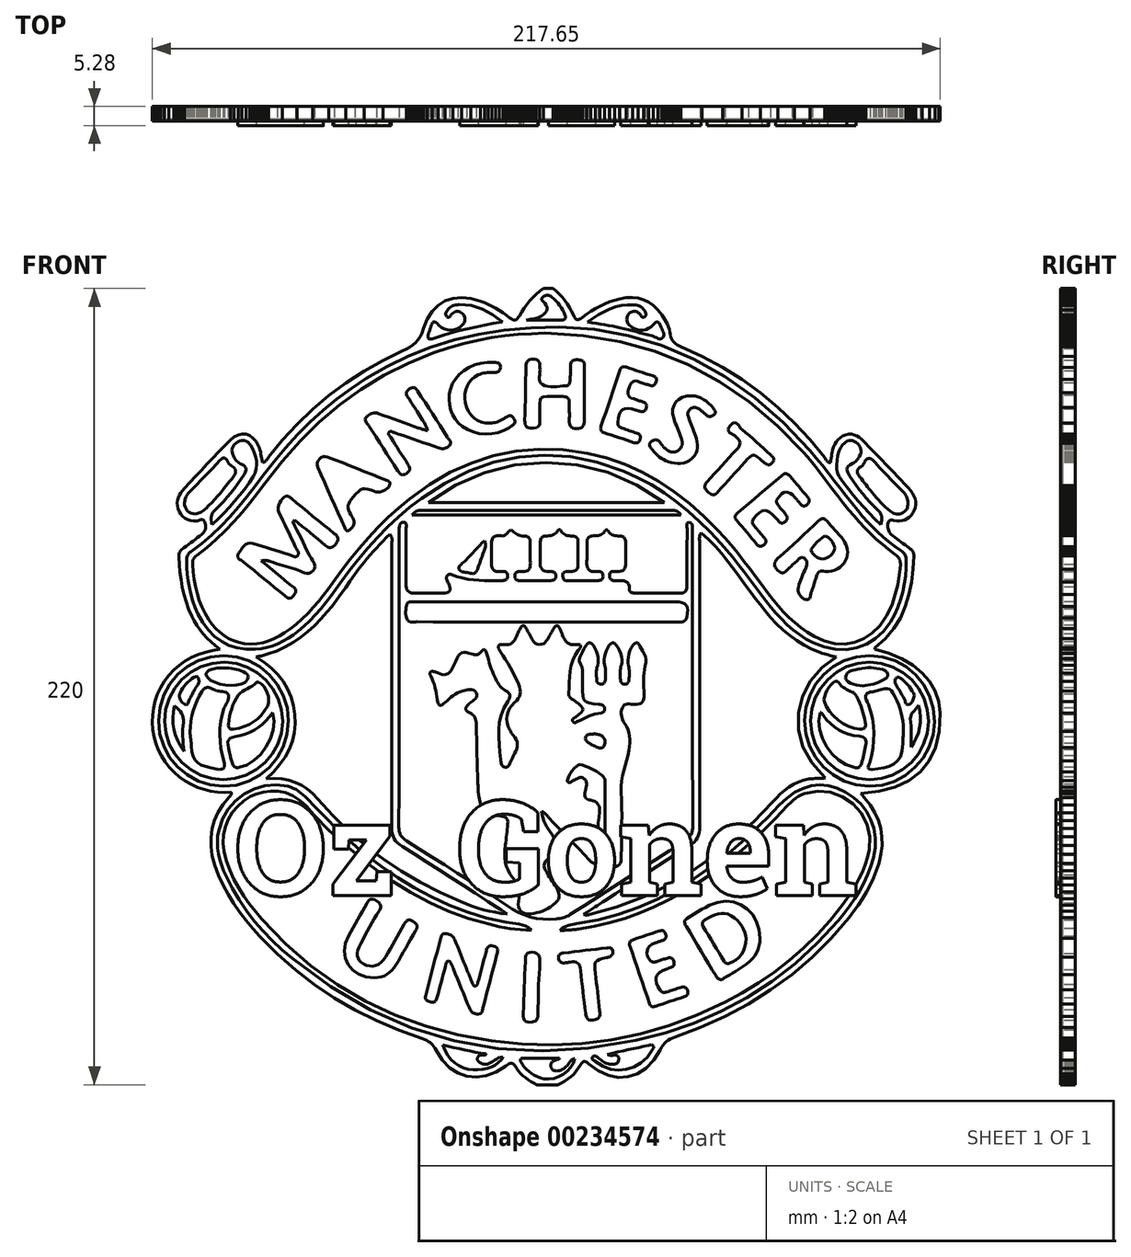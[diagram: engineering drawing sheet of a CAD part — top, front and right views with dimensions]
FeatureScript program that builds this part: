
annotation { "Feature Type Name" : "Feature", "Feature Type Description" : "" }
export const myFeature = defineFeature(function(context is Context, id is Id, definition is map)
    precondition{}
    {
        {
            var Q0;
            Q0=qCreatedBy(makeId("Front.planeOp"),FACE);
            var sketch = newSketch(context, id + "F0", { "sketchPlane" : qUnion([Q0])});
            skLineSegment(sketch, "E0", {"start": v(-1.82, 250) * mm, "end": v(-1.07, 250) * mm});
            skLineSegment(sketch, "E1", {"start": v(-1.07, 250) * mm, "end": v(-0.32, 250) * mm});
            skLineSegment(sketch, "E2", {"start": v(-0.32, 250) * mm, "end": v(0.43, 250) * mm});
            skLineSegment(sketch, "E3", {"start": v(0.43, 250) * mm, "end": v(1.18, 250) * mm});
            skLineSegment(sketch, "E4", {"start": v(1.18, 250) * mm, "end": v(1.93, 250) * mm});
            skLineSegment(sketch, "E5", {"start": v(1.93, 250) * mm, "end": v(2.68, 250) * mm});
            skLineSegment(sketch, "E6", {"start": v(2.68, 250) * mm, "end": v(3.43, 250) * mm});
            skLineSegment(sketch, "E7", {"start": v(3.43, 250) * mm, "end": v(4.18, 250) * mm});
            skLineSegment(sketch, "E8", {"start": v(4.18, 250) * mm, "end": v(6.35, 248.32) * mm});
            skLineSegment(sketch, "E9", {"start": v(6.35, 248.32) * mm, "end": v(8.32, 246.48) * mm});
            skLineSegment(sketch, "E10", {"start": v(8.32, 246.48) * mm, "end": v(10.12, 244.5) * mm});
            skLineSegment(sketch, "E11", {"start": v(10.12, 244.5) * mm, "end": v(11.75, 242.4) * mm});
            skLineSegment(sketch, "E12", {"start": v(11.75, 242.4) * mm, "end": v(13.25, 240.2) * mm});
            skLineSegment(sketch, "E13", {"start": v(13.25, 240.2) * mm, "end": v(14.63, 237.9) * mm});
            skLineSegment(sketch, "E14", {"start": v(14.63, 237.9) * mm, "end": v(15.91, 235.55) * mm});
            skLineSegment(sketch, "E15", {"start": v(15.91, 235.55) * mm, "end": v(17.11, 233.14) * mm});
            skLineSegment(sketch, "E16", {"start": v(17.11, 233.14) * mm, "end": v(17.67, 232.1) * mm});
            skLineSegment(sketch, "E17", {"start": v(17.67, 232.1) * mm, "end": v(18.22, 231.32) * mm});
            skLineSegment(sketch, "E18", {"start": v(18.22, 231.32) * mm, "end": v(18.8, 230.79) * mm});
            skLineSegment(sketch, "E19", {"start": v(18.8, 230.79) * mm, "end": v(19.4, 230.51) * mm});
            skLineSegment(sketch, "E20", {"start": v(19.4, 230.51) * mm, "end": v(20.07, 230.48) * mm});
            skLineSegment(sketch, "E21", {"start": v(20.07, 230.48) * mm, "end": v(20.82, 230.69) * mm});
            skLineSegment(sketch, "E22", {"start": v(20.82, 230.69) * mm, "end": v(21.66, 231.13) * mm});
            skLineSegment(sketch, "E23", {"start": v(21.66, 231.13) * mm, "end": v(22.63, 231.81) * mm});
            skLineSegment(sketch, "E24", {"start": v(22.63, 231.81) * mm, "end": v(25.3, 233.8) * mm});
            skLineSegment(sketch, "E25", {"start": v(25.3, 233.8) * mm, "end": v(28.03, 235.66) * mm});
            skLineSegment(sketch, "E26", {"start": v(28.03, 235.66) * mm, "end": v(30.83, 237.4) * mm});
            skLineSegment(sketch, "E27", {"start": v(30.83, 237.4) * mm, "end": v(33.7, 238.99) * mm});
            skLineSegment(sketch, "E28", {"start": v(33.7, 238.99) * mm, "end": v(36.67, 240.41) * mm});
            skLineSegment(sketch, "E29", {"start": v(36.67, 240.41) * mm, "end": v(39.72, 241.66) * mm});
            skLineSegment(sketch, "E30", {"start": v(39.72, 241.66) * mm, "end": v(42.86, 242.73) * mm});
            skLineSegment(sketch, "E31", {"start": v(42.86, 242.73) * mm, "end": v(46.1, 243.6) * mm});
            skLineSegment(sketch, "E32", {"start": v(46.1, 243.6) * mm, "end": v(50.2, 244.27) * mm});
            skLineSegment(sketch, "E33", {"start": v(50.2, 244.27) * mm, "end": v(54.05, 244.4) * mm});
            skLineSegment(sketch, "E34", {"start": v(54.05, 244.4) * mm, "end": v(57.69, 243.97) * mm});
            skLineSegment(sketch, "E35", {"start": v(57.69, 243.97) * mm, "end": v(61.1, 242.98) * mm});
            skLineSegment(sketch, "E36", {"start": v(61.1, 242.98) * mm, "end": v(64.3, 241.43) * mm});
            skLineSegment(sketch, "E37", {"start": v(64.3, 241.43) * mm, "end": v(67.3, 239.32) * mm});
            skLineSegment(sketch, "E38", {"start": v(67.3, 239.32) * mm, "end": v(70.08, 236.64) * mm});
            skLineSegment(sketch, "E39", {"start": v(70.08, 236.64) * mm, "end": v(72.65, 233.4) * mm});
            skLineSegment(sketch, "E40", {"start": v(72.65, 233.4) * mm, "end": v(73.61, 231.98) * mm});
            skLineSegment(sketch, "E41", {"start": v(73.61, 231.98) * mm, "end": v(74.51, 230.53) * mm});
            skLineSegment(sketch, "E42", {"start": v(74.51, 230.53) * mm, "end": v(75.34, 229.04) * mm});
            skLineSegment(sketch, "E43", {"start": v(75.34, 229.04) * mm, "end": v(76.07, 227.52) * mm});
            skLineSegment(sketch, "E44", {"start": v(76.07, 227.52) * mm, "end": v(76.71, 225.97) * mm});
            skLineSegment(sketch, "E45", {"start": v(76.71, 225.97) * mm, "end": v(77.24, 224.38) * mm});
            skLineSegment(sketch, "E46", {"start": v(77.24, 224.38) * mm, "end": v(77.65, 222.76) * mm});
            skLineSegment(sketch, "E47", {"start": v(77.65, 222.76) * mm, "end": v(77.92, 221.1) * mm});
            skLineSegment(sketch, "E48", {"start": v(77.92, 221.1) * mm, "end": v(78.2, 219.57) * mm});
            skLineSegment(sketch, "E49", {"start": v(78.2, 219.57) * mm, "end": v(78.67, 218.27) * mm});
            skLineSegment(sketch, "E50", {"start": v(78.67, 218.27) * mm, "end": v(79.3, 217.16) * mm});
            skLineSegment(sketch, "E51", {"start": v(79.3, 217.16) * mm, "end": v(80.08, 216.22) * mm});
            skLineSegment(sketch, "E52", {"start": v(80.08, 216.22) * mm, "end": v(81.01, 215.41) * mm});
            skLineSegment(sketch, "E53", {"start": v(81.01, 215.41) * mm, "end": v(82.08, 214.71) * mm});
            skLineSegment(sketch, "E54", {"start": v(82.08, 214.71) * mm, "end": v(83.27, 214.09) * mm});
            skLineSegment(sketch, "E55", {"start": v(83.27, 214.09) * mm, "end": v(84.58, 213.5) * mm});
            skLineSegment(sketch, "E56", {"start": v(84.58, 213.5) * mm, "end": v(97.9, 207.43) * mm});
            skLineSegment(sketch, "E57", {"start": v(97.9, 207.43) * mm, "end": v(110.63, 200.58) * mm});
            skLineSegment(sketch, "E58", {"start": v(110.63, 200.58) * mm, "end": v(122.77, 192.97) * mm});
            skLineSegment(sketch, "E59", {"start": v(122.77, 192.97) * mm, "end": v(134.34, 184.6) * mm});
            skLineSegment(sketch, "E60", {"start": v(134.34, 184.6) * mm, "end": v(145.32, 175.49) * mm});
            skLineSegment(sketch, "E61", {"start": v(145.32, 175.49) * mm, "end": v(155.74, 165.64) * mm});
            skLineSegment(sketch, "E62", {"start": v(155.74, 165.64) * mm, "end": v(165.59, 155.05) * mm});
            skLineSegment(sketch, "E63", {"start": v(165.59, 155.05) * mm, "end": v(174.88, 143.75) * mm});
            skLineSegment(sketch, "E64", {"start": v(174.88, 143.75) * mm, "end": v(175.21, 143.27) * mm});
            skLineSegment(sketch, "E65", {"start": v(175.21, 143.27) * mm, "end": v(175.52, 142.76) * mm});
            skLineSegment(sketch, "E66", {"start": v(175.52, 142.76) * mm, "end": v(175.85, 142.25) * mm});
            skLineSegment(sketch, "E67", {"start": v(175.85, 142.25) * mm, "end": v(176.2, 141.77) * mm});
            skLineSegment(sketch, "E68", {"start": v(176.2, 141.77) * mm, "end": v(176.63, 141.35) * mm});
            skLineSegment(sketch, "E69", {"start": v(176.63, 141.35) * mm, "end": v(177.14, 141.03) * mm});
            skLineSegment(sketch, "E70", {"start": v(177.14, 141.03) * mm, "end": v(177.77, 140.85) * mm});
            skLineSegment(sketch, "E71", {"start": v(177.77, 140.85) * mm, "end": v(178.54, 140.82) * mm});
            skLineSegment(sketch, "E72", {"start": v(178.54, 140.82) * mm, "end": v(178.65, 141.59) * mm});
            skLineSegment(sketch, "E73", {"start": v(178.65, 141.59) * mm, "end": v(178.74, 142.34) * mm});
            skLineSegment(sketch, "E74", {"start": v(178.74, 142.34) * mm, "end": v(178.84, 143.1) * mm});
            skLineSegment(sketch, "E75", {"start": v(178.84, 143.1) * mm, "end": v(178.94, 143.84) * mm});
            skLineSegment(sketch, "E76", {"start": v(178.94, 143.84) * mm, "end": v(179.04, 144.58) * mm});
            skLineSegment(sketch, "E77", {"start": v(179.04, 144.58) * mm, "end": v(179.16, 145.32) * mm});
            skLineSegment(sketch, "E78", {"start": v(179.16, 145.32) * mm, "end": v(179.28, 146.05) * mm});
            skLineSegment(sketch, "E79", {"start": v(179.28, 146.05) * mm, "end": v(179.43, 146.78) * mm});
            skLineSegment(sketch, "E80", {"start": v(179.43, 146.78) * mm, "end": v(179.89, 148.67) * mm});
            skLineSegment(sketch, "E81", {"start": v(179.89, 148.67) * mm, "end": v(180.47, 150.48) * mm});
            skLineSegment(sketch, "E82", {"start": v(180.47, 150.48) * mm, "end": v(181.2, 152.19) * mm});
            skLineSegment(sketch, "E83", {"start": v(181.2, 152.19) * mm, "end": v(182.1, 153.77) * mm});
            skLineSegment(sketch, "E84", {"start": v(182.1, 153.77) * mm, "end": v(183.2, 155.18) * mm});
            skLineSegment(sketch, "E85", {"start": v(183.2, 155.18) * mm, "end": v(184.54, 156.4) * mm});
            skLineSegment(sketch, "E86", {"start": v(184.54, 156.4) * mm, "end": v(186.12, 157.4) * mm});
            skLineSegment(sketch, "E87", {"start": v(186.12, 157.4) * mm, "end": v(187.99, 158.16) * mm});
            skLineSegment(sketch, "E88", {"start": v(187.99, 158.16) * mm, "end": v(189.94, 158.56) * mm});
            skLineSegment(sketch, "E89", {"start": v(189.94, 158.56) * mm, "end": v(191.75, 158.54) * mm});
            skLineSegment(sketch, "E90", {"start": v(191.75, 158.54) * mm, "end": v(193.43, 158.17) * mm});
            skLineSegment(sketch, "E91", {"start": v(193.43, 158.17) * mm, "end": v(195, 157.5) * mm});
            skLineSegment(sketch, "E92", {"start": v(195, 157.5) * mm, "end": v(196.48, 156.57) * mm});
            skLineSegment(sketch, "E93", {"start": v(196.48, 156.57) * mm, "end": v(197.88, 155.44) * mm});
            skLineSegment(sketch, "E94", {"start": v(197.88, 155.44) * mm, "end": v(199.23, 154.18) * mm});
            skLineSegment(sketch, "E95", {"start": v(199.23, 154.18) * mm, "end": v(200.53, 152.83) * mm});
            skLineSegment(sketch, "E96", {"start": v(200.53, 152.83) * mm, "end": v(202.6, 150.65) * mm});
            skLineSegment(sketch, "E97", {"start": v(202.6, 150.65) * mm, "end": v(204.66, 148.48) * mm});
            skLineSegment(sketch, "E98", {"start": v(204.66, 148.48) * mm, "end": v(206.74, 146.32) * mm});
            skLineSegment(sketch, "E99", {"start": v(206.74, 146.32) * mm, "end": v(208.83, 144.17) * mm});
            skLineSegment(sketch, "E100", {"start": v(208.83, 144.17) * mm, "end": v(210.92, 142.01) * mm});
            skLineSegment(sketch, "E101", {"start": v(210.92, 142.01) * mm, "end": v(213, 139.86) * mm});
            skLineSegment(sketch, "E102", {"start": v(213, 139.86) * mm, "end": v(215.09, 137.7) * mm});
            skLineSegment(sketch, "E103", {"start": v(215.09, 137.7) * mm, "end": v(217.16, 135.54) * mm});
            skLineSegment(sketch, "E104", {"start": v(217.16, 135.54) * mm, "end": v(218.63, 134) * mm});
            skLineSegment(sketch, "E105", {"start": v(218.63, 134) * mm, "end": v(220.1, 132.47) * mm});
            skLineSegment(sketch, "E106", {"start": v(220.1, 132.47) * mm, "end": v(221.57, 130.93) * mm});
            skLineSegment(sketch, "E107", {"start": v(221.57, 130.93) * mm, "end": v(223.03, 129.4) * mm});
            skLineSegment(sketch, "E108", {"start": v(223.03, 129.4) * mm, "end": v(224.48, 127.84) * mm});
            skLineSegment(sketch, "E109", {"start": v(224.48, 127.84) * mm, "end": v(225.92, 126.28) * mm});
            skLineSegment(sketch, "E110", {"start": v(225.92, 126.28) * mm, "end": v(227.33, 124.7) * mm});
            skLineSegment(sketch, "E111", {"start": v(227.33, 124.7) * mm, "end": v(228.73, 123.1) * mm});
            skLineSegment(sketch, "E112", {"start": v(228.73, 123.1) * mm, "end": v(229.98, 121.42) * mm});
            skLineSegment(sketch, "E113", {"start": v(229.98, 121.42) * mm, "end": v(230.93, 119.68) * mm});
            skLineSegment(sketch, "E114", {"start": v(230.93, 119.68) * mm, "end": v(231.58, 117.9) * mm});
            skLineSegment(sketch, "E115", {"start": v(231.58, 117.9) * mm, "end": v(231.93, 116.11) * mm});
            skLineSegment(sketch, "E116", {"start": v(231.93, 116.11) * mm, "end": v(231.98, 114.32) * mm});
            skLineSegment(sketch, "E117", {"start": v(231.98, 114.32) * mm, "end": v(231.73, 112.56) * mm});
            skLineSegment(sketch, "E118", {"start": v(231.73, 112.56) * mm, "end": v(231.19, 110.84) * mm});
            skLineSegment(sketch, "E119", {"start": v(231.19, 110.84) * mm, "end": v(230.34, 109.18) * mm});
            skLineSegment(sketch, "E120", {"start": v(230.34, 109.18) * mm, "end": v(229.23, 107.63) * mm});
            skLineSegment(sketch, "E121", {"start": v(229.23, 107.63) * mm, "end": v(228, 106.36) * mm});
            skLineSegment(sketch, "E122", {"start": v(228, 106.36) * mm, "end": v(226.63, 105.37) * mm});
            skLineSegment(sketch, "E123", {"start": v(226.63, 105.37) * mm, "end": v(225.16, 104.65) * mm});
            skLineSegment(sketch, "E124", {"start": v(225.16, 104.65) * mm, "end": v(223.58, 104.2) * mm});
            skLineSegment(sketch, "E125", {"start": v(223.58, 104.2) * mm, "end": v(221.9, 104.02) * mm});
            skLineSegment(sketch, "E126", {"start": v(221.9, 104.02) * mm, "end": v(220.13, 104.1) * mm});
            skLineSegment(sketch, "E127", {"start": v(220.13, 104.1) * mm, "end": v(218.28, 104.43) * mm});
            skLineSegment(sketch, "E128", {"start": v(218.28, 104.43) * mm, "end": v(217.24, 104.62) * mm});
            skLineSegment(sketch, "E129", {"start": v(217.24, 104.62) * mm, "end": v(216.4, 104.63) * mm});
            skLineSegment(sketch, "E130", {"start": v(216.4, 104.63) * mm, "end": v(215.74, 104.47) * mm});
            skLineSegment(sketch, "E131", {"start": v(215.74, 104.47) * mm, "end": v(215.24, 104.14) * mm});
            skLineSegment(sketch, "E132", {"start": v(215.24, 104.14) * mm, "end": v(214.87, 103.64) * mm});
            skLineSegment(sketch, "E133", {"start": v(214.87, 103.64) * mm, "end": v(214.63, 102.98) * mm});
            skLineSegment(sketch, "E134", {"start": v(214.63, 102.98) * mm, "end": v(214.5, 102.15) * mm});
            skLineSegment(sketch, "E135", {"start": v(214.5, 102.15) * mm, "end": v(214.46, 101.17) * mm});
            skLineSegment(sketch, "E136", {"start": v(214.46, 101.17) * mm, "end": v(214.5, 100.17) * mm});
            skLineSegment(sketch, "E137", {"start": v(214.5, 100.17) * mm, "end": v(214.63, 99.22) * mm});
            skLineSegment(sketch, "E138", {"start": v(214.63, 99.22) * mm, "end": v(214.86, 98.34) * mm});
            skLineSegment(sketch, "E139", {"start": v(214.86, 98.34) * mm, "end": v(215.19, 97.52) * mm});
            skLineSegment(sketch, "E140", {"start": v(215.19, 97.52) * mm, "end": v(215.62, 96.75) * mm});
            skLineSegment(sketch, "E141", {"start": v(215.62, 96.75) * mm, "end": v(216.16, 96.03) * mm});
            skLineSegment(sketch, "E142", {"start": v(216.16, 96.03) * mm, "end": v(216.8, 95.36) * mm});
            skLineSegment(sketch, "E143", {"start": v(216.8, 95.36) * mm, "end": v(217.56, 94.74) * mm});
            skLineSegment(sketch, "E144", {"start": v(217.56, 94.74) * mm, "end": v(218.86, 93.78) * mm});
            skLineSegment(sketch, "E145", {"start": v(218.86, 93.78) * mm, "end": v(220.16, 92.8) * mm});
            skLineSegment(sketch, "E146", {"start": v(220.16, 92.8) * mm, "end": v(221.46, 91.83) * mm});
            skLineSegment(sketch, "E147", {"start": v(221.46, 91.83) * mm, "end": v(222.76, 90.86) * mm});
            skLineSegment(sketch, "E148", {"start": v(222.76, 90.86) * mm, "end": v(224.07, 89.9) * mm});
            skLineSegment(sketch, "E149", {"start": v(224.07, 89.9) * mm, "end": v(225.38, 88.93) * mm});
            skLineSegment(sketch, "E150", {"start": v(225.38, 88.93) * mm, "end": v(226.7, 87.98) * mm});
            skLineSegment(sketch, "E151", {"start": v(226.7, 87.98) * mm, "end": v(228.02, 87.04) * mm});
            skLineSegment(sketch, "E152", {"start": v(228.02, 87.04) * mm, "end": v(228.65, 86.57) * mm});
            skLineSegment(sketch, "E153", {"start": v(228.65, 86.57) * mm, "end": v(229.21, 86.07) * mm});
            skLineSegment(sketch, "E154", {"start": v(229.21, 86.07) * mm, "end": v(229.7, 85.54) * mm});
            skLineSegment(sketch, "E155", {"start": v(229.7, 85.54) * mm, "end": v(230.1, 84.98) * mm});
            skLineSegment(sketch, "E156", {"start": v(230.1, 84.98) * mm, "end": v(230.42, 84.36) * mm});
            skLineSegment(sketch, "E157", {"start": v(230.42, 84.36) * mm, "end": v(230.65, 83.69) * mm});
            skLineSegment(sketch, "E158", {"start": v(230.65, 83.69) * mm, "end": v(230.77, 82.95) * mm});
            skLineSegment(sketch, "E159", {"start": v(230.77, 82.95) * mm, "end": v(230.8, 82.13) * mm});
            skLineSegment(sketch, "E160", {"start": v(230.8, 82.13) * mm, "end": v(230.27, 73.86) * mm});
            skLineSegment(sketch, "E161", {"start": v(230.27, 73.86) * mm, "end": v(229.3, 65.78) * mm});
            skLineSegment(sketch, "E162", {"start": v(229.3, 65.78) * mm, "end": v(227.74, 57.94) * mm});
            skLineSegment(sketch, "E163", {"start": v(227.74, 57.94) * mm, "end": v(225.46, 50.41) * mm});
            skLineSegment(sketch, "E164", {"start": v(225.46, 50.41) * mm, "end": v(222.33, 43.24) * mm});
            skLineSegment(sketch, "E165", {"start": v(222.33, 43.24) * mm, "end": v(218.2, 36.5) * mm});
            skLineSegment(sketch, "E166", {"start": v(218.2, 36.5) * mm, "end": v(212.95, 30.22) * mm});
            skLineSegment(sketch, "E167", {"start": v(212.95, 30.22) * mm, "end": v(206.43, 24.48) * mm});
            skLineSegment(sketch, "E168", {"start": v(206.43, 24.48) * mm, "end": v(206.4, 24.42) * mm});
            skLineSegment(sketch, "E169", {"start": v(206.4, 24.42) * mm, "end": v(206.37, 24.33) * mm});
            skLineSegment(sketch, "E170", {"start": v(206.37, 24.33) * mm, "end": v(206.36, 24.23) * mm});
            skLineSegment(sketch, "E171", {"start": v(206.36, 24.23) * mm, "end": v(206.37, 24.1) * mm});
            skLineSegment(sketch, "E172", {"start": v(206.37, 24.1) * mm, "end": v(206.38, 23.97) * mm});
            skLineSegment(sketch, "E173", {"start": v(206.38, 23.97) * mm, "end": v(206.4, 23.84) * mm});
            skLineSegment(sketch, "E174", {"start": v(206.4, 23.84) * mm, "end": v(206.41, 23.7) * mm});
            skLineSegment(sketch, "E175", {"start": v(206.41, 23.7) * mm, "end": v(206.42, 23.59) * mm});
            skLineSegment(sketch, "E176", {"start": v(206.42, 23.59) * mm, "end": v(215.37, 20.89) * mm});
            skLineSegment(sketch, "E177", {"start": v(215.37, 20.89) * mm, "end": v(223.34, 17.47) * mm});
            skLineSegment(sketch, "E178", {"start": v(223.34, 17.47) * mm, "end": v(230.25, 13.37) * mm});
            skLineSegment(sketch, "E179", {"start": v(230.25, 13.37) * mm, "end": v(236.07, 8.6) * mm});
            skLineSegment(sketch, "E180", {"start": v(236.07, 8.6) * mm, "end": v(240.74, 3.21) * mm});
            skLineSegment(sketch, "E181", {"start": v(240.74, 3.21) * mm, "end": v(244.21, -2.78) * mm});
            skLineSegment(sketch, "E182", {"start": v(244.21, -2.78) * mm, "end": v(246.42, -9.36) * mm});
            skLineSegment(sketch, "E183", {"start": v(246.42, -9.36) * mm, "end": v(247.33, -16.48) * mm});
            skLineSegment(sketch, "E184", {"start": v(247.33, -16.48) * mm, "end": v(246.81, -28.2) * mm});
            skLineSegment(sketch, "E185", {"start": v(246.81, -28.2) * mm, "end": v(244.5, -38.26) * mm});
            skLineSegment(sketch, "E186", {"start": v(244.5, -38.26) * mm, "end": v(240.48, -46.7) * mm});
            skLineSegment(sketch, "E187", {"start": v(240.48, -46.7) * mm, "end": v(234.83, -53.6) * mm});
            skLineSegment(sketch, "E188", {"start": v(234.83, -53.6) * mm, "end": v(227.62, -59.01) * mm});
            skLineSegment(sketch, "E189", {"start": v(227.62, -59.01) * mm, "end": v(218.93, -63) * mm});
            skLineSegment(sketch, "E190", {"start": v(218.93, -63) * mm, "end": v(208.85, -65.66) * mm});
            skLineSegment(sketch, "E191", {"start": v(208.85, -65.66) * mm, "end": v(197.45, -67.02) * mm});
            skLineSegment(sketch, "E192", {"start": v(197.45, -67.02) * mm, "end": v(197.8, -67.44) * mm});
            skLineSegment(sketch, "E193", {"start": v(197.8, -67.44) * mm, "end": v(198.13, -67.83) * mm});
            skLineSegment(sketch, "E194", {"start": v(198.13, -67.83) * mm, "end": v(198.43, -68.19) * mm});
            skLineSegment(sketch, "E195", {"start": v(198.43, -68.19) * mm, "end": v(198.72, -68.52) * mm});
            skLineSegment(sketch, "E196", {"start": v(198.72, -68.52) * mm, "end": v(198.98, -68.83) * mm});
            skLineSegment(sketch, "E197", {"start": v(198.98, -68.83) * mm, "end": v(199.23, -69.12) * mm});
            skLineSegment(sketch, "E198", {"start": v(199.23, -69.12) * mm, "end": v(199.48, -69.4) * mm});
            skLineSegment(sketch, "E199", {"start": v(199.48, -69.4) * mm, "end": v(199.72, -69.69) * mm});
            skLineSegment(sketch, "E200", {"start": v(199.72, -69.69) * mm, "end": v(203.35, -74.31) * mm});
            skLineSegment(sketch, "E201", {"start": v(203.35, -74.31) * mm, "end": v(206.27, -79.1) * mm});
            skLineSegment(sketch, "E202", {"start": v(206.27, -79.1) * mm, "end": v(208.5, -84.03) * mm});
            skLineSegment(sketch, "E203", {"start": v(208.5, -84.03) * mm, "end": v(210, -89.12) * mm});
            skLineSegment(sketch, "E204", {"start": v(210, -89.12) * mm, "end": v(210.79, -94.36) * mm});
            skLineSegment(sketch, "E205", {"start": v(210.79, -94.36) * mm, "end": v(210.85, -99.77) * mm});
            skLineSegment(sketch, "E206", {"start": v(210.85, -99.77) * mm, "end": v(210.17, -105.33) * mm});
            skLineSegment(sketch, "E207", {"start": v(210.17, -105.33) * mm, "end": v(208.76, -111.06) * mm});
            skLineSegment(sketch, "E208", {"start": v(208.76, -111.06) * mm, "end": v(207.18, -115.72) * mm});
            skLineSegment(sketch, "E209", {"start": v(207.18, -115.72) * mm, "end": v(205.34, -120.24) * mm});
            skLineSegment(sketch, "E210", {"start": v(205.34, -120.24) * mm, "end": v(203.28, -124.64) * mm});
            skLineSegment(sketch, "E211", {"start": v(203.28, -124.64) * mm, "end": v(201, -128.92) * mm});
            skLineSegment(sketch, "E212", {"start": v(201, -128.92) * mm, "end": v(198.52, -133.1) * mm});
            skLineSegment(sketch, "E213", {"start": v(198.52, -133.1) * mm, "end": v(195.86, -137.16) * mm});
            skLineSegment(sketch, "E214", {"start": v(195.86, -137.16) * mm, "end": v(193.03, -141.13) * mm});
            skLineSegment(sketch, "E215", {"start": v(193.03, -141.13) * mm, "end": v(190.05, -145) * mm});
            skLineSegment(sketch, "E216", {"start": v(190.05, -145) * mm, "end": v(178.88, -158) * mm});
            skLineSegment(sketch, "E217", {"start": v(178.88, -158) * mm, "end": v(166.95, -169.88) * mm});
            skLineSegment(sketch, "E218", {"start": v(166.95, -169.88) * mm, "end": v(154.27, -180.7) * mm});
            skLineSegment(sketch, "E219", {"start": v(154.27, -180.7) * mm, "end": v(140.89, -190.48) * mm});
            skLineSegment(sketch, "E220", {"start": v(140.89, -190.48) * mm, "end": v(126.82, -199.28) * mm});
            skLineSegment(sketch, "E221", {"start": v(126.82, -199.28) * mm, "end": v(112.1, -207.11) * mm});
            skLineSegment(sketch, "E222", {"start": v(112.1, -207.11) * mm, "end": v(96.75, -214.04) * mm});
            skLineSegment(sketch, "E223", {"start": v(96.75, -214.04) * mm, "end": v(80.8, -220.09) * mm});
            skLineSegment(sketch, "E224", {"start": v(80.8, -220.09) * mm, "end": v(79.23, -220.7) * mm});
            skLineSegment(sketch, "E225", {"start": v(79.23, -220.7) * mm, "end": v(77.8, -221.38) * mm});
            skLineSegment(sketch, "E226", {"start": v(77.8, -221.38) * mm, "end": v(76.48, -222.16) * mm});
            skLineSegment(sketch, "E227", {"start": v(76.48, -222.16) * mm, "end": v(75.29, -223.05) * mm});
            skLineSegment(sketch, "E228", {"start": v(75.29, -223.05) * mm, "end": v(74.2, -224.07) * mm});
            skLineSegment(sketch, "E229", {"start": v(74.2, -224.07) * mm, "end": v(73.2, -225.24) * mm});
            skLineSegment(sketch, "E230", {"start": v(73.2, -225.24) * mm, "end": v(72.3, -226.56) * mm});
            skLineSegment(sketch, "E231", {"start": v(72.3, -226.56) * mm, "end": v(71.45, -228.06) * mm});
            skLineSegment(sketch, "E232", {"start": v(71.45, -228.06) * mm, "end": v(67.36, -234.57) * mm});
            skLineSegment(sketch, "E233", {"start": v(67.36, -234.57) * mm, "end": v(62.56, -239.57) * mm});
            skLineSegment(sketch, "E234", {"start": v(62.56, -239.57) * mm, "end": v(57.18, -243.06) * mm});
            skLineSegment(sketch, "E235", {"start": v(57.18, -243.06) * mm, "end": v(51.36, -245) * mm});
            skLineSegment(sketch, "E236", {"start": v(51.36, -245) * mm, "end": v(45.24, -245.35) * mm});
            skLineSegment(sketch, "E237", {"start": v(45.24, -245.35) * mm, "end": v(38.96, -244.12) * mm});
            skLineSegment(sketch, "E238", {"start": v(38.96, -244.12) * mm, "end": v(32.65, -241.26) * mm});
            skLineSegment(sketch, "E239", {"start": v(32.65, -241.26) * mm, "end": v(26.46, -236.75) * mm});
            skLineSegment(sketch, "E240", {"start": v(26.46, -236.75) * mm, "end": v(25.64, -236.1) * mm});
            skLineSegment(sketch, "E241", {"start": v(25.64, -236.1) * mm, "end": v(24.92, -235.64) * mm});
            skLineSegment(sketch, "E242", {"start": v(24.92, -235.64) * mm, "end": v(24.27, -235.4) * mm});
            skLineSegment(sketch, "E243", {"start": v(24.27, -235.4) * mm, "end": v(23.68, -235.38) * mm});
            skLineSegment(sketch, "E244", {"start": v(23.68, -235.38) * mm, "end": v(23.13, -235.57) * mm});
            skLineSegment(sketch, "E245", {"start": v(23.13, -235.57) * mm, "end": v(22.6, -235.98) * mm});
            skLineSegment(sketch, "E246", {"start": v(22.6, -235.98) * mm, "end": v(22.1, -236.6) * mm});
            skLineSegment(sketch, "E247", {"start": v(22.1, -236.6) * mm, "end": v(21.57, -237.43) * mm});
            skLineSegment(sketch, "E248", {"start": v(21.57, -237.43) * mm, "end": v(20.25, -239.55) * mm});
            skLineSegment(sketch, "E249", {"start": v(20.25, -239.55) * mm, "end": v(18.8, -241.51) * mm});
            skLineSegment(sketch, "E250", {"start": v(18.8, -241.51) * mm, "end": v(17.21, -243.32) * mm});
            skLineSegment(sketch, "E251", {"start": v(17.21, -243.32) * mm, "end": v(15.48, -244.98) * mm});
            skLineSegment(sketch, "E252", {"start": v(15.48, -244.98) * mm, "end": v(13.62, -246.47) * mm});
            skLineSegment(sketch, "E253", {"start": v(13.62, -246.47) * mm, "end": v(11.61, -247.81) * mm});
            skLineSegment(sketch, "E254", {"start": v(11.61, -247.81) * mm, "end": v(9.47, -248.99) * mm});
            skLineSegment(sketch, "E255", {"start": v(9.47, -248.99) * mm, "end": v(7.18, -250) * mm});
            skLineSegment(sketch, "E256", {"start": v(7.18, -250) * mm, "end": v(5.55, -250) * mm});
            skLineSegment(sketch, "E257", {"start": v(5.55, -250) * mm, "end": v(3.93, -250) * mm});
            skLineSegment(sketch, "E258", {"start": v(3.93, -250) * mm, "end": v(2.3, -250) * mm});
            skLineSegment(sketch, "E259", {"start": v(2.3, -250) * mm, "end": v(0.68, -250) * mm});
            skLineSegment(sketch, "E260", {"start": v(0.68, -250) * mm, "end": v(-0.95, -250) * mm});
            skLineSegment(sketch, "E261", {"start": v(-0.95, -250) * mm, "end": v(-2.57, -250) * mm});
            skLineSegment(sketch, "E262", {"start": v(-2.57, -250) * mm, "end": v(-4.2, -250) * mm});
            skLineSegment(sketch, "E263", {"start": v(-4.2, -250) * mm, "end": v(-5.82, -250) * mm});
            skLineSegment(sketch, "E264", {"start": v(-5.82, -250) * mm, "end": v(-7.73, -249.02) * mm});
            skLineSegment(sketch, "E265", {"start": v(-7.73, -249.02) * mm, "end": v(-9.6, -247.98) * mm});
            skLineSegment(sketch, "E266", {"start": v(-9.6, -247.98) * mm, "end": v(-11.4, -246.85) * mm});
            skLineSegment(sketch, "E267", {"start": v(-11.4, -246.85) * mm, "end": v(-13.1, -245.62) * mm});
            skLineSegment(sketch, "E268", {"start": v(-13.1, -245.62) * mm, "end": v(-14.71, -244.27) * mm});
            skLineSegment(sketch, "E269", {"start": v(-14.71, -244.27) * mm, "end": v(-16.2, -242.79) * mm});
            skLineSegment(sketch, "E270", {"start": v(-16.2, -242.79) * mm, "end": v(-17.56, -241.15) * mm});
            skLineSegment(sketch, "E271", {"start": v(-17.56, -241.15) * mm, "end": v(-18.76, -239.35) * mm});
            skLineSegment(sketch, "E272", {"start": v(-18.76, -239.35) * mm, "end": v(-19.5, -238.22) * mm});
            skLineSegment(sketch, "E273", {"start": v(-19.5, -238.22) * mm, "end": v(-20.22, -237.38) * mm});
            skLineSegment(sketch, "E274", {"start": v(-20.22, -237.38) * mm, "end": v(-20.94, -236.83) * mm});
            skLineSegment(sketch, "E275", {"start": v(-20.94, -236.83) * mm, "end": v(-21.7, -236.56) * mm});
            skLineSegment(sketch, "E276", {"start": v(-21.7, -236.56) * mm, "end": v(-22.52, -236.58) * mm});
            skLineSegment(sketch, "E277", {"start": v(-22.52, -236.58) * mm, "end": v(-23.42, -236.86) * mm});
            skLineSegment(sketch, "E278", {"start": v(-23.42, -236.86) * mm, "end": v(-24.43, -237.43) * mm});
            skLineSegment(sketch, "E279", {"start": v(-24.43, -237.43) * mm, "end": v(-25.6, -238.25) * mm});
            skLineSegment(sketch, "E280", {"start": v(-25.6, -238.25) * mm, "end": v(-31.66, -242.1) * mm});
            skLineSegment(sketch, "E281", {"start": v(-31.66, -242.1) * mm, "end": v(-37.85, -244.44) * mm});
            skLineSegment(sketch, "E282", {"start": v(-37.85, -244.44) * mm, "end": v(-44, -245.3) * mm});
            skLineSegment(sketch, "E283", {"start": v(-44, -245.3) * mm, "end": v(-49.95, -244.7) * mm});
            skLineSegment(sketch, "E284", {"start": v(-49.95, -244.7) * mm, "end": v(-55.6, -242.7) * mm});
            skLineSegment(sketch, "E285", {"start": v(-55.6, -242.7) * mm, "end": v(-60.75, -239.3) * mm});
            skLineSegment(sketch, "E286", {"start": v(-60.75, -239.3) * mm, "end": v(-65.3, -234.55) * mm});
            skLineSegment(sketch, "E287", {"start": v(-65.3, -234.55) * mm, "end": v(-69.08, -228.5) * mm});
            skLineSegment(sketch, "E288", {"start": v(-69.08, -228.5) * mm, "end": v(-69.88, -227.04) * mm});
            skLineSegment(sketch, "E289", {"start": v(-69.88, -227.04) * mm, "end": v(-70.76, -225.77) * mm});
            skLineSegment(sketch, "E290", {"start": v(-70.76, -225.77) * mm, "end": v(-71.72, -224.66) * mm});
            skLineSegment(sketch, "E291", {"start": v(-71.72, -224.66) * mm, "end": v(-72.77, -223.7) * mm});
            skLineSegment(sketch, "E292", {"start": v(-72.77, -223.7) * mm, "end": v(-73.92, -222.85) * mm});
            skLineSegment(sketch, "E293", {"start": v(-73.92, -222.85) * mm, "end": v(-75.2, -222.12) * mm});
            skLineSegment(sketch, "E294", {"start": v(-75.2, -222.12) * mm, "end": v(-76.59, -221.48) * mm});
            skLineSegment(sketch, "E295", {"start": v(-76.59, -221.48) * mm, "end": v(-78.12, -220.92) * mm});
            skLineSegment(sketch, "E296", {"start": v(-78.12, -220.92) * mm, "end": v(-92.57, -215.7) * mm});
            skLineSegment(sketch, "E297", {"start": v(-92.57, -215.7) * mm, "end": v(-106.56, -209.72) * mm});
            skLineSegment(sketch, "E298", {"start": v(-106.56, -209.72) * mm, "end": v(-120.06, -202.97) * mm});
            skLineSegment(sketch, "E299", {"start": v(-120.06, -202.97) * mm, "end": v(-133.06, -195.41) * mm});
            skLineSegment(sketch, "E300", {"start": v(-133.06, -195.41) * mm, "end": v(-145.55, -187.05) * mm});
            skLineSegment(sketch, "E301", {"start": v(-145.55, -187.05) * mm, "end": v(-157.51, -177.85) * mm});
            skLineSegment(sketch, "E302", {"start": v(-157.51, -177.85) * mm, "end": v(-168.93, -167.8) * mm});
            skLineSegment(sketch, "E303", {"start": v(-168.93, -167.8) * mm, "end": v(-179.79, -156.87) * mm});
            skLineSegment(sketch, "E304", {"start": v(-179.79, -156.87) * mm, "end": v(-184.29, -151.88) * mm});
            skLineSegment(sketch, "E305", {"start": v(-184.29, -151.88) * mm, "end": v(-188.59, -146.76) * mm});
            skLineSegment(sketch, "E306", {"start": v(-188.59, -146.76) * mm, "end": v(-192.65, -141.48) * mm});
            skLineSegment(sketch, "E307", {"start": v(-192.65, -141.48) * mm, "end": v(-196.44, -136.03) * mm});
            skLineSegment(sketch, "E308", {"start": v(-196.44, -136.03) * mm, "end": v(-199.93, -130.38) * mm});
            skLineSegment(sketch, "E309", {"start": v(-199.93, -130.38) * mm, "end": v(-203.08, -124.5) * mm});
            skLineSegment(sketch, "E310", {"start": v(-203.08, -124.5) * mm, "end": v(-205.85, -118.4) * mm});
            skLineSegment(sketch, "E311", {"start": v(-205.85, -118.4) * mm, "end": v(-208.22, -112.05) * mm});
            skLineSegment(sketch, "E312", {"start": v(-208.22, -112.05) * mm, "end": v(-209.8, -106.13) * mm});
            skLineSegment(sketch, "E313", {"start": v(-209.8, -106.13) * mm, "end": v(-210.6, -100.4) * mm});
            skLineSegment(sketch, "E314", {"start": v(-210.6, -100.4) * mm, "end": v(-210.62, -94.81) * mm});
            skLineSegment(sketch, "E315", {"start": v(-210.62, -94.81) * mm, "end": v(-209.86, -89.4) * mm});
            skLineSegment(sketch, "E316", {"start": v(-209.86, -89.4) * mm, "end": v(-208.33, -84.15) * mm});
            skLineSegment(sketch, "E317", {"start": v(-208.33, -84.15) * mm, "end": v(-206.03, -79.07) * mm});
            skLineSegment(sketch, "E318", {"start": v(-206.03, -79.07) * mm, "end": v(-202.97, -74.14) * mm});
            skLineSegment(sketch, "E319", {"start": v(-202.97, -74.14) * mm, "end": v(-199.15, -69.38) * mm});
            skLineSegment(sketch, "E320", {"start": v(-199.15, -69.38) * mm, "end": v(-198.9, -69.12) * mm});
            skLineSegment(sketch, "E321", {"start": v(-198.9, -69.12) * mm, "end": v(-198.63, -68.86) * mm});
            skLineSegment(sketch, "E322", {"start": v(-198.63, -68.86) * mm, "end": v(-198.37, -68.58) * mm});
            skLineSegment(sketch, "E323", {"start": v(-198.37, -68.58) * mm, "end": v(-198.13, -68.28) * mm});
            skLineSegment(sketch, "E324", {"start": v(-198.13, -68.28) * mm, "end": v(-197.94, -67.92) * mm});
            skLineSegment(sketch, "E325", {"start": v(-197.94, -67.92) * mm, "end": v(-197.8, -67.5) * mm});
            skLineSegment(sketch, "E326", {"start": v(-197.8, -67.5) * mm, "end": v(-197.75, -66.98) * mm});
            skLineSegment(sketch, "E327", {"start": v(-197.75, -66.98) * mm, "end": v(-197.8, -66.37) * mm});
            skLineSegment(sketch, "E328", {"start": v(-197.8, -66.37) * mm, "end": v(-202.2, -66.42) * mm});
            skLineSegment(sketch, "E329", {"start": v(-202.2, -66.42) * mm, "end": v(-206.53, -66.15) * mm});
            skLineSegment(sketch, "E330", {"start": v(-206.53, -66.15) * mm, "end": v(-210.76, -65.54) * mm});
            skLineSegment(sketch, "E331", {"start": v(-210.76, -65.54) * mm, "end": v(-214.9, -64.57) * mm});
            skLineSegment(sketch, "E332", {"start": v(-214.9, -64.57) * mm, "end": v(-218.93, -63.22) * mm});
            skLineSegment(sketch, "E333", {"start": v(-218.93, -63.22) * mm, "end": v(-222.84, -61.46) * mm});
            skLineSegment(sketch, "E334", {"start": v(-222.84, -61.46) * mm, "end": v(-226.63, -59.29) * mm});
            skLineSegment(sketch, "E335", {"start": v(-226.63, -59.29) * mm, "end": v(-230.28, -56.67) * mm});
            skLineSegment(sketch, "E336", {"start": v(-230.28, -56.67) * mm, "end": v(-233.7, -53.7) * mm});
            skLineSegment(sketch, "E337", {"start": v(-233.7, -53.7) * mm, "end": v(-236.75, -50.53) * mm});
            skLineSegment(sketch, "E338", {"start": v(-236.75, -50.53) * mm, "end": v(-239.44, -47.14) * mm});
            skLineSegment(sketch, "E339", {"start": v(-239.44, -47.14) * mm, "end": v(-241.74, -43.54) * mm});
            skLineSegment(sketch, "E340", {"start": v(-241.74, -43.54) * mm, "end": v(-243.66, -39.73) * mm});
            skLineSegment(sketch, "E341", {"start": v(-243.66, -39.73) * mm, "end": v(-245.18, -35.7) * mm});
            skLineSegment(sketch, "E342", {"start": v(-245.18, -35.7) * mm, "end": v(-246.3, -31.46) * mm});
            skLineSegment(sketch, "E343", {"start": v(-246.3, -31.46) * mm, "end": v(-247.02, -27) * mm});
            skLineSegment(sketch, "E344", {"start": v(-247.02, -27) * mm, "end": v(-247.33, -22.33) * mm});
            skLineSegment(sketch, "E345", {"start": v(-247.33, -22.33) * mm, "end": v(-247.22, -17.76) * mm});
            skLineSegment(sketch, "E346", {"start": v(-247.22, -17.76) * mm, "end": v(-246.66, -13.3) * mm});
            skLineSegment(sketch, "E347", {"start": v(-246.66, -13.3) * mm, "end": v(-245.66, -8.97) * mm});
            skLineSegment(sketch, "E348", {"start": v(-245.66, -8.97) * mm, "end": v(-244.21, -4.77) * mm});
            skLineSegment(sketch, "E349", {"start": v(-244.21, -4.77) * mm, "end": v(-242.3, -0.7) * mm});
            skLineSegment(sketch, "E350", {"start": v(-242.3, -0.7) * mm, "end": v(-239.92, 3.25) * mm});
            skLineSegment(sketch, "E351", {"start": v(-239.92, 3.25) * mm, "end": v(-237.07, 7.04) * mm});
            skLineSegment(sketch, "E352", {"start": v(-237.07, 7.04) * mm, "end": v(-233.89, 10.49) * mm});
            skLineSegment(sketch, "E353", {"start": v(-233.89, 10.49) * mm, "end": v(-230.46, 13.5) * mm});
            skLineSegment(sketch, "E354", {"start": v(-230.46, 13.5) * mm, "end": v(-226.8, 16.08) * mm});
            skLineSegment(sketch, "E355", {"start": v(-226.8, 16.08) * mm, "end": v(-222.88, 18.29) * mm});
            skLineSegment(sketch, "E356", {"start": v(-222.88, 18.29) * mm, "end": v(-218.73, 20.12) * mm});
            skLineSegment(sketch, "E357", {"start": v(-218.73, 20.12) * mm, "end": v(-214.35, 21.6) * mm});
            skLineSegment(sketch, "E358", {"start": v(-214.35, 21.6) * mm, "end": v(-209.73, 22.78) * mm});
            skLineSegment(sketch, "E359", {"start": v(-209.73, 22.78) * mm, "end": v(-204.87, 23.65) * mm});
            skLineSegment(sketch, "E360", {"start": v(-204.87, 23.65) * mm, "end": v(-207.88, 25.84) * mm});
            skLineSegment(sketch, "E361", {"start": v(-207.88, 25.84) * mm, "end": v(-210.62, 28.14) * mm});
            skLineSegment(sketch, "E362", {"start": v(-210.62, 28.14) * mm, "end": v(-213.12, 30.54) * mm});
            skLineSegment(sketch, "E363", {"start": v(-213.12, 30.54) * mm, "end": v(-215.4, 33.06) * mm});
            skLineSegment(sketch, "E364", {"start": v(-215.4, 33.06) * mm, "end": v(-217.47, 35.69) * mm});
            skLineSegment(sketch, "E365", {"start": v(-217.47, 35.69) * mm, "end": v(-219.34, 38.43) * mm});
            skLineSegment(sketch, "E366", {"start": v(-219.34, 38.43) * mm, "end": v(-221.04, 41.3) * mm});
            skLineSegment(sketch, "E367", {"start": v(-221.04, 41.3) * mm, "end": v(-222.58, 44.27) * mm});
            skLineSegment(sketch, "E368", {"start": v(-222.58, 44.27) * mm, "end": v(-224.53, 48.73) * mm});
            skLineSegment(sketch, "E369", {"start": v(-224.53, 48.73) * mm, "end": v(-226.15, 53.27) * mm});
            skLineSegment(sketch, "E370", {"start": v(-226.15, 53.27) * mm, "end": v(-227.48, 57.86) * mm});
            skLineSegment(sketch, "E371", {"start": v(-227.48, 57.86) * mm, "end": v(-228.53, 62.52) * mm});
            skLineSegment(sketch, "E372", {"start": v(-228.53, 62.52) * mm, "end": v(-229.36, 67.23) * mm});
            skLineSegment(sketch, "E373", {"start": v(-229.36, 67.23) * mm, "end": v(-229.98, 71.99) * mm});
            skLineSegment(sketch, "E374", {"start": v(-229.98, 71.99) * mm, "end": v(-230.43, 76.78) * mm});
            skLineSegment(sketch, "E375", {"start": v(-230.43, 76.78) * mm, "end": v(-230.75, 81.6) * mm});
            skLineSegment(sketch, "E376", {"start": v(-230.75, 81.6) * mm, "end": v(-230.73, 82.55) * mm});
            skLineSegment(sketch, "E377", {"start": v(-230.73, 82.55) * mm, "end": v(-230.58, 83.41) * mm});
            skLineSegment(sketch, "E378", {"start": v(-230.58, 83.41) * mm, "end": v(-230.3, 84.2) * mm});
            skLineSegment(sketch, "E379", {"start": v(-230.3, 84.2) * mm, "end": v(-229.92, 84.9) * mm});
            skLineSegment(sketch, "E380", {"start": v(-229.92, 84.9) * mm, "end": v(-229.43, 85.56) * mm});
            skLineSegment(sketch, "E381", {"start": v(-229.43, 85.56) * mm, "end": v(-228.84, 86.17) * mm});
            skLineSegment(sketch, "E382", {"start": v(-228.84, 86.17) * mm, "end": v(-228.17, 86.74) * mm});
            skLineSegment(sketch, "E383", {"start": v(-228.17, 86.74) * mm, "end": v(-227.44, 87.3) * mm});
            skLineSegment(sketch, "E384", {"start": v(-227.44, 87.3) * mm, "end": v(-226.01, 88.3) * mm});
            skLineSegment(sketch, "E385", {"start": v(-226.01, 88.3) * mm, "end": v(-224.6, 89.33) * mm});
            skLineSegment(sketch, "E386", {"start": v(-224.6, 89.33) * mm, "end": v(-223.19, 90.37) * mm});
            skLineSegment(sketch, "E387", {"start": v(-223.19, 90.37) * mm, "end": v(-221.79, 91.42) * mm});
            skLineSegment(sketch, "E388", {"start": v(-221.79, 91.42) * mm, "end": v(-220.4, 92.47) * mm});
            skLineSegment(sketch, "E389", {"start": v(-220.4, 92.47) * mm, "end": v(-219.01, 93.54) * mm});
            skLineSegment(sketch, "E390", {"start": v(-219.01, 93.54) * mm, "end": v(-217.63, 94.62) * mm});
            skLineSegment(sketch, "E391", {"start": v(-217.63, 94.62) * mm, "end": v(-216.27, 95.7) * mm});
            skLineSegment(sketch, "E392", {"start": v(-216.27, 95.7) * mm, "end": v(-215.4, 96.53) * mm});
            skLineSegment(sketch, "E393", {"start": v(-215.4, 96.53) * mm, "end": v(-214.77, 97.43) * mm});
            skLineSegment(sketch, "E394", {"start": v(-214.77, 97.43) * mm, "end": v(-214.34, 98.4) * mm});
            skLineSegment(sketch, "E395", {"start": v(-214.34, 98.4) * mm, "end": v(-214.09, 99.41) * mm});
            skLineSegment(sketch, "E396", {"start": v(-214.09, 99.41) * mm, "end": v(-214, 100.45) * mm});
            skLineSegment(sketch, "E397", {"start": v(-214, 100.45) * mm, "end": v(-214.06, 101.5) * mm});
            skLineSegment(sketch, "E398", {"start": v(-214.06, 101.5) * mm, "end": v(-214.25, 102.52) * mm});
            skLineSegment(sketch, "E399", {"start": v(-214.25, 102.52) * mm, "end": v(-214.55, 103.52) * mm});
            skLineSegment(sketch, "E400", {"start": v(-214.55, 103.52) * mm, "end": v(-214.98, 104.32) * mm});
            skLineSegment(sketch, "E401", {"start": v(-214.98, 104.32) * mm, "end": v(-215.53, 104.75) * mm});
            skLineSegment(sketch, "E402", {"start": v(-215.53, 104.75) * mm, "end": v(-216.17, 104.9) * mm});
            skLineSegment(sketch, "E403", {"start": v(-216.17, 104.9) * mm, "end": v(-216.87, 104.82) * mm});
            skLineSegment(sketch, "E404", {"start": v(-216.87, 104.82) * mm, "end": v(-217.6, 104.62) * mm});
            skLineSegment(sketch, "E405", {"start": v(-217.6, 104.62) * mm, "end": v(-218.36, 104.36) * mm});
            skLineSegment(sketch, "E406", {"start": v(-218.36, 104.36) * mm, "end": v(-219.1, 104.13) * mm});
            skLineSegment(sketch, "E407", {"start": v(-219.1, 104.13) * mm, "end": v(-219.8, 104) * mm});
            skLineSegment(sketch, "E408", {"start": v(-219.8, 104) * mm, "end": v(-221.76, 104) * mm});
            skLineSegment(sketch, "E409", {"start": v(-221.76, 104) * mm, "end": v(-223.61, 104.3) * mm});
            skLineSegment(sketch, "E410", {"start": v(-223.61, 104.3) * mm, "end": v(-225.33, 104.89) * mm});
            skLineSegment(sketch, "E411", {"start": v(-225.33, 104.89) * mm, "end": v(-226.9, 105.75) * mm});
            skLineSegment(sketch, "E412", {"start": v(-226.9, 105.75) * mm, "end": v(-228.29, 106.88) * mm});
            skLineSegment(sketch, "E413", {"start": v(-228.29, 106.88) * mm, "end": v(-229.49, 108.26) * mm});
            skLineSegment(sketch, "E414", {"start": v(-229.49, 108.26) * mm, "end": v(-230.48, 109.87) * mm});
            skLineSegment(sketch, "E415", {"start": v(-230.48, 109.87) * mm, "end": v(-231.23, 111.71) * mm});
            skLineSegment(sketch, "E416", {"start": v(-231.23, 111.71) * mm, "end": v(-231.68, 113.6) * mm});
            skLineSegment(sketch, "E417", {"start": v(-231.68, 113.6) * mm, "end": v(-231.79, 115.4) * mm});
            skLineSegment(sketch, "E418", {"start": v(-231.79, 115.4) * mm, "end": v(-231.59, 117.1) * mm});
            skLineSegment(sketch, "E419", {"start": v(-231.59, 117.1) * mm, "end": v(-231.12, 118.7) * mm});
            skLineSegment(sketch, "E420", {"start": v(-231.12, 118.7) * mm, "end": v(-230.42, 120.23) * mm});
            skLineSegment(sketch, "E421", {"start": v(-230.42, 120.23) * mm, "end": v(-229.53, 121.68) * mm});
            skLineSegment(sketch, "E422", {"start": v(-229.53, 121.68) * mm, "end": v(-228.48, 123.07) * mm});
            skLineSegment(sketch, "E423", {"start": v(-228.48, 123.07) * mm, "end": v(-227.31, 124.4) * mm});
            skLineSegment(sketch, "E424", {"start": v(-227.31, 124.4) * mm, "end": v(-223.74, 128.26) * mm});
            skLineSegment(sketch, "E425", {"start": v(-223.74, 128.26) * mm, "end": v(-220.17, 132.1) * mm});
            skLineSegment(sketch, "E426", {"start": v(-220.17, 132.1) * mm, "end": v(-216.58, 135.93) * mm});
            skLineSegment(sketch, "E427", {"start": v(-216.58, 135.93) * mm, "end": v(-212.98, 139.75) * mm});
            skLineSegment(sketch, "E428", {"start": v(-212.98, 139.75) * mm, "end": v(-209.37, 143.56) * mm});
            skLineSegment(sketch, "E429", {"start": v(-209.37, 143.56) * mm, "end": v(-205.73, 147.34) * mm});
            skLineSegment(sketch, "E430", {"start": v(-205.73, 147.34) * mm, "end": v(-202.07, 151.1) * mm});
            skLineSegment(sketch, "E431", {"start": v(-202.07, 151.1) * mm, "end": v(-198.38, 154.84) * mm});
            skLineSegment(sketch, "E432", {"start": v(-198.38, 154.84) * mm, "end": v(-195.96, 156.85) * mm});
            skLineSegment(sketch, "E433", {"start": v(-195.96, 156.85) * mm, "end": v(-193.48, 158.12) * mm});
            skLineSegment(sketch, "E434", {"start": v(-193.48, 158.12) * mm, "end": v(-191, 158.66) * mm});
            skLineSegment(sketch, "E435", {"start": v(-191, 158.66) * mm, "end": v(-188.58, 158.5) * mm});
            skLineSegment(sketch, "E436", {"start": v(-188.58, 158.5) * mm, "end": v(-186.28, 157.65) * mm});
            skLineSegment(sketch, "E437", {"start": v(-186.28, 157.65) * mm, "end": v(-184.16, 156.15) * mm});
            skLineSegment(sketch, "E438", {"start": v(-184.16, 156.15) * mm, "end": v(-182.27, 154) * mm});
            skLineSegment(sketch, "E439", {"start": v(-182.27, 154) * mm, "end": v(-180.68, 151.23) * mm});
            skLineSegment(sketch, "E440", {"start": v(-180.68, 151.23) * mm, "end": v(-180.16, 149.97) * mm});
            skLineSegment(sketch, "E441", {"start": v(-180.16, 149.97) * mm, "end": v(-179.76, 148.67) * mm});
            skLineSegment(sketch, "E442", {"start": v(-179.76, 148.67) * mm, "end": v(-179.44, 147.36) * mm});
            skLineSegment(sketch, "E443", {"start": v(-179.44, 147.36) * mm, "end": v(-179.17, 146.03) * mm});
            skLineSegment(sketch, "E444", {"start": v(-179.17, 146.03) * mm, "end": v(-178.94, 144.69) * mm});
            skLineSegment(sketch, "E445", {"start": v(-178.94, 144.69) * mm, "end": v(-178.7, 143.35) * mm});
            skLineSegment(sketch, "E446", {"start": v(-178.7, 143.35) * mm, "end": v(-178.43, 142.01) * mm});
            skLineSegment(sketch, "E447", {"start": v(-178.43, 142.01) * mm, "end": v(-178.1, 140.7) * mm});
            skLineSegment(sketch, "E448", {"start": v(-178.1, 140.7) * mm, "end": v(-177.35, 140.9) * mm});
            skLineSegment(sketch, "E449", {"start": v(-177.35, 140.9) * mm, "end": v(-176.73, 141.2) * mm});
            skLineSegment(sketch, "E450", {"start": v(-176.73, 141.2) * mm, "end": v(-176.22, 141.6) * mm});
            skLineSegment(sketch, "E451", {"start": v(-176.22, 141.6) * mm, "end": v(-175.8, 142.07) * mm});
            skLineSegment(sketch, "E452", {"start": v(-175.8, 142.07) * mm, "end": v(-175.43, 142.57) * mm});
            skLineSegment(sketch, "E453", {"start": v(-175.43, 142.57) * mm, "end": v(-175.1, 143.1) * mm});
            skLineSegment(sketch, "E454", {"start": v(-175.1, 143.1) * mm, "end": v(-174.76, 143.61) * mm});
            skLineSegment(sketch, "E455", {"start": v(-174.76, 143.61) * mm, "end": v(-174.42, 144.1) * mm});
            skLineSegment(sketch, "E456", {"start": v(-174.42, 144.1) * mm, "end": v(-165.71, 154.72) * mm});
            skLineSegment(sketch, "E457", {"start": v(-165.71, 154.72) * mm, "end": v(-156.5, 164.71) * mm});
            skLineSegment(sketch, "E458", {"start": v(-156.5, 164.71) * mm, "end": v(-146.77, 174.06) * mm});
            skLineSegment(sketch, "E459", {"start": v(-146.77, 174.06) * mm, "end": v(-136.53, 182.75) * mm});
            skLineSegment(sketch, "E460", {"start": v(-136.53, 182.75) * mm, "end": v(-125.76, 190.78) * mm});
            skLineSegment(sketch, "E461", {"start": v(-125.76, 190.78) * mm, "end": v(-114.48, 198.15) * mm});
            skLineSegment(sketch, "E462", {"start": v(-114.48, 198.15) * mm, "end": v(-102.66, 204.84) * mm});
            skLineSegment(sketch, "E463", {"start": v(-102.66, 204.84) * mm, "end": v(-90.32, 210.85) * mm});
            skLineSegment(sketch, "E464", {"start": v(-90.32, 210.85) * mm, "end": v(-87.91, 212) * mm});
            skLineSegment(sketch, "E465", {"start": v(-87.91, 212) * mm, "end": v(-85.74, 213.22) * mm});
            skLineSegment(sketch, "E466", {"start": v(-85.74, 213.22) * mm, "end": v(-83.78, 214.57) * mm});
            skLineSegment(sketch, "E467", {"start": v(-83.78, 214.57) * mm, "end": v(-82.04, 216.09) * mm});
            skLineSegment(sketch, "E468", {"start": v(-82.04, 216.09) * mm, "end": v(-80.5, 217.83) * mm});
            skLineSegment(sketch, "E469", {"start": v(-80.5, 217.83) * mm, "end": v(-79.17, 219.85) * mm});
            skLineSegment(sketch, "E470", {"start": v(-79.17, 219.85) * mm, "end": v(-78.03, 222.2) * mm});
            skLineSegment(sketch, "E471", {"start": v(-78.03, 222.2) * mm, "end": v(-77.09, 224.93) * mm});
            skLineSegment(sketch, "E472", {"start": v(-77.09, 224.93) * mm, "end": v(-74.8, 230.87) * mm});
            skLineSegment(sketch, "E473", {"start": v(-74.8, 230.87) * mm, "end": v(-71.75, 235.74) * mm});
            skLineSegment(sketch, "E474", {"start": v(-71.75, 235.74) * mm, "end": v(-68, 239.54) * mm});
            skLineSegment(sketch, "E475", {"start": v(-68, 239.54) * mm, "end": v(-63.62, 242.26) * mm});
            skLineSegment(sketch, "E476", {"start": v(-63.62, 242.26) * mm, "end": v(-58.69, 243.88) * mm});
            skLineSegment(sketch, "E477", {"start": v(-58.69, 243.88) * mm, "end": v(-53.27, 244.39) * mm});
            skLineSegment(sketch, "E478", {"start": v(-53.27, 244.39) * mm, "end": v(-47.45, 243.78) * mm});
            skLineSegment(sketch, "E479", {"start": v(-47.45, 243.78) * mm, "end": v(-41.28, 242.03) * mm});
            skLineSegment(sketch, "E480", {"start": v(-41.28, 242.03) * mm, "end": v(-38.82, 241.08) * mm});
            skLineSegment(sketch, "E481", {"start": v(-38.82, 241.08) * mm, "end": v(-36.4, 240.03) * mm});
            skLineSegment(sketch, "E482", {"start": v(-36.4, 240.03) * mm, "end": v(-34.05, 238.88) * mm});
            skLineSegment(sketch, "E483", {"start": v(-34.05, 238.88) * mm, "end": v(-31.74, 237.65) * mm});
            skLineSegment(sketch, "E484", {"start": v(-31.74, 237.65) * mm, "end": v(-29.5, 236.31) * mm});
            skLineSegment(sketch, "E485", {"start": v(-29.5, 236.31) * mm, "end": v(-27.3, 234.89) * mm});
            skLineSegment(sketch, "E486", {"start": v(-27.3, 234.89) * mm, "end": v(-25.15, 233.37) * mm});
            skLineSegment(sketch, "E487", {"start": v(-25.15, 233.37) * mm, "end": v(-23.07, 231.76) * mm});
            skLineSegment(sketch, "E488", {"start": v(-23.07, 231.76) * mm, "end": v(-22.07, 231.02) * mm});
            skLineSegment(sketch, "E489", {"start": v(-22.07, 231.02) * mm, "end": v(-21.17, 230.54) * mm});
            skLineSegment(sketch, "E490", {"start": v(-21.17, 230.54) * mm, "end": v(-20.35, 230.3) * mm});
            skLineSegment(sketch, "E491", {"start": v(-20.35, 230.3) * mm, "end": v(-19.6, 230.32) * mm});
            skLineSegment(sketch, "E492", {"start": v(-19.6, 230.32) * mm, "end": v(-18.9, 230.59) * mm});
            skLineSegment(sketch, "E493", {"start": v(-18.9, 230.59) * mm, "end": v(-18.24, 231.11) * mm});
            skLineSegment(sketch, "E494", {"start": v(-18.24, 231.11) * mm, "end": v(-17.6, 231.9) * mm});
            skLineSegment(sketch, "E495", {"start": v(-17.6, 231.9) * mm, "end": v(-16.93, 232.93) * mm});
            skLineSegment(sketch, "E496", {"start": v(-16.93, 232.93) * mm, "end": v(-15.44, 235.4) * mm});
            skLineSegment(sketch, "E497", {"start": v(-15.44, 235.4) * mm, "end": v(-13.86, 237.8) * mm});
            skLineSegment(sketch, "E498", {"start": v(-13.86, 237.8) * mm, "end": v(-12.18, 240.12) * mm});
            skLineSegment(sketch, "E499", {"start": v(-12.18, 240.12) * mm, "end": v(-10.37, 242.33) * mm});
            skLineSegment(sketch, "E500", {"start": v(-10.37, 242.33) * mm, "end": v(-8.45, 244.44) * mm});
            skLineSegment(sketch, "E501", {"start": v(-8.45, 244.44) * mm, "end": v(-6.39, 246.42) * mm});
            skLineSegment(sketch, "E502", {"start": v(-6.39, 246.42) * mm, "end": v(-4.18, 248.28) * mm});
            skLineSegment(sketch, "E503", {"start": v(-4.18, 248.28) * mm, "end": v(-1.82, 250) * mm});
            skLineSegment(sketch, "E504", {"start": v(91.86, 4.35) * mm, "end": v(91.86, 16.1) * mm});
            skLineSegment(sketch, "E505", {"start": v(91.86, 16.1) * mm, "end": v(91.86, 27.84) * mm});
            skLineSegment(sketch, "E506", {"start": v(91.86, 27.84) * mm, "end": v(91.86, 39.59) * mm});
            skLineSegment(sketch, "E507", {"start": v(91.86, 39.59) * mm, "end": v(91.86, 51.33) * mm});
            skLineSegment(sketch, "E508", {"start": v(91.86, 51.33) * mm, "end": v(91.86, 63.08) * mm});
            skLineSegment(sketch, "E509", {"start": v(91.86, 63.08) * mm, "end": v(91.85, 74.83) * mm});
            skLineSegment(sketch, "E510", {"start": v(91.85, 74.83) * mm, "end": v(91.85, 86.57) * mm});
            skLineSegment(sketch, "E511", {"start": v(91.85, 86.57) * mm, "end": v(91.84, 98.32) * mm});
            skLineSegment(sketch, "E512", {"start": v(91.84, 98.32) * mm, "end": v(91.85, 99.08) * mm});
            skLineSegment(sketch, "E513", {"start": v(91.85, 99.08) * mm, "end": v(91.85, 99.9) * mm});
            skLineSegment(sketch, "E514", {"start": v(91.85, 99.9) * mm, "end": v(91.82, 100.7) * mm});
            skLineSegment(sketch, "E515", {"start": v(91.82, 100.7) * mm, "end": v(91.7, 101.48) * mm});
            skLineSegment(sketch, "E516", {"start": v(91.7, 101.48) * mm, "end": v(91.47, 102.15) * mm});
            skLineSegment(sketch, "E517", {"start": v(91.47, 102.15) * mm, "end": v(91.07, 102.68) * mm});
            skLineSegment(sketch, "E518", {"start": v(91.07, 102.68) * mm, "end": v(90.49, 103.02) * mm});
            skLineSegment(sketch, "E519", {"start": v(90.49, 103.02) * mm, "end": v(89.67, 103.12) * mm});
            skLineSegment(sketch, "E520", {"start": v(89.67, 103.12) * mm, "end": v(88.96, 102.97) * mm});
            skLineSegment(sketch, "E521", {"start": v(88.96, 102.97) * mm, "end": v(88.51, 102.6) * mm});
            skLineSegment(sketch, "E522", {"start": v(88.51, 102.6) * mm, "end": v(88.28, 102.05) * mm});
            skLineSegment(sketch, "E523", {"start": v(88.28, 102.05) * mm, "end": v(88.2, 101.39) * mm});
            skLineSegment(sketch, "E524", {"start": v(88.2, 101.39) * mm, "end": v(88.23, 100.65) * mm});
            skLineSegment(sketch, "E525", {"start": v(88.23, 100.65) * mm, "end": v(88.32, 99.9) * mm});
            skLineSegment(sketch, "E526", {"start": v(88.32, 99.9) * mm, "end": v(88.4, 99.16) * mm});
            skLineSegment(sketch, "E527", {"start": v(88.4, 99.16) * mm, "end": v(88.44, 98.5) * mm});
            skLineSegment(sketch, "E528", {"start": v(88.44, 98.5) * mm, "end": v(88.4, 94.2) * mm});
            skLineSegment(sketch, "E529", {"start": v(88.4, 94.2) * mm, "end": v(88.38, 89.88) * mm});
            skLineSegment(sketch, "E530", {"start": v(88.38, 89.88) * mm, "end": v(88.36, 85.57) * mm});
            skLineSegment(sketch, "E531", {"start": v(88.36, 85.57) * mm, "end": v(88.35, 81.26) * mm});
            skLineSegment(sketch, "E532", {"start": v(88.35, 81.26) * mm, "end": v(88.35, 76.95) * mm});
            skLineSegment(sketch, "E533", {"start": v(88.35, 76.95) * mm, "end": v(88.36, 72.64) * mm});
            skLineSegment(sketch, "E534", {"start": v(88.36, 72.64) * mm, "end": v(88.36, 68.33) * mm});
            skLineSegment(sketch, "E535", {"start": v(88.36, 68.33) * mm, "end": v(88.36, 64.01) * mm});
            skLineSegment(sketch, "E536", {"start": v(88.36, 64.01) * mm, "end": v(88.33, 62.94) * mm});
            skLineSegment(sketch, "E537", {"start": v(88.33, 62.94) * mm, "end": v(88.22, 61.94) * mm});
            skLineSegment(sketch, "E538", {"start": v(88.22, 61.94) * mm, "end": v(88, 61.04) * mm});
            skLineSegment(sketch, "E539", {"start": v(88, 61.04) * mm, "end": v(87.63, 60.26) * mm});
            skLineSegment(sketch, "E540", {"start": v(87.63, 60.26) * mm, "end": v(87.08, 59.62) * mm});
            skLineSegment(sketch, "E541", {"start": v(87.08, 59.62) * mm, "end": v(86.33, 59.14) * mm});
            skLineSegment(sketch, "E542", {"start": v(86.33, 59.14) * mm, "end": v(85.33, 58.84) * mm});
            skLineSegment(sketch, "E543", {"start": v(85.33, 58.84) * mm, "end": v(84.06, 58.74) * mm});
            skLineSegment(sketch, "E544", {"start": v(84.06, 58.74) * mm, "end": v(80.57, 58.76) * mm});
            skLineSegment(sketch, "E545", {"start": v(80.57, 58.76) * mm, "end": v(77.07, 58.77) * mm});
            skLineSegment(sketch, "E546", {"start": v(77.07, 58.77) * mm, "end": v(73.57, 58.77) * mm});
            skLineSegment(sketch, "E547", {"start": v(73.57, 58.77) * mm, "end": v(70.07, 58.77) * mm});
            skLineSegment(sketch, "E548", {"start": v(70.07, 58.77) * mm, "end": v(66.57, 58.77) * mm});
            skLineSegment(sketch, "E549", {"start": v(66.57, 58.77) * mm, "end": v(63.07, 58.77) * mm});
            skLineSegment(sketch, "E550", {"start": v(63.07, 58.77) * mm, "end": v(59.57, 58.77) * mm});
            skLineSegment(sketch, "E551", {"start": v(59.57, 58.77) * mm, "end": v(56.07, 58.78) * mm});
            skLineSegment(sketch, "E552", {"start": v(56.07, 58.78) * mm, "end": v(55.42, 58.79) * mm});
            skLineSegment(sketch, "E553", {"start": v(55.42, 58.79) * mm, "end": v(54.75, 58.84) * mm});
            skLineSegment(sketch, "E554", {"start": v(54.75, 58.84) * mm, "end": v(54.1, 58.94) * mm});
            skLineSegment(sketch, "E555", {"start": v(54.1, 58.94) * mm, "end": v(53.5, 59.12) * mm});
            skLineSegment(sketch, "E556", {"start": v(53.5, 59.12) * mm, "end": v(52.98, 59.4) * mm});
            skLineSegment(sketch, "E557", {"start": v(52.98, 59.4) * mm, "end": v(52.57, 59.8) * mm});
            skLineSegment(sketch, "E558", {"start": v(52.57, 59.8) * mm, "end": v(52.3, 60.34) * mm});
            skLineSegment(sketch, "E559", {"start": v(52.3, 60.34) * mm, "end": v(52.22, 61.03) * mm});
            skLineSegment(sketch, "E560", {"start": v(52.22, 61.03) * mm, "end": v(52.08, 62.95) * mm});
            skLineSegment(sketch, "E561", {"start": v(52.08, 62.95) * mm, "end": v(51.63, 64.39) * mm});
            skLineSegment(sketch, "E562", {"start": v(51.63, 64.39) * mm, "end": v(50.9, 65.4) * mm});
            skLineSegment(sketch, "E563", {"start": v(50.9, 65.4) * mm, "end": v(49.93, 66.07) * mm});
            skLineSegment(sketch, "E564", {"start": v(49.93, 66.07) * mm, "end": v(48.76, 66.45) * mm});
            skLineSegment(sketch, "E565", {"start": v(48.76, 66.45) * mm, "end": v(47.44, 66.63) * mm});
            skLineSegment(sketch, "E566", {"start": v(47.44, 66.63) * mm, "end": v(46, 66.67) * mm});
            skLineSegment(sketch, "E567", {"start": v(46, 66.67) * mm, "end": v(44.5, 66.65) * mm});
            skLineSegment(sketch, "E568", {"start": v(44.5, 66.65) * mm, "end": v(43.72, 66.61) * mm});
            skLineSegment(sketch, "E569", {"start": v(43.72, 66.61) * mm, "end": v(42.9, 66.59) * mm});
            skLineSegment(sketch, "E570", {"start": v(42.9, 66.59) * mm, "end": v(42.11, 66.62) * mm});
            skLineSegment(sketch, "E571", {"start": v(42.11, 66.62) * mm, "end": v(41.38, 66.76) * mm});
            skLineSegment(sketch, "E572", {"start": v(41.38, 66.76) * mm, "end": v(40.73, 67.06) * mm});
            skLineSegment(sketch, "E573", {"start": v(40.73, 67.06) * mm, "end": v(40.22, 67.57) * mm});
            skLineSegment(sketch, "E574", {"start": v(40.22, 67.57) * mm, "end": v(39.88, 68.35) * mm});
            skLineSegment(sketch, "E575", {"start": v(39.88, 68.35) * mm, "end": v(39.75, 69.44) * mm});
            skLineSegment(sketch, "E576", {"start": v(39.75, 69.44) * mm, "end": v(39.86, 70.54) * mm});
            skLineSegment(sketch, "E577", {"start": v(39.86, 70.54) * mm, "end": v(40.18, 71.34) * mm});
            skLineSegment(sketch, "E578", {"start": v(40.18, 71.34) * mm, "end": v(40.67, 71.87) * mm});
            skLineSegment(sketch, "E579", {"start": v(40.67, 71.87) * mm, "end": v(41.3, 72.2) * mm});
            skLineSegment(sketch, "E580", {"start": v(41.3, 72.2) * mm, "end": v(42.04, 72.35) * mm});
            skLineSegment(sketch, "E581", {"start": v(42.04, 72.35) * mm, "end": v(42.83, 72.4) * mm});
            skLineSegment(sketch, "E582", {"start": v(42.83, 72.4) * mm, "end": v(43.64, 72.36) * mm});
            skLineSegment(sketch, "E583", {"start": v(43.64, 72.36) * mm, "end": v(44.43, 72.3) * mm});
            skLineSegment(sketch, "E584", {"start": v(44.43, 72.3) * mm, "end": v(45.88, 72.3) * mm});
            skLineSegment(sketch, "E585", {"start": v(45.88, 72.3) * mm, "end": v(47.08, 72.49) * mm});
            skLineSegment(sketch, "E586", {"start": v(47.08, 72.49) * mm, "end": v(48.06, 72.88) * mm});
            skLineSegment(sketch, "E587", {"start": v(48.06, 72.88) * mm, "end": v(48.81, 73.48) * mm});
            skLineSegment(sketch, "E588", {"start": v(48.81, 73.48) * mm, "end": v(49.36, 74.29) * mm});
            skLineSegment(sketch, "E589", {"start": v(49.36, 74.29) * mm, "end": v(49.71, 75.3) * mm});
            skLineSegment(sketch, "E590", {"start": v(49.71, 75.3) * mm, "end": v(49.88, 76.5) * mm});
            skLineSegment(sketch, "E591", {"start": v(49.88, 76.5) * mm, "end": v(49.88, 77.92) * mm});
            skLineSegment(sketch, "E592", {"start": v(49.88, 77.92) * mm, "end": v(49.81, 79.48) * mm});
            skLineSegment(sketch, "E593", {"start": v(49.81, 79.48) * mm, "end": v(49.77, 81.04) * mm});
            skLineSegment(sketch, "E594", {"start": v(49.77, 81.04) * mm, "end": v(49.76, 82.6) * mm});
            skLineSegment(sketch, "E595", {"start": v(49.76, 82.6) * mm, "end": v(49.76, 84.16) * mm});
            skLineSegment(sketch, "E596", {"start": v(49.76, 84.16) * mm, "end": v(49.77, 85.72) * mm});
            skLineSegment(sketch, "E597", {"start": v(49.77, 85.72) * mm, "end": v(49.8, 87.29) * mm});
            skLineSegment(sketch, "E598", {"start": v(49.8, 87.29) * mm, "end": v(49.81, 88.85) * mm});
            skLineSegment(sketch, "E599", {"start": v(49.81, 88.85) * mm, "end": v(49.83, 90.41) * mm});
            skLineSegment(sketch, "E600", {"start": v(49.83, 90.41) * mm, "end": v(49.8, 91.32) * mm});
            skLineSegment(sketch, "E601", {"start": v(49.8, 91.32) * mm, "end": v(49.66, 92.14) * mm});
            skLineSegment(sketch, "E602", {"start": v(49.66, 92.14) * mm, "end": v(49.42, 92.87) * mm});
            skLineSegment(sketch, "E603", {"start": v(49.42, 92.87) * mm, "end": v(49.07, 93.49) * mm});
            skLineSegment(sketch, "E604", {"start": v(49.07, 93.49) * mm, "end": v(48.58, 93.99) * mm});
            skLineSegment(sketch, "E605", {"start": v(48.58, 93.99) * mm, "end": v(47.94, 94.36) * mm});
            skLineSegment(sketch, "E606", {"start": v(47.94, 94.36) * mm, "end": v(47.14, 94.59) * mm});
            skLineSegment(sketch, "E607", {"start": v(47.14, 94.59) * mm, "end": v(46.16, 94.66) * mm});
            skLineSegment(sketch, "E608", {"start": v(46.16, 94.66) * mm, "end": v(45.09, 94.67) * mm});
            skLineSegment(sketch, "E609", {"start": v(45.09, 94.67) * mm, "end": v(44.03, 94.71) * mm});
            skLineSegment(sketch, "E610", {"start": v(44.03, 94.71) * mm, "end": v(43.01, 94.83) * mm});
            skLineSegment(sketch, "E611", {"start": v(43.01, 94.83) * mm, "end": v(42.04, 95.05) * mm});
            skLineSegment(sketch, "E612", {"start": v(42.04, 95.05) * mm, "end": v(41.13, 95.43) * mm});
            skLineSegment(sketch, "E613", {"start": v(41.13, 95.43) * mm, "end": v(40.29, 95.98) * mm});
            skLineSegment(sketch, "E614", {"start": v(40.29, 95.98) * mm, "end": v(39.52, 96.75) * mm});
            skLineSegment(sketch, "E615", {"start": v(39.52, 96.75) * mm, "end": v(38.86, 97.77) * mm});
            skLineSegment(sketch, "E616", {"start": v(38.86, 97.77) * mm, "end": v(38.6, 98.15) * mm});
            skLineSegment(sketch, "E617", {"start": v(38.6, 98.15) * mm, "end": v(38.3, 98.39) * mm});
            skLineSegment(sketch, "E618", {"start": v(38.3, 98.39) * mm, "end": v(37.98, 98.5) * mm});
            skLineSegment(sketch, "E619", {"start": v(37.98, 98.5) * mm, "end": v(37.65, 98.5) * mm});
            skLineSegment(sketch, "E620", {"start": v(37.65, 98.5) * mm, "end": v(37.32, 98.38) * mm});
            skLineSegment(sketch, "E621", {"start": v(37.32, 98.38) * mm, "end": v(37.02, 98.18) * mm});
            skLineSegment(sketch, "E622", {"start": v(37.02, 98.18) * mm, "end": v(36.74, 97.9) * mm});
            skLineSegment(sketch, "E623", {"start": v(36.74, 97.9) * mm, "end": v(36.5, 97.54) * mm});
            skLineSegment(sketch, "E624", {"start": v(36.5, 97.54) * mm, "end": v(35.86, 96.59) * mm});
            skLineSegment(sketch, "E625", {"start": v(35.86, 96.59) * mm, "end": v(35.14, 95.87) * mm});
            skLineSegment(sketch, "E626", {"start": v(35.14, 95.87) * mm, "end": v(34.34, 95.36) * mm});
            skLineSegment(sketch, "E627", {"start": v(34.34, 95.36) * mm, "end": v(33.47, 95.01) * mm});
            skLineSegment(sketch, "E628", {"start": v(33.47, 95.01) * mm, "end": v(32.54, 94.8) * mm});
            skLineSegment(sketch, "E629", {"start": v(32.54, 94.8) * mm, "end": v(31.58, 94.7) * mm});
            skLineSegment(sketch, "E630", {"start": v(31.58, 94.7) * mm, "end": v(30.59, 94.68) * mm});
            skLineSegment(sketch, "E631", {"start": v(30.59, 94.68) * mm, "end": v(29.57, 94.7) * mm});
            skLineSegment(sketch, "E632", {"start": v(29.57, 94.7) * mm, "end": v(28.52, 94.64) * mm});
            skLineSegment(sketch, "E633", {"start": v(28.52, 94.64) * mm, "end": v(27.65, 94.43) * mm});
            skLineSegment(sketch, "E634", {"start": v(27.65, 94.43) * mm, "end": v(26.94, 94.07) * mm});
            skLineSegment(sketch, "E635", {"start": v(26.94, 94.07) * mm, "end": v(26.39, 93.58) * mm});
            skLineSegment(sketch, "E636", {"start": v(26.39, 93.58) * mm, "end": v(25.98, 92.94) * mm});
            skLineSegment(sketch, "E637", {"start": v(25.98, 92.94) * mm, "end": v(25.7, 92.18) * mm});
            skLineSegment(sketch, "E638", {"start": v(25.7, 92.18) * mm, "end": v(25.56, 91.3) * mm});
            skLineSegment(sketch, "E639", {"start": v(25.56, 91.3) * mm, "end": v(25.52, 90.3) * mm});
            skLineSegment(sketch, "E640", {"start": v(25.52, 90.3) * mm, "end": v(25.55, 88.85) * mm});
            skLineSegment(sketch, "E641", {"start": v(25.55, 88.85) * mm, "end": v(25.57, 87.42) * mm});
            skLineSegment(sketch, "E642", {"start": v(25.57, 87.42) * mm, "end": v(25.6, 85.98) * mm});
            skLineSegment(sketch, "E643", {"start": v(25.6, 85.98) * mm, "end": v(25.62, 84.54) * mm});
            skLineSegment(sketch, "E644", {"start": v(25.62, 84.54) * mm, "end": v(25.62, 83.1) * mm});
            skLineSegment(sketch, "E645", {"start": v(25.62, 83.1) * mm, "end": v(25.6, 81.66) * mm});
            skLineSegment(sketch, "E646", {"start": v(25.6, 81.66) * mm, "end": v(25.55, 80.23) * mm});
            skLineSegment(sketch, "E647", {"start": v(25.55, 80.23) * mm, "end": v(25.47, 78.8) * mm});
            skLineSegment(sketch, "E648", {"start": v(25.47, 78.8) * mm, "end": v(25.43, 77.19) * mm});
            skLineSegment(sketch, "E649", {"start": v(25.43, 77.19) * mm, "end": v(25.57, 75.78) * mm});
            skLineSegment(sketch, "E650", {"start": v(25.57, 75.78) * mm, "end": v(25.9, 74.59) * mm});
            skLineSegment(sketch, "E651", {"start": v(25.9, 74.59) * mm, "end": v(26.48, 73.63) * mm});
            skLineSegment(sketch, "E652", {"start": v(26.48, 73.63) * mm, "end": v(27.3, 72.9) * mm});
            skLineSegment(sketch, "E653", {"start": v(27.3, 72.9) * mm, "end": v(28.4, 72.43) * mm});
            skLineSegment(sketch, "E654", {"start": v(28.4, 72.43) * mm, "end": v(29.82, 72.23) * mm});
            skLineSegment(sketch, "E655", {"start": v(29.82, 72.23) * mm, "end": v(31.55, 72.3) * mm});
            skLineSegment(sketch, "E656", {"start": v(31.55, 72.3) * mm, "end": v(32.32, 72.36) * mm});
            skLineSegment(sketch, "E657", {"start": v(32.32, 72.36) * mm, "end": v(33.06, 72.36) * mm});
            skLineSegment(sketch, "E658", {"start": v(33.06, 72.36) * mm, "end": v(33.77, 72.25) * mm});
            skLineSegment(sketch, "E659", {"start": v(33.77, 72.25) * mm, "end": v(34.4, 72.02) * mm});
            skLineSegment(sketch, "E660", {"start": v(34.4, 72.02) * mm, "end": v(34.93, 71.64) * mm});
            skLineSegment(sketch, "E661", {"start": v(34.93, 71.64) * mm, "end": v(35.33, 71.09) * mm});
            skLineSegment(sketch, "E662", {"start": v(35.33, 71.09) * mm, "end": v(35.57, 70.33) * mm});
            skLineSegment(sketch, "E663", {"start": v(35.57, 70.33) * mm, "end": v(35.63, 69.34) * mm});
            skLineSegment(sketch, "E664", {"start": v(35.63, 69.34) * mm, "end": v(35.5, 68.35) * mm});
            skLineSegment(sketch, "E665", {"start": v(35.5, 68.35) * mm, "end": v(35.17, 67.64) * mm});
            skLineSegment(sketch, "E666", {"start": v(35.17, 67.64) * mm, "end": v(34.7, 67.15) * mm});
            skLineSegment(sketch, "E667", {"start": v(34.7, 67.15) * mm, "end": v(34.13, 66.85) * mm});
            skLineSegment(sketch, "E668", {"start": v(34.13, 66.85) * mm, "end": v(33.46, 66.7) * mm});
            skLineSegment(sketch, "E669", {"start": v(33.46, 66.7) * mm, "end": v(32.74, 66.64) * mm});
            skLineSegment(sketch, "E670", {"start": v(32.74, 66.64) * mm, "end": v(32, 66.63) * mm});
            skLineSegment(sketch, "E671", {"start": v(32, 66.63) * mm, "end": v(31.26, 66.63) * mm});
            skLineSegment(sketch, "E672", {"start": v(31.26, 66.63) * mm, "end": v(29.32, 66.6) * mm});
            skLineSegment(sketch, "E673", {"start": v(29.32, 66.6) * mm, "end": v(27.38, 66.59) * mm});
            skLineSegment(sketch, "E674", {"start": v(27.38, 66.59) * mm, "end": v(25.44, 66.57) * mm});
            skLineSegment(sketch, "E675", {"start": v(25.44, 66.57) * mm, "end": v(23.5, 66.57) * mm});
            skLineSegment(sketch, "E676", {"start": v(23.5, 66.57) * mm, "end": v(21.57, 66.57) * mm});
            skLineSegment(sketch, "E677", {"start": v(21.57, 66.57) * mm, "end": v(19.63, 66.58) * mm});
            skLineSegment(sketch, "E678", {"start": v(19.63, 66.58) * mm, "end": v(17.7, 66.6) * mm});
            skLineSegment(sketch, "E679", {"start": v(17.7, 66.6) * mm, "end": v(15.76, 66.65) * mm});
            skLineSegment(sketch, "E680", {"start": v(15.76, 66.65) * mm, "end": v(14.93, 66.63) * mm});
            skLineSegment(sketch, "E681", {"start": v(14.93, 66.63) * mm, "end": v(14.05, 66.58) * mm});
            skLineSegment(sketch, "E682", {"start": v(14.05, 66.58) * mm, "end": v(13.17, 66.57) * mm});
            skLineSegment(sketch, "E683", {"start": v(13.17, 66.57) * mm, "end": v(12.33, 66.65) * mm});
            skLineSegment(sketch, "E684", {"start": v(12.33, 66.65) * mm, "end": v(11.58, 66.9) * mm});
            skLineSegment(sketch, "E685", {"start": v(11.58, 66.9) * mm, "end": v(10.97, 67.38) * mm});
            skLineSegment(sketch, "E686", {"start": v(10.97, 67.38) * mm, "end": v(10.54, 68.16) * mm});
            skLineSegment(sketch, "E687", {"start": v(10.54, 68.16) * mm, "end": v(10.34, 69.3) * mm});
            skLineSegment(sketch, "E688", {"start": v(10.34, 69.3) * mm, "end": v(10.4, 70.5) * mm});
            skLineSegment(sketch, "E689", {"start": v(10.4, 70.5) * mm, "end": v(10.73, 71.33) * mm});
            skLineSegment(sketch, "E690", {"start": v(10.73, 71.33) * mm, "end": v(11.27, 71.87) * mm});
            skLineSegment(sketch, "E691", {"start": v(11.27, 71.87) * mm, "end": v(11.97, 72.18) * mm});
            skLineSegment(sketch, "E692", {"start": v(11.97, 72.18) * mm, "end": v(12.78, 72.32) * mm});
            skLineSegment(sketch, "E693", {"start": v(12.78, 72.32) * mm, "end": v(13.65, 72.35) * mm});
            skLineSegment(sketch, "E694", {"start": v(13.65, 72.35) * mm, "end": v(14.53, 72.33) * mm});
            skLineSegment(sketch, "E695", {"start": v(14.53, 72.33) * mm, "end": v(15.38, 72.33) * mm});
            skLineSegment(sketch, "E696", {"start": v(15.38, 72.33) * mm, "end": v(16.36, 72.38) * mm});
            skLineSegment(sketch, "E697", {"start": v(16.36, 72.38) * mm, "end": v(17.25, 72.53) * mm});
            skLineSegment(sketch, "E698", {"start": v(17.25, 72.53) * mm, "end": v(18.03, 72.79) * mm});
            skLineSegment(sketch, "E699", {"start": v(18.03, 72.79) * mm, "end": v(18.69, 73.16) * mm});
            skLineSegment(sketch, "E700", {"start": v(18.69, 73.16) * mm, "end": v(19.22, 73.68) * mm});
            skLineSegment(sketch, "E701", {"start": v(19.22, 73.68) * mm, "end": v(19.61, 74.36) * mm});
            skLineSegment(sketch, "E702", {"start": v(19.61, 74.36) * mm, "end": v(19.85, 75.22) * mm});
            skLineSegment(sketch, "E703", {"start": v(19.85, 75.22) * mm, "end": v(19.94, 76.28) * mm});
            skLineSegment(sketch, "E704", {"start": v(19.94, 76.28) * mm, "end": v(19.93, 78.09) * mm});
            skLineSegment(sketch, "E705", {"start": v(19.93, 78.09) * mm, "end": v(19.93, 79.9) * mm});
            skLineSegment(sketch, "E706", {"start": v(19.93, 79.9) * mm, "end": v(19.93, 81.71) * mm});
            skLineSegment(sketch, "E707", {"start": v(19.93, 81.71) * mm, "end": v(19.93, 83.52) * mm});
            skLineSegment(sketch, "E708", {"start": v(19.93, 83.52) * mm, "end": v(19.94, 85.34) * mm});
            skLineSegment(sketch, "E709", {"start": v(19.94, 85.34) * mm, "end": v(19.94, 87.15) * mm});
            skLineSegment(sketch, "E710", {"start": v(19.94, 87.15) * mm, "end": v(19.93, 88.96) * mm});
            skLineSegment(sketch, "E711", {"start": v(19.93, 88.96) * mm, "end": v(19.93, 90.77) * mm});
            skLineSegment(sketch, "E712", {"start": v(19.93, 90.77) * mm, "end": v(19.88, 91.61) * mm});
            skLineSegment(sketch, "E713", {"start": v(19.88, 91.61) * mm, "end": v(19.73, 92.37) * mm});
            skLineSegment(sketch, "E714", {"start": v(19.73, 92.37) * mm, "end": v(19.48, 93.03) * mm});
            skLineSegment(sketch, "E715", {"start": v(19.48, 93.03) * mm, "end": v(19.1, 93.6) * mm});
            skLineSegment(sketch, "E716", {"start": v(19.1, 93.6) * mm, "end": v(18.62, 94.05) * mm});
            skLineSegment(sketch, "E717", {"start": v(18.62, 94.05) * mm, "end": v(18.01, 94.38) * mm});
            skLineSegment(sketch, "E718", {"start": v(18.01, 94.38) * mm, "end": v(17.27, 94.58) * mm});
            skLineSegment(sketch, "E719", {"start": v(17.27, 94.58) * mm, "end": v(16.4, 94.65) * mm});
            skLineSegment(sketch, "E720", {"start": v(16.4, 94.65) * mm, "end": v(15.3, 94.66) * mm});
            skLineSegment(sketch, "E721", {"start": v(15.3, 94.66) * mm, "end": v(14.25, 94.73) * mm});
            skLineSegment(sketch, "E722", {"start": v(14.25, 94.73) * mm, "end": v(13.24, 94.88) * mm});
            skLineSegment(sketch, "E723", {"start": v(13.24, 94.88) * mm, "end": v(12.27, 95.15) * mm});
            skLineSegment(sketch, "E724", {"start": v(12.27, 95.15) * mm, "end": v(11.38, 95.56) * mm});
            skLineSegment(sketch, "E725", {"start": v(11.38, 95.56) * mm, "end": v(10.56, 96.14) * mm});
            skLineSegment(sketch, "E726", {"start": v(10.56, 96.14) * mm, "end": v(9.82, 96.92) * mm});
            skLineSegment(sketch, "E727", {"start": v(9.82, 96.92) * mm, "end": v(9.18, 97.94) * mm});
            skLineSegment(sketch, "E728", {"start": v(9.18, 97.94) * mm, "end": v(8.98, 98.24) * mm});
            skLineSegment(sketch, "E729", {"start": v(8.98, 98.24) * mm, "end": v(8.74, 98.46) * mm});
            skLineSegment(sketch, "E730", {"start": v(8.74, 98.46) * mm, "end": v(8.46, 98.6) * mm});
            skLineSegment(sketch, "E731", {"start": v(8.46, 98.6) * mm, "end": v(8.17, 98.65) * mm});
            skLineSegment(sketch, "E732", {"start": v(8.17, 98.65) * mm, "end": v(7.88, 98.63) * mm});
            skLineSegment(sketch, "E733", {"start": v(7.88, 98.63) * mm, "end": v(7.6, 98.52) * mm});
            skLineSegment(sketch, "E734", {"start": v(7.6, 98.52) * mm, "end": v(7.35, 98.32) * mm});
            skLineSegment(sketch, "E735", {"start": v(7.35, 98.32) * mm, "end": v(7.15, 98.03) * mm});
            skLineSegment(sketch, "E736", {"start": v(7.15, 98.03) * mm, "end": v(6.45, 96.98) * mm});
            skLineSegment(sketch, "E737", {"start": v(6.45, 96.98) * mm, "end": v(5.65, 96.17) * mm});
            skLineSegment(sketch, "E738", {"start": v(5.65, 96.17) * mm, "end": v(4.76, 95.58) * mm});
            skLineSegment(sketch, "E739", {"start": v(4.76, 95.58) * mm, "end": v(3.8, 95.16) * mm});
            skLineSegment(sketch, "E740", {"start": v(3.8, 95.16) * mm, "end": v(2.78, 94.89) * mm});
            skLineSegment(sketch, "E741", {"start": v(2.78, 94.89) * mm, "end": v(1.7, 94.72) * mm});
            skLineSegment(sketch, "E742", {"start": v(1.7, 94.72) * mm, "end": v(0.59, 94.63) * mm});
            skLineSegment(sketch, "E743", {"start": v(0.59, 94.63) * mm, "end": v(-0.56, 94.58) * mm});
            skLineSegment(sketch, "E744", {"start": v(-0.56, 94.58) * mm, "end": v(-1.45, 94.46) * mm});
            skLineSegment(sketch, "E745", {"start": v(-1.45, 94.46) * mm, "end": v(-2.16, 94.19) * mm});
            skLineSegment(sketch, "E746", {"start": v(-2.16, 94.19) * mm, "end": v(-2.7, 93.78) * mm});
            skLineSegment(sketch, "E747", {"start": v(-2.7, 93.78) * mm, "end": v(-3.12, 93.25) * mm});
            skLineSegment(sketch, "E748", {"start": v(-3.12, 93.25) * mm, "end": v(-3.42, 92.62) * mm});
            skLineSegment(sketch, "E749", {"start": v(-3.42, 92.62) * mm, "end": v(-3.6, 91.91) * mm});
            skLineSegment(sketch, "E750", {"start": v(-3.6, 91.91) * mm, "end": v(-3.71, 91.15) * mm});
            skLineSegment(sketch, "E751", {"start": v(-3.71, 91.15) * mm, "end": v(-3.75, 90.35) * mm});
            skLineSegment(sketch, "E752", {"start": v(-3.75, 90.35) * mm, "end": v(-3.76, 88.91) * mm});
            skLineSegment(sketch, "E753", {"start": v(-3.76, 88.91) * mm, "end": v(-3.75, 87.47) * mm});
            skLineSegment(sketch, "E754", {"start": v(-3.75, 87.47) * mm, "end": v(-3.74, 86.04) * mm});
            skLineSegment(sketch, "E755", {"start": v(-3.74, 86.04) * mm, "end": v(-3.73, 84.6) * mm});
            skLineSegment(sketch, "E756", {"start": v(-3.73, 84.6) * mm, "end": v(-3.73, 83.16) * mm});
            skLineSegment(sketch, "E757", {"start": v(-3.73, 83.16) * mm, "end": v(-3.74, 81.72) * mm});
            skLineSegment(sketch, "E758", {"start": v(-3.74, 81.72) * mm, "end": v(-3.78, 80.29) * mm});
            skLineSegment(sketch, "E759", {"start": v(-3.78, 80.29) * mm, "end": v(-3.84, 78.86) * mm});
            skLineSegment(sketch, "E760", {"start": v(-3.84, 78.86) * mm, "end": v(-3.86, 77.26) * mm});
            skLineSegment(sketch, "E761", {"start": v(-3.86, 77.26) * mm, "end": v(-3.7, 75.86) * mm});
            skLineSegment(sketch, "E762", {"start": v(-3.7, 75.86) * mm, "end": v(-3.35, 74.66) * mm});
            skLineSegment(sketch, "E763", {"start": v(-3.35, 74.66) * mm, "end": v(-2.77, 73.68) * mm});
            skLineSegment(sketch, "E764", {"start": v(-2.77, 73.68) * mm, "end": v(-1.94, 72.95) * mm});
            skLineSegment(sketch, "E765", {"start": v(-1.94, 72.95) * mm, "end": v(-0.83, 72.46) * mm});
            skLineSegment(sketch, "E766", {"start": v(-0.83, 72.46) * mm, "end": v(0.57, 72.24) * mm});
            skLineSegment(sketch, "E767", {"start": v(0.57, 72.24) * mm, "end": v(2.3, 72.3) * mm});
            skLineSegment(sketch, "E768", {"start": v(2.3, 72.3) * mm, "end": v(3.03, 72.33) * mm});
            skLineSegment(sketch, "E769", {"start": v(3.03, 72.33) * mm, "end": v(3.72, 72.29) * mm});
            skLineSegment(sketch, "E770", {"start": v(3.72, 72.29) * mm, "end": v(4.36, 72.14) * mm});
            skLineSegment(sketch, "E771", {"start": v(4.36, 72.14) * mm, "end": v(4.92, 71.88) * mm});
            skLineSegment(sketch, "E772", {"start": v(4.92, 71.88) * mm, "end": v(5.38, 71.49) * mm});
            skLineSegment(sketch, "E773", {"start": v(5.38, 71.49) * mm, "end": v(5.73, 70.96) * mm});
            skLineSegment(sketch, "E774", {"start": v(5.73, 70.96) * mm, "end": v(5.95, 70.27) * mm});
            skLineSegment(sketch, "E775", {"start": v(5.95, 70.27) * mm, "end": v(6.01, 69.4) * mm});
            skLineSegment(sketch, "E776", {"start": v(6.01, 69.4) * mm, "end": v(5.9, 68.55) * mm});
            skLineSegment(sketch, "E777", {"start": v(5.9, 68.55) * mm, "end": v(5.65, 67.89) * mm});
            skLineSegment(sketch, "E778", {"start": v(5.65, 67.89) * mm, "end": v(5.27, 67.4) * mm});
            skLineSegment(sketch, "E779", {"start": v(5.27, 67.4) * mm, "end": v(4.77, 67.06) * mm});
            skLineSegment(sketch, "E780", {"start": v(4.77, 67.06) * mm, "end": v(4.2, 66.84) * mm});
            skLineSegment(sketch, "E781", {"start": v(4.2, 66.84) * mm, "end": v(3.54, 66.7) * mm});
            skLineSegment(sketch, "E782", {"start": v(3.54, 66.7) * mm, "end": v(2.85, 66.65) * mm});
            skLineSegment(sketch, "E783", {"start": v(2.85, 66.65) * mm, "end": v(2.13, 66.63) * mm});
            skLineSegment(sketch, "E784", {"start": v(2.13, 66.63) * mm, "end": v(0, 66.62) * mm});
            skLineSegment(sketch, "E785", {"start": v(0, 66.62) * mm, "end": v(-2.12, 66.61) * mm});
            skLineSegment(sketch, "E786", {"start": v(-2.12, 66.61) * mm, "end": v(-4.24, 66.6) * mm});
            skLineSegment(sketch, "E787", {"start": v(-4.24, 66.6) * mm, "end": v(-6.37, 66.6) * mm});
            skLineSegment(sketch, "E788", {"start": v(-6.37, 66.6) * mm, "end": v(-8.5, 66.6) * mm});
            skLineSegment(sketch, "E789", {"start": v(-8.5, 66.6) * mm, "end": v(-10.62, 66.6) * mm});
            skLineSegment(sketch, "E790", {"start": v(-10.62, 66.6) * mm, "end": v(-12.74, 66.62) * mm});
            skLineSegment(sketch, "E791", {"start": v(-12.74, 66.62) * mm, "end": v(-14.86, 66.64) * mm});
            skLineSegment(sketch, "E792", {"start": v(-14.86, 66.64) * mm, "end": v(-15.65, 66.63) * mm});
            skLineSegment(sketch, "E793", {"start": v(-15.65, 66.63) * mm, "end": v(-16.47, 66.61) * mm});
            skLineSegment(sketch, "E794", {"start": v(-16.47, 66.61) * mm, "end": v(-17.27, 66.64) * mm});
            skLineSegment(sketch, "E795", {"start": v(-17.27, 66.64) * mm, "end": v(-18.02, 66.77) * mm});
            skLineSegment(sketch, "E796", {"start": v(-18.02, 66.77) * mm, "end": v(-18.69, 67.05) * mm});
            skLineSegment(sketch, "E797", {"start": v(-18.69, 67.05) * mm, "end": v(-19.23, 67.54) * mm});
            skLineSegment(sketch, "E798", {"start": v(-19.23, 67.54) * mm, "end": v(-19.6, 68.29) * mm});
            skLineSegment(sketch, "E799", {"start": v(-19.6, 68.29) * mm, "end": v(-19.77, 69.35) * mm});
            skLineSegment(sketch, "E800", {"start": v(-19.77, 69.35) * mm, "end": v(-19.7, 70.44) * mm});
            skLineSegment(sketch, "E801", {"start": v(-19.7, 70.44) * mm, "end": v(-19.4, 71.23) * mm});
            skLineSegment(sketch, "E802", {"start": v(-19.4, 71.23) * mm, "end": v(-18.91, 71.78) * mm});
            skLineSegment(sketch, "E803", {"start": v(-18.91, 71.78) * mm, "end": v(-18.29, 72.12) * mm});
            skLineSegment(sketch, "E804", {"start": v(-18.29, 72.12) * mm, "end": v(-17.56, 72.3) * mm});
            skLineSegment(sketch, "E805", {"start": v(-17.56, 72.3) * mm, "end": v(-16.76, 72.36) * mm});
            skLineSegment(sketch, "E806", {"start": v(-16.76, 72.36) * mm, "end": v(-15.95, 72.35) * mm});
            skLineSegment(sketch, "E807", {"start": v(-15.95, 72.35) * mm, "end": v(-15.14, 72.3) * mm});
            skLineSegment(sketch, "E808", {"start": v(-15.14, 72.3) * mm, "end": v(-13.76, 72.32) * mm});
            skLineSegment(sketch, "E809", {"start": v(-13.76, 72.32) * mm, "end": v(-12.62, 72.54) * mm});
            skLineSegment(sketch, "E810", {"start": v(-12.62, 72.54) * mm, "end": v(-11.7, 72.96) * mm});
            skLineSegment(sketch, "E811", {"start": v(-11.7, 72.96) * mm, "end": v(-11.01, 73.57) * mm});
            skLineSegment(sketch, "E812", {"start": v(-11.01, 73.57) * mm, "end": v(-10.51, 74.36) * mm});
            skLineSegment(sketch, "E813", {"start": v(-10.51, 74.36) * mm, "end": v(-10.2, 75.32) * mm});
            skLineSegment(sketch, "E814", {"start": v(-10.2, 75.32) * mm, "end": v(-10.03, 76.46) * mm});
            skLineSegment(sketch, "E815", {"start": v(-10.03, 76.46) * mm, "end": v(-10.02, 77.77) * mm});
            skLineSegment(sketch, "E816", {"start": v(-10.02, 77.77) * mm, "end": v(-10.07, 79.33) * mm});
            skLineSegment(sketch, "E817", {"start": v(-10.07, 79.33) * mm, "end": v(-10.1, 80.9) * mm});
            skLineSegment(sketch, "E818", {"start": v(-10.1, 80.9) * mm, "end": v(-10.12, 82.45) * mm});
            skLineSegment(sketch, "E819", {"start": v(-10.12, 82.45) * mm, "end": v(-10.12, 84.02) * mm});
            skLineSegment(sketch, "E820", {"start": v(-10.12, 84.02) * mm, "end": v(-10.11, 85.58) * mm});
            skLineSegment(sketch, "E821", {"start": v(-10.11, 85.58) * mm, "end": v(-10.1, 87.14) * mm});
            skLineSegment(sketch, "E822", {"start": v(-10.1, 87.14) * mm, "end": v(-10.08, 88.7) * mm});
            skLineSegment(sketch, "E823", {"start": v(-10.08, 88.7) * mm, "end": v(-10.06, 90.27) * mm});
            skLineSegment(sketch, "E824", {"start": v(-10.06, 90.27) * mm, "end": v(-10.1, 91.26) * mm});
            skLineSegment(sketch, "E825", {"start": v(-10.1, 91.26) * mm, "end": v(-10.26, 92.16) * mm});
            skLineSegment(sketch, "E826", {"start": v(-10.26, 92.16) * mm, "end": v(-10.53, 92.93) * mm});
            skLineSegment(sketch, "E827", {"start": v(-10.53, 92.93) * mm, "end": v(-10.94, 93.58) * mm});
            skLineSegment(sketch, "E828", {"start": v(-10.94, 93.58) * mm, "end": v(-11.5, 94.1) * mm});
            skLineSegment(sketch, "E829", {"start": v(-11.5, 94.1) * mm, "end": v(-12.2, 94.45) * mm});
            skLineSegment(sketch, "E830", {"start": v(-12.2, 94.45) * mm, "end": v(-13.07, 94.64) * mm});
            skLineSegment(sketch, "E831", {"start": v(-13.07, 94.64) * mm, "end": v(-14.12, 94.66) * mm});
            skLineSegment(sketch, "E832", {"start": v(-14.12, 94.66) * mm, "end": v(-15.22, 94.67) * mm});
            skLineSegment(sketch, "E833", {"start": v(-15.22, 94.67) * mm, "end": v(-16.23, 94.83) * mm});
            skLineSegment(sketch, "E834", {"start": v(-16.23, 94.83) * mm, "end": v(-17.16, 95.13) * mm});
            skLineSegment(sketch, "E835", {"start": v(-17.16, 95.13) * mm, "end": v(-18.04, 95.54) * mm});
            skLineSegment(sketch, "E836", {"start": v(-18.04, 95.54) * mm, "end": v(-18.9, 96.04) * mm});
            skLineSegment(sketch, "E837", {"start": v(-18.9, 96.04) * mm, "end": v(-19.73, 96.6) * mm});
            skLineSegment(sketch, "E838", {"start": v(-19.73, 96.6) * mm, "end": v(-20.57, 97.21) * mm});
            skLineSegment(sketch, "E839", {"start": v(-20.57, 97.21) * mm, "end": v(-21.44, 97.85) * mm});
            skLineSegment(sketch, "E840", {"start": v(-21.44, 97.85) * mm, "end": v(-22.23, 98.14) * mm});
            skLineSegment(sketch, "E841", {"start": v(-22.23, 98.14) * mm, "end": v(-22.96, 97.9) * mm});
            skLineSegment(sketch, "E842", {"start": v(-22.96, 97.9) * mm, "end": v(-23.67, 97.3) * mm});
            skLineSegment(sketch, "E843", {"start": v(-23.67, 97.3) * mm, "end": v(-24.4, 96.5) * mm});
            skLineSegment(sketch, "E844", {"start": v(-24.4, 96.5) * mm, "end": v(-25.18, 95.67) * mm});
            skLineSegment(sketch, "E845", {"start": v(-25.18, 95.67) * mm, "end": v(-26.06, 95) * mm});
            skLineSegment(sketch, "E846", {"start": v(-26.06, 95) * mm, "end": v(-27.07, 94.62) * mm});
            skLineSegment(sketch, "E847", {"start": v(-27.07, 94.62) * mm, "end": v(-28.25, 94.73) * mm});
            skLineSegment(sketch, "E848", {"start": v(-28.25, 94.73) * mm, "end": v(-28.42, 94.76) * mm});
            skLineSegment(sketch, "E849", {"start": v(-28.42, 94.76) * mm, "end": v(-28.6, 94.78) * mm});
            skLineSegment(sketch, "E850", {"start": v(-28.6, 94.78) * mm, "end": v(-28.79, 94.77) * mm});
            skLineSegment(sketch, "E851", {"start": v(-28.79, 94.77) * mm, "end": v(-28.98, 94.76) * mm});
            skLineSegment(sketch, "E852", {"start": v(-28.98, 94.76) * mm, "end": v(-29.17, 94.74) * mm});
            skLineSegment(sketch, "E853", {"start": v(-29.17, 94.74) * mm, "end": v(-29.36, 94.72) * mm});
            skLineSegment(sketch, "E854", {"start": v(-29.36, 94.72) * mm, "end": v(-29.55, 94.7) * mm});
            skLineSegment(sketch, "E855", {"start": v(-29.55, 94.7) * mm, "end": v(-29.74, 94.71) * mm});
            skLineSegment(sketch, "E856", {"start": v(-29.74, 94.71) * mm, "end": v(-30.95, 94.71) * mm});
            skLineSegment(sketch, "E857", {"start": v(-30.95, 94.71) * mm, "end": v(-31.96, 94.53) * mm});
            skLineSegment(sketch, "E858", {"start": v(-31.96, 94.53) * mm, "end": v(-32.78, 94.17) * mm});
            skLineSegment(sketch, "E859", {"start": v(-32.78, 94.17) * mm, "end": v(-33.42, 93.64) * mm});
            skLineSegment(sketch, "E860", {"start": v(-33.42, 93.64) * mm, "end": v(-33.9, 92.94) * mm});
            skLineSegment(sketch, "E861", {"start": v(-33.9, 92.94) * mm, "end": v(-34.22, 92.07) * mm});
            skLineSegment(sketch, "E862", {"start": v(-34.22, 92.07) * mm, "end": v(-34.39, 91.06) * mm});
            skLineSegment(sketch, "E863", {"start": v(-34.39, 91.06) * mm, "end": v(-34.41, 89.88) * mm});
            skLineSegment(sketch, "E864", {"start": v(-34.41, 89.88) * mm, "end": v(-34.37, 88.57) * mm});
            skLineSegment(sketch, "E865", {"start": v(-34.37, 88.57) * mm, "end": v(-34.33, 87.26) * mm});
            skLineSegment(sketch, "E866", {"start": v(-34.33, 87.26) * mm, "end": v(-34.3, 85.95) * mm});
            skLineSegment(sketch, "E867", {"start": v(-34.3, 85.95) * mm, "end": v(-34.28, 84.63) * mm});
            skLineSegment(sketch, "E868", {"start": v(-34.28, 84.63) * mm, "end": v(-34.29, 83.32) * mm});
            skLineSegment(sketch, "E869", {"start": v(-34.29, 83.32) * mm, "end": v(-34.31, 82) * mm});
            skLineSegment(sketch, "E870", {"start": v(-34.31, 82) * mm, "end": v(-34.37, 80.7) * mm});
            skLineSegment(sketch, "E871", {"start": v(-34.37, 80.7) * mm, "end": v(-34.45, 79.4) * mm});
            skLineSegment(sketch, "E872", {"start": v(-34.45, 79.4) * mm, "end": v(-34.52, 77.65) * mm});
            skLineSegment(sketch, "E873", {"start": v(-34.52, 77.65) * mm, "end": v(-34.4, 76.12) * mm});
            skLineSegment(sketch, "E874", {"start": v(-34.4, 76.12) * mm, "end": v(-34.06, 74.8) * mm});
            skLineSegment(sketch, "E875", {"start": v(-34.06, 74.8) * mm, "end": v(-33.47, 73.74) * mm});
            skLineSegment(sketch, "E876", {"start": v(-33.47, 73.74) * mm, "end": v(-32.6, 72.93) * mm});
            skLineSegment(sketch, "E877", {"start": v(-32.6, 72.93) * mm, "end": v(-31.4, 72.4) * mm});
            skLineSegment(sketch, "E878", {"start": v(-31.4, 72.4) * mm, "end": v(-29.87, 72.2) * mm});
            skLineSegment(sketch, "E879", {"start": v(-29.87, 72.2) * mm, "end": v(-27.95, 72.3) * mm});
            skLineSegment(sketch, "E880", {"start": v(-27.95, 72.3) * mm, "end": v(-27.23, 72.35) * mm});
            skLineSegment(sketch, "E881", {"start": v(-27.23, 72.35) * mm, "end": v(-26.54, 72.32) * mm});
            skLineSegment(sketch, "E882", {"start": v(-26.54, 72.32) * mm, "end": v(-25.9, 72.19) * mm});
            skLineSegment(sketch, "E883", {"start": v(-25.9, 72.19) * mm, "end": v(-25.35, 71.94) * mm});
            skLineSegment(sketch, "E884", {"start": v(-25.35, 71.94) * mm, "end": v(-24.88, 71.55) * mm});
            skLineSegment(sketch, "E885", {"start": v(-24.88, 71.55) * mm, "end": v(-24.52, 71.02) * mm});
            skLineSegment(sketch, "E886", {"start": v(-24.52, 71.02) * mm, "end": v(-24.3, 70.33) * mm});
            skLineSegment(sketch, "E887", {"start": v(-24.3, 70.33) * mm, "end": v(-24.22, 69.46) * mm});
            skLineSegment(sketch, "E888", {"start": v(-24.22, 69.46) * mm, "end": v(-24.3, 68.6) * mm});
            skLineSegment(sketch, "E889", {"start": v(-24.3, 68.6) * mm, "end": v(-24.54, 67.93) * mm});
            skLineSegment(sketch, "E890", {"start": v(-24.54, 67.93) * mm, "end": v(-24.9, 67.43) * mm});
            skLineSegment(sketch, "E891", {"start": v(-24.9, 67.43) * mm, "end": v(-25.38, 67.08) * mm});
            skLineSegment(sketch, "E892", {"start": v(-25.38, 67.08) * mm, "end": v(-25.95, 66.85) * mm});
            skLineSegment(sketch, "E893", {"start": v(-25.95, 66.85) * mm, "end": v(-26.59, 66.72) * mm});
            skLineSegment(sketch, "E894", {"start": v(-26.59, 66.72) * mm, "end": v(-27.28, 66.65) * mm});
            skLineSegment(sketch, "E895", {"start": v(-27.28, 66.65) * mm, "end": v(-28, 66.62) * mm});
            skLineSegment(sketch, "E896", {"start": v(-28, 66.62) * mm, "end": v(-31.56, 66.57) * mm});
            skLineSegment(sketch, "E897", {"start": v(-31.56, 66.57) * mm, "end": v(-35.12, 66.54) * mm});
            skLineSegment(sketch, "E898", {"start": v(-35.12, 66.54) * mm, "end": v(-38.67, 66.58) * mm});
            skLineSegment(sketch, "E899", {"start": v(-38.67, 66.58) * mm, "end": v(-42.2, 66.71) * mm});
            skLineSegment(sketch, "E900", {"start": v(-42.2, 66.71) * mm, "end": v(-45.74, 67) * mm});
            skLineSegment(sketch, "E901", {"start": v(-45.74, 67) * mm, "end": v(-49.25, 67.47) * mm});
            skLineSegment(sketch, "E902", {"start": v(-49.25, 67.47) * mm, "end": v(-52.75, 68.17) * mm});
            skLineSegment(sketch, "E903", {"start": v(-52.75, 68.17) * mm, "end": v(-56.22, 69.15) * mm});
            skLineSegment(sketch, "E904", {"start": v(-56.22, 69.15) * mm, "end": v(-56.96, 69.42) * mm});
            skLineSegment(sketch, "E905", {"start": v(-56.96, 69.42) * mm, "end": v(-57.74, 69.75) * mm});
            skLineSegment(sketch, "E906", {"start": v(-57.74, 69.75) * mm, "end": v(-58.54, 70.06) * mm});
            skLineSegment(sketch, "E907", {"start": v(-58.54, 70.06) * mm, "end": v(-59.34, 70.32) * mm});
            skLineSegment(sketch, "E908", {"start": v(-59.34, 70.32) * mm, "end": v(-60.13, 70.47) * mm});
            skLineSegment(sketch, "E909", {"start": v(-60.13, 70.47) * mm, "end": v(-60.88, 70.44) * mm});
            skLineSegment(sketch, "E910", {"start": v(-60.88, 70.44) * mm, "end": v(-61.58, 70.19) * mm});
            skLineSegment(sketch, "E911", {"start": v(-61.58, 70.19) * mm, "end": v(-62.21, 69.66) * mm});
            skLineSegment(sketch, "E912", {"start": v(-62.21, 69.66) * mm, "end": v(-62.57, 69.06) * mm});
            skLineSegment(sketch, "E913", {"start": v(-62.57, 69.06) * mm, "end": v(-62.68, 68.4) * mm});
            skLineSegment(sketch, "E914", {"start": v(-62.68, 68.4) * mm, "end": v(-62.61, 67.7) * mm});
            skLineSegment(sketch, "E915", {"start": v(-62.61, 67.7) * mm, "end": v(-62.4, 66.96) * mm});
            skLineSegment(sketch, "E916", {"start": v(-62.4, 66.96) * mm, "end": v(-62.1, 66.22) * mm});
            skLineSegment(sketch, "E917", {"start": v(-62.1, 66.22) * mm, "end": v(-61.74, 65.47) * mm});
            skLineSegment(sketch, "E918", {"start": v(-61.74, 65.47) * mm, "end": v(-61.4, 64.75) * mm});
            skLineSegment(sketch, "E919", {"start": v(-61.4, 64.75) * mm, "end": v(-61.1, 64.05) * mm});
            skLineSegment(sketch, "E920", {"start": v(-61.1, 64.05) * mm, "end": v(-60.64, 62.66) * mm});
            skLineSegment(sketch, "E921", {"start": v(-60.64, 62.66) * mm, "end": v(-60.45, 61.5) * mm});
            skLineSegment(sketch, "E922", {"start": v(-60.45, 61.5) * mm, "end": v(-60.52, 60.55) * mm});
            skLineSegment(sketch, "E923", {"start": v(-60.52, 60.55) * mm, "end": v(-60.86, 59.81) * mm});
            skLineSegment(sketch, "E924", {"start": v(-60.86, 59.81) * mm, "end": v(-61.48, 59.26) * mm});
            skLineSegment(sketch, "E925", {"start": v(-61.48, 59.26) * mm, "end": v(-62.36, 58.9) * mm});
            skLineSegment(sketch, "E926", {"start": v(-62.36, 58.9) * mm, "end": v(-63.53, 58.7) * mm});
            skLineSegment(sketch, "E927", {"start": v(-63.53, 58.7) * mm, "end": v(-64.97, 58.68) * mm});
            skLineSegment(sketch, "E928", {"start": v(-64.97, 58.68) * mm, "end": v(-67.03, 58.74) * mm});
            skLineSegment(sketch, "E929", {"start": v(-67.03, 58.74) * mm, "end": v(-69.1, 58.8) * mm});
            skLineSegment(sketch, "E930", {"start": v(-69.1, 58.8) * mm, "end": v(-71.16, 58.83) * mm});
            skLineSegment(sketch, "E931", {"start": v(-71.16, 58.83) * mm, "end": v(-73.22, 58.85) * mm});
            skLineSegment(sketch, "E932", {"start": v(-73.22, 58.85) * mm, "end": v(-75.29, 58.84) * mm});
            skLineSegment(sketch, "E933", {"start": v(-75.29, 58.84) * mm, "end": v(-77.35, 58.8) * mm});
            skLineSegment(sketch, "E934", {"start": v(-77.35, 58.8) * mm, "end": v(-79.4, 58.74) * mm});
            skLineSegment(sketch, "E935", {"start": v(-79.4, 58.74) * mm, "end": v(-81.46, 58.64) * mm});
            skLineSegment(sketch, "E936", {"start": v(-81.46, 58.64) * mm, "end": v(-83.18, 58.63) * mm});
            skLineSegment(sketch, "E937", {"start": v(-83.18, 58.63) * mm, "end": v(-84.62, 58.82) * mm});
            skLineSegment(sketch, "E938", {"start": v(-84.62, 58.82) * mm, "end": v(-85.8, 59.24) * mm});
            skLineSegment(sketch, "E939", {"start": v(-85.8, 59.24) * mm, "end": v(-86.73, 59.89) * mm});
            skLineSegment(sketch, "E940", {"start": v(-86.73, 59.89) * mm, "end": v(-87.41, 60.79) * mm});
            skLineSegment(sketch, "E941", {"start": v(-87.41, 60.79) * mm, "end": v(-87.88, 61.96) * mm});
            skLineSegment(sketch, "E942", {"start": v(-87.88, 61.96) * mm, "end": v(-88.13, 63.42) * mm});
            skLineSegment(sketch, "E943", {"start": v(-88.13, 63.42) * mm, "end": v(-88.17, 65.18) * mm});
            skLineSegment(sketch, "E944", {"start": v(-88.17, 65.18) * mm, "end": v(-88.08, 69.3) * mm});
            skLineSegment(sketch, "E945", {"start": v(-88.08, 69.3) * mm, "end": v(-88.03, 73.42) * mm});
            skLineSegment(sketch, "E946", {"start": v(-88.03, 73.42) * mm, "end": v(-88, 77.54) * mm});
            skLineSegment(sketch, "E947", {"start": v(-88, 77.54) * mm, "end": v(-88, 81.67) * mm});
            skLineSegment(sketch, "E948", {"start": v(-88, 81.67) * mm, "end": v(-88.03, 85.8) * mm});
            skLineSegment(sketch, "E949", {"start": v(-88.03, 85.8) * mm, "end": v(-88.06, 89.92) * mm});
            skLineSegment(sketch, "E950", {"start": v(-88.06, 89.92) * mm, "end": v(-88.1, 94.04) * mm});
            skLineSegment(sketch, "E951", {"start": v(-88.1, 94.04) * mm, "end": v(-88.15, 98.16) * mm});
            skLineSegment(sketch, "E952", {"start": v(-88.15, 98.16) * mm, "end": v(-88.11, 98.89) * mm});
            skLineSegment(sketch, "E953", {"start": v(-88.11, 98.89) * mm, "end": v(-88.02, 99.69) * mm});
            skLineSegment(sketch, "E954", {"start": v(-88.02, 99.69) * mm, "end": v(-87.93, 100.51) * mm});
            skLineSegment(sketch, "E955", {"start": v(-87.93, 100.51) * mm, "end": v(-87.9, 101.31) * mm});
            skLineSegment(sketch, "E956", {"start": v(-87.9, 101.31) * mm, "end": v(-87.97, 102.04) * mm});
            skLineSegment(sketch, "E957", {"start": v(-87.97, 102.04) * mm, "end": v(-88.22, 102.64) * mm});
            skLineSegment(sketch, "E958", {"start": v(-88.22, 102.64) * mm, "end": v(-88.69, 103.06) * mm});
            skLineSegment(sketch, "E959", {"start": v(-88.69, 103.06) * mm, "end": v(-89.43, 103.24) * mm});
            skLineSegment(sketch, "E960", {"start": v(-89.43, 103.24) * mm, "end": v(-90.37, 103.16) * mm});
            skLineSegment(sketch, "E961", {"start": v(-90.37, 103.16) * mm, "end": v(-91.1, 102.82) * mm});
            skLineSegment(sketch, "E962", {"start": v(-91.1, 102.82) * mm, "end": v(-91.63, 102.26) * mm});
            skLineSegment(sketch, "E963", {"start": v(-91.63, 102.26) * mm, "end": v(-92, 101.54) * mm});
            skLineSegment(sketch, "E964", {"start": v(-92, 101.54) * mm, "end": v(-92.25, 100.7) * mm});
            skLineSegment(sketch, "E965", {"start": v(-92.25, 100.7) * mm, "end": v(-92.4, 99.77) * mm});
            skLineSegment(sketch, "E966", {"start": v(-92.4, 99.77) * mm, "end": v(-92.47, 98.83) * mm});
            skLineSegment(sketch, "E967", {"start": v(-92.47, 98.83) * mm, "end": v(-92.5, 97.9) * mm});
            skLineSegment(sketch, "E968", {"start": v(-92.5, 97.9) * mm, "end": v(-92.5, 97.65) * mm});
            skLineSegment(sketch, "E969", {"start": v(-92.5, 97.65) * mm, "end": v(-92.5, 97.4) * mm});
            skLineSegment(sketch, "E970", {"start": v(-92.5, 97.4) * mm, "end": v(-92.5, 97.15) * mm});
            skLineSegment(sketch, "E971", {"start": v(-92.5, 97.15) * mm, "end": v(-92.5, 96.9) * mm});
            skLineSegment(sketch, "E972", {"start": v(-92.5, 96.9) * mm, "end": v(-92.5, 96.65) * mm});
            skLineSegment(sketch, "E973", {"start": v(-92.5, 96.65) * mm, "end": v(-92.5, 96.4) * mm});
            skLineSegment(sketch, "E974", {"start": v(-92.5, 96.4) * mm, "end": v(-92.5, 96.15) * mm});
            skLineSegment(sketch, "E975", {"start": v(-92.5, 96.15) * mm, "end": v(-92.5, 95.9) * mm});
            skLineSegment(sketch, "E976", {"start": v(-92.5, 95.9) * mm, "end": v(-92.5, 72.9) * mm});
            skLineSegment(sketch, "E977", {"start": v(-92.5, 72.9) * mm, "end": v(-92.5, 49.91) * mm});
            skLineSegment(sketch, "E978", {"start": v(-92.5, 49.91) * mm, "end": v(-92.5, 26.92) * mm});
            skLineSegment(sketch, "E979", {"start": v(-92.5, 26.92) * mm, "end": v(-92.5, 3.92) * mm});
            skLineSegment(sketch, "E980", {"start": v(-92.5, 3.92) * mm, "end": v(-92.5, -19.07) * mm});
            skLineSegment(sketch, "E981", {"start": v(-92.5, -19.07) * mm, "end": v(-92.52, -42.06) * mm});
            skLineSegment(sketch, "E982", {"start": v(-92.52, -42.06) * mm, "end": v(-92.55, -65.06) * mm});
            skLineSegment(sketch, "E983", {"start": v(-92.55, -65.06) * mm, "end": v(-92.58, -88.05) * mm});
            skLineSegment(sketch, "E984", {"start": v(-92.58, -88.05) * mm, "end": v(-92.52, -89.54) * mm});
            skLineSegment(sketch, "E985", {"start": v(-92.52, -89.54) * mm, "end": v(-92.31, -90.9) * mm});
            skLineSegment(sketch, "E986", {"start": v(-92.31, -90.9) * mm, "end": v(-91.96, -92.12) * mm});
            skLineSegment(sketch, "E987", {"start": v(-91.96, -92.12) * mm, "end": v(-91.44, -93.23) * mm});
            skLineSegment(sketch, "E988", {"start": v(-91.44, -93.23) * mm, "end": v(-90.77, -94.26) * mm});
            skLineSegment(sketch, "E989", {"start": v(-90.77, -94.26) * mm, "end": v(-89.92, -95.2) * mm});
            skLineSegment(sketch, "E990", {"start": v(-89.92, -95.2) * mm, "end": v(-88.9, -96.1) * mm});
            skLineSegment(sketch, "E991", {"start": v(-88.9, -96.1) * mm, "end": v(-87.68, -96.94) * mm});
            skLineSegment(sketch, "E992", {"start": v(-87.68, -96.94) * mm, "end": v(-79.75, -101.94) * mm});
            skLineSegment(sketch, "E993", {"start": v(-79.75, -101.94) * mm, "end": v(-71.81, -106.92) * mm});
            skLineSegment(sketch, "E994", {"start": v(-71.81, -106.92) * mm, "end": v(-63.88, -111.92) * mm});
            skLineSegment(sketch, "E995", {"start": v(-63.88, -111.92) * mm, "end": v(-55.97, -116.93) * mm});
            skLineSegment(sketch, "E996", {"start": v(-55.97, -116.93) * mm, "end": v(-48.07, -121.99) * mm});
            skLineSegment(sketch, "E997", {"start": v(-48.07, -121.99) * mm, "end": v(-40.22, -127.1) * mm});
            skLineSegment(sketch, "E998", {"start": v(-40.22, -127.1) * mm, "end": v(-32.4, -132.26) * mm});
            skLineSegment(sketch, "E999", {"start": v(-32.4, -132.26) * mm, "end": v(-24.65, -137.52) * mm});
            skLineSegment(sketch, "E1000", {"start": v(-24.65, -137.52) * mm, "end": v(-21.02, -139.83) * mm});
            skLineSegment(sketch, "E1001", {"start": v(-21.02, -139.83) * mm, "end": v(-17.36, -141.78) * mm});
            skLineSegment(sketch, "E1002", {"start": v(-17.36, -141.78) * mm, "end": v(-13.66, -143.38) * mm});
            skLineSegment(sketch, "E1003", {"start": v(-13.66, -143.38) * mm, "end": v(-9.9, -144.62) * mm});
            skLineSegment(sketch, "E1004", {"start": v(-9.9, -144.62) * mm, "end": v(-6.04, -145.49) * mm});
            skLineSegment(sketch, "E1005", {"start": v(-6.04, -145.49) * mm, "end": v(-2.1, -145.99) * mm});
            skLineSegment(sketch, "E1006", {"start": v(-2.1, -145.99) * mm, "end": v(1.97, -146.11) * mm});
            skLineSegment(sketch, "E1007", {"start": v(1.97, -146.11) * mm, "end": v(6.18, -145.86) * mm});
            skLineSegment(sketch, "E1008", {"start": v(6.18, -145.86) * mm, "end": v(7.37, -145.72) * mm});
            skLineSegment(sketch, "E1009", {"start": v(7.37, -145.72) * mm, "end": v(8.54, -145.55) * mm});
            skLineSegment(sketch, "E1010", {"start": v(8.54, -145.55) * mm, "end": v(9.68, -145.33) * mm});
            skLineSegment(sketch, "E1011", {"start": v(9.68, -145.33) * mm, "end": v(10.8, -145.06) * mm});
            skLineSegment(sketch, "E1012", {"start": v(10.8, -145.06) * mm, "end": v(11.89, -144.71) * mm});
            skLineSegment(sketch, "E1013", {"start": v(11.89, -144.71) * mm, "end": v(12.96, -144.3) * mm});
            skLineSegment(sketch, "E1014", {"start": v(12.96, -144.3) * mm, "end": v(14.02, -143.78) * mm});
            skLineSegment(sketch, "E1015", {"start": v(14.02, -143.78) * mm, "end": v(15.07, -143.16) * mm});
            skLineSegment(sketch, "E1016", {"start": v(15.07, -143.16) * mm, "end": v(24, -137.4) * mm});
            skLineSegment(sketch, "E1017", {"start": v(24, -137.4) * mm, "end": v(32.92, -131.64) * mm});
            skLineSegment(sketch, "E1018", {"start": v(32.92, -131.64) * mm, "end": v(41.84, -125.88) * mm});
            skLineSegment(sketch, "E1019", {"start": v(41.84, -125.88) * mm, "end": v(50.77, -120.14) * mm});
            skLineSegment(sketch, "E1020", {"start": v(50.77, -120.14) * mm, "end": v(59.71, -114.4) * mm});
            skLineSegment(sketch, "E1021", {"start": v(59.71, -114.4) * mm, "end": v(68.66, -108.68) * mm});
            skLineSegment(sketch, "E1022", {"start": v(68.66, -108.68) * mm, "end": v(77.62, -102.98) * mm});
            skLineSegment(sketch, "E1023", {"start": v(77.62, -102.98) * mm, "end": v(86.6, -97.3) * mm});
            skLineSegment(sketch, "E1024", {"start": v(86.6, -97.3) * mm, "end": v(88, -96.32) * mm});
            skLineSegment(sketch, "E1025", {"start": v(88, -96.32) * mm, "end": v(89.15, -95.28) * mm});
            skLineSegment(sketch, "E1026", {"start": v(89.15, -95.28) * mm, "end": v(90.08, -94.18) * mm});
            skLineSegment(sketch, "E1027", {"start": v(90.08, -94.18) * mm, "end": v(90.81, -93) * mm});
            skLineSegment(sketch, "E1028", {"start": v(90.81, -93) * mm, "end": v(91.34, -91.72) * mm});
            skLineSegment(sketch, "E1029", {"start": v(91.34, -91.72) * mm, "end": v(91.7, -90.33) * mm});
            skLineSegment(sketch, "E1030", {"start": v(91.7, -90.33) * mm, "end": v(91.9, -88.8) * mm});
            skLineSegment(sketch, "E1031", {"start": v(91.9, -88.8) * mm, "end": v(91.96, -87.13) * mm});
            skLineSegment(sketch, "E1032", {"start": v(91.96, -87.13) * mm, "end": v(91.9, -75.7) * mm});
            skLineSegment(sketch, "E1033", {"start": v(91.9, -75.7) * mm, "end": v(91.87, -64.26) * mm});
            skLineSegment(sketch, "E1034", {"start": v(91.87, -64.26) * mm, "end": v(91.85, -52.83) * mm});
            skLineSegment(sketch, "E1035", {"start": v(91.85, -52.83) * mm, "end": v(91.85, -41.4) * mm});
            skLineSegment(sketch, "E1036", {"start": v(91.85, -41.4) * mm, "end": v(91.85, -29.96) * mm});
            skLineSegment(sketch, "E1037", {"start": v(91.85, -29.96) * mm, "end": v(91.85, -18.52) * mm});
            skLineSegment(sketch, "E1038", {"start": v(91.85, -18.52) * mm, "end": v(91.86, -7.09) * mm});
            skLineSegment(sketch, "E1039", {"start": v(91.86, -7.09) * mm, "end": v(91.86, 4.35) * mm});
            skLineSegment(sketch, "E1040", {"start": v(23.45, -143) * mm, "end": v(23.83, -143.14) * mm});
            skLineSegment(sketch, "E1041", {"start": v(23.83, -143.14) * mm, "end": v(24.13, -143.26) * mm});
            skLineSegment(sketch, "E1042", {"start": v(24.13, -143.26) * mm, "end": v(24.36, -143.36) * mm});
            skLineSegment(sketch, "E1043", {"start": v(24.36, -143.36) * mm, "end": v(24.54, -143.43) * mm});
            skLineSegment(sketch, "E1044", {"start": v(24.54, -143.43) * mm, "end": v(24.67, -143.49) * mm});
            skLineSegment(sketch, "E1045", {"start": v(24.67, -143.49) * mm, "end": v(24.76, -143.52) * mm});
            skLineSegment(sketch, "E1046", {"start": v(24.76, -143.52) * mm, "end": v(24.83, -143.53) * mm});
            skLineSegment(sketch, "E1047", {"start": v(24.83, -143.53) * mm, "end": v(24.88, -143.53) * mm});
            skLineSegment(sketch, "E1048", {"start": v(24.88, -143.53) * mm, "end": v(25.2, -143.49) * mm});
            skLineSegment(sketch, "E1049", {"start": v(25.2, -143.49) * mm, "end": v(25.5, -143.45) * mm});
            skLineSegment(sketch, "E1050", {"start": v(25.5, -143.45) * mm, "end": v(25.8, -143.4) * mm});
            skLineSegment(sketch, "E1051", {"start": v(25.8, -143.4) * mm, "end": v(26.11, -143.35) * mm});
            skLineSegment(sketch, "E1052", {"start": v(26.11, -143.35) * mm, "end": v(26.42, -143.3) * mm});
            skLineSegment(sketch, "E1053", {"start": v(26.42, -143.3) * mm, "end": v(26.72, -143.25) * mm});
            skLineSegment(sketch, "E1054", {"start": v(26.72, -143.25) * mm, "end": v(27.03, -143.19) * mm});
            skLineSegment(sketch, "E1055", {"start": v(27.03, -143.19) * mm, "end": v(27.33, -143.12) * mm});
            skLineSegment(sketch, "E1056", {"start": v(27.33, -143.12) * mm, "end": v(44.2, -138.4) * mm});
            skLineSegment(sketch, "E1057", {"start": v(44.2, -138.4) * mm, "end": v(60.28, -132.4) * mm});
            skLineSegment(sketch, "E1058", {"start": v(60.28, -132.4) * mm, "end": v(75.6, -125.15) * mm});
            skLineSegment(sketch, "E1059", {"start": v(75.6, -125.15) * mm, "end": v(90.19, -116.73) * mm});
            skLineSegment(sketch, "E1060", {"start": v(90.19, -116.73) * mm, "end": v(104.1, -107.2) * mm});
            skLineSegment(sketch, "E1061", {"start": v(104.1, -107.2) * mm, "end": v(117.34, -96.6) * mm});
            skLineSegment(sketch, "E1062", {"start": v(117.34, -96.6) * mm, "end": v(129.97, -85.01) * mm});
            skLineSegment(sketch, "E1063", {"start": v(129.97, -85.01) * mm, "end": v(142.01, -72.5) * mm});
            skLineSegment(sketch, "E1064", {"start": v(142.01, -72.5) * mm, "end": v(144.47, -69.88) * mm});
            skLineSegment(sketch, "E1065", {"start": v(144.47, -69.88) * mm, "end": v(146.99, -67.42) * mm});
            skLineSegment(sketch, "E1066", {"start": v(146.99, -67.42) * mm, "end": v(149.6, -65.15) * mm});
            skLineSegment(sketch, "E1067", {"start": v(149.6, -65.15) * mm, "end": v(152.33, -63.1) * mm});
            skLineSegment(sketch, "E1068", {"start": v(152.33, -63.1) * mm, "end": v(155.22, -61.34) * mm});
            skLineSegment(sketch, "E1069", {"start": v(155.22, -61.34) * mm, "end": v(158.3, -59.87) * mm});
            skLineSegment(sketch, "E1070", {"start": v(158.3, -59.87) * mm, "end": v(161.6, -58.75) * mm});
            skLineSegment(sketch, "E1071", {"start": v(161.6, -58.75) * mm, "end": v(165.13, -58) * mm});
            skLineSegment(sketch, "E1072", {"start": v(165.13, -58) * mm, "end": v(166.34, -57.85) * mm});
            skLineSegment(sketch, "E1073", {"start": v(166.34, -57.85) * mm, "end": v(167.57, -57.74) * mm});
            skLineSegment(sketch, "E1074", {"start": v(167.57, -57.74) * mm, "end": v(168.8, -57.66) * mm});
            skLineSegment(sketch, "E1075", {"start": v(168.8, -57.66) * mm, "end": v(170.05, -57.6) * mm});
            skLineSegment(sketch, "E1076", {"start": v(170.05, -57.6) * mm, "end": v(171.3, -57.55) * mm});
            skLineSegment(sketch, "E1077", {"start": v(171.3, -57.55) * mm, "end": v(172.59, -57.5) * mm});
            skLineSegment(sketch, "E1078", {"start": v(172.59, -57.5) * mm, "end": v(173.89, -57.45) * mm});
            skLineSegment(sketch, "E1079", {"start": v(173.89, -57.45) * mm, "end": v(175.21, -57.39) * mm});
            skLineSegment(sketch, "E1080", {"start": v(175.21, -57.39) * mm, "end": v(166.62, -47.88) * mm});
            skLineSegment(sketch, "E1081", {"start": v(166.62, -47.88) * mm, "end": v(161.08, -37.57) * mm});
            skLineSegment(sketch, "E1082", {"start": v(161.08, -37.57) * mm, "end": v(158.4, -26.87) * mm});
            skLineSegment(sketch, "E1083", {"start": v(158.4, -26.87) * mm, "end": v(158.42, -16.18) * mm});
            skLineSegment(sketch, "E1084", {"start": v(158.42, -16.18) * mm, "end": v(160.98, -5.89) * mm});
            skLineSegment(sketch, "E1085", {"start": v(160.98, -5.89) * mm, "end": v(165.9, 3.6) * mm});
            skLineSegment(sketch, "E1086", {"start": v(165.9, 3.6) * mm, "end": v(173, 11.9) * mm});
            skLineSegment(sketch, "E1087", {"start": v(173, 11.9) * mm, "end": v(182.13, 18.58) * mm});
            skLineSegment(sketch, "E1088", {"start": v(182.13, 18.58) * mm, "end": v(180.8, 18.94) * mm});
            skLineSegment(sketch, "E1089", {"start": v(180.8, 18.94) * mm, "end": v(179.5, 19.28) * mm});
            skLineSegment(sketch, "E1090", {"start": v(179.5, 19.28) * mm, "end": v(178.2, 19.62) * mm});
            skLineSegment(sketch, "E1091", {"start": v(178.2, 19.62) * mm, "end": v(176.92, 19.95) * mm});
            skLineSegment(sketch, "E1092", {"start": v(176.92, 19.95) * mm, "end": v(175.66, 20.3) * mm});
            skLineSegment(sketch, "E1093", {"start": v(175.66, 20.3) * mm, "end": v(174.41, 20.65) * mm});
            skLineSegment(sketch, "E1094", {"start": v(174.41, 20.65) * mm, "end": v(173.18, 21.03) * mm});
            skLineSegment(sketch, "E1095", {"start": v(173.18, 21.03) * mm, "end": v(171.96, 21.44) * mm});
            skLineSegment(sketch, "E1096", {"start": v(171.96, 21.44) * mm, "end": v(166.76, 23.56) * mm});
            skLineSegment(sketch, "E1097", {"start": v(166.76, 23.56) * mm, "end": v(161.85, 26.07) * mm});
            skLineSegment(sketch, "E1098", {"start": v(161.85, 26.07) * mm, "end": v(157.2, 28.94) * mm});
            skLineSegment(sketch, "E1099", {"start": v(157.2, 28.94) * mm, "end": v(152.79, 32.14) * mm});
            skLineSegment(sketch, "E1100", {"start": v(152.79, 32.14) * mm, "end": v(148.62, 35.63) * mm});
            skLineSegment(sketch, "E1101", {"start": v(148.62, 35.63) * mm, "end": v(144.66, 39.4) * mm});
            skLineSegment(sketch, "E1102", {"start": v(144.66, 39.4) * mm, "end": v(140.9, 43.41) * mm});
            skLineSegment(sketch, "E1103", {"start": v(140.9, 43.41) * mm, "end": v(137.32, 47.64) * mm});
            skLineSegment(sketch, "E1104", {"start": v(137.32, 47.64) * mm, "end": v(134.3, 51.45) * mm});
            skLineSegment(sketch, "E1105", {"start": v(134.3, 51.45) * mm, "end": v(131.34, 55.32) * mm});
            skLineSegment(sketch, "E1106", {"start": v(131.34, 55.32) * mm, "end": v(128.44, 59.22) * mm});
            skLineSegment(sketch, "E1107", {"start": v(128.44, 59.22) * mm, "end": v(125.56, 63.15) * mm});
            skLineSegment(sketch, "E1108", {"start": v(125.56, 63.15) * mm, "end": v(122.69, 67.09) * mm});
            skLineSegment(sketch, "E1109", {"start": v(122.69, 67.09) * mm, "end": v(119.8, 71.01) * mm});
            skLineSegment(sketch, "E1110", {"start": v(119.8, 71.01) * mm, "end": v(116.9, 74.92) * mm});
            skLineSegment(sketch, "E1111", {"start": v(116.9, 74.92) * mm, "end": v(113.94, 78.79) * mm});
            skLineSegment(sketch, "E1112", {"start": v(113.94, 78.79) * mm, "end": v(112.07, 81.17) * mm});
            skLineSegment(sketch, "E1113", {"start": v(112.07, 81.17) * mm, "end": v(110.15, 83.52) * mm});
            skLineSegment(sketch, "E1114", {"start": v(110.15, 83.52) * mm, "end": v(108.2, 85.84) * mm});
            skLineSegment(sketch, "E1115", {"start": v(108.2, 85.84) * mm, "end": v(106.17, 88.11) * mm});
            skLineSegment(sketch, "E1116", {"start": v(106.17, 88.11) * mm, "end": v(104.08, 90.34) * mm});
            skLineSegment(sketch, "E1117", {"start": v(104.08, 90.34) * mm, "end": v(101.9, 92.5) * mm});
            skLineSegment(sketch, "E1118", {"start": v(101.9, 92.5) * mm, "end": v(99.65, 94.58) * mm});
            skLineSegment(sketch, "E1119", {"start": v(99.65, 94.58) * mm, "end": v(97.28, 96.6) * mm});
            skLineSegment(sketch, "E1120", {"start": v(97.28, 96.6) * mm, "end": v(96.77, 95.74) * mm});
            skLineSegment(sketch, "E1121", {"start": v(96.77, 95.74) * mm, "end": v(96.43, 94.9) * mm});
            skLineSegment(sketch, "E1122", {"start": v(96.43, 94.9) * mm, "end": v(96.24, 94.05) * mm});
            skLineSegment(sketch, "E1123", {"start": v(96.24, 94.05) * mm, "end": v(96.16, 93.22) * mm});
            skLineSegment(sketch, "E1124", {"start": v(96.16, 93.22) * mm, "end": v(96.16, 92.4) * mm});
            skLineSegment(sketch, "E1125", {"start": v(96.16, 92.4) * mm, "end": v(96.2, 91.6) * mm});
            skLineSegment(sketch, "E1126", {"start": v(96.2, 91.6) * mm, "end": v(96.25, 90.8) * mm});
            skLineSegment(sketch, "E1127", {"start": v(96.25, 90.8) * mm, "end": v(96.27, 90.02) * mm});
            skLineSegment(sketch, "E1128", {"start": v(96.27, 90.02) * mm, "end": v(96.26, 67.78) * mm});
            skLineSegment(sketch, "E1129", {"start": v(96.26, 67.78) * mm, "end": v(96.24, 45.54) * mm});
            skLineSegment(sketch, "E1130", {"start": v(96.24, 45.54) * mm, "end": v(96.23, 23.3) * mm});
            skLineSegment(sketch, "E1131", {"start": v(96.23, 23.3) * mm, "end": v(96.23, 1.07) * mm});
            skLineSegment(sketch, "E1132", {"start": v(96.23, 1.07) * mm, "end": v(96.24, -21.17) * mm});
            skLineSegment(sketch, "E1133", {"start": v(96.24, -21.17) * mm, "end": v(96.26, -43.4) * mm});
            skLineSegment(sketch, "E1134", {"start": v(96.26, -43.4) * mm, "end": v(96.3, -65.64) * mm});
            skLineSegment(sketch, "E1135", {"start": v(96.3, -65.64) * mm, "end": v(96.36, -87.88) * mm});
            skLineSegment(sketch, "E1136", {"start": v(96.36, -87.88) * mm, "end": v(96.27, -89.9) * mm});
            skLineSegment(sketch, "E1137", {"start": v(96.27, -89.9) * mm, "end": v(96, -91.74) * mm});
            skLineSegment(sketch, "E1138", {"start": v(96, -91.74) * mm, "end": v(95.54, -93.4) * mm});
            skLineSegment(sketch, "E1139", {"start": v(95.54, -93.4) * mm, "end": v(94.87, -94.92) * mm});
            skLineSegment(sketch, "E1140", {"start": v(94.87, -94.92) * mm, "end": v(93.96, -96.31) * mm});
            skLineSegment(sketch, "E1141", {"start": v(93.96, -96.31) * mm, "end": v(92.82, -97.6) * mm});
            skLineSegment(sketch, "E1142", {"start": v(92.82, -97.6) * mm, "end": v(91.42, -98.82) * mm});
            skLineSegment(sketch, "E1143", {"start": v(91.42, -98.82) * mm, "end": v(89.75, -99.98) * mm});
            skLineSegment(sketch, "E1144", {"start": v(89.75, -99.98) * mm, "end": v(83.1, -104.2) * mm});
            skLineSegment(sketch, "E1145", {"start": v(83.1, -104.2) * mm, "end": v(76.49, -108.44) * mm});
            skLineSegment(sketch, "E1146", {"start": v(76.49, -108.44) * mm, "end": v(69.88, -112.72) * mm});
            skLineSegment(sketch, "E1147", {"start": v(69.88, -112.72) * mm, "end": v(63.29, -117.01) * mm});
            skLineSegment(sketch, "E1148", {"start": v(63.29, -117.01) * mm, "end": v(56.7, -121.32) * mm});
            skLineSegment(sketch, "E1149", {"start": v(56.7, -121.32) * mm, "end": v(50.12, -125.63) * mm});
            skLineSegment(sketch, "E1150", {"start": v(50.12, -125.63) * mm, "end": v(43.53, -129.94) * mm});
            skLineSegment(sketch, "E1151", {"start": v(43.53, -129.94) * mm, "end": v(36.95, -134.25) * mm});
            skLineSegment(sketch, "E1152", {"start": v(36.95, -134.25) * mm, "end": v(35.33, -135.3) * mm});
            skLineSegment(sketch, "E1153", {"start": v(35.33, -135.3) * mm, "end": v(33.71, -136.35) * mm});
            skLineSegment(sketch, "E1154", {"start": v(33.71, -136.35) * mm, "end": v(32.08, -137.4) * mm});
            skLineSegment(sketch, "E1155", {"start": v(32.08, -137.4) * mm, "end": v(30.42, -138.48) * mm});
            skLineSegment(sketch, "E1156", {"start": v(30.42, -138.48) * mm, "end": v(28.73, -139.57) * mm});
            skLineSegment(sketch, "E1157", {"start": v(28.73, -139.57) * mm, "end": v(27.02, -140.68) * mm});
            skLineSegment(sketch, "E1158", {"start": v(27.02, -140.68) * mm, "end": v(25.26, -141.82) * mm});
            skLineSegment(sketch, "E1159", {"start": v(25.26, -141.82) * mm, "end": v(23.45, -143) * mm});
            skLineSegment(sketch, "E1160", {"start": v(-24.65, -142.81) * mm, "end": v(-25.2, -142.43) * mm});
            skLineSegment(sketch, "E1161", {"start": v(-25.2, -142.43) * mm, "end": v(-25.74, -142.04) * mm});
            skLineSegment(sketch, "E1162", {"start": v(-25.74, -142.04) * mm, "end": v(-26.29, -141.66) * mm});
            skLineSegment(sketch, "E1163", {"start": v(-26.29, -141.66) * mm, "end": v(-26.83, -141.27) * mm});
            skLineSegment(sketch, "E1164", {"start": v(-26.83, -141.27) * mm, "end": v(-27.38, -140.89) * mm});
            skLineSegment(sketch, "E1165", {"start": v(-27.38, -140.89) * mm, "end": v(-27.92, -140.5) * mm});
            skLineSegment(sketch, "E1166", {"start": v(-27.92, -140.5) * mm, "end": v(-28.48, -140.13) * mm});
            skLineSegment(sketch, "E1167", {"start": v(-28.48, -140.13) * mm, "end": v(-29.03, -139.77) * mm});
            skLineSegment(sketch, "E1168", {"start": v(-29.03, -139.77) * mm, "end": v(-36.7, -134.82) * mm});
            skLineSegment(sketch, "E1169", {"start": v(-36.7, -134.82) * mm, "end": v(-44.36, -129.87) * mm});
            skLineSegment(sketch, "E1170", {"start": v(-44.36, -129.87) * mm, "end": v(-52.02, -124.92) * mm});
            skLineSegment(sketch, "E1171", {"start": v(-52.02, -124.92) * mm, "end": v(-59.69, -119.97) * mm});
            skLineSegment(sketch, "E1172", {"start": v(-59.69, -119.97) * mm, "end": v(-67.36, -115.03) * mm});
            skLineSegment(sketch, "E1173", {"start": v(-67.36, -115.03) * mm, "end": v(-75.05, -110.12) * mm});
            skLineSegment(sketch, "E1174", {"start": v(-75.05, -110.12) * mm, "end": v(-82.75, -105.23) * mm});
            skLineSegment(sketch, "E1175", {"start": v(-82.75, -105.23) * mm, "end": v(-90.47, -100.37) * mm});
            skLineSegment(sketch, "E1176", {"start": v(-90.47, -100.37) * mm, "end": v(-92.14, -99.21) * mm});
            skLineSegment(sketch, "E1177", {"start": v(-92.14, -99.21) * mm, "end": v(-93.54, -98) * mm});
            skLineSegment(sketch, "E1178", {"start": v(-93.54, -98) * mm, "end": v(-94.68, -96.7) * mm});
            skLineSegment(sketch, "E1179", {"start": v(-94.68, -96.7) * mm, "end": v(-95.59, -95.31) * mm});
            skLineSegment(sketch, "E1180", {"start": v(-95.59, -95.31) * mm, "end": v(-96.26, -93.8) * mm});
            skLineSegment(sketch, "E1181", {"start": v(-96.26, -93.8) * mm, "end": v(-96.72, -92.13) * mm});
            skLineSegment(sketch, "E1182", {"start": v(-96.72, -92.13) * mm, "end": v(-96.99, -90.3) * mm});
            skLineSegment(sketch, "E1183", {"start": v(-96.99, -90.3) * mm, "end": v(-97.07, -88.28) * mm});
            skLineSegment(sketch, "E1184", {"start": v(-97.07, -88.28) * mm, "end": v(-97, -66.1) * mm});
            skLineSegment(sketch, "E1185", {"start": v(-97, -66.1) * mm, "end": v(-96.97, -43.9) * mm});
            skLineSegment(sketch, "E1186", {"start": v(-96.97, -43.9) * mm, "end": v(-96.95, -21.72) * mm});
            skLineSegment(sketch, "E1187", {"start": v(-96.95, -21.72) * mm, "end": v(-96.94, 0.46) * mm});
            skLineSegment(sketch, "E1188", {"start": v(-96.94, 0.46) * mm, "end": v(-96.95, 22.65) * mm});
            skLineSegment(sketch, "E1189", {"start": v(-96.95, 22.65) * mm, "end": v(-96.96, 44.84) * mm});
            skLineSegment(sketch, "E1190", {"start": v(-96.96, 44.84) * mm, "end": v(-96.97, 67.02) * mm});
            skLineSegment(sketch, "E1191", {"start": v(-96.97, 67.02) * mm, "end": v(-97, 89.2) * mm});
            skLineSegment(sketch, "E1192", {"start": v(-97, 89.2) * mm, "end": v(-96.96, 89.98) * mm});
            skLineSegment(sketch, "E1193", {"start": v(-96.96, 89.98) * mm, "end": v(-96.9, 90.77) * mm});
            skLineSegment(sketch, "E1194", {"start": v(-96.9, 90.77) * mm, "end": v(-96.86, 91.58) * mm});
            skLineSegment(sketch, "E1195", {"start": v(-96.86, 91.58) * mm, "end": v(-96.86, 92.4) * mm});
            skLineSegment(sketch, "E1196", {"start": v(-96.86, 92.4) * mm, "end": v(-96.95, 93.21) * mm});
            skLineSegment(sketch, "E1197", {"start": v(-96.95, 93.21) * mm, "end": v(-97.17, 94.04) * mm});
            skLineSegment(sketch, "E1198", {"start": v(-97.17, 94.04) * mm, "end": v(-97.56, 94.86) * mm});
            skLineSegment(sketch, "E1199", {"start": v(-97.56, 94.86) * mm, "end": v(-98.17, 95.68) * mm});
            skLineSegment(sketch, "E1200", {"start": v(-98.17, 95.68) * mm, "end": v(-100.4, 93.62) * mm});
            skLineSegment(sketch, "E1201", {"start": v(-100.4, 93.62) * mm, "end": v(-102.54, 91.5) * mm});
            skLineSegment(sketch, "E1202", {"start": v(-102.54, 91.5) * mm, "end": v(-104.62, 89.32) * mm});
            skLineSegment(sketch, "E1203", {"start": v(-104.62, 89.32) * mm, "end": v(-106.65, 87.11) * mm});
            skLineSegment(sketch, "E1204", {"start": v(-106.65, 87.11) * mm, "end": v(-108.63, 84.87) * mm});
            skLineSegment(sketch, "E1205", {"start": v(-108.63, 84.87) * mm, "end": v(-110.58, 82.6) * mm});
            skLineSegment(sketch, "E1206", {"start": v(-110.58, 82.6) * mm, "end": v(-112.5, 80.32) * mm});
            skLineSegment(sketch, "E1207", {"start": v(-112.5, 80.32) * mm, "end": v(-114.43, 78.04) * mm});
            skLineSegment(sketch, "E1208", {"start": v(-114.43, 78.04) * mm, "end": v(-117.47, 74.23) * mm});
            skLineSegment(sketch, "E1209", {"start": v(-117.47, 74.23) * mm, "end": v(-120.38, 70.32) * mm});
            skLineSegment(sketch, "E1210", {"start": v(-120.38, 70.32) * mm, "end": v(-123.2, 66.34) * mm});
            skLineSegment(sketch, "E1211", {"start": v(-123.2, 66.34) * mm, "end": v(-125.96, 62.33) * mm});
            skLineSegment(sketch, "E1212", {"start": v(-125.96, 62.33) * mm, "end": v(-128.75, 58.33) * mm});
            skLineSegment(sketch, "E1213", {"start": v(-128.75, 58.33) * mm, "end": v(-131.6, 54.38) * mm});
            skLineSegment(sketch, "E1214", {"start": v(-131.6, 54.38) * mm, "end": v(-134.55, 50.5) * mm});
            skLineSegment(sketch, "E1215", {"start": v(-134.55, 50.5) * mm, "end": v(-137.68, 46.76) * mm});
            skLineSegment(sketch, "E1216", {"start": v(-137.68, 46.76) * mm, "end": v(-141.59, 42.47) * mm});
            skLineSegment(sketch, "E1217", {"start": v(-141.59, 42.47) * mm, "end": v(-145.64, 38.38) * mm});
            skLineSegment(sketch, "E1218", {"start": v(-145.64, 38.38) * mm, "end": v(-149.86, 34.54) * mm});
            skLineSegment(sketch, "E1219", {"start": v(-149.86, 34.54) * mm, "end": v(-154.29, 30.98) * mm});
            skLineSegment(sketch, "E1220", {"start": v(-154.29, 30.98) * mm, "end": v(-158.95, 27.75) * mm});
            skLineSegment(sketch, "E1221", {"start": v(-158.95, 27.75) * mm, "end": v(-163.88, 24.9) * mm});
            skLineSegment(sketch, "E1222", {"start": v(-163.88, 24.9) * mm, "end": v(-169.1, 22.46) * mm});
            skLineSegment(sketch, "E1223", {"start": v(-169.1, 22.46) * mm, "end": v(-174.66, 20.5) * mm});
            skLineSegment(sketch, "E1224", {"start": v(-174.66, 20.5) * mm, "end": v(-175.52, 20.25) * mm});
            skLineSegment(sketch, "E1225", {"start": v(-175.52, 20.25) * mm, "end": v(-176.39, 20) * mm});
            skLineSegment(sketch, "E1226", {"start": v(-176.39, 20) * mm, "end": v(-177.28, 19.77) * mm});
            skLineSegment(sketch, "E1227", {"start": v(-177.28, 19.77) * mm, "end": v(-178.2, 19.54) * mm});
            skLineSegment(sketch, "E1228", {"start": v(-178.2, 19.54) * mm, "end": v(-179.14, 19.3) * mm});
            skLineSegment(sketch, "E1229", {"start": v(-179.14, 19.3) * mm, "end": v(-180.14, 19.06) * mm});
            skLineSegment(sketch, "E1230", {"start": v(-180.14, 19.06) * mm, "end": v(-181.18, 18.8) * mm});
            skLineSegment(sketch, "E1231", {"start": v(-181.18, 18.8) * mm, "end": v(-182.28, 18.51) * mm});
            skLineSegment(sketch, "E1232", {"start": v(-182.28, 18.51) * mm, "end": v(-177.14, 15.2) * mm});
            skLineSegment(sketch, "E1233", {"start": v(-177.14, 15.2) * mm, "end": v(-172.57, 11.57) * mm});
            skLineSegment(sketch, "E1234", {"start": v(-172.57, 11.57) * mm, "end": v(-168.6, 7.61) * mm});
            skLineSegment(sketch, "E1235", {"start": v(-168.6, 7.61) * mm, "end": v(-165.22, 3.31) * mm});
            skLineSegment(sketch, "E1236", {"start": v(-165.22, 3.31) * mm, "end": v(-162.45, -1.34) * mm});
            skLineSegment(sketch, "E1237", {"start": v(-162.45, -1.34) * mm, "end": v(-160.3, -6.36) * mm});
            skLineSegment(sketch, "E1238", {"start": v(-160.3, -6.36) * mm, "end": v(-158.8, -11.74) * mm});
            skLineSegment(sketch, "E1239", {"start": v(-158.8, -11.74) * mm, "end": v(-157.92, -17.5) * mm});
            skLineSegment(sketch, "E1240", {"start": v(-157.92, -17.5) * mm, "end": v(-157.73, -23.37) * mm});
            skLineSegment(sketch, "E1241", {"start": v(-157.73, -23.37) * mm, "end": v(-158.25, -28.97) * mm});
            skLineSegment(sketch, "E1242", {"start": v(-158.25, -28.97) * mm, "end": v(-159.49, -34.33) * mm});
            skLineSegment(sketch, "E1243", {"start": v(-159.49, -34.33) * mm, "end": v(-161.42, -39.45) * mm});
            skLineSegment(sketch, "E1244", {"start": v(-161.42, -39.45) * mm, "end": v(-164.04, -44.35) * mm});
            skLineSegment(sketch, "E1245", {"start": v(-164.04, -44.35) * mm, "end": v(-167.35, -49.02) * mm});
            skLineSegment(sketch, "E1246", {"start": v(-167.35, -49.02) * mm, "end": v(-171.32, -53.49) * mm});
            skLineSegment(sketch, "E1247", {"start": v(-171.32, -53.49) * mm, "end": v(-175.96, -57.75) * mm});
            skLineSegment(sketch, "E1248", {"start": v(-175.96, -57.75) * mm, "end": v(-170.9, -57.63) * mm});
            skLineSegment(sketch, "E1249", {"start": v(-170.9, -57.63) * mm, "end": v(-166.17, -58) * mm});
            skLineSegment(sketch, "E1250", {"start": v(-166.17, -58) * mm, "end": v(-161.73, -58.84) * mm});
            skLineSegment(sketch, "E1251", {"start": v(-161.73, -58.84) * mm, "end": v(-157.59, -60.18) * mm});
            skLineSegment(sketch, "E1252", {"start": v(-157.59, -60.18) * mm, "end": v(-153.7, -62) * mm});
            skLineSegment(sketch, "E1253", {"start": v(-153.7, -62) * mm, "end": v(-150.07, -64.34) * mm});
            skLineSegment(sketch, "E1254", {"start": v(-150.07, -64.34) * mm, "end": v(-146.67, -67.17) * mm});
            skLineSegment(sketch, "E1255", {"start": v(-146.67, -67.17) * mm, "end": v(-143.5, -70.52) * mm});
            skLineSegment(sketch, "E1256", {"start": v(-143.5, -70.52) * mm, "end": v(-134.01, -80.97) * mm});
            skLineSegment(sketch, "E1257", {"start": v(-134.01, -80.97) * mm, "end": v(-124.03, -90.71) * mm});
            skLineSegment(sketch, "E1258", {"start": v(-124.03, -90.71) * mm, "end": v(-113.54, -99.77) * mm});
            skLineSegment(sketch, "E1259", {"start": v(-113.54, -99.77) * mm, "end": v(-102.56, -108.15) * mm});
            skLineSegment(sketch, "E1260", {"start": v(-102.56, -108.15) * mm, "end": v(-91.1, -115.85) * mm});
            skLineSegment(sketch, "E1261", {"start": v(-91.1, -115.85) * mm, "end": v(-79.16, -122.9) * mm});
            skLineSegment(sketch, "E1262", {"start": v(-79.16, -122.9) * mm, "end": v(-66.75, -129.29) * mm});
            skLineSegment(sketch, "E1263", {"start": v(-66.75, -129.29) * mm, "end": v(-53.89, -135.04) * mm});
            skLineSegment(sketch, "E1264", {"start": v(-53.89, -135.04) * mm, "end": v(-50.38, -136.44) * mm});
            skLineSegment(sketch, "E1265", {"start": v(-50.38, -136.44) * mm, "end": v(-46.84, -137.74) * mm});
            skLineSegment(sketch, "E1266", {"start": v(-46.84, -137.74) * mm, "end": v(-43.26, -138.93) * mm});
            skLineSegment(sketch, "E1267", {"start": v(-43.26, -138.93) * mm, "end": v(-39.63, -140) * mm});
            skLineSegment(sketch, "E1268", {"start": v(-39.63, -140) * mm, "end": v(-35.96, -140.93) * mm});
            skLineSegment(sketch, "E1269", {"start": v(-35.96, -140.93) * mm, "end": v(-32.25, -141.71) * mm});
            skLineSegment(sketch, "E1270", {"start": v(-32.25, -141.71) * mm, "end": v(-28.48, -142.35) * mm});
            skLineSegment(sketch, "E1271", {"start": v(-28.48, -142.35) * mm, "end": v(-24.65, -142.81) * mm});
            skLineSegment(sketch, "E1272", {"start": v(8.24, 225.8) * mm, "end": v(-9.61, 225.29) * mm});
            skLineSegment(sketch, "E1273", {"start": v(-9.61, 225.29) * mm, "end": v(-26.52, 223.78) * mm});
            skLineSegment(sketch, "E1274", {"start": v(-26.52, 223.78) * mm, "end": v(-42.57, 221.28) * mm});
            skLineSegment(sketch, "E1275", {"start": v(-42.57, 221.28) * mm, "end": v(-57.85, 217.78) * mm});
            skLineSegment(sketch, "E1276", {"start": v(-57.85, 217.78) * mm, "end": v(-72.46, 213.26) * mm});
            skLineSegment(sketch, "E1277", {"start": v(-72.46, 213.26) * mm, "end": v(-86.49, 207.7) * mm});
            skLineSegment(sketch, "E1278", {"start": v(-86.49, 207.7) * mm, "end": v(-100.03, 201.11) * mm});
            skLineSegment(sketch, "E1279", {"start": v(-100.03, 201.11) * mm, "end": v(-113.17, 193.47) * mm});
            skLineSegment(sketch, "E1280", {"start": v(-113.17, 193.47) * mm, "end": v(-122.55, 187.22) * mm});
            skLineSegment(sketch, "E1281", {"start": v(-122.55, 187.22) * mm, "end": v(-131.55, 180.56) * mm});
            skLineSegment(sketch, "E1282", {"start": v(-131.55, 180.56) * mm, "end": v(-140.17, 173.5) * mm});
            skLineSegment(sketch, "E1283", {"start": v(-140.17, 173.5) * mm, "end": v(-148.42, 166.03) * mm});
            skLineSegment(sketch, "E1284", {"start": v(-148.42, 166.03) * mm, "end": v(-156.32, 158.2) * mm});
            skLineSegment(sketch, "E1285", {"start": v(-156.32, 158.2) * mm, "end": v(-163.86, 149.99) * mm});
            skLineSegment(sketch, "E1286", {"start": v(-163.86, 149.99) * mm, "end": v(-171.07, 141.42) * mm});
            skLineSegment(sketch, "E1287", {"start": v(-171.07, 141.42) * mm, "end": v(-177.95, 132.51) * mm});
            skLineSegment(sketch, "E1288", {"start": v(-177.95, 132.51) * mm, "end": v(-182.9, 125.9) * mm});
            skLineSegment(sketch, "E1289", {"start": v(-182.9, 125.9) * mm, "end": v(-187.95, 119.37) * mm});
            skLineSegment(sketch, "E1290", {"start": v(-187.95, 119.37) * mm, "end": v(-193.14, 112.98) * mm});
            skLineSegment(sketch, "E1291", {"start": v(-193.14, 112.98) * mm, "end": v(-198.53, 106.78) * mm});
            skLineSegment(sketch, "E1292", {"start": v(-198.53, 106.78) * mm, "end": v(-204.17, 100.82) * mm});
            skLineSegment(sketch, "E1293", {"start": v(-204.17, 100.82) * mm, "end": v(-210.1, 95.15) * mm});
            skLineSegment(sketch, "E1294", {"start": v(-210.1, 95.15) * mm, "end": v(-216.4, 89.8) * mm});
            skLineSegment(sketch, "E1295", {"start": v(-216.4, 89.8) * mm, "end": v(-223.1, 84.85) * mm});
            skLineSegment(sketch, "E1296", {"start": v(-223.1, 84.85) * mm, "end": v(-223.8, 84.32) * mm});
            skLineSegment(sketch, "E1297", {"start": v(-223.8, 84.32) * mm, "end": v(-224.37, 83.74) * mm});
            skLineSegment(sketch, "E1298", {"start": v(-224.37, 83.74) * mm, "end": v(-224.84, 83.12) * mm});
            skLineSegment(sketch, "E1299", {"start": v(-224.84, 83.12) * mm, "end": v(-225.2, 82.45) * mm});
            skLineSegment(sketch, "E1300", {"start": v(-225.2, 82.45) * mm, "end": v(-225.48, 81.74) * mm});
            skLineSegment(sketch, "E1301", {"start": v(-225.48, 81.74) * mm, "end": v(-225.67, 80.98) * mm});
            skLineSegment(sketch, "E1302", {"start": v(-225.67, 80.98) * mm, "end": v(-225.77, 80.17) * mm});
            skLineSegment(sketch, "E1303", {"start": v(-225.77, 80.17) * mm, "end": v(-225.8, 79.32) * mm});
            skLineSegment(sketch, "E1304", {"start": v(-225.8, 79.32) * mm, "end": v(-225.7, 74.97) * mm});
            skLineSegment(sketch, "E1305", {"start": v(-225.7, 74.97) * mm, "end": v(-225.4, 70.66) * mm});
            skLineSegment(sketch, "E1306", {"start": v(-225.4, 70.66) * mm, "end": v(-224.9, 66.4) * mm});
            skLineSegment(sketch, "E1307", {"start": v(-224.9, 66.4) * mm, "end": v(-224.16, 62.18) * mm});
            skLineSegment(sketch, "E1308", {"start": v(-224.16, 62.18) * mm, "end": v(-223.2, 58.02) * mm});
            skLineSegment(sketch, "E1309", {"start": v(-223.2, 58.02) * mm, "end": v(-222, 53.9) * mm});
            skLineSegment(sketch, "E1310", {"start": v(-222, 53.9) * mm, "end": v(-220.53, 49.85) * mm});
            skLineSegment(sketch, "E1311", {"start": v(-220.53, 49.85) * mm, "end": v(-218.79, 45.86) * mm});
            skLineSegment(sketch, "E1312", {"start": v(-218.79, 45.86) * mm, "end": v(-215.76, 40.36) * mm});
            skLineSegment(sketch, "E1313", {"start": v(-215.76, 40.36) * mm, "end": v(-212.28, 35.61) * mm});
            skLineSegment(sketch, "E1314", {"start": v(-212.28, 35.61) * mm, "end": v(-208.35, 31.62) * mm});
            skLineSegment(sketch, "E1315", {"start": v(-208.35, 31.62) * mm, "end": v(-204, 28.39) * mm});
            skLineSegment(sketch, "E1316", {"start": v(-204, 28.39) * mm, "end": v(-199.22, 25.94) * mm});
            skLineSegment(sketch, "E1317", {"start": v(-199.22, 25.94) * mm, "end": v(-194.06, 24.28) * mm});
            skLineSegment(sketch, "E1318", {"start": v(-194.06, 24.28) * mm, "end": v(-188.53, 23.43) * mm});
            skLineSegment(sketch, "E1319", {"start": v(-188.53, 23.43) * mm, "end": v(-182.64, 23.4) * mm});
            skLineSegment(sketch, "E1320", {"start": v(-182.64, 23.4) * mm, "end": v(-178.9, 23.81) * mm});
            skLineSegment(sketch, "E1321", {"start": v(-178.9, 23.81) * mm, "end": v(-175.29, 24.57) * mm});
            skLineSegment(sketch, "E1322", {"start": v(-175.29, 24.57) * mm, "end": v(-171.8, 25.64) * mm});
            skLineSegment(sketch, "E1323", {"start": v(-171.8, 25.64) * mm, "end": v(-168.43, 27) * mm});
            skLineSegment(sketch, "E1324", {"start": v(-168.43, 27) * mm, "end": v(-165.17, 28.62) * mm});
            skLineSegment(sketch, "E1325", {"start": v(-165.17, 28.62) * mm, "end": v(-162.01, 30.48) * mm});
            skLineSegment(sketch, "E1326", {"start": v(-162.01, 30.48) * mm, "end": v(-158.94, 32.54) * mm});
            skLineSegment(sketch, "E1327", {"start": v(-158.94, 32.54) * mm, "end": v(-155.95, 34.8) * mm});
            skLineSegment(sketch, "E1328", {"start": v(-155.95, 34.8) * mm, "end": v(-152.05, 38.08) * mm});
            skLineSegment(sketch, "E1329", {"start": v(-152.05, 38.08) * mm, "end": v(-148.37, 41.56) * mm});
            skLineSegment(sketch, "E1330", {"start": v(-148.37, 41.56) * mm, "end": v(-144.88, 45.21) * mm});
            skLineSegment(sketch, "E1331", {"start": v(-144.88, 45.21) * mm, "end": v(-141.55, 49) * mm});
            skLineSegment(sketch, "E1332", {"start": v(-141.55, 49) * mm, "end": v(-138.35, 52.9) * mm});
            skLineSegment(sketch, "E1333", {"start": v(-138.35, 52.9) * mm, "end": v(-135.25, 56.9) * mm});
            skLineSegment(sketch, "E1334", {"start": v(-135.25, 56.9) * mm, "end": v(-132.23, 60.96) * mm});
            skLineSegment(sketch, "E1335", {"start": v(-132.23, 60.96) * mm, "end": v(-129.26, 65.06) * mm});
            skLineSegment(sketch, "E1336", {"start": v(-129.26, 65.06) * mm, "end": v(-123.74, 72.52) * mm});
            skLineSegment(sketch, "E1337", {"start": v(-123.74, 72.52) * mm, "end": v(-118.04, 79.82) * mm});
            skLineSegment(sketch, "E1338", {"start": v(-118.04, 79.82) * mm, "end": v(-112.13, 86.91) * mm});
            skLineSegment(sketch, "E1339", {"start": v(-112.13, 86.91) * mm, "end": v(-105.98, 93.77) * mm});
            skLineSegment(sketch, "E1340", {"start": v(-105.98, 93.77) * mm, "end": v(-99.56, 100.37) * mm});
            skLineSegment(sketch, "E1341", {"start": v(-99.56, 100.37) * mm, "end": v(-92.83, 106.68) * mm});
            skLineSegment(sketch, "E1342", {"start": v(-92.83, 106.68) * mm, "end": v(-85.77, 112.66) * mm});
            skLineSegment(sketch, "E1343", {"start": v(-85.77, 112.66) * mm, "end": v(-78.35, 118.28) * mm});
            skLineSegment(sketch, "E1344", {"start": v(-78.35, 118.28) * mm, "end": v(-63.48, 127.84) * mm});
            skLineSegment(sketch, "E1345", {"start": v(-63.48, 127.84) * mm, "end": v(-48.32, 135.4) * mm});
            skLineSegment(sketch, "E1346", {"start": v(-48.32, 135.4) * mm, "end": v(-32.88, 140.9) * mm});
            skLineSegment(sketch, "E1347", {"start": v(-32.88, 140.9) * mm, "end": v(-17.15, 144.28) * mm});
            skLineSegment(sketch, "E1348", {"start": v(-17.15, 144.28) * mm, "end": v(-1.13, 145.47) * mm});
            skLineSegment(sketch, "E1349", {"start": v(-1.13, 145.47) * mm, "end": v(15.18, 144.4) * mm});
            skLineSegment(sketch, "E1350", {"start": v(15.18, 144.4) * mm, "end": v(31.8, 141.03) * mm});
            skLineSegment(sketch, "E1351", {"start": v(31.8, 141.03) * mm, "end": v(48.7, 135.26) * mm});
            skLineSegment(sketch, "E1352", {"start": v(48.7, 135.26) * mm, "end": v(57.51, 131.28) * mm});
            skLineSegment(sketch, "E1353", {"start": v(57.51, 131.28) * mm, "end": v(65.93, 126.74) * mm});
            skLineSegment(sketch, "E1354", {"start": v(65.93, 126.74) * mm, "end": v(73.98, 121.68) * mm});
            skLineSegment(sketch, "E1355", {"start": v(73.98, 121.68) * mm, "end": v(81.68, 116.14) * mm});
            skLineSegment(sketch, "E1356", {"start": v(81.68, 116.14) * mm, "end": v(89.06, 110.17) * mm});
            skLineSegment(sketch, "E1357", {"start": v(89.06, 110.17) * mm, "end": v(96.16, 103.8) * mm});
            skLineSegment(sketch, "E1358", {"start": v(96.16, 103.8) * mm, "end": v(102.99, 97.08) * mm});
            skLineSegment(sketch, "E1359", {"start": v(102.99, 97.08) * mm, "end": v(109.58, 90.05) * mm});
            skLineSegment(sketch, "E1360", {"start": v(109.58, 90.05) * mm, "end": v(113.37, 85.71) * mm});
            skLineSegment(sketch, "E1361", {"start": v(113.37, 85.71) * mm, "end": v(117.03, 81.28) * mm});
            skLineSegment(sketch, "E1362", {"start": v(117.03, 81.28) * mm, "end": v(120.58, 76.76) * mm});
            skLineSegment(sketch, "E1363", {"start": v(120.58, 76.76) * mm, "end": v(124.06, 72.2) * mm});
            skLineSegment(sketch, "E1364", {"start": v(124.06, 72.2) * mm, "end": v(127.5, 67.6) * mm});
            skLineSegment(sketch, "E1365", {"start": v(127.5, 67.6) * mm, "end": v(130.93, 62.98) * mm});
            skLineSegment(sketch, "E1366", {"start": v(130.93, 62.98) * mm, "end": v(134.38, 58.39) * mm});
            skLineSegment(sketch, "E1367", {"start": v(134.38, 58.39) * mm, "end": v(137.88, 53.83) * mm});
            skLineSegment(sketch, "E1368", {"start": v(137.88, 53.83) * mm, "end": v(141.02, 49.9) * mm});
            skLineSegment(sketch, "E1369", {"start": v(141.02, 49.9) * mm, "end": v(144.26, 46.1) * mm});
            skLineSegment(sketch, "E1370", {"start": v(144.26, 46.1) * mm, "end": v(147.65, 42.44) * mm});
            skLineSegment(sketch, "E1371", {"start": v(147.65, 42.44) * mm, "end": v(151.2, 38.96) * mm});
            skLineSegment(sketch, "E1372", {"start": v(151.2, 38.96) * mm, "end": v(154.93, 35.7) * mm});
            skLineSegment(sketch, "E1373", {"start": v(154.93, 35.7) * mm, "end": v(158.89, 32.7) * mm});
            skLineSegment(sketch, "E1374", {"start": v(158.89, 32.7) * mm, "end": v(163.09, 29.97) * mm});
            skLineSegment(sketch, "E1375", {"start": v(163.09, 29.97) * mm, "end": v(167.57, 27.57) * mm});
            skLineSegment(sketch, "E1376", {"start": v(167.57, 27.57) * mm, "end": v(174.57, 24.85) * mm});
            skLineSegment(sketch, "E1377", {"start": v(174.57, 24.85) * mm, "end": v(181.53, 23.43) * mm});
            skLineSegment(sketch, "E1378", {"start": v(181.53, 23.43) * mm, "end": v(188.33, 23.3) * mm});
            skLineSegment(sketch, "E1379", {"start": v(188.33, 23.3) * mm, "end": v(194.87, 24.4) * mm});
            skLineSegment(sketch, "E1380", {"start": v(194.87, 24.4) * mm, "end": v(201.02, 26.7) * mm});
            skLineSegment(sketch, "E1381", {"start": v(201.02, 26.7) * mm, "end": v(206.68, 30.21) * mm});
            skLineSegment(sketch, "E1382", {"start": v(206.68, 30.21) * mm, "end": v(211.73, 34.88) * mm});
            skLineSegment(sketch, "E1383", {"start": v(211.73, 34.88) * mm, "end": v(216.08, 40.67) * mm});
            skLineSegment(sketch, "E1384", {"start": v(216.08, 40.67) * mm, "end": v(218.64, 45.22) * mm});
            skLineSegment(sketch, "E1385", {"start": v(218.64, 45.22) * mm, "end": v(220.77, 49.88) * mm});
            skLineSegment(sketch, "E1386", {"start": v(220.77, 49.88) * mm, "end": v(222.49, 54.66) * mm});
            skLineSegment(sketch, "E1387", {"start": v(222.49, 54.66) * mm, "end": v(223.83, 59.53) * mm});
            skLineSegment(sketch, "E1388", {"start": v(223.83, 59.53) * mm, "end": v(224.83, 64.5) * mm});
            skLineSegment(sketch, "E1389", {"start": v(224.83, 64.5) * mm, "end": v(225.51, 69.55) * mm});
            skLineSegment(sketch, "E1390", {"start": v(225.51, 69.55) * mm, "end": v(225.9, 74.67) * mm});
            skLineSegment(sketch, "E1391", {"start": v(225.9, 74.67) * mm, "end": v(226.04, 79.86) * mm});
            skLineSegment(sketch, "E1392", {"start": v(226.04, 79.86) * mm, "end": v(225.98, 80.83) * mm});
            skLineSegment(sketch, "E1393", {"start": v(225.98, 80.83) * mm, "end": v(225.78, 81.7) * mm});
            skLineSegment(sketch, "E1394", {"start": v(225.78, 81.7) * mm, "end": v(225.46, 82.47) * mm});
            skLineSegment(sketch, "E1395", {"start": v(225.46, 82.47) * mm, "end": v(225.03, 83.17) * mm});
            skLineSegment(sketch, "E1396", {"start": v(225.03, 83.17) * mm, "end": v(224.5, 83.8) * mm});
            skLineSegment(sketch, "E1397", {"start": v(224.5, 83.8) * mm, "end": v(223.9, 84.39) * mm});
            skLineSegment(sketch, "E1398", {"start": v(223.9, 84.39) * mm, "end": v(223.24, 84.93) * mm});
            skLineSegment(sketch, "E1399", {"start": v(223.24, 84.93) * mm, "end": v(222.5, 85.46) * mm});
            skLineSegment(sketch, "E1400", {"start": v(222.5, 85.46) * mm, "end": v(218.73, 88.16) * mm});
            skLineSegment(sketch, "E1401", {"start": v(218.73, 88.16) * mm, "end": v(215.07, 91) * mm});
            skLineSegment(sketch, "E1402", {"start": v(215.07, 91) * mm, "end": v(211.53, 93.97) * mm});
            skLineSegment(sketch, "E1403", {"start": v(211.53, 93.97) * mm, "end": v(208.1, 97.06) * mm});
            skLineSegment(sketch, "E1404", {"start": v(208.1, 97.06) * mm, "end": v(204.8, 100.28) * mm});
            skLineSegment(sketch, "E1405", {"start": v(204.8, 100.28) * mm, "end": v(201.6, 103.6) * mm});
            skLineSegment(sketch, "E1406", {"start": v(201.6, 103.6) * mm, "end": v(198.5, 107.04) * mm});
            skLineSegment(sketch, "E1407", {"start": v(198.5, 107.04) * mm, "end": v(195.52, 110.58) * mm});
            skLineSegment(sketch, "E1408", {"start": v(195.52, 110.58) * mm, "end": v(191.76, 115.25) * mm});
            skLineSegment(sketch, "E1409", {"start": v(191.76, 115.25) * mm, "end": v(188.06, 119.97) * mm});
            skLineSegment(sketch, "E1410", {"start": v(188.06, 119.97) * mm, "end": v(184.38, 124.7) * mm});
            skLineSegment(sketch, "E1411", {"start": v(184.38, 124.7) * mm, "end": v(180.7, 129.45) * mm});
            skLineSegment(sketch, "E1412", {"start": v(180.7, 129.45) * mm, "end": v(177.02, 134.18) * mm});
            skLineSegment(sketch, "E1413", {"start": v(177.02, 134.18) * mm, "end": v(173.29, 138.87) * mm});
            skLineSegment(sketch, "E1414", {"start": v(173.29, 138.87) * mm, "end": v(169.5, 143.51) * mm});
            skLineSegment(sketch, "E1415", {"start": v(169.5, 143.51) * mm, "end": v(165.6, 148.07) * mm});
            skLineSegment(sketch, "E1416", {"start": v(165.6, 148.07) * mm, "end": v(148.72, 165.8) * mm});
            skLineSegment(sketch, "E1417", {"start": v(148.72, 165.8) * mm, "end": v(130.88, 181.31) * mm});
            skLineSegment(sketch, "E1418", {"start": v(130.88, 181.31) * mm, "end": v(112.16, 194.58) * mm});
            skLineSegment(sketch, "E1419", {"start": v(112.16, 194.58) * mm, "end": v(92.65, 205.55) * mm});
            skLineSegment(sketch, "E1420", {"start": v(92.65, 205.55) * mm, "end": v(72.42, 214.2) * mm});
            skLineSegment(sketch, "E1421", {"start": v(72.42, 214.2) * mm, "end": v(51.56, 220.5) * mm});
            skLineSegment(sketch, "E1422", {"start": v(51.56, 220.5) * mm, "end": v(30.14, 224.37) * mm});
            skLineSegment(sketch, "E1423", {"start": v(30.14, 224.37) * mm, "end": v(8.24, 225.8) * mm});
            skLineSegment(sketch, "E1424", {"start": v(8.61, -153.2) * mm, "end": v(9.88, -153.11) * mm});
            skLineSegment(sketch, "E1425", {"start": v(9.88, -153.11) * mm, "end": v(11.1, -153.03) * mm});
            skLineSegment(sketch, "E1426", {"start": v(11.1, -153.03) * mm, "end": v(12.27, -152.96) * mm});
            skLineSegment(sketch, "E1427", {"start": v(12.27, -152.96) * mm, "end": v(13.4, -152.88) * mm});
            skLineSegment(sketch, "E1428", {"start": v(13.4, -152.88) * mm, "end": v(14.5, -152.81) * mm});
            skLineSegment(sketch, "E1429", {"start": v(14.5, -152.81) * mm, "end": v(15.59, -152.74) * mm});
            skLineSegment(sketch, "E1430", {"start": v(15.59, -152.74) * mm, "end": v(16.65, -152.66) * mm});
            skLineSegment(sketch, "E1431", {"start": v(16.65, -152.66) * mm, "end": v(17.7, -152.59) * mm});
            skLineSegment(sketch, "E1432", {"start": v(17.7, -152.59) * mm, "end": v(18.01, -152.56) * mm});
            skLineSegment(sketch, "E1433", {"start": v(18.01, -152.56) * mm, "end": v(18.32, -152.52) * mm});
            skLineSegment(sketch, "E1434", {"start": v(18.32, -152.52) * mm, "end": v(18.63, -152.47) * mm});
            skLineSegment(sketch, "E1435", {"start": v(18.63, -152.47) * mm, "end": v(18.94, -152.42) * mm});
            skLineSegment(sketch, "E1436", {"start": v(18.94, -152.42) * mm, "end": v(19.25, -152.36) * mm});
            skLineSegment(sketch, "E1437", {"start": v(19.25, -152.36) * mm, "end": v(19.55, -152.3) * mm});
            skLineSegment(sketch, "E1438", {"start": v(19.55, -152.3) * mm, "end": v(19.86, -152.25) * mm});
            skLineSegment(sketch, "E1439", {"start": v(19.86, -152.25) * mm, "end": v(20.17, -152.2) * mm});
            skLineSegment(sketch, "E1440", {"start": v(20.17, -152.2) * mm, "end": v(30.08, -150.54) * mm});
            skLineSegment(sketch, "E1441", {"start": v(30.08, -150.54) * mm, "end": v(39.77, -148.3) * mm});
            skLineSegment(sketch, "E1442", {"start": v(39.77, -148.3) * mm, "end": v(49.25, -145.5) * mm});
            skLineSegment(sketch, "E1443", {"start": v(49.25, -145.5) * mm, "end": v(58.52, -142.17) * mm});
            skLineSegment(sketch, "E1444", {"start": v(58.52, -142.17) * mm, "end": v(67.6, -138.33) * mm});
            skLineSegment(sketch, "E1445", {"start": v(67.6, -138.33) * mm, "end": v(76.5, -134.03) * mm});
            skLineSegment(sketch, "E1446", {"start": v(76.5, -134.03) * mm, "end": v(85.24, -129.28) * mm});
            skLineSegment(sketch, "E1447", {"start": v(85.24, -129.28) * mm, "end": v(93.81, -124.1) * mm});
            skLineSegment(sketch, "E1448", {"start": v(93.81, -124.1) * mm, "end": v(101.41, -119.1) * mm});
            skLineSegment(sketch, "E1449", {"start": v(101.41, -119.1) * mm, "end": v(108.79, -113.83) * mm});
            skLineSegment(sketch, "E1450", {"start": v(108.79, -113.83) * mm, "end": v(115.95, -108.31) * mm});
            skLineSegment(sketch, "E1451", {"start": v(115.95, -108.31) * mm, "end": v(122.92, -102.56) * mm});
            skLineSegment(sketch, "E1452", {"start": v(122.92, -102.56) * mm, "end": v(129.7, -96.58) * mm});
            skLineSegment(sketch, "E1453", {"start": v(129.7, -96.58) * mm, "end": v(136.28, -90.38) * mm});
            skLineSegment(sketch, "E1454", {"start": v(136.28, -90.38) * mm, "end": v(142.7, -83.98) * mm});
            skLineSegment(sketch, "E1455", {"start": v(142.7, -83.98) * mm, "end": v(148.96, -77.39) * mm});
            skLineSegment(sketch, "E1456", {"start": v(148.96, -77.39) * mm, "end": v(150.4, -75.83) * mm});
            skLineSegment(sketch, "E1457", {"start": v(150.4, -75.83) * mm, "end": v(151.86, -74.3) * mm});
            skLineSegment(sketch, "E1458", {"start": v(151.86, -74.3) * mm, "end": v(153.37, -72.8) * mm});
            skLineSegment(sketch, "E1459", {"start": v(153.37, -72.8) * mm, "end": v(154.93, -71.4) * mm});
            skLineSegment(sketch, "E1460", {"start": v(154.93, -71.4) * mm, "end": v(156.58, -70.1) * mm});
            skLineSegment(sketch, "E1461", {"start": v(156.58, -70.1) * mm, "end": v(158.33, -68.92) * mm});
            skLineSegment(sketch, "E1462", {"start": v(158.33, -68.92) * mm, "end": v(160.2, -67.9) * mm});
            skLineSegment(sketch, "E1463", {"start": v(160.2, -67.9) * mm, "end": v(162.23, -67.08) * mm});
            skLineSegment(sketch, "E1464", {"start": v(162.23, -67.08) * mm, "end": v(170.4, -65.52) * mm});
            skLineSegment(sketch, "E1465", {"start": v(170.4, -65.52) * mm, "end": v(178.36, -66.26) * mm});
            skLineSegment(sketch, "E1466", {"start": v(178.36, -66.26) * mm, "end": v(185.78, -69.01) * mm});
            skLineSegment(sketch, "E1467", {"start": v(185.78, -69.01) * mm, "end": v(192.32, -73.47) * mm});
            skLineSegment(sketch, "E1468", {"start": v(192.32, -73.47) * mm, "end": v(197.65, -79.34) * mm});
            skLineSegment(sketch, "E1469", {"start": v(197.65, -79.34) * mm, "end": v(201.4, -86.33) * mm});
            skLineSegment(sketch, "E1470", {"start": v(201.4, -86.33) * mm, "end": v(203.25, -94.13) * mm});
            skLineSegment(sketch, "E1471", {"start": v(203.25, -94.13) * mm, "end": v(202.86, -102.46) * mm});
            skLineSegment(sketch, "E1472", {"start": v(202.86, -102.46) * mm, "end": v(201.72, -107.28) * mm});
            skLineSegment(sketch, "E1473", {"start": v(201.72, -107.28) * mm, "end": v(200.23, -111.93) * mm});
            skLineSegment(sketch, "E1474", {"start": v(200.23, -111.93) * mm, "end": v(198.4, -116.43) * mm});
            skLineSegment(sketch, "E1475", {"start": v(198.4, -116.43) * mm, "end": v(196.3, -120.79) * mm});
            skLineSegment(sketch, "E1476", {"start": v(196.3, -120.79) * mm, "end": v(193.96, -125.02) * mm});
            skLineSegment(sketch, "E1477", {"start": v(193.96, -125.02) * mm, "end": v(191.4, -129.15) * mm});
            skLineSegment(sketch, "E1478", {"start": v(191.4, -129.15) * mm, "end": v(188.68, -133.2) * mm});
            skLineSegment(sketch, "E1479", {"start": v(188.68, -133.2) * mm, "end": v(185.82, -137.16) * mm});
            skLineSegment(sketch, "E1480", {"start": v(185.82, -137.16) * mm, "end": v(178.24, -146.74) * mm});
            skLineSegment(sketch, "E1481", {"start": v(178.24, -146.74) * mm, "end": v(170.15, -155.72) * mm});
            skLineSegment(sketch, "E1482", {"start": v(170.15, -155.72) * mm, "end": v(161.58, -164.13) * mm});
            skLineSegment(sketch, "E1483", {"start": v(161.58, -164.13) * mm, "end": v(152.55, -171.97) * mm});
            skLineSegment(sketch, "E1484", {"start": v(152.55, -171.97) * mm, "end": v(143.07, -179.27) * mm});
            skLineSegment(sketch, "E1485", {"start": v(143.07, -179.27) * mm, "end": v(133.16, -186.06) * mm});
            skLineSegment(sketch, "E1486", {"start": v(133.16, -186.06) * mm, "end": v(122.85, -192.34) * mm});
            skLineSegment(sketch, "E1487", {"start": v(122.85, -192.34) * mm, "end": v(112.16, -198.14) * mm});
            skLineSegment(sketch, "E1488", {"start": v(112.16, -198.14) * mm, "end": v(94.7, -206.25) * mm});
            skLineSegment(sketch, "E1489", {"start": v(94.7, -206.25) * mm, "end": v(76.98, -212.88) * mm});
            skLineSegment(sketch, "E1490", {"start": v(76.98, -212.88) * mm, "end": v(59.01, -218.04) * mm});
            skLineSegment(sketch, "E1491", {"start": v(59.01, -218.04) * mm, "end": v(40.8, -221.75) * mm});
            skLineSegment(sketch, "E1492", {"start": v(40.8, -221.75) * mm, "end": v(22.34, -224.02) * mm});
            skLineSegment(sketch, "E1493", {"start": v(22.34, -224.02) * mm, "end": v(3.67, -224.86) * mm});
            skLineSegment(sketch, "E1494", {"start": v(3.67, -224.86) * mm, "end": v(-15.23, -224.3) * mm});
            skLineSegment(sketch, "E1495", {"start": v(-15.23, -224.3) * mm, "end": v(-34.34, -222.33) * mm});
            skLineSegment(sketch, "E1496", {"start": v(-34.34, -222.33) * mm, "end": v(-55.4, -218.57) * mm});
            skLineSegment(sketch, "E1497", {"start": v(-55.4, -218.57) * mm, "end": v(-75.65, -213.22) * mm});
            skLineSegment(sketch, "E1498", {"start": v(-75.65, -213.22) * mm, "end": v(-95.04, -206.24) * mm});
            skLineSegment(sketch, "E1499", {"start": v(-95.04, -206.24) * mm, "end": v(-113.57, -197.62) * mm});
            skLineSegment(sketch, "E1500", {"start": v(-113.57, -197.62) * mm, "end": v(-131.22, -187.3) * mm});
            skLineSegment(sketch, "E1501", {"start": v(-131.22, -187.3) * mm, "end": v(-147.95, -175.28) * mm});
            skLineSegment(sketch, "E1502", {"start": v(-147.95, -175.28) * mm, "end": v(-163.75, -161.52) * mm});
            skLineSegment(sketch, "E1503", {"start": v(-163.75, -161.52) * mm, "end": v(-178.6, -145.98) * mm});
            skLineSegment(sketch, "E1504", {"start": v(-178.6, -145.98) * mm, "end": v(-182.6, -141.24) * mm});
            skLineSegment(sketch, "E1505", {"start": v(-182.6, -141.24) * mm, "end": v(-186.42, -136.38) * mm});
            skLineSegment(sketch, "E1506", {"start": v(-186.42, -136.38) * mm, "end": v(-190, -131.36) * mm});
            skLineSegment(sketch, "E1507", {"start": v(-190, -131.36) * mm, "end": v(-193.28, -126.17) * mm});
            skLineSegment(sketch, "E1508", {"start": v(-193.28, -126.17) * mm, "end": v(-196.21, -120.79) * mm});
            skLineSegment(sketch, "E1509", {"start": v(-196.21, -120.79) * mm, "end": v(-198.76, -115.18) * mm});
            skLineSegment(sketch, "E1510", {"start": v(-198.76, -115.18) * mm, "end": v(-200.85, -109.34) * mm});
            skLineSegment(sketch, "E1511", {"start": v(-200.85, -109.34) * mm, "end": v(-202.46, -103.23) * mm});
            skLineSegment(sketch, "E1512", {"start": v(-202.46, -103.23) * mm, "end": v(-203.06, -98.22) * mm});
            skLineSegment(sketch, "E1513", {"start": v(-203.06, -98.22) * mm, "end": v(-202.76, -93.18) * mm});
            skLineSegment(sketch, "E1514", {"start": v(-202.76, -93.18) * mm, "end": v(-201.64, -88.23) * mm});
            skLineSegment(sketch, "E1515", {"start": v(-201.64, -88.23) * mm, "end": v(-199.74, -83.48) * mm});
            skLineSegment(sketch, "E1516", {"start": v(-199.74, -83.48) * mm, "end": v(-197.12, -79.06) * mm});
            skLineSegment(sketch, "E1517", {"start": v(-197.12, -79.06) * mm, "end": v(-193.86, -75.07) * mm});
            skLineSegment(sketch, "E1518", {"start": v(-193.86, -75.07) * mm, "end": v(-190, -71.64) * mm});
            skLineSegment(sketch, "E1519", {"start": v(-190, -71.64) * mm, "end": v(-185.6, -68.87) * mm});
            skLineSegment(sketch, "E1520", {"start": v(-185.6, -68.87) * mm, "end": v(-181.85, -67.28) * mm});
            skLineSegment(sketch, "E1521", {"start": v(-181.85, -67.28) * mm, "end": v(-177.66, -66.15) * mm});
            skLineSegment(sketch, "E1522", {"start": v(-177.66, -66.15) * mm, "end": v(-173.16, -65.6) * mm});
            skLineSegment(sketch, "E1523", {"start": v(-173.16, -65.6) * mm, "end": v(-168.48, -65.74) * mm});
            skLineSegment(sketch, "E1524", {"start": v(-168.48, -65.74) * mm, "end": v(-163.75, -66.67) * mm});
            skLineSegment(sketch, "E1525", {"start": v(-163.75, -66.67) * mm, "end": v(-159.1, -68.5) * mm});
            skLineSegment(sketch, "E1526", {"start": v(-159.1, -68.5) * mm, "end": v(-154.66, -71.34) * mm});
            skLineSegment(sketch, "E1527", {"start": v(-154.66, -71.34) * mm, "end": v(-150.56, -75.3) * mm});
            skLineSegment(sketch, "E1528", {"start": v(-150.56, -75.3) * mm, "end": v(-147.93, -78.31) * mm});
            skLineSegment(sketch, "E1529", {"start": v(-147.93, -78.31) * mm, "end": v(-145.23, -81.26) * mm});
            skLineSegment(sketch, "E1530", {"start": v(-145.23, -81.26) * mm, "end": v(-142.48, -84.16) * mm});
            skLineSegment(sketch, "E1531", {"start": v(-142.48, -84.16) * mm, "end": v(-139.67, -87) * mm});
            skLineSegment(sketch, "E1532", {"start": v(-139.67, -87) * mm, "end": v(-136.8, -89.8) * mm});
            skLineSegment(sketch, "E1533", {"start": v(-136.8, -89.8) * mm, "end": v(-133.9, -92.56) * mm});
            skLineSegment(sketch, "E1534", {"start": v(-133.9, -92.56) * mm, "end": v(-130.96, -95.27) * mm});
            skLineSegment(sketch, "E1535", {"start": v(-130.96, -95.27) * mm, "end": v(-127.98, -97.95) * mm});
            skLineSegment(sketch, "E1536", {"start": v(-127.98, -97.95) * mm, "end": v(-117.75, -106.65) * mm});
            skLineSegment(sketch, "E1537", {"start": v(-117.75, -106.65) * mm, "end": v(-107.22, -114.81) * mm});
            skLineSegment(sketch, "E1538", {"start": v(-107.22, -114.81) * mm, "end": v(-96.35, -122.37) * mm});
            skLineSegment(sketch, "E1539", {"start": v(-96.35, -122.37) * mm, "end": v(-85.11, -129.27) * mm});
            skLineSegment(sketch, "E1540", {"start": v(-85.11, -129.27) * mm, "end": v(-73.48, -135.46) * mm});
            skLineSegment(sketch, "E1541", {"start": v(-73.48, -135.46) * mm, "end": v(-61.42, -140.88) * mm});
            skLineSegment(sketch, "E1542", {"start": v(-61.42, -140.88) * mm, "end": v(-48.9, -145.48) * mm});
            skLineSegment(sketch, "E1543", {"start": v(-48.9, -145.48) * mm, "end": v(-35.9, -149.2) * mm});
            skLineSegment(sketch, "E1544", {"start": v(-35.9, -149.2) * mm, "end": v(-32.69, -149.96) * mm});
            skLineSegment(sketch, "E1545", {"start": v(-32.69, -149.96) * mm, "end": v(-29.45, -150.68) * mm});
            skLineSegment(sketch, "E1546", {"start": v(-29.45, -150.68) * mm, "end": v(-26.2, -151.33) * mm});
            skLineSegment(sketch, "E1547", {"start": v(-26.2, -151.33) * mm, "end": v(-22.9, -151.9) * mm});
            skLineSegment(sketch, "E1548", {"start": v(-22.9, -151.9) * mm, "end": v(-19.56, -152.35) * mm});
            skLineSegment(sketch, "E1549", {"start": v(-19.56, -152.35) * mm, "end": v(-16.17, -152.68) * mm});
            skLineSegment(sketch, "E1550", {"start": v(-16.17, -152.68) * mm, "end": v(-12.73, -152.87) * mm});
            skLineSegment(sketch, "E1551", {"start": v(-12.73, -152.87) * mm, "end": v(-9.22, -152.9) * mm});
            skLineSegment(sketch, "E1552", {"start": v(-9.22, -152.9) * mm, "end": v(-11.1, -151.4) * mm});
            skLineSegment(sketch, "E1553", {"start": v(-11.1, -151.4) * mm, "end": v(-13.04, -150.3) * mm});
            skLineSegment(sketch, "E1554", {"start": v(-13.04, -150.3) * mm, "end": v(-15.04, -149.54) * mm});
            skLineSegment(sketch, "E1555", {"start": v(-15.04, -149.54) * mm, "end": v(-17.07, -149.03) * mm});
            skLineSegment(sketch, "E1556", {"start": v(-17.07, -149.03) * mm, "end": v(-19.13, -148.69) * mm});
            skLineSegment(sketch, "E1557", {"start": v(-19.13, -148.69) * mm, "end": v(-21.19, -148.44) * mm});
            skLineSegment(sketch, "E1558", {"start": v(-21.19, -148.44) * mm, "end": v(-23.23, -148.2) * mm});
            skLineSegment(sketch, "E1559", {"start": v(-23.23, -148.2) * mm, "end": v(-25.24, -147.9) * mm});
            skLineSegment(sketch, "E1560", {"start": v(-25.24, -147.9) * mm, "end": v(-37.52, -145.2) * mm});
            skLineSegment(sketch, "E1561", {"start": v(-37.52, -145.2) * mm, "end": v(-49.4, -141.64) * mm});
            skLineSegment(sketch, "E1562", {"start": v(-49.4, -141.64) * mm, "end": v(-60.88, -137.29) * mm});
            skLineSegment(sketch, "E1563", {"start": v(-60.88, -137.29) * mm, "end": v(-72, -132.2) * mm});
            skLineSegment(sketch, "E1564", {"start": v(-72, -132.2) * mm, "end": v(-82.8, -126.4) * mm});
            skLineSegment(sketch, "E1565", {"start": v(-82.8, -126.4) * mm, "end": v(-93.28, -119.96) * mm});
            skLineSegment(sketch, "E1566", {"start": v(-93.28, -119.96) * mm, "end": v(-103.47, -112.93) * mm});
            skLineSegment(sketch, "E1567", {"start": v(-103.47, -112.93) * mm, "end": v(-113.4, -105.34) * mm});
            skLineSegment(sketch, "E1568", {"start": v(-113.4, -105.34) * mm, "end": v(-118.28, -101.32) * mm});
            skLineSegment(sketch, "E1569", {"start": v(-118.28, -101.32) * mm, "end": v(-123.03, -97.16) * mm});
            skLineSegment(sketch, "E1570", {"start": v(-123.03, -97.16) * mm, "end": v(-127.68, -92.9) * mm});
            skLineSegment(sketch, "E1571", {"start": v(-127.68, -92.9) * mm, "end": v(-132.23, -88.53) * mm});
            skLineSegment(sketch, "E1572", {"start": v(-132.23, -88.53) * mm, "end": v(-136.72, -84.1) * mm});
            skLineSegment(sketch, "E1573", {"start": v(-136.72, -84.1) * mm, "end": v(-141.15, -79.6) * mm});
            skLineSegment(sketch, "E1574", {"start": v(-141.15, -79.6) * mm, "end": v(-145.54, -75.08) * mm});
            skLineSegment(sketch, "E1575", {"start": v(-145.54, -75.08) * mm, "end": v(-149.92, -70.53) * mm});
            skLineSegment(sketch, "E1576", {"start": v(-149.92, -70.53) * mm, "end": v(-151.25, -69.19) * mm});
            skLineSegment(sketch, "E1577", {"start": v(-151.25, -69.19) * mm, "end": v(-152.63, -67.91) * mm});
            skLineSegment(sketch, "E1578", {"start": v(-152.63, -67.91) * mm, "end": v(-154.06, -66.72) * mm});
            skLineSegment(sketch, "E1579", {"start": v(-154.06, -66.72) * mm, "end": v(-155.55, -65.62) * mm});
            skLineSegment(sketch, "E1580", {"start": v(-155.55, -65.62) * mm, "end": v(-157.12, -64.64) * mm});
            skLineSegment(sketch, "E1581", {"start": v(-157.12, -64.64) * mm, "end": v(-158.77, -63.8) * mm});
            skLineSegment(sketch, "E1582", {"start": v(-158.77, -63.8) * mm, "end": v(-160.52, -63.1) * mm});
            skLineSegment(sketch, "E1583", {"start": v(-160.52, -63.1) * mm, "end": v(-162.38, -62.58) * mm});
            skLineSegment(sketch, "E1584", {"start": v(-162.38, -62.58) * mm, "end": v(-169.64, -61.7) * mm});
            skLineSegment(sketch, "E1585", {"start": v(-169.64, -61.7) * mm, "end": v(-176.73, -62.27) * mm});
            skLineSegment(sketch, "E1586", {"start": v(-176.73, -62.27) * mm, "end": v(-183.47, -64.2) * mm});
            skLineSegment(sketch, "E1587", {"start": v(-183.47, -64.2) * mm, "end": v(-189.67, -67.35) * mm});
            skLineSegment(sketch, "E1588", {"start": v(-189.67, -67.35) * mm, "end": v(-195.17, -71.64) * mm});
            skLineSegment(sketch, "E1589", {"start": v(-195.17, -71.64) * mm, "end": v(-199.79, -76.93) * mm});
            skLineSegment(sketch, "E1590", {"start": v(-199.79, -76.93) * mm, "end": v(-203.35, -83.12) * mm});
            skLineSegment(sketch, "E1591", {"start": v(-203.35, -83.12) * mm, "end": v(-205.68, -90.09) * mm});
            skLineSegment(sketch, "E1592", {"start": v(-205.68, -90.09) * mm, "end": v(-206.32, -93.93) * mm});
            skLineSegment(sketch, "E1593", {"start": v(-206.32, -93.93) * mm, "end": v(-206.53, -97.7) * mm});
            skLineSegment(sketch, "E1594", {"start": v(-206.53, -97.7) * mm, "end": v(-206.35, -101.4) * mm});
            skLineSegment(sketch, "E1595", {"start": v(-206.35, -101.4) * mm, "end": v(-205.82, -105.04) * mm});
            skLineSegment(sketch, "E1596", {"start": v(-205.82, -105.04) * mm, "end": v(-204.98, -108.63) * mm});
            skLineSegment(sketch, "E1597", {"start": v(-204.98, -108.63) * mm, "end": v(-203.87, -112.17) * mm});
            skLineSegment(sketch, "E1598", {"start": v(-203.87, -112.17) * mm, "end": v(-202.54, -115.67) * mm});
            skLineSegment(sketch, "E1599", {"start": v(-202.54, -115.67) * mm, "end": v(-201.03, -119.13) * mm});
            skLineSegment(sketch, "E1600", {"start": v(-201.03, -119.13) * mm, "end": v(-197.24, -126.66) * mm});
            skLineSegment(sketch, "E1601", {"start": v(-197.24, -126.66) * mm, "end": v(-193, -133.84) * mm});
            skLineSegment(sketch, "E1602", {"start": v(-193, -133.84) * mm, "end": v(-188.34, -140.7) * mm});
            skLineSegment(sketch, "E1603", {"start": v(-188.34, -140.7) * mm, "end": v(-183.28, -147.23) * mm});
            skLineSegment(sketch, "E1604", {"start": v(-183.28, -147.23) * mm, "end": v(-177.86, -153.47) * mm});
            skLineSegment(sketch, "E1605", {"start": v(-177.86, -153.47) * mm, "end": v(-172.1, -159.42) * mm});
            skLineSegment(sketch, "E1606", {"start": v(-172.1, -159.42) * mm, "end": v(-166.04, -165.1) * mm});
            skLineSegment(sketch, "E1607", {"start": v(-166.04, -165.1) * mm, "end": v(-159.7, -170.54) * mm});
            skLineSegment(sketch, "E1608", {"start": v(-159.7, -170.54) * mm, "end": v(-135.47, -188.47) * mm});
            skLineSegment(sketch, "E1609", {"start": v(-135.47, -188.47) * mm, "end": v(-110.4, -203.07) * mm});
            skLineSegment(sketch, "E1610", {"start": v(-110.4, -203.07) * mm, "end": v(-84.54, -214.37) * mm});
            skLineSegment(sketch, "E1611", {"start": v(-84.54, -214.37) * mm, "end": v(-57.88, -222.4) * mm});
            skLineSegment(sketch, "E1612", {"start": v(-57.88, -222.4) * mm, "end": v(-30.46, -227.17) * mm});
            skLineSegment(sketch, "E1613", {"start": v(-30.46, -227.17) * mm, "end": v(-2.28, -228.7) * mm});
            skLineSegment(sketch, "E1614", {"start": v(-2.28, -228.7) * mm, "end": v(26.62, -227.02) * mm});
            skLineSegment(sketch, "E1615", {"start": v(26.62, -227.02) * mm, "end": v(56.24, -222.15) * mm});
            skLineSegment(sketch, "E1616", {"start": v(56.24, -222.15) * mm, "end": v(74.8, -217.42) * mm});
            skLineSegment(sketch, "E1617", {"start": v(74.8, -217.42) * mm, "end": v(92.63, -211.36) * mm});
            skLineSegment(sketch, "E1618", {"start": v(92.63, -211.36) * mm, "end": v(109.73, -203.98) * mm});
            skLineSegment(sketch, "E1619", {"start": v(109.73, -203.98) * mm, "end": v(126.06, -195.26) * mm});
            skLineSegment(sketch, "E1620", {"start": v(126.06, -195.26) * mm, "end": v(141.62, -185.2) * mm});
            skLineSegment(sketch, "E1621", {"start": v(141.62, -185.2) * mm, "end": v(156.37, -173.78) * mm});
            skLineSegment(sketch, "E1622", {"start": v(156.37, -173.78) * mm, "end": v(170.3, -160.99) * mm});
            skLineSegment(sketch, "E1623", {"start": v(170.3, -160.99) * mm, "end": v(183.37, -146.82) * mm});
            skLineSegment(sketch, "E1624", {"start": v(183.37, -146.82) * mm, "end": v(187, -142.42) * mm});
            skLineSegment(sketch, "E1625", {"start": v(187, -142.42) * mm, "end": v(190.45, -137.89) * mm});
            skLineSegment(sketch, "E1626", {"start": v(190.45, -137.89) * mm, "end": v(193.68, -133.23) * mm});
            skLineSegment(sketch, "E1627", {"start": v(193.68, -133.23) * mm, "end": v(196.66, -128.43) * mm});
            skLineSegment(sketch, "E1628", {"start": v(196.66, -128.43) * mm, "end": v(199.36, -123.46) * mm});
            skLineSegment(sketch, "E1629", {"start": v(199.36, -123.46) * mm, "end": v(201.73, -118.32) * mm});
            skLineSegment(sketch, "E1630", {"start": v(201.73, -118.32) * mm, "end": v(203.76, -113) * mm});
            skLineSegment(sketch, "E1631", {"start": v(203.76, -113) * mm, "end": v(205.4, -107.46) * mm});
            skLineSegment(sketch, "E1632", {"start": v(205.4, -107.46) * mm, "end": v(206.5, -101.15) * mm});
            skLineSegment(sketch, "E1633", {"start": v(206.5, -101.15) * mm, "end": v(206.58, -95) * mm});
            skLineSegment(sketch, "E1634", {"start": v(206.58, -95) * mm, "end": v(205.68, -89.1) * mm});
            skLineSegment(sketch, "E1635", {"start": v(205.68, -89.1) * mm, "end": v(203.84, -83.52) * mm});
            skLineSegment(sketch, "E1636", {"start": v(203.84, -83.52) * mm, "end": v(201.1, -78.35) * mm});
            skLineSegment(sketch, "E1637", {"start": v(201.1, -78.35) * mm, "end": v(197.5, -73.68) * mm});
            skLineSegment(sketch, "E1638", {"start": v(197.5, -73.68) * mm, "end": v(193.08, -69.6) * mm});
            skLineSegment(sketch, "E1639", {"start": v(193.08, -69.6) * mm, "end": v(187.87, -66.17) * mm});
            skLineSegment(sketch, "E1640", {"start": v(187.87, -66.17) * mm, "end": v(182.43, -63.68) * mm});
            skLineSegment(sketch, "E1641", {"start": v(182.43, -63.68) * mm, "end": v(177.02, -62.2) * mm});
            skLineSegment(sketch, "E1642", {"start": v(177.02, -62.2) * mm, "end": v(171.66, -61.74) * mm});
            skLineSegment(sketch, "E1643", {"start": v(171.66, -61.74) * mm, "end": v(166.38, -62.28) * mm});
            skLineSegment(sketch, "E1644", {"start": v(166.38, -62.28) * mm, "end": v(161.2, -63.82) * mm});
            skLineSegment(sketch, "E1645", {"start": v(161.2, -63.82) * mm, "end": v(156.11, -66.37) * mm});
            skLineSegment(sketch, "E1646", {"start": v(156.11, -66.37) * mm, "end": v(151.16, -69.9) * mm});
            skLineSegment(sketch, "E1647", {"start": v(151.16, -69.9) * mm, "end": v(146.35, -74.44) * mm});
            skLineSegment(sketch, "E1648", {"start": v(146.35, -74.44) * mm, "end": v(142.56, -78.43) * mm});
            skLineSegment(sketch, "E1649", {"start": v(142.56, -78.43) * mm, "end": v(138.72, -82.38) * mm});
            skLineSegment(sketch, "E1650", {"start": v(138.72, -82.38) * mm, "end": v(134.84, -86.27) * mm});
            skLineSegment(sketch, "E1651", {"start": v(134.84, -86.27) * mm, "end": v(130.9, -90.1) * mm});
            skLineSegment(sketch, "E1652", {"start": v(130.9, -90.1) * mm, "end": v(126.9, -93.86) * mm});
            skLineSegment(sketch, "E1653", {"start": v(126.9, -93.86) * mm, "end": v(122.82, -97.54) * mm});
            skLineSegment(sketch, "E1654", {"start": v(122.82, -97.54) * mm, "end": v(118.67, -101.15) * mm});
            skLineSegment(sketch, "E1655", {"start": v(118.67, -101.15) * mm, "end": v(114.42, -104.66) * mm});
            skLineSegment(sketch, "E1656", {"start": v(114.42, -104.66) * mm, "end": v(103.75, -112.87) * mm});
            skLineSegment(sketch, "E1657", {"start": v(103.75, -112.87) * mm, "end": v(92.78, -120.44) * mm});
            skLineSegment(sketch, "E1658", {"start": v(92.78, -120.44) * mm, "end": v(81.48, -127.3) * mm});
            skLineSegment(sketch, "E1659", {"start": v(81.48, -127.3) * mm, "end": v(69.83, -133.4) * mm});
            skLineSegment(sketch, "E1660", {"start": v(69.83, -133.4) * mm, "end": v(57.79, -138.65) * mm});
            skLineSegment(sketch, "E1661", {"start": v(57.79, -138.65) * mm, "end": v(45.34, -143.03) * mm});
            skLineSegment(sketch, "E1662", {"start": v(45.34, -143.03) * mm, "end": v(32.44, -146.44) * mm});
            skLineSegment(sketch, "E1663", {"start": v(32.44, -146.44) * mm, "end": v(19.08, -148.84) * mm});
            skLineSegment(sketch, "E1664", {"start": v(19.08, -148.84) * mm, "end": v(17.71, -149.03) * mm});
            skLineSegment(sketch, "E1665", {"start": v(17.71, -149.03) * mm, "end": v(16.35, -149.24) * mm});
            skLineSegment(sketch, "E1666", {"start": v(16.35, -149.24) * mm, "end": v(15, -149.51) * mm});
            skLineSegment(sketch, "E1667", {"start": v(15, -149.51) * mm, "end": v(13.67, -149.89) * mm});
            skLineSegment(sketch, "E1668", {"start": v(13.67, -149.89) * mm, "end": v(12.35, -150.4) * mm});
            skLineSegment(sketch, "E1669", {"start": v(12.35, -150.4) * mm, "end": v(11.07, -151.1) * mm});
            skLineSegment(sketch, "E1670", {"start": v(11.07, -151.1) * mm, "end": v(9.82, -152.02) * mm});
            skLineSegment(sketch, "E1671", {"start": v(9.82, -152.02) * mm, "end": v(8.61, -153.2) * mm});
            skLineSegment(sketch, "E1672", {"start": v(74.04, 115.6) * mm, "end": v(56.88, 126.64) * mm});
            skLineSegment(sketch, "E1673", {"start": v(56.88, 126.64) * mm, "end": v(38.53, 134.51) * mm});
            skLineSegment(sketch, "E1674", {"start": v(38.53, 134.51) * mm, "end": v(19.39, 139.22) * mm});
            skLineSegment(sketch, "E1675", {"start": v(19.39, 139.22) * mm, "end": v(-0.14, 140.77) * mm});
            skLineSegment(sketch, "E1676", {"start": v(-0.14, 140.77) * mm, "end": v(-19.63, 139.17) * mm});
            skLineSegment(sketch, "E1677", {"start": v(-19.63, 139.17) * mm, "end": v(-38.69, 134.44) * mm});
            skLineSegment(sketch, "E1678", {"start": v(-38.69, 134.44) * mm, "end": v(-56.9, 126.58) * mm});
            skLineSegment(sketch, "E1679", {"start": v(-56.9, 126.58) * mm, "end": v(-73.85, 115.6) * mm});
            skLineSegment(sketch, "E1680", {"start": v(-73.85, 115.6) * mm, "end": v(-55.41, 115.6) * mm});
            skLineSegment(sketch, "E1681", {"start": v(-55.41, 115.6) * mm, "end": v(-36.99, 115.6) * mm});
            skLineSegment(sketch, "E1682", {"start": v(-36.99, 115.6) * mm, "end": v(-18.57, 115.6) * mm});
            skLineSegment(sketch, "E1683", {"start": v(-18.57, 115.6) * mm, "end": v(-0.13, 115.6) * mm});
            skLineSegment(sketch, "E1684", {"start": v(-0.13, 115.6) * mm, "end": v(18.33, 115.6) * mm});
            skLineSegment(sketch, "E1685", {"start": v(18.33, 115.6) * mm, "end": v(36.84, 115.6) * mm});
            skLineSegment(sketch, "E1686", {"start": v(36.84, 115.6) * mm, "end": v(55.4, 115.6) * mm});
            skLineSegment(sketch, "E1687", {"start": v(55.4, 115.6) * mm, "end": v(74.04, 115.6) * mm});
            skLineSegment(sketch, "E1688", {"start": v(-161.89, -21.6) * mm, "end": v(-162.7, -13.3) * mm});
            skLineSegment(sketch, "E1689", {"start": v(-162.7, -13.3) * mm, "end": v(-165.06, -5.58) * mm});
            skLineSegment(sketch, "E1690", {"start": v(-165.06, -5.58) * mm, "end": v(-168.8, 1.4) * mm});
            skLineSegment(sketch, "E1691", {"start": v(-168.8, 1.4) * mm, "end": v(-173.76, 7.47) * mm});
            skLineSegment(sketch, "E1692", {"start": v(-173.76, 7.47) * mm, "end": v(-179.8, 12.48) * mm});
            skLineSegment(sketch, "E1693", {"start": v(-179.8, 12.48) * mm, "end": v(-186.72, 16.25) * mm});
            skLineSegment(sketch, "E1694", {"start": v(-186.72, 16.25) * mm, "end": v(-194.4, 18.64) * mm});
            skLineSegment(sketch, "E1695", {"start": v(-194.4, 18.64) * mm, "end": v(-202.66, 19.48) * mm});
            skLineSegment(sketch, "E1696", {"start": v(-202.66, 19.48) * mm, "end": v(-210.81, 18.66) * mm});
            skLineSegment(sketch, "E1697", {"start": v(-210.81, 18.66) * mm, "end": v(-218.44, 16.28) * mm});
            skLineSegment(sketch, "E1698", {"start": v(-218.44, 16.28) * mm, "end": v(-225.36, 12.5) * mm});
            skLineSegment(sketch, "E1699", {"start": v(-225.36, 12.5) * mm, "end": v(-231.4, 7.52) * mm});
            skLineSegment(sketch, "E1700", {"start": v(-231.4, 7.52) * mm, "end": v(-236.42, 1.49) * mm});
            skLineSegment(sketch, "E1701", {"start": v(-236.42, 1.49) * mm, "end": v(-240.22, -5.43) * mm});
            skLineSegment(sketch, "E1702", {"start": v(-240.22, -5.43) * mm, "end": v(-242.64, -13.05) * mm});
            skLineSegment(sketch, "E1703", {"start": v(-242.64, -13.05) * mm, "end": v(-243.5, -21.21) * mm});
            skLineSegment(sketch, "E1704", {"start": v(-243.5, -21.21) * mm, "end": v(-242.7, -29.5) * mm});
            skLineSegment(sketch, "E1705", {"start": v(-242.7, -29.5) * mm, "end": v(-240.36, -37.22) * mm});
            skLineSegment(sketch, "E1706", {"start": v(-240.36, -37.22) * mm, "end": v(-236.61, -44.23) * mm});
            skLineSegment(sketch, "E1707", {"start": v(-236.61, -44.23) * mm, "end": v(-231.64, -50.34) * mm});
            skLineSegment(sketch, "E1708", {"start": v(-231.64, -50.34) * mm, "end": v(-225.61, -55.4) * mm});
            skLineSegment(sketch, "E1709", {"start": v(-225.61, -55.4) * mm, "end": v(-218.69, -59.24) * mm});
            skLineSegment(sketch, "E1710", {"start": v(-218.69, -59.24) * mm, "end": v(-211.03, -61.68) * mm});
            skLineSegment(sketch, "E1711", {"start": v(-211.03, -61.68) * mm, "end": v(-202.8, -62.57) * mm});
            skLineSegment(sketch, "E1712", {"start": v(-202.8, -62.57) * mm, "end": v(-194.57, -61.78) * mm});
            skLineSegment(sketch, "E1713", {"start": v(-194.57, -61.78) * mm, "end": v(-186.9, -59.42) * mm});
            skLineSegment(sketch, "E1714", {"start": v(-186.9, -59.42) * mm, "end": v(-179.95, -55.66) * mm});
            skLineSegment(sketch, "E1715", {"start": v(-179.95, -55.66) * mm, "end": v(-173.9, -50.67) * mm});
            skLineSegment(sketch, "E1716", {"start": v(-173.9, -50.67) * mm, "end": v(-168.9, -44.6) * mm});
            skLineSegment(sketch, "E1717", {"start": v(-168.9, -44.6) * mm, "end": v(-165.12, -37.62) * mm});
            skLineSegment(sketch, "E1718", {"start": v(-165.12, -37.62) * mm, "end": v(-162.73, -29.9) * mm});
            skLineSegment(sketch, "E1719", {"start": v(-162.73, -29.9) * mm, "end": v(-161.89, -21.6) * mm});
            skLineSegment(sketch, "E1720", {"start": v(162.25, -21.22) * mm, "end": v(163.02, -29.54) * mm});
            skLineSegment(sketch, "E1721", {"start": v(163.02, -29.54) * mm, "end": v(165.33, -37.28) * mm});
            skLineSegment(sketch, "E1722", {"start": v(165.33, -37.28) * mm, "end": v(169.02, -44.27) * mm});
            skLineSegment(sketch, "E1723", {"start": v(169.02, -44.27) * mm, "end": v(173.93, -50.36) * mm});
            skLineSegment(sketch, "E1724", {"start": v(173.93, -50.36) * mm, "end": v(179.92, -55.39) * mm});
            skLineSegment(sketch, "E1725", {"start": v(179.92, -55.39) * mm, "end": v(186.82, -59.2) * mm});
            skLineSegment(sketch, "E1726", {"start": v(186.82, -59.2) * mm, "end": v(194.5, -61.65) * mm});
            skLineSegment(sketch, "E1727", {"start": v(194.5, -61.65) * mm, "end": v(202.78, -62.57) * mm});
            skLineSegment(sketch, "E1728", {"start": v(202.78, -62.57) * mm, "end": v(210.89, -61.82) * mm});
            skLineSegment(sketch, "E1729", {"start": v(210.89, -61.82) * mm, "end": v(218.5, -59.48) * mm});
            skLineSegment(sketch, "E1730", {"start": v(218.5, -59.48) * mm, "end": v(225.46, -55.74) * mm});
            skLineSegment(sketch, "E1731", {"start": v(225.46, -55.74) * mm, "end": v(231.55, -50.77) * mm});
            skLineSegment(sketch, "E1732", {"start": v(231.55, -50.77) * mm, "end": v(236.62, -44.74) * mm});
            skLineSegment(sketch, "E1733", {"start": v(236.62, -44.74) * mm, "end": v(240.48, -37.84) * mm});
            skLineSegment(sketch, "E1734", {"start": v(240.48, -37.84) * mm, "end": v(242.95, -30.23) * mm});
            skLineSegment(sketch, "E1735", {"start": v(242.95, -30.23) * mm, "end": v(243.86, -22.1) * mm});
            skLineSegment(sketch, "E1736", {"start": v(243.86, -22.1) * mm, "end": v(243.08, -13.71) * mm});
            skLineSegment(sketch, "E1737", {"start": v(243.08, -13.71) * mm, "end": v(240.71, -5.9) * mm});
            skLineSegment(sketch, "E1738", {"start": v(240.71, -5.9) * mm, "end": v(236.94, 1.2) * mm});
            skLineSegment(sketch, "E1739", {"start": v(236.94, 1.2) * mm, "end": v(231.92, 7.37) * mm});
            skLineSegment(sketch, "E1740", {"start": v(231.92, 7.37) * mm, "end": v(225.84, 12.46) * mm});
            skLineSegment(sketch, "E1741", {"start": v(225.84, 12.46) * mm, "end": v(218.86, 16.3) * mm});
            skLineSegment(sketch, "E1742", {"start": v(218.86, 16.3) * mm, "end": v(211.16, 18.69) * mm});
            skLineSegment(sketch, "E1743", {"start": v(211.16, 18.69) * mm, "end": v(202.9, 19.48) * mm});
            skLineSegment(sketch, "E1744", {"start": v(202.9, 19.48) * mm, "end": v(194.68, 18.6) * mm});
            skLineSegment(sketch, "E1745", {"start": v(194.68, 18.6) * mm, "end": v(187.04, 16.22) * mm});
            skLineSegment(sketch, "E1746", {"start": v(187.04, 16.22) * mm, "end": v(180.15, 12.47) * mm});
            skLineSegment(sketch, "E1747", {"start": v(180.15, 12.47) * mm, "end": v(174.15, 7.51) * mm});
            skLineSegment(sketch, "E1748", {"start": v(174.15, 7.51) * mm, "end": v(169.2, 1.51) * mm});
            skLineSegment(sketch, "E1749", {"start": v(169.2, 1.51) * mm, "end": v(165.47, -5.38) * mm});
            skLineSegment(sketch, "E1750", {"start": v(165.47, -5.38) * mm, "end": v(163.1, -13) * mm});
            skLineSegment(sketch, "E1751", {"start": v(163.1, -13) * mm, "end": v(162.25, -21.22) * mm});
            skLineSegment(sketch, "E1752", {"start": v(134.16, -158.1) * mm, "end": v(133.59, -152.46) * mm});
            skLineSegment(sketch, "E1753", {"start": v(133.59, -152.46) * mm, "end": v(131.95, -147.4) * mm});
            skLineSegment(sketch, "E1754", {"start": v(131.95, -147.4) * mm, "end": v(129.39, -143.05) * mm});
            skLineSegment(sketch, "E1755", {"start": v(129.39, -143.05) * mm, "end": v(126.05, -139.5) * mm});
            skLineSegment(sketch, "E1756", {"start": v(126.05, -139.5) * mm, "end": v(122.06, -136.86) * mm});
            skLineSegment(sketch, "E1757", {"start": v(122.06, -136.86) * mm, "end": v(117.57, -135.24) * mm});
            skLineSegment(sketch, "E1758", {"start": v(117.57, -135.24) * mm, "end": v(112.72, -134.74) * mm});
            skLineSegment(sketch, "E1759", {"start": v(112.72, -134.74) * mm, "end": v(107.63, -135.48) * mm});
            skLineSegment(sketch, "E1760", {"start": v(107.63, -135.48) * mm, "end": v(105, -136.33) * mm});
            skLineSegment(sketch, "E1761", {"start": v(105, -136.33) * mm, "end": v(102.46, -137.38) * mm});
            skLineSegment(sketch, "E1762", {"start": v(102.46, -137.38) * mm, "end": v(100, -138.59) * mm});
            skLineSegment(sketch, "E1763", {"start": v(100, -138.59) * mm, "end": v(97.6, -139.93) * mm});
            skLineSegment(sketch, "E1764", {"start": v(97.6, -139.93) * mm, "end": v(95.26, -141.35) * mm});
            skLineSegment(sketch, "E1765", {"start": v(95.26, -141.35) * mm, "end": v(92.93, -142.82) * mm});
            skLineSegment(sketch, "E1766", {"start": v(92.93, -142.82) * mm, "end": v(90.6, -144.3) * mm});
            skLineSegment(sketch, "E1767", {"start": v(90.6, -144.3) * mm, "end": v(88.27, -145.75) * mm});
            skLineSegment(sketch, "E1768", {"start": v(88.27, -145.75) * mm, "end": v(87.58, -146.26) * mm});
            skLineSegment(sketch, "E1769", {"start": v(87.58, -146.26) * mm, "end": v(87.14, -146.81) * mm});
            skLineSegment(sketch, "E1770", {"start": v(87.14, -146.81) * mm, "end": v(86.9, -147.39) * mm});
            skLineSegment(sketch, "E1771", {"start": v(86.9, -147.39) * mm, "end": v(86.86, -147.99) * mm});
            skLineSegment(sketch, "E1772", {"start": v(86.86, -147.99) * mm, "end": v(86.96, -148.6) * mm});
            skLineSegment(sketch, "E1773", {"start": v(86.96, -148.6) * mm, "end": v(87.18, -149.23) * mm});
            skLineSegment(sketch, "E1774", {"start": v(87.18, -149.23) * mm, "end": v(87.5, -149.86) * mm});
            skLineSegment(sketch, "E1775", {"start": v(87.5, -149.86) * mm, "end": v(87.85, -150.49) * mm});
            skLineSegment(sketch, "E1776", {"start": v(87.85, -150.49) * mm, "end": v(90.2, -154.4) * mm});
            skLineSegment(sketch, "E1777", {"start": v(90.2, -154.4) * mm, "end": v(92.54, -158.31) * mm});
            skLineSegment(sketch, "E1778", {"start": v(92.54, -158.31) * mm, "end": v(94.89, -162.22) * mm});
            skLineSegment(sketch, "E1779", {"start": v(94.89, -162.22) * mm, "end": v(97.23, -166.14) * mm});
            skLineSegment(sketch, "E1780", {"start": v(97.23, -166.14) * mm, "end": v(99.58, -170.05) * mm});
            skLineSegment(sketch, "E1781", {"start": v(99.58, -170.05) * mm, "end": v(101.92, -173.96) * mm});
            skLineSegment(sketch, "E1782", {"start": v(101.92, -173.96) * mm, "end": v(104.26, -177.88) * mm});
            skLineSegment(sketch, "E1783", {"start": v(104.26, -177.88) * mm, "end": v(106.6, -181.8) * mm});
            skLineSegment(sketch, "E1784", {"start": v(106.6, -181.8) * mm, "end": v(107.07, -182.51) * mm});
            skLineSegment(sketch, "E1785", {"start": v(107.07, -182.51) * mm, "end": v(107.56, -183.1) * mm});
            skLineSegment(sketch, "E1786", {"start": v(107.56, -183.1) * mm, "end": v(108.09, -183.54) * mm});
            skLineSegment(sketch, "E1787", {"start": v(108.09, -183.54) * mm, "end": v(108.66, -183.83) * mm});
            skLineSegment(sketch, "E1788", {"start": v(108.66, -183.83) * mm, "end": v(109.27, -183.96) * mm});
            skLineSegment(sketch, "E1789", {"start": v(109.27, -183.96) * mm, "end": v(109.94, -183.92) * mm});
            skLineSegment(sketch, "E1790", {"start": v(109.94, -183.92) * mm, "end": v(110.67, -183.68) * mm});
            skLineSegment(sketch, "E1791", {"start": v(110.67, -183.68) * mm, "end": v(111.47, -183.25) * mm});
            skLineSegment(sketch, "E1792", {"start": v(111.47, -183.25) * mm, "end": v(113.27, -182.13) * mm});
            skLineSegment(sketch, "E1793", {"start": v(113.27, -182.13) * mm, "end": v(115.09, -181.02) * mm});
            skLineSegment(sketch, "E1794", {"start": v(115.09, -181.02) * mm, "end": v(116.9, -179.92) * mm});
            skLineSegment(sketch, "E1795", {"start": v(116.9, -179.92) * mm, "end": v(118.73, -178.82) * mm});
            skLineSegment(sketch, "E1796", {"start": v(118.73, -178.82) * mm, "end": v(120.53, -177.7) * mm});
            skLineSegment(sketch, "E1797", {"start": v(120.53, -177.7) * mm, "end": v(122.32, -176.55) * mm});
            skLineSegment(sketch, "E1798", {"start": v(122.32, -176.55) * mm, "end": v(124.07, -175.37) * mm});
            skLineSegment(sketch, "E1799", {"start": v(124.07, -175.37) * mm, "end": v(125.78, -174.13) * mm});
            skLineSegment(sketch, "E1800", {"start": v(125.78, -174.13) * mm, "end": v(127.71, -172.52) * mm});
            skLineSegment(sketch, "E1801", {"start": v(127.71, -172.52) * mm, "end": v(129.41, -170.78) * mm});
            skLineSegment(sketch, "E1802", {"start": v(129.41, -170.78) * mm, "end": v(130.86, -168.91) * mm});
            skLineSegment(sketch, "E1803", {"start": v(130.86, -168.91) * mm, "end": v(132.07, -166.94) * mm});
            skLineSegment(sketch, "E1804", {"start": v(132.07, -166.94) * mm, "end": v(133, -164.86) * mm});
            skLineSegment(sketch, "E1805", {"start": v(133, -164.86) * mm, "end": v(133.68, -162.68) * mm});
            skLineSegment(sketch, "E1806", {"start": v(133.68, -162.68) * mm, "end": v(134.07, -160.43) * mm});
            skLineSegment(sketch, "E1807", {"start": v(134.07, -160.43) * mm, "end": v(134.16, -158.1) * mm});
            skLineSegment(sketch, "E1808", {"start": v(-75.8, -194.06) * mm, "end": v(-75.97, -194.9) * mm});
            skLineSegment(sketch, "E1809", {"start": v(-75.97, -194.9) * mm, "end": v(-75.97, -195.6) * mm});
            skLineSegment(sketch, "E1810", {"start": v(-75.97, -195.6) * mm, "end": v(-75.8, -196.18) * mm});
            skLineSegment(sketch, "E1811", {"start": v(-75.8, -196.18) * mm, "end": v(-75.5, -196.67) * mm});
            skLineSegment(sketch, "E1812", {"start": v(-75.5, -196.67) * mm, "end": v(-75.07, -197.08) * mm});
            skLineSegment(sketch, "E1813", {"start": v(-75.07, -197.08) * mm, "end": v(-74.53, -197.42) * mm});
            skLineSegment(sketch, "E1814", {"start": v(-74.53, -197.42) * mm, "end": v(-73.88, -197.7) * mm});
            skLineSegment(sketch, "E1815", {"start": v(-73.88, -197.7) * mm, "end": v(-73.14, -197.96) * mm});
            skLineSegment(sketch, "E1816", {"start": v(-73.14, -197.96) * mm, "end": v(-72.27, -198.17) * mm});
            skLineSegment(sketch, "E1817", {"start": v(-72.27, -198.17) * mm, "end": v(-71.5, -198.25) * mm});
            skLineSegment(sketch, "E1818", {"start": v(-71.5, -198.25) * mm, "end": v(-70.82, -198.18) * mm});
            skLineSegment(sketch, "E1819", {"start": v(-70.82, -198.18) * mm, "end": v(-70.22, -197.97) * mm});
            skLineSegment(sketch, "E1820", {"start": v(-70.22, -197.97) * mm, "end": v(-69.71, -197.6) * mm});
            skLineSegment(sketch, "E1821", {"start": v(-69.71, -197.6) * mm, "end": v(-69.29, -197.1) * mm});
            skLineSegment(sketch, "E1822", {"start": v(-69.29, -197.1) * mm, "end": v(-68.94, -196.42) * mm});
            skLineSegment(sketch, "E1823", {"start": v(-68.94, -196.42) * mm, "end": v(-68.66, -195.6) * mm});
            skLineSegment(sketch, "E1824", {"start": v(-68.66, -195.6) * mm, "end": v(-67.99, -193.06) * mm});
            skLineSegment(sketch, "E1825", {"start": v(-67.99, -193.06) * mm, "end": v(-67.31, -190.53) * mm});
            skLineSegment(sketch, "E1826", {"start": v(-67.31, -190.53) * mm, "end": v(-66.64, -188) * mm});
            skLineSegment(sketch, "E1827", {"start": v(-66.64, -188) * mm, "end": v(-65.96, -185.47) * mm});
            skLineSegment(sketch, "E1828", {"start": v(-65.96, -185.47) * mm, "end": v(-65.29, -182.94) * mm});
            skLineSegment(sketch, "E1829", {"start": v(-65.29, -182.94) * mm, "end": v(-64.61, -180.41) * mm});
            skLineSegment(sketch, "E1830", {"start": v(-64.61, -180.41) * mm, "end": v(-63.93, -177.89) * mm});
            skLineSegment(sketch, "E1831", {"start": v(-63.93, -177.89) * mm, "end": v(-63.25, -175.36) * mm});
            skLineSegment(sketch, "E1832", {"start": v(-63.25, -175.36) * mm, "end": v(-63.14, -174.88) * mm});
            skLineSegment(sketch, "E1833", {"start": v(-63.14, -174.88) * mm, "end": v(-63.05, -174.37) * mm});
            skLineSegment(sketch, "E1834", {"start": v(-63.05, -174.37) * mm, "end": v(-62.95, -173.86) * mm});
            skLineSegment(sketch, "E1835", {"start": v(-62.95, -173.86) * mm, "end": v(-62.8, -173.38) * mm});
            skLineSegment(sketch, "E1836", {"start": v(-62.8, -173.38) * mm, "end": v(-62.6, -172.96) * mm});
            skLineSegment(sketch, "E1837", {"start": v(-62.6, -172.96) * mm, "end": v(-62.3, -172.62) * mm});
            skLineSegment(sketch, "E1838", {"start": v(-62.3, -172.62) * mm, "end": v(-61.9, -172.38) * mm});
            skLineSegment(sketch, "E1839", {"start": v(-61.9, -172.38) * mm, "end": v(-61.34, -172.29) * mm});
            skLineSegment(sketch, "E1840", {"start": v(-61.34, -172.29) * mm, "end": v(-60.92, -172.35) * mm});
            skLineSegment(sketch, "E1841", {"start": v(-60.92, -172.35) * mm, "end": v(-60.56, -172.53) * mm});
            skLineSegment(sketch, "E1842", {"start": v(-60.56, -172.53) * mm, "end": v(-60.28, -172.82) * mm});
            skLineSegment(sketch, "E1843", {"start": v(-60.28, -172.82) * mm, "end": v(-60.05, -173.19) * mm});
            skLineSegment(sketch, "E1844", {"start": v(-60.05, -173.19) * mm, "end": v(-59.85, -173.6) * mm});
            skLineSegment(sketch, "E1845", {"start": v(-59.85, -173.6) * mm, "end": v(-59.68, -174.04) * mm});
            skLineSegment(sketch, "E1846", {"start": v(-59.68, -174.04) * mm, "end": v(-59.51, -174.48) * mm});
            skLineSegment(sketch, "E1847", {"start": v(-59.51, -174.48) * mm, "end": v(-59.34, -174.89) * mm});
            skLineSegment(sketch, "E1848", {"start": v(-59.34, -174.89) * mm, "end": v(-59.22, -175.17) * mm});
            skLineSegment(sketch, "E1849", {"start": v(-59.22, -175.17) * mm, "end": v(-59.1, -175.46) * mm});
            skLineSegment(sketch, "E1850", {"start": v(-59.1, -175.46) * mm, "end": v(-58.98, -175.75) * mm});
            skLineSegment(sketch, "E1851", {"start": v(-58.98, -175.75) * mm, "end": v(-58.86, -176.04) * mm});
            skLineSegment(sketch, "E1852", {"start": v(-58.86, -176.04) * mm, "end": v(-58.75, -176.33) * mm});
            skLineSegment(sketch, "E1853", {"start": v(-58.75, -176.33) * mm, "end": v(-58.63, -176.62) * mm});
            skLineSegment(sketch, "E1854", {"start": v(-58.63, -176.62) * mm, "end": v(-58.52, -176.9) * mm});
            skLineSegment(sketch, "E1855", {"start": v(-58.52, -176.9) * mm, "end": v(-58.4, -177.2) * mm});
            skLineSegment(sketch, "E1856", {"start": v(-58.4, -177.2) * mm, "end": v(-57.14, -180.25) * mm});
            skLineSegment(sketch, "E1857", {"start": v(-57.14, -180.25) * mm, "end": v(-55.88, -183.3) * mm});
            skLineSegment(sketch, "E1858", {"start": v(-55.88, -183.3) * mm, "end": v(-54.62, -186.36) * mm});
            skLineSegment(sketch, "E1859", {"start": v(-54.62, -186.36) * mm, "end": v(-53.36, -189.42) * mm});
            skLineSegment(sketch, "E1860", {"start": v(-53.36, -189.42) * mm, "end": v(-52.1, -192.47) * mm});
            skLineSegment(sketch, "E1861", {"start": v(-52.1, -192.47) * mm, "end": v(-50.84, -195.53) * mm});
            skLineSegment(sketch, "E1862", {"start": v(-50.84, -195.53) * mm, "end": v(-49.59, -198.58) * mm});
            skLineSegment(sketch, "E1863", {"start": v(-49.59, -198.58) * mm, "end": v(-48.33, -201.64) * mm});
            skLineSegment(sketch, "E1864", {"start": v(-48.33, -201.64) * mm, "end": v(-47.9, -202.56) * mm});
            skLineSegment(sketch, "E1865", {"start": v(-47.9, -202.56) * mm, "end": v(-47.4, -203.38) * mm});
            skLineSegment(sketch, "E1866", {"start": v(-47.4, -203.38) * mm, "end": v(-46.83, -204.1) * mm});
            skLineSegment(sketch, "E1867", {"start": v(-46.83, -204.1) * mm, "end": v(-46.17, -204.69) * mm});
            skLineSegment(sketch, "E1868", {"start": v(-46.17, -204.69) * mm, "end": v(-45.43, -205.15) * mm});
            skLineSegment(sketch, "E1869", {"start": v(-45.43, -205.15) * mm, "end": v(-44.6, -205.47) * mm});
            skLineSegment(sketch, "E1870", {"start": v(-44.6, -205.47) * mm, "end": v(-43.7, -205.65) * mm});
            skLineSegment(sketch, "E1871", {"start": v(-43.7, -205.65) * mm, "end": v(-42.68, -205.67) * mm});
            skLineSegment(sketch, "E1872", {"start": v(-42.68, -205.67) * mm, "end": v(-41.76, -205.5) * mm});
            skLineSegment(sketch, "E1873", {"start": v(-41.76, -205.5) * mm, "end": v(-41.1, -205.15) * mm});
            skLineSegment(sketch, "E1874", {"start": v(-41.1, -205.15) * mm, "end": v(-40.62, -204.63) * mm});
            skLineSegment(sketch, "E1875", {"start": v(-40.62, -204.63) * mm, "end": v(-40.3, -204) * mm});
            skLineSegment(sketch, "E1876", {"start": v(-40.3, -204) * mm, "end": v(-40.1, -203.3) * mm});
            skLineSegment(sketch, "E1877", {"start": v(-40.1, -203.3) * mm, "end": v(-39.95, -202.56) * mm});
            skLineSegment(sketch, "E1878", {"start": v(-39.95, -202.56) * mm, "end": v(-39.83, -201.83) * mm});
            skLineSegment(sketch, "E1879", {"start": v(-39.83, -201.83) * mm, "end": v(-39.68, -201.13) * mm});
            skLineSegment(sketch, "E1880", {"start": v(-39.68, -201.13) * mm, "end": v(-38.6, -197.1) * mm});
            skLineSegment(sketch, "E1881", {"start": v(-38.6, -197.1) * mm, "end": v(-37.51, -193.07) * mm});
            skLineSegment(sketch, "E1882", {"start": v(-37.51, -193.07) * mm, "end": v(-36.44, -189.03) * mm});
            skLineSegment(sketch, "E1883", {"start": v(-36.44, -189.03) * mm, "end": v(-35.38, -184.99) * mm});
            skLineSegment(sketch, "E1884", {"start": v(-35.38, -184.99) * mm, "end": v(-34.32, -180.95) * mm});
            skLineSegment(sketch, "E1885", {"start": v(-34.32, -180.95) * mm, "end": v(-33.27, -176.9) * mm});
            skLineSegment(sketch, "E1886", {"start": v(-33.27, -176.9) * mm, "end": v(-32.22, -172.86) * mm});
            skLineSegment(sketch, "E1887", {"start": v(-32.22, -172.86) * mm, "end": v(-31.17, -168.82) * mm});
            skLineSegment(sketch, "E1888", {"start": v(-31.17, -168.82) * mm, "end": v(-30.92, -167.93) * mm});
            skLineSegment(sketch, "E1889", {"start": v(-30.92, -167.93) * mm, "end": v(-30.69, -167.04) * mm});
            skLineSegment(sketch, "E1890", {"start": v(-30.69, -167.04) * mm, "end": v(-30.53, -166.17) * mm});
            skLineSegment(sketch, "E1891", {"start": v(-30.53, -166.17) * mm, "end": v(-30.51, -165.35) * mm});
            skLineSegment(sketch, "E1892", {"start": v(-30.51, -165.35) * mm, "end": v(-30.7, -164.58) * mm});
            skLineSegment(sketch, "E1893", {"start": v(-30.7, -164.58) * mm, "end": v(-31.17, -163.9) * mm});
            skLineSegment(sketch, "E1894", {"start": v(-31.17, -163.9) * mm, "end": v(-31.97, -163.33) * mm});
            skLineSegment(sketch, "E1895", {"start": v(-31.97, -163.33) * mm, "end": v(-33.18, -162.88) * mm});
            skLineSegment(sketch, "E1896", {"start": v(-33.18, -162.88) * mm, "end": v(-34.45, -162.67) * mm});
            skLineSegment(sketch, "E1897", {"start": v(-34.45, -162.67) * mm, "end": v(-35.43, -162.76) * mm});
            skLineSegment(sketch, "E1898", {"start": v(-35.43, -162.76) * mm, "end": v(-36.18, -163.11) * mm});
            skLineSegment(sketch, "E1899", {"start": v(-36.18, -163.11) * mm, "end": v(-36.74, -163.67) * mm});
            skLineSegment(sketch, "E1900", {"start": v(-36.74, -163.67) * mm, "end": v(-37.16, -164.38) * mm});
            skLineSegment(sketch, "E1901", {"start": v(-37.16, -164.38) * mm, "end": v(-37.47, -165.2) * mm});
            skLineSegment(sketch, "E1902", {"start": v(-37.47, -165.2) * mm, "end": v(-37.72, -166.1) * mm});
            skLineSegment(sketch, "E1903", {"start": v(-37.72, -166.1) * mm, "end": v(-37.96, -167) * mm});
            skLineSegment(sketch, "E1904", {"start": v(-37.96, -167) * mm, "end": v(-38.59, -169.35) * mm});
            skLineSegment(sketch, "E1905", {"start": v(-38.59, -169.35) * mm, "end": v(-39.21, -171.7) * mm});
            skLineSegment(sketch, "E1906", {"start": v(-39.21, -171.7) * mm, "end": v(-39.83, -174.05) * mm});
            skLineSegment(sketch, "E1907", {"start": v(-39.83, -174.05) * mm, "end": v(-40.45, -176.4) * mm});
            skLineSegment(sketch, "E1908", {"start": v(-40.45, -176.4) * mm, "end": v(-41.07, -178.75) * mm});
            skLineSegment(sketch, "E1909", {"start": v(-41.07, -178.75) * mm, "end": v(-41.7, -181.1) * mm});
            skLineSegment(sketch, "E1910", {"start": v(-41.7, -181.1) * mm, "end": v(-42.32, -183.45) * mm});
            skLineSegment(sketch, "E1911", {"start": v(-42.32, -183.45) * mm, "end": v(-42.95, -185.8) * mm});
            skLineSegment(sketch, "E1912", {"start": v(-42.95, -185.8) * mm, "end": v(-43.04, -186.15) * mm});
            skLineSegment(sketch, "E1913", {"start": v(-43.04, -186.15) * mm, "end": v(-43.14, -186.52) * mm});
            skLineSegment(sketch, "E1914", {"start": v(-43.14, -186.52) * mm, "end": v(-43.26, -186.89) * mm});
            skLineSegment(sketch, "E1915", {"start": v(-43.26, -186.89) * mm, "end": v(-43.4, -187.23) * mm});
            skLineSegment(sketch, "E1916", {"start": v(-43.4, -187.23) * mm, "end": v(-43.6, -187.54) * mm});
            skLineSegment(sketch, "E1917", {"start": v(-43.6, -187.54) * mm, "end": v(-43.84, -187.8) * mm});
            skLineSegment(sketch, "E1918", {"start": v(-43.84, -187.8) * mm, "end": v(-44.15, -188) * mm});
            skLineSegment(sketch, "E1919", {"start": v(-44.15, -188) * mm, "end": v(-44.54, -188.1) * mm});
            skLineSegment(sketch, "E1920", {"start": v(-44.54, -188.1) * mm, "end": v(-44.97, -188.1) * mm});
            skLineSegment(sketch, "E1921", {"start": v(-44.97, -188.1) * mm, "end": v(-45.32, -187.98) * mm});
            skLineSegment(sketch, "E1922", {"start": v(-45.32, -187.98) * mm, "end": v(-45.6, -187.77) * mm});
            skLineSegment(sketch, "E1923", {"start": v(-45.6, -187.77) * mm, "end": v(-45.82, -187.5) * mm});
            skLineSegment(sketch, "E1924", {"start": v(-45.82, -187.5) * mm, "end": v(-46, -187.18) * mm});
            skLineSegment(sketch, "E1925", {"start": v(-46, -187.18) * mm, "end": v(-46.16, -186.82) * mm});
            skLineSegment(sketch, "E1926", {"start": v(-46.16, -186.82) * mm, "end": v(-46.3, -186.47) * mm});
            skLineSegment(sketch, "E1927", {"start": v(-46.3, -186.47) * mm, "end": v(-46.43, -186.12) * mm});
            skLineSegment(sketch, "E1928", {"start": v(-46.43, -186.12) * mm, "end": v(-46.89, -185.03) * mm});
            skLineSegment(sketch, "E1929", {"start": v(-46.89, -185.03) * mm, "end": v(-47.34, -183.94) * mm});
            skLineSegment(sketch, "E1930", {"start": v(-47.34, -183.94) * mm, "end": v(-47.8, -182.84) * mm});
            skLineSegment(sketch, "E1931", {"start": v(-47.8, -182.84) * mm, "end": v(-48.24, -181.74) * mm});
            skLineSegment(sketch, "E1932", {"start": v(-48.24, -181.74) * mm, "end": v(-48.68, -180.65) * mm});
            skLineSegment(sketch, "E1933", {"start": v(-48.68, -180.65) * mm, "end": v(-49.13, -179.55) * mm});
            skLineSegment(sketch, "E1934", {"start": v(-49.13, -179.55) * mm, "end": v(-49.57, -178.45) * mm});
            skLineSegment(sketch, "E1935", {"start": v(-49.57, -178.45) * mm, "end": v(-50.02, -177.35) * mm});
            skLineSegment(sketch, "E1936", {"start": v(-50.02, -177.35) * mm, "end": v(-50.95, -175.04) * mm});
            skLineSegment(sketch, "E1937", {"start": v(-50.95, -175.04) * mm, "end": v(-51.89, -172.73) * mm});
            skLineSegment(sketch, "E1938", {"start": v(-51.89, -172.73) * mm, "end": v(-52.83, -170.42) * mm});
            skLineSegment(sketch, "E1939", {"start": v(-52.83, -170.42) * mm, "end": v(-53.76, -168.1) * mm});
            skLineSegment(sketch, "E1940", {"start": v(-53.76, -168.1) * mm, "end": v(-54.7, -165.8) * mm});
            skLineSegment(sketch, "E1941", {"start": v(-54.7, -165.8) * mm, "end": v(-55.63, -163.48) * mm});
            skLineSegment(sketch, "E1942", {"start": v(-55.63, -163.48) * mm, "end": v(-56.56, -161.16) * mm});
            skLineSegment(sketch, "E1943", {"start": v(-56.56, -161.16) * mm, "end": v(-57.48, -158.85) * mm});
            skLineSegment(sketch, "E1944", {"start": v(-57.48, -158.85) * mm, "end": v(-57.94, -157.91) * mm});
            skLineSegment(sketch, "E1945", {"start": v(-57.94, -157.91) * mm, "end": v(-58.5, -157.15) * mm});
            skLineSegment(sketch, "E1946", {"start": v(-58.5, -157.15) * mm, "end": v(-59.16, -156.54) * mm});
            skLineSegment(sketch, "E1947", {"start": v(-59.16, -156.54) * mm, "end": v(-59.9, -156.05) * mm});
            skLineSegment(sketch, "E1948", {"start": v(-59.9, -156.05) * mm, "end": v(-60.7, -155.68) * mm});
            skLineSegment(sketch, "E1949", {"start": v(-60.7, -155.68) * mm, "end": v(-61.57, -155.4) * mm});
            skLineSegment(sketch, "E1950", {"start": v(-61.57, -155.4) * mm, "end": v(-62.49, -155.21) * mm});
            skLineSegment(sketch, "E1951", {"start": v(-62.49, -155.21) * mm, "end": v(-63.44, -155.07) * mm});
            skLineSegment(sketch, "E1952", {"start": v(-63.44, -155.07) * mm, "end": v(-64.05, -155.06) * mm});
            skLineSegment(sketch, "E1953", {"start": v(-64.05, -155.06) * mm, "end": v(-64.55, -155.16) * mm});
            skLineSegment(sketch, "E1954", {"start": v(-64.55, -155.16) * mm, "end": v(-64.98, -155.37) * mm});
            skLineSegment(sketch, "E1955", {"start": v(-64.98, -155.37) * mm, "end": v(-65.33, -155.67) * mm});
            skLineSegment(sketch, "E1956", {"start": v(-65.33, -155.67) * mm, "end": v(-65.61, -156.03) * mm});
            skLineSegment(sketch, "E1957", {"start": v(-65.61, -156.03) * mm, "end": v(-65.84, -156.46) * mm});
            skLineSegment(sketch, "E1958", {"start": v(-65.84, -156.46) * mm, "end": v(-66.02, -156.92) * mm});
            skLineSegment(sketch, "E1959", {"start": v(-66.02, -156.92) * mm, "end": v(-66.17, -157.4) * mm});
            skLineSegment(sketch, "E1960", {"start": v(-66.17, -157.4) * mm, "end": v(-67.38, -161.99) * mm});
            skLineSegment(sketch, "E1961", {"start": v(-67.38, -161.99) * mm, "end": v(-68.59, -166.57) * mm});
            skLineSegment(sketch, "E1962", {"start": v(-68.59, -166.57) * mm, "end": v(-69.8, -171.15) * mm});
            skLineSegment(sketch, "E1963", {"start": v(-69.8, -171.15) * mm, "end": v(-71, -175.73) * mm});
            skLineSegment(sketch, "E1964", {"start": v(-71, -175.73) * mm, "end": v(-72.2, -180.32) * mm});
            skLineSegment(sketch, "E1965", {"start": v(-72.2, -180.32) * mm, "end": v(-73.4, -184.9) * mm});
            skLineSegment(sketch, "E1966", {"start": v(-73.4, -184.9) * mm, "end": v(-74.6, -189.48) * mm});
            skLineSegment(sketch, "E1967", {"start": v(-74.6, -189.48) * mm, "end": v(-75.8, -194.06) * mm});
            skLineSegment(sketch, "E1968", {"start": v(-107.93, -182.8) * mm, "end": v(-105.71, -182.68) * mm});
            skLineSegment(sketch, "E1969", {"start": v(-105.71, -182.68) * mm, "end": v(-103.66, -182.26) * mm});
            skLineSegment(sketch, "E1970", {"start": v(-103.66, -182.26) * mm, "end": v(-101.76, -181.58) * mm});
            skLineSegment(sketch, "E1971", {"start": v(-101.76, -181.58) * mm, "end": v(-100, -180.65) * mm});
            skLineSegment(sketch, "E1972", {"start": v(-100, -180.65) * mm, "end": v(-98.4, -179.49) * mm});
            skLineSegment(sketch, "E1973", {"start": v(-98.4, -179.49) * mm, "end": v(-96.94, -178.1) * mm});
            skLineSegment(sketch, "E1974", {"start": v(-96.94, -178.1) * mm, "end": v(-95.62, -176.53) * mm});
            skLineSegment(sketch, "E1975", {"start": v(-95.62, -176.53) * mm, "end": v(-94.42, -174.76) * mm});
            skLineSegment(sketch, "E1976", {"start": v(-94.42, -174.76) * mm, "end": v(-92.81, -172.1) * mm});
            skLineSegment(sketch, "E1977", {"start": v(-92.81, -172.1) * mm, "end": v(-91.24, -169.4) * mm});
            skLineSegment(sketch, "E1978", {"start": v(-91.24, -169.4) * mm, "end": v(-89.69, -166.7) * mm});
            skLineSegment(sketch, "E1979", {"start": v(-89.69, -166.7) * mm, "end": v(-88.15, -163.98) * mm});
            skLineSegment(sketch, "E1980", {"start": v(-88.15, -163.98) * mm, "end": v(-86.61, -161.26) * mm});
            skLineSegment(sketch, "E1981", {"start": v(-86.61, -161.26) * mm, "end": v(-85.07, -158.55) * mm});
            skLineSegment(sketch, "E1982", {"start": v(-85.07, -158.55) * mm, "end": v(-83.51, -155.85) * mm});
            skLineSegment(sketch, "E1983", {"start": v(-83.51, -155.85) * mm, "end": v(-81.92, -153.16) * mm});
            skLineSegment(sketch, "E1984", {"start": v(-81.92, -153.16) * mm, "end": v(-81.38, -152.11) * mm});
            skLineSegment(sketch, "E1985", {"start": v(-81.38, -152.11) * mm, "end": v(-81.1, -151.2) * mm});
            skLineSegment(sketch, "E1986", {"start": v(-81.1, -151.2) * mm, "end": v(-81.06, -150.39) * mm});
            skLineSegment(sketch, "E1987", {"start": v(-81.06, -150.39) * mm, "end": v(-81.23, -149.67) * mm});
            skLineSegment(sketch, "E1988", {"start": v(-81.23, -149.67) * mm, "end": v(-81.62, -149.02) * mm});
            skLineSegment(sketch, "E1989", {"start": v(-81.62, -149.02) * mm, "end": v(-82.19, -148.42) * mm});
            skLineSegment(sketch, "E1990", {"start": v(-82.19, -148.42) * mm, "end": v(-82.93, -147.84) * mm});
            skLineSegment(sketch, "E1991", {"start": v(-82.93, -147.84) * mm, "end": v(-83.82, -147.27) * mm});
            skLineSegment(sketch, "E1992", {"start": v(-83.82, -147.27) * mm, "end": v(-84.81, -146.76) * mm});
            skLineSegment(sketch, "E1993", {"start": v(-84.81, -146.76) * mm, "end": v(-85.68, -146.5) * mm});
            skLineSegment(sketch, "E1994", {"start": v(-85.68, -146.5) * mm, "end": v(-86.43, -146.47) * mm});
            skLineSegment(sketch, "E1995", {"start": v(-86.43, -146.47) * mm, "end": v(-87.1, -146.65) * mm});
            skLineSegment(sketch, "E1996", {"start": v(-87.1, -146.65) * mm, "end": v(-87.68, -147.02) * mm});
            skLineSegment(sketch, "E1997", {"start": v(-87.68, -147.02) * mm, "end": v(-88.23, -147.58) * mm});
            skLineSegment(sketch, "E1998", {"start": v(-88.23, -147.58) * mm, "end": v(-88.74, -148.29) * mm});
            skLineSegment(sketch, "E1999", {"start": v(-88.74, -148.29) * mm, "end": v(-89.24, -149.15) * mm});
            skLineSegment(sketch, "E2000", {"start": v(-89.24, -149.15) * mm, "end": v(-90.64, -151.72) * mm});
            skLineSegment(sketch, "E2001", {"start": v(-90.64, -151.72) * mm, "end": v(-92.05, -154.3) * mm});
            skLineSegment(sketch, "E2002", {"start": v(-92.05, -154.3) * mm, "end": v(-93.47, -156.86) * mm});
            skLineSegment(sketch, "E2003", {"start": v(-93.47, -156.86) * mm, "end": v(-94.9, -159.43) * mm});
            skLineSegment(sketch, "E2004", {"start": v(-94.9, -159.43) * mm, "end": v(-96.35, -161.98) * mm});
            skLineSegment(sketch, "E2005", {"start": v(-96.35, -161.98) * mm, "end": v(-97.8, -164.52) * mm});
            skLineSegment(sketch, "E2006", {"start": v(-97.8, -164.52) * mm, "end": v(-99.28, -167.06) * mm});
            skLineSegment(sketch, "E2007", {"start": v(-99.28, -167.06) * mm, "end": v(-100.78, -169.58) * mm});
            skLineSegment(sketch, "E2008", {"start": v(-100.78, -169.58) * mm, "end": v(-102.19, -171.58) * mm});
            skLineSegment(sketch, "E2009", {"start": v(-102.19, -171.58) * mm, "end": v(-103.75, -173.18) * mm});
            skLineSegment(sketch, "E2010", {"start": v(-103.75, -173.18) * mm, "end": v(-105.45, -174.37) * mm});
            skLineSegment(sketch, "E2011", {"start": v(-105.45, -174.37) * mm, "end": v(-107.23, -175.16) * mm});
            skLineSegment(sketch, "E2012", {"start": v(-107.23, -175.16) * mm, "end": v(-109.08, -175.53) * mm});
            skLineSegment(sketch, "E2013", {"start": v(-109.08, -175.53) * mm, "end": v(-110.97, -175.48) * mm});
            skLineSegment(sketch, "E2014", {"start": v(-110.97, -175.48) * mm, "end": v(-112.85, -175.01) * mm});
            skLineSegment(sketch, "E2015", {"start": v(-112.85, -175.01) * mm, "end": v(-114.7, -174.11) * mm});
            skLineSegment(sketch, "E2016", {"start": v(-114.7, -174.11) * mm, "end": v(-116.25, -173.01) * mm});
            skLineSegment(sketch, "E2017", {"start": v(-116.25, -173.01) * mm, "end": v(-117.41, -171.8) * mm});
            skLineSegment(sketch, "E2018", {"start": v(-117.41, -171.8) * mm, "end": v(-118.2, -170.46) * mm});
            skLineSegment(sketch, "E2019", {"start": v(-118.2, -170.46) * mm, "end": v(-118.6, -168.96) * mm});
            skLineSegment(sketch, "E2020", {"start": v(-118.6, -168.96) * mm, "end": v(-118.64, -167.3) * mm});
            skLineSegment(sketch, "E2021", {"start": v(-118.64, -167.3) * mm, "end": v(-118.3, -165.45) * mm});
            skLineSegment(sketch, "E2022", {"start": v(-118.3, -165.45) * mm, "end": v(-117.56, -163.38) * mm});
            skLineSegment(sketch, "E2023", {"start": v(-117.56, -163.38) * mm, "end": v(-116.45, -161.1) * mm});
            skLineSegment(sketch, "E2024", {"start": v(-116.45, -161.1) * mm, "end": v(-115.06, -158.51) * mm});
            skLineSegment(sketch, "E2025", {"start": v(-115.06, -158.51) * mm, "end": v(-113.65, -155.93) * mm});
            skLineSegment(sketch, "E2026", {"start": v(-113.65, -155.93) * mm, "end": v(-112.24, -153.37) * mm});
            skLineSegment(sketch, "E2027", {"start": v(-112.24, -153.37) * mm, "end": v(-110.8, -150.8) * mm});
            skLineSegment(sketch, "E2028", {"start": v(-110.8, -150.8) * mm, "end": v(-109.36, -148.25) * mm});
            skLineSegment(sketch, "E2029", {"start": v(-109.36, -148.25) * mm, "end": v(-107.9, -145.7) * mm});
            skLineSegment(sketch, "E2030", {"start": v(-107.9, -145.7) * mm, "end": v(-106.43, -143.17) * mm});
            skLineSegment(sketch, "E2031", {"start": v(-106.43, -143.17) * mm, "end": v(-104.93, -140.65) * mm});
            skLineSegment(sketch, "E2032", {"start": v(-104.93, -140.65) * mm, "end": v(-104.36, -139.54) * mm});
            skLineSegment(sketch, "E2033", {"start": v(-104.36, -139.54) * mm, "end": v(-104.04, -138.57) * mm});
            skLineSegment(sketch, "E2034", {"start": v(-104.04, -138.57) * mm, "end": v(-103.97, -137.7) * mm});
            skLineSegment(sketch, "E2035", {"start": v(-103.97, -137.7) * mm, "end": v(-104.14, -136.94) * mm});
            skLineSegment(sketch, "E2036", {"start": v(-104.14, -136.94) * mm, "end": v(-104.52, -136.24) * mm});
            skLineSegment(sketch, "E2037", {"start": v(-104.52, -136.24) * mm, "end": v(-105.11, -135.59) * mm});
            skLineSegment(sketch, "E2038", {"start": v(-105.11, -135.59) * mm, "end": v(-105.9, -134.96) * mm});
            skLineSegment(sketch, "E2039", {"start": v(-105.9, -134.96) * mm, "end": v(-106.87, -134.35) * mm});
            skLineSegment(sketch, "E2040", {"start": v(-106.87, -134.35) * mm, "end": v(-107.87, -133.83) * mm});
            skLineSegment(sketch, "E2041", {"start": v(-107.87, -133.83) * mm, "end": v(-108.76, -133.5) * mm});
            skLineSegment(sketch, "E2042", {"start": v(-108.76, -133.5) * mm, "end": v(-109.57, -133.39) * mm});
            skLineSegment(sketch, "E2043", {"start": v(-109.57, -133.39) * mm, "end": v(-110.3, -133.48) * mm});
            skLineSegment(sketch, "E2044", {"start": v(-110.3, -133.48) * mm, "end": v(-110.97, -133.78) * mm});
            skLineSegment(sketch, "E2045", {"start": v(-110.97, -133.78) * mm, "end": v(-111.6, -134.3) * mm});
            skLineSegment(sketch, "E2046", {"start": v(-111.6, -134.3) * mm, "end": v(-112.2, -135.04) * mm});
            skLineSegment(sketch, "E2047", {"start": v(-112.2, -135.04) * mm, "end": v(-112.78, -136) * mm});
            skLineSegment(sketch, "E2048", {"start": v(-112.78, -136) * mm, "end": v(-114.18, -138.58) * mm});
            skLineSegment(sketch, "E2049", {"start": v(-114.18, -138.58) * mm, "end": v(-115.6, -141.15) * mm});
            skLineSegment(sketch, "E2050", {"start": v(-115.6, -141.15) * mm, "end": v(-117.05, -143.7) * mm});
            skLineSegment(sketch, "E2051", {"start": v(-117.05, -143.7) * mm, "end": v(-118.5, -146.25) * mm});
            skLineSegment(sketch, "E2052", {"start": v(-118.5, -146.25) * mm, "end": v(-119.95, -148.8) * mm});
            skLineSegment(sketch, "E2053", {"start": v(-119.95, -148.8) * mm, "end": v(-121.4, -151.35) * mm});
            skLineSegment(sketch, "E2054", {"start": v(-121.4, -151.35) * mm, "end": v(-122.84, -153.9) * mm});
            skLineSegment(sketch, "E2055", {"start": v(-122.84, -153.9) * mm, "end": v(-124.26, -156.47) * mm});
            skLineSegment(sketch, "E2056", {"start": v(-124.26, -156.47) * mm, "end": v(-126.2, -161.3) * mm});
            skLineSegment(sketch, "E2057", {"start": v(-126.2, -161.3) * mm, "end": v(-126.8, -166.04) * mm});
            skLineSegment(sketch, "E2058", {"start": v(-126.8, -166.04) * mm, "end": v(-126.14, -170.5) * mm});
            skLineSegment(sketch, "E2059", {"start": v(-126.14, -170.5) * mm, "end": v(-124.35, -174.52) * mm});
            skLineSegment(sketch, "E2060", {"start": v(-124.35, -174.52) * mm, "end": v(-121.53, -177.93) * mm});
            skLineSegment(sketch, "E2061", {"start": v(-121.53, -177.93) * mm, "end": v(-117.78, -180.56) * mm});
            skLineSegment(sketch, "E2062", {"start": v(-117.78, -180.56) * mm, "end": v(-113.21, -182.24) * mm});
            skLineSegment(sketch, "E2063", {"start": v(-113.21, -182.24) * mm, "end": v(-107.93, -182.8) * mm});
            skLineSegment(sketch, "E2064", {"start": v(52.3, -162.08) * mm, "end": v(53.88, -166.75) * mm});
            skLineSegment(sketch, "E2065", {"start": v(53.88, -166.75) * mm, "end": v(55.44, -171.41) * mm});
            skLineSegment(sketch, "E2066", {"start": v(55.44, -171.41) * mm, "end": v(57.01, -176.08) * mm});
            skLineSegment(sketch, "E2067", {"start": v(57.01, -176.08) * mm, "end": v(58.58, -180.74) * mm});
            skLineSegment(sketch, "E2068", {"start": v(58.58, -180.74) * mm, "end": v(60.16, -185.4) * mm});
            skLineSegment(sketch, "E2069", {"start": v(60.16, -185.4) * mm, "end": v(61.73, -190.07) * mm});
            skLineSegment(sketch, "E2070", {"start": v(61.73, -190.07) * mm, "end": v(63.3, -194.73) * mm});
            skLineSegment(sketch, "E2071", {"start": v(63.3, -194.73) * mm, "end": v(64.9, -199.4) * mm});
            skLineSegment(sketch, "E2072", {"start": v(64.9, -199.4) * mm, "end": v(65.17, -200) * mm});
            skLineSegment(sketch, "E2073", {"start": v(65.17, -200) * mm, "end": v(65.52, -200.45) * mm});
            skLineSegment(sketch, "E2074", {"start": v(65.52, -200.45) * mm, "end": v(65.94, -200.75) * mm});
            skLineSegment(sketch, "E2075", {"start": v(65.94, -200.75) * mm, "end": v(66.41, -200.93) * mm});
            skLineSegment(sketch, "E2076", {"start": v(66.41, -200.93) * mm, "end": v(66.93, -201) * mm});
            skLineSegment(sketch, "E2077", {"start": v(66.93, -201) * mm, "end": v(67.47, -200.97) * mm});
            skLineSegment(sketch, "E2078", {"start": v(67.47, -200.97) * mm, "end": v(68.04, -200.87) * mm});
            skLineSegment(sketch, "E2079", {"start": v(68.04, -200.87) * mm, "end": v(68.63, -200.7) * mm});
            skLineSegment(sketch, "E2080", {"start": v(68.63, -200.7) * mm, "end": v(70.87, -199.96) * mm});
            skLineSegment(sketch, "E2081", {"start": v(70.87, -199.96) * mm, "end": v(73.12, -199.21) * mm});
            skLineSegment(sketch, "E2082", {"start": v(73.12, -199.21) * mm, "end": v(75.37, -198.46) * mm});
            skLineSegment(sketch, "E2083", {"start": v(75.37, -198.46) * mm, "end": v(77.61, -197.71) * mm});
            skLineSegment(sketch, "E2084", {"start": v(77.61, -197.71) * mm, "end": v(79.86, -196.97) * mm});
            skLineSegment(sketch, "E2085", {"start": v(79.86, -196.97) * mm, "end": v(82.1, -196.22) * mm});
            skLineSegment(sketch, "E2086", {"start": v(82.1, -196.22) * mm, "end": v(84.36, -195.48) * mm});
            skLineSegment(sketch, "E2087", {"start": v(84.36, -195.48) * mm, "end": v(86.6, -194.75) * mm});
            skLineSegment(sketch, "E2088", {"start": v(86.6, -194.75) * mm, "end": v(87.27, -194.5) * mm});
            skLineSegment(sketch, "E2089", {"start": v(87.27, -194.5) * mm, "end": v(87.84, -194.19) * mm});
            skLineSegment(sketch, "E2090", {"start": v(87.84, -194.19) * mm, "end": v(88.3, -193.83) * mm});
            skLineSegment(sketch, "E2091", {"start": v(88.3, -193.83) * mm, "end": v(88.64, -193.4) * mm});
            skLineSegment(sketch, "E2092", {"start": v(88.64, -193.4) * mm, "end": v(88.86, -192.92) * mm});
            skLineSegment(sketch, "E2093", {"start": v(88.86, -192.92) * mm, "end": v(88.96, -192.36) * mm});
            skLineSegment(sketch, "E2094", {"start": v(88.96, -192.36) * mm, "end": v(88.93, -191.73) * mm});
            skLineSegment(sketch, "E2095", {"start": v(88.93, -191.73) * mm, "end": v(88.76, -191.02) * mm});
            skLineSegment(sketch, "E2096", {"start": v(88.76, -191.02) * mm, "end": v(88.47, -190.29) * mm});
            skLineSegment(sketch, "E2097", {"start": v(88.47, -190.29) * mm, "end": v(88.11, -189.68) * mm});
            skLineSegment(sketch, "E2098", {"start": v(88.11, -189.68) * mm, "end": v(87.7, -189.21) * mm});
            skLineSegment(sketch, "E2099", {"start": v(87.7, -189.21) * mm, "end": v(87.2, -188.87) * mm});
            skLineSegment(sketch, "E2100", {"start": v(87.2, -188.87) * mm, "end": v(86.64, -188.67) * mm});
            skLineSegment(sketch, "E2101", {"start": v(86.64, -188.67) * mm, "end": v(86, -188.6) * mm});
            skLineSegment(sketch, "E2102", {"start": v(86, -188.6) * mm, "end": v(85.3, -188.66) * mm});
            skLineSegment(sketch, "E2103", {"start": v(85.3, -188.66) * mm, "end": v(84.52, -188.86) * mm});
            skLineSegment(sketch, "E2104", {"start": v(84.52, -188.86) * mm, "end": v(83.4, -189.23) * mm});
            skLineSegment(sketch, "E2105", {"start": v(83.4, -189.23) * mm, "end": v(82.27, -189.6) * mm});
            skLineSegment(sketch, "E2106", {"start": v(82.27, -189.6) * mm, "end": v(81.14, -189.96) * mm});
            skLineSegment(sketch, "E2107", {"start": v(81.14, -189.96) * mm, "end": v(80.02, -190.32) * mm});
            skLineSegment(sketch, "E2108", {"start": v(80.02, -190.32) * mm, "end": v(78.89, -190.68) * mm});
            skLineSegment(sketch, "E2109", {"start": v(78.89, -190.68) * mm, "end": v(77.76, -191.03) * mm});
            skLineSegment(sketch, "E2110", {"start": v(77.76, -191.03) * mm, "end": v(76.63, -191.39) * mm});
            skLineSegment(sketch, "E2111", {"start": v(76.63, -191.39) * mm, "end": v(75.5, -191.75) * mm});
            skLineSegment(sketch, "E2112", {"start": v(75.5, -191.75) * mm, "end": v(74.94, -191.9) * mm});
            skLineSegment(sketch, "E2113", {"start": v(74.94, -191.9) * mm, "end": v(74.4, -192) * mm});
            skLineSegment(sketch, "E2114", {"start": v(74.4, -192) * mm, "end": v(73.89, -192.03) * mm});
            skLineSegment(sketch, "E2115", {"start": v(73.89, -192.03) * mm, "end": v(73.4, -191.98) * mm});
            skLineSegment(sketch, "E2116", {"start": v(73.4, -191.98) * mm, "end": v(72.92, -191.83) * mm});
            skLineSegment(sketch, "E2117", {"start": v(72.92, -191.83) * mm, "end": v(72.46, -191.57) * mm});
            skLineSegment(sketch, "E2118", {"start": v(72.46, -191.57) * mm, "end": v(72.02, -191.2) * mm});
            skLineSegment(sketch, "E2119", {"start": v(72.02, -191.2) * mm, "end": v(71.6, -190.68) * mm});
            skLineSegment(sketch, "E2120", {"start": v(71.6, -190.68) * mm, "end": v(70.12, -188.34) * mm});
            skLineSegment(sketch, "E2121", {"start": v(70.12, -188.34) * mm, "end": v(69.2, -186.2) * mm});
            skLineSegment(sketch, "E2122", {"start": v(69.2, -186.2) * mm, "end": v(68.84, -184.24) * mm});
            skLineSegment(sketch, "E2123", {"start": v(68.84, -184.24) * mm, "end": v(69.06, -182.47) * mm});
            skLineSegment(sketch, "E2124", {"start": v(69.06, -182.47) * mm, "end": v(69.84, -180.9) * mm});
            skLineSegment(sketch, "E2125", {"start": v(69.84, -180.9) * mm, "end": v(71.19, -179.5) * mm});
            skLineSegment(sketch, "E2126", {"start": v(71.19, -179.5) * mm, "end": v(73.11, -178.27) * mm});
            skLineSegment(sketch, "E2127", {"start": v(73.11, -178.27) * mm, "end": v(75.61, -177.22) * mm});
            skLineSegment(sketch, "E2128", {"start": v(75.61, -177.22) * mm, "end": v(75.97, -177.1) * mm});
            skLineSegment(sketch, "E2129", {"start": v(75.97, -177.1) * mm, "end": v(76.32, -176.98) * mm});
            skLineSegment(sketch, "E2130", {"start": v(76.32, -176.98) * mm, "end": v(76.67, -176.86) * mm});
            skLineSegment(sketch, "E2131", {"start": v(76.67, -176.86) * mm, "end": v(77.03, -176.74) * mm});
            skLineSegment(sketch, "E2132", {"start": v(77.03, -176.74) * mm, "end": v(77.38, -176.61) * mm});
            skLineSegment(sketch, "E2133", {"start": v(77.38, -176.61) * mm, "end": v(77.73, -176.49) * mm});
            skLineSegment(sketch, "E2134", {"start": v(77.73, -176.49) * mm, "end": v(78.08, -176.36) * mm});
            skLineSegment(sketch, "E2135", {"start": v(78.08, -176.36) * mm, "end": v(78.43, -176.22) * mm});
            skLineSegment(sketch, "E2136", {"start": v(78.43, -176.22) * mm, "end": v(79, -175.95) * mm});
            skLineSegment(sketch, "E2137", {"start": v(79, -175.95) * mm, "end": v(79.47, -175.63) * mm});
            skLineSegment(sketch, "E2138", {"start": v(79.47, -175.63) * mm, "end": v(79.82, -175.26) * mm});
            skLineSegment(sketch, "E2139", {"start": v(79.82, -175.26) * mm, "end": v(80.06, -174.84) * mm});
            skLineSegment(sketch, "E2140", {"start": v(80.06, -174.84) * mm, "end": v(80.2, -174.36) * mm});
            skLineSegment(sketch, "E2141", {"start": v(80.2, -174.36) * mm, "end": v(80.25, -173.84) * mm});
            skLineSegment(sketch, "E2142", {"start": v(80.25, -173.84) * mm, "end": v(80.2, -173.26) * mm});
            skLineSegment(sketch, "E2143", {"start": v(80.2, -173.26) * mm, "end": v(80.06, -172.63) * mm});
            skLineSegment(sketch, "E2144", {"start": v(80.06, -172.63) * mm, "end": v(79.82, -171.94) * mm});
            skLineSegment(sketch, "E2145", {"start": v(79.82, -171.94) * mm, "end": v(79.53, -171.36) * mm});
            skLineSegment(sketch, "E2146", {"start": v(79.53, -171.36) * mm, "end": v(79.17, -170.9) * mm});
            skLineSegment(sketch, "E2147", {"start": v(79.17, -170.9) * mm, "end": v(78.76, -170.55) * mm});
            skLineSegment(sketch, "E2148", {"start": v(78.76, -170.55) * mm, "end": v(78.27, -170.32) * mm});
            skLineSegment(sketch, "E2149", {"start": v(78.27, -170.32) * mm, "end": v(77.72, -170.2) * mm});
            skLineSegment(sketch, "E2150", {"start": v(77.72, -170.2) * mm, "end": v(77.1, -170.23) * mm});
            skLineSegment(sketch, "E2151", {"start": v(77.1, -170.23) * mm, "end": v(76.39, -170.38) * mm});
            skLineSegment(sketch, "E2152", {"start": v(76.39, -170.38) * mm, "end": v(75.55, -170.62) * mm});
            skLineSegment(sketch, "E2153", {"start": v(75.55, -170.62) * mm, "end": v(74.72, -170.88) * mm});
            skLineSegment(sketch, "E2154", {"start": v(74.72, -170.88) * mm, "end": v(73.89, -171.14) * mm});
            skLineSegment(sketch, "E2155", {"start": v(73.89, -171.14) * mm, "end": v(73.06, -171.4) * mm});
            skLineSegment(sketch, "E2156", {"start": v(73.06, -171.4) * mm, "end": v(72.23, -171.67) * mm});
            skLineSegment(sketch, "E2157", {"start": v(72.23, -171.67) * mm, "end": v(71.4, -171.94) * mm});
            skLineSegment(sketch, "E2158", {"start": v(71.4, -171.94) * mm, "end": v(70.57, -172.2) * mm});
            skLineSegment(sketch, "E2159", {"start": v(70.57, -172.2) * mm, "end": v(69.73, -172.46) * mm});
            skLineSegment(sketch, "E2160", {"start": v(69.73, -172.46) * mm, "end": v(69.2, -172.63) * mm});
            skLineSegment(sketch, "E2161", {"start": v(69.2, -172.63) * mm, "end": v(68.68, -172.8) * mm});
            skLineSegment(sketch, "E2162", {"start": v(68.68, -172.8) * mm, "end": v(68.16, -172.93) * mm});
            skLineSegment(sketch, "E2163", {"start": v(68.16, -172.93) * mm, "end": v(67.64, -173) * mm});
            skLineSegment(sketch, "E2164", {"start": v(67.64, -173) * mm, "end": v(67.12, -173) * mm});
            skLineSegment(sketch, "E2165", {"start": v(67.12, -173) * mm, "end": v(66.6, -172.87) * mm});
            skLineSegment(sketch, "E2166", {"start": v(66.6, -172.87) * mm, "end": v(66.09, -172.61) * mm});
            skLineSegment(sketch, "E2167", {"start": v(66.09, -172.61) * mm, "end": v(65.58, -172.19) * mm});
            skLineSegment(sketch, "E2168", {"start": v(65.58, -172.19) * mm, "end": v(64.3, -170.6) * mm});
            skLineSegment(sketch, "E2169", {"start": v(64.3, -170.6) * mm, "end": v(63.5, -168.96) * mm});
            skLineSegment(sketch, "E2170", {"start": v(63.5, -168.96) * mm, "end": v(63.16, -167.33) * mm});
            skLineSegment(sketch, "E2171", {"start": v(63.16, -167.33) * mm, "end": v(63.3, -165.74) * mm});
            skLineSegment(sketch, "E2172", {"start": v(63.3, -165.74) * mm, "end": v(63.87, -164.26) * mm});
            skLineSegment(sketch, "E2173", {"start": v(63.87, -164.26) * mm, "end": v(64.9, -162.93) * mm});
            skLineSegment(sketch, "E2174", {"start": v(64.9, -162.93) * mm, "end": v(66.33, -161.82) * mm});
            skLineSegment(sketch, "E2175", {"start": v(66.33, -161.82) * mm, "end": v(68.2, -160.97) * mm});
            skLineSegment(sketch, "E2176", {"start": v(68.2, -160.97) * mm, "end": v(68.78, -160.77) * mm});
            skLineSegment(sketch, "E2177", {"start": v(68.78, -160.77) * mm, "end": v(69.37, -160.58) * mm});
            skLineSegment(sketch, "E2178", {"start": v(69.37, -160.58) * mm, "end": v(69.97, -160.38) * mm});
            skLineSegment(sketch, "E2179", {"start": v(69.97, -160.38) * mm, "end": v(70.56, -160.2) * mm});
            skLineSegment(sketch, "E2180", {"start": v(70.56, -160.2) * mm, "end": v(71.15, -160) * mm});
            skLineSegment(sketch, "E2181", {"start": v(71.15, -160) * mm, "end": v(71.74, -159.8) * mm});
            skLineSegment(sketch, "E2182", {"start": v(71.74, -159.8) * mm, "end": v(72.34, -159.6) * mm});
            skLineSegment(sketch, "E2183", {"start": v(72.34, -159.6) * mm, "end": v(72.92, -159.4) * mm});
            skLineSegment(sketch, "E2184", {"start": v(72.92, -159.4) * mm, "end": v(73.56, -159.15) * mm});
            skLineSegment(sketch, "E2185", {"start": v(73.56, -159.15) * mm, "end": v(74.1, -158.85) * mm});
            skLineSegment(sketch, "E2186", {"start": v(74.1, -158.85) * mm, "end": v(74.54, -158.5) * mm});
            skLineSegment(sketch, "E2187", {"start": v(74.54, -158.5) * mm, "end": v(74.87, -158.07) * mm});
            skLineSegment(sketch, "E2188", {"start": v(74.87, -158.07) * mm, "end": v(75.1, -157.58) * mm});
            skLineSegment(sketch, "E2189", {"start": v(75.1, -157.58) * mm, "end": v(75.2, -157.02) * mm});
            skLineSegment(sketch, "E2190", {"start": v(75.2, -157.02) * mm, "end": v(75.17, -156.37) * mm});
            skLineSegment(sketch, "E2191", {"start": v(75.17, -156.37) * mm, "end": v(75.01, -155.62) * mm});
            skLineSegment(sketch, "E2192", {"start": v(75.01, -155.62) * mm, "end": v(74.73, -154.83) * mm});
            skLineSegment(sketch, "E2193", {"start": v(74.73, -154.83) * mm, "end": v(74.37, -154.2) * mm});
            skLineSegment(sketch, "E2194", {"start": v(74.37, -154.2) * mm, "end": v(73.94, -153.73) * mm});
            skLineSegment(sketch, "E2195", {"start": v(73.94, -153.73) * mm, "end": v(73.45, -153.41) * mm});
            skLineSegment(sketch, "E2196", {"start": v(73.45, -153.41) * mm, "end": v(72.9, -153.23) * mm});
            skLineSegment(sketch, "E2197", {"start": v(72.9, -153.23) * mm, "end": v(72.27, -153.2) * mm});
            skLineSegment(sketch, "E2198", {"start": v(72.27, -153.2) * mm, "end": v(71.6, -153.27) * mm});
            skLineSegment(sketch, "E2199", {"start": v(71.6, -153.27) * mm, "end": v(70.85, -153.47) * mm});
            skLineSegment(sketch, "E2200", {"start": v(70.85, -153.47) * mm, "end": v(68.84, -154.13) * mm});
            skLineSegment(sketch, "E2201", {"start": v(68.84, -154.13) * mm, "end": v(66.83, -154.8) * mm});
            skLineSegment(sketch, "E2202", {"start": v(66.83, -154.8) * mm, "end": v(64.82, -155.46) * mm});
            skLineSegment(sketch, "E2203", {"start": v(64.82, -155.46) * mm, "end": v(62.81, -156.13) * mm});
            skLineSegment(sketch, "E2204", {"start": v(62.81, -156.13) * mm, "end": v(60.8, -156.8) * mm});
            skLineSegment(sketch, "E2205", {"start": v(60.8, -156.8) * mm, "end": v(58.8, -157.48) * mm});
            skLineSegment(sketch, "E2206", {"start": v(58.8, -157.48) * mm, "end": v(56.79, -158.16) * mm});
            skLineSegment(sketch, "E2207", {"start": v(56.79, -158.16) * mm, "end": v(54.78, -158.84) * mm});
            skLineSegment(sketch, "E2208", {"start": v(54.78, -158.84) * mm, "end": v(54.23, -159.04) * mm});
            skLineSegment(sketch, "E2209", {"start": v(54.23, -159.04) * mm, "end": v(53.7, -159.28) * mm});
            skLineSegment(sketch, "E2210", {"start": v(53.7, -159.28) * mm, "end": v(53.24, -159.55) * mm});
            skLineSegment(sketch, "E2211", {"start": v(53.24, -159.55) * mm, "end": v(52.85, -159.9) * mm});
            skLineSegment(sketch, "E2212", {"start": v(52.85, -159.9) * mm, "end": v(52.54, -160.3) * mm});
            skLineSegment(sketch, "E2213", {"start": v(52.54, -160.3) * mm, "end": v(52.34, -160.8) * mm});
            skLineSegment(sketch, "E2214", {"start": v(52.34, -160.8) * mm, "end": v(52.25, -161.38) * mm});
            skLineSegment(sketch, "E2215", {"start": v(52.25, -161.38) * mm, "end": v(52.3, -162.08) * mm});
            skLineSegment(sketch, "E2216", {"start": v(-84.26, 107.75) * mm, "end": v(-63.1, 107.75) * mm});
            skLineSegment(sketch, "E2217", {"start": v(-63.1, 107.75) * mm, "end": v(-41.96, 107.75) * mm});
            skLineSegment(sketch, "E2218", {"start": v(-41.96, 107.75) * mm, "end": v(-20.86, 107.75) * mm});
            skLineSegment(sketch, "E2219", {"start": v(-20.86, 107.75) * mm, "end": v(0.22, 107.75) * mm});
            skLineSegment(sketch, "E2220", {"start": v(0.22, 107.75) * mm, "end": v(21.3, 107.75) * mm});
            skLineSegment(sketch, "E2221", {"start": v(21.3, 107.75) * mm, "end": v(42.37, 107.75) * mm});
            skLineSegment(sketch, "E2222", {"start": v(42.37, 107.75) * mm, "end": v(63.45, 107.75) * mm});
            skLineSegment(sketch, "E2223", {"start": v(63.45, 107.75) * mm, "end": v(84.57, 107.75) * mm});
            skLineSegment(sketch, "E2224", {"start": v(84.57, 107.75) * mm, "end": v(83.81, 108.7) * mm});
            skLineSegment(sketch, "E2225", {"start": v(83.81, 108.7) * mm, "end": v(83.01, 109.44) * mm});
            skLineSegment(sketch, "E2226", {"start": v(83.01, 109.44) * mm, "end": v(82.18, 109.98) * mm});
            skLineSegment(sketch, "E2227", {"start": v(82.18, 109.98) * mm, "end": v(81.31, 110.36) * mm});
            skLineSegment(sketch, "E2228", {"start": v(81.31, 110.36) * mm, "end": v(80.41, 110.6) * mm});
            skLineSegment(sketch, "E2229", {"start": v(80.41, 110.6) * mm, "end": v(79.5, 110.74) * mm});
            skLineSegment(sketch, "E2230", {"start": v(79.5, 110.74) * mm, "end": v(78.56, 110.8) * mm});
            skLineSegment(sketch, "E2231", {"start": v(78.56, 110.8) * mm, "end": v(77.6, 110.81) * mm});
            skLineSegment(sketch, "E2232", {"start": v(77.6, 110.81) * mm, "end": v(58.24, 110.81) * mm});
            skLineSegment(sketch, "E2233", {"start": v(58.24, 110.81) * mm, "end": v(38.87, 110.81) * mm});
            skLineSegment(sketch, "E2234", {"start": v(38.87, 110.81) * mm, "end": v(19.5, 110.81) * mm});
            skLineSegment(sketch, "E2235", {"start": v(19.5, 110.81) * mm, "end": v(0.14, 110.81) * mm});
            skLineSegment(sketch, "E2236", {"start": v(0.14, 110.81) * mm, "end": v(-19.22, 110.81) * mm});
            skLineSegment(sketch, "E2237", {"start": v(-19.22, 110.81) * mm, "end": v(-38.6, 110.81) * mm});
            skLineSegment(sketch, "E2238", {"start": v(-38.6, 110.81) * mm, "end": v(-57.96, 110.81) * mm});
            skLineSegment(sketch, "E2239", {"start": v(-57.96, 110.81) * mm, "end": v(-77.32, 110.8) * mm});
            skLineSegment(sketch, "E2240", {"start": v(-77.32, 110.8) * mm, "end": v(-78.27, 110.8) * mm});
            skLineSegment(sketch, "E2241", {"start": v(-78.27, 110.8) * mm, "end": v(-79.2, 110.75) * mm});
            skLineSegment(sketch, "E2242", {"start": v(-79.2, 110.75) * mm, "end": v(-80.12, 110.62) * mm});
            skLineSegment(sketch, "E2243", {"start": v(-80.12, 110.62) * mm, "end": v(-81.02, 110.38) * mm});
            skLineSegment(sketch, "E2244", {"start": v(-81.02, 110.38) * mm, "end": v(-81.9, 110.01) * mm});
            skLineSegment(sketch, "E2245", {"start": v(-81.9, 110.01) * mm, "end": v(-82.73, 109.47) * mm});
            skLineSegment(sketch, "E2246", {"start": v(-82.73, 109.47) * mm, "end": v(-83.52, 108.73) * mm});
            skLineSegment(sketch, "E2247", {"start": v(-83.52, 108.73) * mm, "end": v(-84.26, 107.75) * mm});
            skLineSegment(sketch, "E2248", {"start": v(33.54, -203.44) * mm, "end": v(33.2, -200.65) * mm});
            skLineSegment(sketch, "E2249", {"start": v(33.2, -200.65) * mm, "end": v(32.87, -197.8) * mm});
            skLineSegment(sketch, "E2250", {"start": v(32.87, -197.8) * mm, "end": v(32.53, -194.89) * mm});
            skLineSegment(sketch, "E2251", {"start": v(32.53, -194.89) * mm, "end": v(32.18, -191.94) * mm});
            skLineSegment(sketch, "E2252", {"start": v(32.18, -191.94) * mm, "end": v(31.83, -188.95) * mm});
            skLineSegment(sketch, "E2253", {"start": v(31.83, -188.95) * mm, "end": v(31.49, -185.94) * mm});
            skLineSegment(sketch, "E2254", {"start": v(31.49, -185.94) * mm, "end": v(31.14, -182.91) * mm});
            skLineSegment(sketch, "E2255", {"start": v(31.14, -182.91) * mm, "end": v(30.8, -179.87) * mm});
            skLineSegment(sketch, "E2256", {"start": v(30.8, -179.87) * mm, "end": v(30.53, -177.3) * mm});
            skLineSegment(sketch, "E2257", {"start": v(30.53, -177.3) * mm, "end": v(30.43, -175.35) * mm});
            skLineSegment(sketch, "E2258", {"start": v(30.43, -175.35) * mm, "end": v(30.57, -173.9) * mm});
            skLineSegment(sketch, "E2259", {"start": v(30.57, -173.9) * mm, "end": v(31.04, -172.84) * mm});
            skLineSegment(sketch, "E2260", {"start": v(31.04, -172.84) * mm, "end": v(31.91, -172.05) * mm});
            skLineSegment(sketch, "E2261", {"start": v(31.91, -172.05) * mm, "end": v(33.27, -171.43) * mm});
            skLineSegment(sketch, "E2262", {"start": v(33.27, -171.43) * mm, "end": v(35.2, -170.86) * mm});
            skLineSegment(sketch, "E2263", {"start": v(35.2, -170.86) * mm, "end": v(37.78, -170.23) * mm});
            skLineSegment(sketch, "E2264", {"start": v(37.78, -170.23) * mm, "end": v(37.96, -170.18) * mm});
            skLineSegment(sketch, "E2265", {"start": v(37.96, -170.18) * mm, "end": v(38.15, -170.14) * mm});
            skLineSegment(sketch, "E2266", {"start": v(38.15, -170.14) * mm, "end": v(38.33, -170.1) * mm});
            skLineSegment(sketch, "E2267", {"start": v(38.33, -170.1) * mm, "end": v(38.5, -170.04) * mm});
            skLineSegment(sketch, "E2268", {"start": v(38.5, -170.04) * mm, "end": v(38.7, -170) * mm});
            skLineSegment(sketch, "E2269", {"start": v(38.7, -170) * mm, "end": v(38.87, -169.95) * mm});
            skLineSegment(sketch, "E2270", {"start": v(38.87, -169.95) * mm, "end": v(39.05, -169.9) * mm});
            skLineSegment(sketch, "E2271", {"start": v(39.05, -169.9) * mm, "end": v(39.23, -169.86) * mm});
            skLineSegment(sketch, "E2272", {"start": v(39.23, -169.86) * mm, "end": v(39.9, -169.64) * mm});
            skLineSegment(sketch, "E2273", {"start": v(39.9, -169.64) * mm, "end": v(40.48, -169.35) * mm});
            skLineSegment(sketch, "E2274", {"start": v(40.48, -169.35) * mm, "end": v(40.94, -168.98) * mm});
            skLineSegment(sketch, "E2275", {"start": v(40.94, -168.98) * mm, "end": v(41.3, -168.55) * mm});
            skLineSegment(sketch, "E2276", {"start": v(41.3, -168.55) * mm, "end": v(41.56, -168.05) * mm});
            skLineSegment(sketch, "E2277", {"start": v(41.56, -168.05) * mm, "end": v(41.72, -167.48) * mm});
            skLineSegment(sketch, "E2278", {"start": v(41.72, -167.48) * mm, "end": v(41.8, -166.85) * mm});
            skLineSegment(sketch, "E2279", {"start": v(41.8, -166.85) * mm, "end": v(41.77, -166.15) * mm});
            skLineSegment(sketch, "E2280", {"start": v(41.77, -166.15) * mm, "end": v(41.61, -165.36) * mm});
            skLineSegment(sketch, "E2281", {"start": v(41.61, -165.36) * mm, "end": v(41.34, -164.78) * mm});
            skLineSegment(sketch, "E2282", {"start": v(41.34, -164.78) * mm, "end": v(40.96, -164.37) * mm});
            skLineSegment(sketch, "E2283", {"start": v(40.96, -164.37) * mm, "end": v(40.5, -164.1) * mm});
            skLineSegment(sketch, "E2284", {"start": v(40.5, -164.1) * mm, "end": v(39.97, -163.97) * mm});
            skLineSegment(sketch, "E2285", {"start": v(39.97, -163.97) * mm, "end": v(39.38, -163.93) * mm});
            skLineSegment(sketch, "E2286", {"start": v(39.38, -163.93) * mm, "end": v(38.75, -163.96) * mm});
            skLineSegment(sketch, "E2287", {"start": v(38.75, -163.96) * mm, "end": v(38.09, -164.03) * mm});
            skLineSegment(sketch, "E2288", {"start": v(38.09, -164.03) * mm, "end": v(34.68, -164.44) * mm});
            skLineSegment(sketch, "E2289", {"start": v(34.68, -164.44) * mm, "end": v(31.27, -164.85) * mm});
            skLineSegment(sketch, "E2290", {"start": v(31.27, -164.85) * mm, "end": v(27.86, -165.26) * mm});
            skLineSegment(sketch, "E2291", {"start": v(27.86, -165.26) * mm, "end": v(24.46, -165.67) * mm});
            skLineSegment(sketch, "E2292", {"start": v(24.46, -165.67) * mm, "end": v(21.05, -166.07) * mm});
            skLineSegment(sketch, "E2293", {"start": v(21.05, -166.07) * mm, "end": v(17.64, -166.48) * mm});
            skLineSegment(sketch, "E2294", {"start": v(17.64, -166.48) * mm, "end": v(14.23, -166.88) * mm});
            skLineSegment(sketch, "E2295", {"start": v(14.23, -166.88) * mm, "end": v(10.82, -167.29) * mm});
            skLineSegment(sketch, "E2296", {"start": v(10.82, -167.29) * mm, "end": v(10.14, -167.4) * mm});
            skLineSegment(sketch, "E2297", {"start": v(10.14, -167.4) * mm, "end": v(9.52, -167.56) * mm});
            skLineSegment(sketch, "E2298", {"start": v(9.52, -167.56) * mm, "end": v(8.96, -167.79) * mm});
            skLineSegment(sketch, "E2299", {"start": v(8.96, -167.79) * mm, "end": v(8.5, -168.1) * mm});
            skLineSegment(sketch, "E2300", {"start": v(8.5, -168.1) * mm, "end": v(8.12, -168.5) * mm});
            skLineSegment(sketch, "E2301", {"start": v(8.12, -168.5) * mm, "end": v(7.85, -169) * mm});
            skLineSegment(sketch, "E2302", {"start": v(7.85, -169) * mm, "end": v(7.7, -169.62) * mm});
            skLineSegment(sketch, "E2303", {"start": v(7.7, -169.62) * mm, "end": v(7.7, -170.36) * mm});
            skLineSegment(sketch, "E2304", {"start": v(7.7, -170.36) * mm, "end": v(7.81, -171.12) * mm});
            skLineSegment(sketch, "E2305", {"start": v(7.81, -171.12) * mm, "end": v(8.03, -171.79) * mm});
            skLineSegment(sketch, "E2306", {"start": v(8.03, -171.79) * mm, "end": v(8.35, -172.35) * mm});
            skLineSegment(sketch, "E2307", {"start": v(8.35, -172.35) * mm, "end": v(8.77, -172.8) * mm});
            skLineSegment(sketch, "E2308", {"start": v(8.77, -172.8) * mm, "end": v(9.28, -173.15) * mm});
            skLineSegment(sketch, "E2309", {"start": v(9.28, -173.15) * mm, "end": v(9.89, -173.38) * mm});
            skLineSegment(sketch, "E2310", {"start": v(9.89, -173.38) * mm, "end": v(10.59, -173.49) * mm});
            skLineSegment(sketch, "E2311", {"start": v(10.59, -173.49) * mm, "end": v(11.38, -173.48) * mm});
            skLineSegment(sketch, "E2312", {"start": v(11.38, -173.48) * mm, "end": v(11.81, -173.44) * mm});
            skLineSegment(sketch, "E2313", {"start": v(11.81, -173.44) * mm, "end": v(12.25, -173.39) * mm});
            skLineSegment(sketch, "E2314", {"start": v(12.25, -173.39) * mm, "end": v(12.68, -173.32) * mm});
            skLineSegment(sketch, "E2315", {"start": v(12.68, -173.32) * mm, "end": v(13.11, -173.26) * mm});
            skLineSegment(sketch, "E2316", {"start": v(13.11, -173.26) * mm, "end": v(13.54, -173.18) * mm});
            skLineSegment(sketch, "E2317", {"start": v(13.54, -173.18) * mm, "end": v(13.97, -173.1) * mm});
            skLineSegment(sketch, "E2318", {"start": v(13.97, -173.1) * mm, "end": v(14.4, -173.02) * mm});
            skLineSegment(sketch, "E2319", {"start": v(14.4, -173.02) * mm, "end": v(14.83, -172.93) * mm});
            skLineSegment(sketch, "E2320", {"start": v(14.83, -172.93) * mm, "end": v(16.36, -172.7) * mm});
            skLineSegment(sketch, "E2321", {"start": v(16.36, -172.7) * mm, "end": v(17.67, -172.72) * mm});
            skLineSegment(sketch, "E2322", {"start": v(17.67, -172.72) * mm, "end": v(18.78, -172.98) * mm});
            skLineSegment(sketch, "E2323", {"start": v(18.78, -172.98) * mm, "end": v(19.7, -173.5) * mm});
            skLineSegment(sketch, "E2324", {"start": v(19.7, -173.5) * mm, "end": v(20.42, -174.27) * mm});
            skLineSegment(sketch, "E2325", {"start": v(20.42, -174.27) * mm, "end": v(20.97, -175.31) * mm});
            skLineSegment(sketch, "E2326", {"start": v(20.97, -175.31) * mm, "end": v(21.35, -176.63) * mm});
            skLineSegment(sketch, "E2327", {"start": v(21.35, -176.63) * mm, "end": v(21.58, -178.23) * mm});
            skLineSegment(sketch, "E2328", {"start": v(21.58, -178.23) * mm, "end": v(21.89, -181.58) * mm});
            skLineSegment(sketch, "E2329", {"start": v(21.89, -181.58) * mm, "end": v(22.23, -184.94) * mm});
            skLineSegment(sketch, "E2330", {"start": v(22.23, -184.94) * mm, "end": v(22.6, -188.29) * mm});
            skLineSegment(sketch, "E2331", {"start": v(22.6, -188.29) * mm, "end": v(23, -191.63) * mm});
            skLineSegment(sketch, "E2332", {"start": v(23, -191.63) * mm, "end": v(23.43, -194.98) * mm});
            skLineSegment(sketch, "E2333", {"start": v(23.43, -194.98) * mm, "end": v(23.85, -198.32) * mm});
            skLineSegment(sketch, "E2334", {"start": v(23.85, -198.32) * mm, "end": v(24.28, -201.67) * mm});
            skLineSegment(sketch, "E2335", {"start": v(24.28, -201.67) * mm, "end": v(24.7, -205.01) * mm});
            skLineSegment(sketch, "E2336", {"start": v(24.7, -205.01) * mm, "end": v(24.86, -205.98) * mm});
            skLineSegment(sketch, "E2337", {"start": v(24.86, -205.98) * mm, "end": v(25.08, -206.9) * mm});
            skLineSegment(sketch, "E2338", {"start": v(25.08, -206.9) * mm, "end": v(25.4, -207.73) * mm});
            skLineSegment(sketch, "E2339", {"start": v(25.4, -207.73) * mm, "end": v(25.84, -208.44) * mm});
            skLineSegment(sketch, "E2340", {"start": v(25.84, -208.44) * mm, "end": v(26.43, -209) * mm});
            skLineSegment(sketch, "E2341", {"start": v(26.43, -209) * mm, "end": v(27.2, -209.38) * mm});
            skLineSegment(sketch, "E2342", {"start": v(27.2, -209.38) * mm, "end": v(28.16, -209.55) * mm});
            skLineSegment(sketch, "E2343", {"start": v(28.16, -209.55) * mm, "end": v(29.36, -209.47) * mm});
            skLineSegment(sketch, "E2344", {"start": v(29.36, -209.47) * mm, "end": v(30.45, -209.25) * mm});
            skLineSegment(sketch, "E2345", {"start": v(30.45, -209.25) * mm, "end": v(31.43, -208.93) * mm});
            skLineSegment(sketch, "E2346", {"start": v(31.43, -208.93) * mm, "end": v(32.26, -208.48) * mm});
            skLineSegment(sketch, "E2347", {"start": v(32.26, -208.48) * mm, "end": v(32.92, -207.87) * mm});
            skLineSegment(sketch, "E2348", {"start": v(32.92, -207.87) * mm, "end": v(33.4, -207.1) * mm});
            skLineSegment(sketch, "E2349", {"start": v(33.4, -207.1) * mm, "end": v(33.68, -206.11) * mm});
            skLineSegment(sketch, "E2350", {"start": v(33.68, -206.11) * mm, "end": v(33.73, -204.9) * mm});
            skLineSegment(sketch, "E2351", {"start": v(33.73, -204.9) * mm, "end": v(33.54, -203.44) * mm});
            skLineSegment(sketch, "E2352", {"start": v(-220.32, 108.45) * mm, "end": v(-219.4, 108.59) * mm});
            skLineSegment(sketch, "E2353", {"start": v(-219.4, 108.59) * mm, "end": v(-218.51, 108.83) * mm});
            skLineSegment(sketch, "E2354", {"start": v(-218.51, 108.83) * mm, "end": v(-217.65, 109.18) * mm});
            skLineSegment(sketch, "E2355", {"start": v(-217.65, 109.18) * mm, "end": v(-216.81, 109.6) * mm});
            skLineSegment(sketch, "E2356", {"start": v(-216.81, 109.6) * mm, "end": v(-216, 110.11) * mm});
            skLineSegment(sketch, "E2357", {"start": v(-216, 110.11) * mm, "end": v(-215.2, 110.69) * mm});
            skLineSegment(sketch, "E2358", {"start": v(-215.2, 110.69) * mm, "end": v(-214.44, 111.32) * mm});
            skLineSegment(sketch, "E2359", {"start": v(-214.44, 111.32) * mm, "end": v(-213.68, 111.99) * mm});
            skLineSegment(sketch, "E2360", {"start": v(-213.68, 111.99) * mm, "end": v(-211.8, 113.8) * mm});
            skLineSegment(sketch, "E2361", {"start": v(-211.8, 113.8) * mm, "end": v(-209.95, 115.67) * mm});
            skLineSegment(sketch, "E2362", {"start": v(-209.95, 115.67) * mm, "end": v(-208.16, 117.58) * mm});
            skLineSegment(sketch, "E2363", {"start": v(-208.16, 117.58) * mm, "end": v(-206.42, 119.53) * mm});
            skLineSegment(sketch, "E2364", {"start": v(-206.42, 119.53) * mm, "end": v(-204.72, 121.52) * mm});
            skLineSegment(sketch, "E2365", {"start": v(-204.72, 121.52) * mm, "end": v(-203.06, 123.54) * mm});
            skLineSegment(sketch, "E2366", {"start": v(-203.06, 123.54) * mm, "end": v(-201.44, 125.6) * mm});
            skLineSegment(sketch, "E2367", {"start": v(-201.44, 125.6) * mm, "end": v(-199.85, 127.68) * mm});
            skLineSegment(sketch, "E2368", {"start": v(-199.85, 127.68) * mm, "end": v(-199.14, 128.56) * mm});
            skLineSegment(sketch, "E2369", {"start": v(-199.14, 128.56) * mm, "end": v(-198.39, 129.42) * mm});
            skLineSegment(sketch, "E2370", {"start": v(-198.39, 129.42) * mm, "end": v(-197.63, 130.28) * mm});
            skLineSegment(sketch, "E2371", {"start": v(-197.63, 130.28) * mm, "end": v(-196.9, 131.16) * mm});
            skLineSegment(sketch, "E2372", {"start": v(-196.9, 131.16) * mm, "end": v(-196.23, 132.06) * mm});
            skLineSegment(sketch, "E2373", {"start": v(-196.23, 132.06) * mm, "end": v(-195.69, 133.02) * mm});
            skLineSegment(sketch, "E2374", {"start": v(-195.69, 133.02) * mm, "end": v(-195.3, 134.03) * mm});
            skLineSegment(sketch, "E2375", {"start": v(-195.3, 134.03) * mm, "end": v(-195.1, 135.11) * mm});
            skLineSegment(sketch, "E2376", {"start": v(-195.1, 135.11) * mm, "end": v(-195.19, 136.03) * mm});
            skLineSegment(sketch, "E2377", {"start": v(-195.19, 136.03) * mm, "end": v(-195.57, 136.8) * mm});
            skLineSegment(sketch, "E2378", {"start": v(-195.57, 136.8) * mm, "end": v(-196.17, 137.44) * mm});
            skLineSegment(sketch, "E2379", {"start": v(-196.17, 137.44) * mm, "end": v(-196.9, 138.03) * mm});
            skLineSegment(sketch, "E2380", {"start": v(-196.9, 138.03) * mm, "end": v(-197.7, 138.6) * mm});
            skLineSegment(sketch, "E2381", {"start": v(-197.7, 138.6) * mm, "end": v(-198.48, 139.19) * mm});
            skLineSegment(sketch, "E2382", {"start": v(-198.48, 139.19) * mm, "end": v(-199.16, 139.85) * mm});
            skLineSegment(sketch, "E2383", {"start": v(-199.16, 139.85) * mm, "end": v(-199.67, 140.64) * mm});
            skLineSegment(sketch, "E2384", {"start": v(-199.67, 140.64) * mm, "end": v(-199.72, 140.75) * mm});
            skLineSegment(sketch, "E2385", {"start": v(-199.72, 140.75) * mm, "end": v(-199.79, 140.85) * mm});
            skLineSegment(sketch, "E2386", {"start": v(-199.79, 140.85) * mm, "end": v(-199.85, 140.96) * mm});
            skLineSegment(sketch, "E2387", {"start": v(-199.85, 140.96) * mm, "end": v(-199.92, 141.06) * mm});
            skLineSegment(sketch, "E2388", {"start": v(-199.92, 141.06) * mm, "end": v(-200, 141.17) * mm});
            skLineSegment(sketch, "E2389", {"start": v(-200, 141.17) * mm, "end": v(-200.06, 141.27) * mm});
            skLineSegment(sketch, "E2390", {"start": v(-200.06, 141.27) * mm, "end": v(-200.12, 141.38) * mm});
            skLineSegment(sketch, "E2391", {"start": v(-200.12, 141.38) * mm, "end": v(-200.18, 141.5) * mm});
            skLineSegment(sketch, "E2392", {"start": v(-200.18, 141.5) * mm, "end": v(-200.66, 142.44) * mm});
            skLineSegment(sketch, "E2393", {"start": v(-200.66, 142.44) * mm, "end": v(-201.16, 143.11) * mm});
            skLineSegment(sketch, "E2394", {"start": v(-201.16, 143.11) * mm, "end": v(-201.69, 143.51) * mm});
            skLineSegment(sketch, "E2395", {"start": v(-201.69, 143.51) * mm, "end": v(-202.25, 143.66) * mm});
            skLineSegment(sketch, "E2396", {"start": v(-202.25, 143.66) * mm, "end": v(-202.84, 143.57) * mm});
            skLineSegment(sketch, "E2397", {"start": v(-202.84, 143.57) * mm, "end": v(-203.48, 143.26) * mm});
            skLineSegment(sketch, "E2398", {"start": v(-203.48, 143.26) * mm, "end": v(-204.16, 142.75) * mm});
            skLineSegment(sketch, "E2399", {"start": v(-204.16, 142.75) * mm, "end": v(-204.89, 142.04) * mm});
            skLineSegment(sketch, "E2400", {"start": v(-204.89, 142.04) * mm, "end": v(-207.3, 139.5) * mm});
            skLineSegment(sketch, "E2401", {"start": v(-207.3, 139.5) * mm, "end": v(-209.7, 136.99) * mm});
            skLineSegment(sketch, "E2402", {"start": v(-209.7, 136.99) * mm, "end": v(-212.13, 134.47) * mm});
            skLineSegment(sketch, "E2403", {"start": v(-212.13, 134.47) * mm, "end": v(-214.56, 131.96) * mm});
            skLineSegment(sketch, "E2404", {"start": v(-214.56, 131.96) * mm, "end": v(-216.99, 129.46) * mm});
            skLineSegment(sketch, "E2405", {"start": v(-216.99, 129.46) * mm, "end": v(-219.42, 126.95) * mm});
            skLineSegment(sketch, "E2406", {"start": v(-219.42, 126.95) * mm, "end": v(-221.85, 124.45) * mm});
            skLineSegment(sketch, "E2407", {"start": v(-221.85, 124.45) * mm, "end": v(-224.28, 121.94) * mm});
            skLineSegment(sketch, "E2408", {"start": v(-224.28, 121.94) * mm, "end": v(-224.88, 121.27) * mm});
            skLineSegment(sketch, "E2409", {"start": v(-224.88, 121.27) * mm, "end": v(-225.4, 120.57) * mm});
            skLineSegment(sketch, "E2410", {"start": v(-225.4, 120.57) * mm, "end": v(-225.87, 119.83) * mm});
            skLineSegment(sketch, "E2411", {"start": v(-225.87, 119.83) * mm, "end": v(-226.25, 119.06) * mm});
            skLineSegment(sketch, "E2412", {"start": v(-226.25, 119.06) * mm, "end": v(-226.57, 118.27) * mm});
            skLineSegment(sketch, "E2413", {"start": v(-226.57, 118.27) * mm, "end": v(-226.82, 117.44) * mm});
            skLineSegment(sketch, "E2414", {"start": v(-226.82, 117.44) * mm, "end": v(-227, 116.58) * mm});
            skLineSegment(sketch, "E2415", {"start": v(-227, 116.58) * mm, "end": v(-227.1, 115.7) * mm});
            skLineSegment(sketch, "E2416", {"start": v(-227.1, 115.7) * mm, "end": v(-227.07, 114.23) * mm});
            skLineSegment(sketch, "E2417", {"start": v(-227.07, 114.23) * mm, "end": v(-226.76, 112.86) * mm});
            skLineSegment(sketch, "E2418", {"start": v(-226.76, 112.86) * mm, "end": v(-226.18, 111.61) * mm});
            skLineSegment(sketch, "E2419", {"start": v(-226.18, 111.61) * mm, "end": v(-225.37, 110.53) * mm});
            skLineSegment(sketch, "E2420", {"start": v(-225.37, 110.53) * mm, "end": v(-224.36, 109.64) * mm});
            skLineSegment(sketch, "E2421", {"start": v(-224.36, 109.64) * mm, "end": v(-223.16, 108.98) * mm});
            skLineSegment(sketch, "E2422", {"start": v(-223.16, 108.98) * mm, "end": v(-221.8, 108.57) * mm});
            skLineSegment(sketch, "E2423", {"start": v(-221.8, 108.57) * mm, "end": v(-220.32, 108.45) * mm});
            skLineSegment(sketch, "E2424", {"start": v(227, 115.24) * mm, "end": v(227.01, 116.36) * mm});
            skLineSegment(sketch, "E2425", {"start": v(227.01, 116.36) * mm, "end": v(226.86, 117.43) * mm});
            skLineSegment(sketch, "E2426", {"start": v(226.86, 117.43) * mm, "end": v(226.57, 118.45) * mm});
            skLineSegment(sketch, "E2427", {"start": v(226.57, 118.45) * mm, "end": v(226.15, 119.42) * mm});
            skLineSegment(sketch, "E2428", {"start": v(226.15, 119.42) * mm, "end": v(225.62, 120.35) * mm});
            skLineSegment(sketch, "E2429", {"start": v(225.62, 120.35) * mm, "end": v(225, 121.25) * mm});
            skLineSegment(sketch, "E2430", {"start": v(225, 121.25) * mm, "end": v(224.27, 122.12) * mm});
            skLineSegment(sketch, "E2431", {"start": v(224.27, 122.12) * mm, "end": v(223.49, 122.96) * mm});
            skLineSegment(sketch, "E2432", {"start": v(223.49, 122.96) * mm, "end": v(221.65, 124.82) * mm});
            skLineSegment(sketch, "E2433", {"start": v(221.65, 124.82) * mm, "end": v(219.82, 126.68) * mm});
            skLineSegment(sketch, "E2434", {"start": v(219.82, 126.68) * mm, "end": v(218, 128.55) * mm});
            skLineSegment(sketch, "E2435", {"start": v(218, 128.55) * mm, "end": v(216.17, 130.42) * mm});
            skLineSegment(sketch, "E2436", {"start": v(216.17, 130.42) * mm, "end": v(214.35, 132.29) * mm});
            skLineSegment(sketch, "E2437", {"start": v(214.35, 132.29) * mm, "end": v(212.53, 134.16) * mm});
            skLineSegment(sketch, "E2438", {"start": v(212.53, 134.16) * mm, "end": v(210.7, 136.03) * mm});
            skLineSegment(sketch, "E2439", {"start": v(210.7, 136.03) * mm, "end": v(208.88, 137.9) * mm});
            skLineSegment(sketch, "E2440", {"start": v(208.88, 137.9) * mm, "end": v(208.2, 138.65) * mm});
            skLineSegment(sketch, "E2441", {"start": v(208.2, 138.65) * mm, "end": v(207.53, 139.46) * mm});
            skLineSegment(sketch, "E2442", {"start": v(207.53, 139.46) * mm, "end": v(206.87, 140.3) * mm});
            skLineSegment(sketch, "E2443", {"start": v(206.87, 140.3) * mm, "end": v(206.2, 141.1) * mm});
            skLineSegment(sketch, "E2444", {"start": v(206.2, 141.1) * mm, "end": v(205.53, 141.85) * mm});
            skLineSegment(sketch, "E2445", {"start": v(205.53, 141.85) * mm, "end": v(204.82, 142.5) * mm});
            skLineSegment(sketch, "E2446", {"start": v(204.82, 142.5) * mm, "end": v(204.07, 143) * mm});
            skLineSegment(sketch, "E2447", {"start": v(204.07, 143) * mm, "end": v(203.27, 143.35) * mm});
            skLineSegment(sketch, "E2448", {"start": v(203.27, 143.35) * mm, "end": v(202.16, 143.45) * mm});
            skLineSegment(sketch, "E2449", {"start": v(202.16, 143.45) * mm, "end": v(201.31, 143.13) * mm});
            skLineSegment(sketch, "E2450", {"start": v(201.31, 143.13) * mm, "end": v(200.65, 142.48) * mm});
            skLineSegment(sketch, "E2451", {"start": v(200.65, 142.48) * mm, "end": v(200.1, 141.61) * mm});
            skLineSegment(sketch, "E2452", {"start": v(200.1, 141.61) * mm, "end": v(199.6, 140.64) * mm});
            skLineSegment(sketch, "E2453", {"start": v(199.6, 140.64) * mm, "end": v(199.06, 139.67) * mm});
            skLineSegment(sketch, "E2454", {"start": v(199.06, 139.67) * mm, "end": v(198.43, 138.82) * mm});
            skLineSegment(sketch, "E2455", {"start": v(198.43, 138.82) * mm, "end": v(197.62, 138.18) * mm});
            skLineSegment(sketch, "E2456", {"start": v(197.62, 138.18) * mm, "end": v(196.58, 137.52) * mm});
            skLineSegment(sketch, "E2457", {"start": v(196.58, 137.52) * mm, "end": v(195.87, 136.8) * mm});
            skLineSegment(sketch, "E2458", {"start": v(195.87, 136.8) * mm, "end": v(195.45, 136.04) * mm});
            skLineSegment(sketch, "E2459", {"start": v(195.45, 136.04) * mm, "end": v(195.3, 135.24) * mm});
            skLineSegment(sketch, "E2460", {"start": v(195.3, 135.24) * mm, "end": v(195.4, 134.4) * mm});
            skLineSegment(sketch, "E2461", {"start": v(195.4, 134.4) * mm, "end": v(195.71, 133.52) * mm});
            skLineSegment(sketch, "E2462", {"start": v(195.71, 133.52) * mm, "end": v(196.23, 132.62) * mm});
            skLineSegment(sketch, "E2463", {"start": v(196.23, 132.62) * mm, "end": v(196.92, 131.7) * mm});
            skLineSegment(sketch, "E2464", {"start": v(196.92, 131.7) * mm, "end": v(197.9, 130.49) * mm});
            skLineSegment(sketch, "E2465", {"start": v(197.9, 130.49) * mm, "end": v(198.85, 129.26) * mm});
            skLineSegment(sketch, "E2466", {"start": v(198.85, 129.26) * mm, "end": v(199.8, 128.03) * mm});
            skLineSegment(sketch, "E2467", {"start": v(199.8, 128.03) * mm, "end": v(200.74, 126.8) * mm});
            skLineSegment(sketch, "E2468", {"start": v(200.74, 126.8) * mm, "end": v(201.68, 125.55) * mm});
            skLineSegment(sketch, "E2469", {"start": v(201.68, 125.55) * mm, "end": v(202.63, 124.32) * mm});
            skLineSegment(sketch, "E2470", {"start": v(202.63, 124.32) * mm, "end": v(203.6, 123.1) * mm});
            skLineSegment(sketch, "E2471", {"start": v(203.6, 123.1) * mm, "end": v(204.58, 121.9) * mm});
            skLineSegment(sketch, "E2472", {"start": v(204.58, 121.9) * mm, "end": v(205.9, 120.33) * mm});
            skLineSegment(sketch, "E2473", {"start": v(205.9, 120.33) * mm, "end": v(207.23, 118.77) * mm});
            skLineSegment(sketch, "E2474", {"start": v(207.23, 118.77) * mm, "end": v(208.59, 117.23) * mm});
            skLineSegment(sketch, "E2475", {"start": v(208.59, 117.23) * mm, "end": v(209.98, 115.72) * mm});
            skLineSegment(sketch, "E2476", {"start": v(209.98, 115.72) * mm, "end": v(211.42, 114.26) * mm});
            skLineSegment(sketch, "E2477", {"start": v(211.42, 114.26) * mm, "end": v(212.9, 112.85) * mm});
            skLineSegment(sketch, "E2478", {"start": v(212.9, 112.85) * mm, "end": v(214.45, 111.5) * mm});
            skLineSegment(sketch, "E2479", {"start": v(214.45, 111.5) * mm, "end": v(216.06, 110.22) * mm});
            skLineSegment(sketch, "E2480", {"start": v(216.06, 110.22) * mm, "end": v(216.96, 109.6) * mm});
            skLineSegment(sketch, "E2481", {"start": v(216.96, 109.6) * mm, "end": v(217.88, 109.1) * mm});
            skLineSegment(sketch, "E2482", {"start": v(217.88, 109.1) * mm, "end": v(218.84, 108.71) * mm});
            skLineSegment(sketch, "E2483", {"start": v(218.84, 108.71) * mm, "end": v(219.82, 108.47) * mm});
            skLineSegment(sketch, "E2484", {"start": v(219.82, 108.47) * mm, "end": v(220.82, 108.38) * mm});
            skLineSegment(sketch, "E2485", {"start": v(220.82, 108.38) * mm, "end": v(221.85, 108.47) * mm});
            skLineSegment(sketch, "E2486", {"start": v(221.85, 108.47) * mm, "end": v(222.9, 108.75) * mm});
            skLineSegment(sketch, "E2487", {"start": v(222.9, 108.75) * mm, "end": v(223.96, 109.23) * mm});
            skLineSegment(sketch, "E2488", {"start": v(223.96, 109.23) * mm, "end": v(224.76, 109.74) * mm});
            skLineSegment(sketch, "E2489", {"start": v(224.76, 109.74) * mm, "end": v(225.42, 110.33) * mm});
            skLineSegment(sketch, "E2490", {"start": v(225.42, 110.33) * mm, "end": v(225.95, 110.98) * mm});
            skLineSegment(sketch, "E2491", {"start": v(225.95, 110.98) * mm, "end": v(226.37, 111.7) * mm});
            skLineSegment(sketch, "E2492", {"start": v(226.37, 111.7) * mm, "end": v(226.68, 112.5) * mm});
            skLineSegment(sketch, "E2493", {"start": v(226.68, 112.5) * mm, "end": v(226.88, 113.34) * mm});
            skLineSegment(sketch, "E2494", {"start": v(226.88, 113.34) * mm, "end": v(226.99, 114.26) * mm});
            skLineSegment(sketch, "E2495", {"start": v(226.99, 114.26) * mm, "end": v(227, 115.24) * mm});
            skLineSegment(sketch, "E2496", {"start": v(210.02, 101.7) * mm, "end": v(210.47, 103.24) * mm});
            skLineSegment(sketch, "E2497", {"start": v(210.47, 103.24) * mm, "end": v(210.7, 104.64) * mm});
            skLineSegment(sketch, "E2498", {"start": v(210.7, 104.64) * mm, "end": v(210.73, 105.91) * mm});
            skLineSegment(sketch, "E2499", {"start": v(210.73, 105.91) * mm, "end": v(210.56, 107.08) * mm});
            skLineSegment(sketch, "E2500", {"start": v(210.56, 107.08) * mm, "end": v(210.2, 108.16) * mm});
            skLineSegment(sketch, "E2501", {"start": v(210.2, 108.16) * mm, "end": v(209.64, 109.17) * mm});
            skLineSegment(sketch, "E2502", {"start": v(209.64, 109.17) * mm, "end": v(208.91, 110.13) * mm});
            skLineSegment(sketch, "E2503", {"start": v(208.91, 110.13) * mm, "end": v(208, 111.06) * mm});
            skLineSegment(sketch, "E2504", {"start": v(208, 111.06) * mm, "end": v(205.52, 113.45) * mm});
            skLineSegment(sketch, "E2505", {"start": v(205.52, 113.45) * mm, "end": v(203.15, 115.93) * mm});
            skLineSegment(sketch, "E2506", {"start": v(203.15, 115.93) * mm, "end": v(200.87, 118.49) * mm});
            skLineSegment(sketch, "E2507", {"start": v(200.87, 118.49) * mm, "end": v(198.67, 121.12) * mm});
            skLineSegment(sketch, "E2508", {"start": v(198.67, 121.12) * mm, "end": v(196.56, 123.82) * mm});
            skLineSegment(sketch, "E2509", {"start": v(196.56, 123.82) * mm, "end": v(194.5, 126.58) * mm});
            skLineSegment(sketch, "E2510", {"start": v(194.5, 126.58) * mm, "end": v(192.5, 129.38) * mm});
            skLineSegment(sketch, "E2511", {"start": v(192.5, 129.38) * mm, "end": v(190.56, 132.22) * mm});
            skLineSegment(sketch, "E2512", {"start": v(190.56, 132.22) * mm, "end": v(189.8, 133.43) * mm});
            skLineSegment(sketch, "E2513", {"start": v(189.8, 133.43) * mm, "end": v(189.23, 134.56) * mm});
            skLineSegment(sketch, "E2514", {"start": v(189.23, 134.56) * mm, "end": v(188.89, 135.62) * mm});
            skLineSegment(sketch, "E2515", {"start": v(188.89, 135.62) * mm, "end": v(188.82, 136.62) * mm});
            skLineSegment(sketch, "E2516", {"start": v(188.82, 136.62) * mm, "end": v(189.06, 137.55) * mm});
            skLineSegment(sketch, "E2517", {"start": v(189.06, 137.55) * mm, "end": v(189.65, 138.43) * mm});
            skLineSegment(sketch, "E2518", {"start": v(189.65, 138.43) * mm, "end": v(190.63, 139.25) * mm});
            skLineSegment(sketch, "E2519", {"start": v(190.63, 139.25) * mm, "end": v(192.04, 140.02) * mm});
            skLineSegment(sketch, "E2520", {"start": v(192.04, 140.02) * mm, "end": v(192.76, 140.4) * mm});
            skLineSegment(sketch, "E2521", {"start": v(192.76, 140.4) * mm, "end": v(193.43, 140.83) * mm});
            skLineSegment(sketch, "E2522", {"start": v(193.43, 140.83) * mm, "end": v(194.05, 141.34) * mm});
            skLineSegment(sketch, "E2523", {"start": v(194.05, 141.34) * mm, "end": v(194.64, 141.9) * mm});
            skLineSegment(sketch, "E2524", {"start": v(194.64, 141.9) * mm, "end": v(195.19, 142.5) * mm});
            skLineSegment(sketch, "E2525", {"start": v(195.19, 142.5) * mm, "end": v(195.7, 143.15) * mm});
            skLineSegment(sketch, "E2526", {"start": v(195.7, 143.15) * mm, "end": v(196.16, 143.83) * mm});
            skLineSegment(sketch, "E2527", {"start": v(196.16, 143.83) * mm, "end": v(196.6, 144.55) * mm});
            skLineSegment(sketch, "E2528", {"start": v(196.6, 144.55) * mm, "end": v(197.22, 145.85) * mm});
            skLineSegment(sketch, "E2529", {"start": v(197.22, 145.85) * mm, "end": v(197.56, 147.1) * mm});
            skLineSegment(sketch, "E2530", {"start": v(197.56, 147.1) * mm, "end": v(197.64, 148.27) * mm});
            skLineSegment(sketch, "E2531", {"start": v(197.64, 148.27) * mm, "end": v(197.48, 149.4) * mm});
            skLineSegment(sketch, "E2532", {"start": v(197.48, 149.4) * mm, "end": v(197.07, 150.47) * mm});
            skLineSegment(sketch, "E2533", {"start": v(197.07, 150.47) * mm, "end": v(196.45, 151.47) * mm});
            skLineSegment(sketch, "E2534", {"start": v(196.45, 151.47) * mm, "end": v(195.6, 152.41) * mm});
            skLineSegment(sketch, "E2535", {"start": v(195.6, 152.41) * mm, "end": v(194.57, 153.3) * mm});
            skLineSegment(sketch, "E2536", {"start": v(194.57, 153.3) * mm, "end": v(193.42, 154.02) * mm});
            skLineSegment(sketch, "E2537", {"start": v(193.42, 154.02) * mm, "end": v(192.3, 154.46) * mm});
            skLineSegment(sketch, "E2538", {"start": v(192.3, 154.46) * mm, "end": v(191.2, 154.63) * mm});
            skLineSegment(sketch, "E2539", {"start": v(191.2, 154.63) * mm, "end": v(190.13, 154.55) * mm});
            skLineSegment(sketch, "E2540", {"start": v(190.13, 154.55) * mm, "end": v(189.1, 154.22) * mm});
            skLineSegment(sketch, "E2541", {"start": v(189.1, 154.22) * mm, "end": v(188.09, 153.68) * mm});
            skLineSegment(sketch, "E2542", {"start": v(188.09, 153.68) * mm, "end": v(187.12, 152.94) * mm});
            skLineSegment(sketch, "E2543", {"start": v(187.12, 152.94) * mm, "end": v(186.2, 152.01) * mm});
            skLineSegment(sketch, "E2544", {"start": v(186.2, 152.01) * mm, "end": v(184.9, 150.16) * mm});
            skLineSegment(sketch, "E2545", {"start": v(184.9, 150.16) * mm, "end": v(183.84, 147.8) * mm});
            skLineSegment(sketch, "E2546", {"start": v(183.84, 147.8) * mm, "end": v(183.03, 145.09) * mm});
            skLineSegment(sketch, "E2547", {"start": v(183.03, 145.09) * mm, "end": v(182.5, 142.2) * mm});
            skLineSegment(sketch, "E2548", {"start": v(182.5, 142.2) * mm, "end": v(182.3, 139.28) * mm});
            skLineSegment(sketch, "E2549", {"start": v(182.3, 139.28) * mm, "end": v(182.43, 136.52) * mm});
            skLineSegment(sketch, "E2550", {"start": v(182.43, 136.52) * mm, "end": v(182.96, 134.06) * mm});
            skLineSegment(sketch, "E2551", {"start": v(182.96, 134.06) * mm, "end": v(183.9, 132.08) * mm});
            skLineSegment(sketch, "E2552", {"start": v(183.9, 132.08) * mm, "end": v(186.76, 128.06) * mm});
            skLineSegment(sketch, "E2553", {"start": v(186.76, 128.06) * mm, "end": v(189.72, 124.11) * mm});
            skLineSegment(sketch, "E2554", {"start": v(189.72, 124.11) * mm, "end": v(192.8, 120.24) * mm});
            skLineSegment(sketch, "E2555", {"start": v(192.8, 120.24) * mm, "end": v(196, 116.44) * mm});
            skLineSegment(sketch, "E2556", {"start": v(196, 116.44) * mm, "end": v(199.31, 112.7) * mm});
            skLineSegment(sketch, "E2557", {"start": v(199.31, 112.7) * mm, "end": v(202.75, 109) * mm});
            skLineSegment(sketch, "E2558", {"start": v(202.75, 109) * mm, "end": v(206.32, 105.33) * mm});
            skLineSegment(sketch, "E2559", {"start": v(206.32, 105.33) * mm, "end": v(210.02, 101.7) * mm});
            skLineSegment(sketch, "E2560", {"start": v(-209.77, 101.73) * mm, "end": v(-206.07, 105.34) * mm});
            skLineSegment(sketch, "E2561", {"start": v(-206.07, 105.34) * mm, "end": v(-202.48, 108.96) * mm});
            skLineSegment(sketch, "E2562", {"start": v(-202.48, 108.96) * mm, "end": v(-199, 112.62) * mm});
            skLineSegment(sketch, "E2563", {"start": v(-199, 112.62) * mm, "end": v(-195.67, 116.33) * mm});
            skLineSegment(sketch, "E2564", {"start": v(-195.67, 116.33) * mm, "end": v(-192.48, 120.1) * mm});
            skLineSegment(sketch, "E2565", {"start": v(-192.48, 120.1) * mm, "end": v(-189.46, 123.98) * mm});
            skLineSegment(sketch, "E2566", {"start": v(-189.46, 123.98) * mm, "end": v(-186.62, 127.97) * mm});
            skLineSegment(sketch, "E2567", {"start": v(-186.62, 127.97) * mm, "end": v(-183.99, 132.1) * mm});
            skLineSegment(sketch, "E2568", {"start": v(-183.99, 132.1) * mm, "end": v(-182.86, 134.41) * mm});
            skLineSegment(sketch, "E2569", {"start": v(-182.86, 134.41) * mm, "end": v(-182.18, 136.82) * mm});
            skLineSegment(sketch, "E2570", {"start": v(-182.18, 136.82) * mm, "end": v(-181.92, 139.3) * mm});
            skLineSegment(sketch, "E2571", {"start": v(-181.92, 139.3) * mm, "end": v(-182.04, 141.8) * mm});
            skLineSegment(sketch, "E2572", {"start": v(-182.04, 141.8) * mm, "end": v(-182.5, 144.3) * mm});
            skLineSegment(sketch, "E2573", {"start": v(-182.5, 144.3) * mm, "end": v(-183.29, 146.78) * mm});
            skLineSegment(sketch, "E2574", {"start": v(-183.29, 146.78) * mm, "end": v(-184.35, 149.2) * mm});
            skLineSegment(sketch, "E2575", {"start": v(-184.35, 149.2) * mm, "end": v(-185.66, 151.55) * mm});
            skLineSegment(sketch, "E2576", {"start": v(-185.66, 151.55) * mm, "end": v(-186.4, 152.57) * mm});
            skLineSegment(sketch, "E2577", {"start": v(-186.4, 152.57) * mm, "end": v(-187.24, 153.41) * mm});
            skLineSegment(sketch, "E2578", {"start": v(-187.24, 153.41) * mm, "end": v(-188.18, 154.06) * mm});
            skLineSegment(sketch, "E2579", {"start": v(-188.18, 154.06) * mm, "end": v(-189.2, 154.49) * mm});
            skLineSegment(sketch, "E2580", {"start": v(-189.2, 154.49) * mm, "end": v(-190.28, 154.68) * mm});
            skLineSegment(sketch, "E2581", {"start": v(-190.28, 154.68) * mm, "end": v(-191.43, 154.6) * mm});
            skLineSegment(sketch, "E2582", {"start": v(-191.43, 154.6) * mm, "end": v(-192.62, 154.26) * mm});
            skLineSegment(sketch, "E2583", {"start": v(-192.62, 154.26) * mm, "end": v(-193.84, 153.61) * mm});
            skLineSegment(sketch, "E2584", {"start": v(-193.84, 153.61) * mm, "end": v(-195, 152.77) * mm});
            skLineSegment(sketch, "E2585", {"start": v(-195, 152.77) * mm, "end": v(-195.93, 151.84) * mm});
            skLineSegment(sketch, "E2586", {"start": v(-195.93, 151.84) * mm, "end": v(-196.65, 150.84) * mm});
            skLineSegment(sketch, "E2587", {"start": v(-196.65, 150.84) * mm, "end": v(-197.14, 149.76) * mm});
            skLineSegment(sketch, "E2588", {"start": v(-197.14, 149.76) * mm, "end": v(-197.38, 148.6) * mm});
            skLineSegment(sketch, "E2589", {"start": v(-197.38, 148.6) * mm, "end": v(-197.35, 147.35) * mm});
            skLineSegment(sketch, "E2590", {"start": v(-197.35, 147.35) * mm, "end": v(-197.06, 146.03) * mm});
            skLineSegment(sketch, "E2591", {"start": v(-197.06, 146.03) * mm, "end": v(-196.47, 144.63) * mm});
            skLineSegment(sketch, "E2592", {"start": v(-196.47, 144.63) * mm, "end": v(-196, 143.8) * mm});
            skLineSegment(sketch, "E2593", {"start": v(-196, 143.8) * mm, "end": v(-195.46, 143) * mm});
            skLineSegment(sketch, "E2594", {"start": v(-195.46, 143) * mm, "end": v(-194.87, 142.28) * mm});
            skLineSegment(sketch, "E2595", {"start": v(-194.87, 142.28) * mm, "end": v(-194.23, 141.62) * mm});
            skLineSegment(sketch, "E2596", {"start": v(-194.23, 141.62) * mm, "end": v(-193.53, 141.01) * mm});
            skLineSegment(sketch, "E2597", {"start": v(-193.53, 141.01) * mm, "end": v(-192.79, 140.47) * mm});
            skLineSegment(sketch, "E2598", {"start": v(-192.79, 140.47) * mm, "end": v(-192, 139.98) * mm});
            skLineSegment(sketch, "E2599", {"start": v(-192, 139.98) * mm, "end": v(-191.17, 139.54) * mm});
            skLineSegment(sketch, "E2600", {"start": v(-191.17, 139.54) * mm, "end": v(-190.08, 138.93) * mm});
            skLineSegment(sketch, "E2601", {"start": v(-190.08, 138.93) * mm, "end": v(-189.29, 138.28) * mm});
            skLineSegment(sketch, "E2602", {"start": v(-189.29, 138.28) * mm, "end": v(-188.78, 137.59) * mm});
            skLineSegment(sketch, "E2603", {"start": v(-188.78, 137.59) * mm, "end": v(-188.53, 136.84) * mm});
            skLineSegment(sketch, "E2604", {"start": v(-188.53, 136.84) * mm, "end": v(-188.52, 136.04) * mm});
            skLineSegment(sketch, "E2605", {"start": v(-188.52, 136.04) * mm, "end": v(-188.74, 135.18) * mm});
            skLineSegment(sketch, "E2606", {"start": v(-188.74, 135.18) * mm, "end": v(-189.16, 134.25) * mm});
            skLineSegment(sketch, "E2607", {"start": v(-189.16, 134.25) * mm, "end": v(-189.76, 133.25) * mm});
            skLineSegment(sketch, "E2608", {"start": v(-189.76, 133.25) * mm, "end": v(-191.74, 130.3) * mm});
            skLineSegment(sketch, "E2609", {"start": v(-191.74, 130.3) * mm, "end": v(-193.78, 127.38) * mm});
            skLineSegment(sketch, "E2610", {"start": v(-193.78, 127.38) * mm, "end": v(-195.87, 124.52) * mm});
            skLineSegment(sketch, "E2611", {"start": v(-195.87, 124.52) * mm, "end": v(-198.03, 121.72) * mm});
            skLineSegment(sketch, "E2612", {"start": v(-198.03, 121.72) * mm, "end": v(-200.28, 118.98) * mm});
            skLineSegment(sketch, "E2613", {"start": v(-200.28, 118.98) * mm, "end": v(-202.62, 116.32) * mm});
            skLineSegment(sketch, "E2614", {"start": v(-202.62, 116.32) * mm, "end": v(-205.06, 113.75) * mm});
            skLineSegment(sketch, "E2615", {"start": v(-205.06, 113.75) * mm, "end": v(-207.62, 111.27) * mm});
            skLineSegment(sketch, "E2616", {"start": v(-207.62, 111.27) * mm, "end": v(-208.52, 110.35) * mm});
            skLineSegment(sketch, "E2617", {"start": v(-208.52, 110.35) * mm, "end": v(-209.25, 109.4) * mm});
            skLineSegment(sketch, "E2618", {"start": v(-209.25, 109.4) * mm, "end": v(-209.82, 108.38) * mm});
            skLineSegment(sketch, "E2619", {"start": v(-209.82, 108.38) * mm, "end": v(-210.2, 107.29) * mm});
            skLineSegment(sketch, "E2620", {"start": v(-210.2, 107.29) * mm, "end": v(-210.4, 106.1) * mm});
            skLineSegment(sketch, "E2621", {"start": v(-210.4, 106.1) * mm, "end": v(-210.4, 104.78) * mm});
            skLineSegment(sketch, "E2622", {"start": v(-210.4, 104.78) * mm, "end": v(-210.2, 103.33) * mm});
            skLineSegment(sketch, "E2623", {"start": v(-210.2, 103.33) * mm, "end": v(-209.77, 101.73) * mm});
            skLineSegment(sketch, "E2624", {"start": v(-27.6, 229.17) * mm, "end": v(-30.67, 231.42) * mm});
            skLineSegment(sketch, "E2625", {"start": v(-30.67, 231.42) * mm, "end": v(-33.8, 233.52) * mm});
            skLineSegment(sketch, "E2626", {"start": v(-33.8, 233.52) * mm, "end": v(-36.99, 235.4) * mm});
            skLineSegment(sketch, "E2627", {"start": v(-36.99, 235.4) * mm, "end": v(-40.27, 237.03) * mm});
            skLineSegment(sketch, "E2628", {"start": v(-40.27, 237.03) * mm, "end": v(-43.68, 238.34) * mm});
            skLineSegment(sketch, "E2629", {"start": v(-43.68, 238.34) * mm, "end": v(-47.22, 239.28) * mm});
            skLineSegment(sketch, "E2630", {"start": v(-47.22, 239.28) * mm, "end": v(-50.92, 239.8) * mm});
            skLineSegment(sketch, "E2631", {"start": v(-50.92, 239.8) * mm, "end": v(-54.8, 239.86) * mm});
            skLineSegment(sketch, "E2632", {"start": v(-54.8, 239.86) * mm, "end": v(-55.9, 239.77) * mm});
            skLineSegment(sketch, "E2633", {"start": v(-55.9, 239.77) * mm, "end": v(-56.96, 239.6) * mm});
            skLineSegment(sketch, "E2634", {"start": v(-56.96, 239.6) * mm, "end": v(-57.97, 239.35) * mm});
            skLineSegment(sketch, "E2635", {"start": v(-57.97, 239.35) * mm, "end": v(-58.94, 239) * mm});
            skLineSegment(sketch, "E2636", {"start": v(-58.94, 239) * mm, "end": v(-59.84, 238.54) * mm});
            skLineSegment(sketch, "E2637", {"start": v(-59.84, 238.54) * mm, "end": v(-60.7, 237.95) * mm});
            skLineSegment(sketch, "E2638", {"start": v(-60.7, 237.95) * mm, "end": v(-61.47, 237.23) * mm});
            skLineSegment(sketch, "E2639", {"start": v(-61.47, 237.23) * mm, "end": v(-62.17, 236.37) * mm});
            skLineSegment(sketch, "E2640", {"start": v(-62.17, 236.37) * mm, "end": v(-62.5, 235.89) * mm});
            skLineSegment(sketch, "E2641", {"start": v(-62.5, 235.89) * mm, "end": v(-62.78, 235.38) * mm});
            skLineSegment(sketch, "E2642", {"start": v(-62.78, 235.38) * mm, "end": v(-63.01, 234.86) * mm});
            skLineSegment(sketch, "E2643", {"start": v(-63.01, 234.86) * mm, "end": v(-63.16, 234.33) * mm});
            skLineSegment(sketch, "E2644", {"start": v(-63.16, 234.33) * mm, "end": v(-63.2, 233.8) * mm});
            skLineSegment(sketch, "E2645", {"start": v(-63.2, 233.8) * mm, "end": v(-63.09, 233.29) * mm});
            skLineSegment(sketch, "E2646", {"start": v(-63.09, 233.29) * mm, "end": v(-62.83, 232.8) * mm});
            skLineSegment(sketch, "E2647", {"start": v(-62.83, 232.8) * mm, "end": v(-62.38, 232.33) * mm});
            skLineSegment(sketch, "E2648", {"start": v(-62.38, 232.33) * mm, "end": v(-61.8, 231.97) * mm});
            skLineSegment(sketch, "E2649", {"start": v(-61.8, 231.97) * mm, "end": v(-61.33, 231.87) * mm});
            skLineSegment(sketch, "E2650", {"start": v(-61.33, 231.87) * mm, "end": v(-60.93, 231.98) * mm});
            skLineSegment(sketch, "E2651", {"start": v(-60.93, 231.98) * mm, "end": v(-60.6, 232.24) * mm});
            skLineSegment(sketch, "E2652", {"start": v(-60.6, 232.24) * mm, "end": v(-60.3, 232.62) * mm});
            skLineSegment(sketch, "E2653", {"start": v(-60.3, 232.62) * mm, "end": v(-60.02, 233.04) * mm});
            skLineSegment(sketch, "E2654", {"start": v(-60.02, 233.04) * mm, "end": v(-59.74, 233.46) * mm});
            skLineSegment(sketch, "E2655", {"start": v(-59.74, 233.46) * mm, "end": v(-59.45, 233.83) * mm});
            skLineSegment(sketch, "E2656", {"start": v(-59.45, 233.83) * mm, "end": v(-58.61, 234.6) * mm});
            skLineSegment(sketch, "E2657", {"start": v(-58.61, 234.6) * mm, "end": v(-57.76, 235.18) * mm});
            skLineSegment(sketch, "E2658", {"start": v(-57.76, 235.18) * mm, "end": v(-56.9, 235.57) * mm});
            skLineSegment(sketch, "E2659", {"start": v(-56.9, 235.57) * mm, "end": v(-56.02, 235.75) * mm});
            skLineSegment(sketch, "E2660", {"start": v(-56.02, 235.75) * mm, "end": v(-55.13, 235.7) * mm});
            skLineSegment(sketch, "E2661", {"start": v(-55.13, 235.7) * mm, "end": v(-54.25, 235.44) * mm});
            skLineSegment(sketch, "E2662", {"start": v(-54.25, 235.44) * mm, "end": v(-53.38, 234.93) * mm});
            skLineSegment(sketch, "E2663", {"start": v(-53.38, 234.93) * mm, "end": v(-52.51, 234.17) * mm});
            skLineSegment(sketch, "E2664", {"start": v(-52.51, 234.17) * mm, "end": v(-51.8, 233.3) * mm});
            skLineSegment(sketch, "E2665", {"start": v(-51.8, 233.3) * mm, "end": v(-51.32, 232.41) * mm});
            skLineSegment(sketch, "E2666", {"start": v(-51.32, 232.41) * mm, "end": v(-51.07, 231.52) * mm});
            skLineSegment(sketch, "E2667", {"start": v(-51.07, 231.52) * mm, "end": v(-51.02, 230.62) * mm});
            skLineSegment(sketch, "E2668", {"start": v(-51.02, 230.62) * mm, "end": v(-51.18, 229.72) * mm});
            skLineSegment(sketch, "E2669", {"start": v(-51.18, 229.72) * mm, "end": v(-51.53, 228.83) * mm});
            skLineSegment(sketch, "E2670", {"start": v(-51.53, 228.83) * mm, "end": v(-52.06, 227.94) * mm});
            skLineSegment(sketch, "E2671", {"start": v(-52.06, 227.94) * mm, "end": v(-52.77, 227.07) * mm});
            skLineSegment(sketch, "E2672", {"start": v(-52.77, 227.07) * mm, "end": v(-54.32, 225.7) * mm});
            skLineSegment(sketch, "E2673", {"start": v(-54.32, 225.7) * mm, "end": v(-56.1, 224.7) * mm});
            skLineSegment(sketch, "E2674", {"start": v(-56.1, 224.7) * mm, "end": v(-58.05, 224.08) * mm});
            skLineSegment(sketch, "E2675", {"start": v(-58.05, 224.08) * mm, "end": v(-60.07, 223.84) * mm});
            skLineSegment(sketch, "E2676", {"start": v(-60.07, 223.84) * mm, "end": v(-62.1, 224) * mm});
            skLineSegment(sketch, "E2677", {"start": v(-62.1, 224) * mm, "end": v(-64.06, 224.58) * mm});
            skLineSegment(sketch, "E2678", {"start": v(-64.06, 224.58) * mm, "end": v(-65.87, 225.58) * mm});
            skLineSegment(sketch, "E2679", {"start": v(-65.87, 225.58) * mm, "end": v(-67.47, 227.02) * mm});
            skLineSegment(sketch, "E2680", {"start": v(-67.47, 227.02) * mm, "end": v(-68.51, 228.1) * mm});
            skLineSegment(sketch, "E2681", {"start": v(-68.51, 228.1) * mm, "end": v(-69.39, 228.77) * mm});
            skLineSegment(sketch, "E2682", {"start": v(-69.39, 228.77) * mm, "end": v(-70.12, 229.06) * mm});
            skLineSegment(sketch, "E2683", {"start": v(-70.12, 229.06) * mm, "end": v(-70.73, 229) * mm});
            skLineSegment(sketch, "E2684", {"start": v(-70.73, 229) * mm, "end": v(-71.25, 228.62) * mm});
            skLineSegment(sketch, "E2685", {"start": v(-71.25, 228.62) * mm, "end": v(-71.7, 227.97) * mm});
            skLineSegment(sketch, "E2686", {"start": v(-71.7, 227.97) * mm, "end": v(-72.12, 227.07) * mm});
            skLineSegment(sketch, "E2687", {"start": v(-72.12, 227.07) * mm, "end": v(-72.52, 225.96) * mm});
            skLineSegment(sketch, "E2688", {"start": v(-72.52, 225.96) * mm, "end": v(-72.7, 225.43) * mm});
            skLineSegment(sketch, "E2689", {"start": v(-72.7, 225.43) * mm, "end": v(-72.88, 224.9) * mm});
            skLineSegment(sketch, "E2690", {"start": v(-72.88, 224.9) * mm, "end": v(-73.05, 224.36) * mm});
            skLineSegment(sketch, "E2691", {"start": v(-73.05, 224.36) * mm, "end": v(-73.23, 223.83) * mm});
            skLineSegment(sketch, "E2692", {"start": v(-73.23, 223.83) * mm, "end": v(-73.4, 223.3) * mm});
            skLineSegment(sketch, "E2693", {"start": v(-73.4, 223.3) * mm, "end": v(-73.57, 222.76) * mm});
            skLineSegment(sketch, "E2694", {"start": v(-73.57, 222.76) * mm, "end": v(-73.75, 222.23) * mm});
            skLineSegment(sketch, "E2695", {"start": v(-73.75, 222.23) * mm, "end": v(-73.93, 221.7) * mm});
            skLineSegment(sketch, "E2696", {"start": v(-73.93, 221.7) * mm, "end": v(-74.23, 220.6) * mm});
            skLineSegment(sketch, "E2697", {"start": v(-74.23, 220.6) * mm, "end": v(-74.31, 219.7) * mm});
            skLineSegment(sketch, "E2698", {"start": v(-74.31, 219.7) * mm, "end": v(-74.19, 219.05) * mm});
            skLineSegment(sketch, "E2699", {"start": v(-74.19, 219.05) * mm, "end": v(-73.86, 218.6) * mm});
            skLineSegment(sketch, "E2700", {"start": v(-73.86, 218.6) * mm, "end": v(-73.35, 218.35) * mm});
            skLineSegment(sketch, "E2701", {"start": v(-73.35, 218.35) * mm, "end": v(-72.65, 218.3) * mm});
            skLineSegment(sketch, "E2702", {"start": v(-72.65, 218.3) * mm, "end": v(-71.8, 218.42) * mm});
            skLineSegment(sketch, "E2703", {"start": v(-71.8, 218.42) * mm, "end": v(-70.77, 218.71) * mm});
            skLineSegment(sketch, "E2704", {"start": v(-70.77, 218.71) * mm, "end": v(-65.5, 220.44) * mm});
            skLineSegment(sketch, "E2705", {"start": v(-65.5, 220.44) * mm, "end": v(-60.2, 222.01) * mm});
            skLineSegment(sketch, "E2706", {"start": v(-60.2, 222.01) * mm, "end": v(-54.85, 223.45) * mm});
            skLineSegment(sketch, "E2707", {"start": v(-54.85, 223.45) * mm, "end": v(-49.47, 224.77) * mm});
            skLineSegment(sketch, "E2708", {"start": v(-49.47, 224.77) * mm, "end": v(-44.06, 225.99) * mm});
            skLineSegment(sketch, "E2709", {"start": v(-44.06, 225.99) * mm, "end": v(-38.6, 227.11) * mm});
            skLineSegment(sketch, "E2710", {"start": v(-38.6, 227.11) * mm, "end": v(-33.12, 228.17) * mm});
            skLineSegment(sketch, "E2711", {"start": v(-33.12, 228.17) * mm, "end": v(-27.6, 229.17) * mm});
            skLineSegment(sketch, "E2712", {"start": v(-4.16, -176.73) * mm, "end": v(-4.16, -176.18) * mm});
            skLineSegment(sketch, "E2713", {"start": v(-4.16, -176.18) * mm, "end": v(-4.17, -175.68) * mm});
            skLineSegment(sketch, "E2714", {"start": v(-4.17, -175.68) * mm, "end": v(-4.17, -175.22) * mm});
            skLineSegment(sketch, "E2715", {"start": v(-4.17, -175.22) * mm, "end": v(-4.18, -174.78) * mm});
            skLineSegment(sketch, "E2716", {"start": v(-4.18, -174.78) * mm, "end": v(-4.18, -174.37) * mm});
            skLineSegment(sketch, "E2717", {"start": v(-4.18, -174.37) * mm, "end": v(-4.18, -173.97) * mm});
            skLineSegment(sketch, "E2718", {"start": v(-4.18, -173.97) * mm, "end": v(-4.17, -173.6) * mm});
            skLineSegment(sketch, "E2719", {"start": v(-4.17, -173.6) * mm, "end": v(-4.15, -173.22) * mm});
            skLineSegment(sketch, "E2720", {"start": v(-4.15, -173.22) * mm, "end": v(-4.1, -171.94) * mm});
            skLineSegment(sketch, "E2721", {"start": v(-4.1, -171.94) * mm, "end": v(-4.15, -170.76) * mm});
            skLineSegment(sketch, "E2722", {"start": v(-4.15, -170.76) * mm, "end": v(-4.36, -169.7) * mm});
            skLineSegment(sketch, "E2723", {"start": v(-4.36, -169.7) * mm, "end": v(-4.75, -168.77) * mm});
            skLineSegment(sketch, "E2724", {"start": v(-4.75, -168.77) * mm, "end": v(-5.37, -168) * mm});
            skLineSegment(sketch, "E2725", {"start": v(-5.37, -168) * mm, "end": v(-6.25, -167.41) * mm});
            skLineSegment(sketch, "E2726", {"start": v(-6.25, -167.41) * mm, "end": v(-7.42, -167.01) * mm});
            skLineSegment(sketch, "E2727", {"start": v(-7.42, -167.01) * mm, "end": v(-8.94, -166.83) * mm});
            skLineSegment(sketch, "E2728", {"start": v(-8.94, -166.83) * mm, "end": v(-10.45, -166.91) * mm});
            skLineSegment(sketch, "E2729", {"start": v(-10.45, -166.91) * mm, "end": v(-11.53, -167.28) * mm});
            skLineSegment(sketch, "E2730", {"start": v(-11.53, -167.28) * mm, "end": v(-12.27, -167.89) * mm});
            skLineSegment(sketch, "E2731", {"start": v(-12.27, -167.89) * mm, "end": v(-12.73, -168.68) * mm});
            skLineSegment(sketch, "E2732", {"start": v(-12.73, -168.68) * mm, "end": v(-12.97, -169.6) * mm});
            skLineSegment(sketch, "E2733", {"start": v(-12.97, -169.6) * mm, "end": v(-13.07, -170.59) * mm});
            skLineSegment(sketch, "E2734", {"start": v(-13.07, -170.59) * mm, "end": v(-13.1, -171.6) * mm});
            skLineSegment(sketch, "E2735", {"start": v(-13.1, -171.6) * mm, "end": v(-13.13, -172.6) * mm});
            skLineSegment(sketch, "E2736", {"start": v(-13.13, -172.6) * mm, "end": v(-13.33, -176.65) * mm});
            skLineSegment(sketch, "E2737", {"start": v(-13.33, -176.65) * mm, "end": v(-13.52, -180.7) * mm});
            skLineSegment(sketch, "E2738", {"start": v(-13.52, -180.7) * mm, "end": v(-13.69, -184.74) * mm});
            skLineSegment(sketch, "E2739", {"start": v(-13.69, -184.74) * mm, "end": v(-13.84, -188.8) * mm});
            skLineSegment(sketch, "E2740", {"start": v(-13.84, -188.8) * mm, "end": v(-14, -192.84) * mm});
            skLineSegment(sketch, "E2741", {"start": v(-14, -192.84) * mm, "end": v(-14.14, -196.9) * mm});
            skLineSegment(sketch, "E2742", {"start": v(-14.14, -196.9) * mm, "end": v(-14.3, -200.94) * mm});
            skLineSegment(sketch, "E2743", {"start": v(-14.3, -200.94) * mm, "end": v(-14.45, -204.99) * mm});
            skLineSegment(sketch, "E2744", {"start": v(-14.45, -204.99) * mm, "end": v(-14.48, -206.1) * mm});
            skLineSegment(sketch, "E2745", {"start": v(-14.48, -206.1) * mm, "end": v(-14.45, -207.15) * mm});
            skLineSegment(sketch, "E2746", {"start": v(-14.45, -207.15) * mm, "end": v(-14.3, -208.12) * mm});
            skLineSegment(sketch, "E2747", {"start": v(-14.3, -208.12) * mm, "end": v(-14, -208.97) * mm});
            skLineSegment(sketch, "E2748", {"start": v(-14, -208.97) * mm, "end": v(-13.5, -209.69) * mm});
            skLineSegment(sketch, "E2749", {"start": v(-13.5, -209.69) * mm, "end": v(-12.74, -210.24) * mm});
            skLineSegment(sketch, "E2750", {"start": v(-12.74, -210.24) * mm, "end": v(-11.68, -210.61) * mm});
            skLineSegment(sketch, "E2751", {"start": v(-11.68, -210.61) * mm, "end": v(-10.28, -210.76) * mm});
            skLineSegment(sketch, "E2752", {"start": v(-10.28, -210.76) * mm, "end": v(-8.87, -210.7) * mm});
            skLineSegment(sketch, "E2753", {"start": v(-8.87, -210.7) * mm, "end": v(-7.74, -210.41) * mm});
            skLineSegment(sketch, "E2754", {"start": v(-7.74, -210.41) * mm, "end": v(-6.85, -209.93) * mm});
            skLineSegment(sketch, "E2755", {"start": v(-6.85, -209.93) * mm, "end": v(-6.19, -209.28) * mm});
            skLineSegment(sketch, "E2756", {"start": v(-6.19, -209.28) * mm, "end": v(-5.72, -208.45) * mm});
            skLineSegment(sketch, "E2757", {"start": v(-5.72, -208.45) * mm, "end": v(-5.4, -207.48) * mm});
            skLineSegment(sketch, "E2758", {"start": v(-5.4, -207.48) * mm, "end": v(-5.24, -206.36) * mm});
            skLineSegment(sketch, "E2759", {"start": v(-5.24, -206.36) * mm, "end": v(-5.18, -205.12) * mm});
            skLineSegment(sketch, "E2760", {"start": v(-5.18, -205.12) * mm, "end": v(-5.15, -201.5) * mm});
            skLineSegment(sketch, "E2761", {"start": v(-5.15, -201.5) * mm, "end": v(-5.12, -197.9) * mm});
            skLineSegment(sketch, "E2762", {"start": v(-5.12, -197.9) * mm, "end": v(-5.08, -194.3) * mm});
            skLineSegment(sketch, "E2763", {"start": v(-5.08, -194.3) * mm, "end": v(-5.01, -190.72) * mm});
            skLineSegment(sketch, "E2764", {"start": v(-5.01, -190.72) * mm, "end": v(-4.9, -187.17) * mm});
            skLineSegment(sketch, "E2765", {"start": v(-4.9, -187.17) * mm, "end": v(-4.74, -183.65) * mm});
            skLineSegment(sketch, "E2766", {"start": v(-4.74, -183.65) * mm, "end": v(-4.5, -180.17) * mm});
            skLineSegment(sketch, "E2767", {"start": v(-4.5, -180.17) * mm, "end": v(-4.16, -176.73) * mm});
            skLineSegment(sketch, "E2768", {"start": v(26.05, 229.05) * mm, "end": v(28.82, 228.56) * mm});
            skLineSegment(sketch, "E2769", {"start": v(28.82, 228.56) * mm, "end": v(31.52, 228.1) * mm});
            skLineSegment(sketch, "E2770", {"start": v(31.52, 228.1) * mm, "end": v(34.14, 227.65) * mm});
            skLineSegment(sketch, "E2771", {"start": v(34.14, 227.65) * mm, "end": v(36.7, 227.22) * mm});
            skLineSegment(sketch, "E2772", {"start": v(36.7, 227.22) * mm, "end": v(39.2, 226.77) * mm});
            skLineSegment(sketch, "E2773", {"start": v(39.2, 226.77) * mm, "end": v(41.67, 226.32) * mm});
            skLineSegment(sketch, "E2774", {"start": v(41.67, 226.32) * mm, "end": v(44.1, 225.84) * mm});
            skLineSegment(sketch, "E2775", {"start": v(44.1, 225.84) * mm, "end": v(46.53, 225.33) * mm});
            skLineSegment(sketch, "E2776", {"start": v(46.53, 225.33) * mm, "end": v(49.02, 224.76) * mm});
            skLineSegment(sketch, "E2777", {"start": v(49.02, 224.76) * mm, "end": v(51.5, 224.16) * mm});
            skLineSegment(sketch, "E2778", {"start": v(51.5, 224.16) * mm, "end": v(53.97, 223.52) * mm});
            skLineSegment(sketch, "E2779", {"start": v(53.97, 223.52) * mm, "end": v(56.45, 222.87) * mm});
            skLineSegment(sketch, "E2780", {"start": v(56.45, 222.87) * mm, "end": v(58.92, 222.21) * mm});
            skLineSegment(sketch, "E2781", {"start": v(58.92, 222.21) * mm, "end": v(61.39, 221.56) * mm});
            skLineSegment(sketch, "E2782", {"start": v(61.39, 221.56) * mm, "end": v(63.86, 220.92) * mm});
            skLineSegment(sketch, "E2783", {"start": v(63.86, 220.92) * mm, "end": v(66.34, 220.3) * mm});
            skLineSegment(sketch, "E2784", {"start": v(66.34, 220.3) * mm, "end": v(67.24, 220) * mm});
            skLineSegment(sketch, "E2785", {"start": v(67.24, 220) * mm, "end": v(68.16, 219.6) * mm});
            skLineSegment(sketch, "E2786", {"start": v(68.16, 219.6) * mm, "end": v(69.09, 219.15) * mm});
            skLineSegment(sketch, "E2787", {"start": v(69.09, 219.15) * mm, "end": v(70, 218.75) * mm});
            skLineSegment(sketch, "E2788", {"start": v(70, 218.75) * mm, "end": v(70.9, 218.47) * mm});
            skLineSegment(sketch, "E2789", {"start": v(70.9, 218.47) * mm, "end": v(71.73, 218.38) * mm});
            skLineSegment(sketch, "E2790", {"start": v(71.73, 218.38) * mm, "end": v(72.5, 218.55) * mm});
            skLineSegment(sketch, "E2791", {"start": v(72.5, 218.55) * mm, "end": v(73.19, 219.08) * mm});
            skLineSegment(sketch, "E2792", {"start": v(73.19, 219.08) * mm, "end": v(73.65, 219.87) * mm});
            skLineSegment(sketch, "E2793", {"start": v(73.65, 219.87) * mm, "end": v(73.8, 220.73) * mm});
            skLineSegment(sketch, "E2794", {"start": v(73.8, 220.73) * mm, "end": v(73.7, 221.65) * mm});
            skLineSegment(sketch, "E2795", {"start": v(73.7, 221.65) * mm, "end": v(73.42, 222.6) * mm});
            skLineSegment(sketch, "E2796", {"start": v(73.42, 222.6) * mm, "end": v(73.02, 223.6) * mm});
            skLineSegment(sketch, "E2797", {"start": v(73.02, 223.6) * mm, "end": v(72.56, 224.58) * mm});
            skLineSegment(sketch, "E2798", {"start": v(72.56, 224.58) * mm, "end": v(72.12, 225.55) * mm});
            skLineSegment(sketch, "E2799", {"start": v(72.12, 225.55) * mm, "end": v(71.77, 226.5) * mm});
            skLineSegment(sketch, "E2800", {"start": v(71.77, 226.5) * mm, "end": v(71.37, 227.58) * mm});
            skLineSegment(sketch, "E2801", {"start": v(71.37, 227.58) * mm, "end": v(70.94, 228.35) * mm});
            skLineSegment(sketch, "E2802", {"start": v(70.94, 228.35) * mm, "end": v(70.47, 228.83) * mm});
            skLineSegment(sketch, "E2803", {"start": v(70.47, 228.83) * mm, "end": v(69.95, 229.02) * mm});
            skLineSegment(sketch, "E2804", {"start": v(69.95, 229.02) * mm, "end": v(69.36, 228.95) * mm});
            skLineSegment(sketch, "E2805", {"start": v(69.36, 228.95) * mm, "end": v(68.7, 228.61) * mm});
            skLineSegment(sketch, "E2806", {"start": v(68.7, 228.61) * mm, "end": v(67.97, 228.03) * mm});
            skLineSegment(sketch, "E2807", {"start": v(67.97, 228.03) * mm, "end": v(67.14, 227.2) * mm});
            skLineSegment(sketch, "E2808", {"start": v(67.14, 227.2) * mm, "end": v(65.67, 225.88) * mm});
            skLineSegment(sketch, "E2809", {"start": v(65.67, 225.88) * mm, "end": v(64.1, 224.89) * mm});
            skLineSegment(sketch, "E2810", {"start": v(64.1, 224.89) * mm, "end": v(62.46, 224.22) * mm});
            skLineSegment(sketch, "E2811", {"start": v(62.46, 224.22) * mm, "end": v(60.76, 223.88) * mm});
            skLineSegment(sketch, "E2812", {"start": v(60.76, 223.88) * mm, "end": v(59.04, 223.86) * mm});
            skLineSegment(sketch, "E2813", {"start": v(59.04, 223.86) * mm, "end": v(57.31, 224.15) * mm});
            skLineSegment(sketch, "E2814", {"start": v(57.31, 224.15) * mm, "end": v(55.6, 224.75) * mm});
            skLineSegment(sketch, "E2815", {"start": v(55.6, 224.75) * mm, "end": v(53.95, 225.66) * mm});
            skLineSegment(sketch, "E2816", {"start": v(53.95, 225.66) * mm, "end": v(53.2, 226.17) * mm});
            skLineSegment(sketch, "E2817", {"start": v(53.2, 226.17) * mm, "end": v(52.52, 226.72) * mm});
            skLineSegment(sketch, "E2818", {"start": v(52.52, 226.72) * mm, "end": v(51.91, 227.33) * mm});
            skLineSegment(sketch, "E2819", {"start": v(51.91, 227.33) * mm, "end": v(51.4, 228) * mm});
            skLineSegment(sketch, "E2820", {"start": v(51.4, 228) * mm, "end": v(50.98, 228.72) * mm});
            skLineSegment(sketch, "E2821", {"start": v(50.98, 228.72) * mm, "end": v(50.7, 229.51) * mm});
            skLineSegment(sketch, "E2822", {"start": v(50.7, 229.51) * mm, "end": v(50.57, 230.38) * mm});
            skLineSegment(sketch, "E2823", {"start": v(50.57, 230.38) * mm, "end": v(50.6, 231.34) * mm});
            skLineSegment(sketch, "E2824", {"start": v(50.6, 231.34) * mm, "end": v(50.73, 232.05) * mm});
            skLineSegment(sketch, "E2825", {"start": v(50.73, 232.05) * mm, "end": v(50.94, 232.71) * mm});
            skLineSegment(sketch, "E2826", {"start": v(50.94, 232.71) * mm, "end": v(51.21, 233.32) * mm});
            skLineSegment(sketch, "E2827", {"start": v(51.21, 233.32) * mm, "end": v(51.57, 233.88) * mm});
            skLineSegment(sketch, "E2828", {"start": v(51.57, 233.88) * mm, "end": v(52.01, 234.37) * mm});
            skLineSegment(sketch, "E2829", {"start": v(52.01, 234.37) * mm, "end": v(52.54, 234.79) * mm});
            skLineSegment(sketch, "E2830", {"start": v(52.54, 234.79) * mm, "end": v(53.15, 235.13) * mm});
            skLineSegment(sketch, "E2831", {"start": v(53.15, 235.13) * mm, "end": v(53.84, 235.39) * mm});
            skLineSegment(sketch, "E2832", {"start": v(53.84, 235.39) * mm, "end": v(54.71, 235.58) * mm});
            skLineSegment(sketch, "E2833", {"start": v(54.71, 235.58) * mm, "end": v(55.53, 235.62) * mm});
            skLineSegment(sketch, "E2834", {"start": v(55.53, 235.62) * mm, "end": v(56.3, 235.53) * mm});
            skLineSegment(sketch, "E2835", {"start": v(56.3, 235.53) * mm, "end": v(57.01, 235.3) * mm});
            skLineSegment(sketch, "E2836", {"start": v(57.01, 235.3) * mm, "end": v(57.68, 234.95) * mm});
            skLineSegment(sketch, "E2837", {"start": v(57.68, 234.95) * mm, "end": v(58.29, 234.47) * mm});
            skLineSegment(sketch, "E2838", {"start": v(58.29, 234.47) * mm, "end": v(58.85, 233.85) * mm});
            skLineSegment(sketch, "E2839", {"start": v(58.85, 233.85) * mm, "end": v(59.35, 233.12) * mm});
            skLineSegment(sketch, "E2840", {"start": v(59.35, 233.12) * mm, "end": v(59.56, 232.78) * mm});
            skLineSegment(sketch, "E2841", {"start": v(59.56, 232.78) * mm, "end": v(59.79, 232.47) * mm});
            skLineSegment(sketch, "E2842", {"start": v(59.79, 232.47) * mm, "end": v(60.04, 232.2) * mm});
            skLineSegment(sketch, "E2843", {"start": v(60.04, 232.2) * mm, "end": v(60.3, 231.98) * mm});
            skLineSegment(sketch, "E2844", {"start": v(60.3, 231.98) * mm, "end": v(60.6, 231.85) * mm});
            skLineSegment(sketch, "E2845", {"start": v(60.6, 231.85) * mm, "end": v(60.93, 231.82) * mm});
            skLineSegment(sketch, "E2846", {"start": v(60.93, 231.82) * mm, "end": v(61.3, 231.9) * mm});
            skLineSegment(sketch, "E2847", {"start": v(61.3, 231.9) * mm, "end": v(61.7, 232.11) * mm});
            skLineSegment(sketch, "E2848", {"start": v(61.7, 232.11) * mm, "end": v(62.07, 232.42) * mm});
            skLineSegment(sketch, "E2849", {"start": v(62.07, 232.42) * mm, "end": v(62.35, 232.76) * mm});
            skLineSegment(sketch, "E2850", {"start": v(62.35, 232.76) * mm, "end": v(62.52, 233.14) * mm});
            skLineSegment(sketch, "E2851", {"start": v(62.52, 233.14) * mm, "end": v(62.6, 233.53) * mm});
            skLineSegment(sketch, "E2852", {"start": v(62.6, 233.53) * mm, "end": v(62.61, 233.95) * mm});
            skLineSegment(sketch, "E2853", {"start": v(62.61, 233.95) * mm, "end": v(62.55, 234.37) * mm});
            skLineSegment(sketch, "E2854", {"start": v(62.55, 234.37) * mm, "end": v(62.42, 234.8) * mm});
            skLineSegment(sketch, "E2855", {"start": v(62.42, 234.8) * mm, "end": v(62.23, 235.23) * mm});
            skLineSegment(sketch, "E2856", {"start": v(62.23, 235.23) * mm, "end": v(61.63, 236.28) * mm});
            skLineSegment(sketch, "E2857", {"start": v(61.63, 236.28) * mm, "end": v(60.94, 237.18) * mm});
            skLineSegment(sketch, "E2858", {"start": v(60.94, 237.18) * mm, "end": v(60.15, 237.93) * mm});
            skLineSegment(sketch, "E2859", {"start": v(60.15, 237.93) * mm, "end": v(59.28, 238.55) * mm});
            skLineSegment(sketch, "E2860", {"start": v(59.28, 238.55) * mm, "end": v(58.32, 239.03) * mm});
            skLineSegment(sketch, "E2861", {"start": v(58.32, 239.03) * mm, "end": v(57.3, 239.4) * mm});
            skLineSegment(sketch, "E2862", {"start": v(57.3, 239.4) * mm, "end": v(56.19, 239.65) * mm});
            skLineSegment(sketch, "E2863", {"start": v(56.19, 239.65) * mm, "end": v(55.01, 239.79) * mm});
            skLineSegment(sketch, "E2864", {"start": v(55.01, 239.79) * mm, "end": v(51, 239.83) * mm});
            skLineSegment(sketch, "E2865", {"start": v(51, 239.83) * mm, "end": v(47.15, 239.37) * mm});
            skLineSegment(sketch, "E2866", {"start": v(47.15, 239.37) * mm, "end": v(43.46, 238.46) * mm});
            skLineSegment(sketch, "E2867", {"start": v(43.46, 238.46) * mm, "end": v(39.88, 237.15) * mm});
            skLineSegment(sketch, "E2868", {"start": v(39.88, 237.15) * mm, "end": v(36.38, 235.5) * mm});
            skLineSegment(sketch, "E2869", {"start": v(36.38, 235.5) * mm, "end": v(32.93, 233.57) * mm});
            skLineSegment(sketch, "E2870", {"start": v(32.93, 233.57) * mm, "end": v(29.5, 231.4) * mm});
            skLineSegment(sketch, "E2871", {"start": v(29.5, 231.4) * mm, "end": v(26.05, 229.05) * mm});
            skLineSegment(sketch, "E2872", {"start": v(38.21, -230.97) * mm, "end": v(38.74, -231.1) * mm});
            skLineSegment(sketch, "E2873", {"start": v(38.74, -231.1) * mm, "end": v(39.19, -231.23) * mm});
            skLineSegment(sketch, "E2874", {"start": v(39.19, -231.23) * mm, "end": v(39.55, -231.33) * mm});
            skLineSegment(sketch, "E2875", {"start": v(39.55, -231.33) * mm, "end": v(39.85, -231.42) * mm});
            skLineSegment(sketch, "E2876", {"start": v(39.85, -231.42) * mm, "end": v(40.1, -231.49) * mm});
            skLineSegment(sketch, "E2877", {"start": v(40.1, -231.49) * mm, "end": v(40.32, -231.54) * mm});
            skLineSegment(sketch, "E2878", {"start": v(40.32, -231.54) * mm, "end": v(40.5, -231.57) * mm});
            skLineSegment(sketch, "E2879", {"start": v(40.5, -231.57) * mm, "end": v(40.68, -231.58) * mm});
            skLineSegment(sketch, "E2880", {"start": v(40.68, -231.58) * mm, "end": v(41.47, -231.53) * mm});
            skLineSegment(sketch, "E2881", {"start": v(41.47, -231.53) * mm, "end": v(42.3, -231.45) * mm});
            skLineSegment(sketch, "E2882", {"start": v(42.3, -231.45) * mm, "end": v(43.13, -231.39) * mm});
            skLineSegment(sketch, "E2883", {"start": v(43.13, -231.39) * mm, "end": v(43.9, -231.43) * mm});
            skLineSegment(sketch, "E2884", {"start": v(43.9, -231.43) * mm, "end": v(44.56, -231.63) * mm});
            skLineSegment(sketch, "E2885", {"start": v(44.56, -231.63) * mm, "end": v(45.08, -232.07) * mm});
            skLineSegment(sketch, "E2886", {"start": v(45.08, -232.07) * mm, "end": v(45.4, -232.8) * mm});
            skLineSegment(sketch, "E2887", {"start": v(45.4, -232.8) * mm, "end": v(45.48, -233.9) * mm});
            skLineSegment(sketch, "E2888", {"start": v(45.48, -233.9) * mm, "end": v(45.3, -235.02) * mm});
            skLineSegment(sketch, "E2889", {"start": v(45.3, -235.02) * mm, "end": v(44.9, -235.86) * mm});
            skLineSegment(sketch, "E2890", {"start": v(44.9, -235.86) * mm, "end": v(44.3, -236.48) * mm});
            skLineSegment(sketch, "E2891", {"start": v(44.3, -236.48) * mm, "end": v(43.56, -236.89) * mm});
            skLineSegment(sketch, "E2892", {"start": v(43.56, -236.89) * mm, "end": v(42.7, -237.13) * mm});
            skLineSegment(sketch, "E2893", {"start": v(42.7, -237.13) * mm, "end": v(41.77, -237.22) * mm});
            skLineSegment(sketch, "E2894", {"start": v(41.77, -237.22) * mm, "end": v(40.8, -237.2) * mm});
            skLineSegment(sketch, "E2895", {"start": v(40.8, -237.2) * mm, "end": v(39.82, -237.1) * mm});
            skLineSegment(sketch, "E2896", {"start": v(39.82, -237.1) * mm, "end": v(38.82, -236.9) * mm});
            skLineSegment(sketch, "E2897", {"start": v(38.82, -236.9) * mm, "end": v(37.88, -236.6) * mm});
            skLineSegment(sketch, "E2898", {"start": v(37.88, -236.6) * mm, "end": v(36.98, -236.2) * mm});
            skLineSegment(sketch, "E2899", {"start": v(36.98, -236.2) * mm, "end": v(36.11, -235.72) * mm});
            skLineSegment(sketch, "E2900", {"start": v(36.11, -235.72) * mm, "end": v(35.28, -235.18) * mm});
            skLineSegment(sketch, "E2901", {"start": v(35.28, -235.18) * mm, "end": v(34.46, -234.6) * mm});
            skLineSegment(sketch, "E2902", {"start": v(34.46, -234.6) * mm, "end": v(33.67, -233.98) * mm});
            skLineSegment(sketch, "E2903", {"start": v(33.67, -233.98) * mm, "end": v(32.88, -233.35) * mm});
            skLineSegment(sketch, "E2904", {"start": v(32.88, -233.35) * mm, "end": v(32.44, -232.99) * mm});
            skLineSegment(sketch, "E2905", {"start": v(32.44, -232.99) * mm, "end": v(31.98, -232.6) * mm});
            skLineSegment(sketch, "E2906", {"start": v(31.98, -232.6) * mm, "end": v(31.51, -232.25) * mm});
            skLineSegment(sketch, "E2907", {"start": v(31.51, -232.25) * mm, "end": v(31.02, -231.96) * mm});
            skLineSegment(sketch, "E2908", {"start": v(31.02, -231.96) * mm, "end": v(30.53, -231.8) * mm});
            skLineSegment(sketch, "E2909", {"start": v(30.53, -231.8) * mm, "end": v(30.04, -231.8) * mm});
            skLineSegment(sketch, "E2910", {"start": v(30.04, -231.8) * mm, "end": v(29.55, -232) * mm});
            skLineSegment(sketch, "E2911", {"start": v(29.55, -232) * mm, "end": v(29.08, -232.47) * mm});
            skLineSegment(sketch, "E2912", {"start": v(29.08, -232.47) * mm, "end": v(28.8, -232.98) * mm});
            skLineSegment(sketch, "E2913", {"start": v(28.8, -232.98) * mm, "end": v(28.77, -233.44) * mm});
            skLineSegment(sketch, "E2914", {"start": v(28.77, -233.44) * mm, "end": v(28.92, -233.85) * mm});
            skLineSegment(sketch, "E2915", {"start": v(28.92, -233.85) * mm, "end": v(29.22, -234.22) * mm});
            skLineSegment(sketch, "E2916", {"start": v(29.22, -234.22) * mm, "end": v(29.62, -234.56) * mm});
            skLineSegment(sketch, "E2917", {"start": v(29.62, -234.56) * mm, "end": v(30.06, -234.88) * mm});
            skLineSegment(sketch, "E2918", {"start": v(30.06, -234.88) * mm, "end": v(30.5, -235.18) * mm});
            skLineSegment(sketch, "E2919", {"start": v(30.5, -235.18) * mm, "end": v(30.88, -235.47) * mm});
            skLineSegment(sketch, "E2920", {"start": v(30.88, -235.47) * mm, "end": v(35.37, -238.4) * mm});
            skLineSegment(sketch, "E2921", {"start": v(35.37, -238.4) * mm, "end": v(40.23, -240.15) * mm});
            skLineSegment(sketch, "E2922", {"start": v(40.23, -240.15) * mm, "end": v(45.27, -240.79) * mm});
            skLineSegment(sketch, "E2923", {"start": v(45.27, -240.79) * mm, "end": v(50.3, -240.34) * mm});
            skLineSegment(sketch, "E2924", {"start": v(50.3, -240.34) * mm, "end": v(55.11, -238.84) * mm});
            skLineSegment(sketch, "E2925", {"start": v(55.11, -238.84) * mm, "end": v(59.53, -236.33) * mm});
            skLineSegment(sketch, "E2926", {"start": v(59.53, -236.33) * mm, "end": v(63.35, -232.86) * mm});
            skLineSegment(sketch, "E2927", {"start": v(63.35, -232.86) * mm, "end": v(66.38, -228.45) * mm});
            skLineSegment(sketch, "E2928", {"start": v(66.38, -228.45) * mm, "end": v(66.6, -228.08) * mm});
            skLineSegment(sketch, "E2929", {"start": v(66.6, -228.08) * mm, "end": v(66.83, -227.7) * mm});
            skLineSegment(sketch, "E2930", {"start": v(66.83, -227.7) * mm, "end": v(67.05, -227.33) * mm});
            skLineSegment(sketch, "E2931", {"start": v(67.05, -227.33) * mm, "end": v(67.24, -226.94) * mm});
            skLineSegment(sketch, "E2932", {"start": v(67.24, -226.94) * mm, "end": v(67.36, -226.54) * mm});
            skLineSegment(sketch, "E2933", {"start": v(67.36, -226.54) * mm, "end": v(67.37, -226.14) * mm});
            skLineSegment(sketch, "E2934", {"start": v(67.37, -226.14) * mm, "end": v(67.26, -225.73) * mm});
            skLineSegment(sketch, "E2935", {"start": v(67.26, -225.73) * mm, "end": v(66.98, -225.3) * mm});
            skLineSegment(sketch, "E2936", {"start": v(66.98, -225.3) * mm, "end": v(66.68, -225.03) * mm});
            skLineSegment(sketch, "E2937", {"start": v(66.68, -225.03) * mm, "end": v(66.35, -224.89) * mm});
            skLineSegment(sketch, "E2938", {"start": v(66.35, -224.89) * mm, "end": v(66, -224.84) * mm});
            skLineSegment(sketch, "E2939", {"start": v(66, -224.84) * mm, "end": v(65.63, -224.86) * mm});
            skLineSegment(sketch, "E2940", {"start": v(65.63, -224.86) * mm, "end": v(65.26, -224.94) * mm});
            skLineSegment(sketch, "E2941", {"start": v(65.26, -224.94) * mm, "end": v(64.88, -225.05) * mm});
            skLineSegment(sketch, "E2942", {"start": v(64.88, -225.05) * mm, "end": v(64.52, -225.16) * mm});
            skLineSegment(sketch, "E2943", {"start": v(64.52, -225.16) * mm, "end": v(64.16, -225.25) * mm});
            skLineSegment(sketch, "E2944", {"start": v(64.16, -225.25) * mm, "end": v(61.06, -225.93) * mm});
            skLineSegment(sketch, "E2945", {"start": v(61.06, -225.93) * mm, "end": v(57.94, -226.61) * mm});
            skLineSegment(sketch, "E2946", {"start": v(57.94, -226.61) * mm, "end": v(54.8, -227.3) * mm});
            skLineSegment(sketch, "E2947", {"start": v(54.8, -227.3) * mm, "end": v(51.61, -228) * mm});
            skLineSegment(sketch, "E2948", {"start": v(51.61, -228) * mm, "end": v(48.38, -228.72) * mm});
            skLineSegment(sketch, "E2949", {"start": v(48.38, -228.72) * mm, "end": v(45.07, -229.45) * mm});
            skLineSegment(sketch, "E2950", {"start": v(45.07, -229.45) * mm, "end": v(41.69, -230.2) * mm});
            skLineSegment(sketch, "E2951", {"start": v(41.69, -230.2) * mm, "end": v(38.21, -230.97) * mm});
            skLineSegment(sketch, "E2952", {"start": v(-65.1, -225.08) * mm, "end": v(-63.63, -228.5) * mm});
            skLineSegment(sketch, "E2953", {"start": v(-63.63, -228.5) * mm, "end": v(-61.85, -231.51) * mm});
            skLineSegment(sketch, "E2954", {"start": v(-61.85, -231.51) * mm, "end": v(-59.79, -234.13) * mm});
            skLineSegment(sketch, "E2955", {"start": v(-59.79, -234.13) * mm, "end": v(-57.46, -236.34) * mm});
            skLineSegment(sketch, "E2956", {"start": v(-57.46, -236.34) * mm, "end": v(-54.9, -238.1) * mm});
            skLineSegment(sketch, "E2957", {"start": v(-54.9, -238.1) * mm, "end": v(-52.14, -239.44) * mm});
            skLineSegment(sketch, "E2958", {"start": v(-52.14, -239.44) * mm, "end": v(-49.2, -240.31) * mm});
            skLineSegment(sketch, "E2959", {"start": v(-49.2, -240.31) * mm, "end": v(-46.1, -240.71) * mm});
            skLineSegment(sketch, "E2960", {"start": v(-46.1, -240.71) * mm, "end": v(-42.94, -240.7) * mm});
            skLineSegment(sketch, "E2961", {"start": v(-42.94, -240.7) * mm, "end": v(-39.9, -240.37) * mm});
            skLineSegment(sketch, "E2962", {"start": v(-39.9, -240.37) * mm, "end": v(-37.04, -239.72) * mm});
            skLineSegment(sketch, "E2963", {"start": v(-37.04, -239.72) * mm, "end": v(-34.42, -238.77) * mm});
            skLineSegment(sketch, "E2964", {"start": v(-34.42, -238.77) * mm, "end": v(-32.08, -237.56) * mm});
            skLineSegment(sketch, "E2965", {"start": v(-32.08, -237.56) * mm, "end": v(-30.08, -236.1) * mm});
            skLineSegment(sketch, "E2966", {"start": v(-30.08, -236.1) * mm, "end": v(-28.47, -234.4) * mm});
            skLineSegment(sketch, "E2967", {"start": v(-28.47, -234.4) * mm, "end": v(-27.3, -232.5) * mm});
            skLineSegment(sketch, "E2968", {"start": v(-27.3, -232.5) * mm, "end": v(-28.73, -232.7) * mm});
            skLineSegment(sketch, "E2969", {"start": v(-28.73, -232.7) * mm, "end": v(-30.02, -233.18) * mm});
            skLineSegment(sketch, "E2970", {"start": v(-30.02, -233.18) * mm, "end": v(-31.21, -233.83) * mm});
            skLineSegment(sketch, "E2971", {"start": v(-31.21, -233.83) * mm, "end": v(-32.35, -234.58) * mm});
            skLineSegment(sketch, "E2972", {"start": v(-32.35, -234.58) * mm, "end": v(-33.47, -235.36) * mm});
            skLineSegment(sketch, "E2973", {"start": v(-33.47, -235.36) * mm, "end": v(-34.6, -236.07) * mm});
            skLineSegment(sketch, "E2974", {"start": v(-34.6, -236.07) * mm, "end": v(-35.8, -236.63) * mm});
            skLineSegment(sketch, "E2975", {"start": v(-35.8, -236.63) * mm, "end": v(-37.1, -236.97) * mm});
            skLineSegment(sketch, "E2976", {"start": v(-37.1, -236.97) * mm, "end": v(-37.87, -237.06) * mm});
            skLineSegment(sketch, "E2977", {"start": v(-37.87, -237.06) * mm, "end": v(-38.63, -237.08) * mm});
            skLineSegment(sketch, "E2978", {"start": v(-38.63, -237.08) * mm, "end": v(-39.36, -237.02) * mm});
            skLineSegment(sketch, "E2979", {"start": v(-39.36, -237.02) * mm, "end": v(-40.06, -236.89) * mm});
            skLineSegment(sketch, "E2980", {"start": v(-40.06, -236.89) * mm, "end": v(-40.74, -236.67) * mm});
            skLineSegment(sketch, "E2981", {"start": v(-40.74, -236.67) * mm, "end": v(-41.39, -236.35) * mm});
            skLineSegment(sketch, "E2982", {"start": v(-41.39, -236.35) * mm, "end": v(-42, -235.94) * mm});
            skLineSegment(sketch, "E2983", {"start": v(-42, -235.94) * mm, "end": v(-42.6, -235.43) * mm});
            skLineSegment(sketch, "E2984", {"start": v(-42.6, -235.43) * mm, "end": v(-42.85, -235.13) * mm});
            skLineSegment(sketch, "E2985", {"start": v(-42.85, -235.13) * mm, "end": v(-43.06, -234.81) * mm});
            skLineSegment(sketch, "E2986", {"start": v(-43.06, -234.81) * mm, "end": v(-43.2, -234.48) * mm});
            skLineSegment(sketch, "E2987", {"start": v(-43.2, -234.48) * mm, "end": v(-43.3, -234.14) * mm});
            skLineSegment(sketch, "E2988", {"start": v(-43.3, -234.14) * mm, "end": v(-43.32, -233.78) * mm});
            skLineSegment(sketch, "E2989", {"start": v(-43.32, -233.78) * mm, "end": v(-43.3, -233.42) * mm});
            skLineSegment(sketch, "E2990", {"start": v(-43.3, -233.42) * mm, "end": v(-43.2, -233.05) * mm});
            skLineSegment(sketch, "E2991", {"start": v(-43.2, -233.05) * mm, "end": v(-43.06, -232.67) * mm});
            skLineSegment(sketch, "E2992", {"start": v(-43.06, -232.67) * mm, "end": v(-42.6, -231.96) * mm});
            skLineSegment(sketch, "E2993", {"start": v(-42.6, -231.96) * mm, "end": v(-42.07, -231.52) * mm});
            skLineSegment(sketch, "E2994", {"start": v(-42.07, -231.52) * mm, "end": v(-41.48, -231.3) * mm});
            skLineSegment(sketch, "E2995", {"start": v(-41.48, -231.3) * mm, "end": v(-40.85, -231.25) * mm});
            skLineSegment(sketch, "E2996", {"start": v(-40.85, -231.25) * mm, "end": v(-40.2, -231.3) * mm});
            skLineSegment(sketch, "E2997", {"start": v(-40.2, -231.3) * mm, "end": v(-39.53, -231.39) * mm});
            skLineSegment(sketch, "E2998", {"start": v(-39.53, -231.39) * mm, "end": v(-38.87, -231.45) * mm});
            skLineSegment(sketch, "E2999", {"start": v(-38.87, -231.45) * mm, "end": v(-38.22, -231.45) * mm});
            skLineSegment(sketch, "E3000", {"start": v(-38.22, -231.45) * mm, "end": v(-38.17, -231.42) * mm});
            skLineSegment(sketch, "E3001", {"start": v(-38.17, -231.42) * mm, "end": v(-38.12, -231.36) * mm});
            skLineSegment(sketch, "E3002", {"start": v(-38.12, -231.36) * mm, "end": v(-38.07, -231.28) * mm});
            skLineSegment(sketch, "E3003", {"start": v(-38.07, -231.28) * mm, "end": v(-38.01, -231.17) * mm});
            skLineSegment(sketch, "E3004", {"start": v(-38.01, -231.17) * mm, "end": v(-37.96, -231.04) * mm});
            skLineSegment(sketch, "E3005", {"start": v(-37.96, -231.04) * mm, "end": v(-37.9, -230.9) * mm});
            skLineSegment(sketch, "E3006", {"start": v(-37.9, -230.9) * mm, "end": v(-37.83, -230.75) * mm});
            skLineSegment(sketch, "E3007", {"start": v(-37.83, -230.75) * mm, "end": v(-37.75, -230.6) * mm});
            skLineSegment(sketch, "E3008", {"start": v(-37.75, -230.6) * mm, "end": v(-41.13, -230.1) * mm});
            skLineSegment(sketch, "E3009", {"start": v(-41.13, -230.1) * mm, "end": v(-44.5, -229.52) * mm});
            skLineSegment(sketch, "E3010", {"start": v(-44.5, -229.52) * mm, "end": v(-47.87, -228.87) * mm});
            skLineSegment(sketch, "E3011", {"start": v(-47.87, -228.87) * mm, "end": v(-51.25, -228.16) * mm});
            skLineSegment(sketch, "E3012", {"start": v(-51.25, -228.16) * mm, "end": v(-54.65, -227.42) * mm});
            skLineSegment(sketch, "E3013", {"start": v(-54.65, -227.42) * mm, "end": v(-58.08, -226.64) * mm});
            skLineSegment(sketch, "E3014", {"start": v(-58.08, -226.64) * mm, "end": v(-61.56, -225.86) * mm});
            skLineSegment(sketch, "E3015", {"start": v(-61.56, -225.86) * mm, "end": v(-65.1, -225.08) * mm});
            skLineSegment(sketch, "E3016", {"start": v(8.27, -233.73) * mm, "end": v(8.26, -233.67) * mm});
            skLineSegment(sketch, "E3017", {"start": v(8.26, -233.67) * mm, "end": v(8.25, -233.6) * mm});
            skLineSegment(sketch, "E3018", {"start": v(8.25, -233.6) * mm, "end": v(8.24, -233.55) * mm});
            skLineSegment(sketch, "E3019", {"start": v(8.24, -233.55) * mm, "end": v(8.23, -233.49) * mm});
            skLineSegment(sketch, "E3020", {"start": v(8.23, -233.49) * mm, "end": v(8.21, -233.42) * mm});
            skLineSegment(sketch, "E3021", {"start": v(8.21, -233.42) * mm, "end": v(8.2, -233.36) * mm});
            skLineSegment(sketch, "E3022", {"start": v(8.2, -233.36) * mm, "end": v(8.2, -233.3) * mm});
            skLineSegment(sketch, "E3023", {"start": v(8.2, -233.3) * mm, "end": v(8.18, -233.24) * mm});
            skLineSegment(sketch, "E3024", {"start": v(8.18, -233.24) * mm, "end": v(5.5, -233.24) * mm});
            skLineSegment(sketch, "E3025", {"start": v(5.5, -233.24) * mm, "end": v(2.83, -233.25) * mm});
            skLineSegment(sketch, "E3026", {"start": v(2.83, -233.25) * mm, "end": v(0.15, -233.25) * mm});
            skLineSegment(sketch, "E3027", {"start": v(0.15, -233.25) * mm, "end": v(-2.53, -233.26) * mm});
            skLineSegment(sketch, "E3028", {"start": v(-2.53, -233.26) * mm, "end": v(-5.2, -233.26) * mm});
            skLineSegment(sketch, "E3029", {"start": v(-5.2, -233.26) * mm, "end": v(-7.88, -233.25) * mm});
            skLineSegment(sketch, "E3030", {"start": v(-7.88, -233.25) * mm, "end": v(-10.56, -233.24) * mm});
            skLineSegment(sketch, "E3031", {"start": v(-10.56, -233.24) * mm, "end": v(-13.24, -233.22) * mm});
            skLineSegment(sketch, "E3032", {"start": v(-13.24, -233.22) * mm, "end": v(-14.37, -233.27) * mm});
            skLineSegment(sketch, "E3033", {"start": v(-14.37, -233.27) * mm, "end": v(-15.23, -233.42) * mm});
            skLineSegment(sketch, "E3034", {"start": v(-15.23, -233.42) * mm, "end": v(-15.83, -233.7) * mm});
            skLineSegment(sketch, "E3035", {"start": v(-15.83, -233.7) * mm, "end": v(-16.17, -234.1) * mm});
            skLineSegment(sketch, "E3036", {"start": v(-16.17, -234.1) * mm, "end": v(-16.27, -234.62) * mm});
            skLineSegment(sketch, "E3037", {"start": v(-16.27, -234.62) * mm, "end": v(-16.12, -235.27) * mm});
            skLineSegment(sketch, "E3038", {"start": v(-16.12, -235.27) * mm, "end": v(-15.75, -236.06) * mm});
            skLineSegment(sketch, "E3039", {"start": v(-15.75, -236.06) * mm, "end": v(-15.15, -237) * mm});
            skLineSegment(sketch, "E3040", {"start": v(-15.15, -237) * mm, "end": v(-13.83, -238.73) * mm});
            skLineSegment(sketch, "E3041", {"start": v(-13.83, -238.73) * mm, "end": v(-12.4, -240.31) * mm});
            skLineSegment(sketch, "E3042", {"start": v(-12.4, -240.31) * mm, "end": v(-10.89, -241.74) * mm});
            skLineSegment(sketch, "E3043", {"start": v(-10.89, -241.74) * mm, "end": v(-9.26, -243) * mm});
            skLineSegment(sketch, "E3044", {"start": v(-9.26, -243) * mm, "end": v(-7.5, -244.08) * mm});
            skLineSegment(sketch, "E3045", {"start": v(-7.5, -244.08) * mm, "end": v(-5.64, -244.98) * mm});
            skLineSegment(sketch, "E3046", {"start": v(-5.64, -244.98) * mm, "end": v(-3.63, -245.7) * mm});
            skLineSegment(sketch, "E3047", {"start": v(-3.63, -245.7) * mm, "end": v(-1.5, -246.22) * mm});
            skLineSegment(sketch, "E3048", {"start": v(-1.5, -246.22) * mm, "end": v(1.58, -246.44) * mm});
            skLineSegment(sketch, "E3049", {"start": v(1.58, -246.44) * mm, "end": v(4.7, -246) * mm});
            skLineSegment(sketch, "E3050", {"start": v(4.7, -246) * mm, "end": v(7.75, -244.98) * mm});
            skLineSegment(sketch, "E3051", {"start": v(7.75, -244.98) * mm, "end": v(10.6, -243.45) * mm});
            skLineSegment(sketch, "E3052", {"start": v(10.6, -243.45) * mm, "end": v(13.15, -241.48) * mm});
            skLineSegment(sketch, "E3053", {"start": v(13.15, -241.48) * mm, "end": v(15.27, -239.14) * mm});
            skLineSegment(sketch, "E3054", {"start": v(15.27, -239.14) * mm, "end": v(16.83, -236.52) * mm});
            skLineSegment(sketch, "E3055", {"start": v(16.83, -236.52) * mm, "end": v(17.72, -233.67) * mm});
            skLineSegment(sketch, "E3056", {"start": v(17.72, -233.67) * mm, "end": v(17.08, -233.73) * mm});
            skLineSegment(sketch, "E3057", {"start": v(17.08, -233.73) * mm, "end": v(16.53, -233.91) * mm});
            skLineSegment(sketch, "E3058", {"start": v(16.53, -233.91) * mm, "end": v(16.07, -234.2) * mm});
            skLineSegment(sketch, "E3059", {"start": v(16.07, -234.2) * mm, "end": v(15.68, -234.55) * mm});
            skLineSegment(sketch, "E3060", {"start": v(15.68, -234.55) * mm, "end": v(15.33, -234.96) * mm});
            skLineSegment(sketch, "E3061", {"start": v(15.33, -234.96) * mm, "end": v(15, -235.4) * mm});
            skLineSegment(sketch, "E3062", {"start": v(15, -235.4) * mm, "end": v(14.7, -235.85) * mm});
            skLineSegment(sketch, "E3063", {"start": v(14.7, -235.85) * mm, "end": v(14.39, -236.28) * mm});
            skLineSegment(sketch, "E3064", {"start": v(14.39, -236.28) * mm, "end": v(13.76, -237.07) * mm});
            skLineSegment(sketch, "E3065", {"start": v(13.76, -237.07) * mm, "end": v(13.12, -237.84) * mm});
            skLineSegment(sketch, "E3066", {"start": v(13.12, -237.84) * mm, "end": v(12.44, -238.57) * mm});
            skLineSegment(sketch, "E3067", {"start": v(12.44, -238.57) * mm, "end": v(11.73, -239.25) * mm});
            skLineSegment(sketch, "E3068", {"start": v(11.73, -239.25) * mm, "end": v(10.97, -239.86) * mm});
            skLineSegment(sketch, "E3069", {"start": v(10.97, -239.86) * mm, "end": v(10.14, -240.4) * mm});
            skLineSegment(sketch, "E3070", {"start": v(10.14, -240.4) * mm, "end": v(9.24, -240.82) * mm});
            skLineSegment(sketch, "E3071", {"start": v(9.24, -240.82) * mm, "end": v(8.26, -241.12) * mm});
            skLineSegment(sketch, "E3072", {"start": v(8.26, -241.12) * mm, "end": v(7.42, -241.28) * mm});
            skLineSegment(sketch, "E3073", {"start": v(7.42, -241.28) * mm, "end": v(6.59, -241.34) * mm});
            skLineSegment(sketch, "E3074", {"start": v(6.59, -241.34) * mm, "end": v(5.8, -241.28) * mm});
            skLineSegment(sketch, "E3075", {"start": v(5.8, -241.28) * mm, "end": v(5.05, -241.1) * mm});
            skLineSegment(sketch, "E3076", {"start": v(5.05, -241.1) * mm, "end": v(4.38, -240.77) * mm});
            skLineSegment(sketch, "E3077", {"start": v(4.38, -240.77) * mm, "end": v(3.79, -240.29) * mm});
            skLineSegment(sketch, "E3078", {"start": v(3.79, -240.29) * mm, "end": v(3.3, -239.62) * mm});
            skLineSegment(sketch, "E3079", {"start": v(3.3, -239.62) * mm, "end": v(2.93, -238.77) * mm});
            skLineSegment(sketch, "E3080", {"start": v(2.93, -238.77) * mm, "end": v(2.75, -237.92) * mm});
            skLineSegment(sketch, "E3081", {"start": v(2.75, -237.92) * mm, "end": v(2.77, -237.17) * mm});
            skLineSegment(sketch, "E3082", {"start": v(2.77, -237.17) * mm, "end": v(2.97, -236.52) * mm});
            skLineSegment(sketch, "E3083", {"start": v(2.97, -236.52) * mm, "end": v(3.33, -235.95) * mm});
            skLineSegment(sketch, "E3084", {"start": v(3.33, -235.95) * mm, "end": v(3.82, -235.46) * mm});
            skLineSegment(sketch, "E3085", {"start": v(3.82, -235.46) * mm, "end": v(4.43, -235.04) * mm});
            skLineSegment(sketch, "E3086", {"start": v(4.43, -235.04) * mm, "end": v(5.12, -234.69) * mm});
            skLineSegment(sketch, "E3087", {"start": v(5.12, -234.69) * mm, "end": v(5.88, -234.4) * mm});
            skLineSegment(sketch, "E3088", {"start": v(5.88, -234.4) * mm, "end": v(6.17, -234.3) * mm});
            skLineSegment(sketch, "E3089", {"start": v(6.17, -234.3) * mm, "end": v(6.47, -234.2) * mm});
            skLineSegment(sketch, "E3090", {"start": v(6.47, -234.2) * mm, "end": v(6.77, -234.12) * mm});
            skLineSegment(sketch, "E3091", {"start": v(6.77, -234.12) * mm, "end": v(7.07, -234.04) * mm});
            skLineSegment(sketch, "E3092", {"start": v(7.07, -234.04) * mm, "end": v(7.37, -233.97) * mm});
            skLineSegment(sketch, "E3093", {"start": v(7.37, -233.97) * mm, "end": v(7.67, -233.89) * mm});
            skLineSegment(sketch, "E3094", {"start": v(7.67, -233.89) * mm, "end": v(7.97, -233.81) * mm});
            skLineSegment(sketch, "E3095", {"start": v(7.97, -233.81) * mm, "end": v(8.27, -233.73) * mm});
            skLineSegment(sketch, "E3096", {"start": v(-12.38, 230.23) * mm, "end": v(-9.61, 230.23) * mm});
            skLineSegment(sketch, "E3097", {"start": v(-9.61, 230.23) * mm, "end": v(-6.84, 230.23) * mm});
            skLineSegment(sketch, "E3098", {"start": v(-6.84, 230.23) * mm, "end": v(-4.06, 230.23) * mm});
            skLineSegment(sketch, "E3099", {"start": v(-4.06, 230.23) * mm, "end": v(-1.3, 230.22) * mm});
            skLineSegment(sketch, "E3100", {"start": v(-1.3, 230.22) * mm, "end": v(1.48, 230.22) * mm});
            skLineSegment(sketch, "E3101", {"start": v(1.48, 230.22) * mm, "end": v(4.25, 230.23) * mm});
            skLineSegment(sketch, "E3102", {"start": v(4.25, 230.23) * mm, "end": v(7.03, 230.24) * mm});
            skLineSegment(sketch, "E3103", {"start": v(7.03, 230.24) * mm, "end": v(9.8, 230.25) * mm});
            skLineSegment(sketch, "E3104", {"start": v(9.8, 230.25) * mm, "end": v(10.46, 230.3) * mm});
            skLineSegment(sketch, "E3105", {"start": v(10.46, 230.3) * mm, "end": v(11.03, 230.44) * mm});
            skLineSegment(sketch, "E3106", {"start": v(11.03, 230.44) * mm, "end": v(11.5, 230.68) * mm});
            skLineSegment(sketch, "E3107", {"start": v(11.5, 230.68) * mm, "end": v(11.87, 231) * mm});
            skLineSegment(sketch, "E3108", {"start": v(11.87, 231) * mm, "end": v(12.1, 231.4) * mm});
            skLineSegment(sketch, "E3109", {"start": v(12.1, 231.4) * mm, "end": v(12.19, 231.9) * mm});
            skLineSegment(sketch, "E3110", {"start": v(12.19, 231.9) * mm, "end": v(12.12, 232.49) * mm});
            skLineSegment(sketch, "E3111", {"start": v(12.12, 232.49) * mm, "end": v(11.89, 233.16) * mm});
            skLineSegment(sketch, "E3112", {"start": v(11.89, 233.16) * mm, "end": v(11.1, 234.8) * mm});
            skLineSegment(sketch, "E3113", {"start": v(11.1, 234.8) * mm, "end": v(10.27, 236.4) * mm});
            skLineSegment(sketch, "E3114", {"start": v(10.27, 236.4) * mm, "end": v(9.37, 237.96) * mm});
            skLineSegment(sketch, "E3115", {"start": v(9.37, 237.96) * mm, "end": v(8.39, 239.46) * mm});
            skLineSegment(sketch, "E3116", {"start": v(8.39, 239.46) * mm, "end": v(7.32, 240.9) * mm});
            skLineSegment(sketch, "E3117", {"start": v(7.32, 240.9) * mm, "end": v(6.14, 242.26) * mm});
            skLineSegment(sketch, "E3118", {"start": v(6.14, 242.26) * mm, "end": v(4.86, 243.54) * mm});
            skLineSegment(sketch, "E3119", {"start": v(4.86, 243.54) * mm, "end": v(3.45, 244.73) * mm});
            skLineSegment(sketch, "E3120", {"start": v(3.45, 244.73) * mm, "end": v(2.77, 245.17) * mm});
            skLineSegment(sketch, "E3121", {"start": v(2.77, 245.17) * mm, "end": v(2.09, 245.48) * mm});
            skLineSegment(sketch, "E3122", {"start": v(2.09, 245.48) * mm, "end": v(1.39, 245.66) * mm});
            skLineSegment(sketch, "E3123", {"start": v(1.39, 245.66) * mm, "end": v(0.69, 245.71) * mm});
            skLineSegment(sketch, "E3124", {"start": v(0.69, 245.71) * mm, "end": v(-0.02, 245.63) * mm});
            skLineSegment(sketch, "E3125", {"start": v(-0.02, 245.63) * mm, "end": v(-0.71, 245.43) * mm});
            skLineSegment(sketch, "E3126", {"start": v(-0.71, 245.43) * mm, "end": v(-1.4, 245.1) * mm});
            skLineSegment(sketch, "E3127", {"start": v(-1.4, 245.1) * mm, "end": v(-2.08, 244.65) * mm});
            skLineSegment(sketch, "E3128", {"start": v(-2.08, 244.65) * mm, "end": v(-2.44, 244.38) * mm});
            skLineSegment(sketch, "E3129", {"start": v(-2.44, 244.38) * mm, "end": v(-2.73, 244.1) * mm});
            skLineSegment(sketch, "E3130", {"start": v(-2.73, 244.1) * mm, "end": v(-2.93, 243.83) * mm});
            skLineSegment(sketch, "E3131", {"start": v(-2.93, 243.83) * mm, "end": v(-3.04, 243.55) * mm});
            skLineSegment(sketch, "E3132", {"start": v(-3.04, 243.55) * mm, "end": v(-3.04, 243.24) * mm});
            skLineSegment(sketch, "E3133", {"start": v(-3.04, 243.24) * mm, "end": v(-2.9, 242.89) * mm});
            skLineSegment(sketch, "E3134", {"start": v(-2.9, 242.89) * mm, "end": v(-2.61, 242.5) * mm});
            skLineSegment(sketch, "E3135", {"start": v(-2.61, 242.5) * mm, "end": v(-2.16, 242.05) * mm});
            skLineSegment(sketch, "E3136", {"start": v(-2.16, 242.05) * mm, "end": v(-0.9, 240.77) * mm});
            skLineSegment(sketch, "E3137", {"start": v(-0.9, 240.77) * mm, "end": v(-0.03, 239.53) * mm});
            skLineSegment(sketch, "E3138", {"start": v(-0.03, 239.53) * mm, "end": v(0.43, 238.34) * mm});
            skLineSegment(sketch, "E3139", {"start": v(0.43, 238.34) * mm, "end": v(0.5, 237.18) * mm});
            skLineSegment(sketch, "E3140", {"start": v(0.5, 237.18) * mm, "end": v(0.19, 236.05) * mm});
            skLineSegment(sketch, "E3141", {"start": v(0.19, 236.05) * mm, "end": v(-0.51, 234.94) * mm});
            skLineSegment(sketch, "E3142", {"start": v(-0.51, 234.94) * mm, "end": v(-1.59, 233.85) * mm});
            skLineSegment(sketch, "E3143", {"start": v(-1.59, 233.85) * mm, "end": v(-3.03, 232.77) * mm});
            skLineSegment(sketch, "E3144", {"start": v(-3.03, 232.77) * mm, "end": v(-4.13, 232.15) * mm});
            skLineSegment(sketch, "E3145", {"start": v(-4.13, 232.15) * mm, "end": v(-5.26, 231.69) * mm});
            skLineSegment(sketch, "E3146", {"start": v(-5.26, 231.69) * mm, "end": v(-6.41, 231.35) * mm});
            skLineSegment(sketch, "E3147", {"start": v(-6.41, 231.35) * mm, "end": v(-7.59, 231.1) * mm});
            skLineSegment(sketch, "E3148", {"start": v(-7.59, 231.1) * mm, "end": v(-8.78, 230.89) * mm});
            skLineSegment(sketch, "E3149", {"start": v(-8.78, 230.89) * mm, "end": v(-9.98, 230.7) * mm});
            skLineSegment(sketch, "E3150", {"start": v(-9.98, 230.7) * mm, "end": v(-11.18, 230.5) * mm});
            skLineSegment(sketch, "E3151", {"start": v(-11.18, 230.5) * mm, "end": v(-12.38, 230.23) * mm});
            skLineSegment(sketch, "E3152", {"start": v(-38.86, 91.72) * mm, "end": v(-40.36, 90.14) * mm});
            skLineSegment(sketch, "E3153", {"start": v(-40.36, 90.14) * mm, "end": v(-41.85, 88.58) * mm});
            skLineSegment(sketch, "E3154", {"start": v(-41.85, 88.58) * mm, "end": v(-43.33, 87.04) * mm});
            skLineSegment(sketch, "E3155", {"start": v(-43.33, 87.04) * mm, "end": v(-44.8, 85.5) * mm});
            skLineSegment(sketch, "E3156", {"start": v(-44.8, 85.5) * mm, "end": v(-46.26, 83.97) * mm});
            skLineSegment(sketch, "E3157", {"start": v(-46.26, 83.97) * mm, "end": v(-47.7, 82.44) * mm});
            skLineSegment(sketch, "E3158", {"start": v(-47.7, 82.44) * mm, "end": v(-49.12, 80.9) * mm});
            skLineSegment(sketch, "E3159", {"start": v(-49.12, 80.9) * mm, "end": v(-50.53, 79.35) * mm});
            skLineSegment(sketch, "E3160", {"start": v(-50.53, 79.35) * mm, "end": v(-51.21, 78.7) * mm});
            skLineSegment(sketch, "E3161", {"start": v(-51.21, 78.7) * mm, "end": v(-52, 78.04) * mm});
            skLineSegment(sketch, "E3162", {"start": v(-52, 78.04) * mm, "end": v(-52.8, 77.4) * mm});
            skLineSegment(sketch, "E3163", {"start": v(-52.8, 77.4) * mm, "end": v(-53.58, 76.74) * mm});
            skLineSegment(sketch, "E3164", {"start": v(-53.58, 76.74) * mm, "end": v(-54.24, 76.06) * mm});
            skLineSegment(sketch, "E3165", {"start": v(-54.24, 76.06) * mm, "end": v(-54.71, 75.35) * mm});
            skLineSegment(sketch, "E3166", {"start": v(-54.71, 75.35) * mm, "end": v(-54.92, 74.6) * mm});
            skLineSegment(sketch, "E3167", {"start": v(-54.92, 74.6) * mm, "end": v(-54.8, 73.79) * mm});
            skLineSegment(sketch, "E3168", {"start": v(-54.8, 73.79) * mm, "end": v(-54.34, 73.03) * mm});
            skLineSegment(sketch, "E3169", {"start": v(-54.34, 73.03) * mm, "end": v(-53.66, 72.5) * mm});
            skLineSegment(sketch, "E3170", {"start": v(-53.66, 72.5) * mm, "end": v(-52.8, 72.15) * mm});
            skLineSegment(sketch, "E3171", {"start": v(-52.8, 72.15) * mm, "end": v(-51.82, 71.93) * mm});
            skLineSegment(sketch, "E3172", {"start": v(-51.82, 71.93) * mm, "end": v(-50.77, 71.78) * mm});
            skLineSegment(sketch, "E3173", {"start": v(-50.77, 71.78) * mm, "end": v(-49.68, 71.65) * mm});
            skLineSegment(sketch, "E3174", {"start": v(-49.68, 71.65) * mm, "end": v(-48.63, 71.49) * mm});
            skLineSegment(sketch, "E3175", {"start": v(-48.63, 71.49) * mm, "end": v(-47.64, 71.24) * mm});
            skLineSegment(sketch, "E3176", {"start": v(-47.64, 71.24) * mm, "end": v(-46.78, 71.03) * mm});
            skLineSegment(sketch, "E3177", {"start": v(-46.78, 71.03) * mm, "end": v(-46.02, 71) * mm});
            skLineSegment(sketch, "E3178", {"start": v(-46.02, 71) * mm, "end": v(-45.35, 71.13) * mm});
            skLineSegment(sketch, "E3179", {"start": v(-45.35, 71.13) * mm, "end": v(-44.78, 71.4) * mm});
            skLineSegment(sketch, "E3180", {"start": v(-44.78, 71.4) * mm, "end": v(-44.29, 71.83) * mm});
            skLineSegment(sketch, "E3181", {"start": v(-44.29, 71.83) * mm, "end": v(-43.86, 72.39) * mm});
            skLineSegment(sketch, "E3182", {"start": v(-43.86, 72.39) * mm, "end": v(-43.5, 73.06) * mm});
            skLineSegment(sketch, "E3183", {"start": v(-43.5, 73.06) * mm, "end": v(-43.2, 73.85) * mm});
            skLineSegment(sketch, "E3184", {"start": v(-43.2, 73.85) * mm, "end": v(-42.72, 75.2) * mm});
            skLineSegment(sketch, "E3185", {"start": v(-42.72, 75.2) * mm, "end": v(-42.23, 76.56) * mm});
            skLineSegment(sketch, "E3186", {"start": v(-42.23, 76.56) * mm, "end": v(-41.73, 77.9) * mm});
            skLineSegment(sketch, "E3187", {"start": v(-41.73, 77.9) * mm, "end": v(-41.23, 79.25) * mm});
            skLineSegment(sketch, "E3188", {"start": v(-41.23, 79.25) * mm, "end": v(-40.74, 80.6) * mm});
            skLineSegment(sketch, "E3189", {"start": v(-40.74, 80.6) * mm, "end": v(-40.25, 81.94) * mm});
            skLineSegment(sketch, "E3190", {"start": v(-40.25, 81.94) * mm, "end": v(-39.78, 83.3) * mm});
            skLineSegment(sketch, "E3191", {"start": v(-39.78, 83.3) * mm, "end": v(-39.33, 84.65) * mm});
            skLineSegment(sketch, "E3192", {"start": v(-39.33, 84.65) * mm, "end": v(-39.05, 85.44) * mm});
            skLineSegment(sketch, "E3193", {"start": v(-39.05, 85.44) * mm, "end": v(-38.74, 86.23) * mm});
            skLineSegment(sketch, "E3194", {"start": v(-38.74, 86.23) * mm, "end": v(-38.44, 87.04) * mm});
            skLineSegment(sketch, "E3195", {"start": v(-38.44, 87.04) * mm, "end": v(-38.21, 87.89) * mm});
            skLineSegment(sketch, "E3196", {"start": v(-38.21, 87.89) * mm, "end": v(-38.1, 88.76) * mm});
            skLineSegment(sketch, "E3197", {"start": v(-38.1, 88.76) * mm, "end": v(-38.13, 89.69) * mm});
            skLineSegment(sketch, "E3198", {"start": v(-38.13, 89.69) * mm, "end": v(-38.37, 90.67) * mm});
            skLineSegment(sketch, "E3199", {"start": v(-38.37, 90.67) * mm, "end": v(-38.86, 91.72) * mm});
            skLineSegment(sketch, "E3200", {"start": v(-3.04, -78.42) * mm, "end": v(-2.69, -80.53) * mm});
            skLineSegment(sketch, "E3201", {"start": v(-2.69, -80.53) * mm, "end": v(-2.15, -82.51) * mm});
            skLineSegment(sketch, "E3202", {"start": v(-2.15, -82.51) * mm, "end": v(-1.44, -84.4) * mm});
            skLineSegment(sketch, "E3203", {"start": v(-1.44, -84.4) * mm, "end": v(-0.6, -86.2) * mm});
            skLineSegment(sketch, "E3204", {"start": v(-0.6, -86.2) * mm, "end": v(0.34, -87.95) * mm});
            skLineSegment(sketch, "E3205", {"start": v(0.34, -87.95) * mm, "end": v(1.37, -89.64) * mm});
            skLineSegment(sketch, "E3206", {"start": v(1.37, -89.64) * mm, "end": v(2.45, -91.3) * mm});
            skLineSegment(sketch, "E3207", {"start": v(2.45, -91.3) * mm, "end": v(3.56, -92.94) * mm});
            skLineSegment(sketch, "E3208", {"start": v(3.56, -92.94) * mm, "end": v(5.4, -95.73) * mm});
            skLineSegment(sketch, "E3209", {"start": v(5.4, -95.73) * mm, "end": v(6.67, -97.96) * mm});
            skLineSegment(sketch, "E3210", {"start": v(6.67, -97.96) * mm, "end": v(7.37, -99.78) * mm});
            skLineSegment(sketch, "E3211", {"start": v(7.37, -99.78) * mm, "end": v(7.45, -101.35) * mm});
            skLineSegment(sketch, "E3212", {"start": v(7.45, -101.35) * mm, "end": v(6.9, -102.82) * mm});
            skLineSegment(sketch, "E3213", {"start": v(6.9, -102.82) * mm, "end": v(5.68, -104.34) * mm});
            skLineSegment(sketch, "E3214", {"start": v(5.68, -104.34) * mm, "end": v(3.77, -106.06) * mm});
            skLineSegment(sketch, "E3215", {"start": v(3.77, -106.06) * mm, "end": v(1.15, -108.14) * mm});
            skLineSegment(sketch, "E3216", {"start": v(1.15, -108.14) * mm, "end": v(0.2, -108.96) * mm});
            skLineSegment(sketch, "E3217", {"start": v(0.2, -108.96) * mm, "end": v(-0.51, -109.8) * mm});
            skLineSegment(sketch, "E3218", {"start": v(-0.51, -109.8) * mm, "end": v(-1.02, -110.67) * mm});
            skLineSegment(sketch, "E3219", {"start": v(-1.02, -110.67) * mm, "end": v(-1.31, -111.57) * mm});
            skLineSegment(sketch, "E3220", {"start": v(-1.31, -111.57) * mm, "end": v(-1.4, -112.5) * mm});
            skLineSegment(sketch, "E3221", {"start": v(-1.4, -112.5) * mm, "end": v(-1.28, -113.47) * mm});
            skLineSegment(sketch, "E3222", {"start": v(-1.28, -113.47) * mm, "end": v(-0.96, -114.47) * mm});
            skLineSegment(sketch, "E3223", {"start": v(-0.96, -114.47) * mm, "end": v(-0.43, -115.51) * mm});
            skLineSegment(sketch, "E3224", {"start": v(-0.43, -115.51) * mm, "end": v(0.37, -116.85) * mm});
            skLineSegment(sketch, "E3225", {"start": v(0.37, -116.85) * mm, "end": v(1.18, -118.18) * mm});
            skLineSegment(sketch, "E3226", {"start": v(1.18, -118.18) * mm, "end": v(2.01, -119.5) * mm});
            skLineSegment(sketch, "E3227", {"start": v(2.01, -119.5) * mm, "end": v(2.85, -120.82) * mm});
            skLineSegment(sketch, "E3228", {"start": v(2.85, -120.82) * mm, "end": v(3.69, -122.14) * mm});
            skLineSegment(sketch, "E3229", {"start": v(3.69, -122.14) * mm, "end": v(4.53, -123.45) * mm});
            skLineSegment(sketch, "E3230", {"start": v(4.53, -123.45) * mm, "end": v(5.36, -124.77) * mm});
            skLineSegment(sketch, "E3231", {"start": v(5.36, -124.77) * mm, "end": v(6.18, -126.1) * mm});
            skLineSegment(sketch, "E3232", {"start": v(6.18, -126.1) * mm, "end": v(7.15, -127.85) * mm});
            skLineSegment(sketch, "E3233", {"start": v(7.15, -127.85) * mm, "end": v(7.78, -129.41) * mm});
            skLineSegment(sketch, "E3234", {"start": v(7.78, -129.41) * mm, "end": v(8.07, -130.84) * mm});
            skLineSegment(sketch, "E3235", {"start": v(8.07, -130.84) * mm, "end": v(8, -132.16) * mm});
            skLineSegment(sketch, "E3236", {"start": v(8, -132.16) * mm, "end": v(7.58, -133.42) * mm});
            skLineSegment(sketch, "E3237", {"start": v(7.58, -133.42) * mm, "end": v(6.8, -134.65) * mm});
            skLineSegment(sketch, "E3238", {"start": v(6.8, -134.65) * mm, "end": v(5.64, -135.9) * mm});
            skLineSegment(sketch, "E3239", {"start": v(5.64, -135.9) * mm, "end": v(4.1, -137.19) * mm});
            skLineSegment(sketch, "E3240", {"start": v(4.1, -137.19) * mm, "end": v(2.54, -138.3) * mm});
            skLineSegment(sketch, "E3241", {"start": v(2.54, -138.3) * mm, "end": v(0.94, -139.28) * mm});
            skLineSegment(sketch, "E3242", {"start": v(0.94, -139.28) * mm, "end": v(-0.7, -140.14) * mm});
            skLineSegment(sketch, "E3243", {"start": v(-0.7, -140.14) * mm, "end": v(-2.41, -140.88) * mm});
            skLineSegment(sketch, "E3244", {"start": v(-2.41, -140.88) * mm, "end": v(-4.16, -141.5) * mm});
            skLineSegment(sketch, "E3245", {"start": v(-4.16, -141.5) * mm, "end": v(-5.95, -142) * mm});
            skLineSegment(sketch, "E3246", {"start": v(-5.95, -142) * mm, "end": v(-7.8, -142.4) * mm});
            skLineSegment(sketch, "E3247", {"start": v(-7.8, -142.4) * mm, "end": v(-9.67, -142.66) * mm});
            skLineSegment(sketch, "E3248", {"start": v(-9.67, -142.66) * mm, "end": v(-11.7, -142.74) * mm});
            skLineSegment(sketch, "E3249", {"start": v(-11.7, -142.74) * mm, "end": v(-13.45, -142.5) * mm});
            skLineSegment(sketch, "E3250", {"start": v(-13.45, -142.5) * mm, "end": v(-14.91, -141.96) * mm});
            skLineSegment(sketch, "E3251", {"start": v(-14.91, -141.96) * mm, "end": v(-16.07, -141.1) * mm});
            skLineSegment(sketch, "E3252", {"start": v(-16.07, -141.1) * mm, "end": v(-16.92, -139.96) * mm});
            skLineSegment(sketch, "E3253", {"start": v(-16.92, -139.96) * mm, "end": v(-17.44, -138.52) * mm});
            skLineSegment(sketch, "E3254", {"start": v(-17.44, -138.52) * mm, "end": v(-17.62, -136.8) * mm});
            skLineSegment(sketch, "E3255", {"start": v(-17.62, -136.8) * mm, "end": v(-17.45, -134.82) * mm});
            skLineSegment(sketch, "E3256", {"start": v(-17.45, -134.82) * mm, "end": v(-17.19, -132.73) * mm});
            skLineSegment(sketch, "E3257", {"start": v(-17.19, -132.73) * mm, "end": v(-17.12, -130.71) * mm});
            skLineSegment(sketch, "E3258", {"start": v(-17.12, -130.71) * mm, "end": v(-17.24, -128.75) * mm});
            skLineSegment(sketch, "E3259", {"start": v(-17.24, -128.75) * mm, "end": v(-17.57, -126.84) * mm});
            skLineSegment(sketch, "E3260", {"start": v(-17.57, -126.84) * mm, "end": v(-18.12, -125) * mm});
            skLineSegment(sketch, "E3261", {"start": v(-18.12, -125) * mm, "end": v(-18.88, -123.21) * mm});
            skLineSegment(sketch, "E3262", {"start": v(-18.88, -123.21) * mm, "end": v(-19.88, -121.48) * mm});
            skLineSegment(sketch, "E3263", {"start": v(-19.88, -121.48) * mm, "end": v(-21.11, -119.82) * mm});
            skLineSegment(sketch, "E3264", {"start": v(-21.11, -119.82) * mm, "end": v(-22.78, -117.52) * mm});
            skLineSegment(sketch, "E3265", {"start": v(-22.78, -117.52) * mm, "end": v(-24.09, -115.16) * mm});
            skLineSegment(sketch, "E3266", {"start": v(-24.09, -115.16) * mm, "end": v(-25.05, -112.72) * mm});
            skLineSegment(sketch, "E3267", {"start": v(-25.05, -112.72) * mm, "end": v(-25.7, -110.21) * mm});
            skLineSegment(sketch, "E3268", {"start": v(-25.7, -110.21) * mm, "end": v(-26.07, -107.64) * mm});
            skLineSegment(sketch, "E3269", {"start": v(-26.07, -107.64) * mm, "end": v(-26.18, -105) * mm});
            skLineSegment(sketch, "E3270", {"start": v(-26.18, -105) * mm, "end": v(-26.05, -102.3) * mm});
            skLineSegment(sketch, "E3271", {"start": v(-26.05, -102.3) * mm, "end": v(-25.7, -99.56) * mm});
            skLineSegment(sketch, "E3272", {"start": v(-25.7, -99.56) * mm, "end": v(-25.46, -97.9) * mm});
            skLineSegment(sketch, "E3273", {"start": v(-25.46, -97.9) * mm, "end": v(-25.24, -96.22) * mm});
            skLineSegment(sketch, "E3274", {"start": v(-25.24, -96.22) * mm, "end": v(-25.05, -94.55) * mm});
            skLineSegment(sketch, "E3275", {"start": v(-25.05, -94.55) * mm, "end": v(-24.87, -92.87) * mm});
            skLineSegment(sketch, "E3276", {"start": v(-24.87, -92.87) * mm, "end": v(-24.7, -91.2) * mm});
            skLineSegment(sketch, "E3277", {"start": v(-24.7, -91.2) * mm, "end": v(-24.54, -89.52) * mm});
            skLineSegment(sketch, "E3278", {"start": v(-24.54, -89.52) * mm, "end": v(-24.37, -87.84) * mm});
            skLineSegment(sketch, "E3279", {"start": v(-24.37, -87.84) * mm, "end": v(-24.2, -86.16) * mm});
            skLineSegment(sketch, "E3280", {"start": v(-24.2, -86.16) * mm, "end": v(-24.15, -84.98) * mm});
            skLineSegment(sketch, "E3281", {"start": v(-24.15, -84.98) * mm, "end": v(-24.28, -84) * mm});
            skLineSegment(sketch, "E3282", {"start": v(-24.28, -84) * mm, "end": v(-24.58, -83.17) * mm});
            skLineSegment(sketch, "E3283", {"start": v(-24.58, -83.17) * mm, "end": v(-25.06, -82.5) * mm});
            skLineSegment(sketch, "E3284", {"start": v(-25.06, -82.5) * mm, "end": v(-25.72, -82) * mm});
            skLineSegment(sketch, "E3285", {"start": v(-25.72, -82) * mm, "end": v(-26.56, -81.64) * mm});
            skLineSegment(sketch, "E3286", {"start": v(-26.56, -81.64) * mm, "end": v(-27.58, -81.41) * mm});
            skLineSegment(sketch, "E3287", {"start": v(-27.58, -81.41) * mm, "end": v(-28.79, -81.3) * mm});
            skLineSegment(sketch, "E3288", {"start": v(-28.79, -81.3) * mm, "end": v(-31.9, -81.07) * mm});
            skLineSegment(sketch, "E3289", {"start": v(-31.9, -81.07) * mm, "end": v(-34.5, -80.56) * mm});
            skLineSegment(sketch, "E3290", {"start": v(-34.5, -80.56) * mm, "end": v(-36.64, -79.73) * mm});
            skLineSegment(sketch, "E3291", {"start": v(-36.64, -79.73) * mm, "end": v(-38.36, -78.55) * mm});
            skLineSegment(sketch, "E3292", {"start": v(-38.36, -78.55) * mm, "end": v(-39.74, -76.96) * mm});
            skLineSegment(sketch, "E3293", {"start": v(-39.74, -76.96) * mm, "end": v(-40.8, -74.93) * mm});
            skLineSegment(sketch, "E3294", {"start": v(-40.8, -74.93) * mm, "end": v(-41.62, -72.4) * mm});
            skLineSegment(sketch, "E3295", {"start": v(-41.62, -72.4) * mm, "end": v(-42.25, -69.35) * mm});
            skLineSegment(sketch, "E3296", {"start": v(-42.25, -69.35) * mm, "end": v(-42.4, -68.3) * mm});
            skLineSegment(sketch, "E3297", {"start": v(-42.4, -68.3) * mm, "end": v(-42.53, -67.25) * mm});
            skLineSegment(sketch, "E3298", {"start": v(-42.53, -67.25) * mm, "end": v(-42.65, -66.2) * mm});
            skLineSegment(sketch, "E3299", {"start": v(-42.65, -66.2) * mm, "end": v(-42.74, -65.14) * mm});
            skLineSegment(sketch, "E3300", {"start": v(-42.74, -65.14) * mm, "end": v(-42.82, -64.08) * mm});
            skLineSegment(sketch, "E3301", {"start": v(-42.82, -64.08) * mm, "end": v(-42.88, -63.02) * mm});
            skLineSegment(sketch, "E3302", {"start": v(-42.88, -63.02) * mm, "end": v(-42.93, -61.96) * mm});
            skLineSegment(sketch, "E3303", {"start": v(-42.93, -61.96) * mm, "end": v(-42.96, -60.9) * mm});
            skLineSegment(sketch, "E3304", {"start": v(-42.96, -60.9) * mm, "end": v(-43.11, -56.28) * mm});
            skLineSegment(sketch, "E3305", {"start": v(-43.11, -56.28) * mm, "end": v(-43.26, -51.66) * mm});
            skLineSegment(sketch, "E3306", {"start": v(-43.26, -51.66) * mm, "end": v(-43.4, -47.04) * mm});
            skLineSegment(sketch, "E3307", {"start": v(-43.4, -47.04) * mm, "end": v(-43.53, -42.42) * mm});
            skLineSegment(sketch, "E3308", {"start": v(-43.53, -42.42) * mm, "end": v(-43.66, -37.8) * mm});
            skLineSegment(sketch, "E3309", {"start": v(-43.66, -37.8) * mm, "end": v(-43.78, -33.18) * mm});
            skLineSegment(sketch, "E3310", {"start": v(-43.78, -33.18) * mm, "end": v(-43.89, -28.56) * mm});
            skLineSegment(sketch, "E3311", {"start": v(-43.89, -28.56) * mm, "end": v(-43.98, -23.94) * mm});
            skLineSegment(sketch, "E3312", {"start": v(-43.98, -23.94) * mm, "end": v(-44.05, -22.67) * mm});
            skLineSegment(sketch, "E3313", {"start": v(-44.05, -22.67) * mm, "end": v(-44.2, -21.49) * mm});
            skLineSegment(sketch, "E3314", {"start": v(-44.2, -21.49) * mm, "end": v(-44.48, -20.39) * mm});
            skLineSegment(sketch, "E3315", {"start": v(-44.48, -20.39) * mm, "end": v(-44.9, -19.38) * mm});
            skLineSegment(sketch, "E3316", {"start": v(-44.9, -19.38) * mm, "end": v(-45.47, -18.46) * mm});
            skLineSegment(sketch, "E3317", {"start": v(-45.47, -18.46) * mm, "end": v(-46.22, -17.63) * mm});
            skLineSegment(sketch, "E3318", {"start": v(-46.22, -17.63) * mm, "end": v(-47.16, -16.9) * mm});
            skLineSegment(sketch, "E3319", {"start": v(-47.16, -16.9) * mm, "end": v(-48.34, -16.29) * mm});
            skLineSegment(sketch, "E3320", {"start": v(-48.34, -16.29) * mm, "end": v(-49.36, -15.74) * mm});
            skLineSegment(sketch, "E3321", {"start": v(-49.36, -15.74) * mm, "end": v(-50.06, -15.14) * mm});
            skLineSegment(sketch, "E3322", {"start": v(-50.06, -15.14) * mm, "end": v(-50.47, -14.51) * mm});
            skLineSegment(sketch, "E3323", {"start": v(-50.47, -14.51) * mm, "end": v(-50.6, -13.85) * mm});
            skLineSegment(sketch, "E3324", {"start": v(-50.6, -13.85) * mm, "end": v(-50.46, -13.17) * mm});
            skLineSegment(sketch, "E3325", {"start": v(-50.46, -13.17) * mm, "end": v(-50.09, -12.46) * mm});
            skLineSegment(sketch, "E3326", {"start": v(-50.09, -12.46) * mm, "end": v(-49.5, -11.74) * mm});
            skLineSegment(sketch, "E3327", {"start": v(-49.5, -11.74) * mm, "end": v(-48.73, -11.01) * mm});
            skLineSegment(sketch, "E3328", {"start": v(-48.73, -11.01) * mm, "end": v(-48.63, -10.93) * mm});
            skLineSegment(sketch, "E3329", {"start": v(-48.63, -10.93) * mm, "end": v(-48.53, -10.86) * mm});
            skLineSegment(sketch, "E3330", {"start": v(-48.53, -10.86) * mm, "end": v(-48.44, -10.78) * mm});
            skLineSegment(sketch, "E3331", {"start": v(-48.44, -10.78) * mm, "end": v(-48.34, -10.7) * mm});
            skLineSegment(sketch, "E3332", {"start": v(-48.34, -10.7) * mm, "end": v(-48.24, -10.62) * mm});
            skLineSegment(sketch, "E3333", {"start": v(-48.24, -10.62) * mm, "end": v(-48.15, -10.54) * mm});
            skLineSegment(sketch, "E3334", {"start": v(-48.15, -10.54) * mm, "end": v(-48.06, -10.45) * mm});
            skLineSegment(sketch, "E3335", {"start": v(-48.06, -10.45) * mm, "end": v(-47.96, -10.37) * mm});
            skLineSegment(sketch, "E3336", {"start": v(-47.96, -10.37) * mm, "end": v(-47.16, -9.68) * mm});
            skLineSegment(sketch, "E3337", {"start": v(-47.16, -9.68) * mm, "end": v(-46.28, -8.98) * mm});
            skLineSegment(sketch, "E3338", {"start": v(-46.28, -8.98) * mm, "end": v(-45.4, -8.27) * mm});
            skLineSegment(sketch, "E3339", {"start": v(-45.4, -8.27) * mm, "end": v(-44.61, -7.53) * mm});
            skLineSegment(sketch, "E3340", {"start": v(-44.61, -7.53) * mm, "end": v(-44, -6.72) * mm});
            skLineSegment(sketch, "E3341", {"start": v(-44, -6.72) * mm, "end": v(-43.64, -5.84) * mm});
            skLineSegment(sketch, "E3342", {"start": v(-43.64, -5.84) * mm, "end": v(-43.61, -4.87) * mm});
            skLineSegment(sketch, "E3343", {"start": v(-43.61, -4.87) * mm, "end": v(-44.02, -3.78) * mm});
            skLineSegment(sketch, "E3344", {"start": v(-44.02, -3.78) * mm, "end": v(-44.8, -2.76) * mm});
            skLineSegment(sketch, "E3345", {"start": v(-44.8, -2.76) * mm, "end": v(-45.73, -2.12) * mm});
            skLineSegment(sketch, "E3346", {"start": v(-45.73, -2.12) * mm, "end": v(-46.79, -1.8) * mm});
            skLineSegment(sketch, "E3347", {"start": v(-46.79, -1.8) * mm, "end": v(-47.94, -1.74) * mm});
            skLineSegment(sketch, "E3348", {"start": v(-47.94, -1.74) * mm, "end": v(-49.14, -1.86) * mm});
            skLineSegment(sketch, "E3349", {"start": v(-49.14, -1.86) * mm, "end": v(-50.36, -2.12) * mm});
            skLineSegment(sketch, "E3350", {"start": v(-50.36, -2.12) * mm, "end": v(-51.56, -2.43) * mm});
            skLineSegment(sketch, "E3351", {"start": v(-51.56, -2.43) * mm, "end": v(-52.71, -2.74) * mm});
            skLineSegment(sketch, "E3352", {"start": v(-52.71, -2.74) * mm, "end": v(-54.28, -3.24) * mm});
            skLineSegment(sketch, "E3353", {"start": v(-54.28, -3.24) * mm, "end": v(-55.76, -3.9) * mm});
            skLineSegment(sketch, "E3354", {"start": v(-55.76, -3.9) * mm, "end": v(-57.17, -4.7) * mm});
            skLineSegment(sketch, "E3355", {"start": v(-57.17, -4.7) * mm, "end": v(-58.5, -5.6) * mm});
            skLineSegment(sketch, "E3356", {"start": v(-58.5, -5.6) * mm, "end": v(-59.8, -6.58) * mm});
            skLineSegment(sketch, "E3357", {"start": v(-59.8, -6.58) * mm, "end": v(-61.04, -7.63) * mm});
            skLineSegment(sketch, "E3358", {"start": v(-61.04, -7.63) * mm, "end": v(-62.26, -8.72) * mm});
            skLineSegment(sketch, "E3359", {"start": v(-62.26, -8.72) * mm, "end": v(-63.46, -9.83) * mm});
            skLineSegment(sketch, "E3360", {"start": v(-63.46, -9.83) * mm, "end": v(-64.44, -10.67) * mm});
            skLineSegment(sketch, "E3361", {"start": v(-64.44, -10.67) * mm, "end": v(-65.31, -11.26) * mm});
            skLineSegment(sketch, "E3362", {"start": v(-65.31, -11.26) * mm, "end": v(-66.08, -11.58) * mm});
            skLineSegment(sketch, "E3363", {"start": v(-66.08, -11.58) * mm, "end": v(-66.75, -11.6) * mm});
            skLineSegment(sketch, "E3364", {"start": v(-66.75, -11.6) * mm, "end": v(-67.32, -11.3) * mm});
            skLineSegment(sketch, "E3365", {"start": v(-67.32, -11.3) * mm, "end": v(-67.78, -10.65) * mm});
            skLineSegment(sketch, "E3366", {"start": v(-67.78, -10.65) * mm, "end": v(-68.15, -9.63) * mm});
            skLineSegment(sketch, "E3367", {"start": v(-68.15, -9.63) * mm, "end": v(-68.41, -8.2) * mm});
            skLineSegment(sketch, "E3368", {"start": v(-68.41, -8.2) * mm, "end": v(-68.69, -6.28) * mm});
            skLineSegment(sketch, "E3369", {"start": v(-68.69, -6.28) * mm, "end": v(-69, -4.38) * mm});
            skLineSegment(sketch, "E3370", {"start": v(-69, -4.38) * mm, "end": v(-69.37, -2.48) * mm});
            skLineSegment(sketch, "E3371", {"start": v(-69.37, -2.48) * mm, "end": v(-69.81, -0.6) * mm});
            skLineSegment(sketch, "E3372", {"start": v(-69.81, -0.6) * mm, "end": v(-70.34, 1.26) * mm});
            skLineSegment(sketch, "E3373", {"start": v(-70.34, 1.26) * mm, "end": v(-70.96, 3.08) * mm});
            skLineSegment(sketch, "E3374", {"start": v(-70.96, 3.08) * mm, "end": v(-71.7, 4.88) * mm});
            skLineSegment(sketch, "E3375", {"start": v(-71.7, 4.88) * mm, "end": v(-72.55, 6.64) * mm});
            skLineSegment(sketch, "E3376", {"start": v(-72.55, 6.64) * mm, "end": v(-72.73, 6.98) * mm});
            skLineSegment(sketch, "E3377", {"start": v(-72.73, 6.98) * mm, "end": v(-72.9, 7.32) * mm});
            skLineSegment(sketch, "E3378", {"start": v(-72.9, 7.32) * mm, "end": v(-73.06, 7.67) * mm});
            skLineSegment(sketch, "E3379", {"start": v(-73.06, 7.67) * mm, "end": v(-73.16, 8.03) * mm});
            skLineSegment(sketch, "E3380", {"start": v(-73.16, 8.03) * mm, "end": v(-73.19, 8.38) * mm});
            skLineSegment(sketch, "E3381", {"start": v(-73.19, 8.38) * mm, "end": v(-73.13, 8.71) * mm});
            skLineSegment(sketch, "E3382", {"start": v(-73.13, 8.71) * mm, "end": v(-72.95, 9.03) * mm});
            skLineSegment(sketch, "E3383", {"start": v(-72.95, 9.03) * mm, "end": v(-72.63, 9.32) * mm});
            skLineSegment(sketch, "E3384", {"start": v(-72.63, 9.32) * mm, "end": v(-72.41, 9.44) * mm});
            skLineSegment(sketch, "E3385", {"start": v(-72.41, 9.44) * mm, "end": v(-72.15, 9.5) * mm});
            skLineSegment(sketch, "E3386", {"start": v(-72.15, 9.5) * mm, "end": v(-71.86, 9.55) * mm});
            skLineSegment(sketch, "E3387", {"start": v(-71.86, 9.55) * mm, "end": v(-71.55, 9.55) * mm});
            skLineSegment(sketch, "E3388", {"start": v(-71.55, 9.55) * mm, "end": v(-71.23, 9.53) * mm});
            skLineSegment(sketch, "E3389", {"start": v(-71.23, 9.53) * mm, "end": v(-70.91, 9.49) * mm});
            skLineSegment(sketch, "E3390", {"start": v(-70.91, 9.49) * mm, "end": v(-70.6, 9.43) * mm});
            skLineSegment(sketch, "E3391", {"start": v(-70.6, 9.43) * mm, "end": v(-70.3, 9.37) * mm});
            skLineSegment(sketch, "E3392", {"start": v(-70.3, 9.37) * mm, "end": v(-69.88, 9.27) * mm});
            skLineSegment(sketch, "E3393", {"start": v(-69.88, 9.27) * mm, "end": v(-69.46, 9.15) * mm});
            skLineSegment(sketch, "E3394", {"start": v(-69.46, 9.15) * mm, "end": v(-69.04, 9.03) * mm});
            skLineSegment(sketch, "E3395", {"start": v(-69.04, 9.03) * mm, "end": v(-68.63, 8.89) * mm});
            skLineSegment(sketch, "E3396", {"start": v(-68.63, 8.89) * mm, "end": v(-68.21, 8.74) * mm});
            skLineSegment(sketch, "E3397", {"start": v(-68.21, 8.74) * mm, "end": v(-67.8, 8.58) * mm});
            skLineSegment(sketch, "E3398", {"start": v(-67.8, 8.58) * mm, "end": v(-67.4, 8.4) * mm});
            skLineSegment(sketch, "E3399", {"start": v(-67.4, 8.4) * mm, "end": v(-67, 8.23) * mm});
            skLineSegment(sketch, "E3400", {"start": v(-67, 8.23) * mm, "end": v(-65.7, 7.72) * mm});
            skLineSegment(sketch, "E3401", {"start": v(-65.7, 7.72) * mm, "end": v(-64.5, 7.5) * mm});
            skLineSegment(sketch, "E3402", {"start": v(-64.5, 7.5) * mm, "end": v(-63.39, 7.55) * mm});
            skLineSegment(sketch, "E3403", {"start": v(-63.39, 7.55) * mm, "end": v(-62.38, 7.84) * mm});
            skLineSegment(sketch, "E3404", {"start": v(-62.38, 7.84) * mm, "end": v(-61.46, 8.36) * mm});
            skLineSegment(sketch, "E3405", {"start": v(-61.46, 8.36) * mm, "end": v(-60.62, 9.1) * mm});
            skLineSegment(sketch, "E3406", {"start": v(-60.62, 9.1) * mm, "end": v(-59.86, 10.03) * mm});
            skLineSegment(sketch, "E3407", {"start": v(-59.86, 10.03) * mm, "end": v(-59.17, 11.15) * mm});
            skLineSegment(sketch, "E3408", {"start": v(-59.17, 11.15) * mm, "end": v(-58.88, 11.7) * mm});
            skLineSegment(sketch, "E3409", {"start": v(-58.88, 11.7) * mm, "end": v(-58.6, 12.26) * mm});
            skLineSegment(sketch, "E3410", {"start": v(-58.6, 12.26) * mm, "end": v(-58.33, 12.82) * mm});
            skLineSegment(sketch, "E3411", {"start": v(-58.33, 12.82) * mm, "end": v(-58.07, 13.4) * mm});
            skLineSegment(sketch, "E3412", {"start": v(-58.07, 13.4) * mm, "end": v(-57.82, 13.96) * mm});
            skLineSegment(sketch, "E3413", {"start": v(-57.82, 13.96) * mm, "end": v(-57.56, 14.53) * mm});
            skLineSegment(sketch, "E3414", {"start": v(-57.56, 14.53) * mm, "end": v(-57.31, 15.1) * mm});
            skLineSegment(sketch, "E3415", {"start": v(-57.31, 15.1) * mm, "end": v(-57.05, 15.67) * mm});
            skLineSegment(sketch, "E3416", {"start": v(-57.05, 15.67) * mm, "end": v(-56, 17.86) * mm});
            skLineSegment(sketch, "E3417", {"start": v(-56, 17.86) * mm, "end": v(-55.06, 19.5) * mm});
            skLineSegment(sketch, "E3418", {"start": v(-55.06, 19.5) * mm, "end": v(-54.11, 20.65) * mm});
            skLineSegment(sketch, "E3419", {"start": v(-54.11, 20.65) * mm, "end": v(-53.07, 21.35) * mm});
            skLineSegment(sketch, "E3420", {"start": v(-53.07, 21.35) * mm, "end": v(-51.85, 21.62) * mm});
            skLineSegment(sketch, "E3421", {"start": v(-51.85, 21.62) * mm, "end": v(-50.34, 21.5) * mm});
            skLineSegment(sketch, "E3422", {"start": v(-50.34, 21.5) * mm, "end": v(-48.46, 21.04) * mm});
            skLineSegment(sketch, "E3423", {"start": v(-48.46, 21.04) * mm, "end": v(-46.1, 20.26) * mm});
            skLineSegment(sketch, "E3424", {"start": v(-46.1, 20.26) * mm, "end": v(-45.35, 20.04) * mm});
            skLineSegment(sketch, "E3425", {"start": v(-45.35, 20.04) * mm, "end": v(-44.65, 19.93) * mm});
            skLineSegment(sketch, "E3426", {"start": v(-44.65, 19.93) * mm, "end": v(-44.01, 19.93) * mm});
            skLineSegment(sketch, "E3427", {"start": v(-44.01, 19.93) * mm, "end": v(-43.42, 20.05) * mm});
            skLineSegment(sketch, "E3428", {"start": v(-43.42, 20.05) * mm, "end": v(-42.86, 20.27) * mm});
            skLineSegment(sketch, "E3429", {"start": v(-42.86, 20.27) * mm, "end": v(-42.33, 20.6) * mm});
            skLineSegment(sketch, "E3430", {"start": v(-42.33, 20.6) * mm, "end": v(-41.82, 21.05) * mm});
            skLineSegment(sketch, "E3431", {"start": v(-41.82, 21.05) * mm, "end": v(-41.33, 21.6) * mm});
            skLineSegment(sketch, "E3432", {"start": v(-41.33, 21.6) * mm, "end": v(-40.5, 22.51) * mm});
            skLineSegment(sketch, "E3433", {"start": v(-40.5, 22.51) * mm, "end": v(-39.78, 23.04) * mm});
            skLineSegment(sketch, "E3434", {"start": v(-39.78, 23.04) * mm, "end": v(-39.16, 23.22) * mm});
            skLineSegment(sketch, "E3435", {"start": v(-39.16, 23.22) * mm, "end": v(-38.64, 23.1) * mm});
            skLineSegment(sketch, "E3436", {"start": v(-38.64, 23.1) * mm, "end": v(-38.2, 22.72) * mm});
            skLineSegment(sketch, "E3437", {"start": v(-38.2, 22.72) * mm, "end": v(-37.82, 22.1) * mm});
            skLineSegment(sketch, "E3438", {"start": v(-37.82, 22.1) * mm, "end": v(-37.5, 21.29) * mm});
            skLineSegment(sketch, "E3439", {"start": v(-37.5, 21.29) * mm, "end": v(-37.23, 20.31) * mm});
            skLineSegment(sketch, "E3440", {"start": v(-37.23, 20.31) * mm, "end": v(-36.77, 18.5) * mm});
            skLineSegment(sketch, "E3441", {"start": v(-36.77, 18.5) * mm, "end": v(-36.29, 16.68) * mm});
            skLineSegment(sketch, "E3442", {"start": v(-36.29, 16.68) * mm, "end": v(-35.77, 14.88) * mm});
            skLineSegment(sketch, "E3443", {"start": v(-35.77, 14.88) * mm, "end": v(-35.21, 13.1) * mm});
            skLineSegment(sketch, "E3444", {"start": v(-35.21, 13.1) * mm, "end": v(-34.6, 11.33) * mm});
            skLineSegment(sketch, "E3445", {"start": v(-34.6, 11.33) * mm, "end": v(-33.94, 9.58) * mm});
            skLineSegment(sketch, "E3446", {"start": v(-33.94, 9.58) * mm, "end": v(-33.2, 7.85) * mm});
            skLineSegment(sketch, "E3447", {"start": v(-33.2, 7.85) * mm, "end": v(-32.4, 6.15) * mm});
            skLineSegment(sketch, "E3448", {"start": v(-32.4, 6.15) * mm, "end": v(-31.8, 4.9) * mm});
            skLineSegment(sketch, "E3449", {"start": v(-31.8, 4.9) * mm, "end": v(-31.15, 3.68) * mm});
            skLineSegment(sketch, "E3450", {"start": v(-31.15, 3.68) * mm, "end": v(-30.46, 2.48) * mm});
            skLineSegment(sketch, "E3451", {"start": v(-30.46, 2.48) * mm, "end": v(-29.7, 1.33) * mm});
            skLineSegment(sketch, "E3452", {"start": v(-29.7, 1.33) * mm, "end": v(-28.87, 0.25) * mm});
            skLineSegment(sketch, "E3453", {"start": v(-28.87, 0.25) * mm, "end": v(-27.94, -0.74) * mm});
            skLineSegment(sketch, "E3454", {"start": v(-27.94, -0.74) * mm, "end": v(-26.89, -1.61) * mm});
            skLineSegment(sketch, "E3455", {"start": v(-26.89, -1.61) * mm, "end": v(-25.7, -2.35) * mm});
            skLineSegment(sketch, "E3456", {"start": v(-25.7, -2.35) * mm, "end": v(-24.55, -3.05) * mm});
            skLineSegment(sketch, "E3457", {"start": v(-24.55, -3.05) * mm, "end": v(-23.7, -3.8) * mm});
            skLineSegment(sketch, "E3458", {"start": v(-23.7, -3.8) * mm, "end": v(-23.14, -4.59) * mm});
            skLineSegment(sketch, "E3459", {"start": v(-23.14, -4.59) * mm, "end": v(-22.85, -5.42) * mm});
            skLineSegment(sketch, "E3460", {"start": v(-22.85, -5.42) * mm, "end": v(-22.82, -6.3) * mm});
            skLineSegment(sketch, "E3461", {"start": v(-22.82, -6.3) * mm, "end": v(-23.02, -7.21) * mm});
            skLineSegment(sketch, "E3462", {"start": v(-23.02, -7.21) * mm, "end": v(-23.45, -8.17) * mm});
            skLineSegment(sketch, "E3463", {"start": v(-23.45, -8.17) * mm, "end": v(-24.1, -9.18) * mm});
            skLineSegment(sketch, "E3464", {"start": v(-24.1, -9.18) * mm, "end": v(-26.7, -13.52) * mm});
            skLineSegment(sketch, "E3465", {"start": v(-26.7, -13.52) * mm, "end": v(-28.44, -17.95) * mm});
            skLineSegment(sketch, "E3466", {"start": v(-28.44, -17.95) * mm, "end": v(-29.47, -22.48) * mm});
            skLineSegment(sketch, "E3467", {"start": v(-29.47, -22.48) * mm, "end": v(-29.91, -27.08) * mm});
            skLineSegment(sketch, "E3468", {"start": v(-29.91, -27.08) * mm, "end": v(-29.9, -31.72) * mm});
            skLineSegment(sketch, "E3469", {"start": v(-29.9, -31.72) * mm, "end": v(-29.6, -36.41) * mm});
            skLineSegment(sketch, "E3470", {"start": v(-29.6, -36.41) * mm, "end": v(-29.1, -41.12) * mm});
            skLineSegment(sketch, "E3471", {"start": v(-29.1, -41.12) * mm, "end": v(-28.59, -45.82) * mm});
            skLineSegment(sketch, "E3472", {"start": v(-28.59, -45.82) * mm, "end": v(-28.51, -46.56) * mm});
            skLineSegment(sketch, "E3473", {"start": v(-28.51, -46.56) * mm, "end": v(-28.42, -47.32) * mm});
            skLineSegment(sketch, "E3474", {"start": v(-28.42, -47.32) * mm, "end": v(-28.29, -48.08) * mm});
            skLineSegment(sketch, "E3475", {"start": v(-28.29, -48.08) * mm, "end": v(-28.08, -48.8) * mm});
            skLineSegment(sketch, "E3476", {"start": v(-28.08, -48.8) * mm, "end": v(-27.76, -49.45) * mm});
            skLineSegment(sketch, "E3477", {"start": v(-27.76, -49.45) * mm, "end": v(-27.3, -49.99) * mm});
            skLineSegment(sketch, "E3478", {"start": v(-27.3, -49.99) * mm, "end": v(-26.68, -50.39) * mm});
            skLineSegment(sketch, "E3479", {"start": v(-26.68, -50.39) * mm, "end": v(-25.87, -50.6) * mm});
            skLineSegment(sketch, "E3480", {"start": v(-25.87, -50.6) * mm, "end": v(-25.1, -50.6) * mm});
            skLineSegment(sketch, "E3481", {"start": v(-25.1, -50.6) * mm, "end": v(-24.49, -50.38) * mm});
            skLineSegment(sketch, "E3482", {"start": v(-24.49, -50.38) * mm, "end": v(-24, -49.98) * mm});
            skLineSegment(sketch, "E3483", {"start": v(-24, -49.98) * mm, "end": v(-23.59, -49.45) * mm});
            skLineSegment(sketch, "E3484", {"start": v(-23.59, -49.45) * mm, "end": v(-23.24, -48.84) * mm});
            skLineSegment(sketch, "E3485", {"start": v(-23.24, -48.84) * mm, "end": v(-22.94, -48.2) * mm});
            skLineSegment(sketch, "E3486", {"start": v(-22.94, -48.2) * mm, "end": v(-22.64, -47.54) * mm});
            skLineSegment(sketch, "E3487", {"start": v(-22.64, -47.54) * mm, "end": v(-22.33, -46.94) * mm});
            skLineSegment(sketch, "E3488", {"start": v(-22.33, -46.94) * mm, "end": v(-22, -46.34) * mm});
            skLineSegment(sketch, "E3489", {"start": v(-22, -46.34) * mm, "end": v(-21.69, -45.73) * mm});
            skLineSegment(sketch, "E3490", {"start": v(-21.69, -45.73) * mm, "end": v(-21.39, -45.1) * mm});
            skLineSegment(sketch, "E3491", {"start": v(-21.39, -45.1) * mm, "end": v(-21.1, -44.49) * mm});
            skLineSegment(sketch, "E3492", {"start": v(-21.1, -44.49) * mm, "end": v(-20.8, -43.86) * mm});
            skLineSegment(sketch, "E3493", {"start": v(-20.8, -43.86) * mm, "end": v(-20.5, -43.24) * mm});
            skLineSegment(sketch, "E3494", {"start": v(-20.5, -43.24) * mm, "end": v(-20.18, -42.63) * mm});
            skLineSegment(sketch, "E3495", {"start": v(-20.18, -42.63) * mm, "end": v(-19.85, -42.04) * mm});
            skLineSegment(sketch, "E3496", {"start": v(-19.85, -42.04) * mm, "end": v(-19.06, -40.53) * mm});
            skLineSegment(sketch, "E3497", {"start": v(-19.06, -40.53) * mm, "end": v(-18.52, -39.04) * mm});
            skLineSegment(sketch, "E3498", {"start": v(-18.52, -39.04) * mm, "end": v(-18.22, -37.58) * mm});
            skLineSegment(sketch, "E3499", {"start": v(-18.22, -37.58) * mm, "end": v(-18.17, -36.14) * mm});
            skLineSegment(sketch, "E3500", {"start": v(-18.17, -36.14) * mm, "end": v(-18.4, -34.72) * mm});
            skLineSegment(sketch, "E3501", {"start": v(-18.4, -34.72) * mm, "end": v(-18.89, -33.32) * mm});
            skLineSegment(sketch, "E3502", {"start": v(-18.89, -33.32) * mm, "end": v(-19.67, -31.94) * mm});
            skLineSegment(sketch, "E3503", {"start": v(-19.67, -31.94) * mm, "end": v(-20.74, -30.57) * mm});
            skLineSegment(sketch, "E3504", {"start": v(-20.74, -30.57) * mm, "end": v(-21.06, -30.2) * mm});
            skLineSegment(sketch, "E3505", {"start": v(-21.06, -30.2) * mm, "end": v(-21.37, -29.8) * mm});
            skLineSegment(sketch, "E3506", {"start": v(-21.37, -29.8) * mm, "end": v(-21.65, -29.4) * mm});
            skLineSegment(sketch, "E3507", {"start": v(-21.65, -29.4) * mm, "end": v(-21.92, -28.97) * mm});
            skLineSegment(sketch, "E3508", {"start": v(-21.92, -28.97) * mm, "end": v(-22.18, -28.54) * mm});
            skLineSegment(sketch, "E3509", {"start": v(-22.18, -28.54) * mm, "end": v(-22.43, -28.1) * mm});
            skLineSegment(sketch, "E3510", {"start": v(-22.43, -28.1) * mm, "end": v(-22.66, -27.65) * mm});
            skLineSegment(sketch, "E3511", {"start": v(-22.66, -27.65) * mm, "end": v(-22.9, -27.21) * mm});
            skLineSegment(sketch, "E3512", {"start": v(-22.9, -27.21) * mm, "end": v(-23.94, -24.82) * mm});
            skLineSegment(sketch, "E3513", {"start": v(-23.94, -24.82) * mm, "end": v(-24.6, -22.49) * mm});
            skLineSegment(sketch, "E3514", {"start": v(-24.6, -22.49) * mm, "end": v(-24.86, -20.21) * mm});
            skLineSegment(sketch, "E3515", {"start": v(-24.86, -20.21) * mm, "end": v(-24.71, -18) * mm});
            skLineSegment(sketch, "E3516", {"start": v(-24.71, -18) * mm, "end": v(-24.16, -15.88) * mm});
            skLineSegment(sketch, "E3517", {"start": v(-24.16, -15.88) * mm, "end": v(-23.18, -13.83) * mm});
            skLineSegment(sketch, "E3518", {"start": v(-23.18, -13.83) * mm, "end": v(-21.78, -11.89) * mm});
            skLineSegment(sketch, "E3519", {"start": v(-21.78, -11.89) * mm, "end": v(-19.95, -10.05) * mm});
            skLineSegment(sketch, "E3520", {"start": v(-19.95, -10.05) * mm, "end": v(-18.63, -8.75) * mm});
            skLineSegment(sketch, "E3521", {"start": v(-18.63, -8.75) * mm, "end": v(-17.62, -7.44) * mm});
            skLineSegment(sketch, "E3522", {"start": v(-17.62, -7.44) * mm, "end": v(-16.9, -6.09) * mm});
            skLineSegment(sketch, "E3523", {"start": v(-16.9, -6.09) * mm, "end": v(-16.47, -4.7) * mm});
            skLineSegment(sketch, "E3524", {"start": v(-16.47, -4.7) * mm, "end": v(-16.32, -3.25) * mm});
            skLineSegment(sketch, "E3525", {"start": v(-16.32, -3.25) * mm, "end": v(-16.42, -1.74) * mm});
            skLineSegment(sketch, "E3526", {"start": v(-16.42, -1.74) * mm, "end": v(-16.79, -0.16) * mm});
            skLineSegment(sketch, "E3527", {"start": v(-16.79, -0.16) * mm, "end": v(-17.4, 1.5) * mm});
            skLineSegment(sketch, "E3528", {"start": v(-17.4, 1.5) * mm, "end": v(-18.6, 4.19) * mm});
            skLineSegment(sketch, "E3529", {"start": v(-18.6, 4.19) * mm, "end": v(-19.87, 6.83) * mm});
            skLineSegment(sketch, "E3530", {"start": v(-19.87, 6.83) * mm, "end": v(-21.22, 9.44) * mm});
            skLineSegment(sketch, "E3531", {"start": v(-21.22, 9.44) * mm, "end": v(-22.64, 12) * mm});
            skLineSegment(sketch, "E3532", {"start": v(-22.64, 12) * mm, "end": v(-24.12, 14.54) * mm});
            skLineSegment(sketch, "E3533", {"start": v(-24.12, 14.54) * mm, "end": v(-25.64, 17.05) * mm});
            skLineSegment(sketch, "E3534", {"start": v(-25.64, 17.05) * mm, "end": v(-27.22, 19.52) * mm});
            skLineSegment(sketch, "E3535", {"start": v(-27.22, 19.52) * mm, "end": v(-28.82, 21.98) * mm});
            skLineSegment(sketch, "E3536", {"start": v(-28.82, 21.98) * mm, "end": v(-29.52, 23.13) * mm});
            skLineSegment(sketch, "E3537", {"start": v(-29.52, 23.13) * mm, "end": v(-29.96, 24.12) * mm});
            skLineSegment(sketch, "E3538", {"start": v(-29.96, 24.12) * mm, "end": v(-30.15, 24.95) * mm});
            skLineSegment(sketch, "E3539", {"start": v(-30.15, 24.95) * mm, "end": v(-30.05, 25.6) * mm});
            skLineSegment(sketch, "E3540", {"start": v(-30.05, 25.6) * mm, "end": v(-29.65, 26.09) * mm});
            skLineSegment(sketch, "E3541", {"start": v(-29.65, 26.09) * mm, "end": v(-28.93, 26.39) * mm});
            skLineSegment(sketch, "E3542", {"start": v(-28.93, 26.39) * mm, "end": v(-27.87, 26.5) * mm});
            skLineSegment(sketch, "E3543", {"start": v(-27.87, 26.5) * mm, "end": v(-26.46, 26.42) * mm});
            skLineSegment(sketch, "E3544", {"start": v(-26.46, 26.42) * mm, "end": v(-25.05, 26.35) * mm});
            skLineSegment(sketch, "E3545", {"start": v(-25.05, 26.35) * mm, "end": v(-23.79, 26.48) * mm});
            skLineSegment(sketch, "E3546", {"start": v(-23.79, 26.48) * mm, "end": v(-22.67, 26.8) * mm});
            skLineSegment(sketch, "E3547", {"start": v(-22.67, 26.8) * mm, "end": v(-21.67, 27.33) * mm});
            skLineSegment(sketch, "E3548", {"start": v(-21.67, 27.33) * mm, "end": v(-20.8, 28.04) * mm});
            skLineSegment(sketch, "E3549", {"start": v(-20.8, 28.04) * mm, "end": v(-20.06, 28.95) * mm});
            skLineSegment(sketch, "E3550", {"start": v(-20.06, 28.95) * mm, "end": v(-19.42, 30.04) * mm});
            skLineSegment(sketch, "E3551", {"start": v(-19.42, 30.04) * mm, "end": v(-18.89, 31.31) * mm});
            skLineSegment(sketch, "E3552", {"start": v(-18.89, 31.31) * mm, "end": v(-18.62, 32.01) * mm});
            skLineSegment(sketch, "E3553", {"start": v(-18.62, 32.01) * mm, "end": v(-18.33, 32.7) * mm});
            skLineSegment(sketch, "E3554", {"start": v(-18.33, 32.7) * mm, "end": v(-18, 33.37) * mm});
            skLineSegment(sketch, "E3555", {"start": v(-18, 33.37) * mm, "end": v(-17.68, 34.05) * mm});
            skLineSegment(sketch, "E3556", {"start": v(-17.68, 34.05) * mm, "end": v(-17.33, 34.71) * mm});
            skLineSegment(sketch, "E3557", {"start": v(-17.33, 34.71) * mm, "end": v(-16.98, 35.38) * mm});
            skLineSegment(sketch, "E3558", {"start": v(-16.98, 35.38) * mm, "end": v(-16.64, 36.05) * mm});
            skLineSegment(sketch, "E3559", {"start": v(-16.64, 36.05) * mm, "end": v(-16.3, 36.72) * mm});
            skLineSegment(sketch, "E3560", {"start": v(-16.3, 36.72) * mm, "end": v(-15.86, 37.47) * mm});
            skLineSegment(sketch, "E3561", {"start": v(-15.86, 37.47) * mm, "end": v(-15.42, 37.98) * mm});
            skLineSegment(sketch, "E3562", {"start": v(-15.42, 37.98) * mm, "end": v(-14.98, 38.26) * mm});
            skLineSegment(sketch, "E3563", {"start": v(-14.98, 38.26) * mm, "end": v(-14.53, 38.33) * mm});
            skLineSegment(sketch, "E3564", {"start": v(-14.53, 38.33) * mm, "end": v(-14.08, 38.2) * mm});
            skLineSegment(sketch, "E3565", {"start": v(-14.08, 38.2) * mm, "end": v(-13.63, 37.89) * mm});
            skLineSegment(sketch, "E3566", {"start": v(-13.63, 37.89) * mm, "end": v(-13.19, 37.4) * mm});
            skLineSegment(sketch, "E3567", {"start": v(-13.19, 37.4) * mm, "end": v(-12.74, 36.76) * mm});
            skLineSegment(sketch, "E3568", {"start": v(-12.74, 36.76) * mm, "end": v(-12.49, 36.33) * mm});
            skLineSegment(sketch, "E3569", {"start": v(-12.49, 36.33) * mm, "end": v(-12.25, 35.9) * mm});
            skLineSegment(sketch, "E3570", {"start": v(-12.25, 35.9) * mm, "end": v(-12.01, 35.45) * mm});
            skLineSegment(sketch, "E3571", {"start": v(-12.01, 35.45) * mm, "end": v(-11.78, 35) * mm});
            skLineSegment(sketch, "E3572", {"start": v(-11.78, 35) * mm, "end": v(-11.55, 34.57) * mm});
            skLineSegment(sketch, "E3573", {"start": v(-11.55, 34.57) * mm, "end": v(-11.3, 34.13) * mm});
            skLineSegment(sketch, "E3574", {"start": v(-11.3, 34.13) * mm, "end": v(-11.06, 33.7) * mm});
            skLineSegment(sketch, "E3575", {"start": v(-11.06, 33.7) * mm, "end": v(-10.79, 33.28) * mm});
            skLineSegment(sketch, "E3576", {"start": v(-10.79, 33.28) * mm, "end": v(-10.19, 32.23) * mm});
            skLineSegment(sketch, "E3577", {"start": v(-10.19, 32.23) * mm, "end": v(-9.65, 31.13) * mm});
            skLineSegment(sketch, "E3578", {"start": v(-9.65, 31.13) * mm, "end": v(-9.12, 30.02) * mm});
            skLineSegment(sketch, "E3579", {"start": v(-9.12, 30.02) * mm, "end": v(-8.53, 28.96) * mm});
            skLineSegment(sketch, "E3580", {"start": v(-8.53, 28.96) * mm, "end": v(-7.82, 28.02) * mm});
            skLineSegment(sketch, "E3581", {"start": v(-7.82, 28.02) * mm, "end": v(-6.93, 27.25) * mm});
            skLineSegment(sketch, "E3582", {"start": v(-6.93, 27.25) * mm, "end": v(-5.78, 26.73) * mm});
            skLineSegment(sketch, "E3583", {"start": v(-5.78, 26.73) * mm, "end": v(-4.32, 26.5) * mm});
            skLineSegment(sketch, "E3584", {"start": v(-4.32, 26.5) * mm, "end": v(-2.82, 26.61) * mm});
            skLineSegment(sketch, "E3585", {"start": v(-2.82, 26.61) * mm, "end": v(-1.63, 27.06) * mm});
            skLineSegment(sketch, "E3586", {"start": v(-1.63, 27.06) * mm, "end": v(-0.7, 27.76) * mm});
            skLineSegment(sketch, "E3587", {"start": v(-0.7, 27.76) * mm, "end": v(0.06, 28.66) * mm});
            skLineSegment(sketch, "E3588", {"start": v(0.06, 28.66) * mm, "end": v(0.69, 29.68) * mm});
            skLineSegment(sketch, "E3589", {"start": v(0.69, 29.68) * mm, "end": v(1.25, 30.78) * mm});
            skLineSegment(sketch, "E3590", {"start": v(1.25, 30.78) * mm, "end": v(1.8, 31.87) * mm});
            skLineSegment(sketch, "E3591", {"start": v(1.8, 31.87) * mm, "end": v(2.43, 32.9) * mm});
            skLineSegment(sketch, "E3592", {"start": v(2.43, 32.9) * mm, "end": v(2.74, 33.36) * mm});
            skLineSegment(sketch, "E3593", {"start": v(2.74, 33.36) * mm, "end": v(3.04, 33.84) * mm});
            skLineSegment(sketch, "E3594", {"start": v(3.04, 33.84) * mm, "end": v(3.32, 34.32) * mm});
            skLineSegment(sketch, "E3595", {"start": v(3.32, 34.32) * mm, "end": v(3.6, 34.81) * mm});
            skLineSegment(sketch, "E3596", {"start": v(3.6, 34.81) * mm, "end": v(3.88, 35.3) * mm});
            skLineSegment(sketch, "E3597", {"start": v(3.88, 35.3) * mm, "end": v(4.15, 35.8) * mm});
            skLineSegment(sketch, "E3598", {"start": v(4.15, 35.8) * mm, "end": v(4.43, 36.29) * mm});
            skLineSegment(sketch, "E3599", {"start": v(4.43, 36.29) * mm, "end": v(4.7, 36.77) * mm});
            skLineSegment(sketch, "E3600", {"start": v(4.7, 36.77) * mm, "end": v(5.17, 37.47) * mm});
            skLineSegment(sketch, "E3601", {"start": v(5.17, 37.47) * mm, "end": v(5.64, 37.96) * mm});
            skLineSegment(sketch, "E3602", {"start": v(5.64, 37.96) * mm, "end": v(6.1, 38.23) * mm});
            skLineSegment(sketch, "E3603", {"start": v(6.1, 38.23) * mm, "end": v(6.55, 38.3) * mm});
            skLineSegment(sketch, "E3604", {"start": v(6.55, 38.3) * mm, "end": v(7, 38.19) * mm});
            skLineSegment(sketch, "E3605", {"start": v(7, 38.19) * mm, "end": v(7.44, 37.87) * mm});
            skLineSegment(sketch, "E3606", {"start": v(7.44, 37.87) * mm, "end": v(7.87, 37.37) * mm});
            skLineSegment(sketch, "E3607", {"start": v(7.87, 37.37) * mm, "end": v(8.28, 36.69) * mm});
            skLineSegment(sketch, "E3608", {"start": v(8.28, 36.69) * mm, "end": v(8.55, 36.2) * mm});
            skLineSegment(sketch, "E3609", {"start": v(8.55, 36.2) * mm, "end": v(8.8, 35.7) * mm});
            skLineSegment(sketch, "E3610", {"start": v(8.8, 35.7) * mm, "end": v(9.06, 35.19) * mm});
            skLineSegment(sketch, "E3611", {"start": v(9.06, 35.19) * mm, "end": v(9.3, 34.68) * mm});
            skLineSegment(sketch, "E3612", {"start": v(9.3, 34.68) * mm, "end": v(9.54, 34.17) * mm});
            skLineSegment(sketch, "E3613", {"start": v(9.54, 34.17) * mm, "end": v(9.76, 33.65) * mm});
            skLineSegment(sketch, "E3614", {"start": v(9.76, 33.65) * mm, "end": v(9.97, 33.13) * mm});
            skLineSegment(sketch, "E3615", {"start": v(9.97, 33.13) * mm, "end": v(10.15, 32.6) * mm});
            skLineSegment(sketch, "E3616", {"start": v(10.15, 32.6) * mm, "end": v(10.72, 31.1) * mm});
            skLineSegment(sketch, "E3617", {"start": v(10.72, 31.1) * mm, "end": v(11.4, 29.75) * mm});
            skLineSegment(sketch, "E3618", {"start": v(11.4, 29.75) * mm, "end": v(12.19, 28.6) * mm});
            skLineSegment(sketch, "E3619", {"start": v(12.19, 28.6) * mm, "end": v(13.14, 27.66) * mm});
            skLineSegment(sketch, "E3620", {"start": v(13.14, 27.66) * mm, "end": v(14.25, 26.95) * mm});
            skLineSegment(sketch, "E3621", {"start": v(14.25, 26.95) * mm, "end": v(15.56, 26.48) * mm});
            skLineSegment(sketch, "E3622", {"start": v(15.56, 26.48) * mm, "end": v(17.1, 26.29) * mm});
            skLineSegment(sketch, "E3623", {"start": v(17.1, 26.29) * mm, "end": v(18.86, 26.38) * mm});
            skLineSegment(sketch, "E3624", {"start": v(18.86, 26.38) * mm, "end": v(20.03, 26.44) * mm});
            skLineSegment(sketch, "E3625", {"start": v(20.03, 26.44) * mm, "end": v(20.83, 26.3) * mm});
            skLineSegment(sketch, "E3626", {"start": v(20.83, 26.3) * mm, "end": v(21.32, 25.98) * mm});
            skLineSegment(sketch, "E3627", {"start": v(21.32, 25.98) * mm, "end": v(21.52, 25.52) * mm});
            skLineSegment(sketch, "E3628", {"start": v(21.52, 25.52) * mm, "end": v(21.48, 24.95) * mm});
            skLineSegment(sketch, "E3629", {"start": v(21.48, 24.95) * mm, "end": v(21.23, 24.3) * mm});
            skLineSegment(sketch, "E3630", {"start": v(21.23, 24.3) * mm, "end": v(20.8, 23.6) * mm});
            skLineSegment(sketch, "E3631", {"start": v(20.8, 23.6) * mm, "end": v(20.26, 22.9) * mm});
            skLineSegment(sketch, "E3632", {"start": v(20.26, 22.9) * mm, "end": v(18.07, 19.82) * mm});
            skLineSegment(sketch, "E3633", {"start": v(18.07, 19.82) * mm, "end": v(16.53, 16.6) * mm});
            skLineSegment(sketch, "E3634", {"start": v(16.53, 16.6) * mm, "end": v(15.52, 13.24) * mm});
            skLineSegment(sketch, "E3635", {"start": v(15.52, 13.24) * mm, "end": v(14.9, 9.8) * mm});
            skLineSegment(sketch, "E3636", {"start": v(14.9, 9.8) * mm, "end": v(14.57, 6.3) * mm});
            skLineSegment(sketch, "E3637", {"start": v(14.57, 6.3) * mm, "end": v(14.4, 2.77) * mm});
            skLineSegment(sketch, "E3638", {"start": v(14.4, 2.77) * mm, "end": v(14.25, -0.77) * mm});
            skLineSegment(sketch, "E3639", {"start": v(14.25, -0.77) * mm, "end": v(14.02, -4.3) * mm});
            skLineSegment(sketch, "E3640", {"start": v(14.02, -4.3) * mm, "end": v(14.07, -5.24) * mm});
            skLineSegment(sketch, "E3641", {"start": v(14.07, -5.24) * mm, "end": v(14.36, -6.04) * mm});
            skLineSegment(sketch, "E3642", {"start": v(14.36, -6.04) * mm, "end": v(14.84, -6.72) * mm});
            skLineSegment(sketch, "E3643", {"start": v(14.84, -6.72) * mm, "end": v(15.46, -7.32) * mm});
            skLineSegment(sketch, "E3644", {"start": v(15.46, -7.32) * mm, "end": v(16.18, -7.84) * mm});
            skLineSegment(sketch, "E3645", {"start": v(16.18, -7.84) * mm, "end": v(16.94, -8.33) * mm});
            skLineSegment(sketch, "E3646", {"start": v(16.94, -8.33) * mm, "end": v(17.7, -8.81) * mm});
            skLineSegment(sketch, "E3647", {"start": v(17.7, -8.81) * mm, "end": v(18.4, -9.32) * mm});
            skLineSegment(sketch, "E3648", {"start": v(18.4, -9.32) * mm, "end": v(20.44, -10.94) * mm});
            skLineSegment(sketch, "E3649", {"start": v(20.44, -10.94) * mm, "end": v(21.9, -12.23) * mm});
            skLineSegment(sketch, "E3650", {"start": v(21.9, -12.23) * mm, "end": v(22.76, -13.3) * mm});
            skLineSegment(sketch, "E3651", {"start": v(22.76, -13.3) * mm, "end": v(23.06, -14.26) * mm});
            skLineSegment(sketch, "E3652", {"start": v(23.06, -14.26) * mm, "end": v(22.76, -15.21) * mm});
            skLineSegment(sketch, "E3653", {"start": v(22.76, -15.21) * mm, "end": v(21.89, -16.26) * mm});
            skLineSegment(sketch, "E3654", {"start": v(21.89, -16.26) * mm, "end": v(20.43, -17.53) * mm});
            skLineSegment(sketch, "E3655", {"start": v(20.43, -17.53) * mm, "end": v(18.38, -19.11) * mm});
            skLineSegment(sketch, "E3656", {"start": v(18.38, -19.11) * mm, "end": v(18.02, -19.36) * mm});
            skLineSegment(sketch, "E3657", {"start": v(18.02, -19.36) * mm, "end": v(17.63, -19.61) * mm});
            skLineSegment(sketch, "E3658", {"start": v(17.63, -19.61) * mm, "end": v(17.24, -19.88) * mm});
            skLineSegment(sketch, "E3659", {"start": v(17.24, -19.88) * mm, "end": v(16.89, -20.16) * mm});
            skLineSegment(sketch, "E3660", {"start": v(16.89, -20.16) * mm, "end": v(16.6, -20.47) * mm});
            skLineSegment(sketch, "E3661", {"start": v(16.6, -20.47) * mm, "end": v(16.43, -20.82) * mm});
            skLineSegment(sketch, "E3662", {"start": v(16.43, -20.82) * mm, "end": v(16.4, -21.22) * mm});
            skLineSegment(sketch, "E3663", {"start": v(16.4, -21.22) * mm, "end": v(16.53, -21.67) * mm});
            skLineSegment(sketch, "E3664", {"start": v(16.53, -21.67) * mm, "end": v(16.87, -22.2) * mm});
            skLineSegment(sketch, "E3665", {"start": v(16.87, -22.2) * mm, "end": v(17.27, -22.49) * mm});
            skLineSegment(sketch, "E3666", {"start": v(17.27, -22.49) * mm, "end": v(17.7, -22.59) * mm});
            skLineSegment(sketch, "E3667", {"start": v(17.7, -22.59) * mm, "end": v(18.16, -22.54) * mm});
            skLineSegment(sketch, "E3668", {"start": v(18.16, -22.54) * mm, "end": v(18.63, -22.38) * mm});
            skLineSegment(sketch, "E3669", {"start": v(18.63, -22.38) * mm, "end": v(19.1, -22.17) * mm});
            skLineSegment(sketch, "E3670", {"start": v(19.1, -22.17) * mm, "end": v(19.55, -21.93) * mm});
            skLineSegment(sketch, "E3671", {"start": v(19.55, -21.93) * mm, "end": v(19.98, -21.71) * mm});
            skLineSegment(sketch, "E3672", {"start": v(19.98, -21.71) * mm, "end": v(21.72, -20.88) * mm});
            skLineSegment(sketch, "E3673", {"start": v(21.72, -20.88) * mm, "end": v(23.47, -20.04) * mm});
            skLineSegment(sketch, "E3674", {"start": v(23.47, -20.04) * mm, "end": v(25.22, -19.23) * mm});
            skLineSegment(sketch, "E3675", {"start": v(25.22, -19.23) * mm, "end": v(26.98, -18.46) * mm});
            skLineSegment(sketch, "E3676", {"start": v(26.98, -18.46) * mm, "end": v(28.78, -17.77) * mm});
            skLineSegment(sketch, "E3677", {"start": v(28.78, -17.77) * mm, "end": v(30.62, -17.2) * mm});
            skLineSegment(sketch, "E3678", {"start": v(30.62, -17.2) * mm, "end": v(32.5, -16.76) * mm});
            skLineSegment(sketch, "E3679", {"start": v(32.5, -16.76) * mm, "end": v(34.46, -16.49) * mm});
            skLineSegment(sketch, "E3680", {"start": v(34.46, -16.49) * mm, "end": v(34.92, -16.4) * mm});
            skLineSegment(sketch, "E3681", {"start": v(34.92, -16.4) * mm, "end": v(35.33, -16.26) * mm});
            skLineSegment(sketch, "E3682", {"start": v(35.33, -16.26) * mm, "end": v(35.69, -16.04) * mm});
            skLineSegment(sketch, "E3683", {"start": v(35.69, -16.04) * mm, "end": v(36, -15.76) * mm});
            skLineSegment(sketch, "E3684", {"start": v(36, -15.76) * mm, "end": v(36.25, -15.43) * mm});
            skLineSegment(sketch, "E3685", {"start": v(36.25, -15.43) * mm, "end": v(36.44, -15.04) * mm});
            skLineSegment(sketch, "E3686", {"start": v(36.44, -15.04) * mm, "end": v(36.57, -14.6) * mm});
            skLineSegment(sketch, "E3687", {"start": v(36.57, -14.6) * mm, "end": v(36.63, -14.13) * mm});
            skLineSegment(sketch, "E3688", {"start": v(36.63, -14.13) * mm, "end": v(36.62, -13.57) * mm});
            skLineSegment(sketch, "E3689", {"start": v(36.62, -13.57) * mm, "end": v(36.52, -13.08) * mm});
            skLineSegment(sketch, "E3690", {"start": v(36.52, -13.08) * mm, "end": v(36.34, -12.64) * mm});
            skLineSegment(sketch, "E3691", {"start": v(36.34, -12.64) * mm, "end": v(36.09, -12.26) * mm});
            skLineSegment(sketch, "E3692", {"start": v(36.09, -12.26) * mm, "end": v(35.75, -11.94) * mm});
            skLineSegment(sketch, "E3693", {"start": v(35.75, -11.94) * mm, "end": v(35.35, -11.68) * mm});
            skLineSegment(sketch, "E3694", {"start": v(35.35, -11.68) * mm, "end": v(34.89, -11.47) * mm});
            skLineSegment(sketch, "E3695", {"start": v(34.89, -11.47) * mm, "end": v(34.36, -11.32) * mm});
            skLineSegment(sketch, "E3696", {"start": v(34.36, -11.32) * mm, "end": v(34.18, -11.28) * mm});
            skLineSegment(sketch, "E3697", {"start": v(34.18, -11.28) * mm, "end": v(34, -11.25) * mm});
            skLineSegment(sketch, "E3698", {"start": v(34, -11.25) * mm, "end": v(33.8, -11.22) * mm});
            skLineSegment(sketch, "E3699", {"start": v(33.8, -11.22) * mm, "end": v(33.62, -11.2) * mm});
            skLineSegment(sketch, "E3700", {"start": v(33.62, -11.2) * mm, "end": v(33.43, -11.18) * mm});
            skLineSegment(sketch, "E3701", {"start": v(33.43, -11.18) * mm, "end": v(33.25, -11.17) * mm});
            skLineSegment(sketch, "E3702", {"start": v(33.25, -11.17) * mm, "end": v(33.06, -11.15) * mm});
            skLineSegment(sketch, "E3703", {"start": v(33.06, -11.15) * mm, "end": v(32.87, -11.13) * mm});
            skLineSegment(sketch, "E3704", {"start": v(32.87, -11.13) * mm, "end": v(29.53, -10.73) * mm});
            skLineSegment(sketch, "E3705", {"start": v(29.53, -10.73) * mm, "end": v(27.03, -10.3) * mm});
            skLineSegment(sketch, "E3706", {"start": v(27.03, -10.3) * mm, "end": v(25.24, -9.71) * mm});
            skLineSegment(sketch, "E3707", {"start": v(25.24, -9.71) * mm, "end": v(24.04, -8.83) * mm});
            skLineSegment(sketch, "E3708", {"start": v(24.04, -8.83) * mm, "end": v(23.31, -7.5) * mm});
            skLineSegment(sketch, "E3709", {"start": v(23.31, -7.5) * mm, "end": v(22.93, -5.62) * mm});
            skLineSegment(sketch, "E3710", {"start": v(22.93, -5.62) * mm, "end": v(22.76, -3.03) * mm});
            skLineSegment(sketch, "E3711", {"start": v(22.76, -3.03) * mm, "end": v(22.7, 0.4) * mm});
            skLineSegment(sketch, "E3712", {"start": v(22.7, 0.4) * mm, "end": v(22.72, 2.37) * mm});
            skLineSegment(sketch, "E3713", {"start": v(22.72, 2.37) * mm, "end": v(22.79, 4.35) * mm});
            skLineSegment(sketch, "E3714", {"start": v(22.79, 4.35) * mm, "end": v(22.85, 6.34) * mm});
            skLineSegment(sketch, "E3715", {"start": v(22.85, 6.34) * mm, "end": v(22.83, 8.31) * mm});
            skLineSegment(sketch, "E3716", {"start": v(22.83, 8.31) * mm, "end": v(22.67, 10.28) * mm});
            skLineSegment(sketch, "E3717", {"start": v(22.67, 10.28) * mm, "end": v(22.3, 12.22) * mm});
            skLineSegment(sketch, "E3718", {"start": v(22.3, 12.22) * mm, "end": v(21.68, 14.14) * mm});
            skLineSegment(sketch, "E3719", {"start": v(21.68, 14.14) * mm, "end": v(20.73, 16.02) * mm});
            skLineSegment(sketch, "E3720", {"start": v(20.73, 16.02) * mm, "end": v(20.69, 16.84) * mm});
            skLineSegment(sketch, "E3721", {"start": v(20.69, 16.84) * mm, "end": v(21.06, 18.21) * mm});
            skLineSegment(sketch, "E3722", {"start": v(21.06, 18.21) * mm, "end": v(21.75, 19.96) * mm});
            skLineSegment(sketch, "E3723", {"start": v(21.75, 19.96) * mm, "end": v(22.65, 21.87) * mm});
            skLineSegment(sketch, "E3724", {"start": v(22.65, 21.87) * mm, "end": v(23.65, 23.77) * mm});
            skLineSegment(sketch, "E3725", {"start": v(23.65, 23.77) * mm, "end": v(24.64, 25.45) * mm});
            skLineSegment(sketch, "E3726", {"start": v(24.64, 25.45) * mm, "end": v(25.53, 26.71) * mm});
            skLineSegment(sketch, "E3727", {"start": v(25.53, 26.71) * mm, "end": v(26.21, 27.37) * mm});
            skLineSegment(sketch, "E3728", {"start": v(26.21, 27.37) * mm, "end": v(26.53, 27.52) * mm});
            skLineSegment(sketch, "E3729", {"start": v(26.53, 27.52) * mm, "end": v(26.82, 27.6) * mm});
            skLineSegment(sketch, "E3730", {"start": v(26.82, 27.6) * mm, "end": v(27.1, 27.6) * mm});
            skLineSegment(sketch, "E3731", {"start": v(27.1, 27.6) * mm, "end": v(27.36, 27.57) * mm});
            skLineSegment(sketch, "E3732", {"start": v(27.36, 27.57) * mm, "end": v(27.62, 27.47) * mm});
            skLineSegment(sketch, "E3733", {"start": v(27.62, 27.47) * mm, "end": v(27.88, 27.34) * mm});
            skLineSegment(sketch, "E3734", {"start": v(27.88, 27.34) * mm, "end": v(28.13, 27.16) * mm});
            skLineSegment(sketch, "E3735", {"start": v(28.13, 27.16) * mm, "end": v(28.4, 26.95) * mm});
            skLineSegment(sketch, "E3736", {"start": v(28.4, 26.95) * mm, "end": v(29.54, 25.72) * mm});
            skLineSegment(sketch, "E3737", {"start": v(29.54, 25.72) * mm, "end": v(30.55, 24.18) * mm});
            skLineSegment(sketch, "E3738", {"start": v(30.55, 24.18) * mm, "end": v(31.38, 22.41) * mm});
            skLineSegment(sketch, "E3739", {"start": v(31.38, 22.41) * mm, "end": v(32.02, 20.5) * mm});
            skLineSegment(sketch, "E3740", {"start": v(32.02, 20.5) * mm, "end": v(32.44, 18.54) * mm});
            skLineSegment(sketch, "E3741", {"start": v(32.44, 18.54) * mm, "end": v(32.62, 16.6) * mm});
            skLineSegment(sketch, "E3742", {"start": v(32.62, 16.6) * mm, "end": v(32.52, 14.78) * mm});
            skLineSegment(sketch, "E3743", {"start": v(32.52, 14.78) * mm, "end": v(32.14, 13.16) * mm});
            skLineSegment(sketch, "E3744", {"start": v(32.14, 13.16) * mm, "end": v(31.8, 12.06) * mm});
            skLineSegment(sketch, "E3745", {"start": v(31.8, 12.06) * mm, "end": v(31.6, 10.96) * mm});
            skLineSegment(sketch, "E3746", {"start": v(31.6, 10.96) * mm, "end": v(31.5, 9.84) * mm});
            skLineSegment(sketch, "E3747", {"start": v(31.5, 9.84) * mm, "end": v(31.46, 8.73) * mm});
            skLineSegment(sketch, "E3748", {"start": v(31.46, 8.73) * mm, "end": v(31.48, 7.6) * mm});
            skLineSegment(sketch, "E3749", {"start": v(31.48, 7.6) * mm, "end": v(31.53, 6.49) * mm});
            skLineSegment(sketch, "E3750", {"start": v(31.53, 6.49) * mm, "end": v(31.59, 5.37) * mm});
            skLineSegment(sketch, "E3751", {"start": v(31.59, 5.37) * mm, "end": v(31.63, 4.25) * mm});
            skLineSegment(sketch, "E3752", {"start": v(31.63, 4.25) * mm, "end": v(31.67, 3.71) * mm});
            skLineSegment(sketch, "E3753", {"start": v(31.67, 3.71) * mm, "end": v(31.8, 3.22) * mm});
            skLineSegment(sketch, "E3754", {"start": v(31.8, 3.22) * mm, "end": v(31.98, 2.78) * mm});
            skLineSegment(sketch, "E3755", {"start": v(31.98, 2.78) * mm, "end": v(32.25, 2.4) * mm});
            skLineSegment(sketch, "E3756", {"start": v(32.25, 2.4) * mm, "end": v(32.59, 2.07) * mm});
            skLineSegment(sketch, "E3757", {"start": v(32.59, 2.07) * mm, "end": v(33, 1.82) * mm});
            skLineSegment(sketch, "E3758", {"start": v(33, 1.82) * mm, "end": v(33.49, 1.65) * mm});
            skLineSegment(sketch, "E3759", {"start": v(33.49, 1.65) * mm, "end": v(34.04, 1.57) * mm});
            skLineSegment(sketch, "E3760", {"start": v(34.04, 1.57) * mm, "end": v(34.69, 1.58) * mm});
            skLineSegment(sketch, "E3761", {"start": v(34.69, 1.58) * mm, "end": v(35.25, 1.7) * mm});
            skLineSegment(sketch, "E3762", {"start": v(35.25, 1.7) * mm, "end": v(35.74, 1.92) * mm});
            skLineSegment(sketch, "E3763", {"start": v(35.74, 1.92) * mm, "end": v(36.15, 2.24) * mm});
            skLineSegment(sketch, "E3764", {"start": v(36.15, 2.24) * mm, "end": v(36.49, 2.63) * mm});
            skLineSegment(sketch, "E3765", {"start": v(36.49, 2.63) * mm, "end": v(36.74, 3.1) * mm});
            skLineSegment(sketch, "E3766", {"start": v(36.74, 3.1) * mm, "end": v(36.92, 3.65) * mm});
            skLineSegment(sketch, "E3767", {"start": v(36.92, 3.65) * mm, "end": v(37.02, 4.26) * mm});
            skLineSegment(sketch, "E3768", {"start": v(37.02, 4.26) * mm, "end": v(37.13, 5.44) * mm});
            skLineSegment(sketch, "E3769", {"start": v(37.13, 5.44) * mm, "end": v(37.2, 6.62) * mm});
            skLineSegment(sketch, "E3770", {"start": v(37.2, 6.62) * mm, "end": v(37.26, 7.8) * mm});
            skLineSegment(sketch, "E3771", {"start": v(37.26, 7.8) * mm, "end": v(37.26, 8.98) * mm});
            skLineSegment(sketch, "E3772", {"start": v(37.26, 8.98) * mm, "end": v(37.2, 10.16) * mm});
            skLineSegment(sketch, "E3773", {"start": v(37.2, 10.16) * mm, "end": v(37.07, 11.34) * mm});
            skLineSegment(sketch, "E3774", {"start": v(37.07, 11.34) * mm, "end": v(36.85, 12.5) * mm});
            skLineSegment(sketch, "E3775", {"start": v(36.85, 12.5) * mm, "end": v(36.53, 13.67) * mm});
            skLineSegment(sketch, "E3776", {"start": v(36.53, 13.67) * mm, "end": v(36.26, 15.17) * mm});
            skLineSegment(sketch, "E3777", {"start": v(36.26, 15.17) * mm, "end": v(36.28, 16.94) * mm});
            skLineSegment(sketch, "E3778", {"start": v(36.28, 16.94) * mm, "end": v(36.56, 18.87) * mm});
            skLineSegment(sketch, "E3779", {"start": v(36.56, 18.87) * mm, "end": v(37.07, 20.85) * mm});
            skLineSegment(sketch, "E3780", {"start": v(37.07, 20.85) * mm, "end": v(37.76, 22.77) * mm});
            skLineSegment(sketch, "E3781", {"start": v(37.76, 22.77) * mm, "end": v(38.61, 24.52) * mm});
            skLineSegment(sketch, "E3782", {"start": v(38.61, 24.52) * mm, "end": v(39.58, 25.98) * mm});
            skLineSegment(sketch, "E3783", {"start": v(39.58, 25.98) * mm, "end": v(40.63, 27.05) * mm});
            skLineSegment(sketch, "E3784", {"start": v(40.63, 27.05) * mm, "end": v(40.9, 27.25) * mm});
            skLineSegment(sketch, "E3785", {"start": v(40.9, 27.25) * mm, "end": v(41.17, 27.4) * mm});
            skLineSegment(sketch, "E3786", {"start": v(41.17, 27.4) * mm, "end": v(41.43, 27.51) * mm});
            skLineSegment(sketch, "E3787", {"start": v(41.43, 27.51) * mm, "end": v(41.69, 27.57) * mm});
            skLineSegment(sketch, "E3788", {"start": v(41.69, 27.57) * mm, "end": v(41.95, 27.57) * mm});
            skLineSegment(sketch, "E3789", {"start": v(41.95, 27.57) * mm, "end": v(42.23, 27.52) * mm});
            skLineSegment(sketch, "E3790", {"start": v(42.23, 27.52) * mm, "end": v(42.52, 27.41) * mm});
            skLineSegment(sketch, "E3791", {"start": v(42.52, 27.41) * mm, "end": v(42.83, 27.24) * mm});
            skLineSegment(sketch, "E3792", {"start": v(42.83, 27.24) * mm, "end": v(43.92, 26.27) * mm});
            skLineSegment(sketch, "E3793", {"start": v(43.92, 26.27) * mm, "end": v(44.95, 24.81) * mm});
            skLineSegment(sketch, "E3794", {"start": v(44.95, 24.81) * mm, "end": v(45.86, 23.02) * mm});
            skLineSegment(sketch, "E3795", {"start": v(45.86, 23.02) * mm, "end": v(46.62, 21.02) * mm});
            skLineSegment(sketch, "E3796", {"start": v(46.62, 21.02) * mm, "end": v(47.18, 18.94) * mm});
            skLineSegment(sketch, "E3797", {"start": v(47.18, 18.94) * mm, "end": v(47.5, 16.92) * mm});
            skLineSegment(sketch, "E3798", {"start": v(47.5, 16.92) * mm, "end": v(47.5, 15.1) * mm});
            skLineSegment(sketch, "E3799", {"start": v(47.5, 15.1) * mm, "end": v(47.19, 13.61) * mm});
            skLineSegment(sketch, "E3800", {"start": v(47.19, 13.61) * mm, "end": v(46.81, 12.45) * mm});
            skLineSegment(sketch, "E3801", {"start": v(46.81, 12.45) * mm, "end": v(46.57, 11.3) * mm});
            skLineSegment(sketch, "E3802", {"start": v(46.57, 11.3) * mm, "end": v(46.44, 10.12) * mm});
            skLineSegment(sketch, "E3803", {"start": v(46.44, 10.12) * mm, "end": v(46.4, 8.94) * mm});
            skLineSegment(sketch, "E3804", {"start": v(46.4, 8.94) * mm, "end": v(46.41, 7.76) * mm});
            skLineSegment(sketch, "E3805", {"start": v(46.41, 7.76) * mm, "end": v(46.46, 6.58) * mm});
            skLineSegment(sketch, "E3806", {"start": v(46.46, 6.58) * mm, "end": v(46.52, 5.4) * mm});
            skLineSegment(sketch, "E3807", {"start": v(46.52, 5.4) * mm, "end": v(46.57, 4.22) * mm});
            skLineSegment(sketch, "E3808", {"start": v(46.57, 4.22) * mm, "end": v(46.62, 3.69) * mm});
            skLineSegment(sketch, "E3809", {"start": v(46.62, 3.69) * mm, "end": v(46.74, 3.2) * mm});
            skLineSegment(sketch, "E3810", {"start": v(46.74, 3.2) * mm, "end": v(46.94, 2.76) * mm});
            skLineSegment(sketch, "E3811", {"start": v(46.94, 2.76) * mm, "end": v(47.21, 2.37) * mm});
            skLineSegment(sketch, "E3812", {"start": v(47.21, 2.37) * mm, "end": v(47.55, 2.05) * mm});
            skLineSegment(sketch, "E3813", {"start": v(47.55, 2.05) * mm, "end": v(47.97, 1.81) * mm});
            skLineSegment(sketch, "E3814", {"start": v(47.97, 1.81) * mm, "end": v(48.46, 1.64) * mm});
            skLineSegment(sketch, "E3815", {"start": v(48.46, 1.64) * mm, "end": v(49.01, 1.57) * mm});
            skLineSegment(sketch, "E3816", {"start": v(49.01, 1.57) * mm, "end": v(49.66, 1.59) * mm});
            skLineSegment(sketch, "E3817", {"start": v(49.66, 1.59) * mm, "end": v(50.23, 1.72) * mm});
            skLineSegment(sketch, "E3818", {"start": v(50.23, 1.72) * mm, "end": v(50.7, 1.94) * mm});
            skLineSegment(sketch, "E3819", {"start": v(50.7, 1.94) * mm, "end": v(51.1, 2.27) * mm});
            skLineSegment(sketch, "E3820", {"start": v(51.1, 2.27) * mm, "end": v(51.42, 2.67) * mm});
            skLineSegment(sketch, "E3821", {"start": v(51.42, 2.67) * mm, "end": v(51.66, 3.16) * mm});
            skLineSegment(sketch, "E3822", {"start": v(51.66, 3.16) * mm, "end": v(51.82, 3.7) * mm});
            skLineSegment(sketch, "E3823", {"start": v(51.82, 3.7) * mm, "end": v(51.9, 4.32) * mm});
            skLineSegment(sketch, "E3824", {"start": v(51.9, 4.32) * mm, "end": v(51.98, 5.44) * mm});
            skLineSegment(sketch, "E3825", {"start": v(51.98, 5.44) * mm, "end": v(52.05, 6.56) * mm});
            skLineSegment(sketch, "E3826", {"start": v(52.05, 6.56) * mm, "end": v(52.1, 7.68) * mm});
            skLineSegment(sketch, "E3827", {"start": v(52.1, 7.68) * mm, "end": v(52.11, 8.8) * mm});
            skLineSegment(sketch, "E3828", {"start": v(52.11, 8.8) * mm, "end": v(52.07, 9.93) * mm});
            skLineSegment(sketch, "E3829", {"start": v(52.07, 9.93) * mm, "end": v(51.97, 11.04) * mm});
            skLineSegment(sketch, "E3830", {"start": v(51.97, 11.04) * mm, "end": v(51.8, 12.15) * mm});
            skLineSegment(sketch, "E3831", {"start": v(51.8, 12.15) * mm, "end": v(51.51, 13.25) * mm});
            skLineSegment(sketch, "E3832", {"start": v(51.51, 13.25) * mm, "end": v(51.23, 14.87) * mm});
            skLineSegment(sketch, "E3833", {"start": v(51.23, 14.87) * mm, "end": v(51.22, 16.73) * mm});
            skLineSegment(sketch, "E3834", {"start": v(51.22, 16.73) * mm, "end": v(51.47, 18.73) * mm});
            skLineSegment(sketch, "E3835", {"start": v(51.47, 18.73) * mm, "end": v(51.94, 20.76) * mm});
            skLineSegment(sketch, "E3836", {"start": v(51.94, 20.76) * mm, "end": v(52.6, 22.72) * mm});
            skLineSegment(sketch, "E3837", {"start": v(52.6, 22.72) * mm, "end": v(53.41, 24.5) * mm});
            skLineSegment(sketch, "E3838", {"start": v(53.41, 24.5) * mm, "end": v(54.37, 26) * mm});
            skLineSegment(sketch, "E3839", {"start": v(54.37, 26) * mm, "end": v(55.42, 27.1) * mm});
            skLineSegment(sketch, "E3840", {"start": v(55.42, 27.1) * mm, "end": v(55.79, 27.36) * mm});
            skLineSegment(sketch, "E3841", {"start": v(55.79, 27.36) * mm, "end": v(56.15, 27.55) * mm});
            skLineSegment(sketch, "E3842", {"start": v(56.15, 27.55) * mm, "end": v(56.51, 27.67) * mm});
            skLineSegment(sketch, "E3843", {"start": v(56.51, 27.67) * mm, "end": v(56.85, 27.7) * mm});
            skLineSegment(sketch, "E3844", {"start": v(56.85, 27.7) * mm, "end": v(57.17, 27.66) * mm});
            skLineSegment(sketch, "E3845", {"start": v(57.17, 27.66) * mm, "end": v(57.46, 27.52) * mm});
            skLineSegment(sketch, "E3846", {"start": v(57.46, 27.52) * mm, "end": v(57.7, 27.28) * mm});
            skLineSegment(sketch, "E3847", {"start": v(57.7, 27.28) * mm, "end": v(57.92, 26.93) * mm});
            skLineSegment(sketch, "E3848", {"start": v(57.92, 26.93) * mm, "end": v(58.78, 25.32) * mm});
            skLineSegment(sketch, "E3849", {"start": v(58.78, 25.32) * mm, "end": v(59.72, 23.78) * mm});
            skLineSegment(sketch, "E3850", {"start": v(59.72, 23.78) * mm, "end": v(60.67, 22.23) * mm});
            skLineSegment(sketch, "E3851", {"start": v(60.67, 22.23) * mm, "end": v(61.52, 20.65) * mm});
            skLineSegment(sketch, "E3852", {"start": v(61.52, 20.65) * mm, "end": v(62.18, 18.98) * mm});
            skLineSegment(sketch, "E3853", {"start": v(62.18, 18.98) * mm, "end": v(62.56, 17.17) * mm});
            skLineSegment(sketch, "E3854", {"start": v(62.56, 17.17) * mm, "end": v(62.57, 15.16) * mm});
            skLineSegment(sketch, "E3855", {"start": v(62.57, 15.16) * mm, "end": v(62.1, 12.92) * mm});
            skLineSegment(sketch, "E3856", {"start": v(62.1, 12.92) * mm, "end": v(61.59, 10.82) * mm});
            skLineSegment(sketch, "E3857", {"start": v(61.59, 10.82) * mm, "end": v(61.27, 8.65) * mm});
            skLineSegment(sketch, "E3858", {"start": v(61.27, 8.65) * mm, "end": v(61.12, 6.43) * mm});
            skLineSegment(sketch, "E3859", {"start": v(61.12, 6.43) * mm, "end": v(61.09, 4.17) * mm});
            skLineSegment(sketch, "E3860", {"start": v(61.09, 4.17) * mm, "end": v(61.15, 1.89) * mm});
            skLineSegment(sketch, "E3861", {"start": v(61.15, 1.89) * mm, "end": v(61.26, -0.4) * mm});
            skLineSegment(sketch, "E3862", {"start": v(61.26, -0.4) * mm, "end": v(61.38, -2.68) * mm});
            skLineSegment(sketch, "E3863", {"start": v(61.38, -2.68) * mm, "end": v(61.47, -4.94) * mm});
            skLineSegment(sketch, "E3864", {"start": v(61.47, -4.94) * mm, "end": v(61.43, -6.52) * mm});
            skLineSegment(sketch, "E3865", {"start": v(61.43, -6.52) * mm, "end": v(61.2, -7.85) * mm});
            skLineSegment(sketch, "E3866", {"start": v(61.2, -7.85) * mm, "end": v(60.78, -8.93) * mm});
            skLineSegment(sketch, "E3867", {"start": v(60.78, -8.93) * mm, "end": v(60.15, -9.8) * mm});
            skLineSegment(sketch, "E3868", {"start": v(60.15, -9.8) * mm, "end": v(59.3, -10.43) * mm});
            skLineSegment(sketch, "E3869", {"start": v(59.3, -10.43) * mm, "end": v(58.22, -10.86) * mm});
            skLineSegment(sketch, "E3870", {"start": v(58.22, -10.86) * mm, "end": v(56.9, -11.1) * mm});
            skLineSegment(sketch, "E3871", {"start": v(56.9, -11.1) * mm, "end": v(55.35, -11.15) * mm});
            skLineSegment(sketch, "E3872", {"start": v(55.35, -11.15) * mm, "end": v(54.31, -11.08) * mm});
            skLineSegment(sketch, "E3873", {"start": v(54.31, -11.08) * mm, "end": v(53.23, -10.97) * mm});
            skLineSegment(sketch, "E3874", {"start": v(53.23, -10.97) * mm, "end": v(52.13, -10.89) * mm});
            skLineSegment(sketch, "E3875", {"start": v(52.13, -10.89) * mm, "end": v(51.06, -10.9) * mm});
            skLineSegment(sketch, "E3876", {"start": v(51.06, -10.9) * mm, "end": v(50.05, -11.07) * mm});
            skLineSegment(sketch, "E3877", {"start": v(50.05, -11.07) * mm, "end": v(49.13, -11.46) * mm});
            skLineSegment(sketch, "E3878", {"start": v(49.13, -11.46) * mm, "end": v(48.35, -12.15) * mm});
            skLineSegment(sketch, "E3879", {"start": v(48.35, -12.15) * mm, "end": v(47.74, -13.2) * mm});
            skLineSegment(sketch, "E3880", {"start": v(47.74, -13.2) * mm, "end": v(47.32, -14.44) * mm});
            skLineSegment(sketch, "E3881", {"start": v(47.32, -14.44) * mm, "end": v(47.09, -15.7) * mm});
            skLineSegment(sketch, "E3882", {"start": v(47.09, -15.7) * mm, "end": v(47.03, -16.96) * mm});
            skLineSegment(sketch, "E3883", {"start": v(47.03, -16.96) * mm, "end": v(47.15, -18.21) * mm});
            skLineSegment(sketch, "E3884", {"start": v(47.15, -18.21) * mm, "end": v(47.43, -19.46) * mm});
            skLineSegment(sketch, "E3885", {"start": v(47.43, -19.46) * mm, "end": v(47.87, -20.7) * mm});
            skLineSegment(sketch, "E3886", {"start": v(47.87, -20.7) * mm, "end": v(48.46, -21.94) * mm});
            skLineSegment(sketch, "E3887", {"start": v(48.46, -21.94) * mm, "end": v(49.2, -23.15) * mm});
            skLineSegment(sketch, "E3888", {"start": v(49.2, -23.15) * mm, "end": v(50.34, -25.08) * mm});
            skLineSegment(sketch, "E3889", {"start": v(50.34, -25.08) * mm, "end": v(51.2, -27.03) * mm});
            skLineSegment(sketch, "E3890", {"start": v(51.2, -27.03) * mm, "end": v(51.82, -29.01) * mm});
            skLineSegment(sketch, "E3891", {"start": v(51.82, -29.01) * mm, "end": v(52.2, -31.04) * mm});
            skLineSegment(sketch, "E3892", {"start": v(52.2, -31.04) * mm, "end": v(52.37, -33.14) * mm});
            skLineSegment(sketch, "E3893", {"start": v(52.37, -33.14) * mm, "end": v(52.36, -35.32) * mm});
            skLineSegment(sketch, "E3894", {"start": v(52.36, -35.32) * mm, "end": v(52.2, -37.6) * mm});
            skLineSegment(sketch, "E3895", {"start": v(52.2, -37.6) * mm, "end": v(51.9, -39.98) * mm});
            skLineSegment(sketch, "E3896", {"start": v(51.9, -39.98) * mm, "end": v(51.29, -43.23) * mm});
            skLineSegment(sketch, "E3897", {"start": v(51.29, -43.23) * mm, "end": v(50.47, -46.43) * mm});
            skLineSegment(sketch, "E3898", {"start": v(50.47, -46.43) * mm, "end": v(49.56, -49.6) * mm});
            skLineSegment(sketch, "E3899", {"start": v(49.56, -49.6) * mm, "end": v(48.64, -52.79) * mm});
            skLineSegment(sketch, "E3900", {"start": v(48.64, -52.79) * mm, "end": v(47.81, -56) * mm});
            skLineSegment(sketch, "E3901", {"start": v(47.81, -56) * mm, "end": v(47.18, -59.25) * mm});
            skLineSegment(sketch, "E3902", {"start": v(47.18, -59.25) * mm, "end": v(46.83, -62.6) * mm});
            skLineSegment(sketch, "E3903", {"start": v(46.83, -62.6) * mm, "end": v(46.88, -66.05) * mm});
            skLineSegment(sketch, "E3904", {"start": v(46.88, -66.05) * mm, "end": v(47.18, -71.03) * mm});
            skLineSegment(sketch, "E3905", {"start": v(47.18, -71.03) * mm, "end": v(47.35, -76.01) * mm});
            skLineSegment(sketch, "E3906", {"start": v(47.35, -76.01) * mm, "end": v(47.41, -81) * mm});
            skLineSegment(sketch, "E3907", {"start": v(47.41, -81) * mm, "end": v(47.4, -86) * mm});
            skLineSegment(sketch, "E3908", {"start": v(47.4, -86) * mm, "end": v(47.32, -91.01) * mm});
            skLineSegment(sketch, "E3909", {"start": v(47.32, -91.01) * mm, "end": v(47.23, -96.02) * mm});
            skLineSegment(sketch, "E3910", {"start": v(47.23, -96.02) * mm, "end": v(47.14, -101.02) * mm});
            skLineSegment(sketch, "E3911", {"start": v(47.14, -101.02) * mm, "end": v(47.1, -106.02) * mm});
            skLineSegment(sketch, "E3912", {"start": v(47.1, -106.02) * mm, "end": v(47.1, -106.9) * mm});
            skLineSegment(sketch, "E3913", {"start": v(47.1, -106.9) * mm, "end": v(47.1, -107.77) * mm});
            skLineSegment(sketch, "E3914", {"start": v(47.1, -107.77) * mm, "end": v(47.05, -108.63) * mm});
            skLineSegment(sketch, "E3915", {"start": v(47.05, -108.63) * mm, "end": v(46.93, -109.48) * mm});
            skLineSegment(sketch, "E3916", {"start": v(46.93, -109.48) * mm, "end": v(46.7, -110.3) * mm});
            skLineSegment(sketch, "E3917", {"start": v(46.7, -110.3) * mm, "end": v(46.35, -111.07) * mm});
            skLineSegment(sketch, "E3918", {"start": v(46.35, -111.07) * mm, "end": v(45.81, -111.77) * mm});
            skLineSegment(sketch, "E3919", {"start": v(45.81, -111.77) * mm, "end": v(45.07, -112.4) * mm});
            skLineSegment(sketch, "E3920", {"start": v(45.07, -112.4) * mm, "end": v(44.4, -112.8) * mm});
            skLineSegment(sketch, "E3921", {"start": v(44.4, -112.8) * mm, "end": v(43.7, -113.09) * mm});
            skLineSegment(sketch, "E3922", {"start": v(43.7, -113.09) * mm, "end": v(42.98, -113.27) * mm});
            skLineSegment(sketch, "E3923", {"start": v(42.98, -113.27) * mm, "end": v(42.26, -113.35) * mm});
            skLineSegment(sketch, "E3924", {"start": v(42.26, -113.35) * mm, "end": v(41.53, -113.34) * mm});
            skLineSegment(sketch, "E3925", {"start": v(41.53, -113.34) * mm, "end": v(40.8, -113.24) * mm});
            skLineSegment(sketch, "E3926", {"start": v(40.8, -113.24) * mm, "end": v(40.06, -113.05) * mm});
            skLineSegment(sketch, "E3927", {"start": v(40.06, -113.05) * mm, "end": v(39.33, -112.8) * mm});
            skLineSegment(sketch, "E3928", {"start": v(39.33, -112.8) * mm, "end": v(38.51, -112.36) * mm});
            skLineSegment(sketch, "E3929", {"start": v(38.51, -112.36) * mm, "end": v(37.9, -111.82) * mm});
            skLineSegment(sketch, "E3930", {"start": v(37.9, -111.82) * mm, "end": v(37.45, -111.19) * mm});
            skLineSegment(sketch, "E3931", {"start": v(37.45, -111.19) * mm, "end": v(37.16, -110.49) * mm});
            skLineSegment(sketch, "E3932", {"start": v(37.16, -110.49) * mm, "end": v(36.98, -109.73) * mm});
            skLineSegment(sketch, "E3933", {"start": v(36.98, -109.73) * mm, "end": v(36.88, -108.94) * mm});
            skLineSegment(sketch, "E3934", {"start": v(36.88, -108.94) * mm, "end": v(36.85, -108.12) * mm});
            skLineSegment(sketch, "E3935", {"start": v(36.85, -108.12) * mm, "end": v(36.85, -107.3) * mm});
            skLineSegment(sketch, "E3936", {"start": v(36.85, -107.3) * mm, "end": v(36.84, -101.92) * mm});
            skLineSegment(sketch, "E3937", {"start": v(36.84, -101.92) * mm, "end": v(36.85, -96.55) * mm});
            skLineSegment(sketch, "E3938", {"start": v(36.85, -96.55) * mm, "end": v(36.85, -91.17) * mm});
            skLineSegment(sketch, "E3939", {"start": v(36.85, -91.17) * mm, "end": v(36.85, -85.8) * mm});
            skLineSegment(sketch, "E3940", {"start": v(36.85, -85.8) * mm, "end": v(36.85, -80.42) * mm});
            skLineSegment(sketch, "E3941", {"start": v(36.85, -80.42) * mm, "end": v(36.84, -75.05) * mm});
            skLineSegment(sketch, "E3942", {"start": v(36.84, -75.05) * mm, "end": v(36.82, -69.67) * mm});
            skLineSegment(sketch, "E3943", {"start": v(36.82, -69.67) * mm, "end": v(36.79, -64.3) * mm});
            skLineSegment(sketch, "E3944", {"start": v(36.79, -64.3) * mm, "end": v(36.82, -63.14) * mm});
            skLineSegment(sketch, "E3945", {"start": v(36.82, -63.14) * mm, "end": v(36.9, -61.95) * mm});
            skLineSegment(sketch, "E3946", {"start": v(36.9, -61.95) * mm, "end": v(36.97, -60.75) * mm});
            skLineSegment(sketch, "E3947", {"start": v(36.97, -60.75) * mm, "end": v(36.95, -59.58) * mm});
            skLineSegment(sketch, "E3948", {"start": v(36.95, -59.58) * mm, "end": v(36.79, -58.44) * mm});
            skLineSegment(sketch, "E3949", {"start": v(36.79, -58.44) * mm, "end": v(36.41, -57.36) * mm});
            skLineSegment(sketch, "E3950", {"start": v(36.41, -57.36) * mm, "end": v(35.77, -56.36) * mm});
            skLineSegment(sketch, "E3951", {"start": v(35.77, -56.36) * mm, "end": v(34.8, -55.46) * mm});
            skLineSegment(sketch, "E3952", {"start": v(34.8, -55.46) * mm, "end": v(33.2, -54.36) * mm});
            skLineSegment(sketch, "E3953", {"start": v(33.2, -54.36) * mm, "end": v(31.55, -53.32) * mm});
            skLineSegment(sketch, "E3954", {"start": v(31.55, -53.32) * mm, "end": v(29.88, -52.36) * mm});
            skLineSegment(sketch, "E3955", {"start": v(29.88, -52.36) * mm, "end": v(28.16, -51.47) * mm});
            skLineSegment(sketch, "E3956", {"start": v(28.16, -51.47) * mm, "end": v(26.4, -50.67) * mm});
            skLineSegment(sketch, "E3957", {"start": v(26.4, -50.67) * mm, "end": v(24.6, -49.97) * mm});
            skLineSegment(sketch, "E3958", {"start": v(24.6, -49.97) * mm, "end": v(22.77, -49.35) * mm});
            skLineSegment(sketch, "E3959", {"start": v(22.77, -49.35) * mm, "end": v(20.9, -48.85) * mm});
            skLineSegment(sketch, "E3960", {"start": v(20.9, -48.85) * mm, "end": v(20, -49.07) * mm});
            skLineSegment(sketch, "E3961", {"start": v(20, -49.07) * mm, "end": v(18.85, -49.97) * mm});
            skLineSegment(sketch, "E3962", {"start": v(18.85, -49.97) * mm, "end": v(17.54, -51.34) * mm});
            skLineSegment(sketch, "E3963", {"start": v(17.54, -51.34) * mm, "end": v(16.21, -53.02) * mm});
            skLineSegment(sketch, "E3964", {"start": v(16.21, -53.02) * mm, "end": v(15, -54.82) * mm});
            skLineSegment(sketch, "E3965", {"start": v(15, -54.82) * mm, "end": v(14, -56.56) * mm});
            skLineSegment(sketch, "E3966", {"start": v(14, -56.56) * mm, "end": v(13.37, -58.05) * mm});
            skLineSegment(sketch, "E3967", {"start": v(13.37, -58.05) * mm, "end": v(13.23, -59.11) * mm});
            skLineSegment(sketch, "E3968", {"start": v(13.23, -59.11) * mm, "end": v(13.34, -59.5) * mm});
            skLineSegment(sketch, "E3969", {"start": v(13.34, -59.5) * mm, "end": v(13.49, -59.79) * mm});
            skLineSegment(sketch, "E3970", {"start": v(13.49, -59.79) * mm, "end": v(13.68, -60) * mm});
            skLineSegment(sketch, "E3971", {"start": v(13.68, -60) * mm, "end": v(13.9, -60.16) * mm});
            skLineSegment(sketch, "E3972", {"start": v(13.9, -60.16) * mm, "end": v(14.16, -60.23) * mm});
            skLineSegment(sketch, "E3973", {"start": v(14.16, -60.23) * mm, "end": v(14.44, -60.24) * mm});
            skLineSegment(sketch, "E3974", {"start": v(14.44, -60.24) * mm, "end": v(14.74, -60.19) * mm});
            skLineSegment(sketch, "E3975", {"start": v(14.74, -60.19) * mm, "end": v(15.06, -60.07) * mm});
            skLineSegment(sketch, "E3976", {"start": v(15.06, -60.07) * mm, "end": v(15.5, -59.86) * mm});
            skLineSegment(sketch, "E3977", {"start": v(15.5, -59.86) * mm, "end": v(15.94, -59.62) * mm});
            skLineSegment(sketch, "E3978", {"start": v(15.94, -59.62) * mm, "end": v(16.37, -59.38) * mm});
            skLineSegment(sketch, "E3979", {"start": v(16.37, -59.38) * mm, "end": v(16.8, -59.13) * mm});
            skLineSegment(sketch, "E3980", {"start": v(16.8, -59.13) * mm, "end": v(17.23, -58.87) * mm});
            skLineSegment(sketch, "E3981", {"start": v(17.23, -58.87) * mm, "end": v(17.66, -58.61) * mm});
            skLineSegment(sketch, "E3982", {"start": v(17.66, -58.61) * mm, "end": v(18.08, -58.35) * mm});
            skLineSegment(sketch, "E3983", {"start": v(18.08, -58.35) * mm, "end": v(18.5, -58.1) * mm});
            skLineSegment(sketch, "E3984", {"start": v(18.5, -58.1) * mm, "end": v(19.13, -57.75) * mm});
            skLineSegment(sketch, "E3985", {"start": v(19.13, -57.75) * mm, "end": v(19.76, -57.45) * mm});
            skLineSegment(sketch, "E3986", {"start": v(19.76, -57.45) * mm, "end": v(20.39, -57.22) * mm});
            skLineSegment(sketch, "E3987", {"start": v(20.39, -57.22) * mm, "end": v(21.03, -57.09) * mm});
            skLineSegment(sketch, "E3988", {"start": v(21.03, -57.09) * mm, "end": v(21.67, -57.05) * mm});
            skLineSegment(sketch, "E3989", {"start": v(21.67, -57.05) * mm, "end": v(22.32, -57.14) * mm});
            skLineSegment(sketch, "E3990", {"start": v(22.32, -57.14) * mm, "end": v(22.97, -57.37) * mm});
            skLineSegment(sketch, "E3991", {"start": v(22.97, -57.37) * mm, "end": v(23.64, -57.76) * mm});
            skLineSegment(sketch, "E3992", {"start": v(23.64, -57.76) * mm, "end": v(24.22, -58.25) * mm});
            skLineSegment(sketch, "E3993", {"start": v(24.22, -58.25) * mm, "end": v(24.66, -58.79) * mm});
            skLineSegment(sketch, "E3994", {"start": v(24.66, -58.79) * mm, "end": v(24.97, -59.37) * mm});
            skLineSegment(sketch, "E3995", {"start": v(24.97, -59.37) * mm, "end": v(25.17, -59.98) * mm});
            skLineSegment(sketch, "E3996", {"start": v(25.17, -59.98) * mm, "end": v(25.26, -60.63) * mm});
            skLineSegment(sketch, "E3997", {"start": v(25.26, -60.63) * mm, "end": v(25.27, -61.3) * mm});
            skLineSegment(sketch, "E3998", {"start": v(25.27, -61.3) * mm, "end": v(25.21, -61.99) * mm});
            skLineSegment(sketch, "E3999", {"start": v(25.21, -61.99) * mm, "end": v(25.1, -62.7) * mm});
            skLineSegment(sketch, "E4000", {"start": v(25.1, -62.7) * mm, "end": v(25.02, -63.06) * mm});
            skLineSegment(sketch, "E4001", {"start": v(25.02, -63.06) * mm, "end": v(24.95, -63.43) * mm});
            skLineSegment(sketch, "E4002", {"start": v(24.95, -63.43) * mm, "end": v(24.87, -63.8) * mm});
            skLineSegment(sketch, "E4003", {"start": v(24.87, -63.8) * mm, "end": v(24.8, -64.16) * mm});
            skLineSegment(sketch, "E4004", {"start": v(24.8, -64.16) * mm, "end": v(24.72, -64.53) * mm});
            skLineSegment(sketch, "E4005", {"start": v(24.72, -64.53) * mm, "end": v(24.63, -64.9) * mm});
            skLineSegment(sketch, "E4006", {"start": v(24.63, -64.9) * mm, "end": v(24.53, -65.26) * mm});
            skLineSegment(sketch, "E4007", {"start": v(24.53, -65.26) * mm, "end": v(24.43, -65.61) * mm});
            skLineSegment(sketch, "E4008", {"start": v(24.43, -65.61) * mm, "end": v(24.15, -66.74) * mm});
            skLineSegment(sketch, "E4009", {"start": v(24.15, -66.74) * mm, "end": v(24.03, -67.76) * mm});
            skLineSegment(sketch, "E4010", {"start": v(24.03, -67.76) * mm, "end": v(24.1, -68.66) * mm});
            skLineSegment(sketch, "E4011", {"start": v(24.1, -68.66) * mm, "end": v(24.38, -69.45) * mm});
            skLineSegment(sketch, "E4012", {"start": v(24.38, -69.45) * mm, "end": v(24.86, -70.11) * mm});
            skLineSegment(sketch, "E4013", {"start": v(24.86, -70.11) * mm, "end": v(25.58, -70.65) * mm});
            skLineSegment(sketch, "E4014", {"start": v(25.58, -70.65) * mm, "end": v(26.54, -71.04) * mm});
            skLineSegment(sketch, "E4015", {"start": v(26.54, -71.04) * mm, "end": v(27.77, -71.29) * mm});
            skLineSegment(sketch, "E4016", {"start": v(27.77, -71.29) * mm, "end": v(29.27, -71.6) * mm});
            skLineSegment(sketch, "E4017", {"start": v(29.27, -71.6) * mm, "end": v(30.54, -72.13) * mm});
            skLineSegment(sketch, "E4018", {"start": v(30.54, -72.13) * mm, "end": v(31.58, -72.83) * mm});
            skLineSegment(sketch, "E4019", {"start": v(31.58, -72.83) * mm, "end": v(32.4, -73.72) * mm});
            skLineSegment(sketch, "E4020", {"start": v(32.4, -73.72) * mm, "end": v(32.98, -74.76) * mm});
            skLineSegment(sketch, "E4021", {"start": v(32.98, -74.76) * mm, "end": v(33.34, -75.95) * mm});
            skLineSegment(sketch, "E4022", {"start": v(33.34, -75.95) * mm, "end": v(33.48, -77.26) * mm});
            skLineSegment(sketch, "E4023", {"start": v(33.48, -77.26) * mm, "end": v(33.4, -78.7) * mm});
            skLineSegment(sketch, "E4024", {"start": v(33.4, -78.7) * mm, "end": v(33, -82.12) * mm});
            skLineSegment(sketch, "E4025", {"start": v(33, -82.12) * mm, "end": v(32.66, -85.53) * mm});
            skLineSegment(sketch, "E4026", {"start": v(32.66, -85.53) * mm, "end": v(32.42, -88.95) * mm});
            skLineSegment(sketch, "E4027", {"start": v(32.42, -88.95) * mm, "end": v(32.3, -92.36) * mm});
            skLineSegment(sketch, "E4028", {"start": v(32.3, -92.36) * mm, "end": v(32.31, -95.78) * mm});
            skLineSegment(sketch, "E4029", {"start": v(32.31, -95.78) * mm, "end": v(32.48, -99.2) * mm});
            skLineSegment(sketch, "E4030", {"start": v(32.48, -99.2) * mm, "end": v(32.83, -102.6) * mm});
            skLineSegment(sketch, "E4031", {"start": v(32.83, -102.6) * mm, "end": v(33.38, -106.03) * mm});
            skLineSegment(sketch, "E4032", {"start": v(33.38, -106.03) * mm, "end": v(33.47, -106.72) * mm});
            skLineSegment(sketch, "E4033", {"start": v(33.47, -106.72) * mm, "end": v(33.47, -107.4) * mm});
            skLineSegment(sketch, "E4034", {"start": v(33.47, -107.4) * mm, "end": v(33.39, -108.08) * mm});
            skLineSegment(sketch, "E4035", {"start": v(33.39, -108.08) * mm, "end": v(33.2, -108.73) * mm});
            skLineSegment(sketch, "E4036", {"start": v(33.2, -108.73) * mm, "end": v(32.9, -109.33) * mm});
            skLineSegment(sketch, "E4037", {"start": v(32.9, -109.33) * mm, "end": v(32.5, -109.87) * mm});
            skLineSegment(sketch, "E4038", {"start": v(32.5, -109.87) * mm, "end": v(31.95, -110.33) * mm});
            skLineSegment(sketch, "E4039", {"start": v(31.95, -110.33) * mm, "end": v(31.28, -110.7) * mm});
            skLineSegment(sketch, "E4040", {"start": v(31.28, -110.7) * mm, "end": v(30.6, -110.9) * mm});
            skLineSegment(sketch, "E4041", {"start": v(30.6, -110.9) * mm, "end": v(29.96, -110.92) * mm});
            skLineSegment(sketch, "E4042", {"start": v(29.96, -110.92) * mm, "end": v(29.38, -110.78) * mm});
            skLineSegment(sketch, "E4043", {"start": v(29.38, -110.78) * mm, "end": v(28.84, -110.51) * mm});
            skLineSegment(sketch, "E4044", {"start": v(28.84, -110.51) * mm, "end": v(28.33, -110.15) * mm});
            skLineSegment(sketch, "E4045", {"start": v(28.33, -110.15) * mm, "end": v(27.86, -109.73) * mm});
            skLineSegment(sketch, "E4046", {"start": v(27.86, -109.73) * mm, "end": v(27.42, -109.29) * mm});
            skLineSegment(sketch, "E4047", {"start": v(27.42, -109.29) * mm, "end": v(27, -108.85) * mm});
            skLineSegment(sketch, "E4048", {"start": v(27, -108.85) * mm, "end": v(23.8, -105.51) * mm});
            skLineSegment(sketch, "E4049", {"start": v(23.8, -105.51) * mm, "end": v(20.6, -102.17) * mm});
            skLineSegment(sketch, "E4050", {"start": v(20.6, -102.17) * mm, "end": v(17.4, -98.82) * mm});
            skLineSegment(sketch, "E4051", {"start": v(17.4, -98.82) * mm, "end": v(14.22, -95.48) * mm});
            skLineSegment(sketch, "E4052", {"start": v(14.22, -95.48) * mm, "end": v(11.03, -92.13) * mm});
            skLineSegment(sketch, "E4053", {"start": v(11.03, -92.13) * mm, "end": v(7.84, -88.78) * mm});
            skLineSegment(sketch, "E4054", {"start": v(7.84, -88.78) * mm, "end": v(4.65, -85.44) * mm});
            skLineSegment(sketch, "E4055", {"start": v(4.65, -85.44) * mm, "end": v(1.45, -82.1) * mm});
            skLineSegment(sketch, "E4056", {"start": v(1.45, -82.1) * mm, "end": v(1, -81.6) * mm});
            skLineSegment(sketch, "E4057", {"start": v(1, -81.6) * mm, "end": v(0.56, -81.08) * mm});
            skLineSegment(sketch, "E4058", {"start": v(0.56, -81.08) * mm, "end": v(0.11, -80.56) * mm});
            skLineSegment(sketch, "E4059", {"start": v(0.11, -80.56) * mm, "end": v(-0.37, -80.04) * mm});
            skLineSegment(sketch, "E4060", {"start": v(-0.37, -80.04) * mm, "end": v(-0.9, -79.56) * mm});
            skLineSegment(sketch, "E4061", {"start": v(-0.9, -79.56) * mm, "end": v(-1.52, -79.11) * mm});
            skLineSegment(sketch, "E4062", {"start": v(-1.52, -79.11) * mm, "end": v(-2.22, -78.73) * mm});
            skLineSegment(sketch, "E4063", {"start": v(-2.22, -78.73) * mm, "end": v(-3.04, -78.42) * mm});
            skLineSegment(sketch, "E4064", {"start": v(29.92, -29.62) * mm, "end": v(29.23, -29.76) * mm});
            skLineSegment(sketch, "E4065", {"start": v(29.23, -29.76) * mm, "end": v(28.48, -29.84) * mm});
            skLineSegment(sketch, "E4066", {"start": v(28.48, -29.84) * mm, "end": v(27.71, -29.9) * mm});
            skLineSegment(sketch, "E4067", {"start": v(27.71, -29.9) * mm, "end": v(26.96, -29.98) * mm});
            skLineSegment(sketch, "E4068", {"start": v(26.96, -29.98) * mm, "end": v(26.26, -30.15) * mm});
            skLineSegment(sketch, "E4069", {"start": v(26.26, -30.15) * mm, "end": v(25.63, -30.43) * mm});
            skLineSegment(sketch, "E4070", {"start": v(25.63, -30.43) * mm, "end": v(25.13, -30.88) * mm});
            skLineSegment(sketch, "E4071", {"start": v(25.13, -30.88) * mm, "end": v(24.77, -31.55) * mm});
            skLineSegment(sketch, "E4072", {"start": v(24.77, -31.55) * mm, "end": v(24.6, -32.43) * mm});
            skLineSegment(sketch, "E4073", {"start": v(24.6, -32.43) * mm, "end": v(24.7, -33.2) * mm});
            skLineSegment(sketch, "E4074", {"start": v(24.7, -33.2) * mm, "end": v(25.03, -33.86) * mm});
            skLineSegment(sketch, "E4075", {"start": v(25.03, -33.86) * mm, "end": v(25.52, -34.44) * mm});
            skLineSegment(sketch, "E4076", {"start": v(25.52, -34.44) * mm, "end": v(26.14, -34.96) * mm});
            skLineSegment(sketch, "E4077", {"start": v(26.14, -34.96) * mm, "end": v(26.82, -35.43) * mm});
            skLineSegment(sketch, "E4078", {"start": v(26.82, -35.43) * mm, "end": v(27.53, -35.87) * mm});
            skLineSegment(sketch, "E4079", {"start": v(27.53, -35.87) * mm, "end": v(28.2, -36.3) * mm});
            skLineSegment(sketch, "E4080", {"start": v(28.2, -36.3) * mm, "end": v(28.61, -36.57) * mm});
            skLineSegment(sketch, "E4081", {"start": v(28.61, -36.57) * mm, "end": v(29.04, -36.8) * mm});
            skLineSegment(sketch, "E4082", {"start": v(29.04, -36.8) * mm, "end": v(29.48, -37.03) * mm});
            skLineSegment(sketch, "E4083", {"start": v(29.48, -37.03) * mm, "end": v(29.93, -37.23) * mm});
            skLineSegment(sketch, "E4084", {"start": v(29.93, -37.23) * mm, "end": v(30.38, -37.42) * mm});
            skLineSegment(sketch, "E4085", {"start": v(30.38, -37.42) * mm, "end": v(30.85, -37.6) * mm});
            skLineSegment(sketch, "E4086", {"start": v(30.85, -37.6) * mm, "end": v(31.3, -37.78) * mm});
            skLineSegment(sketch, "E4087", {"start": v(31.3, -37.78) * mm, "end": v(31.77, -37.95) * mm});
            skLineSegment(sketch, "E4088", {"start": v(31.77, -37.95) * mm, "end": v(32.43, -38.18) * mm});
            skLineSegment(sketch, "E4089", {"start": v(32.43, -38.18) * mm, "end": v(33.1, -38.39) * mm});
            skLineSegment(sketch, "E4090", {"start": v(33.1, -38.39) * mm, "end": v(33.77, -38.53) * mm});
            skLineSegment(sketch, "E4091", {"start": v(33.77, -38.53) * mm, "end": v(34.41, -38.56) * mm});
            skLineSegment(sketch, "E4092", {"start": v(34.41, -38.56) * mm, "end": v(35.02, -38.46) * mm});
            skLineSegment(sketch, "E4093", {"start": v(35.02, -38.46) * mm, "end": v(35.57, -38.19) * mm});
            skLineSegment(sketch, "E4094", {"start": v(35.57, -38.19) * mm, "end": v(36.05, -37.7) * mm});
            skLineSegment(sketch, "E4095", {"start": v(36.05, -37.7) * mm, "end": v(36.43, -36.98) * mm});
            skLineSegment(sketch, "E4096", {"start": v(36.43, -36.98) * mm, "end": v(36.7, -36.2) * mm});
            skLineSegment(sketch, "E4097", {"start": v(36.7, -36.2) * mm, "end": v(36.86, -35.43) * mm});
            skLineSegment(sketch, "E4098", {"start": v(36.86, -35.43) * mm, "end": v(36.92, -34.65) * mm});
            skLineSegment(sketch, "E4099", {"start": v(36.92, -34.65) * mm, "end": v(36.86, -33.89) * mm});
            skLineSegment(sketch, "E4100", {"start": v(36.86, -33.89) * mm, "end": v(36.66, -33.14) * mm});
            skLineSegment(sketch, "E4101", {"start": v(36.66, -33.14) * mm, "end": v(36.33, -32.44) * mm});
            skLineSegment(sketch, "E4102", {"start": v(36.33, -32.44) * mm, "end": v(35.83, -31.77) * mm});
            skLineSegment(sketch, "E4103", {"start": v(35.83, -31.77) * mm, "end": v(35.16, -31.16) * mm});
            skLineSegment(sketch, "E4104", {"start": v(35.16, -31.16) * mm, "end": v(34.58, -30.78) * mm});
            skLineSegment(sketch, "E4105", {"start": v(34.58, -30.78) * mm, "end": v(33.97, -30.47) * mm});
            skLineSegment(sketch, "E4106", {"start": v(33.97, -30.47) * mm, "end": v(33.34, -30.23) * mm});
            skLineSegment(sketch, "E4107", {"start": v(33.34, -30.23) * mm, "end": v(32.7, -30.04) * mm});
            skLineSegment(sketch, "E4108", {"start": v(32.7, -30.04) * mm, "end": v(32.02, -29.9) * mm});
            skLineSegment(sketch, "E4109", {"start": v(32.02, -29.9) * mm, "end": v(31.33, -29.79) * mm});
            skLineSegment(sketch, "E4110", {"start": v(31.33, -29.79) * mm, "end": v(30.63, -29.7) * mm});
            skLineSegment(sketch, "E4111", {"start": v(30.63, -29.7) * mm, "end": v(29.92, -29.62) * mm});
            skLineSegment(sketch, "E4112", {"start": v(0.18, 40.65) * mm, "end": v(-10, 40.65) * mm});
            skLineSegment(sketch, "E4113", {"start": v(-10, 40.65) * mm, "end": v(-20.18, 40.65) * mm});
            skLineSegment(sketch, "E4114", {"start": v(-20.18, 40.65) * mm, "end": v(-30.36, 40.65) * mm});
            skLineSegment(sketch, "E4115", {"start": v(-30.36, 40.65) * mm, "end": v(-40.54, 40.65) * mm});
            skLineSegment(sketch, "E4116", {"start": v(-40.54, 40.65) * mm, "end": v(-50.72, 40.65) * mm});
            skLineSegment(sketch, "E4117", {"start": v(-50.72, 40.65) * mm, "end": v(-60.9, 40.66) * mm});
            skLineSegment(sketch, "E4118", {"start": v(-60.9, 40.66) * mm, "end": v(-71.09, 40.68) * mm});
            skLineSegment(sketch, "E4119", {"start": v(-71.09, 40.68) * mm, "end": v(-81.27, 40.7) * mm});
            skLineSegment(sketch, "E4120", {"start": v(-81.27, 40.7) * mm, "end": v(-82.11, 40.66) * mm});
            skLineSegment(sketch, "E4121", {"start": v(-82.11, 40.66) * mm, "end": v(-83, 40.58) * mm});
            skLineSegment(sketch, "E4122", {"start": v(-83, 40.58) * mm, "end": v(-83.9, 40.52) * mm});
            skLineSegment(sketch, "E4123", {"start": v(-83.9, 40.52) * mm, "end": v(-84.78, 40.52) * mm});
            skLineSegment(sketch, "E4124", {"start": v(-84.78, 40.52) * mm, "end": v(-85.61, 40.66) * mm});
            skLineSegment(sketch, "E4125", {"start": v(-85.61, 40.66) * mm, "end": v(-86.36, 40.99) * mm});
            skLineSegment(sketch, "E4126", {"start": v(-86.36, 40.99) * mm, "end": v(-87, 41.56) * mm});
            skLineSegment(sketch, "E4127", {"start": v(-87, 41.56) * mm, "end": v(-87.49, 42.44) * mm});
            skLineSegment(sketch, "E4128", {"start": v(-87.49, 42.44) * mm, "end": v(-87.86, 43.56) * mm});
            skLineSegment(sketch, "E4129", {"start": v(-87.86, 43.56) * mm, "end": v(-88.11, 44.71) * mm});
            skLineSegment(sketch, "E4130", {"start": v(-88.11, 44.71) * mm, "end": v(-88.26, 45.88) * mm});
            skLineSegment(sketch, "E4131", {"start": v(-88.26, 45.88) * mm, "end": v(-88.3, 47.06) * mm});
            skLineSegment(sketch, "E4132", {"start": v(-88.3, 47.06) * mm, "end": v(-88.23, 48.24) * mm});
            skLineSegment(sketch, "E4133", {"start": v(-88.23, 48.24) * mm, "end": v(-88.07, 49.42) * mm});
            skLineSegment(sketch, "E4134", {"start": v(-88.07, 49.42) * mm, "end": v(-87.81, 50.6) * mm});
            skLineSegment(sketch, "E4135", {"start": v(-87.81, 50.6) * mm, "end": v(-87.48, 51.75) * mm});
            skLineSegment(sketch, "E4136", {"start": v(-87.48, 51.75) * mm, "end": v(-87.2, 52.32) * mm});
            skLineSegment(sketch, "E4137", {"start": v(-87.2, 52.32) * mm, "end": v(-86.84, 52.73) * mm});
            skLineSegment(sketch, "E4138", {"start": v(-86.84, 52.73) * mm, "end": v(-86.39, 53.01) * mm});
            skLineSegment(sketch, "E4139", {"start": v(-86.39, 53.01) * mm, "end": v(-85.88, 53.18) * mm});
            skLineSegment(sketch, "E4140", {"start": v(-85.88, 53.18) * mm, "end": v(-85.33, 53.27) * mm});
            skLineSegment(sketch, "E4141", {"start": v(-85.33, 53.27) * mm, "end": v(-84.75, 53.3) * mm});
            skLineSegment(sketch, "E4142", {"start": v(-84.75, 53.3) * mm, "end": v(-84.18, 53.31) * mm});
            skLineSegment(sketch, "E4143", {"start": v(-84.18, 53.31) * mm, "end": v(-83.61, 53.32) * mm});
            skLineSegment(sketch, "E4144", {"start": v(-83.61, 53.32) * mm, "end": v(-82.24, 53.34) * mm});
            skLineSegment(sketch, "E4145", {"start": v(-82.24, 53.34) * mm, "end": v(-80.86, 53.35) * mm});
            skLineSegment(sketch, "E4146", {"start": v(-80.86, 53.35) * mm, "end": v(-79.5, 53.36) * mm});
            skLineSegment(sketch, "E4147", {"start": v(-79.5, 53.36) * mm, "end": v(-78.12, 53.36) * mm});
            skLineSegment(sketch, "E4148", {"start": v(-78.12, 53.36) * mm, "end": v(-76.74, 53.36) * mm});
            skLineSegment(sketch, "E4149", {"start": v(-76.74, 53.36) * mm, "end": v(-75.37, 53.36) * mm});
            skLineSegment(sketch, "E4150", {"start": v(-75.37, 53.36) * mm, "end": v(-74, 53.36) * mm});
            skLineSegment(sketch, "E4151", {"start": v(-74, 53.36) * mm, "end": v(-72.62, 53.36) * mm});
            skLineSegment(sketch, "E4152", {"start": v(-72.62, 53.36) * mm, "end": v(-53.45, 53.36) * mm});
            skLineSegment(sketch, "E4153", {"start": v(-53.45, 53.36) * mm, "end": v(-34.27, 53.36) * mm});
            skLineSegment(sketch, "E4154", {"start": v(-34.27, 53.36) * mm, "end": v(-15.1, 53.36) * mm});
            skLineSegment(sketch, "E4155", {"start": v(-15.1, 53.36) * mm, "end": v(4.08, 53.36) * mm});
            skLineSegment(sketch, "E4156", {"start": v(4.08, 53.36) * mm, "end": v(23.25, 53.36) * mm});
            skLineSegment(sketch, "E4157", {"start": v(23.25, 53.36) * mm, "end": v(42.43, 53.36) * mm});
            skLineSegment(sketch, "E4158", {"start": v(42.43, 53.36) * mm, "end": v(61.6, 53.36) * mm});
            skLineSegment(sketch, "E4159", {"start": v(61.6, 53.36) * mm, "end": v(80.78, 53.36) * mm});
            skLineSegment(sketch, "E4160", {"start": v(80.78, 53.36) * mm, "end": v(83.23, 53.22) * mm});
            skLineSegment(sketch, "E4161", {"start": v(83.23, 53.22) * mm, "end": v(85.22, 52.8) * mm});
            skLineSegment(sketch, "E4162", {"start": v(85.22, 52.8) * mm, "end": v(86.76, 52.09) * mm});
            skLineSegment(sketch, "E4163", {"start": v(86.76, 52.09) * mm, "end": v(87.86, 51.06) * mm});
            skLineSegment(sketch, "E4164", {"start": v(87.86, 51.06) * mm, "end": v(88.53, 49.7) * mm});
            skLineSegment(sketch, "E4165", {"start": v(88.53, 49.7) * mm, "end": v(88.8, 47.98) * mm});
            skLineSegment(sketch, "E4166", {"start": v(88.8, 47.98) * mm, "end": v(88.68, 45.9) * mm});
            skLineSegment(sketch, "E4167", {"start": v(88.68, 45.9) * mm, "end": v(88.19, 43.44) * mm});
            skLineSegment(sketch, "E4168", {"start": v(88.19, 43.44) * mm, "end": v(87.8, 42.38) * mm});
            skLineSegment(sketch, "E4169", {"start": v(87.8, 42.38) * mm, "end": v(87.27, 41.62) * mm});
            skLineSegment(sketch, "E4170", {"start": v(87.27, 41.62) * mm, "end": v(86.64, 41.12) * mm});
            skLineSegment(sketch, "E4171", {"start": v(86.64, 41.12) * mm, "end": v(85.92, 40.83) * mm});
            skLineSegment(sketch, "E4172", {"start": v(85.92, 40.83) * mm, "end": v(85.13, 40.69) * mm});
            skLineSegment(sketch, "E4173", {"start": v(85.13, 40.69) * mm, "end": v(84.3, 40.65) * mm});
            skLineSegment(sketch, "E4174", {"start": v(84.3, 40.65) * mm, "end": v(83.46, 40.67) * mm});
            skLineSegment(sketch, "E4175", {"start": v(83.46, 40.67) * mm, "end": v(82.62, 40.69) * mm});
            skLineSegment(sketch, "E4176", {"start": v(82.62, 40.69) * mm, "end": v(75.63, 40.67) * mm});
            skLineSegment(sketch, "E4177", {"start": v(75.63, 40.67) * mm, "end": v(68.63, 40.66) * mm});
            skLineSegment(sketch, "E4178", {"start": v(68.63, 40.66) * mm, "end": v(61.64, 40.65) * mm});
            skLineSegment(sketch, "E4179", {"start": v(61.64, 40.65) * mm, "end": v(54.64, 40.65) * mm});
            skLineSegment(sketch, "E4180", {"start": v(54.64, 40.65) * mm, "end": v(47.65, 40.65) * mm});
            skLineSegment(sketch, "E4181", {"start": v(47.65, 40.65) * mm, "end": v(40.65, 40.65) * mm});
            skLineSegment(sketch, "E4182", {"start": v(40.65, 40.65) * mm, "end": v(33.66, 40.65) * mm});
            skLineSegment(sketch, "E4183", {"start": v(33.66, 40.65) * mm, "end": v(26.66, 40.65) * mm});
            skLineSegment(sketch, "E4184", {"start": v(26.66, 40.65) * mm, "end": v(23.35, 40.65) * mm});
            skLineSegment(sketch, "E4185", {"start": v(23.35, 40.65) * mm, "end": v(20.04, 40.65) * mm});
            skLineSegment(sketch, "E4186", {"start": v(20.04, 40.65) * mm, "end": v(16.73, 40.65) * mm});
            skLineSegment(sketch, "E4187", {"start": v(16.73, 40.65) * mm, "end": v(13.42, 40.65) * mm});
            skLineSegment(sketch, "E4188", {"start": v(13.42, 40.65) * mm, "end": v(10.1, 40.65) * mm});
            skLineSegment(sketch, "E4189", {"start": v(10.1, 40.65) * mm, "end": v(6.8, 40.65) * mm});
            skLineSegment(sketch, "E4190", {"start": v(6.8, 40.65) * mm, "end": v(3.49, 40.65) * mm});
            skLineSegment(sketch, "E4191", {"start": v(3.49, 40.65) * mm, "end": v(0.18, 40.65) * mm});
            skLineSegment(sketch, "E4192", {"start": v(-0.98, 221.99) * mm, "end": v(23.31, 220.5) * mm});
            skLineSegment(sketch, "E4193", {"start": v(23.31, 220.5) * mm, "end": v(46.41, 216.68) * mm});
            skLineSegment(sketch, "E4194", {"start": v(46.41, 216.68) * mm, "end": v(68.35, 210.54) * mm});
            skLineSegment(sketch, "E4195", {"start": v(68.35, 210.54) * mm, "end": v(89.16, 202.14) * mm});
            skLineSegment(sketch, "E4196", {"start": v(89.16, 202.14) * mm, "end": v(108.88, 191.51) * mm});
            skLineSegment(sketch, "E4197", {"start": v(108.88, 191.51) * mm, "end": v(127.55, 178.7) * mm});
            skLineSegment(sketch, "E4198", {"start": v(127.55, 178.7) * mm, "end": v(145.19, 163.76) * mm});
            skLineSegment(sketch, "E4199", {"start": v(145.19, 163.76) * mm, "end": v(161.84, 146.72) * mm});
            skLineSegment(sketch, "E4200", {"start": v(161.84, 146.72) * mm, "end": v(165.55, 142.4) * mm});
            skLineSegment(sketch, "E4201", {"start": v(165.55, 142.4) * mm, "end": v(169.12, 137.97) * mm});
            skLineSegment(sketch, "E4202", {"start": v(169.12, 137.97) * mm, "end": v(172.58, 133.47) * mm});
            skLineSegment(sketch, "E4203", {"start": v(172.58, 133.47) * mm, "end": v(176, 128.92) * mm});
            skLineSegment(sketch, "E4204", {"start": v(176, 128.92) * mm, "end": v(179.38, 124.36) * mm});
            skLineSegment(sketch, "E4205", {"start": v(179.38, 124.36) * mm, "end": v(182.8, 119.82) * mm});
            skLineSegment(sketch, "E4206", {"start": v(182.8, 119.82) * mm, "end": v(186.3, 115.34) * mm});
            skLineSegment(sketch, "E4207", {"start": v(186.3, 115.34) * mm, "end": v(189.9, 110.95) * mm});
            skLineSegment(sketch, "E4208", {"start": v(189.9, 110.95) * mm, "end": v(193.22, 107.1) * mm});
            skLineSegment(sketch, "E4209", {"start": v(193.22, 107.1) * mm, "end": v(196.6, 103.34) * mm});
            skLineSegment(sketch, "E4210", {"start": v(196.6, 103.34) * mm, "end": v(200.07, 99.66) * mm});
            skLineSegment(sketch, "E4211", {"start": v(200.07, 99.66) * mm, "end": v(203.63, 96.08) * mm});
            skLineSegment(sketch, "E4212", {"start": v(203.63, 96.08) * mm, "end": v(207.3, 92.61) * mm});
            skLineSegment(sketch, "E4213", {"start": v(207.3, 92.61) * mm, "end": v(211.09, 89.27) * mm});
            skLineSegment(sketch, "E4214", {"start": v(211.09, 89.27) * mm, "end": v(215, 86.06) * mm});
            skLineSegment(sketch, "E4215", {"start": v(215, 86.06) * mm, "end": v(219.07, 83.01) * mm});
            skLineSegment(sketch, "E4216", {"start": v(219.07, 83.01) * mm, "end": v(219.92, 82.35) * mm});
            skLineSegment(sketch, "E4217", {"start": v(219.92, 82.35) * mm, "end": v(220.64, 81.65) * mm});
            skLineSegment(sketch, "E4218", {"start": v(220.64, 81.65) * mm, "end": v(221.25, 80.9) * mm});
            skLineSegment(sketch, "E4219", {"start": v(221.25, 80.9) * mm, "end": v(221.73, 80.11) * mm});
            skLineSegment(sketch, "E4220", {"start": v(221.73, 80.11) * mm, "end": v(222.08, 79.26) * mm});
            skLineSegment(sketch, "E4221", {"start": v(222.08, 79.26) * mm, "end": v(222.31, 78.35) * mm});
            skLineSegment(sketch, "E4222", {"start": v(222.31, 78.35) * mm, "end": v(222.41, 77.35) * mm});
            skLineSegment(sketch, "E4223", {"start": v(222.41, 77.35) * mm, "end": v(222.38, 76.28) * mm});
            skLineSegment(sketch, "E4224", {"start": v(222.38, 76.28) * mm, "end": v(221.95, 72.1) * mm});
            skLineSegment(sketch, "E4225", {"start": v(221.95, 72.1) * mm, "end": v(221.38, 67.94) * mm});
            skLineSegment(sketch, "E4226", {"start": v(221.38, 67.94) * mm, "end": v(220.64, 63.84) * mm});
            skLineSegment(sketch, "E4227", {"start": v(220.64, 63.84) * mm, "end": v(219.7, 59.8) * mm});
            skLineSegment(sketch, "E4228", {"start": v(219.7, 59.8) * mm, "end": v(218.55, 55.81) * mm});
            skLineSegment(sketch, "E4229", {"start": v(218.55, 55.81) * mm, "end": v(217.14, 51.9) * mm});
            skLineSegment(sketch, "E4230", {"start": v(217.14, 51.9) * mm, "end": v(215.47, 48.06) * mm});
            skLineSegment(sketch, "E4231", {"start": v(215.47, 48.06) * mm, "end": v(213.5, 44.3) * mm});
            skLineSegment(sketch, "E4232", {"start": v(213.5, 44.3) * mm, "end": v(209.4, 38.38) * mm});
            skLineSegment(sketch, "E4233", {"start": v(209.4, 38.38) * mm, "end": v(204.66, 33.64) * mm});
            skLineSegment(sketch, "E4234", {"start": v(204.66, 33.64) * mm, "end": v(199.37, 30.11) * mm});
            skLineSegment(sketch, "E4235", {"start": v(199.37, 30.11) * mm, "end": v(193.62, 27.82) * mm});
            skLineSegment(sketch, "E4236", {"start": v(193.62, 27.82) * mm, "end": v(187.52, 26.8) * mm});
            skLineSegment(sketch, "E4237", {"start": v(187.52, 26.8) * mm, "end": v(181.17, 27.06) * mm});
            skLineSegment(sketch, "E4238", {"start": v(181.17, 27.06) * mm, "end": v(174.66, 28.66) * mm});
            skLineSegment(sketch, "E4239", {"start": v(174.66, 28.66) * mm, "end": v(168.1, 31.61) * mm});
            skLineSegment(sketch, "E4240", {"start": v(168.1, 31.61) * mm, "end": v(163.81, 34.2) * mm});
            skLineSegment(sketch, "E4241", {"start": v(163.81, 34.2) * mm, "end": v(159.78, 37.07) * mm});
            skLineSegment(sketch, "E4242", {"start": v(159.78, 37.07) * mm, "end": v(155.98, 40.19) * mm});
            skLineSegment(sketch, "E4243", {"start": v(155.98, 40.19) * mm, "end": v(152.37, 43.52) * mm});
            skLineSegment(sketch, "E4244", {"start": v(152.37, 43.52) * mm, "end": v(148.94, 47.03) * mm});
            skLineSegment(sketch, "E4245", {"start": v(148.94, 47.03) * mm, "end": v(145.67, 50.7) * mm});
            skLineSegment(sketch, "E4246", {"start": v(145.67, 50.7) * mm, "end": v(142.52, 54.51) * mm});
            skLineSegment(sketch, "E4247", {"start": v(142.52, 54.51) * mm, "end": v(139.48, 58.42) * mm});
            skLineSegment(sketch, "E4248", {"start": v(139.48, 58.42) * mm, "end": v(135.65, 63.51) * mm});
            skLineSegment(sketch, "E4249", {"start": v(135.65, 63.51) * mm, "end": v(131.85, 68.62) * mm});
            skLineSegment(sketch, "E4250", {"start": v(131.85, 68.62) * mm, "end": v(128.03, 73.72) * mm});
            skLineSegment(sketch, "E4251", {"start": v(128.03, 73.72) * mm, "end": v(124.17, 78.8) * mm});
            skLineSegment(sketch, "E4252", {"start": v(124.17, 78.8) * mm, "end": v(120.24, 83.8) * mm});
            skLineSegment(sketch, "E4253", {"start": v(120.24, 83.8) * mm, "end": v(116.21, 88.73) * mm});
            skLineSegment(sketch, "E4254", {"start": v(116.21, 88.73) * mm, "end": v(112.05, 93.55) * mm});
            skLineSegment(sketch, "E4255", {"start": v(112.05, 93.55) * mm, "end": v(107.71, 98.24) * mm});
            skLineSegment(sketch, "E4256", {"start": v(107.71, 98.24) * mm, "end": v(99.02, 106.87) * mm});
            skLineSegment(sketch, "E4257", {"start": v(99.02, 106.87) * mm, "end": v(89.98, 114.9) * mm});
            skLineSegment(sketch, "E4258", {"start": v(89.98, 114.9) * mm, "end": v(80.54, 122.28) * mm});
            skLineSegment(sketch, "E4259", {"start": v(80.54, 122.28) * mm, "end": v(70.67, 128.92) * mm});
            skLineSegment(sketch, "E4260", {"start": v(70.67, 128.92) * mm, "end": v(60.32, 134.75) * mm});
            skLineSegment(sketch, "E4261", {"start": v(60.32, 134.75) * mm, "end": v(49.46, 139.68) * mm});
            skLineSegment(sketch, "E4262", {"start": v(49.46, 139.68) * mm, "end": v(38.05, 143.66) * mm});
            skLineSegment(sketch, "E4263", {"start": v(38.05, 143.66) * mm, "end": v(26.05, 146.6) * mm});
            skLineSegment(sketch, "E4264", {"start": v(26.05, 146.6) * mm, "end": v(10.63, 148.75) * mm});
            skLineSegment(sketch, "E4265", {"start": v(10.63, 148.75) * mm, "end": v(-4.37, 149.18) * mm});
            skLineSegment(sketch, "E4266", {"start": v(-4.37, 149.18) * mm, "end": v(-18.95, 147.93) * mm});
            skLineSegment(sketch, "E4267", {"start": v(-18.95, 147.93) * mm, "end": v(-33.13, 145.04) * mm});
            skLineSegment(sketch, "E4268", {"start": v(-33.13, 145.04) * mm, "end": v(-46.9, 140.56) * mm});
            skLineSegment(sketch, "E4269", {"start": v(-46.9, 140.56) * mm, "end": v(-60.29, 134.52) * mm});
            skLineSegment(sketch, "E4270", {"start": v(-60.29, 134.52) * mm, "end": v(-73.29, 126.98) * mm});
            skLineSegment(sketch, "E4271", {"start": v(-73.29, 126.98) * mm, "end": v(-85.9, 117.97) * mm});
            skLineSegment(sketch, "E4272", {"start": v(-85.9, 117.97) * mm, "end": v(-92.85, 112.25) * mm});
            skLineSegment(sketch, "E4273", {"start": v(-92.85, 112.25) * mm, "end": v(-99.47, 106.24) * mm});
            skLineSegment(sketch, "E4274", {"start": v(-99.47, 106.24) * mm, "end": v(-105.8, 99.96) * mm});
            skLineSegment(sketch, "E4275", {"start": v(-105.8, 99.96) * mm, "end": v(-111.85, 93.44) * mm});
            skLineSegment(sketch, "E4276", {"start": v(-111.85, 93.44) * mm, "end": v(-117.68, 86.7) * mm});
            skLineSegment(sketch, "E4277", {"start": v(-117.68, 86.7) * mm, "end": v(-123.29, 79.78) * mm});
            skLineSegment(sketch, "E4278", {"start": v(-123.29, 79.78) * mm, "end": v(-128.72, 72.68) * mm});
            skLineSegment(sketch, "E4279", {"start": v(-128.72, 72.68) * mm, "end": v(-134, 65.44) * mm});
            skLineSegment(sketch, "E4280", {"start": v(-134, 65.44) * mm, "end": v(-136.94, 61.39) * mm});
            skLineSegment(sketch, "E4281", {"start": v(-136.94, 61.39) * mm, "end": v(-139.96, 57.4) * mm});
            skLineSegment(sketch, "E4282", {"start": v(-139.96, 57.4) * mm, "end": v(-143.08, 53.5) * mm});
            skLineSegment(sketch, "E4283", {"start": v(-143.08, 53.5) * mm, "end": v(-146.31, 49.71) * mm});
            skLineSegment(sketch, "E4284", {"start": v(-146.31, 49.71) * mm, "end": v(-149.7, 46.06) * mm});
            skLineSegment(sketch, "E4285", {"start": v(-149.7, 46.06) * mm, "end": v(-153.25, 42.55) * mm});
            skLineSegment(sketch, "E4286", {"start": v(-153.25, 42.55) * mm, "end": v(-156.98, 39.23) * mm});
            skLineSegment(sketch, "E4287", {"start": v(-156.98, 39.23) * mm, "end": v(-160.93, 36.1) * mm});
            skLineSegment(sketch, "E4288", {"start": v(-160.93, 36.1) * mm, "end": v(-164.16, 33.84) * mm});
            skLineSegment(sketch, "E4289", {"start": v(-164.16, 33.84) * mm, "end": v(-167.47, 31.8) * mm});
            skLineSegment(sketch, "E4290", {"start": v(-167.47, 31.8) * mm, "end": v(-170.87, 30.05) * mm});
            skLineSegment(sketch, "E4291", {"start": v(-170.87, 30.05) * mm, "end": v(-174.38, 28.63) * mm});
            skLineSegment(sketch, "E4292", {"start": v(-174.38, 28.63) * mm, "end": v(-178, 27.57) * mm});
            skLineSegment(sketch, "E4293", {"start": v(-178, 27.57) * mm, "end": v(-181.76, 26.93) * mm});
            skLineSegment(sketch, "E4294", {"start": v(-181.76, 26.93) * mm, "end": v(-185.66, 26.75) * mm});
            skLineSegment(sketch, "E4295", {"start": v(-185.66, 26.75) * mm, "end": v(-189.7, 27.09) * mm});
            skLineSegment(sketch, "E4296", {"start": v(-189.7, 27.09) * mm, "end": v(-193.22, 27.8) * mm});
            skLineSegment(sketch, "E4297", {"start": v(-193.22, 27.8) * mm, "end": v(-196.51, 28.88) * mm});
            skLineSegment(sketch, "E4298", {"start": v(-196.51, 28.88) * mm, "end": v(-199.58, 30.3) * mm});
            skLineSegment(sketch, "E4299", {"start": v(-199.58, 30.3) * mm, "end": v(-202.43, 32.05) * mm});
            skLineSegment(sketch, "E4300", {"start": v(-202.43, 32.05) * mm, "end": v(-205.08, 34.1) * mm});
            skLineSegment(sketch, "E4301", {"start": v(-205.08, 34.1) * mm, "end": v(-207.52, 36.45) * mm});
            skLineSegment(sketch, "E4302", {"start": v(-207.52, 36.45) * mm, "end": v(-209.76, 39.08) * mm});
            skLineSegment(sketch, "E4303", {"start": v(-209.76, 39.08) * mm, "end": v(-211.82, 41.96) * mm});
            skLineSegment(sketch, "E4304", {"start": v(-211.82, 41.96) * mm, "end": v(-214.2, 45.94) * mm});
            skLineSegment(sketch, "E4305", {"start": v(-214.2, 45.94) * mm, "end": v(-216.2, 50.04) * mm});
            skLineSegment(sketch, "E4306", {"start": v(-216.2, 50.04) * mm, "end": v(-217.86, 54.25) * mm});
            skLineSegment(sketch, "E4307", {"start": v(-217.86, 54.25) * mm, "end": v(-219.22, 58.55) * mm});
            skLineSegment(sketch, "E4308", {"start": v(-219.22, 58.55) * mm, "end": v(-220.29, 62.94) * mm});
            skLineSegment(sketch, "E4309", {"start": v(-220.29, 62.94) * mm, "end": v(-221.1, 67.4) * mm});
            skLineSegment(sketch, "E4310", {"start": v(-221.1, 67.4) * mm, "end": v(-221.7, 71.93) * mm});
            skLineSegment(sketch, "E4311", {"start": v(-221.7, 71.93) * mm, "end": v(-222.09, 76.52) * mm});
            skLineSegment(sketch, "E4312", {"start": v(-222.09, 76.52) * mm, "end": v(-222.1, 77.43) * mm});
            skLineSegment(sketch, "E4313", {"start": v(-222.1, 77.43) * mm, "end": v(-222.05, 78.29) * mm});
            skLineSegment(sketch, "E4314", {"start": v(-222.05, 78.29) * mm, "end": v(-221.89, 79.1) * mm});
            skLineSegment(sketch, "E4315", {"start": v(-221.89, 79.1) * mm, "end": v(-221.63, 79.87) * mm});
            skLineSegment(sketch, "E4316", {"start": v(-221.63, 79.87) * mm, "end": v(-221.27, 80.6) * mm});
            skLineSegment(sketch, "E4317", {"start": v(-221.27, 80.6) * mm, "end": v(-220.78, 81.28) * mm});
            skLineSegment(sketch, "E4318", {"start": v(-220.78, 81.28) * mm, "end": v(-220.17, 81.93) * mm});
            skLineSegment(sketch, "E4319", {"start": v(-220.17, 81.93) * mm, "end": v(-219.43, 82.55) * mm});
            skLineSegment(sketch, "E4320", {"start": v(-219.43, 82.55) * mm, "end": v(-213.16, 87.4) * mm});
            skLineSegment(sketch, "E4321", {"start": v(-213.16, 87.4) * mm, "end": v(-207.21, 92.56) * mm});
            skLineSegment(sketch, "E4322", {"start": v(-207.21, 92.56) * mm, "end": v(-201.55, 98) * mm});
            skLineSegment(sketch, "E4323", {"start": v(-201.55, 98) * mm, "end": v(-196.15, 103.67) * mm});
            skLineSegment(sketch, "E4324", {"start": v(-196.15, 103.67) * mm, "end": v(-190.96, 109.55) * mm});
            skLineSegment(sketch, "E4325", {"start": v(-190.96, 109.55) * mm, "end": v(-185.96, 115.61) * mm});
            skLineSegment(sketch, "E4326", {"start": v(-185.96, 115.61) * mm, "end": v(-181.12, 121.82) * mm});
            skLineSegment(sketch, "E4327", {"start": v(-181.12, 121.82) * mm, "end": v(-176.4, 128.15) * mm});
            skLineSegment(sketch, "E4328", {"start": v(-176.4, 128.15) * mm, "end": v(-165.8, 141.72) * mm});
            skLineSegment(sketch, "E4329", {"start": v(-165.8, 141.72) * mm, "end": v(-154.53, 154.4) * mm});
            skLineSegment(sketch, "E4330", {"start": v(-154.53, 154.4) * mm, "end": v(-142.53, 166.16) * mm});
            skLineSegment(sketch, "E4331", {"start": v(-142.53, 166.16) * mm, "end": v(-129.79, 176.95) * mm});
            skLineSegment(sketch, "E4332", {"start": v(-129.79, 176.95) * mm, "end": v(-116.27, 186.74) * mm});
            skLineSegment(sketch, "E4333", {"start": v(-116.27, 186.74) * mm, "end": v(-101.94, 195.48) * mm});
            skLineSegment(sketch, "E4334", {"start": v(-101.94, 195.48) * mm, "end": v(-86.79, 203.14) * mm});
            skLineSegment(sketch, "E4335", {"start": v(-86.79, 203.14) * mm, "end": v(-70.77, 209.66) * mm});
            skLineSegment(sketch, "E4336", {"start": v(-70.77, 209.66) * mm, "end": v(-61.02, 212.94) * mm});
            skLineSegment(sketch, "E4337", {"start": v(-61.02, 212.94) * mm, "end": v(-51.78, 215.57) * mm});
            skLineSegment(sketch, "E4338", {"start": v(-51.78, 215.57) * mm, "end": v(-42.93, 217.63) * mm});
            skLineSegment(sketch, "E4339", {"start": v(-42.93, 217.63) * mm, "end": v(-34.37, 219.2) * mm});
            skLineSegment(sketch, "E4340", {"start": v(-34.37, 219.2) * mm, "end": v(-26, 220.33) * mm});
            skLineSegment(sketch, "E4341", {"start": v(-26, 220.33) * mm, "end": v(-17.72, 221.13) * mm});
            skLineSegment(sketch, "E4342", {"start": v(-17.72, 221.13) * mm, "end": v(-9.41, 221.65) * mm});
            skLineSegment(sketch, "E4343", {"start": v(-9.41, 221.65) * mm, "end": v(-0.98, 221.99) * mm});
            skLineSegment(sketch, "E4344", {"start": v(-159.22, 103.53) * mm, "end": v(-159.07, 103.66) * mm});
            skLineSegment(sketch, "E4345", {"start": v(-159.07, 103.66) * mm, "end": v(-158.92, 103.8) * mm});
            skLineSegment(sketch, "E4346", {"start": v(-158.92, 103.8) * mm, "end": v(-158.77, 103.93) * mm});
            skLineSegment(sketch, "E4347", {"start": v(-158.77, 103.93) * mm, "end": v(-158.62, 104.06) * mm});
            skLineSegment(sketch, "E4348", {"start": v(-158.62, 104.06) * mm, "end": v(-158.47, 104.2) * mm});
            skLineSegment(sketch, "E4349", {"start": v(-158.47, 104.2) * mm, "end": v(-158.33, 104.32) * mm});
            skLineSegment(sketch, "E4350", {"start": v(-158.33, 104.32) * mm, "end": v(-158.18, 104.46) * mm});
            skLineSegment(sketch, "E4351", {"start": v(-158.18, 104.46) * mm, "end": v(-158.03, 104.59) * mm});
            skLineSegment(sketch, "E4352", {"start": v(-158.03, 104.59) * mm, "end": v(-155.62, 102.64) * mm});
            skLineSegment(sketch, "E4353", {"start": v(-155.62, 102.64) * mm, "end": v(-153.22, 100.7) * mm});
            skLineSegment(sketch, "E4354", {"start": v(-153.22, 100.7) * mm, "end": v(-150.8, 98.75) * mm});
            skLineSegment(sketch, "E4355", {"start": v(-150.8, 98.75) * mm, "end": v(-148.4, 96.8) * mm});
            skLineSegment(sketch, "E4356", {"start": v(-148.4, 96.8) * mm, "end": v(-146, 94.85) * mm});
            skLineSegment(sketch, "E4357", {"start": v(-146, 94.85) * mm, "end": v(-143.6, 92.88) * mm});
            skLineSegment(sketch, "E4358", {"start": v(-143.6, 92.88) * mm, "end": v(-141.23, 90.9) * mm});
            skLineSegment(sketch, "E4359", {"start": v(-141.23, 90.9) * mm, "end": v(-138.87, 88.9) * mm});
            skLineSegment(sketch, "E4360", {"start": v(-138.87, 88.9) * mm, "end": v(-137.92, 88.17) * mm});
            skLineSegment(sketch, "E4361", {"start": v(-137.92, 88.17) * mm, "end": v(-137.04, 87.66) * mm});
            skLineSegment(sketch, "E4362", {"start": v(-137.04, 87.66) * mm, "end": v(-136.2, 87.37) * mm});
            skLineSegment(sketch, "E4363", {"start": v(-136.2, 87.37) * mm, "end": v(-135.41, 87.32) * mm});
            skLineSegment(sketch, "E4364", {"start": v(-135.41, 87.32) * mm, "end": v(-134.64, 87.5) * mm});
            skLineSegment(sketch, "E4365", {"start": v(-134.64, 87.5) * mm, "end": v(-133.87, 87.9) * mm});
            skLineSegment(sketch, "E4366", {"start": v(-133.87, 87.9) * mm, "end": v(-133.09, 88.55) * mm});
            skLineSegment(sketch, "E4367", {"start": v(-133.09, 88.55) * mm, "end": v(-132.28, 89.43) * mm});
            skLineSegment(sketch, "E4368", {"start": v(-132.28, 89.43) * mm, "end": v(-131.57, 90.4) * mm});
            skLineSegment(sketch, "E4369", {"start": v(-131.57, 90.4) * mm, "end": v(-131.08, 91.3) * mm});
            skLineSegment(sketch, "E4370", {"start": v(-131.08, 91.3) * mm, "end": v(-130.83, 92.15) * mm});
            skLineSegment(sketch, "E4371", {"start": v(-130.83, 92.15) * mm, "end": v(-130.81, 92.95) * mm});
            skLineSegment(sketch, "E4372", {"start": v(-130.81, 92.95) * mm, "end": v(-131.02, 93.74) * mm});
            skLineSegment(sketch, "E4373", {"start": v(-131.02, 93.74) * mm, "end": v(-131.45, 94.5) * mm});
            skLineSegment(sketch, "E4374", {"start": v(-131.45, 94.5) * mm, "end": v(-132.1, 95.28) * mm});
            skLineSegment(sketch, "E4375", {"start": v(-132.1, 95.28) * mm, "end": v(-132.99, 96.06) * mm});
            skLineSegment(sketch, "E4376", {"start": v(-132.99, 96.06) * mm, "end": v(-136.4, 98.8) * mm});
            skLineSegment(sketch, "E4377", {"start": v(-136.4, 98.8) * mm, "end": v(-139.79, 101.55) * mm});
            skLineSegment(sketch, "E4378", {"start": v(-139.79, 101.55) * mm, "end": v(-143.18, 104.3) * mm});
            skLineSegment(sketch, "E4379", {"start": v(-143.18, 104.3) * mm, "end": v(-146.56, 107.07) * mm});
            skLineSegment(sketch, "E4380", {"start": v(-146.56, 107.07) * mm, "end": v(-149.95, 109.84) * mm});
            skLineSegment(sketch, "E4381", {"start": v(-149.95, 109.84) * mm, "end": v(-153.33, 112.6) * mm});
            skLineSegment(sketch, "E4382", {"start": v(-153.33, 112.6) * mm, "end": v(-156.71, 115.37) * mm});
            skLineSegment(sketch, "E4383", {"start": v(-156.71, 115.37) * mm, "end": v(-160.1, 118.13) * mm});
            skLineSegment(sketch, "E4384", {"start": v(-160.1, 118.13) * mm, "end": v(-160.47, 118.45) * mm});
            skLineSegment(sketch, "E4385", {"start": v(-160.47, 118.45) * mm, "end": v(-160.85, 118.77) * mm});
            skLineSegment(sketch, "E4386", {"start": v(-160.85, 118.77) * mm, "end": v(-161.24, 119.07) * mm});
            skLineSegment(sketch, "E4387", {"start": v(-161.24, 119.07) * mm, "end": v(-161.64, 119.34) * mm});
            skLineSegment(sketch, "E4388", {"start": v(-161.64, 119.34) * mm, "end": v(-162.08, 119.54) * mm});
            skLineSegment(sketch, "E4389", {"start": v(-162.08, 119.54) * mm, "end": v(-162.54, 119.66) * mm});
            skLineSegment(sketch, "E4390", {"start": v(-162.54, 119.66) * mm, "end": v(-163.05, 119.68) * mm});
            skLineSegment(sketch, "E4391", {"start": v(-163.05, 119.68) * mm, "end": v(-163.6, 119.56) * mm});
            skLineSegment(sketch, "E4392", {"start": v(-163.6, 119.56) * mm, "end": v(-164.69, 119) * mm});
            skLineSegment(sketch, "E4393", {"start": v(-164.69, 119) * mm, "end": v(-165.7, 118.03) * mm});
            skLineSegment(sketch, "E4394", {"start": v(-165.7, 118.03) * mm, "end": v(-166.61, 116.79) * mm});
            skLineSegment(sketch, "E4395", {"start": v(-166.61, 116.79) * mm, "end": v(-167.36, 115.36) * mm});
            skLineSegment(sketch, "E4396", {"start": v(-167.36, 115.36) * mm, "end": v(-167.91, 113.83) * mm});
            skLineSegment(sketch, "E4397", {"start": v(-167.91, 113.83) * mm, "end": v(-168.22, 112.31) * mm});
            skLineSegment(sketch, "E4398", {"start": v(-168.22, 112.31) * mm, "end": v(-168.24, 110.9) * mm});
            skLineSegment(sketch, "E4399", {"start": v(-168.24, 110.9) * mm, "end": v(-167.92, 109.68) * mm});
            skLineSegment(sketch, "E4400", {"start": v(-167.92, 109.68) * mm, "end": v(-166.65, 106.97) * mm});
            skLineSegment(sketch, "E4401", {"start": v(-166.65, 106.97) * mm, "end": v(-165.37, 104.26) * mm});
            skLineSegment(sketch, "E4402", {"start": v(-165.37, 104.26) * mm, "end": v(-164.08, 101.56) * mm});
            skLineSegment(sketch, "E4403", {"start": v(-164.08, 101.56) * mm, "end": v(-162.79, 98.85) * mm});
            skLineSegment(sketch, "E4404", {"start": v(-162.79, 98.85) * mm, "end": v(-161.5, 96.15) * mm});
            skLineSegment(sketch, "E4405", {"start": v(-161.5, 96.15) * mm, "end": v(-160.22, 93.44) * mm});
            skLineSegment(sketch, "E4406", {"start": v(-160.22, 93.44) * mm, "end": v(-158.96, 90.72) * mm});
            skLineSegment(sketch, "E4407", {"start": v(-158.96, 90.72) * mm, "end": v(-157.7, 88) * mm});
            skLineSegment(sketch, "E4408", {"start": v(-157.7, 88) * mm, "end": v(-157.33, 87.3) * mm});
            skLineSegment(sketch, "E4409", {"start": v(-157.33, 87.3) * mm, "end": v(-156.87, 86.58) * mm});
            skLineSegment(sketch, "E4410", {"start": v(-156.87, 86.58) * mm, "end": v(-156.4, 85.85) * mm});
            skLineSegment(sketch, "E4411", {"start": v(-156.4, 85.85) * mm, "end": v(-155.98, 85.12) * mm});
            skLineSegment(sketch, "E4412", {"start": v(-155.98, 85.12) * mm, "end": v(-155.67, 84.38) * mm});
            skLineSegment(sketch, "E4413", {"start": v(-155.67, 84.38) * mm, "end": v(-155.54, 83.65) * mm});
            skLineSegment(sketch, "E4414", {"start": v(-155.54, 83.65) * mm, "end": v(-155.66, 82.93) * mm});
            skLineSegment(sketch, "E4415", {"start": v(-155.66, 82.93) * mm, "end": v(-156.09, 82.22) * mm});
            skLineSegment(sketch, "E4416", {"start": v(-156.09, 82.22) * mm, "end": v(-156.65, 81.78) * mm});
            skLineSegment(sketch, "E4417", {"start": v(-156.65, 81.78) * mm, "end": v(-157.28, 81.6) * mm});
            skLineSegment(sketch, "E4418", {"start": v(-157.28, 81.6) * mm, "end": v(-157.97, 81.65) * mm});
            skLineSegment(sketch, "E4419", {"start": v(-157.97, 81.65) * mm, "end": v(-158.7, 81.84) * mm});
            skLineSegment(sketch, "E4420", {"start": v(-158.7, 81.84) * mm, "end": v(-159.44, 82.14) * mm});
            skLineSegment(sketch, "E4421", {"start": v(-159.44, 82.14) * mm, "end": v(-160.2, 82.48) * mm});
            skLineSegment(sketch, "E4422", {"start": v(-160.2, 82.48) * mm, "end": v(-160.93, 82.8) * mm});
            skLineSegment(sketch, "E4423", {"start": v(-160.93, 82.8) * mm, "end": v(-161.64, 83.05) * mm});
            skLineSegment(sketch, "E4424", {"start": v(-161.64, 83.05) * mm, "end": v(-164.46, 83.86) * mm});
            skLineSegment(sketch, "E4425", {"start": v(-164.46, 83.86) * mm, "end": v(-167.27, 84.69) * mm});
            skLineSegment(sketch, "E4426", {"start": v(-167.27, 84.69) * mm, "end": v(-170.08, 85.53) * mm});
            skLineSegment(sketch, "E4427", {"start": v(-170.08, 85.53) * mm, "end": v(-172.89, 86.37) * mm});
            skLineSegment(sketch, "E4428", {"start": v(-172.89, 86.37) * mm, "end": v(-175.7, 87.23) * mm});
            skLineSegment(sketch, "E4429", {"start": v(-175.7, 87.23) * mm, "end": v(-178.5, 88.09) * mm});
            skLineSegment(sketch, "E4430", {"start": v(-178.5, 88.09) * mm, "end": v(-181.3, 88.95) * mm});
            skLineSegment(sketch, "E4431", {"start": v(-181.3, 88.95) * mm, "end": v(-184.1, 89.81) * mm});
            skLineSegment(sketch, "E4432", {"start": v(-184.1, 89.81) * mm, "end": v(-185.98, 90.16) * mm});
            skLineSegment(sketch, "E4433", {"start": v(-185.98, 90.16) * mm, "end": v(-187.52, 89.98) * mm});
            skLineSegment(sketch, "E4434", {"start": v(-187.52, 89.98) * mm, "end": v(-188.78, 89.4) * mm});
            skLineSegment(sketch, "E4435", {"start": v(-188.78, 89.4) * mm, "end": v(-189.82, 88.49) * mm});
            skLineSegment(sketch, "E4436", {"start": v(-189.82, 88.49) * mm, "end": v(-190.72, 87.37) * mm});
            skLineSegment(sketch, "E4437", {"start": v(-190.72, 87.37) * mm, "end": v(-191.52, 86.14) * mm});
            skLineSegment(sketch, "E4438", {"start": v(-191.52, 86.14) * mm, "end": v(-192.3, 84.9) * mm});
            skLineSegment(sketch, "E4439", {"start": v(-192.3, 84.9) * mm, "end": v(-193.1, 83.74) * mm});
            skLineSegment(sketch, "E4440", {"start": v(-193.1, 83.74) * mm, "end": v(-193.7, 82.73) * mm});
            skLineSegment(sketch, "E4441", {"start": v(-193.7, 82.73) * mm, "end": v(-193.84, 81.86) * mm});
            skLineSegment(sketch, "E4442", {"start": v(-193.84, 81.86) * mm, "end": v(-193.62, 81.13) * mm});
            skLineSegment(sketch, "E4443", {"start": v(-193.62, 81.13) * mm, "end": v(-193.13, 80.49) * mm});
            skLineSegment(sketch, "E4444", {"start": v(-193.13, 80.49) * mm, "end": v(-192.46, 79.93) * mm});
            skLineSegment(sketch, "E4445", {"start": v(-192.46, 79.93) * mm, "end": v(-191.7, 79.42) * mm});
            skLineSegment(sketch, "E4446", {"start": v(-191.7, 79.42) * mm, "end": v(-190.96, 78.94) * mm});
            skLineSegment(sketch, "E4447", {"start": v(-190.96, 78.94) * mm, "end": v(-190.3, 78.46) * mm});
            skLineSegment(sketch, "E4448", {"start": v(-190.3, 78.46) * mm, "end": v(-187.04, 75.75) * mm});
            skLineSegment(sketch, "E4449", {"start": v(-187.04, 75.75) * mm, "end": v(-183.77, 73.05) * mm});
            skLineSegment(sketch, "E4450", {"start": v(-183.77, 73.05) * mm, "end": v(-180.48, 70.36) * mm});
            skLineSegment(sketch, "E4451", {"start": v(-180.48, 70.36) * mm, "end": v(-177.2, 67.68) * mm});
            skLineSegment(sketch, "E4452", {"start": v(-177.2, 67.68) * mm, "end": v(-173.9, 65) * mm});
            skLineSegment(sketch, "E4453", {"start": v(-173.9, 65) * mm, "end": v(-170.61, 62.31) * mm});
            skLineSegment(sketch, "E4454", {"start": v(-170.61, 62.31) * mm, "end": v(-167.33, 59.62) * mm});
            skLineSegment(sketch, "E4455", {"start": v(-167.33, 59.62) * mm, "end": v(-164.06, 56.91) * mm});
            skLineSegment(sketch, "E4456", {"start": v(-164.06, 56.91) * mm, "end": v(-163.33, 56.34) * mm});
            skLineSegment(sketch, "E4457", {"start": v(-163.33, 56.34) * mm, "end": v(-162.64, 55.9) * mm});
            skLineSegment(sketch, "E4458", {"start": v(-162.64, 55.9) * mm, "end": v(-161.98, 55.6) * mm});
            skLineSegment(sketch, "E4459", {"start": v(-161.98, 55.6) * mm, "end": v(-161.35, 55.49) * mm});
            skLineSegment(sketch, "E4460", {"start": v(-161.35, 55.49) * mm, "end": v(-160.72, 55.56) * mm});
            skLineSegment(sketch, "E4461", {"start": v(-160.72, 55.56) * mm, "end": v(-160.08, 55.84) * mm});
            skLineSegment(sketch, "E4462", {"start": v(-160.08, 55.84) * mm, "end": v(-159.43, 56.35) * mm});
            skLineSegment(sketch, "E4463", {"start": v(-159.43, 56.35) * mm, "end": v(-158.74, 57.11) * mm});
            skLineSegment(sketch, "E4464", {"start": v(-158.74, 57.11) * mm, "end": v(-158.15, 57.93) * mm});
            skLineSegment(sketch, "E4465", {"start": v(-158.15, 57.93) * mm, "end": v(-157.7, 58.7) * mm});
            skLineSegment(sketch, "E4466", {"start": v(-157.7, 58.7) * mm, "end": v(-157.4, 59.42) * mm});
            skLineSegment(sketch, "E4467", {"start": v(-157.4, 59.42) * mm, "end": v(-157.3, 60.12) * mm});
            skLineSegment(sketch, "E4468", {"start": v(-157.3, 60.12) * mm, "end": v(-157.4, 60.8) * mm});
            skLineSegment(sketch, "E4469", {"start": v(-157.4, 60.8) * mm, "end": v(-157.74, 61.48) * mm});
            skLineSegment(sketch, "E4470", {"start": v(-157.74, 61.48) * mm, "end": v(-158.33, 62.15) * mm});
            skLineSegment(sketch, "E4471", {"start": v(-158.33, 62.15) * mm, "end": v(-159.2, 62.83) * mm});
            skLineSegment(sketch, "E4472", {"start": v(-159.2, 62.83) * mm, "end": v(-159.96, 63.36) * mm});
            skLineSegment(sketch, "E4473", {"start": v(-159.96, 63.36) * mm, "end": v(-160.7, 63.93) * mm});
            skLineSegment(sketch, "E4474", {"start": v(-160.7, 63.93) * mm, "end": v(-161.44, 64.5) * mm});
            skLineSegment(sketch, "E4475", {"start": v(-161.44, 64.5) * mm, "end": v(-162.16, 65.1) * mm});
            skLineSegment(sketch, "E4476", {"start": v(-162.16, 65.1) * mm, "end": v(-162.87, 65.71) * mm});
            skLineSegment(sketch, "E4477", {"start": v(-162.87, 65.71) * mm, "end": v(-163.59, 66.32) * mm});
            skLineSegment(sketch, "E4478", {"start": v(-163.59, 66.32) * mm, "end": v(-164.3, 66.93) * mm});
            skLineSegment(sketch, "E4479", {"start": v(-164.3, 66.93) * mm, "end": v(-165.02, 67.53) * mm});
            skLineSegment(sketch, "E4480", {"start": v(-165.02, 67.53) * mm, "end": v(-166.68, 68.9) * mm});
            skLineSegment(sketch, "E4481", {"start": v(-166.68, 68.9) * mm, "end": v(-168.34, 70.28) * mm});
            skLineSegment(sketch, "E4482", {"start": v(-168.34, 70.28) * mm, "end": v(-170.02, 71.66) * mm});
            skLineSegment(sketch, "E4483", {"start": v(-170.02, 71.66) * mm, "end": v(-171.72, 73.07) * mm});
            skLineSegment(sketch, "E4484", {"start": v(-171.72, 73.07) * mm, "end": v(-173.45, 74.5) * mm});
            skLineSegment(sketch, "E4485", {"start": v(-173.45, 74.5) * mm, "end": v(-175.22, 75.97) * mm});
            skLineSegment(sketch, "E4486", {"start": v(-175.22, 75.97) * mm, "end": v(-177.03, 77.47) * mm});
            skLineSegment(sketch, "E4487", {"start": v(-177.03, 77.47) * mm, "end": v(-178.9, 79.01) * mm});
            skLineSegment(sketch, "E4488", {"start": v(-178.9, 79.01) * mm, "end": v(-177.98, 79.22) * mm});
            skLineSegment(sketch, "E4489", {"start": v(-177.98, 79.22) * mm, "end": v(-177.17, 79.32) * mm});
            skLineSegment(sketch, "E4490", {"start": v(-177.17, 79.32) * mm, "end": v(-176.44, 79.33) * mm});
            skLineSegment(sketch, "E4491", {"start": v(-176.44, 79.33) * mm, "end": v(-175.79, 79.27) * mm});
            skLineSegment(sketch, "E4492", {"start": v(-175.79, 79.27) * mm, "end": v(-175.19, 79.15) * mm});
            skLineSegment(sketch, "E4493", {"start": v(-175.19, 79.15) * mm, "end": v(-174.63, 79) * mm});
            skLineSegment(sketch, "E4494", {"start": v(-174.63, 79) * mm, "end": v(-174.1, 78.83) * mm});
            skLineSegment(sketch, "E4495", {"start": v(-174.1, 78.83) * mm, "end": v(-173.58, 78.66) * mm});
            skLineSegment(sketch, "E4496", {"start": v(-173.58, 78.66) * mm, "end": v(-171.56, 78.01) * mm});
            skLineSegment(sketch, "E4497", {"start": v(-171.56, 78.01) * mm, "end": v(-169.55, 77.34) * mm});
            skLineSegment(sketch, "E4498", {"start": v(-169.55, 77.34) * mm, "end": v(-167.53, 76.67) * mm});
            skLineSegment(sketch, "E4499", {"start": v(-167.53, 76.67) * mm, "end": v(-165.51, 76.01) * mm});
            skLineSegment(sketch, "E4500", {"start": v(-165.51, 76.01) * mm, "end": v(-163.49, 75.37) * mm});
            skLineSegment(sketch, "E4501", {"start": v(-163.49, 75.37) * mm, "end": v(-161.46, 74.77) * mm});
            skLineSegment(sketch, "E4502", {"start": v(-161.46, 74.77) * mm, "end": v(-159.42, 74.2) * mm});
            skLineSegment(sketch, "E4503", {"start": v(-159.42, 74.2) * mm, "end": v(-157.36, 73.7) * mm});
            skLineSegment(sketch, "E4504", {"start": v(-157.36, 73.7) * mm, "end": v(-156, 73.25) * mm});
            skLineSegment(sketch, "E4505", {"start": v(-156, 73.25) * mm, "end": v(-154.6, 72.64) * mm});
            skLineSegment(sketch, "E4506", {"start": v(-154.6, 72.64) * mm, "end": v(-153.2, 71.99) * mm});
            skLineSegment(sketch, "E4507", {"start": v(-153.2, 71.99) * mm, "end": v(-151.8, 71.42) * mm});
            skLineSegment(sketch, "E4508", {"start": v(-151.8, 71.42) * mm, "end": v(-150.4, 71.09) * mm});
            skLineSegment(sketch, "E4509", {"start": v(-150.4, 71.09) * mm, "end": v(-149.03, 71.11) * mm});
            skLineSegment(sketch, "E4510", {"start": v(-149.03, 71.11) * mm, "end": v(-147.7, 71.62) * mm});
            skLineSegment(sketch, "E4511", {"start": v(-147.7, 71.62) * mm, "end": v(-146.42, 72.76) * mm});
            skLineSegment(sketch, "E4512", {"start": v(-146.42, 72.76) * mm, "end": v(-145.59, 74.14) * mm});
            skLineSegment(sketch, "E4513", {"start": v(-145.59, 74.14) * mm, "end": v(-145.33, 75.49) * mm});
            skLineSegment(sketch, "E4514", {"start": v(-145.33, 75.49) * mm, "end": v(-145.54, 76.8) * mm});
            skLineSegment(sketch, "E4515", {"start": v(-145.54, 76.8) * mm, "end": v(-146.07, 78.08) * mm});
            skLineSegment(sketch, "E4516", {"start": v(-146.07, 78.08) * mm, "end": v(-146.82, 79.35) * mm});
            skLineSegment(sketch, "E4517", {"start": v(-146.82, 79.35) * mm, "end": v(-147.67, 80.6) * mm});
            skLineSegment(sketch, "E4518", {"start": v(-147.67, 80.6) * mm, "end": v(-148.48, 81.82) * mm});
            skLineSegment(sketch, "E4519", {"start": v(-148.48, 81.82) * mm, "end": v(-149.13, 83.05) * mm});
            skLineSegment(sketch, "E4520", {"start": v(-149.13, 83.05) * mm, "end": v(-150.31, 85.64) * mm});
            skLineSegment(sketch, "E4521", {"start": v(-150.31, 85.64) * mm, "end": v(-151.53, 88.22) * mm});
            skLineSegment(sketch, "E4522", {"start": v(-151.53, 88.22) * mm, "end": v(-152.78, 90.79) * mm});
            skLineSegment(sketch, "E4523", {"start": v(-152.78, 90.79) * mm, "end": v(-154.06, 93.34) * mm});
            skLineSegment(sketch, "E4524", {"start": v(-154.06, 93.34) * mm, "end": v(-155.35, 95.89) * mm});
            skLineSegment(sketch, "E4525", {"start": v(-155.35, 95.89) * mm, "end": v(-156.64, 98.43) * mm});
            skLineSegment(sketch, "E4526", {"start": v(-156.64, 98.43) * mm, "end": v(-157.94, 100.98) * mm});
            skLineSegment(sketch, "E4527", {"start": v(-157.94, 100.98) * mm, "end": v(-159.22, 103.53) * mm});
            skLineSegment(sketch, "E4528", {"start": v(-74.41, 160.6) * mm, "end": v(-75.3, 160.9) * mm});
            skLineSegment(sketch, "E4529", {"start": v(-75.3, 160.9) * mm, "end": v(-76.14, 161.15) * mm});
            skLineSegment(sketch, "E4530", {"start": v(-76.14, 161.15) * mm, "end": v(-76.91, 161.4) * mm});
            skLineSegment(sketch, "E4531", {"start": v(-76.91, 161.4) * mm, "end": v(-77.64, 161.62) * mm});
            skLineSegment(sketch, "E4532", {"start": v(-77.64, 161.62) * mm, "end": v(-78.33, 161.84) * mm});
            skLineSegment(sketch, "E4533", {"start": v(-78.33, 161.84) * mm, "end": v(-78.99, 162.05) * mm});
            skLineSegment(sketch, "E4534", {"start": v(-78.99, 162.05) * mm, "end": v(-79.62, 162.26) * mm});
            skLineSegment(sketch, "E4535", {"start": v(-79.62, 162.26) * mm, "end": v(-80.25, 162.48) * mm});
            skLineSegment(sketch, "E4536", {"start": v(-80.25, 162.48) * mm, "end": v(-83.36, 163.58) * mm});
            skLineSegment(sketch, "E4537", {"start": v(-83.36, 163.58) * mm, "end": v(-86.48, 164.69) * mm});
            skLineSegment(sketch, "E4538", {"start": v(-86.48, 164.69) * mm, "end": v(-89.6, 165.8) * mm});
            skLineSegment(sketch, "E4539", {"start": v(-89.6, 165.8) * mm, "end": v(-92.7, 166.9) * mm});
            skLineSegment(sketch, "E4540", {"start": v(-92.7, 166.9) * mm, "end": v(-95.82, 168.02) * mm});
            skLineSegment(sketch, "E4541", {"start": v(-95.82, 168.02) * mm, "end": v(-98.92, 169.14) * mm});
            skLineSegment(sketch, "E4542", {"start": v(-98.92, 169.14) * mm, "end": v(-102.03, 170.28) * mm});
            skLineSegment(sketch, "E4543", {"start": v(-102.03, 170.28) * mm, "end": v(-105.13, 171.42) * mm});
            skLineSegment(sketch, "E4544", {"start": v(-105.13, 171.42) * mm, "end": v(-106.28, 171.76) * mm});
            skLineSegment(sketch, "E4545", {"start": v(-106.28, 171.76) * mm, "end": v(-107.38, 171.9) * mm});
            skLineSegment(sketch, "E4546", {"start": v(-107.38, 171.9) * mm, "end": v(-108.42, 171.85) * mm});
            skLineSegment(sketch, "E4547", {"start": v(-108.42, 171.85) * mm, "end": v(-109.4, 171.63) * mm});
            skLineSegment(sketch, "E4548", {"start": v(-109.4, 171.63) * mm, "end": v(-110.33, 171.26) * mm});
            skLineSegment(sketch, "E4549", {"start": v(-110.33, 171.26) * mm, "end": v(-111.2, 170.76) * mm});
            skLineSegment(sketch, "E4550", {"start": v(-111.2, 170.76) * mm, "end": v(-112.03, 170.13) * mm});
            skLineSegment(sketch, "E4551", {"start": v(-112.03, 170.13) * mm, "end": v(-112.81, 169.4) * mm});
            skLineSegment(sketch, "E4552", {"start": v(-112.81, 169.4) * mm, "end": v(-113.43, 168.57) * mm});
            skLineSegment(sketch, "E4553", {"start": v(-113.43, 168.57) * mm, "end": v(-113.67, 167.79) * mm});
            skLineSegment(sketch, "E4554", {"start": v(-113.67, 167.79) * mm, "end": v(-113.6, 167.05) * mm});
            skLineSegment(sketch, "E4555", {"start": v(-113.6, 167.05) * mm, "end": v(-113.3, 166.35) * mm});
            skLineSegment(sketch, "E4556", {"start": v(-113.3, 166.35) * mm, "end": v(-112.86, 165.68) * mm});
            skLineSegment(sketch, "E4557", {"start": v(-112.86, 165.68) * mm, "end": v(-112.34, 165.03) * mm});
            skLineSegment(sketch, "E4558", {"start": v(-112.34, 165.03) * mm, "end": v(-111.82, 164.4) * mm});
            skLineSegment(sketch, "E4559", {"start": v(-111.82, 164.4) * mm, "end": v(-111.38, 163.8) * mm});
            skLineSegment(sketch, "E4560", {"start": v(-111.38, 163.8) * mm, "end": v(-109.15, 160.26) * mm});
            skLineSegment(sketch, "E4561", {"start": v(-109.15, 160.26) * mm, "end": v(-106.9, 156.74) * mm});
            skLineSegment(sketch, "E4562", {"start": v(-106.9, 156.74) * mm, "end": v(-104.65, 153.22) * mm});
            skLineSegment(sketch, "E4563", {"start": v(-104.65, 153.22) * mm, "end": v(-102.38, 149.7) * mm});
            skLineSegment(sketch, "E4564", {"start": v(-102.38, 149.7) * mm, "end": v(-100.12, 146.2) * mm});
            skLineSegment(sketch, "E4565", {"start": v(-100.12, 146.2) * mm, "end": v(-97.85, 142.68) * mm});
            skLineSegment(sketch, "E4566", {"start": v(-97.85, 142.68) * mm, "end": v(-95.59, 139.17) * mm});
            skLineSegment(sketch, "E4567", {"start": v(-95.59, 139.17) * mm, "end": v(-93.33, 135.65) * mm});
            skLineSegment(sketch, "E4568", {"start": v(-93.33, 135.65) * mm, "end": v(-92.8, 134.87) * mm});
            skLineSegment(sketch, "E4569", {"start": v(-92.8, 134.87) * mm, "end": v(-92.26, 134.19) * mm});
            skLineSegment(sketch, "E4570", {"start": v(-92.26, 134.19) * mm, "end": v(-91.7, 133.64) * mm});
            skLineSegment(sketch, "E4571", {"start": v(-91.7, 133.64) * mm, "end": v(-91.08, 133.25) * mm});
            skLineSegment(sketch, "E4572", {"start": v(-91.08, 133.25) * mm, "end": v(-90.4, 133.05) * mm});
            skLineSegment(sketch, "E4573", {"start": v(-90.4, 133.05) * mm, "end": v(-89.63, 133.07) * mm});
            skLineSegment(sketch, "E4574", {"start": v(-89.63, 133.07) * mm, "end": v(-88.75, 133.34) * mm});
            skLineSegment(sketch, "E4575", {"start": v(-88.75, 133.34) * mm, "end": v(-87.76, 133.89) * mm});
            skLineSegment(sketch, "E4576", {"start": v(-87.76, 133.89) * mm, "end": v(-86.88, 134.54) * mm});
            skLineSegment(sketch, "E4577", {"start": v(-86.88, 134.54) * mm, "end": v(-86.26, 135.2) * mm});
            skLineSegment(sketch, "E4578", {"start": v(-86.26, 135.2) * mm, "end": v(-85.88, 135.88) * mm});
            skLineSegment(sketch, "E4579", {"start": v(-85.88, 135.88) * mm, "end": v(-85.72, 136.57) * mm});
            skLineSegment(sketch, "E4580", {"start": v(-85.72, 136.57) * mm, "end": v(-85.75, 137.29) * mm});
            skLineSegment(sketch, "E4581", {"start": v(-85.75, 137.29) * mm, "end": v(-85.96, 138.04) * mm});
            skLineSegment(sketch, "E4582", {"start": v(-85.96, 138.04) * mm, "end": v(-86.33, 138.83) * mm});
            skLineSegment(sketch, "E4583", {"start": v(-86.33, 138.83) * mm, "end": v(-86.84, 139.68) * mm});
            skLineSegment(sketch, "E4584", {"start": v(-86.84, 139.68) * mm, "end": v(-88.21, 141.76) * mm});
            skLineSegment(sketch, "E4585", {"start": v(-88.21, 141.76) * mm, "end": v(-89.58, 143.85) * mm});
            skLineSegment(sketch, "E4586", {"start": v(-89.58, 143.85) * mm, "end": v(-90.93, 145.94) * mm});
            skLineSegment(sketch, "E4587", {"start": v(-90.93, 145.94) * mm, "end": v(-92.28, 148.04) * mm});
            skLineSegment(sketch, "E4588", {"start": v(-92.28, 148.04) * mm, "end": v(-93.63, 150.14) * mm});
            skLineSegment(sketch, "E4589", {"start": v(-93.63, 150.14) * mm, "end": v(-94.97, 152.25) * mm});
            skLineSegment(sketch, "E4590", {"start": v(-94.97, 152.25) * mm, "end": v(-96.3, 154.36) * mm});
            skLineSegment(sketch, "E4591", {"start": v(-96.3, 154.36) * mm, "end": v(-97.63, 156.47) * mm});
            skLineSegment(sketch, "E4592", {"start": v(-97.63, 156.47) * mm, "end": v(-97.9, 156.85) * mm});
            skLineSegment(sketch, "E4593", {"start": v(-97.9, 156.85) * mm, "end": v(-98.23, 157.25) * mm});
            skLineSegment(sketch, "E4594", {"start": v(-98.23, 157.25) * mm, "end": v(-98.55, 157.65) * mm});
            skLineSegment(sketch, "E4595", {"start": v(-98.55, 157.65) * mm, "end": v(-98.83, 158.06) * mm});
            skLineSegment(sketch, "E4596", {"start": v(-98.83, 158.06) * mm, "end": v(-99.02, 158.5) * mm});
            skLineSegment(sketch, "E4597", {"start": v(-99.02, 158.5) * mm, "end": v(-99.09, 158.94) * mm});
            skLineSegment(sketch, "E4598", {"start": v(-99.09, 158.94) * mm, "end": v(-98.97, 159.41) * mm});
            skLineSegment(sketch, "E4599", {"start": v(-98.97, 159.41) * mm, "end": v(-98.64, 159.9) * mm});
            skLineSegment(sketch, "E4600", {"start": v(-98.64, 159.9) * mm, "end": v(-98.28, 160.2) * mm});
            skLineSegment(sketch, "E4601", {"start": v(-98.28, 160.2) * mm, "end": v(-97.9, 160.32) * mm});
            skLineSegment(sketch, "E4602", {"start": v(-97.9, 160.32) * mm, "end": v(-97.5, 160.32) * mm});
            skLineSegment(sketch, "E4603", {"start": v(-97.5, 160.32) * mm, "end": v(-97.08, 160.22) * mm});
            skLineSegment(sketch, "E4604", {"start": v(-97.08, 160.22) * mm, "end": v(-96.66, 160.06) * mm});
            skLineSegment(sketch, "E4605", {"start": v(-96.66, 160.06) * mm, "end": v(-96.23, 159.87) * mm});
            skLineSegment(sketch, "E4606", {"start": v(-96.23, 159.87) * mm, "end": v(-95.82, 159.68) * mm});
            skLineSegment(sketch, "E4607", {"start": v(-95.82, 159.68) * mm, "end": v(-95.4, 159.52) * mm});
            skLineSegment(sketch, "E4608", {"start": v(-95.4, 159.52) * mm, "end": v(-95.11, 159.42) * mm});
            skLineSegment(sketch, "E4609", {"start": v(-95.11, 159.42) * mm, "end": v(-94.82, 159.33) * mm});
            skLineSegment(sketch, "E4610", {"start": v(-94.82, 159.33) * mm, "end": v(-94.52, 159.23) * mm});
            skLineSegment(sketch, "E4611", {"start": v(-94.52, 159.23) * mm, "end": v(-94.22, 159.13) * mm});
            skLineSegment(sketch, "E4612", {"start": v(-94.22, 159.13) * mm, "end": v(-93.93, 159.03) * mm});
            skLineSegment(sketch, "E4613", {"start": v(-93.93, 159.03) * mm, "end": v(-93.63, 158.93) * mm});
            skLineSegment(sketch, "E4614", {"start": v(-93.63, 158.93) * mm, "end": v(-93.34, 158.83) * mm});
            skLineSegment(sketch, "E4615", {"start": v(-93.34, 158.83) * mm, "end": v(-93.04, 158.73) * mm});
            skLineSegment(sketch, "E4616", {"start": v(-93.04, 158.73) * mm, "end": v(-89.86, 157.63) * mm});
            skLineSegment(sketch, "E4617", {"start": v(-89.86, 157.63) * mm, "end": v(-86.68, 156.53) * mm});
            skLineSegment(sketch, "E4618", {"start": v(-86.68, 156.53) * mm, "end": v(-83.5, 155.44) * mm});
            skLineSegment(sketch, "E4619", {"start": v(-83.5, 155.44) * mm, "end": v(-80.3, 154.34) * mm});
            skLineSegment(sketch, "E4620", {"start": v(-80.3, 154.34) * mm, "end": v(-77.13, 153.24) * mm});
            skLineSegment(sketch, "E4621", {"start": v(-77.13, 153.24) * mm, "end": v(-73.95, 152.13) * mm});
            skLineSegment(sketch, "E4622", {"start": v(-73.95, 152.13) * mm, "end": v(-70.77, 151.01) * mm});
            skLineSegment(sketch, "E4623", {"start": v(-70.77, 151.01) * mm, "end": v(-67.6, 149.89) * mm});
            skLineSegment(sketch, "E4624", {"start": v(-67.6, 149.89) * mm, "end": v(-66.59, 149.6) * mm});
            skLineSegment(sketch, "E4625", {"start": v(-66.59, 149.6) * mm, "end": v(-65.62, 149.45) * mm});
            skLineSegment(sketch, "E4626", {"start": v(-65.62, 149.45) * mm, "end": v(-64.7, 149.45) * mm});
            skLineSegment(sketch, "E4627", {"start": v(-64.7, 149.45) * mm, "end": v(-63.81, 149.59) * mm});
            skLineSegment(sketch, "E4628", {"start": v(-63.81, 149.59) * mm, "end": v(-62.98, 149.86) * mm});
            skLineSegment(sketch, "E4629", {"start": v(-62.98, 149.86) * mm, "end": v(-62.2, 150.27) * mm});
            skLineSegment(sketch, "E4630", {"start": v(-62.2, 150.27) * mm, "end": v(-61.46, 150.82) * mm});
            skLineSegment(sketch, "E4631", {"start": v(-61.46, 150.82) * mm, "end": v(-60.77, 151.49) * mm});
            skLineSegment(sketch, "E4632", {"start": v(-60.77, 151.49) * mm, "end": v(-60.26, 152.25) * mm});
            skLineSegment(sketch, "E4633", {"start": v(-60.26, 152.25) * mm, "end": v(-60.07, 152.96) * mm});
            skLineSegment(sketch, "E4634", {"start": v(-60.07, 152.96) * mm, "end": v(-60.14, 153.64) * mm});
            skLineSegment(sketch, "E4635", {"start": v(-60.14, 153.64) * mm, "end": v(-60.41, 154.3) * mm});
            skLineSegment(sketch, "E4636", {"start": v(-60.41, 154.3) * mm, "end": v(-60.82, 154.92) * mm});
            skLineSegment(sketch, "E4637", {"start": v(-60.82, 154.92) * mm, "end": v(-61.29, 155.52) * mm});
            skLineSegment(sketch, "E4638", {"start": v(-61.29, 155.52) * mm, "end": v(-61.76, 156.11) * mm});
            skLineSegment(sketch, "E4639", {"start": v(-61.76, 156.11) * mm, "end": v(-62.18, 156.7) * mm});
            skLineSegment(sketch, "E4640", {"start": v(-62.18, 156.7) * mm, "end": v(-64.49, 160.32) * mm});
            skLineSegment(sketch, "E4641", {"start": v(-64.49, 160.32) * mm, "end": v(-66.8, 163.95) * mm});
            skLineSegment(sketch, "E4642", {"start": v(-66.8, 163.95) * mm, "end": v(-69.13, 167.57) * mm});
            skLineSegment(sketch, "E4643", {"start": v(-69.13, 167.57) * mm, "end": v(-71.46, 171.2) * mm});
            skLineSegment(sketch, "E4644", {"start": v(-71.46, 171.2) * mm, "end": v(-73.8, 174.81) * mm});
            skLineSegment(sketch, "E4645", {"start": v(-73.8, 174.81) * mm, "end": v(-76.12, 178.43) * mm});
            skLineSegment(sketch, "E4646", {"start": v(-76.12, 178.43) * mm, "end": v(-78.45, 182.05) * mm});
            skLineSegment(sketch, "E4647", {"start": v(-78.45, 182.05) * mm, "end": v(-80.78, 185.67) * mm});
            skLineSegment(sketch, "E4648", {"start": v(-80.78, 185.67) * mm, "end": v(-81.25, 186.36) * mm});
            skLineSegment(sketch, "E4649", {"start": v(-81.25, 186.36) * mm, "end": v(-81.74, 186.93) * mm});
            skLineSegment(sketch, "E4650", {"start": v(-81.74, 186.93) * mm, "end": v(-82.26, 187.37) * mm});
            skLineSegment(sketch, "E4651", {"start": v(-82.26, 187.37) * mm, "end": v(-82.82, 187.66) * mm});
            skLineSegment(sketch, "E4652", {"start": v(-82.82, 187.66) * mm, "end": v(-83.43, 187.8) * mm});
            skLineSegment(sketch, "E4653", {"start": v(-83.43, 187.8) * mm, "end": v(-84.1, 187.75) * mm});
            skLineSegment(sketch, "E4654", {"start": v(-84.1, 187.75) * mm, "end": v(-84.84, 187.52) * mm});
            skLineSegment(sketch, "E4655", {"start": v(-84.84, 187.52) * mm, "end": v(-85.67, 187.09) * mm});
            skLineSegment(sketch, "E4656", {"start": v(-85.67, 187.09) * mm, "end": v(-86.45, 186.55) * mm});
            skLineSegment(sketch, "E4657", {"start": v(-86.45, 186.55) * mm, "end": v(-87.07, 185.99) * mm});
            skLineSegment(sketch, "E4658", {"start": v(-87.07, 185.99) * mm, "end": v(-87.5, 185.4) * mm});
            skLineSegment(sketch, "E4659", {"start": v(-87.5, 185.4) * mm, "end": v(-87.77, 184.78) * mm});
            skLineSegment(sketch, "E4660", {"start": v(-87.77, 184.78) * mm, "end": v(-87.86, 184.11) * mm});
            skLineSegment(sketch, "E4661", {"start": v(-87.86, 184.11) * mm, "end": v(-87.75, 183.4) * mm});
            skLineSegment(sketch, "E4662", {"start": v(-87.75, 183.4) * mm, "end": v(-87.46, 182.63) * mm});
            skLineSegment(sketch, "E4663", {"start": v(-87.46, 182.63) * mm, "end": v(-86.96, 181.79) * mm});
            skLineSegment(sketch, "E4664", {"start": v(-86.96, 181.79) * mm, "end": v(-86.23, 180.7) * mm});
            skLineSegment(sketch, "E4665", {"start": v(-86.23, 180.7) * mm, "end": v(-85.5, 179.61) * mm});
            skLineSegment(sketch, "E4666", {"start": v(-85.5, 179.61) * mm, "end": v(-84.78, 178.52) * mm});
            skLineSegment(sketch, "E4667", {"start": v(-84.78, 178.52) * mm, "end": v(-84.07, 177.42) * mm});
            skLineSegment(sketch, "E4668", {"start": v(-84.07, 177.42) * mm, "end": v(-83.36, 176.32) * mm});
            skLineSegment(sketch, "E4669", {"start": v(-83.36, 176.32) * mm, "end": v(-82.67, 175.2) * mm});
            skLineSegment(sketch, "E4670", {"start": v(-82.67, 175.2) * mm, "end": v(-81.98, 174.1) * mm});
            skLineSegment(sketch, "E4671", {"start": v(-81.98, 174.1) * mm, "end": v(-81.3, 172.97) * mm});
            skLineSegment(sketch, "E4672", {"start": v(-81.3, 172.97) * mm, "end": v(-80.43, 171.58) * mm});
            skLineSegment(sketch, "E4673", {"start": v(-80.43, 171.58) * mm, "end": v(-79.5, 170.2) * mm});
            skLineSegment(sketch, "E4674", {"start": v(-79.5, 170.2) * mm, "end": v(-78.56, 168.8) * mm});
            skLineSegment(sketch, "E4675", {"start": v(-78.56, 168.8) * mm, "end": v(-77.61, 167.37) * mm});
            skLineSegment(sketch, "E4676", {"start": v(-77.61, 167.37) * mm, "end": v(-76.7, 165.86) * mm});
            skLineSegment(sketch, "E4677", {"start": v(-76.7, 165.86) * mm, "end": v(-75.85, 164.25) * mm});
            skLineSegment(sketch, "E4678", {"start": v(-75.85, 164.25) * mm, "end": v(-75.07, 162.5) * mm});
            skLineSegment(sketch, "E4679", {"start": v(-75.07, 162.5) * mm, "end": v(-74.41, 160.6) * mm});
            skLineSegment(sketch, "E4680", {"start": v(23.79, 183.78) * mm, "end": v(23.81, 183.78) * mm});
            skLineSegment(sketch, "E4681", {"start": v(23.81, 183.78) * mm, "end": v(23.84, 183.78) * mm});
            skLineSegment(sketch, "E4682", {"start": v(23.84, 183.78) * mm, "end": v(23.86, 183.78) * mm});
            skLineSegment(sketch, "E4683", {"start": v(23.86, 183.78) * mm, "end": v(23.88, 183.78) * mm});
            skLineSegment(sketch, "E4684", {"start": v(23.88, 183.78) * mm, "end": v(23.9, 183.78) * mm});
            skLineSegment(sketch, "E4685", {"start": v(23.9, 183.78) * mm, "end": v(23.93, 183.78) * mm});
            skLineSegment(sketch, "E4686", {"start": v(23.93, 183.78) * mm, "end": v(23.96, 183.78) * mm});
            skLineSegment(sketch, "E4687", {"start": v(23.96, 183.78) * mm, "end": v(23.98, 183.78) * mm});
            skLineSegment(sketch, "E4688", {"start": v(23.98, 183.78) * mm, "end": v(23.97, 185.96) * mm});
            skLineSegment(sketch, "E4689", {"start": v(23.97, 185.96) * mm, "end": v(23.96, 188.15) * mm});
            skLineSegment(sketch, "E4690", {"start": v(23.96, 188.15) * mm, "end": v(23.95, 190.34) * mm});
            skLineSegment(sketch, "E4691", {"start": v(23.95, 190.34) * mm, "end": v(23.94, 192.52) * mm});
            skLineSegment(sketch, "E4692", {"start": v(23.94, 192.52) * mm, "end": v(23.94, 194.7) * mm});
            skLineSegment(sketch, "E4693", {"start": v(23.94, 194.7) * mm, "end": v(23.95, 196.9) * mm});
            skLineSegment(sketch, "E4694", {"start": v(23.95, 196.9) * mm, "end": v(23.98, 199.08) * mm});
            skLineSegment(sketch, "E4695", {"start": v(23.98, 199.08) * mm, "end": v(24.02, 201.26) * mm});
            skLineSegment(sketch, "E4696", {"start": v(24.02, 201.26) * mm, "end": v(23.97, 202.35) * mm});
            skLineSegment(sketch, "E4697", {"start": v(23.97, 202.35) * mm, "end": v(23.76, 203.22) * mm});
            skLineSegment(sketch, "E4698", {"start": v(23.76, 203.22) * mm, "end": v(23.4, 203.9) * mm});
            skLineSegment(sketch, "E4699", {"start": v(23.4, 203.9) * mm, "end": v(22.9, 204.42) * mm});
            skLineSegment(sketch, "E4700", {"start": v(22.9, 204.42) * mm, "end": v(22.28, 204.8) * mm});
            skLineSegment(sketch, "E4701", {"start": v(22.28, 204.8) * mm, "end": v(21.53, 205.05) * mm});
            skLineSegment(sketch, "E4702", {"start": v(21.53, 205.05) * mm, "end": v(20.67, 205.2) * mm});
            skLineSegment(sketch, "E4703", {"start": v(20.67, 205.2) * mm, "end": v(19.7, 205.3) * mm});
            skLineSegment(sketch, "E4704", {"start": v(19.7, 205.3) * mm, "end": v(18.68, 205.31) * mm});
            skLineSegment(sketch, "E4705", {"start": v(18.68, 205.31) * mm, "end": v(17.78, 205.21) * mm});
            skLineSegment(sketch, "E4706", {"start": v(17.78, 205.21) * mm, "end": v(17.02, 204.99) * mm});
            skLineSegment(sketch, "E4707", {"start": v(17.02, 204.99) * mm, "end": v(16.39, 204.62) * mm});
            skLineSegment(sketch, "E4708", {"start": v(16.39, 204.62) * mm, "end": v(15.9, 204.1) * mm});
            skLineSegment(sketch, "E4709", {"start": v(15.9, 204.1) * mm, "end": v(15.53, 203.41) * mm});
            skLineSegment(sketch, "E4710", {"start": v(15.53, 203.41) * mm, "end": v(15.31, 202.55) * mm});
            skLineSegment(sketch, "E4711", {"start": v(15.31, 202.55) * mm, "end": v(15.23, 201.49) * mm});
            skLineSegment(sketch, "E4712", {"start": v(15.23, 201.49) * mm, "end": v(15.22, 200.37) * mm});
            skLineSegment(sketch, "E4713", {"start": v(15.22, 200.37) * mm, "end": v(15.2, 199.24) * mm});
            skLineSegment(sketch, "E4714", {"start": v(15.2, 199.24) * mm, "end": v(15.17, 198.12) * mm});
            skLineSegment(sketch, "E4715", {"start": v(15.17, 198.12) * mm, "end": v(15.14, 197) * mm});
            skLineSegment(sketch, "E4716", {"start": v(15.14, 197) * mm, "end": v(15.09, 195.87) * mm});
            skLineSegment(sketch, "E4717", {"start": v(15.09, 195.87) * mm, "end": v(15.03, 194.75) * mm});
            skLineSegment(sketch, "E4718", {"start": v(15.03, 194.75) * mm, "end": v(14.97, 193.63) * mm});
            skLineSegment(sketch, "E4719", {"start": v(14.97, 193.63) * mm, "end": v(14.9, 192.5) * mm});
            skLineSegment(sketch, "E4720", {"start": v(14.9, 192.5) * mm, "end": v(14.84, 191.87) * mm});
            skLineSegment(sketch, "E4721", {"start": v(14.84, 191.87) * mm, "end": v(14.74, 191.24) * mm});
            skLineSegment(sketch, "E4722", {"start": v(14.74, 191.24) * mm, "end": v(14.58, 190.64) * mm});
            skLineSegment(sketch, "E4723", {"start": v(14.58, 190.64) * mm, "end": v(14.35, 190.09) * mm});
            skLineSegment(sketch, "E4724", {"start": v(14.35, 190.09) * mm, "end": v(14.02, 189.61) * mm});
            skLineSegment(sketch, "E4725", {"start": v(14.02, 189.61) * mm, "end": v(13.57, 189.24) * mm});
            skLineSegment(sketch, "E4726", {"start": v(13.57, 189.24) * mm, "end": v(13, 188.98) * mm});
            skLineSegment(sketch, "E4727", {"start": v(13, 188.98) * mm, "end": v(12.26, 188.88) * mm});
            skLineSegment(sketch, "E4728", {"start": v(12.26, 188.88) * mm, "end": v(10.38, 188.77) * mm});
            skLineSegment(sketch, "E4729", {"start": v(10.38, 188.77) * mm, "end": v(8.46, 188.6) * mm});
            skLineSegment(sketch, "E4730", {"start": v(8.46, 188.6) * mm, "end": v(6.54, 188.42) * mm});
            skLineSegment(sketch, "E4731", {"start": v(6.54, 188.42) * mm, "end": v(4.63, 188.3) * mm});
            skLineSegment(sketch, "E4732", {"start": v(4.63, 188.3) * mm, "end": v(2.75, 188.3) * mm});
            skLineSegment(sketch, "E4733", {"start": v(2.75, 188.3) * mm, "end": v(0.93, 188.5) * mm});
            skLineSegment(sketch, "E4734", {"start": v(0.93, 188.5) * mm, "end": v(-0.81, 188.94) * mm});
            skLineSegment(sketch, "E4735", {"start": v(-0.81, 188.94) * mm, "end": v(-2.46, 189.7) * mm});
            skLineSegment(sketch, "E4736", {"start": v(-2.46, 189.7) * mm, "end": v(-3.5, 190.6) * mm});
            skLineSegment(sketch, "E4737", {"start": v(-3.5, 190.6) * mm, "end": v(-4.1, 191.72) * mm});
            skLineSegment(sketch, "E4738", {"start": v(-4.1, 191.72) * mm, "end": v(-4.34, 193.03) * mm});
            skLineSegment(sketch, "E4739", {"start": v(-4.34, 193.03) * mm, "end": v(-4.35, 194.47) * mm});
            skLineSegment(sketch, "E4740", {"start": v(-4.35, 194.47) * mm, "end": v(-4.22, 195.98) * mm});
            skLineSegment(sketch, "E4741", {"start": v(-4.22, 195.98) * mm, "end": v(-4.05, 197.52) * mm});
            skLineSegment(sketch, "E4742", {"start": v(-4.05, 197.52) * mm, "end": v(-3.95, 199.04) * mm});
            skLineSegment(sketch, "E4743", {"start": v(-3.95, 199.04) * mm, "end": v(-4.02, 200.47) * mm});
            skLineSegment(sketch, "E4744", {"start": v(-4.02, 200.47) * mm, "end": v(-4.03, 200.53) * mm});
            skLineSegment(sketch, "E4745", {"start": v(-4.03, 200.53) * mm, "end": v(-4.03, 200.6) * mm});
            skLineSegment(sketch, "E4746", {"start": v(-4.03, 200.6) * mm, "end": v(-4.03, 200.66) * mm});
            skLineSegment(sketch, "E4747", {"start": v(-4.03, 200.66) * mm, "end": v(-4.03, 200.72) * mm});
            skLineSegment(sketch, "E4748", {"start": v(-4.03, 200.72) * mm, "end": v(-4.03, 200.78) * mm});
            skLineSegment(sketch, "E4749", {"start": v(-4.03, 200.78) * mm, "end": v(-4.03, 200.85) * mm});
            skLineSegment(sketch, "E4750", {"start": v(-4.03, 200.85) * mm, "end": v(-4.03, 200.9) * mm});
            skLineSegment(sketch, "E4751", {"start": v(-4.03, 200.9) * mm, "end": v(-4.02, 200.97) * mm});
            skLineSegment(sketch, "E4752", {"start": v(-4.02, 200.97) * mm, "end": v(-4.04, 202.03) * mm});
            skLineSegment(sketch, "E4753", {"start": v(-4.04, 202.03) * mm, "end": v(-4.17, 202.96) * mm});
            skLineSegment(sketch, "E4754", {"start": v(-4.17, 202.96) * mm, "end": v(-4.45, 203.77) * mm});
            skLineSegment(sketch, "E4755", {"start": v(-4.45, 203.77) * mm, "end": v(-4.87, 204.45) * mm});
            skLineSegment(sketch, "E4756", {"start": v(-4.87, 204.45) * mm, "end": v(-5.45, 204.98) * mm});
            skLineSegment(sketch, "E4757", {"start": v(-5.45, 204.98) * mm, "end": v(-6.21, 205.38) * mm});
            skLineSegment(sketch, "E4758", {"start": v(-6.21, 205.38) * mm, "end": v(-7.16, 205.62) * mm});
            skLineSegment(sketch, "E4759", {"start": v(-7.16, 205.62) * mm, "end": v(-8.3, 205.7) * mm});
            skLineSegment(sketch, "E4760", {"start": v(-8.3, 205.7) * mm, "end": v(-9.44, 205.64) * mm});
            skLineSegment(sketch, "E4761", {"start": v(-9.44, 205.64) * mm, "end": v(-10.38, 205.42) * mm});
            skLineSegment(sketch, "E4762", {"start": v(-10.38, 205.42) * mm, "end": v(-11.14, 205.05) * mm});
            skLineSegment(sketch, "E4763", {"start": v(-11.14, 205.05) * mm, "end": v(-11.75, 204.54) * mm});
            skLineSegment(sketch, "E4764", {"start": v(-11.75, 204.54) * mm, "end": v(-12.2, 203.88) * mm});
            skLineSegment(sketch, "E4765", {"start": v(-12.2, 203.88) * mm, "end": v(-12.51, 203.09) * mm});
            skLineSegment(sketch, "E4766", {"start": v(-12.51, 203.09) * mm, "end": v(-12.7, 202.16) * mm});
            skLineSegment(sketch, "E4767", {"start": v(-12.7, 202.16) * mm, "end": v(-12.77, 201.1) * mm});
            skLineSegment(sketch, "E4768", {"start": v(-12.77, 201.1) * mm, "end": v(-12.85, 196.85) * mm});
            skLineSegment(sketch, "E4769", {"start": v(-12.85, 196.85) * mm, "end": v(-12.93, 192.6) * mm});
            skLineSegment(sketch, "E4770", {"start": v(-12.93, 192.6) * mm, "end": v(-13.01, 188.36) * mm});
            skLineSegment(sketch, "E4771", {"start": v(-13.01, 188.36) * mm, "end": v(-13.1, 184.12) * mm});
            skLineSegment(sketch, "E4772", {"start": v(-13.1, 184.12) * mm, "end": v(-13.2, 179.88) * mm});
            skLineSegment(sketch, "E4773", {"start": v(-13.2, 179.88) * mm, "end": v(-13.3, 175.63) * mm});
            skLineSegment(sketch, "E4774", {"start": v(-13.3, 175.63) * mm, "end": v(-13.41, 171.39) * mm});
            skLineSegment(sketch, "E4775", {"start": v(-13.41, 171.39) * mm, "end": v(-13.54, 167.15) * mm});
            skLineSegment(sketch, "E4776", {"start": v(-13.54, 167.15) * mm, "end": v(-13.48, 165.71) * mm});
            skLineSegment(sketch, "E4777", {"start": v(-13.48, 165.71) * mm, "end": v(-13.21, 164.56) * mm});
            skLineSegment(sketch, "E4778", {"start": v(-13.21, 164.56) * mm, "end": v(-12.75, 163.68) * mm});
            skLineSegment(sketch, "E4779", {"start": v(-12.75, 163.68) * mm, "end": v(-12.1, 163.03) * mm});
            skLineSegment(sketch, "E4780", {"start": v(-12.1, 163.03) * mm, "end": v(-11.27, 162.6) * mm});
            skLineSegment(sketch, "E4781", {"start": v(-11.27, 162.6) * mm, "end": v(-10.29, 162.35) * mm});
            skLineSegment(sketch, "E4782", {"start": v(-10.29, 162.35) * mm, "end": v(-9.16, 162.27) * mm});
            skLineSegment(sketch, "E4783", {"start": v(-9.16, 162.27) * mm, "end": v(-7.9, 162.33) * mm});
            skLineSegment(sketch, "E4784", {"start": v(-7.9, 162.33) * mm, "end": v(-6.27, 162.66) * mm});
            skLineSegment(sketch, "E4785", {"start": v(-6.27, 162.66) * mm, "end": v(-5.18, 163.26) * mm});
            skLineSegment(sketch, "E4786", {"start": v(-5.18, 163.26) * mm, "end": v(-4.52, 164.09) * mm});
            skLineSegment(sketch, "E4787", {"start": v(-4.52, 164.09) * mm, "end": v(-4.19, 165.08) * mm});
            skLineSegment(sketch, "E4788", {"start": v(-4.19, 165.08) * mm, "end": v(-4.09, 166.18) * mm});
            skLineSegment(sketch, "E4789", {"start": v(-4.09, 166.18) * mm, "end": v(-4.13, 167.34) * mm});
            skLineSegment(sketch, "E4790", {"start": v(-4.13, 167.34) * mm, "end": v(-4.2, 168.5) * mm});
            skLineSegment(sketch, "E4791", {"start": v(-4.2, 168.5) * mm, "end": v(-4.23, 169.6) * mm});
            skLineSegment(sketch, "E4792", {"start": v(-4.23, 169.6) * mm, "end": v(-4.17, 174.27) * mm});
            skLineSegment(sketch, "E4793", {"start": v(-4.17, 174.27) * mm, "end": v(-4.17, 177.64) * mm});
            skLineSegment(sketch, "E4794", {"start": v(-4.17, 177.64) * mm, "end": v(-3.96, 179.92) * mm});
            skLineSegment(sketch, "E4795", {"start": v(-3.96, 179.92) * mm, "end": v(-3.28, 181.32) * mm});
            skLineSegment(sketch, "E4796", {"start": v(-3.28, 181.32) * mm, "end": v(-1.85, 182.05) * mm});
            skLineSegment(sketch, "E4797", {"start": v(-1.85, 182.05) * mm, "end": v(0.59, 182.3) * mm});
            skLineSegment(sketch, "E4798", {"start": v(0.59, 182.3) * mm, "end": v(4.32, 182.3) * mm});
            skLineSegment(sketch, "E4799", {"start": v(4.32, 182.3) * mm, "end": v(9.6, 182.25) * mm});
            skLineSegment(sketch, "E4800", {"start": v(9.6, 182.25) * mm, "end": v(9.72, 182.24) * mm});
            skLineSegment(sketch, "E4801", {"start": v(9.72, 182.24) * mm, "end": v(9.85, 182.24) * mm});
            skLineSegment(sketch, "E4802", {"start": v(9.85, 182.24) * mm, "end": v(9.97, 182.23) * mm});
            skLineSegment(sketch, "E4803", {"start": v(9.97, 182.23) * mm, "end": v(10.1, 182.22) * mm});
            skLineSegment(sketch, "E4804", {"start": v(10.1, 182.22) * mm, "end": v(10.22, 182.21) * mm});
            skLineSegment(sketch, "E4805", {"start": v(10.22, 182.21) * mm, "end": v(10.35, 182.2) * mm});
            skLineSegment(sketch, "E4806", {"start": v(10.35, 182.2) * mm, "end": v(10.47, 182.2) * mm});
            skLineSegment(sketch, "E4807", {"start": v(10.47, 182.2) * mm, "end": v(10.6, 182.2) * mm});
            skLineSegment(sketch, "E4808", {"start": v(10.6, 182.2) * mm, "end": v(11.53, 182.13) * mm});
            skLineSegment(sketch, "E4809", {"start": v(11.53, 182.13) * mm, "end": v(12.34, 181.94) * mm});
            skLineSegment(sketch, "E4810", {"start": v(12.34, 181.94) * mm, "end": v(13.01, 181.62) * mm});
            skLineSegment(sketch, "E4811", {"start": v(13.01, 181.62) * mm, "end": v(13.56, 181.18) * mm});
            skLineSegment(sketch, "E4812", {"start": v(13.56, 181.18) * mm, "end": v(13.98, 180.61) * mm});
            skLineSegment(sketch, "E4813", {"start": v(13.98, 180.61) * mm, "end": v(14.27, 179.92) * mm});
            skLineSegment(sketch, "E4814", {"start": v(14.27, 179.92) * mm, "end": v(14.44, 179.1) * mm});
            skLineSegment(sketch, "E4815", {"start": v(14.44, 179.1) * mm, "end": v(14.5, 178.16) * mm});
            skLineSegment(sketch, "E4816", {"start": v(14.5, 178.16) * mm, "end": v(14.48, 176.79) * mm});
            skLineSegment(sketch, "E4817", {"start": v(14.48, 176.79) * mm, "end": v(14.48, 175.41) * mm});
            skLineSegment(sketch, "E4818", {"start": v(14.48, 175.41) * mm, "end": v(14.5, 174.04) * mm});
            skLineSegment(sketch, "E4819", {"start": v(14.5, 174.04) * mm, "end": v(14.5, 172.67) * mm});
            skLineSegment(sketch, "E4820", {"start": v(14.5, 172.67) * mm, "end": v(14.51, 171.3) * mm});
            skLineSegment(sketch, "E4821", {"start": v(14.51, 171.3) * mm, "end": v(14.51, 169.92) * mm});
            skLineSegment(sketch, "E4822", {"start": v(14.51, 169.92) * mm, "end": v(14.5, 168.55) * mm});
            skLineSegment(sketch, "E4823", {"start": v(14.5, 168.55) * mm, "end": v(14.47, 167.17) * mm});
            skLineSegment(sketch, "E4824", {"start": v(14.47, 167.17) * mm, "end": v(14.5, 166.04) * mm});
            skLineSegment(sketch, "E4825", {"start": v(14.5, 166.04) * mm, "end": v(14.63, 165.05) * mm});
            skLineSegment(sketch, "E4826", {"start": v(14.63, 165.05) * mm, "end": v(14.9, 164.18) * mm});
            skLineSegment(sketch, "E4827", {"start": v(14.9, 164.18) * mm, "end": v(15.34, 163.45) * mm});
            skLineSegment(sketch, "E4828", {"start": v(15.34, 163.45) * mm, "end": v(15.94, 162.87) * mm});
            skLineSegment(sketch, "E4829", {"start": v(15.94, 162.87) * mm, "end": v(16.73, 162.44) * mm});
            skLineSegment(sketch, "E4830", {"start": v(16.73, 162.44) * mm, "end": v(17.72, 162.16) * mm});
            skLineSegment(sketch, "E4831", {"start": v(17.72, 162.16) * mm, "end": v(18.94, 162.05) * mm});
            skLineSegment(sketch, "E4832", {"start": v(18.94, 162.05) * mm, "end": v(20.26, 162.1) * mm});
            skLineSegment(sketch, "E4833", {"start": v(20.26, 162.1) * mm, "end": v(21.33, 162.34) * mm});
            skLineSegment(sketch, "E4834", {"start": v(21.33, 162.34) * mm, "end": v(22.19, 162.76) * mm});
            skLineSegment(sketch, "E4835", {"start": v(22.19, 162.76) * mm, "end": v(22.84, 163.35) * mm});
            skLineSegment(sketch, "E4836", {"start": v(22.84, 163.35) * mm, "end": v(23.3, 164.1) * mm});
            skLineSegment(sketch, "E4837", {"start": v(23.3, 164.1) * mm, "end": v(23.61, 165.02) * mm});
            skLineSegment(sketch, "E4838", {"start": v(23.61, 165.02) * mm, "end": v(23.78, 166.09) * mm});
            skLineSegment(sketch, "E4839", {"start": v(23.78, 166.09) * mm, "end": v(23.81, 167.3) * mm});
            skLineSegment(sketch, "E4840", {"start": v(23.81, 167.3) * mm, "end": v(23.79, 169.35) * mm});
            skLineSegment(sketch, "E4841", {"start": v(23.79, 169.35) * mm, "end": v(23.77, 171.41) * mm});
            skLineSegment(sketch, "E4842", {"start": v(23.77, 171.41) * mm, "end": v(23.77, 173.48) * mm});
            skLineSegment(sketch, "E4843", {"start": v(23.77, 173.48) * mm, "end": v(23.77, 175.54) * mm});
            skLineSegment(sketch, "E4844", {"start": v(23.77, 175.54) * mm, "end": v(23.77, 177.6) * mm});
            skLineSegment(sketch, "E4845", {"start": v(23.77, 177.6) * mm, "end": v(23.78, 179.66) * mm});
            skLineSegment(sketch, "E4846", {"start": v(23.78, 179.66) * mm, "end": v(23.79, 181.72) * mm});
            skLineSegment(sketch, "E4847", {"start": v(23.79, 181.72) * mm, "end": v(23.79, 183.78) * mm});
            skLineSegment(sketch, "E4848", {"start": v(175.2, 72.34) * mm, "end": v(177.33, 72.4) * mm});
            skLineSegment(sketch, "E4849", {"start": v(177.33, 72.4) * mm, "end": v(179.3, 72.69) * mm});
            skLineSegment(sketch, "E4850", {"start": v(179.3, 72.69) * mm, "end": v(181.12, 73.2) * mm});
            skLineSegment(sketch, "E4851", {"start": v(181.12, 73.2) * mm, "end": v(182.8, 73.96) * mm});
            skLineSegment(sketch, "E4852", {"start": v(182.8, 73.96) * mm, "end": v(184.3, 74.94) * mm});
            skLineSegment(sketch, "E4853", {"start": v(184.3, 74.94) * mm, "end": v(185.66, 76.16) * mm});
            skLineSegment(sketch, "E4854", {"start": v(185.66, 76.16) * mm, "end": v(186.85, 77.6) * mm});
            skLineSegment(sketch, "E4855", {"start": v(186.85, 77.6) * mm, "end": v(187.87, 79.29) * mm});
            skLineSegment(sketch, "E4856", {"start": v(187.87, 79.29) * mm, "end": v(188.6, 80.99) * mm});
            skLineSegment(sketch, "E4857", {"start": v(188.6, 80.99) * mm, "end": v(189.05, 82.7) * mm});
            skLineSegment(sketch, "E4858", {"start": v(189.05, 82.7) * mm, "end": v(189.22, 84.4) * mm});
            skLineSegment(sketch, "E4859", {"start": v(189.22, 84.4) * mm, "end": v(189.12, 86.07) * mm});
            skLineSegment(sketch, "E4860", {"start": v(189.12, 86.07) * mm, "end": v(188.77, 87.73) * mm});
            skLineSegment(sketch, "E4861", {"start": v(188.77, 87.73) * mm, "end": v(188.17, 89.34) * mm});
            skLineSegment(sketch, "E4862", {"start": v(188.17, 89.34) * mm, "end": v(187.35, 90.91) * mm});
            skLineSegment(sketch, "E4863", {"start": v(187.35, 90.91) * mm, "end": v(186.3, 92.42) * mm});
            skLineSegment(sketch, "E4864", {"start": v(186.3, 92.42) * mm, "end": v(185.1, 93.93) * mm});
            skLineSegment(sketch, "E4865", {"start": v(185.1, 93.93) * mm, "end": v(183.86, 95.4) * mm});
            skLineSegment(sketch, "E4866", {"start": v(183.86, 95.4) * mm, "end": v(182.6, 96.86) * mm});
            skLineSegment(sketch, "E4867", {"start": v(182.6, 96.86) * mm, "end": v(181.3, 98.3) * mm});
            skLineSegment(sketch, "E4868", {"start": v(181.3, 98.3) * mm, "end": v(180.02, 99.74) * mm});
            skLineSegment(sketch, "E4869", {"start": v(180.02, 99.74) * mm, "end": v(178.72, 101.18) * mm});
            skLineSegment(sketch, "E4870", {"start": v(178.72, 101.18) * mm, "end": v(177.44, 102.63) * mm});
            skLineSegment(sketch, "E4871", {"start": v(177.44, 102.63) * mm, "end": v(176.18, 104.09) * mm});
            skLineSegment(sketch, "E4872", {"start": v(176.18, 104.09) * mm, "end": v(175.56, 104.74) * mm});
            skLineSegment(sketch, "E4873", {"start": v(175.56, 104.74) * mm, "end": v(174.95, 105.2) * mm});
            skLineSegment(sketch, "E4874", {"start": v(174.95, 105.2) * mm, "end": v(174.36, 105.46) * mm});
            skLineSegment(sketch, "E4875", {"start": v(174.36, 105.46) * mm, "end": v(173.77, 105.55) * mm});
            skLineSegment(sketch, "E4876", {"start": v(173.77, 105.55) * mm, "end": v(173.17, 105.46) * mm});
            skLineSegment(sketch, "E4877", {"start": v(173.17, 105.46) * mm, "end": v(172.56, 105.2) * mm});
            skLineSegment(sketch, "E4878", {"start": v(172.56, 105.2) * mm, "end": v(171.91, 104.78) * mm});
            skLineSegment(sketch, "E4879", {"start": v(171.91, 104.78) * mm, "end": v(171.23, 104.2) * mm});
            skLineSegment(sketch, "E4880", {"start": v(171.23, 104.2) * mm, "end": v(168.04, 101.23) * mm});
            skLineSegment(sketch, "E4881", {"start": v(168.04, 101.23) * mm, "end": v(164.84, 98.26) * mm});
            skLineSegment(sketch, "E4882", {"start": v(164.84, 98.26) * mm, "end": v(161.64, 95.3) * mm});
            skLineSegment(sketch, "E4883", {"start": v(161.64, 95.3) * mm, "end": v(158.43, 92.34) * mm});
            skLineSegment(sketch, "E4884", {"start": v(158.43, 92.34) * mm, "end": v(155.2, 89.39) * mm});
            skLineSegment(sketch, "E4885", {"start": v(155.2, 89.39) * mm, "end": v(151.98, 86.45) * mm});
            skLineSegment(sketch, "E4886", {"start": v(151.98, 86.45) * mm, "end": v(148.74, 83.53) * mm});
            skLineSegment(sketch, "E4887", {"start": v(148.74, 83.53) * mm, "end": v(145.48, 80.63) * mm});
            skLineSegment(sketch, "E4888", {"start": v(145.48, 80.63) * mm, "end": v(144.52, 79.67) * mm});
            skLineSegment(sketch, "E4889", {"start": v(144.52, 79.67) * mm, "end": v(143.84, 78.77) * mm});
            skLineSegment(sketch, "E4890", {"start": v(143.84, 78.77) * mm, "end": v(143.43, 77.89) * mm});
            skLineSegment(sketch, "E4891", {"start": v(143.43, 77.89) * mm, "end": v(143.3, 77.02) * mm});
            skLineSegment(sketch, "E4892", {"start": v(143.3, 77.02) * mm, "end": v(143.4, 76.13) * mm});
            skLineSegment(sketch, "E4893", {"start": v(143.4, 76.13) * mm, "end": v(143.76, 75.22) * mm});
            skLineSegment(sketch, "E4894", {"start": v(143.76, 75.22) * mm, "end": v(144.36, 74.25) * mm});
            skLineSegment(sketch, "E4895", {"start": v(144.36, 74.25) * mm, "end": v(145.18, 73.21) * mm});
            skLineSegment(sketch, "E4896", {"start": v(145.18, 73.21) * mm, "end": v(146.16, 72.24) * mm});
            skLineSegment(sketch, "E4897", {"start": v(146.16, 72.24) * mm, "end": v(147.06, 71.67) * mm});
            skLineSegment(sketch, "E4898", {"start": v(147.06, 71.67) * mm, "end": v(147.9, 71.46) * mm});
            skLineSegment(sketch, "E4899", {"start": v(147.9, 71.46) * mm, "end": v(148.7, 71.54) * mm});
            skLineSegment(sketch, "E4900", {"start": v(148.7, 71.54) * mm, "end": v(149.45, 71.86) * mm});
            skLineSegment(sketch, "E4901", {"start": v(149.45, 71.86) * mm, "end": v(150.2, 72.36) * mm});
            skLineSegment(sketch, "E4902", {"start": v(150.2, 72.36) * mm, "end": v(150.93, 72.99) * mm});
            skLineSegment(sketch, "E4903", {"start": v(150.93, 72.99) * mm, "end": v(151.68, 73.68) * mm});
            skLineSegment(sketch, "E4904", {"start": v(151.68, 73.68) * mm, "end": v(152.36, 74.32) * mm});
            skLineSegment(sketch, "E4905", {"start": v(152.36, 74.32) * mm, "end": v(153.04, 74.97) * mm});
            skLineSegment(sketch, "E4906", {"start": v(153.04, 74.97) * mm, "end": v(153.71, 75.61) * mm});
            skLineSegment(sketch, "E4907", {"start": v(153.71, 75.61) * mm, "end": v(154.4, 76.26) * mm});
            skLineSegment(sketch, "E4908", {"start": v(154.4, 76.26) * mm, "end": v(155.07, 76.9) * mm});
            skLineSegment(sketch, "E4909", {"start": v(155.07, 76.9) * mm, "end": v(155.76, 77.53) * mm});
            skLineSegment(sketch, "E4910", {"start": v(155.76, 77.53) * mm, "end": v(156.46, 78.15) * mm});
            skLineSegment(sketch, "E4911", {"start": v(156.46, 78.15) * mm, "end": v(157.18, 78.75) * mm});
            skLineSegment(sketch, "E4912", {"start": v(157.18, 78.75) * mm, "end": v(157.7, 79.23) * mm});
            skLineSegment(sketch, "E4913", {"start": v(157.7, 79.23) * mm, "end": v(158.2, 79.76) * mm});
            skLineSegment(sketch, "E4914", {"start": v(158.2, 79.76) * mm, "end": v(158.73, 80.29) * mm});
            skLineSegment(sketch, "E4915", {"start": v(158.73, 80.29) * mm, "end": v(159.28, 80.74) * mm});
            skLineSegment(sketch, "E4916", {"start": v(159.28, 80.74) * mm, "end": v(159.88, 81.06) * mm});
            skLineSegment(sketch, "E4917", {"start": v(159.88, 81.06) * mm, "end": v(160.54, 81.18) * mm});
            skLineSegment(sketch, "E4918", {"start": v(160.54, 81.18) * mm, "end": v(161.3, 81.03) * mm});
            skLineSegment(sketch, "E4919", {"start": v(161.3, 81.03) * mm, "end": v(162.15, 80.55) * mm});
            skLineSegment(sketch, "E4920", {"start": v(162.15, 80.55) * mm, "end": v(162.86, 79.92) * mm});
            skLineSegment(sketch, "E4921", {"start": v(162.86, 79.92) * mm, "end": v(163.33, 79.25) * mm});
            skLineSegment(sketch, "E4922", {"start": v(163.33, 79.25) * mm, "end": v(163.6, 78.55) * mm});
            skLineSegment(sketch, "E4923", {"start": v(163.6, 78.55) * mm, "end": v(163.69, 77.82) * mm});
            skLineSegment(sketch, "E4924", {"start": v(163.69, 77.82) * mm, "end": v(163.63, 77.07) * mm});
            skLineSegment(sketch, "E4925", {"start": v(163.63, 77.07) * mm, "end": v(163.47, 76.3) * mm});
            skLineSegment(sketch, "E4926", {"start": v(163.47, 76.3) * mm, "end": v(163.22, 75.51) * mm});
            skLineSegment(sketch, "E4927", {"start": v(163.22, 75.51) * mm, "end": v(162.92, 74.72) * mm});
            skLineSegment(sketch, "E4928", {"start": v(162.92, 74.72) * mm, "end": v(162.32, 73.21) * mm});
            skLineSegment(sketch, "E4929", {"start": v(162.32, 73.21) * mm, "end": v(161.72, 71.7) * mm});
            skLineSegment(sketch, "E4930", {"start": v(161.72, 71.7) * mm, "end": v(161.12, 70.2) * mm});
            skLineSegment(sketch, "E4931", {"start": v(161.12, 70.2) * mm, "end": v(160.53, 68.69) * mm});
            skLineSegment(sketch, "E4932", {"start": v(160.53, 68.69) * mm, "end": v(159.95, 67.18) * mm});
            skLineSegment(sketch, "E4933", {"start": v(159.95, 67.18) * mm, "end": v(159.37, 65.66) * mm});
            skLineSegment(sketch, "E4934", {"start": v(159.37, 65.66) * mm, "end": v(158.8, 64.14) * mm});
            skLineSegment(sketch, "E4935", {"start": v(158.8, 64.14) * mm, "end": v(158.25, 62.62) * mm});
            skLineSegment(sketch, "E4936", {"start": v(158.25, 62.62) * mm, "end": v(158.02, 61.46) * mm});
            skLineSegment(sketch, "E4937", {"start": v(158.02, 61.46) * mm, "end": v(158.1, 60.23) * mm});
            skLineSegment(sketch, "E4938", {"start": v(158.1, 60.23) * mm, "end": v(158.43, 58.97) * mm});
            skLineSegment(sketch, "E4939", {"start": v(158.43, 58.97) * mm, "end": v(159, 57.76) * mm});
            skLineSegment(sketch, "E4940", {"start": v(159, 57.76) * mm, "end": v(159.78, 56.66) * mm});
            skLineSegment(sketch, "E4941", {"start": v(159.78, 56.66) * mm, "end": v(160.73, 55.74) * mm});
            skLineSegment(sketch, "E4942", {"start": v(160.73, 55.74) * mm, "end": v(161.8, 55.05) * mm});
            skLineSegment(sketch, "E4943", {"start": v(161.8, 55.05) * mm, "end": v(162.98, 54.66) * mm});
            skLineSegment(sketch, "E4944", {"start": v(162.98, 54.66) * mm, "end": v(164.08, 54.6) * mm});
            skLineSegment(sketch, "E4945", {"start": v(164.08, 54.6) * mm, "end": v(164.85, 54.86) * mm});
            skLineSegment(sketch, "E4946", {"start": v(164.85, 54.86) * mm, "end": v(165.36, 55.35) * mm});
            skLineSegment(sketch, "E4947", {"start": v(165.36, 55.35) * mm, "end": v(165.68, 56.02) * mm});
            skLineSegment(sketch, "E4948", {"start": v(165.68, 56.02) * mm, "end": v(165.86, 56.8) * mm});
            skLineSegment(sketch, "E4949", {"start": v(165.86, 56.8) * mm, "end": v(165.99, 57.6) * mm});
            skLineSegment(sketch, "E4950", {"start": v(165.99, 57.6) * mm, "end": v(166.12, 58.4) * mm});
            skLineSegment(sketch, "E4951", {"start": v(166.12, 58.4) * mm, "end": v(166.33, 59.09) * mm});
            skLineSegment(sketch, "E4952", {"start": v(166.33, 59.09) * mm, "end": v(166.78, 60.18) * mm});
            skLineSegment(sketch, "E4953", {"start": v(166.78, 60.18) * mm, "end": v(167.2, 61.28) * mm});
            skLineSegment(sketch, "E4954", {"start": v(167.2, 61.28) * mm, "end": v(167.58, 62.4) * mm});
            skLineSegment(sketch, "E4955", {"start": v(167.58, 62.4) * mm, "end": v(167.94, 63.53) * mm});
            skLineSegment(sketch, "E4956", {"start": v(167.94, 63.53) * mm, "end": v(168.28, 64.67) * mm});
            skLineSegment(sketch, "E4957", {"start": v(168.28, 64.67) * mm, "end": v(168.61, 65.8) * mm});
            skLineSegment(sketch, "E4958", {"start": v(168.61, 65.8) * mm, "end": v(168.93, 66.95) * mm});
            skLineSegment(sketch, "E4959", {"start": v(168.93, 66.95) * mm, "end": v(169.24, 68.1) * mm});
            skLineSegment(sketch, "E4960", {"start": v(169.24, 68.1) * mm, "end": v(169.6, 69.28) * mm});
            skLineSegment(sketch, "E4961", {"start": v(169.6, 69.28) * mm, "end": v(170.04, 70.34) * mm});
            skLineSegment(sketch, "E4962", {"start": v(170.04, 70.34) * mm, "end": v(170.57, 71.24) * mm});
            skLineSegment(sketch, "E4963", {"start": v(170.57, 71.24) * mm, "end": v(171.2, 71.96) * mm});
            skLineSegment(sketch, "E4964", {"start": v(171.2, 71.96) * mm, "end": v(171.97, 72.45) * mm});
            skLineSegment(sketch, "E4965", {"start": v(171.97, 72.45) * mm, "end": v(172.88, 72.7) * mm});
            skLineSegment(sketch, "E4966", {"start": v(172.88, 72.7) * mm, "end": v(173.95, 72.67) * mm});
            skLineSegment(sketch, "E4967", {"start": v(173.95, 72.67) * mm, "end": v(175.2, 72.34) * mm});
            skLineSegment(sketch, "E4968", {"start": v(-98.11, 127.36) * mm, "end": v(-98.12, 127.8) * mm});
            skLineSegment(sketch, "E4969", {"start": v(-98.12, 127.8) * mm, "end": v(-98.22, 128.18) * mm});
            skLineSegment(sketch, "E4970", {"start": v(-98.22, 128.18) * mm, "end": v(-98.39, 128.5) * mm});
            skLineSegment(sketch, "E4971", {"start": v(-98.39, 128.5) * mm, "end": v(-98.62, 128.75) * mm});
            skLineSegment(sketch, "E4972", {"start": v(-98.62, 128.75) * mm, "end": v(-98.9, 128.97) * mm});
            skLineSegment(sketch, "E4973", {"start": v(-98.9, 128.97) * mm, "end": v(-99.21, 129.15) * mm});
            skLineSegment(sketch, "E4974", {"start": v(-99.21, 129.15) * mm, "end": v(-99.55, 129.3) * mm});
            skLineSegment(sketch, "E4975", {"start": v(-99.55, 129.3) * mm, "end": v(-99.89, 129.45) * mm});
            skLineSegment(sketch, "E4976", {"start": v(-99.89, 129.45) * mm, "end": v(-104.57, 131.32) * mm});
            skLineSegment(sketch, "E4977", {"start": v(-104.57, 131.32) * mm, "end": v(-109.26, 133.2) * mm});
            skLineSegment(sketch, "E4978", {"start": v(-109.26, 133.2) * mm, "end": v(-113.94, 135.06) * mm});
            skLineSegment(sketch, "E4979", {"start": v(-113.94, 135.06) * mm, "end": v(-118.63, 136.93) * mm});
            skLineSegment(sketch, "E4980", {"start": v(-118.63, 136.93) * mm, "end": v(-123.32, 138.79) * mm});
            skLineSegment(sketch, "E4981", {"start": v(-123.32, 138.79) * mm, "end": v(-128.02, 140.63) * mm});
            skLineSegment(sketch, "E4982", {"start": v(-128.02, 140.63) * mm, "end": v(-132.72, 142.45) * mm});
            skLineSegment(sketch, "E4983", {"start": v(-132.72, 142.45) * mm, "end": v(-137.44, 144.24) * mm});
            skLineSegment(sketch, "E4984", {"start": v(-137.44, 144.24) * mm, "end": v(-138.82, 144.5) * mm});
            skLineSegment(sketch, "E4985", {"start": v(-138.82, 144.5) * mm, "end": v(-140.16, 144.33) * mm});
            skLineSegment(sketch, "E4986", {"start": v(-140.16, 144.33) * mm, "end": v(-141.38, 143.78) * mm});
            skLineSegment(sketch, "E4987", {"start": v(-141.38, 143.78) * mm, "end": v(-142.41, 142.92) * mm});
            skLineSegment(sketch, "E4988", {"start": v(-142.41, 142.92) * mm, "end": v(-143.2, 141.83) * mm});
            skLineSegment(sketch, "E4989", {"start": v(-143.2, 141.83) * mm, "end": v(-143.68, 140.58) * mm});
            skLineSegment(sketch, "E4990", {"start": v(-143.68, 140.58) * mm, "end": v(-143.79, 139.23) * mm});
            skLineSegment(sketch, "E4991", {"start": v(-143.79, 139.23) * mm, "end": v(-143.45, 137.87) * mm});
            skLineSegment(sketch, "E4992", {"start": v(-143.45, 137.87) * mm, "end": v(-141.37, 133.07) * mm});
            skLineSegment(sketch, "E4993", {"start": v(-141.37, 133.07) * mm, "end": v(-139.27, 128.27) * mm});
            skLineSegment(sketch, "E4994", {"start": v(-139.27, 128.27) * mm, "end": v(-137.15, 123.49) * mm});
            skLineSegment(sketch, "E4995", {"start": v(-137.15, 123.49) * mm, "end": v(-135.03, 118.7) * mm});
            skLineSegment(sketch, "E4996", {"start": v(-135.03, 118.7) * mm, "end": v(-132.9, 113.93) * mm});
            skLineSegment(sketch, "E4997", {"start": v(-132.9, 113.93) * mm, "end": v(-130.76, 109.15) * mm});
            skLineSegment(sketch, "E4998", {"start": v(-130.76, 109.15) * mm, "end": v(-128.64, 104.37) * mm});
            skLineSegment(sketch, "E4999", {"start": v(-128.64, 104.37) * mm, "end": v(-126.52, 99.59) * mm});
            skLineSegment(sketch, "E5000", {"start": v(-126.52, 99.59) * mm, "end": v(-126.09, 98.74) * mm});
            skLineSegment(sketch, "E5001", {"start": v(-126.09, 98.74) * mm, "end": v(-125.66, 98.18) * mm});
            skLineSegment(sketch, "E5002", {"start": v(-125.66, 98.18) * mm, "end": v(-125.23, 97.86) * mm});
            skLineSegment(sketch, "E5003", {"start": v(-125.23, 97.86) * mm, "end": v(-124.79, 97.77) * mm});
            skLineSegment(sketch, "E5004", {"start": v(-124.79, 97.77) * mm, "end": v(-124.31, 97.88) * mm});
            skLineSegment(sketch, "E5005", {"start": v(-124.31, 97.88) * mm, "end": v(-123.8, 98.17) * mm});
            skLineSegment(sketch, "E5006", {"start": v(-123.8, 98.17) * mm, "end": v(-123.24, 98.61) * mm});
            skLineSegment(sketch, "E5007", {"start": v(-123.24, 98.61) * mm, "end": v(-122.62, 99.19) * mm});
            skLineSegment(sketch, "E5008", {"start": v(-122.62, 99.19) * mm, "end": v(-121.61, 100.36) * mm});
            skLineSegment(sketch, "E5009", {"start": v(-121.61, 100.36) * mm, "end": v(-121, 101.52) * mm});
            skLineSegment(sketch, "E5010", {"start": v(-121, 101.52) * mm, "end": v(-120.74, 102.66) * mm});
            skLineSegment(sketch, "E5011", {"start": v(-120.74, 102.66) * mm, "end": v(-120.76, 103.79) * mm});
            skLineSegment(sketch, "E5012", {"start": v(-120.76, 103.79) * mm, "end": v(-121.03, 104.9) * mm});
            skLineSegment(sketch, "E5013", {"start": v(-121.03, 104.9) * mm, "end": v(-121.48, 105.99) * mm});
            skLineSegment(sketch, "E5014", {"start": v(-121.48, 105.99) * mm, "end": v(-122.06, 107.07) * mm});
            skLineSegment(sketch, "E5015", {"start": v(-122.06, 107.07) * mm, "end": v(-122.72, 108.13) * mm});
            skLineSegment(sketch, "E5016", {"start": v(-122.72, 108.13) * mm, "end": v(-123.57, 109.64) * mm});
            skLineSegment(sketch, "E5017", {"start": v(-123.57, 109.64) * mm, "end": v(-124.13, 111.08) * mm});
            skLineSegment(sketch, "E5018", {"start": v(-124.13, 111.08) * mm, "end": v(-124.39, 112.46) * mm});
            skLineSegment(sketch, "E5019", {"start": v(-124.39, 112.46) * mm, "end": v(-124.36, 113.8) * mm});
            skLineSegment(sketch, "E5020", {"start": v(-124.36, 113.8) * mm, "end": v(-124.04, 115.1) * mm});
            skLineSegment(sketch, "E5021", {"start": v(-124.04, 115.1) * mm, "end": v(-123.44, 116.41) * mm});
            skLineSegment(sketch, "E5022", {"start": v(-123.44, 116.41) * mm, "end": v(-122.56, 117.73) * mm});
            skLineSegment(sketch, "E5023", {"start": v(-122.56, 117.73) * mm, "end": v(-121.4, 119.06) * mm});
            skLineSegment(sketch, "E5024", {"start": v(-121.4, 119.06) * mm, "end": v(-119.45, 121.1) * mm});
            skLineSegment(sketch, "E5025", {"start": v(-119.45, 121.1) * mm, "end": v(-117.9, 122.61) * mm});
            skLineSegment(sketch, "E5026", {"start": v(-117.9, 122.61) * mm, "end": v(-116.56, 123.62) * mm});
            skLineSegment(sketch, "E5027", {"start": v(-116.56, 123.62) * mm, "end": v(-115.26, 124.17) * mm});
            skLineSegment(sketch, "E5028", {"start": v(-115.26, 124.17) * mm, "end": v(-113.82, 124.28) * mm});
            skLineSegment(sketch, "E5029", {"start": v(-113.82, 124.28) * mm, "end": v(-112.07, 123.98) * mm});
            skLineSegment(sketch, "E5030", {"start": v(-112.07, 123.98) * mm, "end": v(-109.82, 123.31) * mm});
            skLineSegment(sketch, "E5031", {"start": v(-109.82, 123.31) * mm, "end": v(-106.9, 122.3) * mm});
            skLineSegment(sketch, "E5032", {"start": v(-106.9, 122.3) * mm, "end": v(-105.7, 122.1) * mm});
            skLineSegment(sketch, "E5033", {"start": v(-105.7, 122.1) * mm, "end": v(-104.31, 122.25) * mm});
            skLineSegment(sketch, "E5034", {"start": v(-104.31, 122.25) * mm, "end": v(-102.87, 122.7) * mm});
            skLineSegment(sketch, "E5035", {"start": v(-102.87, 122.7) * mm, "end": v(-101.47, 123.38) * mm});
            skLineSegment(sketch, "E5036", {"start": v(-101.47, 123.38) * mm, "end": v(-100.2, 124.24) * mm});
            skLineSegment(sketch, "E5037", {"start": v(-100.2, 124.24) * mm, "end": v(-99.14, 125.23) * mm});
            skLineSegment(sketch, "E5038", {"start": v(-99.14, 125.23) * mm, "end": v(-98.42, 126.3) * mm});
            skLineSegment(sketch, "E5039", {"start": v(-98.42, 126.3) * mm, "end": v(-98.11, 127.36) * mm});
            skLineSegment(sketch, "E5040", {"start": v(151.4, 106.1) * mm, "end": v(150.98, 107.09) * mm});
            skLineSegment(sketch, "E5041", {"start": v(150.98, 107.09) * mm, "end": v(150.45, 108.02) * mm});
            skLineSegment(sketch, "E5042", {"start": v(150.45, 108.02) * mm, "end": v(149.83, 108.9) * mm});
            skLineSegment(sketch, "E5043", {"start": v(149.83, 108.9) * mm, "end": v(149.14, 109.75) * mm});
            skLineSegment(sketch, "E5044", {"start": v(149.14, 109.75) * mm, "end": v(148.42, 110.58) * mm});
            skLineSegment(sketch, "E5045", {"start": v(148.42, 110.58) * mm, "end": v(147.68, 111.41) * mm});
            skLineSegment(sketch, "E5046", {"start": v(147.68, 111.41) * mm, "end": v(146.96, 112.25) * mm});
            skLineSegment(sketch, "E5047", {"start": v(146.96, 112.25) * mm, "end": v(146.26, 113.12) * mm});
            skLineSegment(sketch, "E5048", {"start": v(146.26, 113.12) * mm, "end": v(145.85, 113.63) * mm});
            skLineSegment(sketch, "E5049", {"start": v(145.85, 113.63) * mm, "end": v(145.43, 114.13) * mm});
            skLineSegment(sketch, "E5050", {"start": v(145.43, 114.13) * mm, "end": v(145.04, 114.64) * mm});
            skLineSegment(sketch, "E5051", {"start": v(145.04, 114.64) * mm, "end": v(144.73, 115.18) * mm});
            skLineSegment(sketch, "E5052", {"start": v(144.73, 115.18) * mm, "end": v(144.53, 115.75) * mm});
            skLineSegment(sketch, "E5053", {"start": v(144.53, 115.75) * mm, "end": v(144.5, 116.38) * mm});
            skLineSegment(sketch, "E5054", {"start": v(144.5, 116.38) * mm, "end": v(144.66, 117.08) * mm});
            skLineSegment(sketch, "E5055", {"start": v(144.66, 117.08) * mm, "end": v(145.08, 117.86) * mm});
            skLineSegment(sketch, "E5056", {"start": v(145.08, 117.86) * mm, "end": v(146.42, 119.66) * mm});
            skLineSegment(sketch, "E5057", {"start": v(146.42, 119.66) * mm, "end": v(147.75, 120.98) * mm});
            skLineSegment(sketch, "E5058", {"start": v(147.75, 120.98) * mm, "end": v(149.07, 121.83) * mm});
            skLineSegment(sketch, "E5059", {"start": v(149.07, 121.83) * mm, "end": v(150.4, 122.2) * mm});
            skLineSegment(sketch, "E5060", {"start": v(150.4, 122.2) * mm, "end": v(151.76, 122.08) * mm});
            skLineSegment(sketch, "E5061", {"start": v(151.76, 122.08) * mm, "end": v(153.16, 121.48) * mm});
            skLineSegment(sketch, "E5062", {"start": v(153.16, 121.48) * mm, "end": v(154.62, 120.4) * mm});
            skLineSegment(sketch, "E5063", {"start": v(154.62, 120.4) * mm, "end": v(156.15, 118.84) * mm});
            skLineSegment(sketch, "E5064", {"start": v(156.15, 118.84) * mm, "end": v(156.56, 118.37) * mm});
            skLineSegment(sketch, "E5065", {"start": v(156.56, 118.37) * mm, "end": v(156.96, 117.9) * mm});
            skLineSegment(sketch, "E5066", {"start": v(156.96, 117.9) * mm, "end": v(157.37, 117.43) * mm});
            skLineSegment(sketch, "E5067", {"start": v(157.37, 117.43) * mm, "end": v(157.78, 116.96) * mm});
            skLineSegment(sketch, "E5068", {"start": v(157.78, 116.96) * mm, "end": v(158.18, 116.48) * mm});
            skLineSegment(sketch, "E5069", {"start": v(158.18, 116.48) * mm, "end": v(158.57, 116) * mm});
            skLineSegment(sketch, "E5070", {"start": v(158.57, 116) * mm, "end": v(158.96, 115.5) * mm});
            skLineSegment(sketch, "E5071", {"start": v(158.96, 115.5) * mm, "end": v(159.34, 115.01) * mm});
            skLineSegment(sketch, "E5072", {"start": v(159.34, 115.01) * mm, "end": v(159.84, 114.4) * mm});
            skLineSegment(sketch, "E5073", {"start": v(159.84, 114.4) * mm, "end": v(160.35, 113.93) * mm});
            skLineSegment(sketch, "E5074", {"start": v(160.35, 113.93) * mm, "end": v(160.86, 113.6) * mm});
            skLineSegment(sketch, "E5075", {"start": v(160.86, 113.6) * mm, "end": v(161.4, 113.41) * mm});
            skLineSegment(sketch, "E5076", {"start": v(161.4, 113.41) * mm, "end": v(161.95, 113.4) * mm});
            skLineSegment(sketch, "E5077", {"start": v(161.95, 113.4) * mm, "end": v(162.54, 113.56) * mm});
            skLineSegment(sketch, "E5078", {"start": v(162.54, 113.56) * mm, "end": v(163.17, 113.9) * mm});
            skLineSegment(sketch, "E5079", {"start": v(163.17, 113.9) * mm, "end": v(163.83, 114.46) * mm});
            skLineSegment(sketch, "E5080", {"start": v(163.83, 114.46) * mm, "end": v(164.39, 115.04) * mm});
            skLineSegment(sketch, "E5081", {"start": v(164.39, 115.04) * mm, "end": v(164.8, 115.61) * mm});
            skLineSegment(sketch, "E5082", {"start": v(164.8, 115.61) * mm, "end": v(165.05, 116.18) * mm});
            skLineSegment(sketch, "E5083", {"start": v(165.05, 116.18) * mm, "end": v(165.16, 116.75) * mm});
            skLineSegment(sketch, "E5084", {"start": v(165.16, 116.75) * mm, "end": v(165.12, 117.32) * mm});
            skLineSegment(sketch, "E5085", {"start": v(165.12, 117.32) * mm, "end": v(164.93, 117.9) * mm});
            skLineSegment(sketch, "E5086", {"start": v(164.93, 117.9) * mm, "end": v(164.6, 118.52) * mm});
            skLineSegment(sketch, "E5087", {"start": v(164.6, 118.52) * mm, "end": v(164.1, 119.15) * mm});
            skLineSegment(sketch, "E5088", {"start": v(164.1, 119.15) * mm, "end": v(162.72, 120.76) * mm});
            skLineSegment(sketch, "E5089", {"start": v(162.72, 120.76) * mm, "end": v(161.33, 122.36) * mm});
            skLineSegment(sketch, "E5090", {"start": v(161.33, 122.36) * mm, "end": v(159.95, 123.98) * mm});
            skLineSegment(sketch, "E5091", {"start": v(159.95, 123.98) * mm, "end": v(158.58, 125.6) * mm});
            skLineSegment(sketch, "E5092", {"start": v(158.58, 125.6) * mm, "end": v(157.21, 127.21) * mm});
            skLineSegment(sketch, "E5093", {"start": v(157.21, 127.21) * mm, "end": v(155.85, 128.84) * mm});
            skLineSegment(sketch, "E5094", {"start": v(155.85, 128.84) * mm, "end": v(154.5, 130.47) * mm});
            skLineSegment(sketch, "E5095", {"start": v(154.5, 130.47) * mm, "end": v(153.16, 132.1) * mm});
            skLineSegment(sketch, "E5096", {"start": v(153.16, 132.1) * mm, "end": v(152.48, 132.83) * mm});
            skLineSegment(sketch, "E5097", {"start": v(152.48, 132.83) * mm, "end": v(151.82, 133.33) * mm});
            skLineSegment(sketch, "E5098", {"start": v(151.82, 133.33) * mm, "end": v(151.16, 133.63) * mm});
            skLineSegment(sketch, "E5099", {"start": v(151.16, 133.63) * mm, "end": v(150.5, 133.74) * mm});
            skLineSegment(sketch, "E5100", {"start": v(150.5, 133.74) * mm, "end": v(149.82, 133.66) * mm});
            skLineSegment(sketch, "E5101", {"start": v(149.82, 133.66) * mm, "end": v(149.13, 133.4) * mm});
            skLineSegment(sketch, "E5102", {"start": v(149.13, 133.4) * mm, "end": v(148.42, 132.99) * mm});
            skLineSegment(sketch, "E5103", {"start": v(148.42, 132.99) * mm, "end": v(147.68, 132.42) * mm});
            skLineSegment(sketch, "E5104", {"start": v(147.68, 132.42) * mm, "end": v(144.26, 129.51) * mm});
            skLineSegment(sketch, "E5105", {"start": v(144.26, 129.51) * mm, "end": v(140.84, 126.6) * mm});
            skLineSegment(sketch, "E5106", {"start": v(140.84, 126.6) * mm, "end": v(137.42, 123.7) * mm});
            skLineSegment(sketch, "E5107", {"start": v(137.42, 123.7) * mm, "end": v(134, 120.8) * mm});
            skLineSegment(sketch, "E5108", {"start": v(134, 120.8) * mm, "end": v(130.56, 117.9) * mm});
            skLineSegment(sketch, "E5109", {"start": v(130.56, 117.9) * mm, "end": v(127.13, 115.01) * mm});
            skLineSegment(sketch, "E5110", {"start": v(127.13, 115.01) * mm, "end": v(123.7, 112.12) * mm});
            skLineSegment(sketch, "E5111", {"start": v(123.7, 112.12) * mm, "end": v(120.27, 109.23) * mm});
            skLineSegment(sketch, "E5112", {"start": v(120.27, 109.23) * mm, "end": v(119.65, 108.67) * mm});
            skLineSegment(sketch, "E5113", {"start": v(119.65, 108.67) * mm, "end": v(119.15, 108.11) * mm});
            skLineSegment(sketch, "E5114", {"start": v(119.15, 108.11) * mm, "end": v(118.78, 107.55) * mm});
            skLineSegment(sketch, "E5115", {"start": v(118.78, 107.55) * mm, "end": v(118.57, 106.96) * mm});
            skLineSegment(sketch, "E5116", {"start": v(118.57, 106.96) * mm, "end": v(118.52, 106.35) * mm});
            skLineSegment(sketch, "E5117", {"start": v(118.52, 106.35) * mm, "end": v(118.67, 105.7) * mm});
            skLineSegment(sketch, "E5118", {"start": v(118.67, 105.7) * mm, "end": v(119.02, 105.01) * mm});
            skLineSegment(sketch, "E5119", {"start": v(119.02, 105.01) * mm, "end": v(119.59, 104.26) * mm});
            skLineSegment(sketch, "E5120", {"start": v(119.59, 104.26) * mm, "end": v(121.18, 102.43) * mm});
            skLineSegment(sketch, "E5121", {"start": v(121.18, 102.43) * mm, "end": v(122.77, 100.59) * mm});
            skLineSegment(sketch, "E5122", {"start": v(122.77, 100.59) * mm, "end": v(124.35, 98.74) * mm});
            skLineSegment(sketch, "E5123", {"start": v(124.35, 98.74) * mm, "end": v(125.92, 96.88) * mm});
            skLineSegment(sketch, "E5124", {"start": v(125.92, 96.88) * mm, "end": v(127.48, 95.02) * mm});
            skLineSegment(sketch, "E5125", {"start": v(127.48, 95.02) * mm, "end": v(129.04, 93.15) * mm});
            skLineSegment(sketch, "E5126", {"start": v(129.04, 93.15) * mm, "end": v(130.6, 91.28) * mm});
            skLineSegment(sketch, "E5127", {"start": v(130.6, 91.28) * mm, "end": v(132.15, 89.4) * mm});
            skLineSegment(sketch, "E5128", {"start": v(132.15, 89.4) * mm, "end": v(132.72, 88.8) * mm});
            skLineSegment(sketch, "E5129", {"start": v(132.72, 88.8) * mm, "end": v(133.29, 88.38) * mm});
            skLineSegment(sketch, "E5130", {"start": v(133.29, 88.38) * mm, "end": v(133.85, 88.14) * mm});
            skLineSegment(sketch, "E5131", {"start": v(133.85, 88.14) * mm, "end": v(134.41, 88.06) * mm});
            skLineSegment(sketch, "E5132", {"start": v(134.41, 88.06) * mm, "end": v(134.98, 88.13) * mm});
            skLineSegment(sketch, "E5133", {"start": v(134.98, 88.13) * mm, "end": v(135.57, 88.35) * mm});
            skLineSegment(sketch, "E5134", {"start": v(135.57, 88.35) * mm, "end": v(136.17, 88.7) * mm});
            skLineSegment(sketch, "E5135", {"start": v(136.17, 88.7) * mm, "end": v(136.8, 89.18) * mm});
            skLineSegment(sketch, "E5136", {"start": v(136.8, 89.18) * mm, "end": v(137.35, 89.7) * mm});
            skLineSegment(sketch, "E5137", {"start": v(137.35, 89.7) * mm, "end": v(137.73, 90.22) * mm});
            skLineSegment(sketch, "E5138", {"start": v(137.73, 90.22) * mm, "end": v(137.96, 90.73) * mm});
            skLineSegment(sketch, "E5139", {"start": v(137.96, 90.73) * mm, "end": v(138.03, 91.24) * mm});
            skLineSegment(sketch, "E5140", {"start": v(138.03, 91.24) * mm, "end": v(137.96, 91.75) * mm});
            skLineSegment(sketch, "E5141", {"start": v(137.96, 91.75) * mm, "end": v(137.76, 92.28) * mm});
            skLineSegment(sketch, "E5142", {"start": v(137.76, 92.28) * mm, "end": v(137.43, 92.82) * mm});
            skLineSegment(sketch, "E5143", {"start": v(137.43, 92.82) * mm, "end": v(136.98, 93.38) * mm});
            skLineSegment(sketch, "E5144", {"start": v(136.98, 93.38) * mm, "end": v(136.17, 94.32) * mm});
            skLineSegment(sketch, "E5145", {"start": v(136.17, 94.32) * mm, "end": v(135.35, 95.27) * mm});
            skLineSegment(sketch, "E5146", {"start": v(135.35, 95.27) * mm, "end": v(134.55, 96.22) * mm});
            skLineSegment(sketch, "E5147", {"start": v(134.55, 96.22) * mm, "end": v(133.74, 97.17) * mm});
            skLineSegment(sketch, "E5148", {"start": v(133.74, 97.17) * mm, "end": v(132.94, 98.13) * mm});
            skLineSegment(sketch, "E5149", {"start": v(132.94, 98.13) * mm, "end": v(132.15, 99.09) * mm});
            skLineSegment(sketch, "E5150", {"start": v(132.15, 99.09) * mm, "end": v(131.35, 100.05) * mm});
            skLineSegment(sketch, "E5151", {"start": v(131.35, 100.05) * mm, "end": v(130.56, 101.01) * mm});
            skLineSegment(sketch, "E5152", {"start": v(130.56, 101.01) * mm, "end": v(130.17, 101.51) * mm});
            skLineSegment(sketch, "E5153", {"start": v(130.17, 101.51) * mm, "end": v(129.84, 102) * mm});
            skLineSegment(sketch, "E5154", {"start": v(129.84, 102) * mm, "end": v(129.58, 102.5) * mm});
            skLineSegment(sketch, "E5155", {"start": v(129.58, 102.5) * mm, "end": v(129.42, 103.02) * mm});
            skLineSegment(sketch, "E5156", {"start": v(129.42, 103.02) * mm, "end": v(129.38, 103.56) * mm});
            skLineSegment(sketch, "E5157", {"start": v(129.38, 103.56) * mm, "end": v(129.47, 104.13) * mm});
            skLineSegment(sketch, "E5158", {"start": v(129.47, 104.13) * mm, "end": v(129.72, 104.74) * mm});
            skLineSegment(sketch, "E5159", {"start": v(129.72, 104.74) * mm, "end": v(130.16, 105.39) * mm});
            skLineSegment(sketch, "E5160", {"start": v(130.16, 105.39) * mm, "end": v(132.09, 107.7) * mm});
            skLineSegment(sketch, "E5161", {"start": v(132.09, 107.7) * mm, "end": v(133.83, 109.36) * mm});
            skLineSegment(sketch, "E5162", {"start": v(133.83, 109.36) * mm, "end": v(135.45, 110.39) * mm});
            skLineSegment(sketch, "E5163", {"start": v(135.45, 110.39) * mm, "end": v(137.02, 110.78) * mm});
            skLineSegment(sketch, "E5164", {"start": v(137.02, 110.78) * mm, "end": v(138.6, 110.53) * mm});
            skLineSegment(sketch, "E5165", {"start": v(138.6, 110.53) * mm, "end": v(140.26, 109.65) * mm});
            skLineSegment(sketch, "E5166", {"start": v(140.26, 109.65) * mm, "end": v(142.07, 108.14) * mm});
            skLineSegment(sketch, "E5167", {"start": v(142.07, 108.14) * mm, "end": v(144.08, 106) * mm});
            skLineSegment(sketch, "E5168", {"start": v(144.08, 106) * mm, "end": v(144.33, 105.71) * mm});
            skLineSegment(sketch, "E5169", {"start": v(144.33, 105.71) * mm, "end": v(144.57, 105.43) * mm});
            skLineSegment(sketch, "E5170", {"start": v(144.57, 105.43) * mm, "end": v(144.82, 105.15) * mm});
            skLineSegment(sketch, "E5171", {"start": v(144.82, 105.15) * mm, "end": v(145.07, 104.87) * mm});
            skLineSegment(sketch, "E5172", {"start": v(145.07, 104.87) * mm, "end": v(145.31, 104.59) * mm});
            skLineSegment(sketch, "E5173", {"start": v(145.31, 104.59) * mm, "end": v(145.56, 104.3) * mm});
            skLineSegment(sketch, "E5174", {"start": v(145.56, 104.3) * mm, "end": v(145.8, 104.03) * mm});
            skLineSegment(sketch, "E5175", {"start": v(145.8, 104.03) * mm, "end": v(146.06, 103.75) * mm});
            skLineSegment(sketch, "E5176", {"start": v(146.06, 103.75) * mm, "end": v(146.36, 103.42) * mm});
            skLineSegment(sketch, "E5177", {"start": v(146.36, 103.42) * mm, "end": v(146.67, 103.1) * mm});
            skLineSegment(sketch, "E5178", {"start": v(146.67, 103.1) * mm, "end": v(147, 102.83) * mm});
            skLineSegment(sketch, "E5179", {"start": v(147, 102.83) * mm, "end": v(147.33, 102.62) * mm});
            skLineSegment(sketch, "E5180", {"start": v(147.33, 102.62) * mm, "end": v(147.7, 102.49) * mm});
            skLineSegment(sketch, "E5181", {"start": v(147.7, 102.49) * mm, "end": v(148.1, 102.47) * mm});
            skLineSegment(sketch, "E5182", {"start": v(148.1, 102.47) * mm, "end": v(148.53, 102.57) * mm});
            skLineSegment(sketch, "E5183", {"start": v(148.53, 102.57) * mm, "end": v(149, 102.83) * mm});
            skLineSegment(sketch, "E5184", {"start": v(149, 102.83) * mm, "end": v(149.4, 103.12) * mm});
            skLineSegment(sketch, "E5185", {"start": v(149.4, 103.12) * mm, "end": v(149.8, 103.42) * mm});
            skLineSegment(sketch, "E5186", {"start": v(149.8, 103.42) * mm, "end": v(150.18, 103.75) * mm});
            skLineSegment(sketch, "E5187", {"start": v(150.18, 103.75) * mm, "end": v(150.52, 104.1) * mm});
            skLineSegment(sketch, "E5188", {"start": v(150.52, 104.1) * mm, "end": v(150.83, 104.51) * mm});
            skLineSegment(sketch, "E5189", {"start": v(150.83, 104.51) * mm, "end": v(151.08, 104.97) * mm});
            skLineSegment(sketch, "E5190", {"start": v(151.08, 104.97) * mm, "end": v(151.28, 105.5) * mm});
            skLineSegment(sketch, "E5191", {"start": v(151.28, 105.5) * mm, "end": v(151.4, 106.1) * mm});
            skLineSegment(sketch, "E5192", {"start": v(65.25, 189.15) * mm, "end": v(65.99, 189) * mm});
            skLineSegment(sketch, "E5193", {"start": v(65.99, 189) * mm, "end": v(66.63, 189) * mm});
            skLineSegment(sketch, "E5194", {"start": v(66.63, 189) * mm, "end": v(67.18, 189.12) * mm});
            skLineSegment(sketch, "E5195", {"start": v(67.18, 189.12) * mm, "end": v(67.66, 189.37) * mm});
            skLineSegment(sketch, "E5196", {"start": v(67.66, 189.37) * mm, "end": v(68.07, 189.73) * mm});
            skLineSegment(sketch, "E5197", {"start": v(68.07, 189.73) * mm, "end": v(68.41, 190.2) * mm});
            skLineSegment(sketch, "E5198", {"start": v(68.41, 190.2) * mm, "end": v(68.7, 190.78) * mm});
            skLineSegment(sketch, "E5199", {"start": v(68.7, 190.78) * mm, "end": v(68.96, 191.45) * mm});
            skLineSegment(sketch, "E5200", {"start": v(68.96, 191.45) * mm, "end": v(69.14, 192.19) * mm});
            skLineSegment(sketch, "E5201", {"start": v(69.14, 192.19) * mm, "end": v(69.18, 192.83) * mm});
            skLineSegment(sketch, "E5202", {"start": v(69.18, 192.83) * mm, "end": v(69.08, 193.39) * mm});
            skLineSegment(sketch, "E5203", {"start": v(69.08, 193.39) * mm, "end": v(68.85, 193.86) * mm});
            skLineSegment(sketch, "E5204", {"start": v(68.85, 193.86) * mm, "end": v(68.5, 194.27) * mm});
            skLineSegment(sketch, "E5205", {"start": v(68.5, 194.27) * mm, "end": v(68.05, 194.6) * mm});
            skLineSegment(sketch, "E5206", {"start": v(68.05, 194.6) * mm, "end": v(67.49, 194.9) * mm});
            skLineSegment(sketch, "E5207", {"start": v(67.49, 194.9) * mm, "end": v(66.83, 195.15) * mm});
            skLineSegment(sketch, "E5208", {"start": v(66.83, 195.15) * mm, "end": v(64.76, 195.83) * mm});
            skLineSegment(sketch, "E5209", {"start": v(64.76, 195.83) * mm, "end": v(62.68, 196.51) * mm});
            skLineSegment(sketch, "E5210", {"start": v(62.68, 196.51) * mm, "end": v(60.6, 197.2) * mm});
            skLineSegment(sketch, "E5211", {"start": v(60.6, 197.2) * mm, "end": v(58.54, 197.89) * mm});
            skLineSegment(sketch, "E5212", {"start": v(58.54, 197.89) * mm, "end": v(56.46, 198.58) * mm});
            skLineSegment(sketch, "E5213", {"start": v(56.46, 198.58) * mm, "end": v(54.4, 199.27) * mm});
            skLineSegment(sketch, "E5214", {"start": v(54.4, 199.27) * mm, "end": v(52.32, 199.96) * mm});
            skLineSegment(sketch, "E5215", {"start": v(52.32, 199.96) * mm, "end": v(50.25, 200.65) * mm});
            skLineSegment(sketch, "E5216", {"start": v(50.25, 200.65) * mm, "end": v(49.48, 200.85) * mm});
            skLineSegment(sketch, "E5217", {"start": v(49.48, 200.85) * mm, "end": v(48.8, 200.92) * mm});
            skLineSegment(sketch, "E5218", {"start": v(48.8, 200.92) * mm, "end": v(48.17, 200.86) * mm});
            skLineSegment(sketch, "E5219", {"start": v(48.17, 200.86) * mm, "end": v(47.62, 200.67) * mm});
            skLineSegment(sketch, "E5220", {"start": v(47.62, 200.67) * mm, "end": v(47.13, 200.34) * mm});
            skLineSegment(sketch, "E5221", {"start": v(47.13, 200.34) * mm, "end": v(46.71, 199.88) * mm});
            skLineSegment(sketch, "E5222", {"start": v(46.71, 199.88) * mm, "end": v(46.35, 199.27) * mm});
            skLineSegment(sketch, "E5223", {"start": v(46.35, 199.27) * mm, "end": v(46.05, 198.5) * mm});
            skLineSegment(sketch, "E5224", {"start": v(46.05, 198.5) * mm, "end": v(44.6, 194.12) * mm});
            skLineSegment(sketch, "E5225", {"start": v(44.6, 194.12) * mm, "end": v(43.15, 189.74) * mm});
            skLineSegment(sketch, "E5226", {"start": v(43.15, 189.74) * mm, "end": v(41.7, 185.36) * mm});
            skLineSegment(sketch, "E5227", {"start": v(41.7, 185.36) * mm, "end": v(40.23, 180.97) * mm});
            skLineSegment(sketch, "E5228", {"start": v(40.23, 180.97) * mm, "end": v(38.77, 176.6) * mm});
            skLineSegment(sketch, "E5229", {"start": v(38.77, 176.6) * mm, "end": v(37.31, 172.2) * mm});
            skLineSegment(sketch, "E5230", {"start": v(37.31, 172.2) * mm, "end": v(35.85, 167.83) * mm});
            skLineSegment(sketch, "E5231", {"start": v(35.85, 167.83) * mm, "end": v(34.39, 163.45) * mm});
            skLineSegment(sketch, "E5232", {"start": v(34.39, 163.45) * mm, "end": v(34.2, 162.76) * mm});
            skLineSegment(sketch, "E5233", {"start": v(34.2, 162.76) * mm, "end": v(34.13, 162.12) * mm});
            skLineSegment(sketch, "E5234", {"start": v(34.13, 162.12) * mm, "end": v(34.17, 161.53) * mm});
            skLineSegment(sketch, "E5235", {"start": v(34.17, 161.53) * mm, "end": v(34.33, 161) * mm});
            skLineSegment(sketch, "E5236", {"start": v(34.33, 161) * mm, "end": v(34.6, 160.54) * mm});
            skLineSegment(sketch, "E5237", {"start": v(34.6, 160.54) * mm, "end": v(35, 160.13) * mm});
            skLineSegment(sketch, "E5238", {"start": v(35, 160.13) * mm, "end": v(35.55, 159.79) * mm});
            skLineSegment(sketch, "E5239", {"start": v(35.55, 159.79) * mm, "end": v(36.22, 159.5) * mm});
            skLineSegment(sketch, "E5240", {"start": v(36.22, 159.5) * mm, "end": v(38.58, 158.72) * mm});
            skLineSegment(sketch, "E5241", {"start": v(38.58, 158.72) * mm, "end": v(40.95, 157.93) * mm});
            skLineSegment(sketch, "E5242", {"start": v(40.95, 157.93) * mm, "end": v(43.32, 157.15) * mm});
            skLineSegment(sketch, "E5243", {"start": v(43.32, 157.15) * mm, "end": v(45.7, 156.36) * mm});
            skLineSegment(sketch, "E5244", {"start": v(45.7, 156.36) * mm, "end": v(48.06, 155.58) * mm});
            skLineSegment(sketch, "E5245", {"start": v(48.06, 155.58) * mm, "end": v(50.43, 154.8) * mm});
            skLineSegment(sketch, "E5246", {"start": v(50.43, 154.8) * mm, "end": v(52.8, 154.02) * mm});
            skLineSegment(sketch, "E5247", {"start": v(52.8, 154.02) * mm, "end": v(55.18, 153.24) * mm});
            skLineSegment(sketch, "E5248", {"start": v(55.18, 153.24) * mm, "end": v(55.88, 153.07) * mm});
            skLineSegment(sketch, "E5249", {"start": v(55.88, 153.07) * mm, "end": v(56.5, 153.03) * mm});
            skLineSegment(sketch, "E5250", {"start": v(56.5, 153.03) * mm, "end": v(57.06, 153.12) * mm});
            skLineSegment(sketch, "E5251", {"start": v(57.06, 153.12) * mm, "end": v(57.56, 153.33) * mm});
            skLineSegment(sketch, "E5252", {"start": v(57.56, 153.33) * mm, "end": v(57.98, 153.67) * mm});
            skLineSegment(sketch, "E5253", {"start": v(57.98, 153.67) * mm, "end": v(58.35, 154.12) * mm});
            skLineSegment(sketch, "E5254", {"start": v(58.35, 154.12) * mm, "end": v(58.67, 154.7) * mm});
            skLineSegment(sketch, "E5255", {"start": v(58.67, 154.7) * mm, "end": v(58.93, 155.37) * mm});
            skLineSegment(sketch, "E5256", {"start": v(58.93, 155.37) * mm, "end": v(59.1, 156.1) * mm});
            skLineSegment(sketch, "E5257", {"start": v(59.1, 156.1) * mm, "end": v(59.16, 156.74) * mm});
            skLineSegment(sketch, "E5258", {"start": v(59.16, 156.74) * mm, "end": v(59.09, 157.3) * mm});
            skLineSegment(sketch, "E5259", {"start": v(59.09, 157.3) * mm, "end": v(58.9, 157.8) * mm});
            skLineSegment(sketch, "E5260", {"start": v(58.9, 157.8) * mm, "end": v(58.57, 158.21) * mm});
            skLineSegment(sketch, "E5261", {"start": v(58.57, 158.21) * mm, "end": v(58.14, 158.57) * mm});
            skLineSegment(sketch, "E5262", {"start": v(58.14, 158.57) * mm, "end": v(57.58, 158.88) * mm});
            skLineSegment(sketch, "E5263", {"start": v(57.58, 158.88) * mm, "end": v(56.92, 159.14) * mm});
            skLineSegment(sketch, "E5264", {"start": v(56.92, 159.14) * mm, "end": v(55.73, 159.53) * mm});
            skLineSegment(sketch, "E5265", {"start": v(55.73, 159.53) * mm, "end": v(54.55, 159.93) * mm});
            skLineSegment(sketch, "E5266", {"start": v(54.55, 159.93) * mm, "end": v(53.37, 160.33) * mm});
            skLineSegment(sketch, "E5267", {"start": v(53.37, 160.33) * mm, "end": v(52.19, 160.74) * mm});
            skLineSegment(sketch, "E5268", {"start": v(52.19, 160.74) * mm, "end": v(51, 161.14) * mm});
            skLineSegment(sketch, "E5269", {"start": v(51, 161.14) * mm, "end": v(49.83, 161.55) * mm});
            skLineSegment(sketch, "E5270", {"start": v(49.83, 161.55) * mm, "end": v(48.65, 161.95) * mm});
            skLineSegment(sketch, "E5271", {"start": v(48.65, 161.95) * mm, "end": v(47.46, 162.35) * mm});
            skLineSegment(sketch, "E5272", {"start": v(47.46, 162.35) * mm, "end": v(46.85, 162.59) * mm});
            skLineSegment(sketch, "E5273", {"start": v(46.85, 162.59) * mm, "end": v(46.3, 162.86) * mm});
            skLineSegment(sketch, "E5274", {"start": v(46.3, 162.86) * mm, "end": v(45.83, 163.18) * mm});
            skLineSegment(sketch, "E5275", {"start": v(45.83, 163.18) * mm, "end": v(45.45, 163.56) * mm});
            skLineSegment(sketch, "E5276", {"start": v(45.45, 163.56) * mm, "end": v(45.15, 164.02) * mm});
            skLineSegment(sketch, "E5277", {"start": v(45.15, 164.02) * mm, "end": v(44.96, 164.56) * mm});
            skLineSegment(sketch, "E5278", {"start": v(44.96, 164.56) * mm, "end": v(44.87, 165.2) * mm});
            skLineSegment(sketch, "E5279", {"start": v(44.87, 165.2) * mm, "end": v(44.9, 165.96) * mm});
            skLineSegment(sketch, "E5280", {"start": v(44.9, 165.96) * mm, "end": v(45.3, 168.8) * mm});
            skLineSegment(sketch, "E5281", {"start": v(45.3, 168.8) * mm, "end": v(45.93, 171.07) * mm});
            skLineSegment(sketch, "E5282", {"start": v(45.93, 171.07) * mm, "end": v(46.79, 172.76) * mm});
            skLineSegment(sketch, "E5283", {"start": v(46.79, 172.76) * mm, "end": v(47.94, 173.92) * mm});
            skLineSegment(sketch, "E5284", {"start": v(47.94, 173.92) * mm, "end": v(49.42, 174.56) * mm});
            skLineSegment(sketch, "E5285", {"start": v(49.42, 174.56) * mm, "end": v(51.27, 174.72) * mm});
            skLineSegment(sketch, "E5286", {"start": v(51.27, 174.72) * mm, "end": v(53.52, 174.42) * mm});
            skLineSegment(sketch, "E5287", {"start": v(53.52, 174.42) * mm, "end": v(56.23, 173.68) * mm});
            skLineSegment(sketch, "E5288", {"start": v(56.23, 173.68) * mm, "end": v(56.53, 173.58) * mm});
            skLineSegment(sketch, "E5289", {"start": v(56.53, 173.58) * mm, "end": v(56.83, 173.5) * mm});
            skLineSegment(sketch, "E5290", {"start": v(56.83, 173.5) * mm, "end": v(57.13, 173.4) * mm});
            skLineSegment(sketch, "E5291", {"start": v(57.13, 173.4) * mm, "end": v(57.43, 173.32) * mm});
            skLineSegment(sketch, "E5292", {"start": v(57.43, 173.32) * mm, "end": v(57.73, 173.23) * mm});
            skLineSegment(sketch, "E5293", {"start": v(57.73, 173.23) * mm, "end": v(58.03, 173.14) * mm});
            skLineSegment(sketch, "E5294", {"start": v(58.03, 173.14) * mm, "end": v(58.32, 173.05) * mm});
            skLineSegment(sketch, "E5295", {"start": v(58.32, 173.05) * mm, "end": v(58.62, 172.95) * mm});
            skLineSegment(sketch, "E5296", {"start": v(58.62, 172.95) * mm, "end": v(59.4, 172.72) * mm});
            skLineSegment(sketch, "E5297", {"start": v(59.4, 172.72) * mm, "end": v(60.1, 172.65) * mm});
            skLineSegment(sketch, "E5298", {"start": v(60.1, 172.65) * mm, "end": v(60.73, 172.71) * mm});
            skLineSegment(sketch, "E5299", {"start": v(60.73, 172.71) * mm, "end": v(61.29, 172.91) * mm});
            skLineSegment(sketch, "E5300", {"start": v(61.29, 172.91) * mm, "end": v(61.77, 173.26) * mm});
            skLineSegment(sketch, "E5301", {"start": v(61.77, 173.26) * mm, "end": v(62.2, 173.73) * mm});
            skLineSegment(sketch, "E5302", {"start": v(62.2, 173.73) * mm, "end": v(62.54, 174.35) * mm});
            skLineSegment(sketch, "E5303", {"start": v(62.54, 174.35) * mm, "end": v(62.82, 175.09) * mm});
            skLineSegment(sketch, "E5304", {"start": v(62.82, 175.09) * mm, "end": v(62.99, 175.81) * mm});
            skLineSegment(sketch, "E5305", {"start": v(62.99, 175.81) * mm, "end": v(63.01, 176.45) * mm});
            skLineSegment(sketch, "E5306", {"start": v(63.01, 176.45) * mm, "end": v(62.9, 177) * mm});
            skLineSegment(sketch, "E5307", {"start": v(62.9, 177) * mm, "end": v(62.67, 177.5) * mm});
            skLineSegment(sketch, "E5308", {"start": v(62.67, 177.5) * mm, "end": v(62.32, 177.9) * mm});
            skLineSegment(sketch, "E5309", {"start": v(62.32, 177.9) * mm, "end": v(61.85, 178.26) * mm});
            skLineSegment(sketch, "E5310", {"start": v(61.85, 178.26) * mm, "end": v(61.28, 178.55) * mm});
            skLineSegment(sketch, "E5311", {"start": v(61.28, 178.55) * mm, "end": v(60.62, 178.8) * mm});
            skLineSegment(sketch, "E5312", {"start": v(60.62, 178.8) * mm, "end": v(59.9, 179.02) * mm});
            skLineSegment(sketch, "E5313", {"start": v(59.9, 179.02) * mm, "end": v(59.2, 179.27) * mm});
            skLineSegment(sketch, "E5314", {"start": v(59.2, 179.27) * mm, "end": v(58.49, 179.53) * mm});
            skLineSegment(sketch, "E5315", {"start": v(58.49, 179.53) * mm, "end": v(57.79, 179.79) * mm});
            skLineSegment(sketch, "E5316", {"start": v(57.79, 179.79) * mm, "end": v(57.08, 180.04) * mm});
            skLineSegment(sketch, "E5317", {"start": v(57.08, 180.04) * mm, "end": v(56.37, 180.28) * mm});
            skLineSegment(sketch, "E5318", {"start": v(56.37, 180.28) * mm, "end": v(55.66, 180.5) * mm});
            skLineSegment(sketch, "E5319", {"start": v(55.66, 180.5) * mm, "end": v(54.94, 180.7) * mm});
            skLineSegment(sketch, "E5320", {"start": v(54.94, 180.7) * mm, "end": v(53.46, 181.17) * mm});
            skLineSegment(sketch, "E5321", {"start": v(53.46, 181.17) * mm, "end": v(52.42, 181.8) * mm});
            skLineSegment(sketch, "E5322", {"start": v(52.42, 181.8) * mm, "end": v(51.75, 182.57) * mm});
            skLineSegment(sketch, "E5323", {"start": v(51.75, 182.57) * mm, "end": v(51.4, 183.45) * mm});
            skLineSegment(sketch, "E5324", {"start": v(51.4, 183.45) * mm, "end": v(51.32, 184.44) * mm});
            skLineSegment(sketch, "E5325", {"start": v(51.32, 184.44) * mm, "end": v(51.45, 185.53) * mm});
            skLineSegment(sketch, "E5326", {"start": v(51.45, 185.53) * mm, "end": v(51.72, 186.7) * mm});
            skLineSegment(sketch, "E5327", {"start": v(51.72, 186.7) * mm, "end": v(52.1, 187.93) * mm});
            skLineSegment(sketch, "E5328", {"start": v(52.1, 187.93) * mm, "end": v(52.54, 189.15) * mm});
            skLineSegment(sketch, "E5329", {"start": v(52.54, 189.15) * mm, "end": v(53.06, 190.18) * mm});
            skLineSegment(sketch, "E5330", {"start": v(53.06, 190.18) * mm, "end": v(53.66, 191) * mm});
            skLineSegment(sketch, "E5331", {"start": v(53.66, 191) * mm, "end": v(54.36, 191.6) * mm});
            skLineSegment(sketch, "E5332", {"start": v(54.36, 191.6) * mm, "end": v(55.2, 191.94) * mm});
            skLineSegment(sketch, "E5333", {"start": v(55.2, 191.94) * mm, "end": v(56.17, 192.03) * mm});
            skLineSegment(sketch, "E5334", {"start": v(56.17, 192.03) * mm, "end": v(57.3, 191.84) * mm});
            skLineSegment(sketch, "E5335", {"start": v(57.3, 191.84) * mm, "end": v(58.63, 191.35) * mm});
            skLineSegment(sketch, "E5336", {"start": v(58.63, 191.35) * mm, "end": v(59.43, 191.02) * mm});
            skLineSegment(sketch, "E5337", {"start": v(59.43, 191.02) * mm, "end": v(60.24, 190.71) * mm});
            skLineSegment(sketch, "E5338", {"start": v(60.24, 190.71) * mm, "end": v(61.07, 190.43) * mm});
            skLineSegment(sketch, "E5339", {"start": v(61.07, 190.43) * mm, "end": v(61.9, 190.17) * mm});
            skLineSegment(sketch, "E5340", {"start": v(61.9, 190.17) * mm, "end": v(62.74, 189.91) * mm});
            skLineSegment(sketch, "E5341", {"start": v(62.74, 189.91) * mm, "end": v(63.58, 189.66) * mm});
            skLineSegment(sketch, "E5342", {"start": v(63.58, 189.66) * mm, "end": v(64.42, 189.4) * mm});
            skLineSegment(sketch, "E5343", {"start": v(64.42, 189.4) * mm, "end": v(65.25, 189.15) * mm});
            skLineSegment(sketch, "E5344", {"start": v(-35.26, 165.53) * mm, "end": v(-38.2, 165.66) * mm});
            skLineSegment(sketch, "E5345", {"start": v(-38.2, 165.66) * mm, "end": v(-40.87, 166.25) * mm});
            skLineSegment(sketch, "E5346", {"start": v(-40.87, 166.25) * mm, "end": v(-43.27, 167.26) * mm});
            skLineSegment(sketch, "E5347", {"start": v(-43.27, 167.26) * mm, "end": v(-45.39, 168.7) * mm});
            skLineSegment(sketch, "E5348", {"start": v(-45.39, 168.7) * mm, "end": v(-47.2, 170.52) * mm});
            skLineSegment(sketch, "E5349", {"start": v(-47.2, 170.52) * mm, "end": v(-48.71, 172.73) * mm});
            skLineSegment(sketch, "E5350", {"start": v(-48.71, 172.73) * mm, "end": v(-49.9, 175.3) * mm});
            skLineSegment(sketch, "E5351", {"start": v(-49.9, 175.3) * mm, "end": v(-50.75, 178.22) * mm});
            skLineSegment(sketch, "E5352", {"start": v(-50.75, 178.22) * mm, "end": v(-51.16, 181.06) * mm});
            skLineSegment(sketch, "E5353", {"start": v(-51.16, 181.06) * mm, "end": v(-51.12, 183.8) * mm});
            skLineSegment(sketch, "E5354", {"start": v(-51.12, 183.8) * mm, "end": v(-50.67, 186.37) * mm});
            skLineSegment(sketch, "E5355", {"start": v(-50.67, 186.37) * mm, "end": v(-49.81, 188.76) * mm});
            skLineSegment(sketch, "E5356", {"start": v(-49.81, 188.76) * mm, "end": v(-48.57, 190.92) * mm});
            skLineSegment(sketch, "E5357", {"start": v(-48.57, 190.92) * mm, "end": v(-46.95, 192.83) * mm});
            skLineSegment(sketch, "E5358", {"start": v(-46.95, 192.83) * mm, "end": v(-44.97, 194.45) * mm});
            skLineSegment(sketch, "E5359", {"start": v(-44.97, 194.45) * mm, "end": v(-42.65, 195.74) * mm});
            skLineSegment(sketch, "E5360", {"start": v(-42.65, 195.74) * mm, "end": v(-41.53, 196.2) * mm});
            skLineSegment(sketch, "E5361", {"start": v(-41.53, 196.2) * mm, "end": v(-40.4, 196.56) * mm});
            skLineSegment(sketch, "E5362", {"start": v(-40.4, 196.56) * mm, "end": v(-39.26, 196.86) * mm});
            skLineSegment(sketch, "E5363", {"start": v(-39.26, 196.86) * mm, "end": v(-38.1, 197.08) * mm});
            skLineSegment(sketch, "E5364", {"start": v(-38.1, 197.08) * mm, "end": v(-36.94, 197.24) * mm});
            skLineSegment(sketch, "E5365", {"start": v(-36.94, 197.24) * mm, "end": v(-35.76, 197.32) * mm});
            skLineSegment(sketch, "E5366", {"start": v(-35.76, 197.32) * mm, "end": v(-34.58, 197.35) * mm});
            skLineSegment(sketch, "E5367", {"start": v(-34.58, 197.35) * mm, "end": v(-33.38, 197.31) * mm});
            skLineSegment(sketch, "E5368", {"start": v(-33.38, 197.31) * mm, "end": v(-32.48, 197.3) * mm});
            skLineSegment(sketch, "E5369", {"start": v(-32.48, 197.3) * mm, "end": v(-31.63, 197.4) * mm});
            skLineSegment(sketch, "E5370", {"start": v(-31.63, 197.4) * mm, "end": v(-30.86, 197.58) * mm});
            skLineSegment(sketch, "E5371", {"start": v(-30.86, 197.58) * mm, "end": v(-30.19, 197.9) * mm});
            skLineSegment(sketch, "E5372", {"start": v(-30.19, 197.9) * mm, "end": v(-29.62, 198.35) * mm});
            skLineSegment(sketch, "E5373", {"start": v(-29.62, 198.35) * mm, "end": v(-29.19, 198.94) * mm});
            skLineSegment(sketch, "E5374", {"start": v(-29.19, 198.94) * mm, "end": v(-28.9, 199.7) * mm});
            skLineSegment(sketch, "E5375", {"start": v(-28.9, 199.7) * mm, "end": v(-28.77, 200.64) * mm});
            skLineSegment(sketch, "E5376", {"start": v(-28.77, 200.64) * mm, "end": v(-28.86, 201.7) * mm});
            skLineSegment(sketch, "E5377", {"start": v(-28.86, 201.7) * mm, "end": v(-29.17, 202.46) * mm});
            skLineSegment(sketch, "E5378", {"start": v(-29.17, 202.46) * mm, "end": v(-29.66, 202.98) * mm});
            skLineSegment(sketch, "E5379", {"start": v(-29.66, 202.98) * mm, "end": v(-30.3, 203.3) * mm});
            skLineSegment(sketch, "E5380", {"start": v(-30.3, 203.3) * mm, "end": v(-31.04, 203.47) * mm});
            skLineSegment(sketch, "E5381", {"start": v(-31.04, 203.47) * mm, "end": v(-31.84, 203.56) * mm});
            skLineSegment(sketch, "E5382", {"start": v(-31.84, 203.56) * mm, "end": v(-32.66, 203.6) * mm});
            skLineSegment(sketch, "E5383", {"start": v(-32.66, 203.6) * mm, "end": v(-33.46, 203.64) * mm});
            skLineSegment(sketch, "E5384", {"start": v(-33.46, 203.64) * mm, "end": v(-33.9, 203.67) * mm});
            skLineSegment(sketch, "E5385", {"start": v(-33.9, 203.67) * mm, "end": v(-34.34, 203.68) * mm});
            skLineSegment(sketch, "E5386", {"start": v(-34.34, 203.68) * mm, "end": v(-34.77, 203.7) * mm});
            skLineSegment(sketch, "E5387", {"start": v(-34.77, 203.7) * mm, "end": v(-35.21, 203.7) * mm});
            skLineSegment(sketch, "E5388", {"start": v(-35.21, 203.7) * mm, "end": v(-35.65, 203.68) * mm});
            skLineSegment(sketch, "E5389", {"start": v(-35.65, 203.68) * mm, "end": v(-36.09, 203.67) * mm});
            skLineSegment(sketch, "E5390", {"start": v(-36.09, 203.67) * mm, "end": v(-36.52, 203.65) * mm});
            skLineSegment(sketch, "E5391", {"start": v(-36.52, 203.65) * mm, "end": v(-36.96, 203.62) * mm});
            skLineSegment(sketch, "E5392", {"start": v(-36.96, 203.62) * mm, "end": v(-41.06, 203.1) * mm});
            skLineSegment(sketch, "E5393", {"start": v(-41.06, 203.1) * mm, "end": v(-44.92, 202.05) * mm});
            skLineSegment(sketch, "E5394", {"start": v(-44.92, 202.05) * mm, "end": v(-48.49, 200.52) * mm});
            skLineSegment(sketch, "E5395", {"start": v(-48.49, 200.52) * mm, "end": v(-51.72, 198.54) * mm});
            skLineSegment(sketch, "E5396", {"start": v(-51.72, 198.54) * mm, "end": v(-54.55, 196.15) * mm});
            skLineSegment(sketch, "E5397", {"start": v(-54.55, 196.15) * mm, "end": v(-56.94, 193.38) * mm});
            skLineSegment(sketch, "E5398", {"start": v(-56.94, 193.38) * mm, "end": v(-58.84, 190.28) * mm});
            skLineSegment(sketch, "E5399", {"start": v(-58.84, 190.28) * mm, "end": v(-60.2, 186.87) * mm});
            skLineSegment(sketch, "E5400", {"start": v(-60.2, 186.87) * mm, "end": v(-60.89, 183.62) * mm});
            skLineSegment(sketch, "E5401", {"start": v(-60.89, 183.62) * mm, "end": v(-61.08, 180.33) * mm});
            skLineSegment(sketch, "E5402", {"start": v(-61.08, 180.33) * mm, "end": v(-60.8, 177.06) * mm});
            skLineSegment(sketch, "E5403", {"start": v(-60.8, 177.06) * mm, "end": v(-60.05, 173.88) * mm});
            skLineSegment(sketch, "E5404", {"start": v(-60.05, 173.88) * mm, "end": v(-58.86, 170.87) * mm});
            skLineSegment(sketch, "E5405", {"start": v(-58.86, 170.87) * mm, "end": v(-57.26, 168.1) * mm});
            skLineSegment(sketch, "E5406", {"start": v(-57.26, 168.1) * mm, "end": v(-55.26, 165.63) * mm});
            skLineSegment(sketch, "E5407", {"start": v(-55.26, 165.63) * mm, "end": v(-52.88, 163.54) * mm});
            skLineSegment(sketch, "E5408", {"start": v(-52.88, 163.54) * mm, "end": v(-49.55, 161.48) * mm});
            skLineSegment(sketch, "E5409", {"start": v(-49.55, 161.48) * mm, "end": v(-45.92, 159.98) * mm});
            skLineSegment(sketch, "E5410", {"start": v(-45.92, 159.98) * mm, "end": v(-42.08, 159.03) * mm});
            skLineSegment(sketch, "E5411", {"start": v(-42.08, 159.03) * mm, "end": v(-38.13, 158.64) * mm});
            skLineSegment(sketch, "E5412", {"start": v(-38.13, 158.64) * mm, "end": v(-34.17, 158.81) * mm});
            skLineSegment(sketch, "E5413", {"start": v(-34.17, 158.81) * mm, "end": v(-30.3, 159.55) * mm});
            skLineSegment(sketch, "E5414", {"start": v(-30.3, 159.55) * mm, "end": v(-26.63, 160.87) * mm});
            skLineSegment(sketch, "E5415", {"start": v(-26.63, 160.87) * mm, "end": v(-23.24, 162.76) * mm});
            skLineSegment(sketch, "E5416", {"start": v(-23.24, 162.76) * mm, "end": v(-22.54, 163.2) * mm});
            skLineSegment(sketch, "E5417", {"start": v(-22.54, 163.2) * mm, "end": v(-21.8, 163.67) * mm});
            skLineSegment(sketch, "E5418", {"start": v(-21.8, 163.67) * mm, "end": v(-21.08, 164.16) * mm});
            skLineSegment(sketch, "E5419", {"start": v(-21.08, 164.16) * mm, "end": v(-20.45, 164.72) * mm});
            skLineSegment(sketch, "E5420", {"start": v(-20.45, 164.72) * mm, "end": v(-19.98, 165.37) * mm});
            skLineSegment(sketch, "E5421", {"start": v(-19.98, 165.37) * mm, "end": v(-19.74, 166.14) * mm});
            skLineSegment(sketch, "E5422", {"start": v(-19.74, 166.14) * mm, "end": v(-19.79, 167.04) * mm});
            skLineSegment(sketch, "E5423", {"start": v(-19.79, 167.04) * mm, "end": v(-20.2, 168.1) * mm});
            skLineSegment(sketch, "E5424", {"start": v(-20.2, 168.1) * mm, "end": v(-20.9, 169.11) * mm});
            skLineSegment(sketch, "E5425", {"start": v(-20.9, 169.11) * mm, "end": v(-21.62, 169.73) * mm});
            skLineSegment(sketch, "E5426", {"start": v(-21.62, 169.73) * mm, "end": v(-22.38, 170.02) * mm});
            skLineSegment(sketch, "E5427", {"start": v(-22.38, 170.02) * mm, "end": v(-23.16, 170.02) * mm});
            skLineSegment(sketch, "E5428", {"start": v(-23.16, 170.02) * mm, "end": v(-23.97, 169.8) * mm});
            skLineSegment(sketch, "E5429", {"start": v(-23.97, 169.8) * mm, "end": v(-24.79, 169.43) * mm});
            skLineSegment(sketch, "E5430", {"start": v(-24.79, 169.43) * mm, "end": v(-25.62, 168.94) * mm});
            skLineSegment(sketch, "E5431", {"start": v(-25.62, 168.94) * mm, "end": v(-26.45, 168.4) * mm});
            skLineSegment(sketch, "E5432", {"start": v(-26.45, 168.4) * mm, "end": v(-27.52, 167.72) * mm});
            skLineSegment(sketch, "E5433", {"start": v(-27.52, 167.72) * mm, "end": v(-28.62, 167.14) * mm});
            skLineSegment(sketch, "E5434", {"start": v(-28.62, 167.14) * mm, "end": v(-29.74, 166.65) * mm});
            skLineSegment(sketch, "E5435", {"start": v(-29.74, 166.65) * mm, "end": v(-30.86, 166.24) * mm});
            skLineSegment(sketch, "E5436", {"start": v(-30.86, 166.24) * mm, "end": v(-31.98, 165.93) * mm});
            skLineSegment(sketch, "E5437", {"start": v(-31.98, 165.93) * mm, "end": v(-33.09, 165.7) * mm});
            skLineSegment(sketch, "E5438", {"start": v(-33.09, 165.7) * mm, "end": v(-34.19, 165.57) * mm});
            skLineSegment(sketch, "E5439", {"start": v(-34.19, 165.57) * mm, "end": v(-35.26, 165.53) * mm});
            skLineSegment(sketch, "E5440", {"start": v(91.5, 182.67) * mm, "end": v(88.18, 182.43) * mm});
            skLineSegment(sketch, "E5441", {"start": v(88.18, 182.43) * mm, "end": v(85.35, 181.64) * mm});
            skLineSegment(sketch, "E5442", {"start": v(85.35, 181.64) * mm, "end": v(83.03, 180.37) * mm});
            skLineSegment(sketch, "E5443", {"start": v(83.03, 180.37) * mm, "end": v(81.26, 178.67) * mm});
            skLineSegment(sketch, "E5444", {"start": v(81.26, 178.67) * mm, "end": v(80.06, 176.58) * mm});
            skLineSegment(sketch, "E5445", {"start": v(80.06, 176.58) * mm, "end": v(79.44, 174.15) * mm});
            skLineSegment(sketch, "E5446", {"start": v(79.44, 174.15) * mm, "end": v(79.43, 171.44) * mm});
            skLineSegment(sketch, "E5447", {"start": v(79.43, 171.44) * mm, "end": v(80.06, 168.5) * mm});
            skLineSegment(sketch, "E5448", {"start": v(80.06, 168.5) * mm, "end": v(80.59, 166.9) * mm});
            skLineSegment(sketch, "E5449", {"start": v(80.59, 166.9) * mm, "end": v(81.16, 165.32) * mm});
            skLineSegment(sketch, "E5450", {"start": v(81.16, 165.32) * mm, "end": v(81.77, 163.75) * mm});
            skLineSegment(sketch, "E5451", {"start": v(81.77, 163.75) * mm, "end": v(82.4, 162.19) * mm});
            skLineSegment(sketch, "E5452", {"start": v(82.4, 162.19) * mm, "end": v(83.02, 160.63) * mm});
            skLineSegment(sketch, "E5453", {"start": v(83.02, 160.63) * mm, "end": v(83.65, 159.07) * mm});
            skLineSegment(sketch, "E5454", {"start": v(83.65, 159.07) * mm, "end": v(84.27, 157.5) * mm});
            skLineSegment(sketch, "E5455", {"start": v(84.27, 157.5) * mm, "end": v(84.85, 155.93) * mm});
            skLineSegment(sketch, "E5456", {"start": v(84.85, 155.93) * mm, "end": v(85.17, 154.84) * mm});
            skLineSegment(sketch, "E5457", {"start": v(85.17, 154.84) * mm, "end": v(85.35, 153.77) * mm});
            skLineSegment(sketch, "E5458", {"start": v(85.35, 153.77) * mm, "end": v(85.37, 152.73) * mm});
            skLineSegment(sketch, "E5459", {"start": v(85.37, 152.73) * mm, "end": v(85.23, 151.73) * mm});
            skLineSegment(sketch, "E5460", {"start": v(85.23, 151.73) * mm, "end": v(84.9, 150.78) * mm});
            skLineSegment(sketch, "E5461", {"start": v(84.9, 150.78) * mm, "end": v(84.4, 149.9) * mm});
            skLineSegment(sketch, "E5462", {"start": v(84.4, 149.9) * mm, "end": v(83.71, 149.08) * mm});
            skLineSegment(sketch, "E5463", {"start": v(83.71, 149.08) * mm, "end": v(82.81, 148.34) * mm});
            skLineSegment(sketch, "E5464", {"start": v(82.81, 148.34) * mm, "end": v(81.71, 147.73) * mm});
            skLineSegment(sketch, "E5465", {"start": v(81.71, 147.73) * mm, "end": v(80.63, 147.39) * mm});
            skLineSegment(sketch, "E5466", {"start": v(80.63, 147.39) * mm, "end": v(79.57, 147.3) * mm});
            skLineSegment(sketch, "E5467", {"start": v(79.57, 147.3) * mm, "end": v(78.54, 147.42) * mm});
            skLineSegment(sketch, "E5468", {"start": v(78.54, 147.42) * mm, "end": v(77.52, 147.74) * mm});
            skLineSegment(sketch, "E5469", {"start": v(77.52, 147.74) * mm, "end": v(76.54, 148.23) * mm});
            skLineSegment(sketch, "E5470", {"start": v(76.54, 148.23) * mm, "end": v(75.58, 148.86) * mm});
            skLineSegment(sketch, "E5471", {"start": v(75.58, 148.86) * mm, "end": v(74.66, 149.6) * mm});
            skLineSegment(sketch, "E5472", {"start": v(74.66, 149.6) * mm, "end": v(74.25, 149.98) * mm});
            skLineSegment(sketch, "E5473", {"start": v(74.25, 149.98) * mm, "end": v(73.84, 150.37) * mm});
            skLineSegment(sketch, "E5474", {"start": v(73.84, 150.37) * mm, "end": v(73.44, 150.77) * mm});
            skLineSegment(sketch, "E5475", {"start": v(73.44, 150.77) * mm, "end": v(73.06, 151.18) * mm});
            skLineSegment(sketch, "E5476", {"start": v(73.06, 151.18) * mm, "end": v(72.69, 151.6) * mm});
            skLineSegment(sketch, "E5477", {"start": v(72.69, 151.6) * mm, "end": v(72.34, 152.04) * mm});
            skLineSegment(sketch, "E5478", {"start": v(72.34, 152.04) * mm, "end": v(72, 152.49) * mm});
            skLineSegment(sketch, "E5479", {"start": v(72, 152.49) * mm, "end": v(71.69, 152.94) * mm});
            skLineSegment(sketch, "E5480", {"start": v(71.69, 152.94) * mm, "end": v(71.13, 153.7) * mm});
            skLineSegment(sketch, "E5481", {"start": v(71.13, 153.7) * mm, "end": v(70.54, 154.3) * mm});
            skLineSegment(sketch, "E5482", {"start": v(70.54, 154.3) * mm, "end": v(69.93, 154.73) * mm});
            skLineSegment(sketch, "E5483", {"start": v(69.93, 154.73) * mm, "end": v(69.28, 154.99) * mm});
            skLineSegment(sketch, "E5484", {"start": v(69.28, 154.99) * mm, "end": v(68.6, 155.06) * mm});
            skLineSegment(sketch, "E5485", {"start": v(68.6, 155.06) * mm, "end": v(67.87, 154.95) * mm});
            skLineSegment(sketch, "E5486", {"start": v(67.87, 154.95) * mm, "end": v(67.1, 154.65) * mm});
            skLineSegment(sketch, "E5487", {"start": v(67.1, 154.65) * mm, "end": v(66.29, 154.16) * mm});
            skLineSegment(sketch, "E5488", {"start": v(66.29, 154.16) * mm, "end": v(65.44, 153.42) * mm});
            skLineSegment(sketch, "E5489", {"start": v(65.44, 153.42) * mm, "end": v(64.98, 152.7) * mm});
            skLineSegment(sketch, "E5490", {"start": v(64.98, 152.7) * mm, "end": v(64.83, 152) * mm});
            skLineSegment(sketch, "E5491", {"start": v(64.83, 152) * mm, "end": v(64.94, 151.31) * mm});
            skLineSegment(sketch, "E5492", {"start": v(64.94, 151.31) * mm, "end": v(65.24, 150.64) * mm});
            skLineSegment(sketch, "E5493", {"start": v(65.24, 150.64) * mm, "end": v(65.66, 149.98) * mm});
            skLineSegment(sketch, "E5494", {"start": v(65.66, 149.98) * mm, "end": v(66.15, 149.35) * mm});
            skLineSegment(sketch, "E5495", {"start": v(66.15, 149.35) * mm, "end": v(66.63, 148.72) * mm});
            skLineSegment(sketch, "E5496", {"start": v(66.63, 148.72) * mm, "end": v(67.63, 147.5) * mm});
            skLineSegment(sketch, "E5497", {"start": v(67.63, 147.5) * mm, "end": v(68.69, 146.34) * mm});
            skLineSegment(sketch, "E5498", {"start": v(68.69, 146.34) * mm, "end": v(69.82, 145.28) * mm});
            skLineSegment(sketch, "E5499", {"start": v(69.82, 145.28) * mm, "end": v(71.02, 144.3) * mm});
            skLineSegment(sketch, "E5500", {"start": v(71.02, 144.3) * mm, "end": v(72.29, 143.42) * mm});
            skLineSegment(sketch, "E5501", {"start": v(72.29, 143.42) * mm, "end": v(73.62, 142.63) * mm});
            skLineSegment(sketch, "E5502", {"start": v(73.62, 142.63) * mm, "end": v(75.03, 141.96) * mm});
            skLineSegment(sketch, "E5503", {"start": v(75.03, 141.96) * mm, "end": v(76.5, 141.39) * mm});
            skLineSegment(sketch, "E5504", {"start": v(76.5, 141.39) * mm, "end": v(78.46, 140.78) * mm});
            skLineSegment(sketch, "E5505", {"start": v(78.46, 140.78) * mm, "end": v(80.41, 140.32) * mm});
            skLineSegment(sketch, "E5506", {"start": v(80.41, 140.32) * mm, "end": v(82.36, 140.06) * mm});
            skLineSegment(sketch, "E5507", {"start": v(82.36, 140.06) * mm, "end": v(84.27, 140.04) * mm});
            skLineSegment(sketch, "E5508", {"start": v(84.27, 140.04) * mm, "end": v(86.15, 140.3) * mm});
            skLineSegment(sketch, "E5509", {"start": v(86.15, 140.3) * mm, "end": v(87.98, 140.9) * mm});
            skLineSegment(sketch, "E5510", {"start": v(87.98, 140.9) * mm, "end": v(89.76, 141.85) * mm});
            skLineSegment(sketch, "E5511", {"start": v(89.76, 141.85) * mm, "end": v(91.46, 143.22) * mm});
            skLineSegment(sketch, "E5512", {"start": v(91.46, 143.22) * mm, "end": v(92.87, 144.8) * mm});
            skLineSegment(sketch, "E5513", {"start": v(92.87, 144.8) * mm, "end": v(93.88, 146.48) * mm});
            skLineSegment(sketch, "E5514", {"start": v(93.88, 146.48) * mm, "end": v(94.53, 148.21) * mm});
            skLineSegment(sketch, "E5515", {"start": v(94.53, 148.21) * mm, "end": v(94.86, 150) * mm});
            skLineSegment(sketch, "E5516", {"start": v(94.86, 150) * mm, "end": v(94.9, 151.84) * mm});
            skLineSegment(sketch, "E5517", {"start": v(94.9, 151.84) * mm, "end": v(94.68, 153.72) * mm});
            skLineSegment(sketch, "E5518", {"start": v(94.68, 153.72) * mm, "end": v(94.24, 155.63) * mm});
            skLineSegment(sketch, "E5519", {"start": v(94.24, 155.63) * mm, "end": v(93.62, 157.56) * mm});
            skLineSegment(sketch, "E5520", {"start": v(93.62, 157.56) * mm, "end": v(93.08, 159.02) * mm});
            skLineSegment(sketch, "E5521", {"start": v(93.08, 159.02) * mm, "end": v(92.54, 160.48) * mm});
            skLineSegment(sketch, "E5522", {"start": v(92.54, 160.48) * mm, "end": v(91.99, 161.94) * mm});
            skLineSegment(sketch, "E5523", {"start": v(91.99, 161.94) * mm, "end": v(91.43, 163.4) * mm});
            skLineSegment(sketch, "E5524", {"start": v(91.43, 163.4) * mm, "end": v(90.88, 164.85) * mm});
            skLineSegment(sketch, "E5525", {"start": v(90.88, 164.85) * mm, "end": v(90.33, 166.3) * mm});
            skLineSegment(sketch, "E5526", {"start": v(90.33, 166.3) * mm, "end": v(89.8, 167.77) * mm});
            skLineSegment(sketch, "E5527", {"start": v(89.8, 167.77) * mm, "end": v(89.27, 169.24) * mm});
            skLineSegment(sketch, "E5528", {"start": v(89.27, 169.24) * mm, "end": v(89.07, 169.91) * mm});
            skLineSegment(sketch, "E5529", {"start": v(89.07, 169.91) * mm, "end": v(88.93, 170.59) * mm});
            skLineSegment(sketch, "E5530", {"start": v(88.93, 170.59) * mm, "end": v(88.87, 171.26) * mm});
            skLineSegment(sketch, "E5531", {"start": v(88.87, 171.26) * mm, "end": v(88.91, 171.92) * mm});
            skLineSegment(sketch, "E5532", {"start": v(88.91, 171.92) * mm, "end": v(89.05, 172.56) * mm});
            skLineSegment(sketch, "E5533", {"start": v(89.05, 172.56) * mm, "end": v(89.31, 173.17) * mm});
            skLineSegment(sketch, "E5534", {"start": v(89.31, 173.17) * mm, "end": v(89.7, 173.75) * mm});
            skLineSegment(sketch, "E5535", {"start": v(89.7, 173.75) * mm, "end": v(90.24, 174.3) * mm});
            skLineSegment(sketch, "E5536", {"start": v(90.24, 174.3) * mm, "end": v(90.9, 174.78) * mm});
            skLineSegment(sketch, "E5537", {"start": v(90.9, 174.78) * mm, "end": v(91.6, 175.1) * mm});
            skLineSegment(sketch, "E5538", {"start": v(91.6, 175.1) * mm, "end": v(92.3, 175.3) * mm});
            skLineSegment(sketch, "E5539", {"start": v(92.3, 175.3) * mm, "end": v(93.02, 175.36) * mm});
            skLineSegment(sketch, "E5540", {"start": v(93.02, 175.36) * mm, "end": v(93.73, 175.3) * mm});
            skLineSegment(sketch, "E5541", {"start": v(93.73, 175.3) * mm, "end": v(94.44, 175.13) * mm});
            skLineSegment(sketch, "E5542", {"start": v(94.44, 175.13) * mm, "end": v(95.14, 174.85) * mm});
            skLineSegment(sketch, "E5543", {"start": v(95.14, 174.85) * mm, "end": v(95.81, 174.47) * mm});
            skLineSegment(sketch, "E5544", {"start": v(95.81, 174.47) * mm, "end": v(96.42, 174.06) * mm});
            skLineSegment(sketch, "E5545", {"start": v(96.42, 174.06) * mm, "end": v(97.02, 173.63) * mm});
            skLineSegment(sketch, "E5546", {"start": v(97.02, 173.63) * mm, "end": v(97.6, 173.17) * mm});
            skLineSegment(sketch, "E5547", {"start": v(97.6, 173.17) * mm, "end": v(98.17, 172.69) * mm});
            skLineSegment(sketch, "E5548", {"start": v(98.17, 172.69) * mm, "end": v(98.72, 172.19) * mm});
            skLineSegment(sketch, "E5549", {"start": v(98.72, 172.19) * mm, "end": v(99.27, 171.68) * mm});
            skLineSegment(sketch, "E5550", {"start": v(99.27, 171.68) * mm, "end": v(99.81, 171.17) * mm});
            skLineSegment(sketch, "E5551", {"start": v(99.81, 171.17) * mm, "end": v(100.35, 170.66) * mm});
            skLineSegment(sketch, "E5552", {"start": v(100.35, 170.66) * mm, "end": v(101, 170.14) * mm});
            skLineSegment(sketch, "E5553", {"start": v(101, 170.14) * mm, "end": v(101.64, 169.81) * mm});
            skLineSegment(sketch, "E5554", {"start": v(101.64, 169.81) * mm, "end": v(102.28, 169.65) * mm});
            skLineSegment(sketch, "E5555", {"start": v(102.28, 169.65) * mm, "end": v(102.9, 169.63) * mm});
            skLineSegment(sketch, "E5556", {"start": v(102.9, 169.63) * mm, "end": v(103.53, 169.75) * mm});
            skLineSegment(sketch, "E5557", {"start": v(103.53, 169.75) * mm, "end": v(104.14, 169.98) * mm});
            skLineSegment(sketch, "E5558", {"start": v(104.14, 169.98) * mm, "end": v(104.72, 170.31) * mm});
            skLineSegment(sketch, "E5559", {"start": v(104.72, 170.31) * mm, "end": v(105.3, 170.72) * mm});
            skLineSegment(sketch, "E5560", {"start": v(105.3, 170.72) * mm, "end": v(105.79, 171.2) * mm});
            skLineSegment(sketch, "E5561", {"start": v(105.79, 171.2) * mm, "end": v(106.05, 171.7) * mm});
            skLineSegment(sketch, "E5562", {"start": v(106.05, 171.7) * mm, "end": v(106.13, 172.2) * mm});
            skLineSegment(sketch, "E5563", {"start": v(106.13, 172.2) * mm, "end": v(106.05, 172.71) * mm});
            skLineSegment(sketch, "E5564", {"start": v(106.05, 172.71) * mm, "end": v(105.85, 173.21) * mm});
            skLineSegment(sketch, "E5565", {"start": v(105.85, 173.21) * mm, "end": v(105.58, 173.7) * mm});
            skLineSegment(sketch, "E5566", {"start": v(105.58, 173.7) * mm, "end": v(105.25, 174.17) * mm});
            skLineSegment(sketch, "E5567", {"start": v(105.25, 174.17) * mm, "end": v(104.92, 174.63) * mm});
            skLineSegment(sketch, "E5568", {"start": v(104.92, 174.63) * mm, "end": v(103.49, 176.38) * mm});
            skLineSegment(sketch, "E5569", {"start": v(103.49, 176.38) * mm, "end": v(101.96, 177.93) * mm});
            skLineSegment(sketch, "E5570", {"start": v(101.96, 177.93) * mm, "end": v(100.34, 179.27) * mm});
            skLineSegment(sketch, "E5571", {"start": v(100.34, 179.27) * mm, "end": v(98.65, 180.39) * mm});
            skLineSegment(sketch, "E5572", {"start": v(98.65, 180.39) * mm, "end": v(96.91, 181.3) * mm});
            skLineSegment(sketch, "E5573", {"start": v(96.91, 181.3) * mm, "end": v(95.13, 181.98) * mm});
            skLineSegment(sketch, "E5574", {"start": v(95.13, 181.98) * mm, "end": v(93.32, 182.44) * mm});
            skLineSegment(sketch, "E5575", {"start": v(93.32, 182.44) * mm, "end": v(91.5, 182.67) * mm});
            skLineSegment(sketch, "E5576", {"start": v(142.99, 142.26) * mm, "end": v(142.91, 142.84) * mm});
            skLineSegment(sketch, "E5577", {"start": v(142.91, 142.84) * mm, "end": v(142.75, 143.35) * mm});
            skLineSegment(sketch, "E5578", {"start": v(142.75, 143.35) * mm, "end": v(142.51, 143.8) * mm});
            skLineSegment(sketch, "E5579", {"start": v(142.51, 143.8) * mm, "end": v(142.22, 144.2) * mm});
            skLineSegment(sketch, "E5580", {"start": v(142.22, 144.2) * mm, "end": v(141.88, 144.57) * mm});
            skLineSegment(sketch, "E5581", {"start": v(141.88, 144.57) * mm, "end": v(141.52, 144.9) * mm});
            skLineSegment(sketch, "E5582", {"start": v(141.52, 144.9) * mm, "end": v(141.15, 145.23) * mm});
            skLineSegment(sketch, "E5583", {"start": v(141.15, 145.23) * mm, "end": v(140.79, 145.56) * mm});
            skLineSegment(sketch, "E5584", {"start": v(140.79, 145.56) * mm, "end": v(138.57, 147.57) * mm});
            skLineSegment(sketch, "E5585", {"start": v(138.57, 147.57) * mm, "end": v(136.35, 149.6) * mm});
            skLineSegment(sketch, "E5586", {"start": v(136.35, 149.6) * mm, "end": v(134.14, 151.63) * mm});
            skLineSegment(sketch, "E5587", {"start": v(134.14, 151.63) * mm, "end": v(131.92, 153.64) * mm});
            skLineSegment(sketch, "E5588", {"start": v(131.92, 153.64) * mm, "end": v(129.69, 155.65) * mm});
            skLineSegment(sketch, "E5589", {"start": v(129.69, 155.65) * mm, "end": v(127.43, 157.62) * mm});
            skLineSegment(sketch, "E5590", {"start": v(127.43, 157.62) * mm, "end": v(125.16, 159.57) * mm});
            skLineSegment(sketch, "E5591", {"start": v(125.16, 159.57) * mm, "end": v(122.85, 161.48) * mm});
            skLineSegment(sketch, "E5592", {"start": v(122.85, 161.48) * mm, "end": v(122.15, 162.2) * mm});
            skLineSegment(sketch, "E5593", {"start": v(122.15, 162.2) * mm, "end": v(121.46, 163.13) * mm});
            skLineSegment(sketch, "E5594", {"start": v(121.46, 163.13) * mm, "end": v(120.73, 164.1) * mm});
            skLineSegment(sketch, "E5595", {"start": v(120.73, 164.1) * mm, "end": v(119.94, 164.96) * mm});
            skLineSegment(sketch, "E5596", {"start": v(119.94, 164.96) * mm, "end": v(119.07, 165.54) * mm});
            skLineSegment(sketch, "E5597", {"start": v(119.07, 165.54) * mm, "end": v(118.07, 165.7) * mm});
            skLineSegment(sketch, "E5598", {"start": v(118.07, 165.7) * mm, "end": v(116.93, 165.25) * mm});
            skLineSegment(sketch, "E5599", {"start": v(116.93, 165.25) * mm, "end": v(115.6, 164.06) * mm});
            skLineSegment(sketch, "E5600", {"start": v(115.6, 164.06) * mm, "end": v(114.62, 162.63) * mm});
            skLineSegment(sketch, "E5601", {"start": v(114.62, 162.63) * mm, "end": v(114.33, 161.44) * mm});
            skLineSegment(sketch, "E5602", {"start": v(114.33, 161.44) * mm, "end": v(114.58, 160.44) * mm});
            skLineSegment(sketch, "E5603", {"start": v(114.58, 160.44) * mm, "end": v(115.23, 159.6) * mm});
            skLineSegment(sketch, "E5604", {"start": v(115.23, 159.6) * mm, "end": v(116.14, 158.89) * mm});
            skLineSegment(sketch, "E5605", {"start": v(116.14, 158.89) * mm, "end": v(117.17, 158.24) * mm});
            skLineSegment(sketch, "E5606", {"start": v(117.17, 158.24) * mm, "end": v(118.17, 157.63) * mm});
            skLineSegment(sketch, "E5607", {"start": v(118.17, 157.63) * mm, "end": v(119, 157.01) * mm});
            skLineSegment(sketch, "E5608", {"start": v(119, 157.01) * mm, "end": v(120.07, 155.99) * mm});
            skLineSegment(sketch, "E5609", {"start": v(120.07, 155.99) * mm, "end": v(120.86, 155) * mm});
            skLineSegment(sketch, "E5610", {"start": v(120.86, 155) * mm, "end": v(121.38, 154.06) * mm});
            skLineSegment(sketch, "E5611", {"start": v(121.38, 154.06) * mm, "end": v(121.6, 153.12) * mm});
            skLineSegment(sketch, "E5612", {"start": v(121.6, 153.12) * mm, "end": v(121.55, 152.16) * mm});
            skLineSegment(sketch, "E5613", {"start": v(121.55, 152.16) * mm, "end": v(121.18, 151.15) * mm});
            skLineSegment(sketch, "E5614", {"start": v(121.18, 151.15) * mm, "end": v(120.5, 150.08) * mm});
            skLineSegment(sketch, "E5615", {"start": v(120.5, 150.08) * mm, "end": v(119.5, 148.92) * mm});
            skLineSegment(sketch, "E5616", {"start": v(119.5, 148.92) * mm, "end": v(117.14, 146.42) * mm});
            skLineSegment(sketch, "E5617", {"start": v(117.14, 146.42) * mm, "end": v(114.8, 143.9) * mm});
            skLineSegment(sketch, "E5618", {"start": v(114.8, 143.9) * mm, "end": v(112.5, 141.35) * mm});
            skLineSegment(sketch, "E5619", {"start": v(112.5, 141.35) * mm, "end": v(110.21, 138.79) * mm});
            skLineSegment(sketch, "E5620", {"start": v(110.21, 138.79) * mm, "end": v(107.93, 136.22) * mm});
            skLineSegment(sketch, "E5621", {"start": v(107.93, 136.22) * mm, "end": v(105.64, 133.66) * mm});
            skLineSegment(sketch, "E5622", {"start": v(105.64, 133.66) * mm, "end": v(103.33, 131.1) * mm});
            skLineSegment(sketch, "E5623", {"start": v(103.33, 131.1) * mm, "end": v(101, 128.58) * mm});
            skLineSegment(sketch, "E5624", {"start": v(101, 128.58) * mm, "end": v(100.21, 127.6) * mm});
            skLineSegment(sketch, "E5625", {"start": v(100.21, 127.6) * mm, "end": v(99.73, 126.7) * mm});
            skLineSegment(sketch, "E5626", {"start": v(99.73, 126.7) * mm, "end": v(99.54, 125.85) * mm});
            skLineSegment(sketch, "E5627", {"start": v(99.54, 125.85) * mm, "end": v(99.6, 125.06) * mm});
            skLineSegment(sketch, "E5628", {"start": v(99.6, 125.06) * mm, "end": v(99.89, 124.3) * mm});
            skLineSegment(sketch, "E5629", {"start": v(99.89, 124.3) * mm, "end": v(100.37, 123.55) * mm});
            skLineSegment(sketch, "E5630", {"start": v(100.37, 123.55) * mm, "end": v(101.02, 122.78) * mm});
            skLineSegment(sketch, "E5631", {"start": v(101.02, 122.78) * mm, "end": v(101.8, 122) * mm});
            skLineSegment(sketch, "E5632", {"start": v(101.8, 122) * mm, "end": v(102.69, 121.23) * mm});
            skLineSegment(sketch, "E5633", {"start": v(102.69, 121.23) * mm, "end": v(103.5, 120.73) * mm});
            skLineSegment(sketch, "E5634", {"start": v(103.5, 120.73) * mm, "end": v(104.28, 120.46) * mm});
            skLineSegment(sketch, "E5635", {"start": v(104.28, 120.46) * mm, "end": v(105.02, 120.43) * mm});
            skLineSegment(sketch, "E5636", {"start": v(105.02, 120.43) * mm, "end": v(105.74, 120.62) * mm});
            skLineSegment(sketch, "E5637", {"start": v(105.74, 120.62) * mm, "end": v(106.46, 121.02) * mm});
            skLineSegment(sketch, "E5638", {"start": v(106.46, 121.02) * mm, "end": v(107.18, 121.62) * mm});
            skLineSegment(sketch, "E5639", {"start": v(107.18, 121.62) * mm, "end": v(107.94, 122.41) * mm});
            skLineSegment(sketch, "E5640", {"start": v(107.94, 122.41) * mm, "end": v(110, 124.75) * mm});
            skLineSegment(sketch, "E5641", {"start": v(110, 124.75) * mm, "end": v(112.08, 127.09) * mm});
            skLineSegment(sketch, "E5642", {"start": v(112.08, 127.09) * mm, "end": v(114.17, 129.4) * mm});
            skLineSegment(sketch, "E5643", {"start": v(114.17, 129.4) * mm, "end": v(116.27, 131.73) * mm});
            skLineSegment(sketch, "E5644", {"start": v(116.27, 131.73) * mm, "end": v(118.37, 134.04) * mm});
            skLineSegment(sketch, "E5645", {"start": v(118.37, 134.04) * mm, "end": v(120.46, 136.36) * mm});
            skLineSegment(sketch, "E5646", {"start": v(120.46, 136.36) * mm, "end": v(122.56, 138.67) * mm});
            skLineSegment(sketch, "E5647", {"start": v(122.56, 138.67) * mm, "end": v(124.64, 141) * mm});
            skLineSegment(sketch, "E5648", {"start": v(124.64, 141) * mm, "end": v(126.35, 142.88) * mm});
            skLineSegment(sketch, "E5649", {"start": v(126.35, 142.88) * mm, "end": v(127.7, 144.24) * mm});
            skLineSegment(sketch, "E5650", {"start": v(127.7, 144.24) * mm, "end": v(128.82, 145.07) * mm});
            skLineSegment(sketch, "E5651", {"start": v(128.82, 145.07) * mm, "end": v(129.86, 145.4) * mm});
            skLineSegment(sketch, "E5652", {"start": v(129.86, 145.4) * mm, "end": v(130.94, 145.2) * mm});
            skLineSegment(sketch, "E5653", {"start": v(130.94, 145.2) * mm, "end": v(132.19, 144.52) * mm});
            skLineSegment(sketch, "E5654", {"start": v(132.19, 144.52) * mm, "end": v(133.73, 143.34) * mm});
            skLineSegment(sketch, "E5655", {"start": v(133.73, 143.34) * mm, "end": v(135.71, 141.68) * mm});
            skLineSegment(sketch, "E5656", {"start": v(135.71, 141.68) * mm, "end": v(136, 141.44) * mm});
            skLineSegment(sketch, "E5657", {"start": v(136, 141.44) * mm, "end": v(136.28, 141.19) * mm});
            skLineSegment(sketch, "E5658", {"start": v(136.28, 141.19) * mm, "end": v(136.57, 140.94) * mm});
            skLineSegment(sketch, "E5659", {"start": v(136.57, 140.94) * mm, "end": v(136.85, 140.7) * mm});
            skLineSegment(sketch, "E5660", {"start": v(136.85, 140.7) * mm, "end": v(137.14, 140.45) * mm});
            skLineSegment(sketch, "E5661", {"start": v(137.14, 140.45) * mm, "end": v(137.44, 140.23) * mm});
            skLineSegment(sketch, "E5662", {"start": v(137.44, 140.23) * mm, "end": v(137.75, 140.01) * mm});
            skLineSegment(sketch, "E5663", {"start": v(137.75, 140.01) * mm, "end": v(138.06, 139.82) * mm});
            skLineSegment(sketch, "E5664", {"start": v(138.06, 139.82) * mm, "end": v(139.05, 139.38) * mm});
            skLineSegment(sketch, "E5665", {"start": v(139.05, 139.38) * mm, "end": v(139.88, 139.27) * mm});
            skLineSegment(sketch, "E5666", {"start": v(139.88, 139.27) * mm, "end": v(140.56, 139.45) * mm});
            skLineSegment(sketch, "E5667", {"start": v(140.56, 139.45) * mm, "end": v(141.13, 139.83) * mm});
            skLineSegment(sketch, "E5668", {"start": v(141.13, 139.83) * mm, "end": v(141.63, 140.37) * mm});
            skLineSegment(sketch, "E5669", {"start": v(141.63, 140.37) * mm, "end": v(142.09, 141) * mm});
            skLineSegment(sketch, "E5670", {"start": v(142.09, 141) * mm, "end": v(142.53, 141.65) * mm});
            skLineSegment(sketch, "E5671", {"start": v(142.53, 141.65) * mm, "end": v(142.99, 142.26) * mm});
            skLineSegment(sketch, "E5672", {"start": v(-202.84, -58.35) * mm, "end": v(-210.2, -57.6) * mm});
            skLineSegment(sketch, "E5673", {"start": v(-210.2, -57.6) * mm, "end": v(-217.07, -55.47) * mm});
            skLineSegment(sketch, "E5674", {"start": v(-217.07, -55.47) * mm, "end": v(-223.3, -52.1) * mm});
            skLineSegment(sketch, "E5675", {"start": v(-223.3, -52.1) * mm, "end": v(-228.73, -47.65) * mm});
            skLineSegment(sketch, "E5676", {"start": v(-228.73, -47.65) * mm, "end": v(-233.24, -42.27) * mm});
            skLineSegment(sketch, "E5677", {"start": v(-233.24, -42.27) * mm, "end": v(-236.67, -36.08) * mm});
            skLineSegment(sketch, "E5678", {"start": v(-236.67, -36.08) * mm, "end": v(-238.86, -29.25) * mm});
            skLineSegment(sketch, "E5679", {"start": v(-238.86, -29.25) * mm, "end": v(-239.68, -21.92) * mm});
            skLineSegment(sketch, "E5680", {"start": v(-239.68, -21.92) * mm, "end": v(-239, -14.38) * mm});
            skLineSegment(sketch, "E5681", {"start": v(-239, -14.38) * mm, "end": v(-236.85, -7.37) * mm});
            skLineSegment(sketch, "E5682", {"start": v(-236.85, -7.37) * mm, "end": v(-233.41, -1.03) * mm});
            skLineSegment(sketch, "E5683", {"start": v(-233.41, -1.03) * mm, "end": v(-228.83, 4.5) * mm});
            skLineSegment(sketch, "E5684", {"start": v(-228.83, 4.5) * mm, "end": v(-223.25, 9.04) * mm});
            skLineSegment(sketch, "E5685", {"start": v(-223.25, 9.04) * mm, "end": v(-216.83, 12.47) * mm});
            skLineSegment(sketch, "E5686", {"start": v(-216.83, 12.47) * mm, "end": v(-209.73, 14.62) * mm});
            skLineSegment(sketch, "E5687", {"start": v(-209.73, 14.62) * mm, "end": v(-202.1, 15.34) * mm});
            skLineSegment(sketch, "E5688", {"start": v(-202.1, 15.34) * mm, "end": v(-194.72, 14.54) * mm});
            skLineSegment(sketch, "E5689", {"start": v(-194.72, 14.54) * mm, "end": v(-187.84, 12.33) * mm});
            skLineSegment(sketch, "E5690", {"start": v(-187.84, 12.33) * mm, "end": v(-181.62, 8.86) * mm});
            skLineSegment(sketch, "E5691", {"start": v(-181.62, 8.86) * mm, "end": v(-176.19, 4.29) * mm});
            skLineSegment(sketch, "E5692", {"start": v(-176.19, 4.29) * mm, "end": v(-171.72, -1.23) * mm});
            skLineSegment(sketch, "E5693", {"start": v(-171.72, -1.23) * mm, "end": v(-168.35, -7.53) * mm});
            skLineSegment(sketch, "E5694", {"start": v(-168.35, -7.53) * mm, "end": v(-166.24, -14.48) * mm});
            skLineSegment(sketch, "E5695", {"start": v(-166.24, -14.48) * mm, "end": v(-165.54, -21.9) * mm});
            skLineSegment(sketch, "E5696", {"start": v(-165.54, -21.9) * mm, "end": v(-166.35, -29.27) * mm});
            skLineSegment(sketch, "E5697", {"start": v(-166.35, -29.27) * mm, "end": v(-168.55, -36.13) * mm});
            skLineSegment(sketch, "E5698", {"start": v(-168.55, -36.13) * mm, "end": v(-172, -42.33) * mm});
            skLineSegment(sketch, "E5699", {"start": v(-172, -42.33) * mm, "end": v(-176.57, -47.72) * mm});
            skLineSegment(sketch, "E5700", {"start": v(-176.57, -47.72) * mm, "end": v(-182.08, -52.17) * mm});
            skLineSegment(sketch, "E5701", {"start": v(-182.08, -52.17) * mm, "end": v(-188.4, -55.52) * mm});
            skLineSegment(sketch, "E5702", {"start": v(-188.4, -55.52) * mm, "end": v(-195.36, -57.63) * mm});
            skLineSegment(sketch, "E5703", {"start": v(-195.36, -57.63) * mm, "end": v(-202.84, -58.35) * mm});
            skLineSegment(sketch, "E5704", {"start": v(-223.76, -28.56) * mm, "end": v(-223.64, -29.67) * mm});
            skLineSegment(sketch, "E5705", {"start": v(-223.64, -29.67) * mm, "end": v(-223.5, -30.78) * mm});
            skLineSegment(sketch, "E5706", {"start": v(-223.5, -30.78) * mm, "end": v(-223.37, -31.9) * mm});
            skLineSegment(sketch, "E5707", {"start": v(-223.37, -31.9) * mm, "end": v(-223.24, -33) * mm});
            skLineSegment(sketch, "E5708", {"start": v(-223.24, -33) * mm, "end": v(-223.11, -34.12) * mm});
            skLineSegment(sketch, "E5709", {"start": v(-223.11, -34.12) * mm, "end": v(-223, -35.24) * mm});
            skLineSegment(sketch, "E5710", {"start": v(-223, -35.24) * mm, "end": v(-222.92, -36.35) * mm});
            skLineSegment(sketch, "E5711", {"start": v(-222.92, -36.35) * mm, "end": v(-222.86, -37.47) * mm});
            skLineSegment(sketch, "E5712", {"start": v(-222.86, -37.47) * mm, "end": v(-222.53, -40.91) * mm});
            skLineSegment(sketch, "E5713", {"start": v(-222.53, -40.91) * mm, "end": v(-221.8, -43.72) * mm});
            skLineSegment(sketch, "E5714", {"start": v(-221.8, -43.72) * mm, "end": v(-220.64, -45.96) * mm});
            skLineSegment(sketch, "E5715", {"start": v(-220.64, -45.96) * mm, "end": v(-218.98, -47.74) * mm});
            skLineSegment(sketch, "E5716", {"start": v(-218.98, -47.74) * mm, "end": v(-216.8, -49.13) * mm});
            skLineSegment(sketch, "E5717", {"start": v(-216.8, -49.13) * mm, "end": v(-214.05, -50.21) * mm});
            skLineSegment(sketch, "E5718", {"start": v(-214.05, -50.21) * mm, "end": v(-210.68, -51.08) * mm});
            skLineSegment(sketch, "E5719", {"start": v(-210.68, -51.08) * mm, "end": v(-206.65, -51.82) * mm});
            skLineSegment(sketch, "E5720", {"start": v(-206.65, -51.82) * mm, "end": v(-205.25, -51.97) * mm});
            skLineSegment(sketch, "E5721", {"start": v(-205.25, -51.97) * mm, "end": v(-204.1, -51.92) * mm});
            skLineSegment(sketch, "E5722", {"start": v(-204.1, -51.92) * mm, "end": v(-203.2, -51.67) * mm});
            skLineSegment(sketch, "E5723", {"start": v(-203.2, -51.67) * mm, "end": v(-202.54, -51.2) * mm});
            skLineSegment(sketch, "E5724", {"start": v(-202.54, -51.2) * mm, "end": v(-202.14, -50.5) * mm});
            skLineSegment(sketch, "E5725", {"start": v(-202.14, -50.5) * mm, "end": v(-201.98, -49.55) * mm});
            skLineSegment(sketch, "E5726", {"start": v(-201.98, -49.55) * mm, "end": v(-202.08, -48.34) * mm});
            skLineSegment(sketch, "E5727", {"start": v(-202.08, -48.34) * mm, "end": v(-202.44, -46.86) * mm});
            skLineSegment(sketch, "E5728", {"start": v(-202.44, -46.86) * mm, "end": v(-203.54, -42.7) * mm});
            skLineSegment(sketch, "E5729", {"start": v(-203.54, -42.7) * mm, "end": v(-204.34, -38.53) * mm});
            skLineSegment(sketch, "E5730", {"start": v(-204.34, -38.53) * mm, "end": v(-204.84, -34.36) * mm});
            skLineSegment(sketch, "E5731", {"start": v(-204.84, -34.36) * mm, "end": v(-205.02, -30.19) * mm});
            skLineSegment(sketch, "E5732", {"start": v(-205.02, -30.19) * mm, "end": v(-204.86, -26.01) * mm});
            skLineSegment(sketch, "E5733", {"start": v(-204.86, -26.01) * mm, "end": v(-204.36, -21.84) * mm});
            skLineSegment(sketch, "E5734", {"start": v(-204.36, -21.84) * mm, "end": v(-203.5, -17.66) * mm});
            skLineSegment(sketch, "E5735", {"start": v(-203.5, -17.66) * mm, "end": v(-202.27, -13.49) * mm});
            skLineSegment(sketch, "E5736", {"start": v(-202.27, -13.49) * mm, "end": v(-201.84, -12.43) * mm});
            skLineSegment(sketch, "E5737", {"start": v(-201.84, -12.43) * mm, "end": v(-201.3, -11.37) * mm});
            skLineSegment(sketch, "E5738", {"start": v(-201.3, -11.37) * mm, "end": v(-200.74, -10.3) * mm});
            skLineSegment(sketch, "E5739", {"start": v(-200.74, -10.3) * mm, "end": v(-200.2, -9.25) * mm});
            skLineSegment(sketch, "E5740", {"start": v(-200.2, -9.25) * mm, "end": v(-199.76, -8.2) * mm});
            skLineSegment(sketch, "E5741", {"start": v(-199.76, -8.2) * mm, "end": v(-199.48, -7.18) * mm});
            skLineSegment(sketch, "E5742", {"start": v(-199.48, -7.18) * mm, "end": v(-199.42, -6.17) * mm});
            skLineSegment(sketch, "E5743", {"start": v(-199.42, -6.17) * mm, "end": v(-199.66, -5.2) * mm});
            skLineSegment(sketch, "E5744", {"start": v(-199.66, -5.2) * mm, "end": v(-200.23, -4.32) * mm});
            skLineSegment(sketch, "E5745", {"start": v(-200.23, -4.32) * mm, "end": v(-201.03, -3.74) * mm});
            skLineSegment(sketch, "E5746", {"start": v(-201.03, -3.74) * mm, "end": v(-202.01, -3.37) * mm});
            skLineSegment(sketch, "E5747", {"start": v(-202.01, -3.37) * mm, "end": v(-203.12, -3.15) * mm});
            skLineSegment(sketch, "E5748", {"start": v(-203.12, -3.15) * mm, "end": v(-204.3, -3) * mm});
            skLineSegment(sketch, "E5749", {"start": v(-204.3, -3) * mm, "end": v(-205.49, -2.83) * mm});
            skLineSegment(sketch, "E5750", {"start": v(-205.49, -2.83) * mm, "end": v(-206.64, -2.6) * mm});
            skLineSegment(sketch, "E5751", {"start": v(-206.64, -2.6) * mm, "end": v(-207.7, -2.22) * mm});
            skLineSegment(sketch, "E5752", {"start": v(-207.7, -2.22) * mm, "end": v(-208.05, -2.08) * mm});
            skLineSegment(sketch, "E5753", {"start": v(-208.05, -2.08) * mm, "end": v(-208.4, -1.95) * mm});
            skLineSegment(sketch, "E5754", {"start": v(-208.4, -1.95) * mm, "end": v(-208.76, -1.83) * mm});
            skLineSegment(sketch, "E5755", {"start": v(-208.76, -1.83) * mm, "end": v(-209.12, -1.71) * mm});
            skLineSegment(sketch, "E5756", {"start": v(-209.12, -1.71) * mm, "end": v(-209.48, -1.6) * mm});
            skLineSegment(sketch, "E5757", {"start": v(-209.48, -1.6) * mm, "end": v(-209.83, -1.47) * mm});
            skLineSegment(sketch, "E5758", {"start": v(-209.83, -1.47) * mm, "end": v(-210.17, -1.32) * mm});
            skLineSegment(sketch, "E5759", {"start": v(-210.17, -1.32) * mm, "end": v(-210.5, -1.15) * mm});
            skLineSegment(sketch, "E5760", {"start": v(-210.5, -1.15) * mm, "end": v(-211.44, -0.68) * mm});
            skLineSegment(sketch, "E5761", {"start": v(-211.44, -0.68) * mm, "end": v(-212.29, -0.44) * mm});
            skLineSegment(sketch, "E5762", {"start": v(-212.29, -0.44) * mm, "end": v(-213.06, -0.42) * mm});
            skLineSegment(sketch, "E5763", {"start": v(-213.06, -0.42) * mm, "end": v(-213.76, -0.6) * mm});
            skLineSegment(sketch, "E5764", {"start": v(-213.76, -0.6) * mm, "end": v(-214.41, -0.96) * mm});
            skLineSegment(sketch, "E5765", {"start": v(-214.41, -0.96) * mm, "end": v(-215.02, -1.5) * mm});
            skLineSegment(sketch, "E5766", {"start": v(-215.02, -1.5) * mm, "end": v(-215.6, -2.18) * mm});
            skLineSegment(sketch, "E5767", {"start": v(-215.6, -2.18) * mm, "end": v(-216.15, -3) * mm});
            skLineSegment(sketch, "E5768", {"start": v(-216.15, -3) * mm, "end": v(-217.88, -5.97) * mm});
            skLineSegment(sketch, "E5769", {"start": v(-217.88, -5.97) * mm, "end": v(-219.38, -9) * mm});
            skLineSegment(sketch, "E5770", {"start": v(-219.38, -9) * mm, "end": v(-220.65, -12.09) * mm});
            skLineSegment(sketch, "E5771", {"start": v(-220.65, -12.09) * mm, "end": v(-221.7, -15.25) * mm});
            skLineSegment(sketch, "E5772", {"start": v(-221.7, -15.25) * mm, "end": v(-222.55, -18.47) * mm});
            skLineSegment(sketch, "E5773", {"start": v(-222.55, -18.47) * mm, "end": v(-223.16, -21.76) * mm});
            skLineSegment(sketch, "E5774", {"start": v(-223.16, -21.76) * mm, "end": v(-223.57, -25.12) * mm});
            skLineSegment(sketch, "E5775", {"start": v(-223.57, -25.12) * mm, "end": v(-223.76, -28.56) * mm});
            skLineSegment(sketch, "E5776", {"start": v(-171.73, -16.26) * mm, "end": v(-173.82, -19) * mm});
            skLineSegment(sketch, "E5777", {"start": v(-173.82, -19) * mm, "end": v(-176.01, -21.48) * mm});
            skLineSegment(sketch, "E5778", {"start": v(-176.01, -21.48) * mm, "end": v(-178.33, -23.7) * mm});
            skLineSegment(sketch, "E5779", {"start": v(-178.33, -23.7) * mm, "end": v(-180.78, -25.64) * mm});
            skLineSegment(sketch, "E5780", {"start": v(-180.78, -25.64) * mm, "end": v(-183.37, -27.32) * mm});
            skLineSegment(sketch, "E5781", {"start": v(-183.37, -27.32) * mm, "end": v(-186.13, -28.72) * mm});
            skLineSegment(sketch, "E5782", {"start": v(-186.13, -28.72) * mm, "end": v(-189.07, -29.84) * mm});
            skLineSegment(sketch, "E5783", {"start": v(-189.07, -29.84) * mm, "end": v(-192.2, -30.68) * mm});
            skLineSegment(sketch, "E5784", {"start": v(-192.2, -30.68) * mm, "end": v(-195.05, -31.32) * mm});
            skLineSegment(sketch, "E5785", {"start": v(-195.05, -31.32) * mm, "end": v(-197.18, -31.92) * mm});
            skLineSegment(sketch, "E5786", {"start": v(-197.18, -31.92) * mm, "end": v(-198.66, -32.61) * mm});
            skLineSegment(sketch, "E5787", {"start": v(-198.66, -32.61) * mm, "end": v(-199.56, -33.5) * mm});
            skLineSegment(sketch, "E5788", {"start": v(-199.56, -33.5) * mm, "end": v(-199.96, -34.73) * mm});
            skLineSegment(sketch, "E5789", {"start": v(-199.96, -34.73) * mm, "end": v(-199.94, -36.4) * mm});
            skLineSegment(sketch, "E5790", {"start": v(-199.94, -36.4) * mm, "end": v(-199.57, -38.63) * mm});
            skLineSegment(sketch, "E5791", {"start": v(-199.57, -38.63) * mm, "end": v(-198.93, -41.55) * mm});
            skLineSegment(sketch, "E5792", {"start": v(-198.93, -41.55) * mm, "end": v(-198.7, -42.46) * mm});
            skLineSegment(sketch, "E5793", {"start": v(-198.7, -42.46) * mm, "end": v(-198.47, -43.36) * mm});
            skLineSegment(sketch, "E5794", {"start": v(-198.47, -43.36) * mm, "end": v(-198.22, -44.26) * mm});
            skLineSegment(sketch, "E5795", {"start": v(-198.22, -44.26) * mm, "end": v(-197.95, -45.15) * mm});
            skLineSegment(sketch, "E5796", {"start": v(-197.95, -45.15) * mm, "end": v(-197.67, -46.04) * mm});
            skLineSegment(sketch, "E5797", {"start": v(-197.67, -46.04) * mm, "end": v(-197.4, -46.94) * mm});
            skLineSegment(sketch, "E5798", {"start": v(-197.4, -46.94) * mm, "end": v(-197.11, -47.83) * mm});
            skLineSegment(sketch, "E5799", {"start": v(-197.11, -47.83) * mm, "end": v(-196.84, -48.72) * mm});
            skLineSegment(sketch, "E5800", {"start": v(-196.84, -48.72) * mm, "end": v(-196.58, -49.38) * mm});
            skLineSegment(sketch, "E5801", {"start": v(-196.58, -49.38) * mm, "end": v(-196.25, -49.9) * mm});
            skLineSegment(sketch, "E5802", {"start": v(-196.25, -49.9) * mm, "end": v(-195.86, -50.3) * mm});
            skLineSegment(sketch, "E5803", {"start": v(-195.86, -50.3) * mm, "end": v(-195.4, -50.59) * mm});
            skLineSegment(sketch, "E5804", {"start": v(-195.4, -50.59) * mm, "end": v(-194.89, -50.76) * mm});
            skLineSegment(sketch, "E5805", {"start": v(-194.89, -50.76) * mm, "end": v(-194.3, -50.84) * mm});
            skLineSegment(sketch, "E5806", {"start": v(-194.3, -50.84) * mm, "end": v(-193.66, -50.83) * mm});
            skLineSegment(sketch, "E5807", {"start": v(-193.66, -50.83) * mm, "end": v(-192.95, -50.75) * mm});
            skLineSegment(sketch, "E5808", {"start": v(-192.95, -50.75) * mm, "end": v(-188.07, -49.2) * mm});
            skLineSegment(sketch, "E5809", {"start": v(-188.07, -49.2) * mm, "end": v(-183.52, -46.4) * mm});
            skLineSegment(sketch, "E5810", {"start": v(-183.52, -46.4) * mm, "end": v(-179.44, -42.58) * mm});
            skLineSegment(sketch, "E5811", {"start": v(-179.44, -42.58) * mm, "end": v(-176, -37.97) * mm});
            skLineSegment(sketch, "E5812", {"start": v(-176, -37.97) * mm, "end": v(-173.34, -32.8) * mm});
            skLineSegment(sketch, "E5813", {"start": v(-173.34, -32.8) * mm, "end": v(-171.64, -27.3) * mm});
            skLineSegment(sketch, "E5814", {"start": v(-171.64, -27.3) * mm, "end": v(-171.05, -21.71) * mm});
            skLineSegment(sketch, "E5815", {"start": v(-171.05, -21.71) * mm, "end": v(-171.73, -16.26) * mm});
            skLineSegment(sketch, "E5816", {"start": v(-196.4, -26.6) * mm, "end": v(-192.94, -26) * mm});
            skLineSegment(sketch, "E5817", {"start": v(-192.94, -26) * mm, "end": v(-189.68, -25.06) * mm});
            skLineSegment(sketch, "E5818", {"start": v(-189.68, -25.06) * mm, "end": v(-186.65, -23.8) * mm});
            skLineSegment(sketch, "E5819", {"start": v(-186.65, -23.8) * mm, "end": v(-183.85, -22.2) * mm});
            skLineSegment(sketch, "E5820", {"start": v(-183.85, -22.2) * mm, "end": v(-181.28, -20.26) * mm});
            skLineSegment(sketch, "E5821", {"start": v(-181.28, -20.26) * mm, "end": v(-178.95, -17.95) * mm});
            skLineSegment(sketch, "E5822", {"start": v(-178.95, -17.95) * mm, "end": v(-176.87, -15.27) * mm});
            skLineSegment(sketch, "E5823", {"start": v(-176.87, -15.27) * mm, "end": v(-175.05, -12.2) * mm});
            skLineSegment(sketch, "E5824", {"start": v(-175.05, -12.2) * mm, "end": v(-174.43, -10.37) * mm});
            skLineSegment(sketch, "E5825", {"start": v(-174.43, -10.37) * mm, "end": v(-174.27, -8.28) * mm});
            skLineSegment(sketch, "E5826", {"start": v(-174.27, -8.28) * mm, "end": v(-174.52, -6.07) * mm});
            skLineSegment(sketch, "E5827", {"start": v(-174.52, -6.07) * mm, "end": v(-175.14, -3.85) * mm});
            skLineSegment(sketch, "E5828", {"start": v(-175.14, -3.85) * mm, "end": v(-176.08, -1.74) * mm});
            skLineSegment(sketch, "E5829", {"start": v(-176.08, -1.74) * mm, "end": v(-177.3, 0.12) * mm});
            skLineSegment(sketch, "E5830", {"start": v(-177.3, 0.12) * mm, "end": v(-178.76, 1.6) * mm});
            skLineSegment(sketch, "E5831", {"start": v(-178.76, 1.6) * mm, "end": v(-180.4, 2.6) * mm});
            skLineSegment(sketch, "E5832", {"start": v(-180.4, 2.6) * mm, "end": v(-180.58, 2.68) * mm});
            skLineSegment(sketch, "E5833", {"start": v(-180.58, 2.68) * mm, "end": v(-180.78, 2.75) * mm});
            skLineSegment(sketch, "E5834", {"start": v(-180.78, 2.75) * mm, "end": v(-181, 2.81) * mm});
            skLineSegment(sketch, "E5835", {"start": v(-181, 2.81) * mm, "end": v(-181.2, 2.87) * mm});
            skLineSegment(sketch, "E5836", {"start": v(-181.2, 2.87) * mm, "end": v(-181.4, 2.9) * mm});
            skLineSegment(sketch, "E5837", {"start": v(-181.4, 2.9) * mm, "end": v(-181.56, 2.92) * mm});
            skLineSegment(sketch, "E5838", {"start": v(-181.56, 2.92) * mm, "end": v(-181.7, 2.9) * mm});
            skLineSegment(sketch, "E5839", {"start": v(-181.7, 2.9) * mm, "end": v(-181.78, 2.85) * mm});
            skLineSegment(sketch, "E5840", {"start": v(-181.78, 2.85) * mm, "end": v(-183.08, 1.57) * mm});
            skLineSegment(sketch, "E5841", {"start": v(-183.08, 1.57) * mm, "end": v(-184.55, 0.5) * mm});
            skLineSegment(sketch, "E5842", {"start": v(-184.55, 0.5) * mm, "end": v(-186.13, -0.4) * mm});
            skLineSegment(sketch, "E5843", {"start": v(-186.13, -0.4) * mm, "end": v(-187.75, -1.25) * mm});
            skLineSegment(sketch, "E5844", {"start": v(-187.75, -1.25) * mm, "end": v(-189.34, -2.09) * mm});
            skLineSegment(sketch, "E5845", {"start": v(-189.34, -2.09) * mm, "end": v(-190.85, -3) * mm});
            skLineSegment(sketch, "E5846", {"start": v(-190.85, -3) * mm, "end": v(-192.2, -4.06) * mm});
            skLineSegment(sketch, "E5847", {"start": v(-192.2, -4.06) * mm, "end": v(-193.34, -5.34) * mm});
            skLineSegment(sketch, "E5848", {"start": v(-193.34, -5.34) * mm, "end": v(-194.66, -7.37) * mm});
            skLineSegment(sketch, "E5849", {"start": v(-194.66, -7.37) * mm, "end": v(-195.8, -9.49) * mm});
            skLineSegment(sketch, "E5850", {"start": v(-195.8, -9.49) * mm, "end": v(-196.79, -11.69) * mm});
            skLineSegment(sketch, "E5851", {"start": v(-196.79, -11.69) * mm, "end": v(-197.62, -13.96) * mm});
            skLineSegment(sketch, "E5852", {"start": v(-197.62, -13.96) * mm, "end": v(-198.31, -16.29) * mm});
            skLineSegment(sketch, "E5853", {"start": v(-198.31, -16.29) * mm, "end": v(-198.88, -18.67) * mm});
            skLineSegment(sketch, "E5854", {"start": v(-198.88, -18.67) * mm, "end": v(-199.32, -21.08) * mm});
            skLineSegment(sketch, "E5855", {"start": v(-199.32, -21.08) * mm, "end": v(-199.65, -23.53) * mm});
            skLineSegment(sketch, "E5856", {"start": v(-199.65, -23.53) * mm, "end": v(-199.69, -24.4) * mm});
            skLineSegment(sketch, "E5857", {"start": v(-199.69, -24.4) * mm, "end": v(-199.59, -25.1) * mm});
            skLineSegment(sketch, "E5858", {"start": v(-199.59, -25.1) * mm, "end": v(-199.36, -25.67) * mm});
            skLineSegment(sketch, "E5859", {"start": v(-199.36, -25.67) * mm, "end": v(-199, -26.1) * mm});
            skLineSegment(sketch, "E5860", {"start": v(-199, -26.1) * mm, "end": v(-198.52, -26.4) * mm});
            skLineSegment(sketch, "E5861", {"start": v(-198.52, -26.4) * mm, "end": v(-197.92, -26.58) * mm});
            skLineSegment(sketch, "E5862", {"start": v(-197.92, -26.58) * mm, "end": v(-197.22, -26.64) * mm});
            skLineSegment(sketch, "E5863", {"start": v(-197.22, -26.64) * mm, "end": v(-196.4, -26.6) * mm});
            skLineSegment(sketch, "E5864", {"start": v(-202.26, 11.7) * mm, "end": v(-203.4, 11.73) * mm});
            skLineSegment(sketch, "E5865", {"start": v(-203.4, 11.73) * mm, "end": v(-204.53, 11.74) * mm});
            skLineSegment(sketch, "E5866", {"start": v(-204.53, 11.74) * mm, "end": v(-205.65, 11.7) * mm});
            skLineSegment(sketch, "E5867", {"start": v(-205.65, 11.7) * mm, "end": v(-206.77, 11.62) * mm});
            skLineSegment(sketch, "E5868", {"start": v(-206.77, 11.62) * mm, "end": v(-207.87, 11.47) * mm});
            skLineSegment(sketch, "E5869", {"start": v(-207.87, 11.47) * mm, "end": v(-208.97, 11.24) * mm});
            skLineSegment(sketch, "E5870", {"start": v(-208.97, 11.24) * mm, "end": v(-210.04, 10.92) * mm});
            skLineSegment(sketch, "E5871", {"start": v(-210.04, 10.92) * mm, "end": v(-211.1, 10.5) * mm});
            skLineSegment(sketch, "E5872", {"start": v(-211.1, 10.5) * mm, "end": v(-211.88, 10.1) * mm});
            skLineSegment(sketch, "E5873", {"start": v(-211.88, 10.1) * mm, "end": v(-212.57, 9.65) * mm});
            skLineSegment(sketch, "E5874", {"start": v(-212.57, 9.65) * mm, "end": v(-213.1, 9.13) * mm});
            skLineSegment(sketch, "E5875", {"start": v(-213.1, 9.13) * mm, "end": v(-213.48, 8.55) * mm});
            skLineSegment(sketch, "E5876", {"start": v(-213.48, 8.55) * mm, "end": v(-213.64, 7.9) * mm});
            skLineSegment(sketch, "E5877", {"start": v(-213.64, 7.9) * mm, "end": v(-213.57, 7.17) * mm});
            skLineSegment(sketch, "E5878", {"start": v(-213.57, 7.17) * mm, "end": v(-213.22, 6.38) * mm});
            skLineSegment(sketch, "E5879", {"start": v(-213.22, 6.38) * mm, "end": v(-212.58, 5.5) * mm});
            skLineSegment(sketch, "E5880", {"start": v(-212.58, 5.5) * mm, "end": v(-210.65, 3.94) * mm});
            skLineSegment(sketch, "E5881", {"start": v(-210.65, 3.94) * mm, "end": v(-208, 2.66) * mm});
            skLineSegment(sketch, "E5882", {"start": v(-208, 2.66) * mm, "end": v(-204.85, 1.7) * mm});
            skLineSegment(sketch, "E5883", {"start": v(-204.85, 1.7) * mm, "end": v(-201.43, 1.08) * mm});
            skLineSegment(sketch, "E5884", {"start": v(-201.43, 1.08) * mm, "end": v(-197.97, 0.82) * mm});
            skLineSegment(sketch, "E5885", {"start": v(-197.97, 0.82) * mm, "end": v(-194.68, 0.97) * mm});
            skLineSegment(sketch, "E5886", {"start": v(-194.68, 0.97) * mm, "end": v(-191.8, 1.54) * mm});
            skLineSegment(sketch, "E5887", {"start": v(-191.8, 1.54) * mm, "end": v(-189.56, 2.57) * mm});
            skLineSegment(sketch, "E5888", {"start": v(-189.56, 2.57) * mm, "end": v(-188.47, 3.44) * mm});
            skLineSegment(sketch, "E5889", {"start": v(-188.47, 3.44) * mm, "end": v(-187.72, 4.34) * mm});
            skLineSegment(sketch, "E5890", {"start": v(-187.72, 4.34) * mm, "end": v(-187.29, 5.24) * mm});
            skLineSegment(sketch, "E5891", {"start": v(-187.29, 5.24) * mm, "end": v(-187.2, 6.14) * mm});
            skLineSegment(sketch, "E5892", {"start": v(-187.2, 6.14) * mm, "end": v(-187.43, 7) * mm});
            skLineSegment(sketch, "E5893", {"start": v(-187.43, 7) * mm, "end": v(-188, 7.83) * mm});
            skLineSegment(sketch, "E5894", {"start": v(-188, 7.83) * mm, "end": v(-188.9, 8.6) * mm});
            skLineSegment(sketch, "E5895", {"start": v(-188.9, 8.6) * mm, "end": v(-190.14, 9.27) * mm});
            skLineSegment(sketch, "E5896", {"start": v(-190.14, 9.27) * mm, "end": v(-191.59, 9.88) * mm});
            skLineSegment(sketch, "E5897", {"start": v(-191.59, 9.88) * mm, "end": v(-193.05, 10.4) * mm});
            skLineSegment(sketch, "E5898", {"start": v(-193.05, 10.4) * mm, "end": v(-194.54, 10.85) * mm});
            skLineSegment(sketch, "E5899", {"start": v(-194.54, 10.85) * mm, "end": v(-196.05, 11.2) * mm});
            skLineSegment(sketch, "E5900", {"start": v(-196.05, 11.2) * mm, "end": v(-197.57, 11.47) * mm});
            skLineSegment(sketch, "E5901", {"start": v(-197.57, 11.47) * mm, "end": v(-199.12, 11.65) * mm});
            skLineSegment(sketch, "E5902", {"start": v(-199.12, 11.65) * mm, "end": v(-200.68, 11.72) * mm});
            skLineSegment(sketch, "E5903", {"start": v(-200.68, 11.72) * mm, "end": v(-202.26, 11.7) * mm});
            skLineSegment(sketch, "E5904", {"start": v(-227.52, -40.43) * mm, "end": v(-227.78, -37.94) * mm});
            skLineSegment(sketch, "E5905", {"start": v(-227.78, -37.94) * mm, "end": v(-228, -35.56) * mm});
            skLineSegment(sketch, "E5906", {"start": v(-228, -35.56) * mm, "end": v(-228.16, -33.27) * mm});
            skLineSegment(sketch, "E5907", {"start": v(-228.16, -33.27) * mm, "end": v(-228.27, -31.06) * mm});
            skLineSegment(sketch, "E5908", {"start": v(-228.27, -31.06) * mm, "end": v(-228.3, -28.92) * mm});
            skLineSegment(sketch, "E5909", {"start": v(-228.3, -28.92) * mm, "end": v(-228.27, -26.83) * mm});
            skLineSegment(sketch, "E5910", {"start": v(-228.27, -26.83) * mm, "end": v(-228.15, -24.77) * mm});
            skLineSegment(sketch, "E5911", {"start": v(-228.15, -24.77) * mm, "end": v(-227.93, -22.74) * mm});
            skLineSegment(sketch, "E5912", {"start": v(-227.93, -22.74) * mm, "end": v(-227.83, -21) * mm});
            skLineSegment(sketch, "E5913", {"start": v(-227.83, -21) * mm, "end": v(-228, -19.45) * mm});
            skLineSegment(sketch, "E5914", {"start": v(-228, -19.45) * mm, "end": v(-228.42, -18.04) * mm});
            skLineSegment(sketch, "E5915", {"start": v(-228.42, -18.04) * mm, "end": v(-229.07, -16.74) * mm});
            skLineSegment(sketch, "E5916", {"start": v(-229.07, -16.74) * mm, "end": v(-229.93, -15.53) * mm});
            skLineSegment(sketch, "E5917", {"start": v(-229.93, -15.53) * mm, "end": v(-230.97, -14.36) * mm});
            skLineSegment(sketch, "E5918", {"start": v(-230.97, -14.36) * mm, "end": v(-232.17, -13.2) * mm});
            skLineSegment(sketch, "E5919", {"start": v(-232.17, -13.2) * mm, "end": v(-233.5, -12.04) * mm});
            skLineSegment(sketch, "E5920", {"start": v(-233.5, -12.04) * mm, "end": v(-234.2, -15.88) * mm});
            skLineSegment(sketch, "E5921", {"start": v(-234.2, -15.88) * mm, "end": v(-234.5, -19.58) * mm});
            skLineSegment(sketch, "E5922", {"start": v(-234.5, -19.58) * mm, "end": v(-234.41, -23.18) * mm});
            skLineSegment(sketch, "E5923", {"start": v(-234.41, -23.18) * mm, "end": v(-233.9, -26.7) * mm});
            skLineSegment(sketch, "E5924", {"start": v(-233.9, -26.7) * mm, "end": v(-232.96, -30.16) * mm});
            skLineSegment(sketch, "E5925", {"start": v(-232.96, -30.16) * mm, "end": v(-231.6, -33.58) * mm});
            skLineSegment(sketch, "E5926", {"start": v(-231.6, -33.58) * mm, "end": v(-229.79, -37) * mm});
            skLineSegment(sketch, "E5927", {"start": v(-229.79, -37) * mm, "end": v(-227.52, -40.43) * mm});
            skLineSegment(sketch, "E5928", {"start": v(-217.94, 3.73) * mm, "end": v(-218.16, 4.25) * mm});
            skLineSegment(sketch, "E5929", {"start": v(-218.16, 4.25) * mm, "end": v(-218.35, 4.82) * mm});
            skLineSegment(sketch, "E5930", {"start": v(-218.35, 4.82) * mm, "end": v(-218.55, 5.39) * mm});
            skLineSegment(sketch, "E5931", {"start": v(-218.55, 5.39) * mm, "end": v(-218.8, 5.89) * mm});
            skLineSegment(sketch, "E5932", {"start": v(-218.8, 5.89) * mm, "end": v(-219.14, 6.25) * mm});
            skLineSegment(sketch, "E5933", {"start": v(-219.14, 6.25) * mm, "end": v(-219.6, 6.42) * mm});
            skLineSegment(sketch, "E5934", {"start": v(-219.6, 6.42) * mm, "end": v(-220.24, 6.32) * mm});
            skLineSegment(sketch, "E5935", {"start": v(-220.24, 6.32) * mm, "end": v(-221.09, 5.9) * mm});
            skLineSegment(sketch, "E5936", {"start": v(-221.09, 5.9) * mm, "end": v(-222.5, 4.96) * mm});
            skLineSegment(sketch, "E5937", {"start": v(-222.5, 4.96) * mm, "end": v(-223.84, 3.93) * mm});
            skLineSegment(sketch, "E5938", {"start": v(-223.84, 3.93) * mm, "end": v(-225.1, 2.83) * mm});
            skLineSegment(sketch, "E5939", {"start": v(-225.1, 2.83) * mm, "end": v(-226.28, 1.65) * mm});
            skLineSegment(sketch, "E5940", {"start": v(-226.28, 1.65) * mm, "end": v(-227.35, 0.38) * mm});
            skLineSegment(sketch, "E5941", {"start": v(-227.35, 0.38) * mm, "end": v(-228.32, -0.97) * mm});
            skLineSegment(sketch, "E5942", {"start": v(-228.32, -0.97) * mm, "end": v(-229.19, -2.41) * mm});
            skLineSegment(sketch, "E5943", {"start": v(-229.19, -2.41) * mm, "end": v(-229.93, -3.94) * mm});
            skLineSegment(sketch, "E5944", {"start": v(-229.93, -3.94) * mm, "end": v(-230.28, -5.1) * mm});
            skLineSegment(sketch, "E5945", {"start": v(-230.28, -5.1) * mm, "end": v(-230.35, -6.23) * mm});
            skLineSegment(sketch, "E5946", {"start": v(-230.35, -6.23) * mm, "end": v(-230.18, -7.3) * mm});
            skLineSegment(sketch, "E5947", {"start": v(-230.18, -7.3) * mm, "end": v(-229.8, -8.29) * mm});
            skLineSegment(sketch, "E5948", {"start": v(-229.8, -8.29) * mm, "end": v(-229.26, -9.19) * mm});
            skLineSegment(sketch, "E5949", {"start": v(-229.26, -9.19) * mm, "end": v(-228.58, -9.97) * mm});
            skLineSegment(sketch, "E5950", {"start": v(-228.58, -9.97) * mm, "end": v(-227.8, -10.61) * mm});
            skLineSegment(sketch, "E5951", {"start": v(-227.8, -10.61) * mm, "end": v(-226.98, -11.1) * mm});
            skLineSegment(sketch, "E5952", {"start": v(-226.98, -11.1) * mm, "end": v(-226.16, -11.34) * mm});
            skLineSegment(sketch, "E5953", {"start": v(-226.16, -11.34) * mm, "end": v(-225.57, -11.2) * mm});
            skLineSegment(sketch, "E5954", {"start": v(-225.57, -11.2) * mm, "end": v(-225.13, -10.77) * mm});
            skLineSegment(sketch, "E5955", {"start": v(-225.13, -10.77) * mm, "end": v(-224.82, -10.14) * mm});
            skLineSegment(sketch, "E5956", {"start": v(-224.82, -10.14) * mm, "end": v(-224.58, -9.4) * mm});
            skLineSegment(sketch, "E5957", {"start": v(-224.58, -9.4) * mm, "end": v(-224.36, -8.6) * mm});
            skLineSegment(sketch, "E5958", {"start": v(-224.36, -8.6) * mm, "end": v(-224.11, -7.85) * mm});
            skLineSegment(sketch, "E5959", {"start": v(-224.11, -7.85) * mm, "end": v(-223.8, -7.22) * mm});
            skLineSegment(sketch, "E5960", {"start": v(-223.8, -7.22) * mm, "end": v(-223.32, -6.5) * mm});
            skLineSegment(sketch, "E5961", {"start": v(-223.32, -6.5) * mm, "end": v(-222.88, -5.75) * mm});
            skLineSegment(sketch, "E5962", {"start": v(-222.88, -5.75) * mm, "end": v(-222.45, -5) * mm});
            skLineSegment(sketch, "E5963", {"start": v(-222.45, -5) * mm, "end": v(-222.05, -4.23) * mm});
            skLineSegment(sketch, "E5964", {"start": v(-222.05, -4.23) * mm, "end": v(-221.65, -3.46) * mm});
            skLineSegment(sketch, "E5965", {"start": v(-221.65, -3.46) * mm, "end": v(-221.25, -2.68) * mm});
            skLineSegment(sketch, "E5966", {"start": v(-221.25, -2.68) * mm, "end": v(-220.85, -1.9) * mm});
            skLineSegment(sketch, "E5967", {"start": v(-220.85, -1.9) * mm, "end": v(-220.44, -1.14) * mm});
            skLineSegment(sketch, "E5968", {"start": v(-220.44, -1.14) * mm, "end": v(-220.1, -0.56) * mm});
            skLineSegment(sketch, "E5969", {"start": v(-220.1, -0.56) * mm, "end": v(-219.7, 0) * mm});
            skLineSegment(sketch, "E5970", {"start": v(-219.7, 0) * mm, "end": v(-219.3, 0.55) * mm});
            skLineSegment(sketch, "E5971", {"start": v(-219.3, 0.55) * mm, "end": v(-218.92, 1.11) * mm});
            skLineSegment(sketch, "E5972", {"start": v(-218.92, 1.11) * mm, "end": v(-218.56, 1.7) * mm});
            skLineSegment(sketch, "E5973", {"start": v(-218.56, 1.7) * mm, "end": v(-218.27, 2.32) * mm});
            skLineSegment(sketch, "E5974", {"start": v(-218.27, 2.32) * mm, "end": v(-218.05, 3) * mm});
            skLineSegment(sketch, "E5975", {"start": v(-218.05, 3) * mm, "end": v(-217.94, 3.73) * mm});
            skLineSegment(sketch, "E5976", {"start": v(203.2, -58.35) * mm, "end": v(195.66, -57.62) * mm});
            skLineSegment(sketch, "E5977", {"start": v(195.66, -57.62) * mm, "end": v(188.64, -55.48) * mm});
            skLineSegment(sketch, "E5978", {"start": v(188.64, -55.48) * mm, "end": v(182.3, -52.09) * mm});
            skLineSegment(sketch, "E5979", {"start": v(182.3, -52.09) * mm, "end": v(176.78, -47.58) * mm});
            skLineSegment(sketch, "E5980", {"start": v(176.78, -47.58) * mm, "end": v(172.23, -42.12) * mm});
            skLineSegment(sketch, "E5981", {"start": v(172.23, -42.12) * mm, "end": v(168.8, -35.84) * mm});
            skLineSegment(sketch, "E5982", {"start": v(168.8, -35.84) * mm, "end": v(166.64, -28.89) * mm});
            skLineSegment(sketch, "E5983", {"start": v(166.64, -28.89) * mm, "end": v(165.9, -21.42) * mm});
            skLineSegment(sketch, "E5984", {"start": v(165.9, -21.42) * mm, "end": v(166.66, -14.02) * mm});
            skLineSegment(sketch, "E5985", {"start": v(166.66, -14.02) * mm, "end": v(168.84, -7.13) * mm});
            skLineSegment(sketch, "E5986", {"start": v(168.84, -7.13) * mm, "end": v(172.26, -0.89) * mm});
            skLineSegment(sketch, "E5987", {"start": v(172.26, -0.89) * mm, "end": v(176.8, 4.56) * mm});
            skLineSegment(sketch, "E5988", {"start": v(176.8, 4.56) * mm, "end": v(182.28, 9.05) * mm});
            skLineSegment(sketch, "E5989", {"start": v(182.28, 9.05) * mm, "end": v(188.57, 12.45) * mm});
            skLineSegment(sketch, "E5990", {"start": v(188.57, 12.45) * mm, "end": v(195.5, 14.6) * mm});
            skLineSegment(sketch, "E5991", {"start": v(195.5, 14.6) * mm, "end": v(202.94, 15.34) * mm});
            skLineSegment(sketch, "E5992", {"start": v(202.94, 15.34) * mm, "end": v(210.45, 14.57) * mm});
            skLineSegment(sketch, "E5993", {"start": v(210.45, 14.57) * mm, "end": v(217.45, 12.39) * mm});
            skLineSegment(sketch, "E5994", {"start": v(217.45, 12.39) * mm, "end": v(223.78, 8.94) * mm});
            skLineSegment(sketch, "E5995", {"start": v(223.78, 8.94) * mm, "end": v(229.29, 4.38) * mm});
            skLineSegment(sketch, "E5996", {"start": v(229.29, 4.38) * mm, "end": v(233.82, -1.14) * mm});
            skLineSegment(sketch, "E5997", {"start": v(233.82, -1.14) * mm, "end": v(237.23, -7.46) * mm});
            skLineSegment(sketch, "E5998", {"start": v(237.23, -7.46) * mm, "end": v(239.35, -14.44) * mm});
            skLineSegment(sketch, "E5999", {"start": v(239.35, -14.44) * mm, "end": v(240.04, -21.9) * mm});
            skLineSegment(sketch, "E6000", {"start": v(240.04, -21.9) * mm, "end": v(239.22, -29.24) * mm});
            skLineSegment(sketch, "E6001", {"start": v(239.22, -29.24) * mm, "end": v(237.03, -36.07) * mm});
            skLineSegment(sketch, "E6002", {"start": v(237.03, -36.07) * mm, "end": v(233.6, -42.25) * mm});
            skLineSegment(sketch, "E6003", {"start": v(233.6, -42.25) * mm, "end": v(229.1, -47.65) * mm});
            skLineSegment(sketch, "E6004", {"start": v(229.1, -47.65) * mm, "end": v(223.66, -52.1) * mm});
            skLineSegment(sketch, "E6005", {"start": v(223.66, -52.1) * mm, "end": v(217.43, -55.46) * mm});
            skLineSegment(sketch, "E6006", {"start": v(217.43, -55.46) * mm, "end": v(210.57, -57.6) * mm});
            skLineSegment(sketch, "E6007", {"start": v(210.57, -57.6) * mm, "end": v(203.2, -58.35) * mm});
            skLineSegment(sketch, "E6008", {"start": v(224.16, -29.34) * mm, "end": v(224.2, -26.68) * mm});
            skLineSegment(sketch, "E6009", {"start": v(224.2, -26.68) * mm, "end": v(224.08, -24.06) * mm});
            skLineSegment(sketch, "E6010", {"start": v(224.08, -24.06) * mm, "end": v(223.8, -21.47) * mm});
            skLineSegment(sketch, "E6011", {"start": v(223.8, -21.47) * mm, "end": v(223.38, -18.9) * mm});
            skLineSegment(sketch, "E6012", {"start": v(223.38, -18.9) * mm, "end": v(222.8, -16.37) * mm});
            skLineSegment(sketch, "E6013", {"start": v(222.8, -16.37) * mm, "end": v(222.07, -13.87) * mm});
            skLineSegment(sketch, "E6014", {"start": v(222.07, -13.87) * mm, "end": v(221.19, -11.4) * mm});
            skLineSegment(sketch, "E6015", {"start": v(221.19, -11.4) * mm, "end": v(220.15, -8.95) * mm});
            skLineSegment(sketch, "E6016", {"start": v(220.15, -8.95) * mm, "end": v(218.79, -6.03) * mm});
            skLineSegment(sketch, "E6017", {"start": v(218.79, -6.03) * mm, "end": v(217.65, -3.87) * mm});
            skLineSegment(sketch, "E6018", {"start": v(217.65, -3.87) * mm, "end": v(216.58, -2.39) * mm});
            skLineSegment(sketch, "E6019", {"start": v(216.58, -2.39) * mm, "end": v(215.43, -1.51) * mm});
            skLineSegment(sketch, "E6020", {"start": v(215.43, -1.51) * mm, "end": v(214.05, -1.17) * mm});
            skLineSegment(sketch, "E6021", {"start": v(214.05, -1.17) * mm, "end": v(212.3, -1.3) * mm});
            skLineSegment(sketch, "E6022", {"start": v(212.3, -1.3) * mm, "end": v(210, -1.83) * mm});
            skLineSegment(sketch, "E6023", {"start": v(210, -1.83) * mm, "end": v(207, -2.68) * mm});
            skLineSegment(sketch, "E6024", {"start": v(207, -2.68) * mm, "end": v(206.77, -2.75) * mm});
            skLineSegment(sketch, "E6025", {"start": v(206.77, -2.75) * mm, "end": v(206.53, -2.83) * mm});
            skLineSegment(sketch, "E6026", {"start": v(206.53, -2.83) * mm, "end": v(206.3, -2.91) * mm});
            skLineSegment(sketch, "E6027", {"start": v(206.3, -2.91) * mm, "end": v(206.05, -2.99) * mm});
            skLineSegment(sketch, "E6028", {"start": v(206.05, -2.99) * mm, "end": v(205.81, -3.06) * mm});
            skLineSegment(sketch, "E6029", {"start": v(205.81, -3.06) * mm, "end": v(205.57, -3.12) * mm});
            skLineSegment(sketch, "E6030", {"start": v(205.57, -3.12) * mm, "end": v(205.33, -3.17) * mm});
            skLineSegment(sketch, "E6031", {"start": v(205.33, -3.17) * mm, "end": v(205.09, -3.2) * mm});
            skLineSegment(sketch, "E6032", {"start": v(205.09, -3.2) * mm, "end": v(203.54, -3.41) * mm});
            skLineSegment(sketch, "E6033", {"start": v(203.54, -3.41) * mm, "end": v(202.29, -3.78) * mm});
            skLineSegment(sketch, "E6034", {"start": v(202.29, -3.78) * mm, "end": v(201.35, -4.32) * mm});
            skLineSegment(sketch, "E6035", {"start": v(201.35, -4.32) * mm, "end": v(200.73, -5.03) * mm});
            skLineSegment(sketch, "E6036", {"start": v(200.73, -5.03) * mm, "end": v(200.43, -5.91) * mm});
            skLineSegment(sketch, "E6037", {"start": v(200.43, -5.91) * mm, "end": v(200.47, -6.97) * mm});
            skLineSegment(sketch, "E6038", {"start": v(200.47, -6.97) * mm, "end": v(200.86, -8.23) * mm});
            skLineSegment(sketch, "E6039", {"start": v(200.86, -8.23) * mm, "end": v(201.6, -9.67) * mm});
            skLineSegment(sketch, "E6040", {"start": v(201.6, -9.67) * mm, "end": v(201.68, -9.83) * mm});
            skLineSegment(sketch, "E6041", {"start": v(201.68, -9.83) * mm, "end": v(201.76, -10) * mm});
            skLineSegment(sketch, "E6042", {"start": v(201.76, -10) * mm, "end": v(201.84, -10.17) * mm});
            skLineSegment(sketch, "E6043", {"start": v(201.84, -10.17) * mm, "end": v(201.9, -10.35) * mm});
            skLineSegment(sketch, "E6044", {"start": v(201.9, -10.35) * mm, "end": v(201.97, -10.52) * mm});
            skLineSegment(sketch, "E6045", {"start": v(201.97, -10.52) * mm, "end": v(202.04, -10.7) * mm});
            skLineSegment(sketch, "E6046", {"start": v(202.04, -10.7) * mm, "end": v(202.1, -10.88) * mm});
            skLineSegment(sketch, "E6047", {"start": v(202.1, -10.88) * mm, "end": v(202.17, -11.05) * mm});
            skLineSegment(sketch, "E6048", {"start": v(202.17, -11.05) * mm, "end": v(203.69, -15.61) * mm});
            skLineSegment(sketch, "E6049", {"start": v(203.69, -15.61) * mm, "end": v(204.77, -20.18) * mm});
            skLineSegment(sketch, "E6050", {"start": v(204.77, -20.18) * mm, "end": v(205.42, -24.76) * mm});
            skLineSegment(sketch, "E6051", {"start": v(205.42, -24.76) * mm, "end": v(205.67, -29.35) * mm});
            skLineSegment(sketch, "E6052", {"start": v(205.67, -29.35) * mm, "end": v(205.54, -33.96) * mm});
            skLineSegment(sketch, "E6053", {"start": v(205.54, -33.96) * mm, "end": v(205.04, -38.57) * mm});
            skLineSegment(sketch, "E6054", {"start": v(205.04, -38.57) * mm, "end": v(204.21, -43.19) * mm});
            skLineSegment(sketch, "E6055", {"start": v(204.21, -43.19) * mm, "end": v(203.06, -47.82) * mm});
            skLineSegment(sketch, "E6056", {"start": v(203.06, -47.82) * mm, "end": v(202.83, -48.44) * mm});
            skLineSegment(sketch, "E6057", {"start": v(202.83, -48.44) * mm, "end": v(202.53, -49.15) * mm});
            skLineSegment(sketch, "E6058", {"start": v(202.53, -49.15) * mm, "end": v(202.26, -49.87) * mm});
            skLineSegment(sketch, "E6059", {"start": v(202.26, -49.87) * mm, "end": v(202.1, -50.57) * mm});
            skLineSegment(sketch, "E6060", {"start": v(202.1, -50.57) * mm, "end": v(202.14, -51.19) * mm});
            skLineSegment(sketch, "E6061", {"start": v(202.14, -51.19) * mm, "end": v(202.5, -51.66) * mm});
            skLineSegment(sketch, "E6062", {"start": v(202.5, -51.66) * mm, "end": v(203.23, -51.94) * mm});
            skLineSegment(sketch, "E6063", {"start": v(203.23, -51.94) * mm, "end": v(204.46, -51.96) * mm});
            skLineSegment(sketch, "E6064", {"start": v(204.46, -51.96) * mm, "end": v(208.43, -51.57) * mm});
            skLineSegment(sketch, "E6065", {"start": v(208.43, -51.57) * mm, "end": v(212.1, -50.96) * mm});
            skLineSegment(sketch, "E6066", {"start": v(212.1, -50.96) * mm, "end": v(215.38, -50) * mm});
            skLineSegment(sketch, "E6067", {"start": v(215.38, -50) * mm, "end": v(218.22, -48.6) * mm});
            skLineSegment(sketch, "E6068", {"start": v(218.22, -48.6) * mm, "end": v(220.56, -46.6) * mm});
            skLineSegment(sketch, "E6069", {"start": v(220.56, -46.6) * mm, "end": v(222.33, -43.88) * mm});
            skLineSegment(sketch, "E6070", {"start": v(222.33, -43.88) * mm, "end": v(223.46, -40.34) * mm});
            skLineSegment(sketch, "E6071", {"start": v(223.46, -40.34) * mm, "end": v(223.88, -35.83) * mm});
            skLineSegment(sketch, "E6072", {"start": v(223.88, -35.83) * mm, "end": v(223.9, -35.02) * mm});
            skLineSegment(sketch, "E6073", {"start": v(223.9, -35.02) * mm, "end": v(223.92, -34.2) * mm});
            skLineSegment(sketch, "E6074", {"start": v(223.92, -34.2) * mm, "end": v(223.95, -33.4) * mm});
            skLineSegment(sketch, "E6075", {"start": v(223.95, -33.4) * mm, "end": v(223.99, -32.58) * mm});
            skLineSegment(sketch, "E6076", {"start": v(223.99, -32.58) * mm, "end": v(224.03, -31.77) * mm});
            skLineSegment(sketch, "E6077", {"start": v(224.03, -31.77) * mm, "end": v(224.07, -30.96) * mm});
            skLineSegment(sketch, "E6078", {"start": v(224.07, -30.96) * mm, "end": v(224.12, -30.15) * mm});
            skLineSegment(sketch, "E6079", {"start": v(224.12, -30.15) * mm, "end": v(224.16, -29.34) * mm});
            skLineSegment(sketch, "E6080", {"start": v(171.87, -16.2) * mm, "end": v(171.22, -21.6) * mm});
            skLineSegment(sketch, "E6081", {"start": v(171.22, -21.6) * mm, "end": v(171.77, -27.1) * mm});
            skLineSegment(sketch, "E6082", {"start": v(171.77, -27.1) * mm, "end": v(173.42, -32.51) * mm});
            skLineSegment(sketch, "E6083", {"start": v(173.42, -32.51) * mm, "end": v(176.01, -37.6) * mm});
            skLineSegment(sketch, "E6084", {"start": v(176.01, -37.6) * mm, "end": v(179.43, -42.2) * mm});
            skLineSegment(sketch, "E6085", {"start": v(179.43, -42.2) * mm, "end": v(183.53, -46.05) * mm});
            skLineSegment(sketch, "E6086", {"start": v(183.53, -46.05) * mm, "end": v(188.2, -48.98) * mm});
            skLineSegment(sketch, "E6087", {"start": v(188.2, -48.98) * mm, "end": v(193.3, -50.77) * mm});
            skLineSegment(sketch, "E6088", {"start": v(193.3, -50.77) * mm, "end": v(194.17, -50.91) * mm});
            skLineSegment(sketch, "E6089", {"start": v(194.17, -50.91) * mm, "end": v(194.93, -50.93) * mm});
            skLineSegment(sketch, "E6090", {"start": v(194.93, -50.93) * mm, "end": v(195.6, -50.82) * mm});
            skLineSegment(sketch, "E6091", {"start": v(195.6, -50.82) * mm, "end": v(196.18, -50.59) * mm});
            skLineSegment(sketch, "E6092", {"start": v(196.18, -50.59) * mm, "end": v(196.69, -50.22) * mm});
            skLineSegment(sketch, "E6093", {"start": v(196.69, -50.22) * mm, "end": v(197.13, -49.73) * mm});
            skLineSegment(sketch, "E6094", {"start": v(197.13, -49.73) * mm, "end": v(197.5, -49.1) * mm});
            skLineSegment(sketch, "E6095", {"start": v(197.5, -49.1) * mm, "end": v(197.85, -48.33) * mm});
            skLineSegment(sketch, "E6096", {"start": v(197.85, -48.33) * mm, "end": v(198.35, -46.91) * mm});
            skLineSegment(sketch, "E6097", {"start": v(198.35, -46.91) * mm, "end": v(198.78, -45.48) * mm});
            skLineSegment(sketch, "E6098", {"start": v(198.78, -45.48) * mm, "end": v(199.15, -44.04) * mm});
            skLineSegment(sketch, "E6099", {"start": v(199.15, -44.04) * mm, "end": v(199.48, -42.59) * mm});
            skLineSegment(sketch, "E6100", {"start": v(199.48, -42.59) * mm, "end": v(199.78, -41.13) * mm});
            skLineSegment(sketch, "E6101", {"start": v(199.78, -41.13) * mm, "end": v(200.06, -39.66) * mm});
            skLineSegment(sketch, "E6102", {"start": v(200.06, -39.66) * mm, "end": v(200.33, -38.2) * mm});
            skLineSegment(sketch, "E6103", {"start": v(200.33, -38.2) * mm, "end": v(200.6, -36.73) * mm});
            skLineSegment(sketch, "E6104", {"start": v(200.6, -36.73) * mm, "end": v(200.77, -35.54) * mm});
            skLineSegment(sketch, "E6105", {"start": v(200.77, -35.54) * mm, "end": v(200.77, -34.49) * mm});
            skLineSegment(sketch, "E6106", {"start": v(200.77, -34.49) * mm, "end": v(200.6, -33.58) * mm});
            skLineSegment(sketch, "E6107", {"start": v(200.6, -33.58) * mm, "end": v(200.21, -32.82) * mm});
            skLineSegment(sketch, "E6108", {"start": v(200.21, -32.82) * mm, "end": v(199.63, -32.2) * mm});
            skLineSegment(sketch, "E6109", {"start": v(199.63, -32.2) * mm, "end": v(198.8, -31.72) * mm});
            skLineSegment(sketch, "E6110", {"start": v(198.8, -31.72) * mm, "end": v(197.75, -31.38) * mm});
            skLineSegment(sketch, "E6111", {"start": v(197.75, -31.38) * mm, "end": v(196.42, -31.17) * mm});
            skLineSegment(sketch, "E6112", {"start": v(196.42, -31.17) * mm, "end": v(192.99, -30.65) * mm});
            skLineSegment(sketch, "E6113", {"start": v(192.99, -30.65) * mm, "end": v(189.73, -29.81) * mm});
            skLineSegment(sketch, "E6114", {"start": v(189.73, -29.81) * mm, "end": v(186.64, -28.65) * mm});
            skLineSegment(sketch, "E6115", {"start": v(186.64, -28.65) * mm, "end": v(183.74, -27.16) * mm});
            skLineSegment(sketch, "E6116", {"start": v(183.74, -27.16) * mm, "end": v(181.02, -25.36) * mm});
            skLineSegment(sketch, "E6117", {"start": v(181.02, -25.36) * mm, "end": v(178.48, -23.24) * mm});
            skLineSegment(sketch, "E6118", {"start": v(178.48, -23.24) * mm, "end": v(176.13, -20.8) * mm});
            skLineSegment(sketch, "E6119", {"start": v(176.13, -20.8) * mm, "end": v(173.96, -18.05) * mm});
            skLineSegment(sketch, "E6120", {"start": v(173.96, -18.05) * mm, "end": v(173.77, -17.75) * mm});
            skLineSegment(sketch, "E6121", {"start": v(173.77, -17.75) * mm, "end": v(173.58, -17.44) * mm});
            skLineSegment(sketch, "E6122", {"start": v(173.58, -17.44) * mm, "end": v(173.38, -17.13) * mm});
            skLineSegment(sketch, "E6123", {"start": v(173.38, -17.13) * mm, "end": v(173.17, -16.85) * mm});
            skLineSegment(sketch, "E6124", {"start": v(173.17, -16.85) * mm, "end": v(172.93, -16.6) * mm});
            skLineSegment(sketch, "E6125", {"start": v(172.93, -16.6) * mm, "end": v(172.64, -16.4) * mm});
            skLineSegment(sketch, "E6126", {"start": v(172.64, -16.4) * mm, "end": v(172.29, -16.26) * mm});
            skLineSegment(sketch, "E6127", {"start": v(172.29, -16.26) * mm, "end": v(171.87, -16.2) * mm});
            skLineSegment(sketch, "E6128", {"start": v(196.84, -26.58) * mm, "end": v(197.95, -26.56) * mm});
            skLineSegment(sketch, "E6129", {"start": v(197.95, -26.56) * mm, "end": v(198.85, -26.44) * mm});
            skLineSegment(sketch, "E6130", {"start": v(198.85, -26.44) * mm, "end": v(199.54, -26.18) * mm});
            skLineSegment(sketch, "E6131", {"start": v(199.54, -26.18) * mm, "end": v(200.04, -25.77) * mm});
            skLineSegment(sketch, "E6132", {"start": v(200.04, -25.77) * mm, "end": v(200.37, -25.2) * mm});
            skLineSegment(sketch, "E6133", {"start": v(200.37, -25.2) * mm, "end": v(200.52, -24.46) * mm});
            skLineSegment(sketch, "E6134", {"start": v(200.52, -24.46) * mm, "end": v(200.52, -23.51) * mm});
            skLineSegment(sketch, "E6135", {"start": v(200.52, -23.51) * mm, "end": v(200.38, -22.36) * mm});
            skLineSegment(sketch, "E6136", {"start": v(200.38, -22.36) * mm, "end": v(199.98, -20.27) * mm});
            skLineSegment(sketch, "E6137", {"start": v(199.98, -20.27) * mm, "end": v(199.49, -18.21) * mm});
            skLineSegment(sketch, "E6138", {"start": v(199.49, -18.21) * mm, "end": v(198.91, -16.18) * mm});
            skLineSegment(sketch, "E6139", {"start": v(198.91, -16.18) * mm, "end": v(198.26, -14.18) * mm});
            skLineSegment(sketch, "E6140", {"start": v(198.26, -14.18) * mm, "end": v(197.53, -12.2) * mm});
            skLineSegment(sketch, "E6141", {"start": v(197.53, -12.2) * mm, "end": v(196.74, -10.24) * mm});
            skLineSegment(sketch, "E6142", {"start": v(196.74, -10.24) * mm, "end": v(195.88, -8.3) * mm});
            skLineSegment(sketch, "E6143", {"start": v(195.88, -8.3) * mm, "end": v(194.97, -6.38) * mm});
            skLineSegment(sketch, "E6144", {"start": v(194.97, -6.38) * mm, "end": v(194.74, -5.93) * mm});
            skLineSegment(sketch, "E6145", {"start": v(194.74, -5.93) * mm, "end": v(194.48, -5.5) * mm});
            skLineSegment(sketch, "E6146", {"start": v(194.48, -5.5) * mm, "end": v(194.2, -5.08) * mm});
            skLineSegment(sketch, "E6147", {"start": v(194.2, -5.08) * mm, "end": v(193.9, -4.7) * mm});
            skLineSegment(sketch, "E6148", {"start": v(193.9, -4.7) * mm, "end": v(193.57, -4.34) * mm});
            skLineSegment(sketch, "E6149", {"start": v(193.57, -4.34) * mm, "end": v(193.2, -4.02) * mm});
            skLineSegment(sketch, "E6150", {"start": v(193.2, -4.02) * mm, "end": v(192.78, -3.75) * mm});
            skLineSegment(sketch, "E6151", {"start": v(192.78, -3.75) * mm, "end": v(192.32, -3.52) * mm});
            skLineSegment(sketch, "E6152", {"start": v(192.32, -3.52) * mm, "end": v(191.05, -2.98) * mm});
            skLineSegment(sketch, "E6153", {"start": v(191.05, -2.98) * mm, "end": v(189.8, -2.4) * mm});
            skLineSegment(sketch, "E6154", {"start": v(189.8, -2.4) * mm, "end": v(188.6, -1.79) * mm});
            skLineSegment(sketch, "E6155", {"start": v(188.6, -1.79) * mm, "end": v(187.44, -1.1) * mm});
            skLineSegment(sketch, "E6156", {"start": v(187.44, -1.1) * mm, "end": v(186.33, -0.32) * mm});
            skLineSegment(sketch, "E6157", {"start": v(186.33, -0.32) * mm, "end": v(185.3, 0.55) * mm});
            skLineSegment(sketch, "E6158", {"start": v(185.3, 0.55) * mm, "end": v(184.34, 1.53) * mm});
            skLineSegment(sketch, "E6159", {"start": v(184.34, 1.53) * mm, "end": v(183.47, 2.65) * mm});
            skLineSegment(sketch, "E6160", {"start": v(183.47, 2.65) * mm, "end": v(183.27, 2.9) * mm});
            skLineSegment(sketch, "E6161", {"start": v(183.27, 2.9) * mm, "end": v(183.06, 3.1) * mm});
            skLineSegment(sketch, "E6162", {"start": v(183.06, 3.1) * mm, "end": v(182.83, 3.26) * mm});
            skLineSegment(sketch, "E6163", {"start": v(182.83, 3.26) * mm, "end": v(182.58, 3.37) * mm});
            skLineSegment(sketch, "E6164", {"start": v(182.58, 3.37) * mm, "end": v(182.3, 3.43) * mm});
            skLineSegment(sketch, "E6165", {"start": v(182.3, 3.43) * mm, "end": v(182, 3.44) * mm});
            skLineSegment(sketch, "E6166", {"start": v(182, 3.44) * mm, "end": v(181.68, 3.39) * mm});
            skLineSegment(sketch, "E6167", {"start": v(181.68, 3.39) * mm, "end": v(181.33, 3.28) * mm});
            skLineSegment(sketch, "E6168", {"start": v(181.33, 3.28) * mm, "end": v(180.11, 2.54) * mm});
            skLineSegment(sketch, "E6169", {"start": v(180.11, 2.54) * mm, "end": v(178.83, 1.27) * mm});
            skLineSegment(sketch, "E6170", {"start": v(178.83, 1.27) * mm, "end": v(177.58, -0.37) * mm});
            skLineSegment(sketch, "E6171", {"start": v(177.58, -0.37) * mm, "end": v(176.42, -2.24) * mm});
            skLineSegment(sketch, "E6172", {"start": v(176.42, -2.24) * mm, "end": v(175.46, -4.2) * mm});
            skLineSegment(sketch, "E6173", {"start": v(175.46, -4.2) * mm, "end": v(174.75, -6.1) * mm});
            skLineSegment(sketch, "E6174", {"start": v(174.75, -6.1) * mm, "end": v(174.4, -7.8) * mm});
            skLineSegment(sketch, "E6175", {"start": v(174.4, -7.8) * mm, "end": v(174.47, -9.15) * mm});
            skLineSegment(sketch, "E6176", {"start": v(174.47, -9.15) * mm, "end": v(175.76, -12.36) * mm});
            skLineSegment(sketch, "E6177", {"start": v(175.76, -12.36) * mm, "end": v(177.73, -15.47) * mm});
            skLineSegment(sketch, "E6178", {"start": v(177.73, -15.47) * mm, "end": v(180.24, -18.38) * mm});
            skLineSegment(sketch, "E6179", {"start": v(180.24, -18.38) * mm, "end": v(183.19, -21) * mm});
            skLineSegment(sketch, "E6180", {"start": v(183.19, -21) * mm, "end": v(186.45, -23.21) * mm});
            skLineSegment(sketch, "E6181", {"start": v(186.45, -23.21) * mm, "end": v(189.89, -24.95) * mm});
            skLineSegment(sketch, "E6182", {"start": v(189.89, -24.95) * mm, "end": v(193.4, -26.1) * mm});
            skLineSegment(sketch, "E6183", {"start": v(193.4, -26.1) * mm, "end": v(196.84, -26.58) * mm});
            skLineSegment(sketch, "E6184", {"start": v(198.76, 0.47) * mm, "end": v(200.37, 0.72) * mm});
            skLineSegment(sketch, "E6185", {"start": v(200.37, 0.72) * mm, "end": v(202, 1) * mm});
            skLineSegment(sketch, "E6186", {"start": v(202, 1) * mm, "end": v(203.68, 1.33) * mm});
            skLineSegment(sketch, "E6187", {"start": v(203.68, 1.33) * mm, "end": v(205.36, 1.73) * mm});
            skLineSegment(sketch, "E6188", {"start": v(205.36, 1.73) * mm, "end": v(207.05, 2.21) * mm});
            skLineSegment(sketch, "E6189", {"start": v(207.05, 2.21) * mm, "end": v(208.73, 2.8) * mm});
            skLineSegment(sketch, "E6190", {"start": v(208.73, 2.8) * mm, "end": v(210.38, 3.52) * mm});
            skLineSegment(sketch, "E6191", {"start": v(210.38, 3.52) * mm, "end": v(212, 4.38) * mm});
            skLineSegment(sketch, "E6192", {"start": v(212, 4.38) * mm, "end": v(212.48, 4.67) * mm});
            skLineSegment(sketch, "E6193", {"start": v(212.48, 4.67) * mm, "end": v(212.95, 4.98) * mm});
            skLineSegment(sketch, "E6194", {"start": v(212.95, 4.98) * mm, "end": v(213.4, 5.32) * mm});
            skLineSegment(sketch, "E6195", {"start": v(213.4, 5.32) * mm, "end": v(213.78, 5.7) * mm});
            skLineSegment(sketch, "E6196", {"start": v(213.78, 5.7) * mm, "end": v(214.1, 6.13) * mm});
            skLineSegment(sketch, "E6197", {"start": v(214.1, 6.13) * mm, "end": v(214.32, 6.62) * mm});
            skLineSegment(sketch, "E6198", {"start": v(214.32, 6.62) * mm, "end": v(214.42, 7.18) * mm});
            skLineSegment(sketch, "E6199", {"start": v(214.42, 7.18) * mm, "end": v(214.38, 7.81) * mm});
            skLineSegment(sketch, "E6200", {"start": v(214.38, 7.81) * mm, "end": v(214.23, 8.4) * mm});
            skLineSegment(sketch, "E6201", {"start": v(214.23, 8.4) * mm, "end": v(214, 8.9) * mm});
            skLineSegment(sketch, "E6202", {"start": v(214, 8.9) * mm, "end": v(213.68, 9.33) * mm});
            skLineSegment(sketch, "E6203", {"start": v(213.68, 9.33) * mm, "end": v(213.3, 9.7) * mm});
            skLineSegment(sketch, "E6204", {"start": v(213.3, 9.7) * mm, "end": v(212.86, 10.02) * mm});
            skLineSegment(sketch, "E6205", {"start": v(212.86, 10.02) * mm, "end": v(212.37, 10.28) * mm});
            skLineSegment(sketch, "E6206", {"start": v(212.37, 10.28) * mm, "end": v(211.84, 10.5) * mm});
            skLineSegment(sketch, "E6207", {"start": v(211.84, 10.5) * mm, "end": v(211.28, 10.68) * mm});
            skLineSegment(sketch, "E6208", {"start": v(211.28, 10.68) * mm, "end": v(209.43, 11.15) * mm});
            skLineSegment(sketch, "E6209", {"start": v(209.43, 11.15) * mm, "end": v(207.59, 11.5) * mm});
            skLineSegment(sketch, "E6210", {"start": v(207.59, 11.5) * mm, "end": v(205.74, 11.73) * mm});
            skLineSegment(sketch, "E6211", {"start": v(205.74, 11.73) * mm, "end": v(203.88, 11.85) * mm});
            skLineSegment(sketch, "E6212", {"start": v(203.88, 11.85) * mm, "end": v(202.03, 11.84) * mm});
            skLineSegment(sketch, "E6213", {"start": v(202.03, 11.84) * mm, "end": v(200.18, 11.7) * mm});
            skLineSegment(sketch, "E6214", {"start": v(200.18, 11.7) * mm, "end": v(198.33, 11.45) * mm});
            skLineSegment(sketch, "E6215", {"start": v(198.33, 11.45) * mm, "end": v(196.49, 11.06) * mm});
            skLineSegment(sketch, "E6216", {"start": v(196.49, 11.06) * mm, "end": v(195.19, 10.8) * mm});
            skLineSegment(sketch, "E6217", {"start": v(195.19, 10.8) * mm, "end": v(193.84, 10.55) * mm});
            skLineSegment(sketch, "E6218", {"start": v(193.84, 10.55) * mm, "end": v(192.5, 10.26) * mm});
            skLineSegment(sketch, "E6219", {"start": v(192.5, 10.26) * mm, "end": v(191.23, 9.86) * mm});
            skLineSegment(sketch, "E6220", {"start": v(191.23, 9.86) * mm, "end": v(190.07, 9.28) * mm});
            skLineSegment(sketch, "E6221", {"start": v(190.07, 9.28) * mm, "end": v(189.1, 8.45) * mm});
            skLineSegment(sketch, "E6222", {"start": v(189.1, 8.45) * mm, "end": v(188.35, 7.3) * mm});
            skLineSegment(sketch, "E6223", {"start": v(188.35, 7.3) * mm, "end": v(187.89, 5.75) * mm});
            skLineSegment(sketch, "E6224", {"start": v(187.89, 5.75) * mm, "end": v(188, 4.8) * mm});
            skLineSegment(sketch, "E6225", {"start": v(188, 4.8) * mm, "end": v(188.63, 3.85) * mm});
            skLineSegment(sketch, "E6226", {"start": v(188.63, 3.85) * mm, "end": v(189.69, 2.96) * mm});
            skLineSegment(sketch, "E6227", {"start": v(189.69, 2.96) * mm, "end": v(191.1, 2.15) * mm});
            skLineSegment(sketch, "E6228", {"start": v(191.1, 2.15) * mm, "end": v(192.78, 1.45) * mm});
            skLineSegment(sketch, "E6229", {"start": v(192.78, 1.45) * mm, "end": v(194.67, 0.92) * mm});
            skLineSegment(sketch, "E6230", {"start": v(194.67, 0.92) * mm, "end": v(196.7, 0.58) * mm});
            skLineSegment(sketch, "E6231", {"start": v(196.7, 0.58) * mm, "end": v(198.76, 0.47) * mm});
            skLineSegment(sketch, "E6232", {"start": v(233.86, -11.82) * mm, "end": v(232.87, -12.98) * mm});
            skLineSegment(sketch, "E6233", {"start": v(232.87, -12.98) * mm, "end": v(231.9, -14.05) * mm});
            skLineSegment(sketch, "E6234", {"start": v(231.9, -14.05) * mm, "end": v(230.99, -15.06) * mm});
            skLineSegment(sketch, "E6235", {"start": v(230.99, -15.06) * mm, "end": v(230.18, -16.04) * mm});
            skLineSegment(sketch, "E6236", {"start": v(230.18, -16.04) * mm, "end": v(229.5, -17) * mm});
            skLineSegment(sketch, "E6237", {"start": v(229.5, -17) * mm, "end": v(229, -18) * mm});
            skLineSegment(sketch, "E6238", {"start": v(229, -18) * mm, "end": v(228.72, -19.06) * mm});
            skLineSegment(sketch, "E6239", {"start": v(228.72, -19.06) * mm, "end": v(228.69, -20.2) * mm});
            skLineSegment(sketch, "E6240", {"start": v(228.69, -20.2) * mm, "end": v(228.87, -22.4) * mm});
            skLineSegment(sketch, "E6241", {"start": v(228.87, -22.4) * mm, "end": v(229, -24.61) * mm});
            skLineSegment(sketch, "E6242", {"start": v(229, -24.61) * mm, "end": v(229.1, -26.82) * mm});
            skLineSegment(sketch, "E6243", {"start": v(229.1, -26.82) * mm, "end": v(229.15, -29.03) * mm});
            skLineSegment(sketch, "E6244", {"start": v(229.15, -29.03) * mm, "end": v(229.16, -31.24) * mm});
            skLineSegment(sketch, "E6245", {"start": v(229.16, -31.24) * mm, "end": v(229.14, -33.45) * mm});
            skLineSegment(sketch, "E6246", {"start": v(229.14, -33.45) * mm, "end": v(229.08, -35.67) * mm});
            skLineSegment(sketch, "E6247", {"start": v(229.08, -35.67) * mm, "end": v(229, -37.9) * mm});
            skLineSegment(sketch, "E6248", {"start": v(229, -37.9) * mm, "end": v(230.91, -35.04) * mm});
            skLineSegment(sketch, "E6249", {"start": v(230.91, -35.04) * mm, "end": v(232.44, -32.1) * mm});
            skLineSegment(sketch, "E6250", {"start": v(232.44, -32.1) * mm, "end": v(233.6, -29.05) * mm});
            skLineSegment(sketch, "E6251", {"start": v(233.6, -29.05) * mm, "end": v(234.37, -25.89) * mm});
            skLineSegment(sketch, "E6252", {"start": v(234.37, -25.89) * mm, "end": v(234.78, -22.6) * mm});
            skLineSegment(sketch, "E6253", {"start": v(234.78, -22.6) * mm, "end": v(234.83, -19.17) * mm});
            skLineSegment(sketch, "E6254", {"start": v(234.83, -19.17) * mm, "end": v(234.52, -15.58) * mm});
            skLineSegment(sketch, "E6255", {"start": v(234.52, -15.58) * mm, "end": v(233.86, -11.82) * mm});
            skLineSegment(sketch, "E6256", {"start": v(231.17, -5.47) * mm, "end": v(230.5, -4.01) * mm});
            skLineSegment(sketch, "E6257", {"start": v(230.5, -4.01) * mm, "end": v(229.73, -2.61) * mm});
            skLineSegment(sketch, "E6258", {"start": v(229.73, -2.61) * mm, "end": v(228.86, -1.26) * mm});
            skLineSegment(sketch, "E6259", {"start": v(228.86, -1.26) * mm, "end": v(227.9, 0.03) * mm});
            skLineSegment(sketch, "E6260", {"start": v(227.9, 0.03) * mm, "end": v(226.84, 1.27) * mm});
            skLineSegment(sketch, "E6261", {"start": v(226.84, 1.27) * mm, "end": v(225.7, 2.46) * mm});
            skLineSegment(sketch, "E6262", {"start": v(225.7, 2.46) * mm, "end": v(224.49, 3.58) * mm});
            skLineSegment(sketch, "E6263", {"start": v(224.49, 3.58) * mm, "end": v(223.2, 4.66) * mm});
            skLineSegment(sketch, "E6264", {"start": v(223.2, 4.66) * mm, "end": v(222.82, 4.96) * mm});
            skLineSegment(sketch, "E6265", {"start": v(222.82, 4.96) * mm, "end": v(222.42, 5.28) * mm});
            skLineSegment(sketch, "E6266", {"start": v(222.42, 5.28) * mm, "end": v(222, 5.56) * mm});
            skLineSegment(sketch, "E6267", {"start": v(222, 5.56) * mm, "end": v(221.58, 5.8) * mm});
            skLineSegment(sketch, "E6268", {"start": v(221.58, 5.8) * mm, "end": v(221.14, 5.93) * mm});
            skLineSegment(sketch, "E6269", {"start": v(221.14, 5.93) * mm, "end": v(220.68, 5.93) * mm});
            skLineSegment(sketch, "E6270", {"start": v(220.68, 5.93) * mm, "end": v(220.21, 5.78) * mm});
            skLineSegment(sketch, "E6271", {"start": v(220.21, 5.78) * mm, "end": v(219.73, 5.43) * mm});
            skLineSegment(sketch, "E6272", {"start": v(219.73, 5.43) * mm, "end": v(219.33, 4.99) * mm});
            skLineSegment(sketch, "E6273", {"start": v(219.33, 4.99) * mm, "end": v(219.06, 4.51) * mm});
            skLineSegment(sketch, "E6274", {"start": v(219.06, 4.51) * mm, "end": v(218.91, 4.02) * mm});
            skLineSegment(sketch, "E6275", {"start": v(218.91, 4.02) * mm, "end": v(218.87, 3.5) * mm});
            skLineSegment(sketch, "E6276", {"start": v(218.87, 3.5) * mm, "end": v(218.92, 2.98) * mm});
            skLineSegment(sketch, "E6277", {"start": v(218.92, 2.98) * mm, "end": v(219.06, 2.45) * mm});
            skLineSegment(sketch, "E6278", {"start": v(219.06, 2.45) * mm, "end": v(219.29, 1.91) * mm});
            skLineSegment(sketch, "E6279", {"start": v(219.29, 1.91) * mm, "end": v(219.58, 1.37) * mm});
            skLineSegment(sketch, "E6280", {"start": v(219.58, 1.37) * mm, "end": v(220.23, 0.25) * mm});
            skLineSegment(sketch, "E6281", {"start": v(220.23, 0.25) * mm, "end": v(220.87, -0.88) * mm});
            skLineSegment(sketch, "E6282", {"start": v(220.87, -0.88) * mm, "end": v(221.5, -2.01) * mm});
            skLineSegment(sketch, "E6283", {"start": v(221.5, -2.01) * mm, "end": v(222.13, -3.15) * mm});
            skLineSegment(sketch, "E6284", {"start": v(222.13, -3.15) * mm, "end": v(222.77, -4.27) * mm});
            skLineSegment(sketch, "E6285", {"start": v(222.77, -4.27) * mm, "end": v(223.41, -5.4) * mm});
            skLineSegment(sketch, "E6286", {"start": v(223.41, -5.4) * mm, "end": v(224.08, -6.5) * mm});
            skLineSegment(sketch, "E6287", {"start": v(224.08, -6.5) * mm, "end": v(224.76, -7.6) * mm});
            skLineSegment(sketch, "E6288", {"start": v(224.76, -7.6) * mm, "end": v(225.03, -8.17) * mm});
            skLineSegment(sketch, "E6289", {"start": v(225.03, -8.17) * mm, "end": v(225.24, -8.84) * mm});
            skLineSegment(sketch, "E6290", {"start": v(225.24, -8.84) * mm, "end": v(225.44, -9.53) * mm});
            skLineSegment(sketch, "E6291", {"start": v(225.44, -9.53) * mm, "end": v(225.66, -10.2) * mm});
            skLineSegment(sketch, "E6292", {"start": v(225.66, -10.2) * mm, "end": v(225.97, -10.75) * mm});
            skLineSegment(sketch, "E6293", {"start": v(225.97, -10.75) * mm, "end": v(226.4, -11.12) * mm});
            skLineSegment(sketch, "E6294", {"start": v(226.4, -11.12) * mm, "end": v(227, -11.26) * mm});
            skLineSegment(sketch, "E6295", {"start": v(227, -11.26) * mm, "end": v(227.81, -11.09) * mm});
            skLineSegment(sketch, "E6296", {"start": v(227.81, -11.09) * mm, "end": v(228.47, -10.75) * mm});
            skLineSegment(sketch, "E6297", {"start": v(228.47, -10.75) * mm, "end": v(229.05, -10.27) * mm});
            skLineSegment(sketch, "E6298", {"start": v(229.05, -10.27) * mm, "end": v(229.55, -9.68) * mm});
            skLineSegment(sketch, "E6299", {"start": v(229.55, -9.68) * mm, "end": v(230, -8.97) * mm});
            skLineSegment(sketch, "E6300", {"start": v(230, -8.97) * mm, "end": v(230.37, -8.18) * mm});
            skLineSegment(sketch, "E6301", {"start": v(230.37, -8.18) * mm, "end": v(230.69, -7.32) * mm});
            skLineSegment(sketch, "E6302", {"start": v(230.69, -7.32) * mm, "end": v(230.95, -6.42) * mm});
            skLineSegment(sketch, "E6303", {"start": v(230.95, -6.42) * mm, "end": v(231.17, -5.47) * mm});
            skLineSegment(sketch, "E6304", {"start": v(125.48, -158.2) * mm, "end": v(125.3, -161) * mm});
            skLineSegment(sketch, "E6305", {"start": v(125.3, -161) * mm, "end": v(124.7, -163.63) * mm});
            skLineSegment(sketch, "E6306", {"start": v(124.7, -163.63) * mm, "end": v(123.76, -166.02) * mm});
            skLineSegment(sketch, "E6307", {"start": v(123.76, -166.02) * mm, "end": v(122.49, -168.16) * mm});
            skLineSegment(sketch, "E6308", {"start": v(122.49, -168.16) * mm, "end": v(120.94, -170.02) * mm});
            skLineSegment(sketch, "E6309", {"start": v(120.94, -170.02) * mm, "end": v(119.14, -171.58) * mm});
            skLineSegment(sketch, "E6310", {"start": v(119.14, -171.58) * mm, "end": v(117.14, -172.8) * mm});
            skLineSegment(sketch, "E6311", {"start": v(117.14, -172.8) * mm, "end": v(114.98, -173.66) * mm});
            skLineSegment(sketch, "E6312", {"start": v(114.98, -173.66) * mm, "end": v(114.4, -173.8) * mm});
            skLineSegment(sketch, "E6313", {"start": v(114.4, -173.8) * mm, "end": v(113.88, -173.85) * mm});
            skLineSegment(sketch, "E6314", {"start": v(113.88, -173.85) * mm, "end": v(113.4, -173.81) * mm});
            skLineSegment(sketch, "E6315", {"start": v(113.4, -173.81) * mm, "end": v(112.98, -173.7) * mm});
            skLineSegment(sketch, "E6316", {"start": v(112.98, -173.7) * mm, "end": v(112.6, -173.49) * mm});
            skLineSegment(sketch, "E6317", {"start": v(112.6, -173.49) * mm, "end": v(112.25, -173.2) * mm});
            skLineSegment(sketch, "E6318", {"start": v(112.25, -173.2) * mm, "end": v(111.93, -172.85) * mm});
            skLineSegment(sketch, "E6319", {"start": v(111.93, -172.85) * mm, "end": v(111.64, -172.41) * mm});
            skLineSegment(sketch, "E6320", {"start": v(111.64, -172.41) * mm, "end": v(110, -169.7) * mm});
            skLineSegment(sketch, "E6321", {"start": v(110, -169.7) * mm, "end": v(108.35, -166.97) * mm});
            skLineSegment(sketch, "E6322", {"start": v(108.35, -166.97) * mm, "end": v(106.7, -164.24) * mm});
            skLineSegment(sketch, "E6323", {"start": v(106.7, -164.24) * mm, "end": v(105.07, -161.52) * mm});
            skLineSegment(sketch, "E6324", {"start": v(105.07, -161.52) * mm, "end": v(103.43, -158.79) * mm});
            skLineSegment(sketch, "E6325", {"start": v(103.43, -158.79) * mm, "end": v(101.78, -156.06) * mm});
            skLineSegment(sketch, "E6326", {"start": v(101.78, -156.06) * mm, "end": v(100.14, -153.34) * mm});
            skLineSegment(sketch, "E6327", {"start": v(100.14, -153.34) * mm, "end": v(98.5, -150.62) * mm});
            skLineSegment(sketch, "E6328", {"start": v(98.5, -150.62) * mm, "end": v(98.11, -149.83) * mm});
            skLineSegment(sketch, "E6329", {"start": v(98.11, -149.83) * mm, "end": v(97.95, -149.14) * mm});
            skLineSegment(sketch, "E6330", {"start": v(97.95, -149.14) * mm, "end": v(97.98, -148.53) * mm});
            skLineSegment(sketch, "E6331", {"start": v(97.98, -148.53) * mm, "end": v(98.19, -147.98) * mm});
            skLineSegment(sketch, "E6332", {"start": v(98.19, -147.98) * mm, "end": v(98.53, -147.48) * mm});
            skLineSegment(sketch, "E6333", {"start": v(98.53, -147.48) * mm, "end": v(99, -147.03) * mm});
            skLineSegment(sketch, "E6334", {"start": v(99, -147.03) * mm, "end": v(99.54, -146.62) * mm});
            skLineSegment(sketch, "E6335", {"start": v(99.54, -146.62) * mm, "end": v(100.16, -146.22) * mm});
            skLineSegment(sketch, "E6336", {"start": v(100.16, -146.22) * mm, "end": v(102.04, -145.12) * mm});
            skLineSegment(sketch, "E6337", {"start": v(102.04, -145.12) * mm, "end": v(103.94, -144.12) * mm});
            skLineSegment(sketch, "E6338", {"start": v(103.94, -144.12) * mm, "end": v(105.87, -143.28) * mm});
            skLineSegment(sketch, "E6339", {"start": v(105.87, -143.28) * mm, "end": v(107.83, -142.67) * mm});
            skLineSegment(sketch, "E6340", {"start": v(107.83, -142.67) * mm, "end": v(109.82, -142.35) * mm});
            skLineSegment(sketch, "E6341", {"start": v(109.82, -142.35) * mm, "end": v(111.86, -142.39) * mm});
            skLineSegment(sketch, "E6342", {"start": v(111.86, -142.39) * mm, "end": v(113.93, -142.85) * mm});
            skLineSegment(sketch, "E6343", {"start": v(113.93, -142.85) * mm, "end": v(116.06, -143.8) * mm});
            skLineSegment(sketch, "E6344", {"start": v(116.06, -143.8) * mm, "end": v(118.18, -145.2) * mm});
            skLineSegment(sketch, "E6345", {"start": v(118.18, -145.2) * mm, "end": v(120, -146.8) * mm});
            skLineSegment(sketch, "E6346", {"start": v(120, -146.8) * mm, "end": v(121.51, -148.55) * mm});
            skLineSegment(sketch, "E6347", {"start": v(121.51, -148.55) * mm, "end": v(122.76, -150.41) * mm});
            skLineSegment(sketch, "E6348", {"start": v(122.76, -150.41) * mm, "end": v(123.76, -152.34) * mm});
            skLineSegment(sketch, "E6349", {"start": v(123.76, -152.34) * mm, "end": v(124.53, -154.31) * mm});
            skLineSegment(sketch, "E6350", {"start": v(124.53, -154.31) * mm, "end": v(125.1, -156.28) * mm});
            skLineSegment(sketch, "E6351", {"start": v(125.1, -156.28) * mm, "end": v(125.48, -158.2) * mm});
            skLineSegment(sketch, "E6352", {"start": v(173.42, 80.22) * mm, "end": v(172.24, 80.46) * mm});
            skLineSegment(sketch, "E6353", {"start": v(172.24, 80.46) * mm, "end": v(171.11, 80.8) * mm});
            skLineSegment(sketch, "E6354", {"start": v(171.11, 80.8) * mm, "end": v(170.04, 81.26) * mm});
            skLineSegment(sketch, "E6355", {"start": v(170.04, 81.26) * mm, "end": v(169.05, 81.85) * mm});
            skLineSegment(sketch, "E6356", {"start": v(169.05, 81.85) * mm, "end": v(168.16, 82.58) * mm});
            skLineSegment(sketch, "E6357", {"start": v(168.16, 82.58) * mm, "end": v(167.39, 83.48) * mm});
            skLineSegment(sketch, "E6358", {"start": v(167.39, 83.48) * mm, "end": v(166.74, 84.54) * mm});
            skLineSegment(sketch, "E6359", {"start": v(166.74, 84.54) * mm, "end": v(166.25, 85.78) * mm});
            skLineSegment(sketch, "E6360", {"start": v(166.25, 85.78) * mm, "end": v(166.45, 86.55) * mm});
            skLineSegment(sketch, "E6361", {"start": v(166.45, 86.55) * mm, "end": v(167.24, 87.72) * mm});
            skLineSegment(sketch, "E6362", {"start": v(167.24, 87.72) * mm, "end": v(168.47, 89.14) * mm});
            skLineSegment(sketch, "E6363", {"start": v(168.47, 89.14) * mm, "end": v(169.97, 90.64) * mm});
            skLineSegment(sketch, "E6364", {"start": v(169.97, 90.64) * mm, "end": v(171.56, 92.08) * mm});
            skLineSegment(sketch, "E6365", {"start": v(171.56, 92.08) * mm, "end": v(173.08, 93.3) * mm});
            skLineSegment(sketch, "E6366", {"start": v(173.08, 93.3) * mm, "end": v(174.37, 94.16) * mm});
            skLineSegment(sketch, "E6367", {"start": v(174.37, 94.16) * mm, "end": v(175.25, 94.5) * mm});
            skLineSegment(sketch, "E6368", {"start": v(175.25, 94.5) * mm, "end": v(176.08, 94.3) * mm});
            skLineSegment(sketch, "E6369", {"start": v(176.08, 94.3) * mm, "end": v(177, 93.75) * mm});
            skLineSegment(sketch, "E6370", {"start": v(177, 93.75) * mm, "end": v(177.97, 92.9) * mm});
            skLineSegment(sketch, "E6371", {"start": v(177.97, 92.9) * mm, "end": v(178.9, 91.83) * mm});
            skLineSegment(sketch, "E6372", {"start": v(178.9, 91.83) * mm, "end": v(179.75, 90.65) * mm});
            skLineSegment(sketch, "E6373", {"start": v(179.75, 90.65) * mm, "end": v(180.44, 89.41) * mm});
            skLineSegment(sketch, "E6374", {"start": v(180.44, 89.41) * mm, "end": v(180.9, 88.21) * mm});
            skLineSegment(sketch, "E6375", {"start": v(180.9, 88.21) * mm, "end": v(181.07, 87.13) * mm});
            skLineSegment(sketch, "E6376", {"start": v(181.07, 87.13) * mm, "end": v(180.9, 85.92) * mm});
            skLineSegment(sketch, "E6377", {"start": v(180.9, 85.92) * mm, "end": v(180.42, 84.71) * mm});
            skLineSegment(sketch, "E6378", {"start": v(180.42, 84.71) * mm, "end": v(179.65, 83.55) * mm});
            skLineSegment(sketch, "E6379", {"start": v(179.65, 83.55) * mm, "end": v(178.66, 82.5) * mm});
            skLineSegment(sketch, "E6380", {"start": v(178.66, 82.5) * mm, "end": v(177.5, 81.58) * mm});
            skLineSegment(sketch, "E6381", {"start": v(177.5, 81.58) * mm, "end": v(176.2, 80.86) * mm});
            skLineSegment(sketch, "E6382", {"start": v(176.2, 80.86) * mm, "end": v(174.82, 80.4) * mm});
            skLineSegment(sketch, "E6383", {"start": v(174.82, 80.4) * mm, "end": v(173.42, 80.22) * mm});
            skSolve(sketch);
        }
        {
            var Q0;
            Q0=makeQuery(id+"F0.imprint","IMPRINT",FACE,{"disambiguationData":[TD([[makeQuery(id+"F0.imprint","IMPRINT",EDGE,{"derivedFrom":sQuery(id+"F0.wireOp",EDGE,"E1040")}),1.0]])]});
            var Q1;
            Q1=makeQuery(id+"F0.imprint","IMPRINT",FACE,{"disambiguationData":[TD([[makeQuery(id+"F0.imprint","IMPRINT",EDGE,{"derivedFrom":sQuery(id+"F0.wireOp",EDGE,"E1160")}),1.0]])]});
            var Q2;
            Q2=makeQuery(id+"F0.imprint","IMPRINT",FACE,{"disambiguationData":[TD([[makeQuery(id+"F0.imprint","IMPRINT",EDGE,{"derivedFrom":sQuery(id+"F0.wireOp",EDGE,"E1672")}),1.0]])]});
            var Q3;
            Q3=makeQuery(id+"F0.imprint","IMPRINT",FACE,{"disambiguationData":[TD([[makeQuery(id+"F0.imprint","IMPRINT",EDGE,{"derivedFrom":sQuery(id+"F0.wireOp",EDGE,"E5704")}),1.0]])]});
            var Q4;
            Q4=makeQuery(id+"F0.imprint","IMPRINT",FACE,{"disambiguationData":[TD([[makeQuery(id+"F0.imprint","IMPRINT",EDGE,{"derivedFrom":sQuery(id+"F0.wireOp",EDGE,"E5776")}),1.0]])]});
            var Q5;
            Q5=makeQuery(id+"F0.imprint","IMPRINT",FACE,{"disambiguationData":[TD([[makeQuery(id+"F0.imprint","IMPRINT",EDGE,{"derivedFrom":sQuery(id+"F0.wireOp",EDGE,"E3200")}),-1.0]])]});
            var Q6;
            Q6=makeQuery(id+"F0.imprint","IMPRINT",FACE,{"disambiguationData":[TD([[makeQuery(id+"F0.imprint","IMPRINT",EDGE,{"derivedFrom":sQuery(id+"F0.wireOp",EDGE,"E504")}),1.0]])]});
            var Q7;
            Q7=makeQuery(id+"F0.imprint","IMPRINT",FACE,{"disambiguationData":[TD([[makeQuery(id+"F0.imprint","IMPRINT",EDGE,{"derivedFrom":sQuery(id+"F0.wireOp",EDGE,"E6008")}),1.0]])]});
            var Q8;
            Q8=makeQuery(id+"F0.imprint","IMPRINT",FACE,{"disambiguationData":[TD([[makeQuery(id+"F0.imprint","IMPRINT",EDGE,{"derivedFrom":sQuery(id+"F0.wireOp",EDGE,"E4112")}),-1.0]])]});
            var Q9;
            Q9=makeQuery(id+"F0.imprint","IMPRINT",FACE,{"disambiguationData":[TD([[makeQuery(id+"F0.imprint","IMPRINT",EDGE,{"derivedFrom":sQuery(id+"F0.wireOp",EDGE,"E4192")}),-1.0]])]});
            var Q10;
            Q10=makeQuery(id+"F0.imprint","IMPRINT",FACE,{"disambiguationData":[TD([[makeQuery(id+"F0.imprint","IMPRINT",EDGE,{"derivedFrom":sQuery(id+"F0.wireOp",EDGE,"E6080")}),1.0]])]});
            var Q11;
            Q11=makeQuery(id+"F0.imprint","IMPRINT",FACE,{"disambiguationData":[TD([[makeQuery(id+"F0.imprint","IMPRINT",EDGE,{"derivedFrom":sQuery(id+"F0.wireOp",EDGE,"E0")}),-1.0]])]});
            var Q12;
            Q12=makeQuery(id+"F0.imprint","IMPRINT",FACE,{"disambiguationData":[TD([[makeQuery(id+"F0.imprint","IMPRINT",EDGE,{"derivedFrom":sQuery(id+"F0.wireOp",EDGE,"E6128")}),1.0]])]});
            var Q13;
            Q13=makeQuery(id+"F0.imprint","IMPRINT",FACE,{"disambiguationData":[TD([[makeQuery(id+"F0.imprint","IMPRINT",EDGE,{"derivedFrom":sQuery(id+"F0.wireOp",EDGE,"E4968")}),1.0]])]});
            var Q14;
            Q14=makeQuery(id+"F0.imprint","IMPRINT",FACE,{"disambiguationData":[TD([[makeQuery(id+"F0.imprint","IMPRINT",EDGE,{"derivedFrom":sQuery(id+"F0.wireOp",EDGE,"E6304")}),-1.0]])]});
            var Q15;
            Q15=makeQuery(id+"F0.imprint","IMPRINT",FACE,{"disambiguationData":[TD([[makeQuery(id+"F0.imprint","IMPRINT",EDGE,{"derivedFrom":sQuery(id+"F0.wireOp",EDGE,"E1424")}),1.0]])]});
            var Q16;
            Q16=makeQuery(id+"F0.imprint","IMPRINT",FACE,{"disambiguationData":[TD([[makeQuery(id+"F0.imprint","IMPRINT",EDGE,{"derivedFrom":sQuery(id+"F0.wireOp",EDGE,"E2216")}),1.0]])]});
            var Q17;
            Q17=makeQuery(id+"F0.imprint","IMPRINT",FACE,{"disambiguationData":[TD([[makeQuery(id+"F0.imprint","IMPRINT",EDGE,{"derivedFrom":sQuery(id+"F0.wireOp",EDGE,"E1272")}),1.0]])]});
            var Q18;
            Q18=makeQuery(id+"F0.imprint","IMPRINT",FACE,{"disambiguationData":[TD([[makeQuery(id+"F0.imprint","IMPRINT",EDGE,{"derivedFrom":sQuery(id+"F0.wireOp",EDGE,"E2352")}),1.0]])]});
            var Q19;
            Q19=makeQuery(id+"F0.imprint","IMPRINT",FACE,{"disambiguationData":[TD([[makeQuery(id+"F0.imprint","IMPRINT",EDGE,{"derivedFrom":sQuery(id+"F0.wireOp",EDGE,"E1752")}),1.0]])]});
            var Q20;
            Q20=makeQuery(id+"F0.imprint","IMPRINT",FACE,{"disambiguationData":[TD([[makeQuery(id+"F0.imprint","IMPRINT",EDGE,{"derivedFrom":sQuery(id+"F0.wireOp",EDGE,"E5816")}),1.0]])]});
            var Q21;
            Q21=makeQuery(id+"F0.imprint","IMPRINT",FACE,{"disambiguationData":[TD([[makeQuery(id+"F0.imprint","IMPRINT",EDGE,{"derivedFrom":sQuery(id+"F0.wireOp",EDGE,"E4344")}),1.0]])]});
            var Q22;
            Q22=makeQuery(id+"F0.imprint","IMPRINT",FACE,{"disambiguationData":[TD([[makeQuery(id+"F0.imprint","IMPRINT",EDGE,{"derivedFrom":sQuery(id+"F0.wireOp",EDGE,"E5040")}),1.0]])]});
            var Q23;
            Q23=makeQuery(id+"F0.imprint","IMPRINT",FACE,{"disambiguationData":[TD([[makeQuery(id+"F0.imprint","IMPRINT",EDGE,{"derivedFrom":sQuery(id+"F0.wireOp",EDGE,"E2064")}),1.0]])]});
            var Q24;
            Q24=makeQuery(id+"F0.imprint","IMPRINT",FACE,{"disambiguationData":[TD([[makeQuery(id+"F0.imprint","IMPRINT",EDGE,{"derivedFrom":sQuery(id+"F0.wireOp",EDGE,"E5576")}),1.0]])]});
            var Q25;
            Q25=makeQuery(id+"F0.imprint","IMPRINT",FACE,{"disambiguationData":[TD([[makeQuery(id+"F0.imprint","IMPRINT",EDGE,{"derivedFrom":sQuery(id+"F0.wireOp",EDGE,"E1688")}),1.0]])]});
            var Q26;
            Q26=makeQuery(id+"F0.imprint","IMPRINT",FACE,{"disambiguationData":[TD([[makeQuery(id+"F0.imprint","IMPRINT",EDGE,{"derivedFrom":sQuery(id+"F0.wireOp",EDGE,"E2872")}),1.0]])]});
            var Q27;
            Q27=makeQuery(id+"F0.imprint","IMPRINT",FACE,{"disambiguationData":[TD([[makeQuery(id+"F0.imprint","IMPRINT",EDGE,{"derivedFrom":sQuery(id+"F0.wireOp",EDGE,"E1720")}),1.0]])]});
            var Q28;
            Q28=makeQuery(id+"F0.imprint","IMPRINT",FACE,{"disambiguationData":[TD([[makeQuery(id+"F0.imprint","IMPRINT",EDGE,{"derivedFrom":sQuery(id+"F0.wireOp",EDGE,"E5672")}),-1.0]])]});
            var Q29;
            Q29=makeQuery(id+"F0.imprint","IMPRINT",FACE,{"disambiguationData":[TD([[makeQuery(id+"F0.imprint","IMPRINT",EDGE,{"derivedFrom":sQuery(id+"F0.wireOp",EDGE,"E5976")}),-1.0]])]});
            var Q30;
            Q30=makeQuery(id+"F0.imprint","IMPRINT",FACE,{"disambiguationData":[TD([[makeQuery(id+"F0.imprint","IMPRINT",EDGE,{"derivedFrom":sQuery(id+"F0.wireOp",EDGE,"E4680")}),1.0]])]});
            var Q31;
            Q31=makeQuery(id+"F0.imprint","IMPRINT",FACE,{"disambiguationData":[TD([[makeQuery(id+"F0.imprint","IMPRINT",EDGE,{"derivedFrom":sQuery(id+"F0.wireOp",EDGE,"E2768")}),1.0]])]});
            var Q32;
            Q32=makeQuery(id+"F0.imprint","IMPRINT",FACE,{"disambiguationData":[TD([[makeQuery(id+"F0.imprint","IMPRINT",EDGE,{"derivedFrom":sQuery(id+"F0.wireOp",EDGE,"E2624")}),1.0]])]});
            var Q33;
            Q33=makeQuery(id+"F0.imprint","IMPRINT",FACE,{"disambiguationData":[TD([[makeQuery(id+"F0.imprint","IMPRINT",EDGE,{"derivedFrom":sQuery(id+"F0.wireOp",EDGE,"E2712")}),1.0]])]});
            var Q34;
            Q34=makeQuery(id+"F0.imprint","IMPRINT",FACE,{"disambiguationData":[TD([[makeQuery(id+"F0.imprint","IMPRINT",EDGE,{"derivedFrom":sQuery(id+"F0.wireOp",EDGE,"E1808")}),1.0]])]});
            var Q35;
            Q35=makeQuery(id+"F0.imprint","IMPRINT",FACE,{"disambiguationData":[TD([[makeQuery(id+"F0.imprint","IMPRINT",EDGE,{"derivedFrom":sQuery(id+"F0.wireOp",EDGE,"E1968")}),1.0]])]});
            var Q36;
            Q36=makeQuery(id+"F0.imprint","IMPRINT",FACE,{"disambiguationData":[TD([[makeQuery(id+"F0.imprint","IMPRINT",EDGE,{"derivedFrom":sQuery(id+"F0.wireOp",EDGE,"E2424")}),1.0]])]});
            var Q37;
            Q37=makeQuery(id+"F0.imprint","IMPRINT",FACE,{"disambiguationData":[TD([[makeQuery(id+"F0.imprint","IMPRINT",EDGE,{"derivedFrom":sQuery(id+"F0.wireOp",EDGE,"E5344")}),1.0]])]});
            var Q38;
            Q38=makeQuery(id+"F0.imprint","IMPRINT",FACE,{"disambiguationData":[TD([[makeQuery(id+"F0.imprint","IMPRINT",EDGE,{"derivedFrom":sQuery(id+"F0.wireOp",EDGE,"E2952")}),1.0]])]});
            var Q39;
            Q39=makeQuery(id+"F0.imprint","IMPRINT",FACE,{"disambiguationData":[TD([[makeQuery(id+"F0.imprint","IMPRINT",EDGE,{"derivedFrom":sQuery(id+"F0.wireOp",EDGE,"E4848")}),1.0]])]});
            var Q40;
            Q40=makeQuery(id+"F0.imprint","IMPRINT",FACE,{"disambiguationData":[TD([[makeQuery(id+"F0.imprint","IMPRINT",EDGE,{"derivedFrom":sQuery(id+"F0.wireOp",EDGE,"E5192")}),1.0]])]});
            var Q41;
            Q41=makeQuery(id+"F0.imprint","IMPRINT",FACE,{"disambiguationData":[TD([[makeQuery(id+"F0.imprint","IMPRINT",EDGE,{"derivedFrom":sQuery(id+"F0.wireOp",EDGE,"E2496")}),1.0]])]});
            var Q42;
            Q42=makeQuery(id+"F0.imprint","IMPRINT",FACE,{"disambiguationData":[TD([[makeQuery(id+"F0.imprint","IMPRINT",EDGE,{"derivedFrom":sQuery(id+"F0.wireOp",EDGE,"E2560")}),1.0]])]});
            var Q43;
            Q43=makeQuery(id+"F0.imprint","IMPRINT",FACE,{"disambiguationData":[TD([[makeQuery(id+"F0.imprint","IMPRINT",EDGE,{"derivedFrom":sQuery(id+"F0.wireOp",EDGE,"E5440")}),1.0]])]});
            var Q44;
            Q44=makeQuery(id+"F0.imprint","IMPRINT",FACE,{"disambiguationData":[TD([[makeQuery(id+"F0.imprint","IMPRINT",EDGE,{"derivedFrom":sQuery(id+"F0.wireOp",EDGE,"E4528")}),1.0]])]});
            var Q45;
            Q45=makeQuery(id+"F0.imprint","IMPRINT",FACE,{"disambiguationData":[TD([[makeQuery(id+"F0.imprint","IMPRINT",EDGE,{"derivedFrom":sQuery(id+"F0.wireOp",EDGE,"E2248")}),1.0]])]});
            var Q46;
            Q46=makeQuery(id+"F0.imprint","IMPRINT",FACE,{"disambiguationData":[TD([[makeQuery(id+"F0.imprint","IMPRINT",EDGE,{"derivedFrom":sQuery(id+"F0.wireOp",EDGE,"E3016")}),1.0]])]});
            var Q47;
            Q47=makeQuery(id+"F0.imprint","IMPRINT",FACE,{"disambiguationData":[TD([[makeQuery(id+"F0.imprint","IMPRINT",EDGE,{"derivedFrom":sQuery(id+"F0.wireOp",EDGE,"E5904")}),1.0]])]});
            var Q48;
            Q48=makeQuery(id+"F0.imprint","IMPRINT",FACE,{"disambiguationData":[TD([[makeQuery(id+"F0.imprint","IMPRINT",EDGE,{"derivedFrom":sQuery(id+"F0.wireOp",EDGE,"E6352")}),-1.0]])]});
            var Q49;
            Q49=makeQuery(id+"F0.imprint","IMPRINT",FACE,{"disambiguationData":[TD([[makeQuery(id+"F0.imprint","IMPRINT",EDGE,{"derivedFrom":sQuery(id+"F0.wireOp",EDGE,"E5864")}),1.0]])]});
            var Q50;
            Q50=makeQuery(id+"F0.imprint","IMPRINT",FACE,{"disambiguationData":[TD([[makeQuery(id+"F0.imprint","IMPRINT",EDGE,{"derivedFrom":sQuery(id+"F0.wireOp",EDGE,"E6232")}),1.0]])]});
            var Q51;
            Q51=makeQuery(id+"F0.imprint","IMPRINT",FACE,{"disambiguationData":[TD([[makeQuery(id+"F0.imprint","IMPRINT",EDGE,{"derivedFrom":sQuery(id+"F0.wireOp",EDGE,"E3152")}),1.0]])]});
            var Q52;
            Q52=makeQuery(id+"F0.imprint","IMPRINT",FACE,{"disambiguationData":[TD([[makeQuery(id+"F0.imprint","IMPRINT",EDGE,{"derivedFrom":sQuery(id+"F0.wireOp",EDGE,"E5928")}),1.0]])]});
            var Q53;
            Q53=makeQuery(id+"F0.imprint","IMPRINT",FACE,{"disambiguationData":[TD([[makeQuery(id+"F0.imprint","IMPRINT",EDGE,{"derivedFrom":sQuery(id+"F0.wireOp",EDGE,"E6184")}),1.0]])]});
            var Q54;
            Q54=makeQuery(id+"F0.imprint","IMPRINT",FACE,{"disambiguationData":[TD([[makeQuery(id+"F0.imprint","IMPRINT",EDGE,{"derivedFrom":sQuery(id+"F0.wireOp",EDGE,"E3096")}),1.0]])]});
            var Q55;
            Q55=makeQuery(id+"F0.imprint","IMPRINT",FACE,{"disambiguationData":[TD([[makeQuery(id+"F0.imprint","IMPRINT",EDGE,{"derivedFrom":sQuery(id+"F0.wireOp",EDGE,"E4064")}),1.0]])]});
            var Q56;
            Q56=makeQuery(id+"F0.imprint","IMPRINT",FACE,{"disambiguationData":[TD([[makeQuery(id+"F0.imprint","IMPRINT",EDGE,{"derivedFrom":sQuery(id+"F0.wireOp",EDGE,"E6256")}),1.0]])]});
            extrude(context, id + "F1", {"entities" : qUnion([Q0, Q1, Q2, Q3, Q4, Q5, Q6, Q7, Q8, Q9, Q10, Q11, Q12, Q13, Q14, Q15, Q16, Q17, Q18, Q19, Q20, Q21, Q22, Q23, Q24, Q25, Q26, Q27, Q28, Q29, Q30, Q31, Q32, Q33, Q34, Q35, Q36, Q37, Q38, Q39, Q40, Q41, Q42, Q43, Q44, Q45, Q46, Q47, Q48, Q49, Q50, Q51, Q52, Q53, Q54, Q55, Q56]), "oppositeDirection" : true, "depth" : 8 * mm});
        }
        {
            var Q0;
            Q0=makeQuery(id+"F0.imprint","IMPRINT",FACE,{"disambiguationData":[TD([[makeQuery(id+"F0.imprint","IMPRINT",EDGE,{"derivedFrom":sQuery(id+"F0.wireOp",EDGE,"E4192")}),-1.0]])]});
            var Q1;
            Q1=makeQuery(id+"F0.imprint","IMPRINT",FACE,{"disambiguationData":[TD([[makeQuery(id+"F0.imprint","IMPRINT",EDGE,{"derivedFrom":sQuery(id+"F0.wireOp",EDGE,"E0")}),-1.0]])]});
            var Q2;
            Q2=makeQuery(id+"F0.imprint","IMPRINT",FACE,{"disambiguationData":[TD([[makeQuery(id+"F0.imprint","IMPRINT",EDGE,{"derivedFrom":sQuery(id+"F0.wireOp",EDGE,"E5672")}),-1.0]])]});
            var Q3;
            Q3=makeQuery(id+"F0.imprint","IMPRINT",FACE,{"disambiguationData":[TD([[makeQuery(id+"F0.imprint","IMPRINT",EDGE,{"derivedFrom":sQuery(id+"F0.wireOp",EDGE,"E5976")}),-1.0]])]});
            var Q4;
            Q4=makeQuery(id+"F0.imprint","IMPRINT",FACE,{"disambiguationData":[TD([[makeQuery(id+"F0.imprint","IMPRINT",EDGE,{"derivedFrom":sQuery(id+"F0.wireOp",EDGE,"E3200")}),-1.0]])]});
            var Q5;
            Q5=makeQuery(id+"F0.imprint","IMPRINT",FACE,{"disambiguationData":[TD([[makeQuery(id+"F0.imprint","IMPRINT",EDGE,{"derivedFrom":sQuery(id+"F0.wireOp",EDGE,"E4112")}),-1.0]])]});
            var Q6;
            Q6=makeQuery(id+"F0.imprint","IMPRINT",FACE,{"disambiguationData":[TD([[makeQuery(id+"F0.imprint","IMPRINT",EDGE,{"derivedFrom":sQuery(id+"F0.wireOp",EDGE,"E6352")}),-1.0]])]});
            var Q7;
            Q7=makeQuery(id+"F0.imprint","IMPRINT",FACE,{"disambiguationData":[TD([[makeQuery(id+"F0.imprint","IMPRINT",EDGE,{"derivedFrom":sQuery(id+"F0.wireOp",EDGE,"E6304")}),-1.0]])]});
            extrude(context, id + "F2", {"entities" : qUnion([Q0, Q1, Q2, Q3, Q4, Q5, Q6, Q7]), "operationType" : NewBodyOperationType.ADD, "depth" : 1 * mm});
        }
        {
            var Q0;
            Q0=makeQuery(id+"F1.opExtrude","CAP_FACE",FACE,{"disambiguationData":[OSD([sQuery(id+"F0.wireOp",EDGE,"E0"),sQuery(id+"F0.wireOp",EDGE,"E1"),sQuery(id+"F0.wireOp",EDGE,"E2"),sQuery(id+"F0.wireOp",EDGE,"E3"),sQuery(id+"F0.wireOp",EDGE,"E4"),sQuery(id+"F0.wireOp",EDGE,"E5"),sQuery(id+"F0.wireOp",EDGE,"E6"),sQuery(id+"F0.wireOp",EDGE,"E7"),sQuery(id+"F0.wireOp",EDGE,"E8"),sQuery(id+"F0.wireOp",EDGE,"E9"),sQuery(id+"F0.wireOp",EDGE,"E10"),sQuery(id+"F0.wireOp",EDGE,"E11"),sQuery(id+"F0.wireOp",EDGE,"E12"),sQuery(id+"F0.wireOp",EDGE,"E13"),sQuery(id+"F0.wireOp",EDGE,"E14"),sQuery(id+"F0.wireOp",EDGE,"E15"),sQuery(id+"F0.wireOp",EDGE,"E16"),sQuery(id+"F0.wireOp",EDGE,"E17"),sQuery(id+"F0.wireOp",EDGE,"E18"),sQuery(id+"F0.wireOp",EDGE,"E19"),sQuery(id+"F0.wireOp",EDGE,"E20"),sQuery(id+"F0.wireOp",EDGE,"E21"),sQuery(id+"F0.wireOp",EDGE,"E22"),sQuery(id+"F0.wireOp",EDGE,"E23"),sQuery(id+"F0.wireOp",EDGE,"E24"),sQuery(id+"F0.wireOp",EDGE,"E25"),sQuery(id+"F0.wireOp",EDGE,"E26"),sQuery(id+"F0.wireOp",EDGE,"E27"),sQuery(id+"F0.wireOp",EDGE,"E28"),sQuery(id+"F0.wireOp",EDGE,"E29"),sQuery(id+"F0.wireOp",EDGE,"E30"),sQuery(id+"F0.wireOp",EDGE,"E31"),sQuery(id+"F0.wireOp",EDGE,"E32"),sQuery(id+"F0.wireOp",EDGE,"E33"),sQuery(id+"F0.wireOp",EDGE,"E34"),sQuery(id+"F0.wireOp",EDGE,"E35"),sQuery(id+"F0.wireOp",EDGE,"E36"),sQuery(id+"F0.wireOp",EDGE,"E37"),sQuery(id+"F0.wireOp",EDGE,"E38"),sQuery(id+"F0.wireOp",EDGE,"E39"),sQuery(id+"F0.wireOp",EDGE,"E40"),sQuery(id+"F0.wireOp",EDGE,"E41"),sQuery(id+"F0.wireOp",EDGE,"E42"),sQuery(id+"F0.wireOp",EDGE,"E43"),sQuery(id+"F0.wireOp",EDGE,"E44"),sQuery(id+"F0.wireOp",EDGE,"E45"),sQuery(id+"F0.wireOp",EDGE,"E46"),sQuery(id+"F0.wireOp",EDGE,"E47"),sQuery(id+"F0.wireOp",EDGE,"E48"),sQuery(id+"F0.wireOp",EDGE,"E49"),sQuery(id+"F0.wireOp",EDGE,"E50"),sQuery(id+"F0.wireOp",EDGE,"E51"),sQuery(id+"F0.wireOp",EDGE,"E52"),sQuery(id+"F0.wireOp",EDGE,"E53"),sQuery(id+"F0.wireOp",EDGE,"E54"),sQuery(id+"F0.wireOp",EDGE,"E55"),sQuery(id+"F0.wireOp",EDGE,"E56"),sQuery(id+"F0.wireOp",EDGE,"E57"),sQuery(id+"F0.wireOp",EDGE,"E58"),sQuery(id+"F0.wireOp",EDGE,"E59"),sQuery(id+"F0.wireOp",EDGE,"E60"),sQuery(id+"F0.wireOp",EDGE,"E61"),sQuery(id+"F0.wireOp",EDGE,"E62"),sQuery(id+"F0.wireOp",EDGE,"E63"),sQuery(id+"F0.wireOp",EDGE,"E64"),sQuery(id+"F0.wireOp",EDGE,"E65"),sQuery(id+"F0.wireOp",EDGE,"E66"),sQuery(id+"F0.wireOp",EDGE,"E67"),sQuery(id+"F0.wireOp",EDGE,"E68"),sQuery(id+"F0.wireOp",EDGE,"E69"),sQuery(id+"F0.wireOp",EDGE,"E70"),sQuery(id+"F0.wireOp",EDGE,"E71"),sQuery(id+"F0.wireOp",EDGE,"E72"),sQuery(id+"F0.wireOp",EDGE,"E73"),sQuery(id+"F0.wireOp",EDGE,"E74"),sQuery(id+"F0.wireOp",EDGE,"E75"),sQuery(id+"F0.wireOp",EDGE,"E76"),sQuery(id+"F0.wireOp",EDGE,"E77"),sQuery(id+"F0.wireOp",EDGE,"E78"),sQuery(id+"F0.wireOp",EDGE,"E79"),sQuery(id+"F0.wireOp",EDGE,"E80"),sQuery(id+"F0.wireOp",EDGE,"E81"),sQuery(id+"F0.wireOp",EDGE,"E82"),sQuery(id+"F0.wireOp",EDGE,"E83"),sQuery(id+"F0.wireOp",EDGE,"E84"),sQuery(id+"F0.wireOp",EDGE,"E85"),sQuery(id+"F0.wireOp",EDGE,"E86"),sQuery(id+"F0.wireOp",EDGE,"E87"),sQuery(id+"F0.wireOp",EDGE,"E88"),sQuery(id+"F0.wireOp",EDGE,"E89"),sQuery(id+"F0.wireOp",EDGE,"E90"),sQuery(id+"F0.wireOp",EDGE,"E91"),sQuery(id+"F0.wireOp",EDGE,"E92"),sQuery(id+"F0.wireOp",EDGE,"E93"),sQuery(id+"F0.wireOp",EDGE,"E94"),sQuery(id+"F0.wireOp",EDGE,"E95"),sQuery(id+"F0.wireOp",EDGE,"E96"),sQuery(id+"F0.wireOp",EDGE,"E97"),sQuery(id+"F0.wireOp",EDGE,"E98"),sQuery(id+"F0.wireOp",EDGE,"E99"),sQuery(id+"F0.wireOp",EDGE,"E100"),sQuery(id+"F0.wireOp",EDGE,"E101"),sQuery(id+"F0.wireOp",EDGE,"E102"),sQuery(id+"F0.wireOp",EDGE,"E103"),sQuery(id+"F0.wireOp",EDGE,"E104"),sQuery(id+"F0.wireOp",EDGE,"E105"),sQuery(id+"F0.wireOp",EDGE,"E106"),sQuery(id+"F0.wireOp",EDGE,"E107"),sQuery(id+"F0.wireOp",EDGE,"E108"),sQuery(id+"F0.wireOp",EDGE,"E109"),sQuery(id+"F0.wireOp",EDGE,"E110"),sQuery(id+"F0.wireOp",EDGE,"E111"),sQuery(id+"F0.wireOp",EDGE,"E112"),sQuery(id+"F0.wireOp",EDGE,"E113"),sQuery(id+"F0.wireOp",EDGE,"E114"),sQuery(id+"F0.wireOp",EDGE,"E115"),sQuery(id+"F0.wireOp",EDGE,"E116"),sQuery(id+"F0.wireOp",EDGE,"E117"),sQuery(id+"F0.wireOp",EDGE,"E118"),sQuery(id+"F0.wireOp",EDGE,"E119"),sQuery(id+"F0.wireOp",EDGE,"E120"),sQuery(id+"F0.wireOp",EDGE,"E121"),sQuery(id+"F0.wireOp",EDGE,"E122"),sQuery(id+"F0.wireOp",EDGE,"E123"),sQuery(id+"F0.wireOp",EDGE,"E124"),sQuery(id+"F0.wireOp",EDGE,"E125"),sQuery(id+"F0.wireOp",EDGE,"E126"),sQuery(id+"F0.wireOp",EDGE,"E127"),sQuery(id+"F0.wireOp",EDGE,"E128"),sQuery(id+"F0.wireOp",EDGE,"E129"),sQuery(id+"F0.wireOp",EDGE,"E130"),sQuery(id+"F0.wireOp",EDGE,"E131"),sQuery(id+"F0.wireOp",EDGE,"E132"),sQuery(id+"F0.wireOp",EDGE,"E133"),sQuery(id+"F0.wireOp",EDGE,"E134"),sQuery(id+"F0.wireOp",EDGE,"E135"),sQuery(id+"F0.wireOp",EDGE,"E136"),sQuery(id+"F0.wireOp",EDGE,"E137"),sQuery(id+"F0.wireOp",EDGE,"E138"),sQuery(id+"F0.wireOp",EDGE,"E139"),sQuery(id+"F0.wireOp",EDGE,"E140"),sQuery(id+"F0.wireOp",EDGE,"E141"),sQuery(id+"F0.wireOp",EDGE,"E142"),sQuery(id+"F0.wireOp",EDGE,"E143"),sQuery(id+"F0.wireOp",EDGE,"E144"),sQuery(id+"F0.wireOp",EDGE,"E145"),sQuery(id+"F0.wireOp",EDGE,"E146"),sQuery(id+"F0.wireOp",EDGE,"E147"),sQuery(id+"F0.wireOp",EDGE,"E148"),sQuery(id+"F0.wireOp",EDGE,"E149"),sQuery(id+"F0.wireOp",EDGE,"E150"),sQuery(id+"F0.wireOp",EDGE,"E151"),sQuery(id+"F0.wireOp",EDGE,"E152"),sQuery(id+"F0.wireOp",EDGE,"E153"),sQuery(id+"F0.wireOp",EDGE,"E154"),sQuery(id+"F0.wireOp",EDGE,"E155"),sQuery(id+"F0.wireOp",EDGE,"E156"),sQuery(id+"F0.wireOp",EDGE,"E157"),sQuery(id+"F0.wireOp",EDGE,"E158"),sQuery(id+"F0.wireOp",EDGE,"E159"),sQuery(id+"F0.wireOp",EDGE,"E160"),sQuery(id+"F0.wireOp",EDGE,"E161"),sQuery(id+"F0.wireOp",EDGE,"E162"),sQuery(id+"F0.wireOp",EDGE,"E163"),sQuery(id+"F0.wireOp",EDGE,"E164"),sQuery(id+"F0.wireOp",EDGE,"E165"),sQuery(id+"F0.wireOp",EDGE,"E166"),sQuery(id+"F0.wireOp",EDGE,"E167"),sQuery(id+"F0.wireOp",EDGE,"E168"),sQuery(id+"F0.wireOp",EDGE,"E169"),sQuery(id+"F0.wireOp",EDGE,"E170"),sQuery(id+"F0.wireOp",EDGE,"E171"),sQuery(id+"F0.wireOp",EDGE,"E172"),sQuery(id+"F0.wireOp",EDGE,"E173"),sQuery(id+"F0.wireOp",EDGE,"E174"),sQuery(id+"F0.wireOp",EDGE,"E175"),sQuery(id+"F0.wireOp",EDGE,"E176"),sQuery(id+"F0.wireOp",EDGE,"E177"),sQuery(id+"F0.wireOp",EDGE,"E178"),sQuery(id+"F0.wireOp",EDGE,"E179"),sQuery(id+"F0.wireOp",EDGE,"E180"),sQuery(id+"F0.wireOp",EDGE,"E181"),sQuery(id+"F0.wireOp",EDGE,"E182"),sQuery(id+"F0.wireOp",EDGE,"E183"),sQuery(id+"F0.wireOp",EDGE,"E184"),sQuery(id+"F0.wireOp",EDGE,"E185"),sQuery(id+"F0.wireOp",EDGE,"E186"),sQuery(id+"F0.wireOp",EDGE,"E187"),sQuery(id+"F0.wireOp",EDGE,"E188"),sQuery(id+"F0.wireOp",EDGE,"E189"),sQuery(id+"F0.wireOp",EDGE,"E190"),sQuery(id+"F0.wireOp",EDGE,"E191"),sQuery(id+"F0.wireOp",EDGE,"E192"),sQuery(id+"F0.wireOp",EDGE,"E193"),sQuery(id+"F0.wireOp",EDGE,"E194"),sQuery(id+"F0.wireOp",EDGE,"E195"),sQuery(id+"F0.wireOp",EDGE,"E196"),sQuery(id+"F0.wireOp",EDGE,"E197"),sQuery(id+"F0.wireOp",EDGE,"E198"),sQuery(id+"F0.wireOp",EDGE,"E199"),sQuery(id+"F0.wireOp",EDGE,"E200"),sQuery(id+"F0.wireOp",EDGE,"E201"),sQuery(id+"F0.wireOp",EDGE,"E202"),sQuery(id+"F0.wireOp",EDGE,"E203"),sQuery(id+"F0.wireOp",EDGE,"E204"),sQuery(id+"F0.wireOp",EDGE,"E205"),sQuery(id+"F0.wireOp",EDGE,"E206"),sQuery(id+"F0.wireOp",EDGE,"E207"),sQuery(id+"F0.wireOp",EDGE,"E208"),sQuery(id+"F0.wireOp",EDGE,"E209"),sQuery(id+"F0.wireOp",EDGE,"E210"),sQuery(id+"F0.wireOp",EDGE,"E211"),sQuery(id+"F0.wireOp",EDGE,"E212"),sQuery(id+"F0.wireOp",EDGE,"E213"),sQuery(id+"F0.wireOp",EDGE,"E214"),sQuery(id+"F0.wireOp",EDGE,"E215"),sQuery(id+"F0.wireOp",EDGE,"E216"),sQuery(id+"F0.wireOp",EDGE,"E217"),sQuery(id+"F0.wireOp",EDGE,"E218"),sQuery(id+"F0.wireOp",EDGE,"E219"),sQuery(id+"F0.wireOp",EDGE,"E220"),sQuery(id+"F0.wireOp",EDGE,"E221"),sQuery(id+"F0.wireOp",EDGE,"E222"),sQuery(id+"F0.wireOp",EDGE,"E223"),sQuery(id+"F0.wireOp",EDGE,"E224"),sQuery(id+"F0.wireOp",EDGE,"E225"),sQuery(id+"F0.wireOp",EDGE,"E226"),sQuery(id+"F0.wireOp",EDGE,"E227"),sQuery(id+"F0.wireOp",EDGE,"E228"),sQuery(id+"F0.wireOp",EDGE,"E229"),sQuery(id+"F0.wireOp",EDGE,"E230"),sQuery(id+"F0.wireOp",EDGE,"E231"),sQuery(id+"F0.wireOp",EDGE,"E232"),sQuery(id+"F0.wireOp",EDGE,"E233"),sQuery(id+"F0.wireOp",EDGE,"E234"),sQuery(id+"F0.wireOp",EDGE,"E235"),sQuery(id+"F0.wireOp",EDGE,"E236"),sQuery(id+"F0.wireOp",EDGE,"E237"),sQuery(id+"F0.wireOp",EDGE,"E238"),sQuery(id+"F0.wireOp",EDGE,"E239"),sQuery(id+"F0.wireOp",EDGE,"E240"),sQuery(id+"F0.wireOp",EDGE,"E241"),sQuery(id+"F0.wireOp",EDGE,"E242"),sQuery(id+"F0.wireOp",EDGE,"E243"),sQuery(id+"F0.wireOp",EDGE,"E244"),sQuery(id+"F0.wireOp",EDGE,"E245"),sQuery(id+"F0.wireOp",EDGE,"E246"),sQuery(id+"F0.wireOp",EDGE,"E247"),sQuery(id+"F0.wireOp",EDGE,"E248"),sQuery(id+"F0.wireOp",EDGE,"E249"),sQuery(id+"F0.wireOp",EDGE,"E250"),sQuery(id+"F0.wireOp",EDGE,"E251"),sQuery(id+"F0.wireOp",EDGE,"E252"),sQuery(id+"F0.wireOp",EDGE,"E253"),sQuery(id+"F0.wireOp",EDGE,"E254"),sQuery(id+"F0.wireOp",EDGE,"E255"),sQuery(id+"F0.wireOp",EDGE,"E256"),sQuery(id+"F0.wireOp",EDGE,"E257"),sQuery(id+"F0.wireOp",EDGE,"E258"),sQuery(id+"F0.wireOp",EDGE,"E259"),sQuery(id+"F0.wireOp",EDGE,"E260"),sQuery(id+"F0.wireOp",EDGE,"E261"),sQuery(id+"F0.wireOp",EDGE,"E262"),sQuery(id+"F0.wireOp",EDGE,"E263"),sQuery(id+"F0.wireOp",EDGE,"E264"),sQuery(id+"F0.wireOp",EDGE,"E265"),sQuery(id+"F0.wireOp",EDGE,"E266"),sQuery(id+"F0.wireOp",EDGE,"E267"),sQuery(id+"F0.wireOp",EDGE,"E268"),sQuery(id+"F0.wireOp",EDGE,"E269"),sQuery(id+"F0.wireOp",EDGE,"E270"),sQuery(id+"F0.wireOp",EDGE,"E271"),sQuery(id+"F0.wireOp",EDGE,"E272"),sQuery(id+"F0.wireOp",EDGE,"E273"),sQuery(id+"F0.wireOp",EDGE,"E274"),sQuery(id+"F0.wireOp",EDGE,"E275"),sQuery(id+"F0.wireOp",EDGE,"E276"),sQuery(id+"F0.wireOp",EDGE,"E277"),sQuery(id+"F0.wireOp",EDGE,"E278"),sQuery(id+"F0.wireOp",EDGE,"E279"),sQuery(id+"F0.wireOp",EDGE,"E280"),sQuery(id+"F0.wireOp",EDGE,"E281"),sQuery(id+"F0.wireOp",EDGE,"E282"),sQuery(id+"F0.wireOp",EDGE,"E283"),sQuery(id+"F0.wireOp",EDGE,"E284"),sQuery(id+"F0.wireOp",EDGE,"E285"),sQuery(id+"F0.wireOp",EDGE,"E286"),sQuery(id+"F0.wireOp",EDGE,"E287"),sQuery(id+"F0.wireOp",EDGE,"E288"),sQuery(id+"F0.wireOp",EDGE,"E289"),sQuery(id+"F0.wireOp",EDGE,"E290"),sQuery(id+"F0.wireOp",EDGE,"E291"),sQuery(id+"F0.wireOp",EDGE,"E292"),sQuery(id+"F0.wireOp",EDGE,"E293"),sQuery(id+"F0.wireOp",EDGE,"E294"),sQuery(id+"F0.wireOp",EDGE,"E295"),sQuery(id+"F0.wireOp",EDGE,"E296"),sQuery(id+"F0.wireOp",EDGE,"E297"),sQuery(id+"F0.wireOp",EDGE,"E298"),sQuery(id+"F0.wireOp",EDGE,"E299"),sQuery(id+"F0.wireOp",EDGE,"E300"),sQuery(id+"F0.wireOp",EDGE,"E301"),sQuery(id+"F0.wireOp",EDGE,"E302"),sQuery(id+"F0.wireOp",EDGE,"E303"),sQuery(id+"F0.wireOp",EDGE,"E304"),sQuery(id+"F0.wireOp",EDGE,"E305"),sQuery(id+"F0.wireOp",EDGE,"E306"),sQuery(id+"F0.wireOp",EDGE,"E307"),sQuery(id+"F0.wireOp",EDGE,"E308"),sQuery(id+"F0.wireOp",EDGE,"E309"),sQuery(id+"F0.wireOp",EDGE,"E310"),sQuery(id+"F0.wireOp",EDGE,"E311"),sQuery(id+"F0.wireOp",EDGE,"E312"),sQuery(id+"F0.wireOp",EDGE,"E313"),sQuery(id+"F0.wireOp",EDGE,"E314"),sQuery(id+"F0.wireOp",EDGE,"E315"),sQuery(id+"F0.wireOp",EDGE,"E316"),sQuery(id+"F0.wireOp",EDGE,"E317"),sQuery(id+"F0.wireOp",EDGE,"E318"),sQuery(id+"F0.wireOp",EDGE,"E319"),sQuery(id+"F0.wireOp",EDGE,"E320"),sQuery(id+"F0.wireOp",EDGE,"E321"),sQuery(id+"F0.wireOp",EDGE,"E322"),sQuery(id+"F0.wireOp",EDGE,"E323"),sQuery(id+"F0.wireOp",EDGE,"E324"),sQuery(id+"F0.wireOp",EDGE,"E325"),sQuery(id+"F0.wireOp",EDGE,"E326"),sQuery(id+"F0.wireOp",EDGE,"E327"),sQuery(id+"F0.wireOp",EDGE,"E328"),sQuery(id+"F0.wireOp",EDGE,"E329"),sQuery(id+"F0.wireOp",EDGE,"E330"),sQuery(id+"F0.wireOp",EDGE,"E331"),sQuery(id+"F0.wireOp",EDGE,"E332"),sQuery(id+"F0.wireOp",EDGE,"E333"),sQuery(id+"F0.wireOp",EDGE,"E334"),sQuery(id+"F0.wireOp",EDGE,"E335"),sQuery(id+"F0.wireOp",EDGE,"E336"),sQuery(id+"F0.wireOp",EDGE,"E337"),sQuery(id+"F0.wireOp",EDGE,"E338"),sQuery(id+"F0.wireOp",EDGE,"E339"),sQuery(id+"F0.wireOp",EDGE,"E340"),sQuery(id+"F0.wireOp",EDGE,"E341"),sQuery(id+"F0.wireOp",EDGE,"E342"),sQuery(id+"F0.wireOp",EDGE,"E343"),sQuery(id+"F0.wireOp",EDGE,"E344"),sQuery(id+"F0.wireOp",EDGE,"E345"),sQuery(id+"F0.wireOp",EDGE,"E346"),sQuery(id+"F0.wireOp",EDGE,"E347"),sQuery(id+"F0.wireOp",EDGE,"E348"),sQuery(id+"F0.wireOp",EDGE,"E349"),sQuery(id+"F0.wireOp",EDGE,"E350"),sQuery(id+"F0.wireOp",EDGE,"E351"),sQuery(id+"F0.wireOp",EDGE,"E352"),sQuery(id+"F0.wireOp",EDGE,"E353"),sQuery(id+"F0.wireOp",EDGE,"E354"),sQuery(id+"F0.wireOp",EDGE,"E355"),sQuery(id+"F0.wireOp",EDGE,"E356"),sQuery(id+"F0.wireOp",EDGE,"E357"),sQuery(id+"F0.wireOp",EDGE,"E358"),sQuery(id+"F0.wireOp",EDGE,"E359"),sQuery(id+"F0.wireOp",EDGE,"E360"),sQuery(id+"F0.wireOp",EDGE,"E361"),sQuery(id+"F0.wireOp",EDGE,"E362"),sQuery(id+"F0.wireOp",EDGE,"E363"),sQuery(id+"F0.wireOp",EDGE,"E364"),sQuery(id+"F0.wireOp",EDGE,"E365"),sQuery(id+"F0.wireOp",EDGE,"E366"),sQuery(id+"F0.wireOp",EDGE,"E367"),sQuery(id+"F0.wireOp",EDGE,"E368"),sQuery(id+"F0.wireOp",EDGE,"E369"),sQuery(id+"F0.wireOp",EDGE,"E370"),sQuery(id+"F0.wireOp",EDGE,"E371"),sQuery(id+"F0.wireOp",EDGE,"E372"),sQuery(id+"F0.wireOp",EDGE,"E373"),sQuery(id+"F0.wireOp",EDGE,"E374"),sQuery(id+"F0.wireOp",EDGE,"E375"),sQuery(id+"F0.wireOp",EDGE,"E376"),sQuery(id+"F0.wireOp",EDGE,"E377"),sQuery(id+"F0.wireOp",EDGE,"E378"),sQuery(id+"F0.wireOp",EDGE,"E379"),sQuery(id+"F0.wireOp",EDGE,"E380"),sQuery(id+"F0.wireOp",EDGE,"E381"),sQuery(id+"F0.wireOp",EDGE,"E382"),sQuery(id+"F0.wireOp",EDGE,"E383"),sQuery(id+"F0.wireOp",EDGE,"E384"),sQuery(id+"F0.wireOp",EDGE,"E385"),sQuery(id+"F0.wireOp",EDGE,"E386"),sQuery(id+"F0.wireOp",EDGE,"E387"),sQuery(id+"F0.wireOp",EDGE,"E388"),sQuery(id+"F0.wireOp",EDGE,"E389"),sQuery(id+"F0.wireOp",EDGE,"E390"),sQuery(id+"F0.wireOp",EDGE,"E391"),sQuery(id+"F0.wireOp",EDGE,"E392"),sQuery(id+"F0.wireOp",EDGE,"E393"),sQuery(id+"F0.wireOp",EDGE,"E394"),sQuery(id+"F0.wireOp",EDGE,"E395"),sQuery(id+"F0.wireOp",EDGE,"E396"),sQuery(id+"F0.wireOp",EDGE,"E397"),sQuery(id+"F0.wireOp",EDGE,"E398"),sQuery(id+"F0.wireOp",EDGE,"E399"),sQuery(id+"F0.wireOp",EDGE,"E400"),sQuery(id+"F0.wireOp",EDGE,"E401"),sQuery(id+"F0.wireOp",EDGE,"E402"),sQuery(id+"F0.wireOp",EDGE,"E403"),sQuery(id+"F0.wireOp",EDGE,"E404"),sQuery(id+"F0.wireOp",EDGE,"E405"),sQuery(id+"F0.wireOp",EDGE,"E406"),sQuery(id+"F0.wireOp",EDGE,"E407"),sQuery(id+"F0.wireOp",EDGE,"E408"),sQuery(id+"F0.wireOp",EDGE,"E409"),sQuery(id+"F0.wireOp",EDGE,"E410"),sQuery(id+"F0.wireOp",EDGE,"E411"),sQuery(id+"F0.wireOp",EDGE,"E412"),sQuery(id+"F0.wireOp",EDGE,"E413"),sQuery(id+"F0.wireOp",EDGE,"E414"),sQuery(id+"F0.wireOp",EDGE,"E415"),sQuery(id+"F0.wireOp",EDGE,"E416"),sQuery(id+"F0.wireOp",EDGE,"E417"),sQuery(id+"F0.wireOp",EDGE,"E418"),sQuery(id+"F0.wireOp",EDGE,"E419"),sQuery(id+"F0.wireOp",EDGE,"E420"),sQuery(id+"F0.wireOp",EDGE,"E421"),sQuery(id+"F0.wireOp",EDGE,"E422"),sQuery(id+"F0.wireOp",EDGE,"E423"),sQuery(id+"F0.wireOp",EDGE,"E424"),sQuery(id+"F0.wireOp",EDGE,"E425"),sQuery(id+"F0.wireOp",EDGE,"E426"),sQuery(id+"F0.wireOp",EDGE,"E427"),sQuery(id+"F0.wireOp",EDGE,"E428"),sQuery(id+"F0.wireOp",EDGE,"E429"),sQuery(id+"F0.wireOp",EDGE,"E430"),sQuery(id+"F0.wireOp",EDGE,"E431"),sQuery(id+"F0.wireOp",EDGE,"E432"),sQuery(id+"F0.wireOp",EDGE,"E433"),sQuery(id+"F0.wireOp",EDGE,"E434"),sQuery(id+"F0.wireOp",EDGE,"E435"),sQuery(id+"F0.wireOp",EDGE,"E436"),sQuery(id+"F0.wireOp",EDGE,"E437"),sQuery(id+"F0.wireOp",EDGE,"E438"),sQuery(id+"F0.wireOp",EDGE,"E439"),sQuery(id+"F0.wireOp",EDGE,"E440"),sQuery(id+"F0.wireOp",EDGE,"E441"),sQuery(id+"F0.wireOp",EDGE,"E442"),sQuery(id+"F0.wireOp",EDGE,"E443"),sQuery(id+"F0.wireOp",EDGE,"E444"),sQuery(id+"F0.wireOp",EDGE,"E445"),sQuery(id+"F0.wireOp",EDGE,"E446"),sQuery(id+"F0.wireOp",EDGE,"E447"),sQuery(id+"F0.wireOp",EDGE,"E448"),sQuery(id+"F0.wireOp",EDGE,"E449"),sQuery(id+"F0.wireOp",EDGE,"E450"),sQuery(id+"F0.wireOp",EDGE,"E451"),sQuery(id+"F0.wireOp",EDGE,"E452"),sQuery(id+"F0.wireOp",EDGE,"E453"),sQuery(id+"F0.wireOp",EDGE,"E454"),sQuery(id+"F0.wireOp",EDGE,"E455"),sQuery(id+"F0.wireOp",EDGE,"E456"),sQuery(id+"F0.wireOp",EDGE,"E457"),sQuery(id+"F0.wireOp",EDGE,"E458"),sQuery(id+"F0.wireOp",EDGE,"E459"),sQuery(id+"F0.wireOp",EDGE,"E460"),sQuery(id+"F0.wireOp",EDGE,"E461"),sQuery(id+"F0.wireOp",EDGE,"E462"),sQuery(id+"F0.wireOp",EDGE,"E463"),sQuery(id+"F0.wireOp",EDGE,"E464"),sQuery(id+"F0.wireOp",EDGE,"E465"),sQuery(id+"F0.wireOp",EDGE,"E466"),sQuery(id+"F0.wireOp",EDGE,"E467"),sQuery(id+"F0.wireOp",EDGE,"E468"),sQuery(id+"F0.wireOp",EDGE,"E469"),sQuery(id+"F0.wireOp",EDGE,"E470"),sQuery(id+"F0.wireOp",EDGE,"E471"),sQuery(id+"F0.wireOp",EDGE,"E472"),sQuery(id+"F0.wireOp",EDGE,"E473"),sQuery(id+"F0.wireOp",EDGE,"E474"),sQuery(id+"F0.wireOp",EDGE,"E475"),sQuery(id+"F0.wireOp",EDGE,"E476"),sQuery(id+"F0.wireOp",EDGE,"E477"),sQuery(id+"F0.wireOp",EDGE,"E478"),sQuery(id+"F0.wireOp",EDGE,"E479"),sQuery(id+"F0.wireOp",EDGE,"E480"),sQuery(id+"F0.wireOp",EDGE,"E481"),sQuery(id+"F0.wireOp",EDGE,"E482"),sQuery(id+"F0.wireOp",EDGE,"E483"),sQuery(id+"F0.wireOp",EDGE,"E484"),sQuery(id+"F0.wireOp",EDGE,"E485"),sQuery(id+"F0.wireOp",EDGE,"E486"),sQuery(id+"F0.wireOp",EDGE,"E487"),sQuery(id+"F0.wireOp",EDGE,"E488"),sQuery(id+"F0.wireOp",EDGE,"E489"),sQuery(id+"F0.wireOp",EDGE,"E490"),sQuery(id+"F0.wireOp",EDGE,"E491"),sQuery(id+"F0.wireOp",EDGE,"E492"),sQuery(id+"F0.wireOp",EDGE,"E493"),sQuery(id+"F0.wireOp",EDGE,"E494"),sQuery(id+"F0.wireOp",EDGE,"E495"),sQuery(id+"F0.wireOp",EDGE,"E496"),sQuery(id+"F0.wireOp",EDGE,"E497"),sQuery(id+"F0.wireOp",EDGE,"E498"),sQuery(id+"F0.wireOp",EDGE,"E499"),sQuery(id+"F0.wireOp",EDGE,"E500"),sQuery(id+"F0.wireOp",EDGE,"E501"),sQuery(id+"F0.wireOp",EDGE,"E502"),sQuery(id+"F0.wireOp",EDGE,"E503")])],"isStart":true});
            var sketch = newSketch(context, id + "F3", { "sketchPlane" : qUnion([Q0])});
            skText(sketch, "E6384", { "text": "Oz", "fontName": "RobotoSlab-Bold.ttf"});
            skText(sketch, "E6385", { "text": "Gonen", "fontName": "RobotoSlab-Bold.ttf"});
            skLineSegment(sketch, "E6386", {"start": v(-56.31, -71.07) * mm, "end": v(-92.25, -71.07) * mm, "construction": true});
            const initialGuessF3  = {"E6384": [-0.19643, -0.13107, 1, 0, 0.06], "E6385": [-0.05631, -0.13107, 1, 0, 0.06]};
            skSetInitialGuess(sketch, initialGuessF3);
            skSolve(sketch);
        }
        {
            var Q0;
            Q0 = qSketchRegion(id + "F3", true);
            extrude(context, id + "F4", {"entities" : qUnion([Q0]), "operationType" : NewBodyOperationType.ADD, "depth" : 4 * mm, "hasSecondDirection" : true, "secondDirectionOppositeDirection" : true, "secondDirectionDepth" : 2 * mm});
        }
        {
            var Q0;
            Q0=makeQuery(id+"F1.opExtrude","SWEPT_BODY",BODY,{"disambiguationData":[OSD([sQuery(id+"F0.wireOp",EDGE,"E0"),sQuery(id+"F0.wireOp",EDGE,"E1"),sQuery(id+"F0.wireOp",EDGE,"E2"),sQuery(id+"F0.wireOp",EDGE,"E3"),sQuery(id+"F0.wireOp",EDGE,"E4"),sQuery(id+"F0.wireOp",EDGE,"E5"),sQuery(id+"F0.wireOp",EDGE,"E6"),sQuery(id+"F0.wireOp",EDGE,"E7"),sQuery(id+"F0.wireOp",EDGE,"E8"),sQuery(id+"F0.wireOp",EDGE,"E9"),sQuery(id+"F0.wireOp",EDGE,"E10"),sQuery(id+"F0.wireOp",EDGE,"E11"),sQuery(id+"F0.wireOp",EDGE,"E12"),sQuery(id+"F0.wireOp",EDGE,"E13"),sQuery(id+"F0.wireOp",EDGE,"E14"),sQuery(id+"F0.wireOp",EDGE,"E15"),sQuery(id+"F0.wireOp",EDGE,"E16"),sQuery(id+"F0.wireOp",EDGE,"E17"),sQuery(id+"F0.wireOp",EDGE,"E18"),sQuery(id+"F0.wireOp",EDGE,"E19"),sQuery(id+"F0.wireOp",EDGE,"E20"),sQuery(id+"F0.wireOp",EDGE,"E21"),sQuery(id+"F0.wireOp",EDGE,"E22"),sQuery(id+"F0.wireOp",EDGE,"E23"),sQuery(id+"F0.wireOp",EDGE,"E24"),sQuery(id+"F0.wireOp",EDGE,"E25"),sQuery(id+"F0.wireOp",EDGE,"E26"),sQuery(id+"F0.wireOp",EDGE,"E27"),sQuery(id+"F0.wireOp",EDGE,"E28"),sQuery(id+"F0.wireOp",EDGE,"E29"),sQuery(id+"F0.wireOp",EDGE,"E30"),sQuery(id+"F0.wireOp",EDGE,"E31"),sQuery(id+"F0.wireOp",EDGE,"E32"),sQuery(id+"F0.wireOp",EDGE,"E33"),sQuery(id+"F0.wireOp",EDGE,"E34"),sQuery(id+"F0.wireOp",EDGE,"E35"),sQuery(id+"F0.wireOp",EDGE,"E36"),sQuery(id+"F0.wireOp",EDGE,"E37"),sQuery(id+"F0.wireOp",EDGE,"E38"),sQuery(id+"F0.wireOp",EDGE,"E39"),sQuery(id+"F0.wireOp",EDGE,"E40"),sQuery(id+"F0.wireOp",EDGE,"E41"),sQuery(id+"F0.wireOp",EDGE,"E42"),sQuery(id+"F0.wireOp",EDGE,"E43"),sQuery(id+"F0.wireOp",EDGE,"E44"),sQuery(id+"F0.wireOp",EDGE,"E45"),sQuery(id+"F0.wireOp",EDGE,"E46"),sQuery(id+"F0.wireOp",EDGE,"E47"),sQuery(id+"F0.wireOp",EDGE,"E48"),sQuery(id+"F0.wireOp",EDGE,"E49"),sQuery(id+"F0.wireOp",EDGE,"E50"),sQuery(id+"F0.wireOp",EDGE,"E51"),sQuery(id+"F0.wireOp",EDGE,"E52"),sQuery(id+"F0.wireOp",EDGE,"E53"),sQuery(id+"F0.wireOp",EDGE,"E54"),sQuery(id+"F0.wireOp",EDGE,"E55"),sQuery(id+"F0.wireOp",EDGE,"E56"),sQuery(id+"F0.wireOp",EDGE,"E57"),sQuery(id+"F0.wireOp",EDGE,"E58"),sQuery(id+"F0.wireOp",EDGE,"E59"),sQuery(id+"F0.wireOp",EDGE,"E60"),sQuery(id+"F0.wireOp",EDGE,"E61"),sQuery(id+"F0.wireOp",EDGE,"E62"),sQuery(id+"F0.wireOp",EDGE,"E63"),sQuery(id+"F0.wireOp",EDGE,"E64"),sQuery(id+"F0.wireOp",EDGE,"E65"),sQuery(id+"F0.wireOp",EDGE,"E66"),sQuery(id+"F0.wireOp",EDGE,"E67"),sQuery(id+"F0.wireOp",EDGE,"E68"),sQuery(id+"F0.wireOp",EDGE,"E69"),sQuery(id+"F0.wireOp",EDGE,"E70"),sQuery(id+"F0.wireOp",EDGE,"E71"),sQuery(id+"F0.wireOp",EDGE,"E72"),sQuery(id+"F0.wireOp",EDGE,"E73"),sQuery(id+"F0.wireOp",EDGE,"E74"),sQuery(id+"F0.wireOp",EDGE,"E75"),sQuery(id+"F0.wireOp",EDGE,"E76"),sQuery(id+"F0.wireOp",EDGE,"E77"),sQuery(id+"F0.wireOp",EDGE,"E78"),sQuery(id+"F0.wireOp",EDGE,"E79"),sQuery(id+"F0.wireOp",EDGE,"E80"),sQuery(id+"F0.wireOp",EDGE,"E81"),sQuery(id+"F0.wireOp",EDGE,"E82"),sQuery(id+"F0.wireOp",EDGE,"E83"),sQuery(id+"F0.wireOp",EDGE,"E84"),sQuery(id+"F0.wireOp",EDGE,"E85"),sQuery(id+"F0.wireOp",EDGE,"E86"),sQuery(id+"F0.wireOp",EDGE,"E87"),sQuery(id+"F0.wireOp",EDGE,"E88"),sQuery(id+"F0.wireOp",EDGE,"E89"),sQuery(id+"F0.wireOp",EDGE,"E90"),sQuery(id+"F0.wireOp",EDGE,"E91"),sQuery(id+"F0.wireOp",EDGE,"E92"),sQuery(id+"F0.wireOp",EDGE,"E93"),sQuery(id+"F0.wireOp",EDGE,"E94"),sQuery(id+"F0.wireOp",EDGE,"E95"),sQuery(id+"F0.wireOp",EDGE,"E96"),sQuery(id+"F0.wireOp",EDGE,"E97"),sQuery(id+"F0.wireOp",EDGE,"E98"),sQuery(id+"F0.wireOp",EDGE,"E99"),sQuery(id+"F0.wireOp",EDGE,"E100"),sQuery(id+"F0.wireOp",EDGE,"E101"),sQuery(id+"F0.wireOp",EDGE,"E102"),sQuery(id+"F0.wireOp",EDGE,"E103"),sQuery(id+"F0.wireOp",EDGE,"E104"),sQuery(id+"F0.wireOp",EDGE,"E105"),sQuery(id+"F0.wireOp",EDGE,"E106"),sQuery(id+"F0.wireOp",EDGE,"E107"),sQuery(id+"F0.wireOp",EDGE,"E108"),sQuery(id+"F0.wireOp",EDGE,"E109"),sQuery(id+"F0.wireOp",EDGE,"E110"),sQuery(id+"F0.wireOp",EDGE,"E111"),sQuery(id+"F0.wireOp",EDGE,"E112"),sQuery(id+"F0.wireOp",EDGE,"E113"),sQuery(id+"F0.wireOp",EDGE,"E114"),sQuery(id+"F0.wireOp",EDGE,"E115"),sQuery(id+"F0.wireOp",EDGE,"E116"),sQuery(id+"F0.wireOp",EDGE,"E117"),sQuery(id+"F0.wireOp",EDGE,"E118"),sQuery(id+"F0.wireOp",EDGE,"E119"),sQuery(id+"F0.wireOp",EDGE,"E120"),sQuery(id+"F0.wireOp",EDGE,"E121"),sQuery(id+"F0.wireOp",EDGE,"E122"),sQuery(id+"F0.wireOp",EDGE,"E123"),sQuery(id+"F0.wireOp",EDGE,"E124"),sQuery(id+"F0.wireOp",EDGE,"E125"),sQuery(id+"F0.wireOp",EDGE,"E126"),sQuery(id+"F0.wireOp",EDGE,"E127"),sQuery(id+"F0.wireOp",EDGE,"E128"),sQuery(id+"F0.wireOp",EDGE,"E129"),sQuery(id+"F0.wireOp",EDGE,"E130"),sQuery(id+"F0.wireOp",EDGE,"E131"),sQuery(id+"F0.wireOp",EDGE,"E132"),sQuery(id+"F0.wireOp",EDGE,"E133"),sQuery(id+"F0.wireOp",EDGE,"E134"),sQuery(id+"F0.wireOp",EDGE,"E135"),sQuery(id+"F0.wireOp",EDGE,"E136"),sQuery(id+"F0.wireOp",EDGE,"E137"),sQuery(id+"F0.wireOp",EDGE,"E138"),sQuery(id+"F0.wireOp",EDGE,"E139"),sQuery(id+"F0.wireOp",EDGE,"E140"),sQuery(id+"F0.wireOp",EDGE,"E141"),sQuery(id+"F0.wireOp",EDGE,"E142"),sQuery(id+"F0.wireOp",EDGE,"E143"),sQuery(id+"F0.wireOp",EDGE,"E144"),sQuery(id+"F0.wireOp",EDGE,"E145"),sQuery(id+"F0.wireOp",EDGE,"E146"),sQuery(id+"F0.wireOp",EDGE,"E147"),sQuery(id+"F0.wireOp",EDGE,"E148"),sQuery(id+"F0.wireOp",EDGE,"E149"),sQuery(id+"F0.wireOp",EDGE,"E150"),sQuery(id+"F0.wireOp",EDGE,"E151"),sQuery(id+"F0.wireOp",EDGE,"E152"),sQuery(id+"F0.wireOp",EDGE,"E153"),sQuery(id+"F0.wireOp",EDGE,"E154"),sQuery(id+"F0.wireOp",EDGE,"E155"),sQuery(id+"F0.wireOp",EDGE,"E156"),sQuery(id+"F0.wireOp",EDGE,"E157"),sQuery(id+"F0.wireOp",EDGE,"E158"),sQuery(id+"F0.wireOp",EDGE,"E159"),sQuery(id+"F0.wireOp",EDGE,"E160"),sQuery(id+"F0.wireOp",EDGE,"E161"),sQuery(id+"F0.wireOp",EDGE,"E162"),sQuery(id+"F0.wireOp",EDGE,"E163"),sQuery(id+"F0.wireOp",EDGE,"E164"),sQuery(id+"F0.wireOp",EDGE,"E165"),sQuery(id+"F0.wireOp",EDGE,"E166"),sQuery(id+"F0.wireOp",EDGE,"E167"),sQuery(id+"F0.wireOp",EDGE,"E168"),sQuery(id+"F0.wireOp",EDGE,"E169"),sQuery(id+"F0.wireOp",EDGE,"E170"),sQuery(id+"F0.wireOp",EDGE,"E171"),sQuery(id+"F0.wireOp",EDGE,"E172"),sQuery(id+"F0.wireOp",EDGE,"E173"),sQuery(id+"F0.wireOp",EDGE,"E174"),sQuery(id+"F0.wireOp",EDGE,"E175"),sQuery(id+"F0.wireOp",EDGE,"E176"),sQuery(id+"F0.wireOp",EDGE,"E177"),sQuery(id+"F0.wireOp",EDGE,"E178"),sQuery(id+"F0.wireOp",EDGE,"E179"),sQuery(id+"F0.wireOp",EDGE,"E180"),sQuery(id+"F0.wireOp",EDGE,"E181"),sQuery(id+"F0.wireOp",EDGE,"E182"),sQuery(id+"F0.wireOp",EDGE,"E183"),sQuery(id+"F0.wireOp",EDGE,"E184"),sQuery(id+"F0.wireOp",EDGE,"E185"),sQuery(id+"F0.wireOp",EDGE,"E186"),sQuery(id+"F0.wireOp",EDGE,"E187"),sQuery(id+"F0.wireOp",EDGE,"E188"),sQuery(id+"F0.wireOp",EDGE,"E189"),sQuery(id+"F0.wireOp",EDGE,"E190"),sQuery(id+"F0.wireOp",EDGE,"E191"),sQuery(id+"F0.wireOp",EDGE,"E192"),sQuery(id+"F0.wireOp",EDGE,"E193"),sQuery(id+"F0.wireOp",EDGE,"E194"),sQuery(id+"F0.wireOp",EDGE,"E195"),sQuery(id+"F0.wireOp",EDGE,"E196"),sQuery(id+"F0.wireOp",EDGE,"E197"),sQuery(id+"F0.wireOp",EDGE,"E198"),sQuery(id+"F0.wireOp",EDGE,"E199"),sQuery(id+"F0.wireOp",EDGE,"E200"),sQuery(id+"F0.wireOp",EDGE,"E201"),sQuery(id+"F0.wireOp",EDGE,"E202"),sQuery(id+"F0.wireOp",EDGE,"E203"),sQuery(id+"F0.wireOp",EDGE,"E204"),sQuery(id+"F0.wireOp",EDGE,"E205"),sQuery(id+"F0.wireOp",EDGE,"E206"),sQuery(id+"F0.wireOp",EDGE,"E207"),sQuery(id+"F0.wireOp",EDGE,"E208"),sQuery(id+"F0.wireOp",EDGE,"E209"),sQuery(id+"F0.wireOp",EDGE,"E210"),sQuery(id+"F0.wireOp",EDGE,"E211"),sQuery(id+"F0.wireOp",EDGE,"E212"),sQuery(id+"F0.wireOp",EDGE,"E213"),sQuery(id+"F0.wireOp",EDGE,"E214"),sQuery(id+"F0.wireOp",EDGE,"E215"),sQuery(id+"F0.wireOp",EDGE,"E216"),sQuery(id+"F0.wireOp",EDGE,"E217"),sQuery(id+"F0.wireOp",EDGE,"E218"),sQuery(id+"F0.wireOp",EDGE,"E219"),sQuery(id+"F0.wireOp",EDGE,"E220"),sQuery(id+"F0.wireOp",EDGE,"E221"),sQuery(id+"F0.wireOp",EDGE,"E222"),sQuery(id+"F0.wireOp",EDGE,"E223"),sQuery(id+"F0.wireOp",EDGE,"E224"),sQuery(id+"F0.wireOp",EDGE,"E225"),sQuery(id+"F0.wireOp",EDGE,"E226"),sQuery(id+"F0.wireOp",EDGE,"E227"),sQuery(id+"F0.wireOp",EDGE,"E228"),sQuery(id+"F0.wireOp",EDGE,"E229"),sQuery(id+"F0.wireOp",EDGE,"E230"),sQuery(id+"F0.wireOp",EDGE,"E231"),sQuery(id+"F0.wireOp",EDGE,"E232"),sQuery(id+"F0.wireOp",EDGE,"E233"),sQuery(id+"F0.wireOp",EDGE,"E234"),sQuery(id+"F0.wireOp",EDGE,"E235"),sQuery(id+"F0.wireOp",EDGE,"E236"),sQuery(id+"F0.wireOp",EDGE,"E237"),sQuery(id+"F0.wireOp",EDGE,"E238"),sQuery(id+"F0.wireOp",EDGE,"E239"),sQuery(id+"F0.wireOp",EDGE,"E240"),sQuery(id+"F0.wireOp",EDGE,"E241"),sQuery(id+"F0.wireOp",EDGE,"E242"),sQuery(id+"F0.wireOp",EDGE,"E243"),sQuery(id+"F0.wireOp",EDGE,"E244"),sQuery(id+"F0.wireOp",EDGE,"E245"),sQuery(id+"F0.wireOp",EDGE,"E246"),sQuery(id+"F0.wireOp",EDGE,"E247"),sQuery(id+"F0.wireOp",EDGE,"E248"),sQuery(id+"F0.wireOp",EDGE,"E249"),sQuery(id+"F0.wireOp",EDGE,"E250"),sQuery(id+"F0.wireOp",EDGE,"E251"),sQuery(id+"F0.wireOp",EDGE,"E252"),sQuery(id+"F0.wireOp",EDGE,"E253"),sQuery(id+"F0.wireOp",EDGE,"E254"),sQuery(id+"F0.wireOp",EDGE,"E255"),sQuery(id+"F0.wireOp",EDGE,"E256"),sQuery(id+"F0.wireOp",EDGE,"E257"),sQuery(id+"F0.wireOp",EDGE,"E258"),sQuery(id+"F0.wireOp",EDGE,"E259"),sQuery(id+"F0.wireOp",EDGE,"E260"),sQuery(id+"F0.wireOp",EDGE,"E261"),sQuery(id+"F0.wireOp",EDGE,"E262"),sQuery(id+"F0.wireOp",EDGE,"E263"),sQuery(id+"F0.wireOp",EDGE,"E264"),sQuery(id+"F0.wireOp",EDGE,"E265"),sQuery(id+"F0.wireOp",EDGE,"E266"),sQuery(id+"F0.wireOp",EDGE,"E267"),sQuery(id+"F0.wireOp",EDGE,"E268"),sQuery(id+"F0.wireOp",EDGE,"E269"),sQuery(id+"F0.wireOp",EDGE,"E270"),sQuery(id+"F0.wireOp",EDGE,"E271"),sQuery(id+"F0.wireOp",EDGE,"E272"),sQuery(id+"F0.wireOp",EDGE,"E273"),sQuery(id+"F0.wireOp",EDGE,"E274"),sQuery(id+"F0.wireOp",EDGE,"E275"),sQuery(id+"F0.wireOp",EDGE,"E276"),sQuery(id+"F0.wireOp",EDGE,"E277"),sQuery(id+"F0.wireOp",EDGE,"E278"),sQuery(id+"F0.wireOp",EDGE,"E279"),sQuery(id+"F0.wireOp",EDGE,"E280"),sQuery(id+"F0.wireOp",EDGE,"E281"),sQuery(id+"F0.wireOp",EDGE,"E282"),sQuery(id+"F0.wireOp",EDGE,"E283"),sQuery(id+"F0.wireOp",EDGE,"E284"),sQuery(id+"F0.wireOp",EDGE,"E285"),sQuery(id+"F0.wireOp",EDGE,"E286"),sQuery(id+"F0.wireOp",EDGE,"E287"),sQuery(id+"F0.wireOp",EDGE,"E288"),sQuery(id+"F0.wireOp",EDGE,"E289"),sQuery(id+"F0.wireOp",EDGE,"E290"),sQuery(id+"F0.wireOp",EDGE,"E291"),sQuery(id+"F0.wireOp",EDGE,"E292"),sQuery(id+"F0.wireOp",EDGE,"E293"),sQuery(id+"F0.wireOp",EDGE,"E294"),sQuery(id+"F0.wireOp",EDGE,"E295"),sQuery(id+"F0.wireOp",EDGE,"E296"),sQuery(id+"F0.wireOp",EDGE,"E297"),sQuery(id+"F0.wireOp",EDGE,"E298"),sQuery(id+"F0.wireOp",EDGE,"E299"),sQuery(id+"F0.wireOp",EDGE,"E300"),sQuery(id+"F0.wireOp",EDGE,"E301"),sQuery(id+"F0.wireOp",EDGE,"E302"),sQuery(id+"F0.wireOp",EDGE,"E303"),sQuery(id+"F0.wireOp",EDGE,"E304"),sQuery(id+"F0.wireOp",EDGE,"E305"),sQuery(id+"F0.wireOp",EDGE,"E306"),sQuery(id+"F0.wireOp",EDGE,"E307"),sQuery(id+"F0.wireOp",EDGE,"E308"),sQuery(id+"F0.wireOp",EDGE,"E309"),sQuery(id+"F0.wireOp",EDGE,"E310"),sQuery(id+"F0.wireOp",EDGE,"E311"),sQuery(id+"F0.wireOp",EDGE,"E312"),sQuery(id+"F0.wireOp",EDGE,"E313"),sQuery(id+"F0.wireOp",EDGE,"E314"),sQuery(id+"F0.wireOp",EDGE,"E315"),sQuery(id+"F0.wireOp",EDGE,"E316"),sQuery(id+"F0.wireOp",EDGE,"E317"),sQuery(id+"F0.wireOp",EDGE,"E318"),sQuery(id+"F0.wireOp",EDGE,"E319"),sQuery(id+"F0.wireOp",EDGE,"E320"),sQuery(id+"F0.wireOp",EDGE,"E321"),sQuery(id+"F0.wireOp",EDGE,"E322"),sQuery(id+"F0.wireOp",EDGE,"E323"),sQuery(id+"F0.wireOp",EDGE,"E324"),sQuery(id+"F0.wireOp",EDGE,"E325"),sQuery(id+"F0.wireOp",EDGE,"E326"),sQuery(id+"F0.wireOp",EDGE,"E327"),sQuery(id+"F0.wireOp",EDGE,"E328"),sQuery(id+"F0.wireOp",EDGE,"E329"),sQuery(id+"F0.wireOp",EDGE,"E330"),sQuery(id+"F0.wireOp",EDGE,"E331"),sQuery(id+"F0.wireOp",EDGE,"E332"),sQuery(id+"F0.wireOp",EDGE,"E333"),sQuery(id+"F0.wireOp",EDGE,"E334"),sQuery(id+"F0.wireOp",EDGE,"E335"),sQuery(id+"F0.wireOp",EDGE,"E336"),sQuery(id+"F0.wireOp",EDGE,"E337"),sQuery(id+"F0.wireOp",EDGE,"E338"),sQuery(id+"F0.wireOp",EDGE,"E339"),sQuery(id+"F0.wireOp",EDGE,"E340"),sQuery(id+"F0.wireOp",EDGE,"E341"),sQuery(id+"F0.wireOp",EDGE,"E342"),sQuery(id+"F0.wireOp",EDGE,"E343"),sQuery(id+"F0.wireOp",EDGE,"E344"),sQuery(id+"F0.wireOp",EDGE,"E345"),sQuery(id+"F0.wireOp",EDGE,"E346"),sQuery(id+"F0.wireOp",EDGE,"E347"),sQuery(id+"F0.wireOp",EDGE,"E348"),sQuery(id+"F0.wireOp",EDGE,"E349"),sQuery(id+"F0.wireOp",EDGE,"E350"),sQuery(id+"F0.wireOp",EDGE,"E351"),sQuery(id+"F0.wireOp",EDGE,"E352"),sQuery(id+"F0.wireOp",EDGE,"E353"),sQuery(id+"F0.wireOp",EDGE,"E354"),sQuery(id+"F0.wireOp",EDGE,"E355"),sQuery(id+"F0.wireOp",EDGE,"E356"),sQuery(id+"F0.wireOp",EDGE,"E357"),sQuery(id+"F0.wireOp",EDGE,"E358"),sQuery(id+"F0.wireOp",EDGE,"E359"),sQuery(id+"F0.wireOp",EDGE,"E360"),sQuery(id+"F0.wireOp",EDGE,"E361"),sQuery(id+"F0.wireOp",EDGE,"E362"),sQuery(id+"F0.wireOp",EDGE,"E363"),sQuery(id+"F0.wireOp",EDGE,"E364"),sQuery(id+"F0.wireOp",EDGE,"E365"),sQuery(id+"F0.wireOp",EDGE,"E366"),sQuery(id+"F0.wireOp",EDGE,"E367"),sQuery(id+"F0.wireOp",EDGE,"E368"),sQuery(id+"F0.wireOp",EDGE,"E369"),sQuery(id+"F0.wireOp",EDGE,"E370"),sQuery(id+"F0.wireOp",EDGE,"E371"),sQuery(id+"F0.wireOp",EDGE,"E372"),sQuery(id+"F0.wireOp",EDGE,"E373"),sQuery(id+"F0.wireOp",EDGE,"E374"),sQuery(id+"F0.wireOp",EDGE,"E375"),sQuery(id+"F0.wireOp",EDGE,"E376"),sQuery(id+"F0.wireOp",EDGE,"E377"),sQuery(id+"F0.wireOp",EDGE,"E378"),sQuery(id+"F0.wireOp",EDGE,"E379"),sQuery(id+"F0.wireOp",EDGE,"E380"),sQuery(id+"F0.wireOp",EDGE,"E381"),sQuery(id+"F0.wireOp",EDGE,"E382"),sQuery(id+"F0.wireOp",EDGE,"E383"),sQuery(id+"F0.wireOp",EDGE,"E384"),sQuery(id+"F0.wireOp",EDGE,"E385"),sQuery(id+"F0.wireOp",EDGE,"E386"),sQuery(id+"F0.wireOp",EDGE,"E387"),sQuery(id+"F0.wireOp",EDGE,"E388"),sQuery(id+"F0.wireOp",EDGE,"E389"),sQuery(id+"F0.wireOp",EDGE,"E390"),sQuery(id+"F0.wireOp",EDGE,"E391"),sQuery(id+"F0.wireOp",EDGE,"E392"),sQuery(id+"F0.wireOp",EDGE,"E393"),sQuery(id+"F0.wireOp",EDGE,"E394"),sQuery(id+"F0.wireOp",EDGE,"E395"),sQuery(id+"F0.wireOp",EDGE,"E396"),sQuery(id+"F0.wireOp",EDGE,"E397"),sQuery(id+"F0.wireOp",EDGE,"E398"),sQuery(id+"F0.wireOp",EDGE,"E399"),sQuery(id+"F0.wireOp",EDGE,"E400"),sQuery(id+"F0.wireOp",EDGE,"E401"),sQuery(id+"F0.wireOp",EDGE,"E402"),sQuery(id+"F0.wireOp",EDGE,"E403"),sQuery(id+"F0.wireOp",EDGE,"E404"),sQuery(id+"F0.wireOp",EDGE,"E405"),sQuery(id+"F0.wireOp",EDGE,"E406"),sQuery(id+"F0.wireOp",EDGE,"E407"),sQuery(id+"F0.wireOp",EDGE,"E408"),sQuery(id+"F0.wireOp",EDGE,"E409"),sQuery(id+"F0.wireOp",EDGE,"E410"),sQuery(id+"F0.wireOp",EDGE,"E411"),sQuery(id+"F0.wireOp",EDGE,"E412"),sQuery(id+"F0.wireOp",EDGE,"E413"),sQuery(id+"F0.wireOp",EDGE,"E414"),sQuery(id+"F0.wireOp",EDGE,"E415"),sQuery(id+"F0.wireOp",EDGE,"E416"),sQuery(id+"F0.wireOp",EDGE,"E417"),sQuery(id+"F0.wireOp",EDGE,"E418"),sQuery(id+"F0.wireOp",EDGE,"E419"),sQuery(id+"F0.wireOp",EDGE,"E420"),sQuery(id+"F0.wireOp",EDGE,"E421"),sQuery(id+"F0.wireOp",EDGE,"E422"),sQuery(id+"F0.wireOp",EDGE,"E423"),sQuery(id+"F0.wireOp",EDGE,"E424"),sQuery(id+"F0.wireOp",EDGE,"E425"),sQuery(id+"F0.wireOp",EDGE,"E426"),sQuery(id+"F0.wireOp",EDGE,"E427"),sQuery(id+"F0.wireOp",EDGE,"E428"),sQuery(id+"F0.wireOp",EDGE,"E429"),sQuery(id+"F0.wireOp",EDGE,"E430"),sQuery(id+"F0.wireOp",EDGE,"E431"),sQuery(id+"F0.wireOp",EDGE,"E432"),sQuery(id+"F0.wireOp",EDGE,"E433"),sQuery(id+"F0.wireOp",EDGE,"E434"),sQuery(id+"F0.wireOp",EDGE,"E435"),sQuery(id+"F0.wireOp",EDGE,"E436"),sQuery(id+"F0.wireOp",EDGE,"E437"),sQuery(id+"F0.wireOp",EDGE,"E438"),sQuery(id+"F0.wireOp",EDGE,"E439"),sQuery(id+"F0.wireOp",EDGE,"E440"),sQuery(id+"F0.wireOp",EDGE,"E441"),sQuery(id+"F0.wireOp",EDGE,"E442"),sQuery(id+"F0.wireOp",EDGE,"E443"),sQuery(id+"F0.wireOp",EDGE,"E444"),sQuery(id+"F0.wireOp",EDGE,"E445"),sQuery(id+"F0.wireOp",EDGE,"E446"),sQuery(id+"F0.wireOp",EDGE,"E447"),sQuery(id+"F0.wireOp",EDGE,"E448"),sQuery(id+"F0.wireOp",EDGE,"E449"),sQuery(id+"F0.wireOp",EDGE,"E450"),sQuery(id+"F0.wireOp",EDGE,"E451"),sQuery(id+"F0.wireOp",EDGE,"E452"),sQuery(id+"F0.wireOp",EDGE,"E453"),sQuery(id+"F0.wireOp",EDGE,"E454"),sQuery(id+"F0.wireOp",EDGE,"E455"),sQuery(id+"F0.wireOp",EDGE,"E456"),sQuery(id+"F0.wireOp",EDGE,"E457"),sQuery(id+"F0.wireOp",EDGE,"E458"),sQuery(id+"F0.wireOp",EDGE,"E459"),sQuery(id+"F0.wireOp",EDGE,"E460"),sQuery(id+"F0.wireOp",EDGE,"E461"),sQuery(id+"F0.wireOp",EDGE,"E462"),sQuery(id+"F0.wireOp",EDGE,"E463"),sQuery(id+"F0.wireOp",EDGE,"E464"),sQuery(id+"F0.wireOp",EDGE,"E465"),sQuery(id+"F0.wireOp",EDGE,"E466"),sQuery(id+"F0.wireOp",EDGE,"E467"),sQuery(id+"F0.wireOp",EDGE,"E468"),sQuery(id+"F0.wireOp",EDGE,"E469"),sQuery(id+"F0.wireOp",EDGE,"E470"),sQuery(id+"F0.wireOp",EDGE,"E471"),sQuery(id+"F0.wireOp",EDGE,"E472"),sQuery(id+"F0.wireOp",EDGE,"E473"),sQuery(id+"F0.wireOp",EDGE,"E474"),sQuery(id+"F0.wireOp",EDGE,"E475"),sQuery(id+"F0.wireOp",EDGE,"E476"),sQuery(id+"F0.wireOp",EDGE,"E477"),sQuery(id+"F0.wireOp",EDGE,"E478"),sQuery(id+"F0.wireOp",EDGE,"E479"),sQuery(id+"F0.wireOp",EDGE,"E480"),sQuery(id+"F0.wireOp",EDGE,"E481"),sQuery(id+"F0.wireOp",EDGE,"E482"),sQuery(id+"F0.wireOp",EDGE,"E483"),sQuery(id+"F0.wireOp",EDGE,"E484"),sQuery(id+"F0.wireOp",EDGE,"E485"),sQuery(id+"F0.wireOp",EDGE,"E486"),sQuery(id+"F0.wireOp",EDGE,"E487"),sQuery(id+"F0.wireOp",EDGE,"E488"),sQuery(id+"F0.wireOp",EDGE,"E489"),sQuery(id+"F0.wireOp",EDGE,"E490"),sQuery(id+"F0.wireOp",EDGE,"E491"),sQuery(id+"F0.wireOp",EDGE,"E492"),sQuery(id+"F0.wireOp",EDGE,"E493"),sQuery(id+"F0.wireOp",EDGE,"E494"),sQuery(id+"F0.wireOp",EDGE,"E495"),sQuery(id+"F0.wireOp",EDGE,"E496"),sQuery(id+"F0.wireOp",EDGE,"E497"),sQuery(id+"F0.wireOp",EDGE,"E498"),sQuery(id+"F0.wireOp",EDGE,"E499"),sQuery(id+"F0.wireOp",EDGE,"E500"),sQuery(id+"F0.wireOp",EDGE,"E501"),sQuery(id+"F0.wireOp",EDGE,"E502"),sQuery(id+"F0.wireOp",EDGE,"E503")])]});
            var Q1;
            Q1=makeQuery(id+"F2.opExtrude","CAP_VERTEX",VERTEX,{"disambiguationData":[OSD([sQuery(id+"F0.wireOp",EDGE,"E3567"),sQuery(id+"F0.wireOp",EDGE,"E3568")])],"isStart":false});
            transform(context, id + "F5", {"entities" : qUnion([Q0]), "transformType" : TransformType.SCALE_UNIFORMLY, "scale" : 0.44, "scalePoint" : qUnion([Q1]), "makeCopy" : false});
        }
    });
